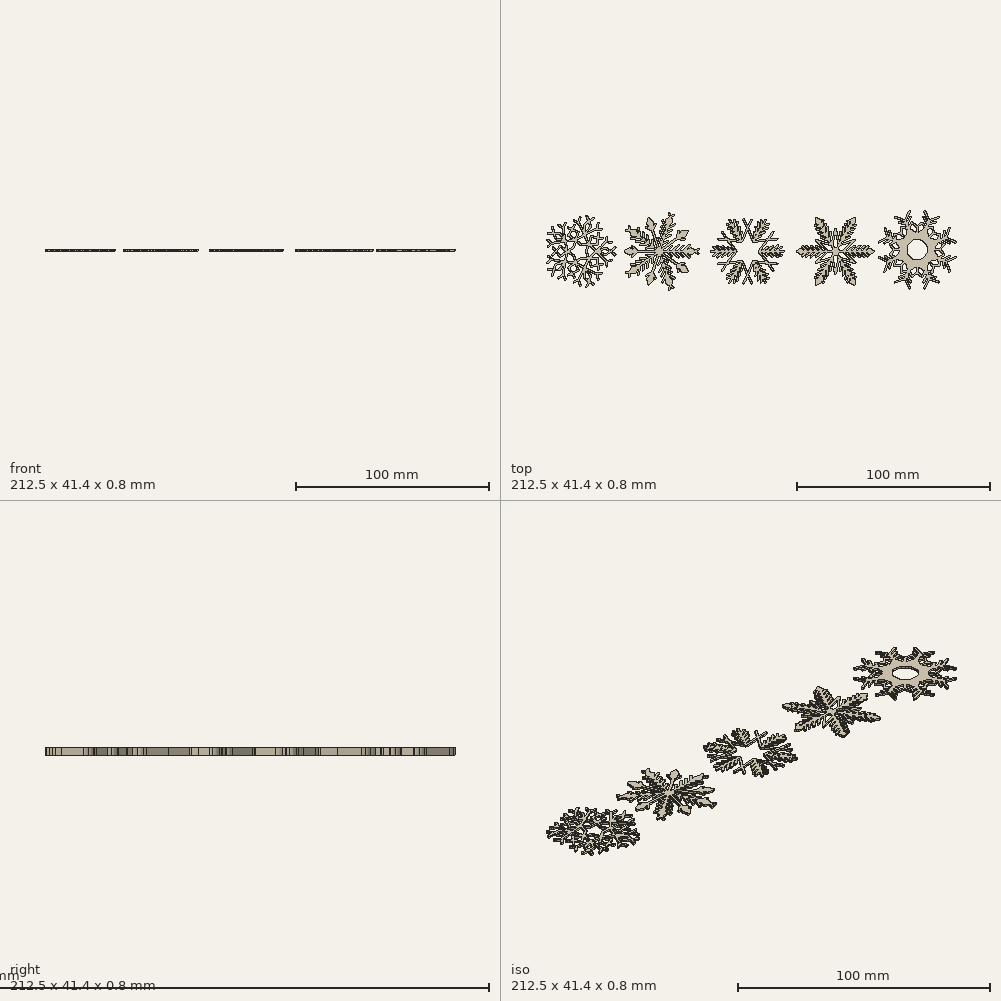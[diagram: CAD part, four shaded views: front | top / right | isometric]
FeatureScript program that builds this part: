
annotation { "Feature Type Name" : "Feature", "Feature Type Description" : "" }
export const myFeature = defineFeature(function(context is Context, id is Id, definition is map)
    precondition{}
    {
        {
            var Q0;
            Q0=qCreatedBy(makeId("Top.planeOp"),FACE);
            var sketch = newSketch(context, id + "F0", { "sketchPlane" : qUnion([Q0])});
            skFitSpline(sketch, "E0", {"points": [v(111.87, -6.39) * mm, v(111.5, -7.63) * mm, v(111.28, -8.86) * mm, v(111.02, -10.1) * mm]});
            skFitSpline(sketch, "E1", {"points": [v(111.02, -10.1) * mm, v(111.8, -10.32) * mm, v(112.58, -10.54) * mm, v(113.38, -10.77) * mm]});
            skFitSpline(sketch, "E2", {"points": [v(113.38, -10.77) * mm, v(113.4, -10.65) * mm, v(113.42, -10.54) * mm, v(113.43, -10.43) * mm]});
            skFitSpline(sketch, "E3", {"points": [v(113.43, -10.43) * mm, v(113.52, -9.82) * mm, v(113.59, -9.2) * mm, v(113.69, -8.59) * mm]});
            skFitSpline(sketch, "E4", {"points": [v(113.69, -8.59) * mm, v(113.72, -8.4) * mm, v(113.68, -8.28) * mm, v(113.58, -8.15) * mm]});
            skFitSpline(sketch, "E5", {"points": [v(113.58, -8.15) * mm, v(113.52, -8.08) * mm, v(113.46, -8.01) * mm, v(113.4, -7.95) * mm]});
            skFitSpline(sketch, "E6", {"points": [v(113.4, -7.95) * mm, v(113.06, -7.6) * mm, v(112.71, -7.24) * mm, v(112.37, -6.89) * mm]});
            skFitSpline(sketch, "E7", {"points": [v(112.37, -6.89) * mm, v(112.21, -6.73) * mm, v(112.05, -6.57) * mm, v(111.87, -6.39) * mm]});
            skFitSpline(sketch, "E8", {"points": [v(95.38, 5.54) * mm, v(96.61, 5.8) * mm, v(97.85, 6.01) * mm, v(99.08, 6.39) * mm]});
            skFitSpline(sketch, "E9", {"points": [v(99.08, 6.39) * mm, v(99.03, 6.44) * mm, v(99, 6.48) * mm, v(98.97, 6.51) * mm]});
            skFitSpline(sketch, "E10", {"points": [v(98.97, 6.51) * mm, v(98.46, 7.01) * mm, v(97.95, 7.52) * mm, v(97.43, 8.02) * mm]});
            skFitSpline(sketch, "E11", {"points": [v(97.43, 8.02) * mm, v(97.36, 8.08) * mm, v(97.28, 8.14) * mm, v(97.2, 8.18) * mm]});
            skFitSpline(sketch, "E12", {"points": [v(97.2, 8.18) * mm, v(97.13, 8.21) * mm, v(97.04, 8.22) * mm, v(96.97, 8.22) * mm]});
            skFitSpline(sketch, "E13", {"points": [v(96.97, 8.22) * mm, v(96.44, 8.15) * mm, v(95.92, 8.08) * mm, v(95.39, 8) * mm]});
            skFitSpline(sketch, "E14", {"points": [v(95.39, 8) * mm, v(95.16, 7.97) * mm, v(94.94, 7.93) * mm, v(94.7, 7.9) * mm]});
            skFitSpline(sketch, "E15", {"points": [v(94.7, 7.9) * mm, v(94.94, 7.1) * mm, v(95.16, 6.33) * mm, v(95.38, 5.54) * mm]});
            skFitSpline(sketch, "E16", {"points": [v(112.6, -5.66) * mm, v(112.68, -5.74) * mm, v(112.73, -5.8) * mm, v(112.79, -5.86) * mm]});
            skFitSpline(sketch, "E17", {"points": [v(112.79, -5.86) * mm, v(113.27, -6.32) * mm, v(113.75, -6.8) * mm, v(114.23, -7.26) * mm]});
            skFitSpline(sketch, "E18", {"points": [v(114.23, -7.26) * mm, v(114.27, -7.3) * mm, v(114.3, -7.34) * mm, v(114.35, -7.37) * mm]});
            skFitSpline(sketch, "E19", {"points": [v(114.35, -7.37) * mm, v(114.48, -7.47) * mm, v(114.63, -7.51) * mm, v(114.8, -7.49) * mm]});
            skFitSpline(sketch, "E20", {"points": [v(114.8, -7.49) * mm, v(115.46, -7.39) * mm, v(116.12, -7.3) * mm, v(116.78, -7.2) * mm]});
            skFitSpline(sketch, "E21", {"points": [v(116.78, -7.2) * mm, v(116.85, -7.2) * mm, v(116.92, -7.18) * mm, v(116.98, -7.16) * mm]});
            skFitSpline(sketch, "E22", {"points": [v(116.98, -7.16) * mm, v(116.75, -6.36) * mm, v(116.52, -5.58) * mm, v(116.3, -4.8) * mm]});
            skFitSpline(sketch, "E23", {"points": [v(116.3, -4.8) * mm, v(115.07, -5.08) * mm, v(113.84, -5.28) * mm, v(112.6, -5.66) * mm]});
            skFitSpline(sketch, "E24", {"points": [v(98.3, 11.5) * mm, v(98.3, 11.42) * mm, v(98.28, 11.35) * mm, v(98.27, 11.28) * mm]});
            skFitSpline(sketch, "E25", {"points": [v(98.27, 11.28) * mm, v(98.18, 10.65) * mm, v(98.1, 10.01) * mm, v(98, 9.39) * mm]});
            skFitSpline(sketch, "E26", {"points": [v(98, 9.39) * mm, v(97.96, 9.14) * mm, v(98.02, 8.95) * mm, v(98.19, 8.78) * mm]});
            skFitSpline(sketch, "E27", {"points": [v(98.19, 8.78) * mm, v(98.7, 8.26) * mm, v(99.2, 7.74) * mm, v(99.71, 7.22) * mm]});
            skFitSpline(sketch, "E28", {"points": [v(99.71, 7.22) * mm, v(99.74, 7.2) * mm, v(99.78, 7.18) * mm, v(99.82, 7.15) * mm]});
            skFitSpline(sketch, "E29", {"points": [v(99.82, 7.15) * mm, v(100.2, 8.37) * mm, v(100.4, 9.6) * mm, v(100.67, 10.82) * mm]});
            skFitSpline(sketch, "E30", {"points": [v(100.67, 10.82) * mm, v(99.88, 11.05) * mm, v(99.11, 11.27) * mm, v(98.3, 11.5) * mm]});
            skFitSpline(sketch, "E31", {"points": [v(99.83, -6.44) * mm, v(99.73, -6.42) * mm, v(99.7, -6.51) * mm, v(99.64, -6.56) * mm]});
            skFitSpline(sketch, "E32", {"points": [v(99.64, -6.56) * mm, v(99.17, -7.05) * mm, v(98.7, -7.53) * mm, v(98.22, -8.02) * mm]});
            skFitSpline(sketch, "E33", {"points": [v(98.22, -8.02) * mm, v(98.18, -8.06) * mm, v(98.13, -8.11) * mm, v(98.1, -8.16) * mm]});
            skFitSpline(sketch, "E34", {"points": [v(98.1, -8.16) * mm, v(98, -8.29) * mm, v(97.97, -8.42) * mm, v(98, -8.59) * mm]});
            skFitSpline(sketch, "E35", {"points": [v(98, -8.59) * mm, v(98.1, -9.26) * mm, v(98.18, -9.93) * mm, v(98.27, -10.6) * mm]});
            skFitSpline(sketch, "E36", {"points": [v(98.27, -10.6) * mm, v(98.28, -10.65) * mm, v(98.3, -10.71) * mm, v(98.32, -10.77) * mm]});
            skFitSpline(sketch, "E37", {"points": [v(98.32, -10.77) * mm, v(99.11, -10.54) * mm, v(99.89, -10.32) * mm, v(100.67, -10.1) * mm]});
            skFitSpline(sketch, "E38", {"points": [v(100.67, -10.1) * mm, v(100.4, -8.87) * mm, v(100.2, -7.64) * mm, v(99.83, -6.44) * mm]});
            skFitSpline(sketch, "E39", {"points": [v(99.08, -5.66) * mm, v(97.84, -5.28) * mm, v(96.6, -5.08) * mm, v(95.38, -4.81) * mm]});
            skFitSpline(sketch, "E40", {"points": [v(95.38, -4.81) * mm, v(95.15, -5.6) * mm, v(94.93, -6.38) * mm, v(94.7, -7.17) * mm]});
            skFitSpline(sketch, "E41", {"points": [v(94.7, -7.17) * mm, v(94.76, -7.18) * mm, v(94.8, -7.2) * mm, v(94.84, -7.2) * mm]});
            skFitSpline(sketch, "E42", {"points": [v(94.84, -7.2) * mm, v(95.53, -7.3) * mm, v(96.23, -7.39) * mm, v(96.92, -7.49) * mm]});
            skFitSpline(sketch, "E43", {"points": [v(96.92, -7.49) * mm, v(97.05, -7.5) * mm, v(97.17, -7.5) * mm, v(97.28, -7.4) * mm]});
            skFitSpline(sketch, "E44", {"points": [v(97.28, -7.4) * mm, v(97.37, -7.34) * mm, v(97.45, -7.27) * mm, v(97.53, -7.19) * mm]});
            skFitSpline(sketch, "E45", {"points": [v(97.53, -7.19) * mm, v(97.89, -6.85) * mm, v(98.24, -6.5) * mm, v(98.6, -6.16) * mm]});
            skFitSpline(sketch, "E46", {"points": [v(98.6, -6.16) * mm, v(98.75, -6) * mm, v(98.9, -5.84) * mm, v(99.08, -5.66) * mm]});
            skFitSpline(sketch, "E47", {"points": [v(116.9, 4.1) * mm, v(116.77, 3.91) * mm, v(116.65, 3.73) * mm, v(116.54, 3.54) * mm]});
            skFitSpline(sketch, "E48", {"points": [v(116.54, 3.54) * mm, v(116.02, 2.73) * mm, v(115.51, 1.92) * mm, v(115, 1.11) * mm]});
            skFitSpline(sketch, "E49", {"points": [v(115, 1.11) * mm, v(114.96, 1.04) * mm, v(114.93, 0.96) * mm, v(114.87, 0.85) * mm]});
            skFitSpline(sketch, "E50", {"points": [v(114.87, 0.85) * mm, v(115.26, 0.87) * mm, v(115.59, 0.89) * mm, v(115.92, 0.9) * mm]});
            skFitSpline(sketch, "E51", {"points": [v(115.92, 0.9) * mm, v(116.35, 0.9) * mm, v(116.77, 0.9) * mm, v(117.2, 0.9) * mm]});
            skFitSpline(sketch, "E52", {"points": [v(117.2, 0.9) * mm, v(117.36, 0.9) * mm, v(117.54, 0.91) * mm, v(117.66, 1.07) * mm]});
            skFitSpline(sketch, "E53", {"points": [v(117.66, 1.07) * mm, v(118.08, 1.63) * mm, v(118.5, 2.18) * mm, v(118.92, 2.73) * mm]});
            skFitSpline(sketch, "E54", {"points": [v(118.92, 2.73) * mm, v(118.96, 2.8) * mm, v(119, 2.86) * mm, v(119.04, 2.91) * mm]});
            skFitSpline(sketch, "E55", {"points": [v(119.04, 2.91) * mm, v(118.31, 3.32) * mm, v(117.61, 3.7) * mm, v(116.9, 4.1) * mm]});
            skFitSpline(sketch, "E56", {"points": [v(112.6, 6.4) * mm, v(113.83, 6.01) * mm, v(115.07, 5.8) * mm, v(116.3, 5.54) * mm]});
            skFitSpline(sketch, "E57", {"points": [v(116.3, 5.54) * mm, v(116.53, 6.33) * mm, v(116.75, 7.1) * mm, v(116.98, 7.9) * mm]});
            skFitSpline(sketch, "E58", {"points": [v(116.98, 7.9) * mm, v(116.87, 7.92) * mm, v(116.76, 7.94) * mm, v(116.65, 7.95) * mm]});
            skFitSpline(sketch, "E59", {"points": [v(116.65, 7.95) * mm, v(116.04, 8.04) * mm, v(115.42, 8.1) * mm, v(114.8, 8.2) * mm]});
            skFitSpline(sketch, "E60", {"points": [v(114.8, 8.2) * mm, v(114.6, 8.25) * mm, v(114.45, 8.18) * mm, v(114.3, 8.06) * mm]});
            skFitSpline(sketch, "E61", {"points": [v(114.3, 8.06) * mm, v(114.25, 8.01) * mm, v(114.2, 7.95) * mm, v(114.13, 7.9) * mm]});
            skFitSpline(sketch, "E62", {"points": [v(114.13, 7.9) * mm, v(113.79, 7.57) * mm, v(113.45, 7.23) * mm, v(113.1, 6.9) * mm]});
            skFitSpline(sketch, "E63", {"points": [v(113.1, 6.9) * mm, v(112.94, 6.74) * mm, v(112.78, 6.57) * mm, v(112.6, 6.4) * mm]});
            skFitSpline(sketch, "E64", {"points": [v(111.88, 7.14) * mm, v(111.92, 7.18) * mm, v(111.97, 7.21) * mm, v(112, 7.25) * mm]});
            skFitSpline(sketch, "E65", {"points": [v(112, 7.25) * mm, v(112.5, 7.75) * mm, v(112.99, 8.25) * mm, v(113.48, 8.76) * mm]});
            skFitSpline(sketch, "E66", {"points": [v(113.48, 8.76) * mm, v(113.55, 8.84) * mm, v(113.61, 8.93) * mm, v(113.67, 9.03) * mm]});
            skFitSpline(sketch, "E67", {"points": [v(113.67, 9.03) * mm, v(113.7, 9.07) * mm, v(113.71, 9.14) * mm, v(113.7, 9.19) * mm]});
            skFitSpline(sketch, "E68", {"points": [v(113.7, 9.19) * mm, v(113.7, 9.34) * mm, v(113.67, 9.49) * mm, v(113.65, 9.64) * mm]});
            skFitSpline(sketch, "E69", {"points": [v(113.65, 9.64) * mm, v(113.6, 10.05) * mm, v(113.54, 10.46) * mm, v(113.48, 10.87) * mm]});
            skFitSpline(sketch, "E70", {"points": [v(113.48, 10.87) * mm, v(113.45, 11.08) * mm, v(113.41, 11.29) * mm, v(113.38, 11.5) * mm]});
            skFitSpline(sketch, "E71", {"points": [v(113.38, 11.5) * mm, v(112.58, 11.27) * mm, v(111.8, 11.05) * mm, v(111.02, 10.82) * mm]});
            skFitSpline(sketch, "E72", {"points": [v(111.02, 10.82) * mm, v(111.1, 10.13) * mm, v(111.7, 7.54) * mm, v(111.88, 7.14) * mm]});
            skFitSpline(sketch, "E73", {"points": [v(106.33, 9.42) * mm, v(106.73, 9.56) * mm, v(109.14, 11.06) * mm, v(109.57, 11.43) * mm]});
            skFitSpline(sketch, "E74", {"points": [v(109.57, 11.43) * mm, v(109.18, 12.14) * mm, v(108.8, 12.84) * mm, v(108.4, 13.55) * mm]});
            skFitSpline(sketch, "E75", {"points": [v(108.4, 13.55) * mm, v(108.37, 13.54) * mm, v(108.35, 13.54) * mm, v(108.33, 13.52) * mm]});
            skFitSpline(sketch, "E76", {"points": [v(108.33, 13.52) * mm, v(107.72, 13.07) * mm, v(107.12, 12.61) * mm, v(106.52, 12.15) * mm]});
            skFitSpline(sketch, "E77", {"points": [v(106.52, 12.15) * mm, v(106.48, 12.12) * mm, v(106.44, 12.07) * mm, v(106.43, 12.02) * mm]});
            skFitSpline(sketch, "E78", {"points": [v(106.43, 12.02) * mm, v(106.4, 11.86) * mm, v(106.38, 11.7) * mm, v(106.38, 11.55) * mm]});
            skFitSpline(sketch, "E79", {"points": [v(106.38, 11.55) * mm, v(106.37, 11.15) * mm, v(106.38, 10.75) * mm, v(106.37, 10.35) * mm]});
            skFitSpline(sketch, "E80", {"points": [v(106.37, 10.35) * mm, v(106.37, 10.05) * mm, v(106.34, 9.75) * mm, v(106.33, 9.42) * mm]});
            skFitSpline(sketch, "E81", {"points": [v(106.34, -8.67) * mm, v(106.34, -8.8) * mm, v(106.34, -8.87) * mm, v(106.34, -8.95) * mm]});
            skFitSpline(sketch, "E82", {"points": [v(106.34, -8.95) * mm, v(106.35, -9.6) * mm, v(106.36, -10.27) * mm, v(106.37, -10.93) * mm]});
            skFitSpline(sketch, "E83", {"points": [v(106.37, -10.93) * mm, v(106.37, -10.96) * mm, v(106.37, -10.98) * mm, v(106.38, -11) * mm]});
            skFitSpline(sketch, "E84", {"points": [v(106.38, -11) * mm, v(106.39, -11.22) * mm, v(106.45, -11.4) * mm, v(106.64, -11.53) * mm]});
            skFitSpline(sketch, "E85", {"points": [v(106.64, -11.53) * mm, v(107.07, -11.83) * mm, v(107.47, -12.15) * mm, v(107.88, -12.47) * mm]});
            skFitSpline(sketch, "E86", {"points": [v(107.88, -12.47) * mm, v(108.05, -12.6) * mm, v(108.21, -12.71) * mm, v(108.39, -12.84) * mm]});
            skFitSpline(sketch, "E87", {"points": [v(108.39, -12.84) * mm, v(108.8, -12.1) * mm, v(109.19, -11.4) * mm, v(109.58, -10.69) * mm]});
            skFitSpline(sketch, "E88", {"points": [v(109.58, -10.69) * mm, v(108.52, -10.01) * mm, v(107.5, -9.28) * mm, v(106.34, -8.67) * mm]});
            skFitSpline(sketch, "E89", {"points": [v(94.79, 4.1) * mm, v(94.06, 3.7) * mm, v(93.36, 3.3) * mm, v(92.65, 2.91) * mm]});
            skFitSpline(sketch, "E90", {"points": [v(92.65, 2.91) * mm, v(92.68, 2.86) * mm, v(92.7, 2.83) * mm, v(92.72, 2.8) * mm]});
            skFitSpline(sketch, "E91", {"points": [v(92.72, 2.8) * mm, v(93.16, 2.22) * mm, v(93.6, 1.64) * mm, v(94.04, 1.06) * mm]});
            skFitSpline(sketch, "E92", {"points": [v(94.04, 1.06) * mm, v(94.08, 1) * mm, v(94.15, 0.96) * mm, v(94.21, 0.95) * mm]});
            skFitSpline(sketch, "E93", {"points": [v(94.21, 0.95) * mm, v(94.35, 0.92) * mm, v(94.5, 0.9) * mm, v(94.63, 0.9) * mm]});
            skFitSpline(sketch, "E94", {"points": [v(94.63, 0.9) * mm, v(95.13, 0.88) * mm, v(95.62, 0.87) * mm, v(96.12, 0.86) * mm]});
            skFitSpline(sketch, "E95", {"points": [v(96.12, 0.86) * mm, v(96.34, 0.86) * mm, v(96.56, 0.86) * mm, v(96.8, 0.86) * mm]});
            skFitSpline(sketch, "E96", {"points": [v(96.8, 0.86) * mm, v(96.2, 2.02) * mm, v(95.47, 3.03) * mm, v(94.79, 4.1) * mm]});
            skFitSpline(sketch, "E97", {"points": [v(119.04, -2.18) * mm, v(118.98, -2.09) * mm, v(118.92, -2) * mm, v(118.86, -1.92) * mm]});
            skFitSpline(sketch, "E98", {"points": [v(118.86, -1.92) * mm, v(118.49, -1.43) * mm, v(118.1, -0.95) * mm, v(117.75, -0.45) * mm]});
            skFitSpline(sketch, "E99", {"points": [v(117.75, -0.45) * mm, v(117.6, -0.24) * mm, v(117.42, -0.19) * mm, v(117.2, -0.16) * mm]});
            skFitSpline(sketch, "E100", {"points": [v(117.2, -0.16) * mm, v(117.15, -0.15) * mm, v(117.1, -0.16) * mm, v(117.03, -0.16) * mm]});
            skFitSpline(sketch, "E101", {"points": [v(117.03, -0.16) * mm, v(116.55, -0.15) * mm, v(116.06, -0.15) * mm, v(115.57, -0.14) * mm]});
            skFitSpline(sketch, "E102", {"points": [v(115.57, -0.14) * mm, v(115.35, -0.14) * mm, v(115.13, -0.14) * mm, v(114.88, -0.14) * mm]});
            skFitSpline(sketch, "E103", {"points": [v(114.88, -0.14) * mm, v(115.49, -1.3) * mm, v(116.22, -2.32) * mm, v(116.9, -3.37) * mm]});
            skFitSpline(sketch, "E104", {"points": [v(116.9, -3.37) * mm, v(117.62, -2.97) * mm, v(118.32, -2.58) * mm, v(119.04, -2.18) * mm]});
            skFitSpline(sketch, "E105", {"points": [v(105.34, 9.42) * mm, v(105.34, 9.52) * mm, v(105.34, 9.6) * mm, v(105.34, 9.68) * mm]});
            skFitSpline(sketch, "E106", {"points": [v(105.34, 9.68) * mm, v(105.33, 10.29) * mm, v(105.32, 10.9) * mm, v(105.32, 11.5) * mm]});
            skFitSpline(sketch, "E107", {"points": [v(105.32, 11.5) * mm, v(105.32, 11.56) * mm, v(105.32, 11.61) * mm, v(105.32, 11.67) * mm]});
            skFitSpline(sketch, "E108", {"points": [v(105.32, 11.67) * mm, v(105.3, 11.91) * mm, v(105.25, 12.12) * mm, v(105.02, 12.28) * mm]});
            skFitSpline(sketch, "E109", {"points": [v(105.02, 12.28) * mm, v(104.58, 12.58) * mm, v(104.16, 12.92) * mm, v(103.74, 13.24) * mm]});
            skFitSpline(sketch, "E110", {"points": [v(103.74, 13.24) * mm, v(103.6, 13.35) * mm, v(103.44, 13.46) * mm, v(103.3, 13.57) * mm]});
            skFitSpline(sketch, "E111", {"points": [v(103.3, 13.57) * mm, v(102.9, 12.84) * mm, v(102.5, 12.14) * mm, v(102.11, 11.43) * mm]});
            skFitSpline(sketch, "E112", {"points": [v(102.11, 11.43) * mm, v(102.57, 11.05) * mm, v(104.9, 9.6) * mm, v(105.34, 9.42) * mm]});
            skFitSpline(sketch, "E113", {"points": [v(105.34, -8.7) * mm, v(104.9, -8.86) * mm, v(102.73, -10.22) * mm, v(102.1, -10.7) * mm]});
            skFitSpline(sketch, "E114", {"points": [v(102.1, -10.7) * mm, v(102.5, -11.4) * mm, v(102.9, -12.11) * mm, v(103.3, -12.84) * mm]});
            skFitSpline(sketch, "E115", {"points": [v(103.3, -12.84) * mm, v(103.38, -12.78) * mm, v(103.47, -12.72) * mm, v(103.55, -12.66) * mm]});
            skFitSpline(sketch, "E116", {"points": [v(103.55, -12.66) * mm, v(104.04, -12.28) * mm, v(104.53, -11.9) * mm, v(105.04, -11.53) * mm]});
            skFitSpline(sketch, "E117", {"points": [v(105.04, -11.53) * mm, v(105.2, -11.42) * mm, v(105.28, -11.3) * mm, v(105.3, -11.1) * mm]});
            skFitSpline(sketch, "E118", {"points": [v(105.3, -11.1) * mm, v(105.3, -11.03) * mm, v(105.32, -10.96) * mm, v(105.32, -10.9) * mm]});
            skFitSpline(sketch, "E119", {"points": [v(105.32, -10.9) * mm, v(105.33, -10.37) * mm, v(105.33, -9.85) * mm, v(105.34, -9.34) * mm]});
            skFitSpline(sketch, "E120", {"points": [v(105.34, -9.34) * mm, v(105.34, -9.13) * mm, v(105.34, -8.92) * mm, v(105.34, -8.7) * mm]});
            skFitSpline(sketch, "E121", {"points": [v(94.78, -3.37) * mm, v(95.2, -2.86) * mm, v(96.68, -0.48) * mm, v(96.77, -0.14) * mm]});
            skFitSpline(sketch, "E122", {"points": [v(96.77, -0.14) * mm, v(96.69, -0.14) * mm, v(96.61, -0.14) * mm, v(96.53, -0.14) * mm]});
            skFitSpline(sketch, "E123", {"points": [v(96.53, -0.14) * mm, v(96.03, -0.15) * mm, v(95.53, -0.15) * mm, v(95.02, -0.16) * mm]});
            skFitSpline(sketch, "E124", {"points": [v(95.02, -0.16) * mm, v(94.86, -0.16) * mm, v(94.69, -0.15) * mm, v(94.52, -0.16) * mm]});
            skFitSpline(sketch, "E125", {"points": [v(94.52, -0.16) * mm, v(94.29, -0.18) * mm, v(94.09, -0.23) * mm, v(93.93, -0.46) * mm]});
            skFitSpline(sketch, "E126", {"points": [v(93.93, -0.46) * mm, v(93.64, -0.89) * mm, v(93.3, -1.3) * mm, v(92.98, -1.72) * mm]});
            skFitSpline(sketch, "E127", {"points": [v(92.98, -1.72) * mm, v(92.87, -1.87) * mm, v(92.76, -2.02) * mm, v(92.64, -2.18) * mm]});
            skFitSpline(sketch, "E128", {"points": [v(92.64, -2.18) * mm, v(93.36, -2.58) * mm, v(94.07, -2.98) * mm, v(94.78, -3.37) * mm]});
            skFitSpline(sketch, "E129", {"points": [v(100.7, 0.34) * mm, v(100.72, -0.1) * mm, v(100.75, -0.58) * mm, v(100.76, -1.06) * mm]});
            skFitSpline(sketch, "E130", {"points": [v(100.76, -1.06) * mm, v(100.76, -1.49) * mm, v(100.91, -1.86) * mm, v(101.18, -2.18) * mm]});
            skFitSpline(sketch, "E131", {"points": [v(101.18, -2.18) * mm, v(101.46, -2.5) * mm, v(101.75, -2.8) * mm, v(102.05, -3.1) * mm]});
            skFitSpline(sketch, "E132", {"points": [v(102.05, -3.1) * mm, v(102.45, -3.5) * mm, v(102.86, -3.9) * mm, v(103.28, -4.28) * mm]});
            skFitSpline(sketch, "E133", {"points": [v(103.28, -4.28) * mm, v(103.56, -4.53) * mm, v(103.9, -4.7) * mm, v(104.27, -4.71) * mm]});
            skFitSpline(sketch, "E134", {"points": [v(104.27, -4.71) * mm, v(104.77, -4.74) * mm, v(105.28, -4.76) * mm, v(105.78, -4.76) * mm]});
            skFitSpline(sketch, "E135", {"points": [v(105.78, -4.76) * mm, v(106.27, -4.76) * mm, v(106.77, -4.72) * mm, v(107.26, -4.72) * mm]});
            skFitSpline(sketch, "E136", {"points": [v(107.26, -4.72) * mm, v(107.7, -4.72) * mm, v(108.08, -4.56) * mm, v(108.4, -4.28) * mm]});
            skFitSpline(sketch, "E137", {"points": [v(108.4, -4.28) * mm, v(108.75, -3.97) * mm, v(109.09, -3.64) * mm, v(109.42, -3.31) * mm]});
            skFitSpline(sketch, "E138", {"points": [v(109.42, -3.31) * mm, v(109.78, -2.95) * mm, v(110.14, -2.58) * mm, v(110.48, -2.2) * mm]});
            skFitSpline(sketch, "E139", {"points": [v(110.48, -2.2) * mm, v(110.74, -1.92) * mm, v(110.9, -1.57) * mm, v(110.93, -1.19) * mm]});
            skFitSpline(sketch, "E140", {"points": [v(110.93, -1.19) * mm, v(110.96, -0.77) * mm, v(110.98, -0.34) * mm, v(110.98, 0.08) * mm]});
            skFitSpline(sketch, "E141", {"points": [v(110.98, 0.08) * mm, v(110.97, 0.64) * mm, v(110.95, 1.2) * mm, v(110.93, 1.78) * mm]});
            skFitSpline(sketch, "E142", {"points": [v(110.93, 1.78) * mm, v(110.92, 2.2) * mm, v(110.78, 2.6) * mm, v(110.5, 2.91) * mm]});
            skFitSpline(sketch, "E143", {"points": [v(110.5, 2.91) * mm, v(110.19, 3.26) * mm, v(109.87, 3.6) * mm, v(109.54, 3.92) * mm]});
            skFitSpline(sketch, "E144", {"points": [v(109.54, 3.92) * mm, v(109.17, 4.29) * mm, v(108.8, 4.65) * mm, v(108.41, 5) * mm]});
            skFitSpline(sketch, "E145", {"points": [v(108.41, 5) * mm, v(108.13, 5.26) * mm, v(107.78, 5.41) * mm, v(107.4, 5.45) * mm]});
            skFitSpline(sketch, "E146", {"points": [v(107.4, 5.45) * mm, v(107, 5.49) * mm, v(106.57, 5.5) * mm, v(106.16, 5.5) * mm]});
            skFitSpline(sketch, "E147", {"points": [v(106.16, 5.5) * mm, v(105.6, 5.5) * mm, v(105.03, 5.46) * mm, v(104.46, 5.46) * mm]});
            skFitSpline(sketch, "E148", {"points": [v(104.46, 5.46) * mm, v(104.02, 5.45) * mm, v(103.63, 5.3) * mm, v(103.3, 5.02) * mm]});
            skFitSpline(sketch, "E149", {"points": [v(103.3, 5.02) * mm, v(102.97, 4.73) * mm, v(102.65, 4.43) * mm, v(102.34, 4.12) * mm]});
            skFitSpline(sketch, "E150", {"points": [v(102.34, 4.12) * mm, v(101.96, 3.73) * mm, v(101.58, 3.34) * mm, v(101.21, 2.94) * mm]});
            skFitSpline(sketch, "E151", {"points": [v(101.21, 2.94) * mm, v(100.95, 2.66) * mm, v(100.79, 2.32) * mm, v(100.77, 1.93) * mm]});
            skFitSpline(sketch, "E152", {"points": [v(100.77, 1.93) * mm, v(100.73, 1.41) * mm, v(100.72, 0.9) * mm, v(100.7, 0.34) * mm]});
            skFitSpline(sketch, "E153", {"points": [v(99.2, -13.61) * mm, v(98.76, -13.75) * mm, v(98.37, -13.87) * mm, v(97.98, -13.99) * mm]});
            skFitSpline(sketch, "E154", {"points": [v(97.98, -13.99) * mm, v(97.52, -14.12) * mm, v(97.06, -14.25) * mm, v(96.6, -14.37) * mm]});
            skFitSpline(sketch, "E155", {"points": [v(96.6, -14.37) * mm, v(96.3, -14.45) * mm, v(96.06, -14.32) * mm, v(95.97, -14.07) * mm]});
            skFitSpline(sketch, "E156", {"points": [v(95.97, -14.07) * mm, v(95.87, -13.8) * mm, v(96.02, -13.52) * mm, v(96.34, -13.43) * mm]});
            skFitSpline(sketch, "E157", {"points": [v(96.34, -13.43) * mm, v(96.65, -13.34) * mm, v(96.97, -13.27) * mm, v(97.28, -13.17) * mm]});
            skFitSpline(sketch, "E158", {"points": [v(97.28, -13.17) * mm, v(97.8, -13.02) * mm, v(98.32, -12.86) * mm, v(98.84, -12.71) * mm]});
            skFitSpline(sketch, "E159", {"points": [v(98.84, -12.71) * mm, v(99.08, -12.64) * mm, v(99.33, -12.6) * mm, v(99.57, -12.54) * mm]});
            skFitSpline(sketch, "E160", {"points": [v(99.57, -12.54) * mm, v(99.63, -12.52) * mm, v(99.7, -12.48) * mm, v(99.73, -12.43) * mm]});
            skFitSpline(sketch, "E161", {"points": [v(99.73, -12.43) * mm, v(99.9, -12.1) * mm, v(100.04, -11.77) * mm, v(100.2, -11.4) * mm]});
            skFitSpline(sketch, "E162", {"points": [v(100.2, -11.4) * mm, v(100.12, -11.42) * mm, v(100.07, -11.42) * mm, v(100.03, -11.43) * mm]});
            skFitSpline(sketch, "E163", {"points": [v(100.03, -11.43) * mm, v(99.67, -11.5) * mm, v(99.32, -11.62) * mm, v(98.95, -11.64) * mm]});
            skFitSpline(sketch, "E164", {"points": [v(98.95, -11.64) * mm, v(98.7, -11.66) * mm, v(98.47, -11.76) * mm, v(98.24, -11.84) * mm]});
            skFitSpline(sketch, "E165", {"points": [v(98.24, -11.84) * mm, v(97.8, -11.98) * mm, v(97.42, -11.65) * mm, v(97.37, -11.23) * mm]});
            skFitSpline(sketch, "E166", {"points": [v(97.37, -11.23) * mm, v(97.3, -10.57) * mm, v(97.18, -9.92) * mm, v(97.1, -9.27) * mm]});
            skFitSpline(sketch, "E167", {"points": [v(97.1, -9.27) * mm, v(97.06, -9.01) * mm, v(97.04, -8.76) * mm, v(97.01, -8.49) * mm]});
            skFitSpline(sketch, "E168", {"points": [v(97.01, -8.49) * mm, v(96.86, -8.46) * mm, v(96.72, -8.43) * mm, v(96.58, -8.41) * mm]});
            skFitSpline(sketch, "E169", {"points": [v(96.58, -8.41) * mm, v(96.03, -8.34) * mm, v(95.48, -8.27) * mm, v(94.92, -8.2) * mm]});
            skFitSpline(sketch, "E170", {"points": [v(94.92, -8.2) * mm, v(94.71, -8.17) * mm, v(94.5, -8.12) * mm, v(94.28, -8.11) * mm]});
            skFitSpline(sketch, "E171", {"points": [v(94.28, -8.11) * mm, v(93.83, -8.1) * mm, v(93.49, -7.67) * mm, v(93.65, -7.23) * mm]});
            skFitSpline(sketch, "E172", {"points": [v(93.65, -7.23) * mm, v(93.7, -7.05) * mm, v(93.75, -6.86) * mm, v(93.8, -6.68) * mm]});
            skFitSpline(sketch, "E173", {"points": [v(93.8, -6.68) * mm, v(93.8, -6.67) * mm, v(93.81, -6.65) * mm, v(93.81, -6.63) * mm]});
            skFitSpline(sketch, "E174", {"points": [v(93.81, -6.63) * mm, v(93.9, -6.2) * mm, v(93.97, -5.76) * mm, v(94.06, -5.28) * mm]});
            skFitSpline(sketch, "E175", {"points": [v(94.06, -5.28) * mm, v(93.8, -5.4) * mm, v(93.58, -5.51) * mm, v(93.33, -5.6) * mm]});
            skFitSpline(sketch, "E176", {"points": [v(93.33, -5.6) * mm, v(93.06, -5.7) * mm, v(92.92, -5.85) * mm, v(92.88, -6.16) * mm]});
            skFitSpline(sketch, "E177", {"points": [v(92.88, -6.16) * mm, v(92.84, -6.49) * mm, v(92.72, -6.8) * mm, v(92.63, -7.13) * mm]});
            skFitSpline(sketch, "E178", {"points": [v(92.63, -7.13) * mm, v(92.44, -7.79) * mm, v(92.24, -8.45) * mm, v(92.06, -9.1) * mm]});
            skFitSpline(sketch, "E179", {"points": [v(92.06, -9.1) * mm, v(91.96, -9.45) * mm, v(91.7, -9.61) * mm, v(91.42, -9.51) * mm]});
            skFitSpline(sketch, "E180", {"points": [v(91.42, -9.51) * mm, v(91.21, -9.44) * mm, v(91.08, -9.26) * mm, v(91.09, -9.03) * mm]});
            skFitSpline(sketch, "E181", {"points": [v(91.09, -9.03) * mm, v(91.1, -8.94) * mm, v(91.1, -8.84) * mm, v(91.14, -8.75) * mm]});
            skFitSpline(sketch, "E182", {"points": [v(91.14, -8.75) * mm, v(91.33, -8.08) * mm, v(91.53, -7.4) * mm, v(91.73, -6.73) * mm]});
            skFitSpline(sketch, "E183", {"points": [v(91.73, -6.73) * mm, v(91.77, -6.6) * mm, v(91.8, -6.46) * mm, v(91.86, -6.27) * mm]});
            skFitSpline(sketch, "E184", {"points": [v(91.86, -6.27) * mm, v(91.6, -6.36) * mm, v(91.4, -6.43) * mm, v(91.2, -6.51) * mm]});
            skFitSpline(sketch, "E185", {"points": [v(91.2, -6.51) * mm, v(91.13, -6.54) * mm, v(91.08, -6.62) * mm, v(91.05, -6.69) * mm]});
            skFitSpline(sketch, "E186", {"points": [v(91.05, -6.69) * mm, v(90.6, -7.95) * mm, v(90.15, -9.21) * mm, v(89.7, -10.48) * mm]});
            skFitSpline(sketch, "E187", {"points": [v(89.7, -10.48) * mm, v(89.66, -10.6) * mm, v(89.64, -10.74) * mm, v(89.63, -10.88) * mm]});
            skFitSpline(sketch, "E188", {"points": [v(89.63, -10.88) * mm, v(89.6, -11.17) * mm, v(89.4, -11.38) * mm, v(89.12, -11.37) * mm]});
            skFitSpline(sketch, "E189", {"points": [v(89.12, -11.37) * mm, v(88.83, -11.36) * mm, v(88.6, -11.14) * mm, v(88.63, -10.84) * mm]});
            skFitSpline(sketch, "E190", {"points": [v(88.63, -10.84) * mm, v(88.65, -10.6) * mm, v(88.71, -10.36) * mm, v(88.8, -10.14) * mm]});
            skFitSpline(sketch, "E191", {"points": [v(88.8, -10.14) * mm, v(89.2, -9) * mm, v(89.6, -7.87) * mm, v(90, -6.73) * mm]});
            skFitSpline(sketch, "E192", {"points": [v(90, -6.73) * mm, v(90.08, -6.53) * mm, v(90.15, -6.33) * mm, v(90.22, -6.11) * mm]});
            skFitSpline(sketch, "E193", {"points": [v(90.22, -6.11) * mm, v(90.06, -6.03) * mm, v(89.91, -5.95) * mm, v(89.76, -5.87) * mm]});
            skFitSpline(sketch, "E194", {"points": [v(89.76, -5.87) * mm, v(89.15, -5.6) * mm, v(88.53, -5.32) * mm, v(87.93, -5.03) * mm]});
            skFitSpline(sketch, "E195", {"points": [v(87.93, -5.03) * mm, v(87.31, -4.74) * mm, v(86.7, -4.44) * mm, v(86.1, -4.13) * mm]});
            skFitSpline(sketch, "E196", {"points": [v(86.1, -4.13) * mm, v(85.97, -4.07) * mm, v(85.85, -3.99) * mm, v(85.74, -3.9) * mm]});
            skFitSpline(sketch, "E197", {"points": [v(85.74, -3.9) * mm, v(85.52, -3.69) * mm, v(85.51, -3.38) * mm, v(85.72, -3.17) * mm]});
            skFitSpline(sketch, "E198", {"points": [v(85.72, -3.17) * mm, v(85.91, -2.96) * mm, v(86.2, -2.97) * mm, v(86.43, -3.16) * mm]});
            skFitSpline(sketch, "E199", {"points": [v(86.43, -3.16) * mm, v(86.54, -3.25) * mm, v(86.66, -3.33) * mm, v(86.79, -3.4) * mm]});
            skFitSpline(sketch, "E200", {"points": [v(86.79, -3.4) * mm, v(87.88, -3.91) * mm, v(88.98, -4.43) * mm, v(90.08, -4.95) * mm]});
            skFitSpline(sketch, "E201", {"points": [v(90.08, -4.95) * mm, v(90.12, -4.97) * mm, v(90.17, -4.98) * mm, v(90.2, -5.01) * mm]});
            skFitSpline(sketch, "E202", {"points": [v(90.2, -5.01) * mm, v(90.45, -5.2) * mm, v(90.68, -5.15) * mm, v(90.92, -5) * mm]});
            skFitSpline(sketch, "E203", {"points": [v(90.92, -5) * mm, v(91.01, -4.95) * mm, v(91.11, -4.9) * mm, v(91.25, -4.83) * mm]});
            skFitSpline(sketch, "E204", {"points": [v(91.25, -4.83) * mm, v(91.14, -4.76) * mm, v(91.06, -4.71) * mm, v(90.97, -4.66) * mm]});
            skFitSpline(sketch, "E205", {"points": [v(90.97, -4.66) * mm, v(90.34, -4.32) * mm, v(89.71, -3.98) * mm, v(89.08, -3.63) * mm]});
            skFitSpline(sketch, "E206", {"points": [v(89.08, -3.63) * mm, v(88.98, -3.58) * mm, v(88.88, -3.52) * mm, v(88.8, -3.45) * mm]});
            skFitSpline(sketch, "E207", {"points": [v(88.8, -3.45) * mm, v(88.63, -3.32) * mm, v(88.51, -3.07) * mm, v(88.68, -2.81) * mm]});
            skFitSpline(sketch, "E208", {"points": [v(88.68, -2.81) * mm, v(88.82, -2.6) * mm, v(89.09, -2.52) * mm, v(89.33, -2.65) * mm]});
            skFitSpline(sketch, "E209", {"points": [v(89.33, -2.65) * mm, v(89.51, -2.74) * mm, v(89.68, -2.85) * mm, v(89.86, -2.95) * mm]});
            skFitSpline(sketch, "E210", {"points": [v(89.86, -2.95) * mm, v(90.33, -3.2) * mm, v(90.81, -3.46) * mm, v(91.28, -3.73) * mm]});
            skFitSpline(sketch, "E211", {"points": [v(91.28, -3.73) * mm, v(91.61, -3.91) * mm, v(91.93, -4.11) * mm, v(92.25, -4.31) * mm]});
            skFitSpline(sketch, "E212", {"points": [v(92.25, -4.31) * mm, v(92.35, -4.37) * mm, v(92.43, -4.4) * mm, v(92.54, -4.35) * mm]});
            skFitSpline(sketch, "E213", {"points": [v(92.54, -4.35) * mm, v(92.86, -4.23) * mm, v(93.18, -4.11) * mm, v(93.55, -3.97) * mm]});
            skFitSpline(sketch, "E214", {"points": [v(93.55, -3.97) * mm, v(93.38, -3.87) * mm, v(93.25, -3.79) * mm, v(93.12, -3.7) * mm]});
            skFitSpline(sketch, "E215", {"points": [v(93.12, -3.7) * mm, v(92.92, -3.57) * mm, v(92.73, -3.43) * mm, v(92.53, -3.3) * mm]});
            skFitSpline(sketch, "E216", {"points": [v(92.53, -3.3) * mm, v(92.46, -3.25) * mm, v(92.4, -3.2) * mm, v(92.33, -3.16) * mm]});
            skFitSpline(sketch, "E217", {"points": [v(92.33, -3.16) * mm, v(92.15, -3.06) * mm, v(91.97, -2.94) * mm, v(91.79, -2.86) * mm]});
            skFitSpline(sketch, "E218", {"points": [v(91.79, -2.86) * mm, v(91.47, -2.7) * mm, v(91.4, -2.16) * mm, v(91.61, -1.9) * mm]});
            skFitSpline(sketch, "E219", {"points": [v(91.61, -1.9) * mm, v(91.89, -1.57) * mm, v(92.14, -1.22) * mm, v(92.4, -0.87) * mm]});
            skFitSpline(sketch, "E220", {"points": [v(92.4, -0.87) * mm, v(92.71, -0.47) * mm, v(93.02, -0.05) * mm, v(93.33, 0.36) * mm]});
            skFitSpline(sketch, "E221", {"points": [v(93.33, 0.36) * mm, v(93.3, 0.4) * mm, v(93.27, 0.46) * mm, v(93.23, 0.5) * mm]});
            skFitSpline(sketch, "E222", {"points": [v(93.23, 0.5) * mm, v(92.72, 1.18) * mm, v(92.2, 1.86) * mm, v(91.68, 2.54) * mm]});
            skFitSpline(sketch, "E223", {"points": [v(91.68, 2.54) * mm, v(91.55, 2.7) * mm, v(91.45, 2.87) * mm, v(91.5, 3.1) * mm]});
            skFitSpline(sketch, "E224", {"points": [v(91.5, 3.1) * mm, v(91.52, 3.33) * mm, v(91.61, 3.48) * mm, v(91.8, 3.59) * mm]});
            skFitSpline(sketch, "E225", {"points": [v(91.8, 3.59) * mm, v(91.98, 3.7) * mm, v(92.16, 3.8) * mm, v(92.34, 3.9) * mm]});
            skFitSpline(sketch, "E226", {"points": [v(92.34, 3.9) * mm, v(92.38, 3.91) * mm, v(92.41, 3.93) * mm, v(92.44, 3.95) * mm]});
            skFitSpline(sketch, "E227", {"points": [v(92.44, 3.95) * mm, v(92.8, 4.2) * mm, v(93.14, 4.44) * mm, v(93.5, 4.69) * mm]});
            skFitSpline(sketch, "E228", {"points": [v(93.5, 4.69) * mm, v(93.46, 4.71) * mm, v(93.41, 4.74) * mm, v(93.37, 4.76) * mm]});
            skFitSpline(sketch, "E229", {"points": [v(93.37, 4.76) * mm, v(93.08, 4.87) * mm, v(92.8, 4.97) * mm, v(92.52, 5.08) * mm]});
            skFitSpline(sketch, "E230", {"points": [v(92.52, 5.08) * mm, v(92.44, 5.11) * mm, v(92.37, 5.12) * mm, v(92.3, 5.07) * mm]});
            skFitSpline(sketch, "E231", {"points": [v(92.3, 5.07) * mm, v(91.45, 4.47) * mm, v(90.49, 4.08) * mm, v(89.6, 3.54) * mm]});
            skFitSpline(sketch, "E232", {"points": [v(89.6, 3.54) * mm, v(89.51, 3.48) * mm, v(89.42, 3.42) * mm, v(89.32, 3.37) * mm]});
            skFitSpline(sketch, "E233", {"points": [v(89.32, 3.37) * mm, v(89.02, 3.23) * mm, v(88.71, 3.37) * mm, v(88.62, 3.69) * mm]});
            skFitSpline(sketch, "E234", {"points": [v(88.62, 3.69) * mm, v(88.56, 3.88) * mm, v(88.64, 4.03) * mm, v(88.77, 4.16) * mm]});
            skFitSpline(sketch, "E235", {"points": [v(88.77, 4.16) * mm, v(88.86, 4.24) * mm, v(88.97, 4.3) * mm, v(89.07, 4.36) * mm]});
            skFitSpline(sketch, "E236", {"points": [v(89.07, 4.36) * mm, v(89.7, 4.7) * mm, v(90.34, 5.04) * mm, v(90.97, 5.39) * mm]});
            skFitSpline(sketch, "E237", {"points": [v(90.97, 5.39) * mm, v(91.05, 5.43) * mm, v(91.13, 5.48) * mm, v(91.23, 5.54) * mm]});
            skFitSpline(sketch, "E238", {"points": [v(91.23, 5.54) * mm, v(91.02, 5.7) * mm, v(90.8, 5.8) * mm, v(90.59, 5.87) * mm]});
            skFitSpline(sketch, "E239", {"points": [v(90.59, 5.87) * mm, v(90.53, 5.89) * mm, v(90.46, 5.86) * mm, v(90.4, 5.84) * mm]});
            skFitSpline(sketch, "E240", {"points": [v(90.4, 5.84) * mm, v(89.2, 5.27) * mm, v(88, 4.7) * mm, v(86.8, 4.12) * mm]});
            skFitSpline(sketch, "E241", {"points": [v(86.8, 4.12) * mm, v(86.66, 4.06) * mm, v(86.53, 3.97) * mm, v(86.41, 3.87) * mm]});
            skFitSpline(sketch, "E242", {"points": [v(86.41, 3.87) * mm, v(86.2, 3.7) * mm, v(85.92, 3.7) * mm, v(85.72, 3.9) * mm]});
            skFitSpline(sketch, "E243", {"points": [v(85.72, 3.9) * mm, v(85.53, 4.1) * mm, v(85.51, 4.38) * mm, v(85.7, 4.58) * mm]});
            skFitSpline(sketch, "E244", {"points": [v(85.7, 4.58) * mm, v(85.8, 4.68) * mm, v(85.93, 4.77) * mm, v(86.05, 4.83) * mm]});
            skFitSpline(sketch, "E245", {"points": [v(86.05, 4.83) * mm, v(86.8, 5.2) * mm, v(87.56, 5.57) * mm, v(88.31, 5.94) * mm]});
            skFitSpline(sketch, "E246", {"points": [v(88.31, 5.94) * mm, v(88.94, 6.24) * mm, v(89.57, 6.52) * mm, v(90.22, 6.82) * mm]});
            skFitSpline(sketch, "E247", {"points": [v(90.22, 6.82) * mm, v(90.16, 7) * mm, v(90.11, 7.17) * mm, v(90.05, 7.34) * mm]});
            skFitSpline(sketch, "E248", {"points": [v(90.05, 7.34) * mm, v(89.64, 8.5) * mm, v(89.22, 9.66) * mm, v(88.8, 10.82) * mm]});
            skFitSpline(sketch, "E249", {"points": [v(88.8, 10.82) * mm, v(88.75, 10.98) * mm, v(88.7, 11.15) * mm, v(88.66, 11.32) * mm]});
            skFitSpline(sketch, "E250", {"points": [v(88.66, 11.32) * mm, v(88.63, 11.41) * mm, v(88.62, 11.5) * mm, v(88.63, 11.6) * mm]});
            skFitSpline(sketch, "E251", {"points": [v(88.63, 11.6) * mm, v(88.63, 11.88) * mm, v(88.82, 12.08) * mm, v(89.09, 12.09) * mm]});
            skFitSpline(sketch, "E252", {"points": [v(89.09, 12.09) * mm, v(89.37, 12.1) * mm, v(89.6, 11.94) * mm, v(89.62, 11.66) * mm]});
            skFitSpline(sketch, "E253", {"points": [v(89.62, 11.66) * mm, v(89.63, 11.43) * mm, v(89.7, 11.22) * mm, v(89.77, 11) * mm]});
            skFitSpline(sketch, "E254", {"points": [v(89.77, 11) * mm, v(90.16, 9.94) * mm, v(90.54, 8.87) * mm, v(90.92, 7.8) * mm]});
            skFitSpline(sketch, "E255", {"points": [v(90.92, 7.8) * mm, v(90.94, 7.74) * mm, v(90.98, 7.67) * mm, v(90.99, 7.6) * mm]});
            skFitSpline(sketch, "E256", {"points": [v(90.99, 7.6) * mm, v(91.03, 7.33) * mm, v(91.2, 7.2) * mm, v(91.46, 7.13) * mm]});
            skFitSpline(sketch, "E257", {"points": [v(91.46, 7.13) * mm, v(91.58, 7.1) * mm, v(91.7, 7.06) * mm, v(91.86, 7.01) * mm]});
            skFitSpline(sketch, "E258", {"points": [v(91.86, 7.01) * mm, v(91.82, 7.16) * mm, v(91.79, 7.28) * mm, v(91.75, 7.39) * mm]});
            skFitSpline(sketch, "E259", {"points": [v(91.75, 7.39) * mm, v(91.55, 8.08) * mm, v(91.34, 8.77) * mm, v(91.14, 9.45) * mm]});
            skFitSpline(sketch, "E260", {"points": [v(91.14, 9.45) * mm, v(91.12, 9.54) * mm, v(91.1, 9.63) * mm, v(91.09, 9.71) * mm]});
            skFitSpline(sketch, "E261", {"points": [v(91.09, 9.71) * mm, v(91.06, 9.97) * mm, v(91.22, 10.2) * mm, v(91.46, 10.25) * mm]});
            skFitSpline(sketch, "E262", {"points": [v(91.46, 10.25) * mm, v(91.71, 10.31) * mm, v(91.96, 10.17) * mm, v(92.04, 9.9) * mm]});
            skFitSpline(sketch, "E263", {"points": [v(92.04, 9.9) * mm, v(92.12, 9.65) * mm, v(92.18, 9.38) * mm, v(92.25, 9.12) * mm]});
            skFitSpline(sketch, "E264", {"points": [v(92.25, 9.12) * mm, v(92.42, 8.53) * mm, v(92.6, 7.94) * mm, v(92.77, 7.35) * mm]});
            skFitSpline(sketch, "E265", {"points": [v(92.77, 7.35) * mm, v(92.84, 7.12) * mm, v(92.88, 6.88) * mm, v(92.94, 6.65) * mm]});
            skFitSpline(sketch, "E266", {"points": [v(92.94, 6.65) * mm, v(92.95, 6.59) * mm, v(92.98, 6.5) * mm, v(93.03, 6.48) * mm]});
            skFitSpline(sketch, "E267", {"points": [v(93.03, 6.48) * mm, v(93.36, 6.32) * mm, v(93.7, 6.17) * mm, v(94.08, 6) * mm]});
            skFitSpline(sketch, "E268", {"points": [v(94.08, 6) * mm, v(94.04, 6.2) * mm, v(94, 6.34) * mm, v(93.97, 6.49) * mm]});
            skFitSpline(sketch, "E269", {"points": [v(93.97, 6.49) * mm, v(93.93, 6.72) * mm, v(93.9, 6.94) * mm, v(93.85, 7.17) * mm]});
            skFitSpline(sketch, "E270", {"points": [v(93.85, 7.17) * mm, v(93.83, 7.27) * mm, v(93.8, 7.37) * mm, v(93.78, 7.47) * mm]});
            skFitSpline(sketch, "E271", {"points": [v(93.78, 7.47) * mm, v(93.72, 7.67) * mm, v(93.66, 7.87) * mm, v(93.62, 8.07) * mm]});
            skFitSpline(sketch, "E272", {"points": [v(93.62, 8.07) * mm, v(93.56, 8.45) * mm, v(93.8, 8.77) * mm, v(94.19, 8.82) * mm]});
            skFitSpline(sketch, "E273", {"points": [v(94.19, 8.82) * mm, v(94.83, 8.91) * mm, v(95.46, 9) * mm, v(96.1, 9.1) * mm]});
            skFitSpline(sketch, "E274", {"points": [v(96.1, 9.1) * mm, v(96.4, 9.14) * mm, v(96.69, 9.16) * mm, v(97, 9.2) * mm]});
            skFitSpline(sketch, "E275", {"points": [v(97, 9.2) * mm, v(97.02, 9.35) * mm, v(97.05, 9.5) * mm, v(97.07, 9.63) * mm]});
            skFitSpline(sketch, "E276", {"points": [v(97.07, 9.63) * mm, v(97.14, 10.19) * mm, v(97.21, 10.74) * mm, v(97.29, 11.3) * mm]});
            skFitSpline(sketch, "E277", {"points": [v(97.29, 11.3) * mm, v(97.31, 11.51) * mm, v(97.35, 11.73) * mm, v(97.37, 11.96) * mm]});
            skFitSpline(sketch, "E278", {"points": [v(97.37, 11.96) * mm, v(97.4, 12.19) * mm, v(97.5, 12.36) * mm, v(97.68, 12.5) * mm]});
            skFitSpline(sketch, "E279", {"points": [v(97.68, 12.5) * mm, v(97.8, 12.58) * mm, v(97.94, 12.63) * mm, v(98.1, 12.6) * mm]});
            skFitSpline(sketch, "E280", {"points": [v(98.1, 12.6) * mm, v(98.3, 12.55) * mm, v(98.52, 12.48) * mm, v(98.74, 12.43) * mm]});
            skFitSpline(sketch, "E281", {"points": [v(98.74, 12.43) * mm, v(98.9, 12.4) * mm, v(99.05, 12.38) * mm, v(99.2, 12.34) * mm]});
            skFitSpline(sketch, "E282", {"points": [v(99.2, 12.34) * mm, v(99.52, 12.28) * mm, v(99.84, 12.2) * mm, v(100.19, 12.13) * mm]});
            skFitSpline(sketch, "E283", {"points": [v(100.19, 12.13) * mm, v(100.07, 12.51) * mm, v(99.9, 12.84) * mm, v(99.73, 13.17) * mm]});
            skFitSpline(sketch, "E284", {"points": [v(99.73, 13.17) * mm, v(99.7, 13.22) * mm, v(99.62, 13.26) * mm, v(99.55, 13.27) * mm]});
            skFitSpline(sketch, "E285", {"points": [v(99.55, 13.27) * mm, v(99.04, 13.41) * mm, v(98.52, 13.55) * mm, v(98, 13.69) * mm]});
            skFitSpline(sketch, "E286", {"points": [v(98, 13.69) * mm, v(97.46, 13.84) * mm, v(96.92, 14) * mm, v(96.37, 14.15) * mm]});
            skFitSpline(sketch, "E287", {"points": [v(96.37, 14.15) * mm, v(96.03, 14.24) * mm, v(95.86, 14.52) * mm, v(95.98, 14.81) * mm]});
            skFitSpline(sketch, "E288", {"points": [v(95.98, 14.81) * mm, v(96.05, 14.99) * mm, v(96.18, 15.1) * mm, v(96.38, 15.1) * mm]});
            skFitSpline(sketch, "E289", {"points": [v(96.38, 15.1) * mm, v(96.52, 15.1) * mm, v(96.66, 15.09) * mm, v(96.8, 15.05) * mm]});
            skFitSpline(sketch, "E290", {"points": [v(96.8, 15.05) * mm, v(97.49, 14.85) * mm, v(98.18, 14.64) * mm, v(98.87, 14.44) * mm]});
            skFitSpline(sketch, "E291", {"points": [v(98.87, 14.44) * mm, v(98.96, 14.4) * mm, v(99.06, 14.4) * mm, v(99.2, 14.36) * mm]});
            skFitSpline(sketch, "E292", {"points": [v(99.2, 14.36) * mm, v(99.12, 14.6) * mm, v(99.05, 14.82) * mm, v(98.96, 15.02) * mm]});
            skFitSpline(sketch, "E293", {"points": [v(98.96, 15.02) * mm, v(98.94, 15.07) * mm, v(98.86, 15.13) * mm, v(98.8, 15.15) * mm]});
            skFitSpline(sketch, "E294", {"points": [v(98.8, 15.15) * mm, v(97.72, 15.54) * mm, v(96.64, 15.93) * mm, v(95.56, 16.32) * mm]});
            skFitSpline(sketch, "E295", {"points": [v(95.56, 16.32) * mm, v(95.36, 16.39) * mm, v(95.17, 16.46) * mm, v(94.97, 16.51) * mm]});
            skFitSpline(sketch, "E296", {"points": [v(94.97, 16.51) * mm, v(94.85, 16.55) * mm, v(94.72, 16.57) * mm, v(94.6, 16.58) * mm]});
            skFitSpline(sketch, "E297", {"points": [v(94.6, 16.58) * mm, v(94.3, 16.6) * mm, v(94.11, 16.8) * mm, v(94.1, 17.08) * mm]});
            skFitSpline(sketch, "E298", {"points": [v(94.1, 17.08) * mm, v(94.1, 17.36) * mm, v(94.32, 17.59) * mm, v(94.6, 17.59) * mm]});
            skFitSpline(sketch, "E299", {"points": [v(94.6, 17.59) * mm, v(94.73, 17.59) * mm, v(94.86, 17.56) * mm, v(94.98, 17.52) * mm]});
            skFitSpline(sketch, "E300", {"points": [v(94.98, 17.52) * mm, v(95.77, 17.26) * mm, v(96.55, 17) * mm, v(97.34, 16.72) * mm]});
            skFitSpline(sketch, "E301", {"points": [v(97.34, 16.72) * mm, v(98.01, 16.48) * mm, v(98.68, 16.23) * mm, v(99.37, 15.97) * mm]});
            skFitSpline(sketch, "E302", {"points": [v(99.37, 15.97) * mm, v(99.46, 16.16) * mm, v(99.54, 16.32) * mm, v(99.62, 16.5) * mm]});
            skFitSpline(sketch, "E303", {"points": [v(99.62, 16.5) * mm, v(100.04, 17.38) * mm, v(100.44, 18.27) * mm, v(100.86, 19.15) * mm]});
            skFitSpline(sketch, "E304", {"points": [v(100.86, 19.15) * mm, v(101.03, 19.5) * mm, v(101.21, 19.85) * mm, v(101.4, 20.2) * mm]});
            skFitSpline(sketch, "E305", {"points": [v(101.4, 20.2) * mm, v(101.46, 20.3) * mm, v(101.53, 20.41) * mm, v(101.62, 20.5) * mm]});
            skFitSpline(sketch, "E306", {"points": [v(101.62, 20.5) * mm, v(101.82, 20.69) * mm, v(102.12, 20.68) * mm, v(102.31, 20.49) * mm]});
            skFitSpline(sketch, "E307", {"points": [v(102.31, 20.49) * mm, v(102.5, 20.3) * mm, v(102.51, 20) * mm, v(102.33, 19.8) * mm]});
            skFitSpline(sketch, "E308", {"points": [v(102.33, 19.8) * mm, v(102.24, 19.68) * mm, v(102.15, 19.55) * mm, v(102.09, 19.42) * mm]});
            skFitSpline(sketch, "E309", {"points": [v(102.09, 19.42) * mm, v(101.56, 18.32) * mm, v(101.05, 17.22) * mm, v(100.53, 16.13) * mm]});
            skFitSpline(sketch, "E310", {"points": [v(100.53, 16.13) * mm, v(100.49, 16.04) * mm, v(100.45, 15.95) * mm, v(100.4, 15.87) * mm]});
            skFitSpline(sketch, "E311", {"points": [v(100.4, 15.87) * mm, v(100.32, 15.74) * mm, v(100.31, 15.62) * mm, v(100.38, 15.48) * mm]});
            skFitSpline(sketch, "E312", {"points": [v(100.38, 15.48) * mm, v(100.47, 15.32) * mm, v(100.54, 15.15) * mm, v(100.64, 14.95) * mm]});
            skFitSpline(sketch, "E313", {"points": [v(100.64, 14.95) * mm, v(100.7, 15.05) * mm, v(100.75, 15.12) * mm, v(100.79, 15.19) * mm]});
            skFitSpline(sketch, "E314", {"points": [v(100.79, 15.19) * mm, v(101.14, 15.83) * mm, v(101.48, 16.47) * mm, v(101.83, 17.1) * mm]});
            skFitSpline(sketch, "E315", {"points": [v(101.83, 17.1) * mm, v(101.9, 17.2) * mm, v(101.95, 17.32) * mm, v(102.02, 17.4) * mm]});
            skFitSpline(sketch, "E316", {"points": [v(102.02, 17.4) * mm, v(102.2, 17.63) * mm, v(102.47, 17.67) * mm, v(102.69, 17.51) * mm]});
            skFitSpline(sketch, "E317", {"points": [v(102.69, 17.51) * mm, v(102.89, 17.37) * mm, v(102.95, 17.1) * mm, v(102.83, 16.87) * mm]});
            skFitSpline(sketch, "E318", {"points": [v(102.83, 16.87) * mm, v(102.71, 16.66) * mm, v(102.59, 16.46) * mm, v(102.47, 16.25) * mm]});
            skFitSpline(sketch, "E319", {"points": [v(102.47, 16.25) * mm, v(102.19, 15.73) * mm, v(101.91, 15.2) * mm, v(101.62, 14.69) * mm]});
            skFitSpline(sketch, "E320", {"points": [v(101.62, 14.69) * mm, v(101.48, 14.44) * mm, v(101.33, 14.2) * mm, v(101.17, 13.96) * mm]});
            skFitSpline(sketch, "E321", {"points": [v(101.17, 13.96) * mm, v(101.1, 13.86) * mm, v(101.09, 13.78) * mm, v(101.13, 13.67) * mm]});
            skFitSpline(sketch, "E322", {"points": [v(101.13, 13.67) * mm, v(101.25, 13.35) * mm, v(101.37, 13.03) * mm, v(101.5, 12.66) * mm]});
            skFitSpline(sketch, "E323", {"points": [v(101.5, 12.66) * mm, v(101.61, 12.83) * mm, v(101.7, 12.96) * mm, v(101.78, 13.09) * mm]});
            skFitSpline(sketch, "E324", {"points": [v(101.78, 13.09) * mm, v(101.91, 13.28) * mm, v(102.05, 13.48) * mm, v(102.18, 13.68) * mm]});
            skFitSpline(sketch, "E325", {"points": [v(102.18, 13.68) * mm, v(102.25, 13.77) * mm, v(102.3, 13.87) * mm, v(102.35, 13.96) * mm]});
            skFitSpline(sketch, "E326", {"points": [v(102.35, 13.96) * mm, v(102.47, 14.15) * mm, v(102.58, 14.33) * mm, v(102.7, 14.51) * mm]});
            skFitSpline(sketch, "E327", {"points": [v(102.7, 14.51) * mm, v(102.85, 14.75) * mm, v(103.34, 14.8) * mm, v(103.58, 14.6) * mm]});
            skFitSpline(sketch, "E328", {"points": [v(103.58, 14.6) * mm, v(103.9, 14.32) * mm, v(104.25, 14.07) * mm, v(104.59, 13.82) * mm]});
            skFitSpline(sketch, "E329", {"points": [v(104.59, 13.82) * mm, v(105, 13.5) * mm, v(105.42, 13.2) * mm, v(105.84, 12.88) * mm]});
            skFitSpline(sketch, "E330", {"points": [v(105.84, 12.88) * mm, v(105.9, 12.92) * mm, v(105.97, 12.96) * mm, v(106.02, 13) * mm]});
            skFitSpline(sketch, "E331", {"points": [v(106.02, 13) * mm, v(106.7, 13.52) * mm, v(107.38, 14.04) * mm, v(108.06, 14.56) * mm]});
            skFitSpline(sketch, "E332", {"points": [v(108.06, 14.56) * mm, v(108.2, 14.67) * mm, v(108.35, 14.74) * mm, v(108.54, 14.72) * mm]});
            skFitSpline(sketch, "E333", {"points": [v(108.54, 14.72) * mm, v(108.78, 14.7) * mm, v(108.96, 14.6) * mm, v(109.07, 14.4) * mm]});
            skFitSpline(sketch, "E334", {"points": [v(109.07, 14.4) * mm, v(109.17, 14.22) * mm, v(109.27, 14.04) * mm, v(109.38, 13.86) * mm]});
            skFitSpline(sketch, "E335", {"points": [v(109.38, 13.86) * mm, v(109.39, 13.84) * mm, v(109.4, 13.82) * mm, v(109.4, 13.8) * mm]});
            skFitSpline(sketch, "E336", {"points": [v(109.4, 13.8) * mm, v(109.66, 13.44) * mm, v(109.91, 13.08) * mm, v(110.18, 12.7) * mm]});
            skFitSpline(sketch, "E337", {"points": [v(110.18, 12.7) * mm, v(110.23, 12.81) * mm, v(110.28, 12.92) * mm, v(110.32, 13.02) * mm]});
            skFitSpline(sketch, "E338", {"points": [v(110.32, 13.02) * mm, v(110.4, 13.25) * mm, v(110.48, 13.48) * mm, v(110.57, 13.7) * mm]});
            skFitSpline(sketch, "E339", {"points": [v(110.57, 13.7) * mm, v(110.6, 13.78) * mm, v(110.6, 13.85) * mm, v(110.54, 13.92) * mm]});
            skFitSpline(sketch, "E340", {"points": [v(110.54, 13.92) * mm, v(109.95, 14.75) * mm, v(109.57, 15.7) * mm, v(109.04, 16.56) * mm]});
            skFitSpline(sketch, "E341", {"points": [v(109.04, 16.56) * mm, v(108.98, 16.66) * mm, v(108.92, 16.76) * mm, v(108.87, 16.86) * mm]});
            skFitSpline(sketch, "E342", {"points": [v(108.87, 16.86) * mm, v(108.73, 17.11) * mm, v(108.8, 17.39) * mm, v(109.02, 17.53) * mm]});
            skFitSpline(sketch, "E343", {"points": [v(109.02, 17.53) * mm, v(109.24, 17.67) * mm, v(109.5, 17.61) * mm, v(109.68, 17.39) * mm]});
            skFitSpline(sketch, "E344", {"points": [v(109.68, 17.39) * mm, v(109.73, 17.32) * mm, v(109.77, 17.26) * mm, v(109.8, 17.19) * mm]});
            skFitSpline(sketch, "E345", {"points": [v(109.8, 17.19) * mm, v(110.15, 16.56) * mm, v(110.49, 15.94) * mm, v(110.83, 15.31) * mm]});
            skFitSpline(sketch, "E346", {"points": [v(110.83, 15.31) * mm, v(110.89, 15.2) * mm, v(110.95, 15.1) * mm, v(111.02, 14.97) * mm]});
            skFitSpline(sketch, "E347", {"points": [v(111.02, 14.97) * mm, v(111.19, 15.19) * mm, v(111.28, 15.41) * mm, v(111.36, 15.64) * mm]});
            skFitSpline(sketch, "E348", {"points": [v(111.36, 15.64) * mm, v(111.37, 15.68) * mm, v(111.34, 15.75) * mm, v(111.32, 15.8) * mm]});
            skFitSpline(sketch, "E349", {"points": [v(111.32, 15.8) * mm, v(110.86, 16.78) * mm, v(110.4, 17.75) * mm, v(109.95, 18.73) * mm]});
            skFitSpline(sketch, "E350", {"points": [v(109.95, 18.73) * mm, v(109.83, 18.98) * mm, v(109.7, 19.23) * mm, v(109.57, 19.48) * mm]});
            skFitSpline(sketch, "E351", {"points": [v(109.57, 19.48) * mm, v(109.5, 19.59) * mm, v(109.43, 19.7) * mm, v(109.35, 19.8) * mm]});
            skFitSpline(sketch, "E352", {"points": [v(109.35, 19.8) * mm, v(109.17, 20) * mm, v(109.17, 20.29) * mm, v(109.37, 20.48) * mm]});
            skFitSpline(sketch, "E353", {"points": [v(109.37, 20.48) * mm, v(109.57, 20.68) * mm, v(109.88, 20.7) * mm, v(110.08, 20.49) * mm]});
            skFitSpline(sketch, "E354", {"points": [v(110.08, 20.49) * mm, v(110.18, 20.38) * mm, v(110.27, 20.25) * mm, v(110.33, 20.11) * mm]});
            skFitSpline(sketch, "E355", {"points": [v(110.33, 20.11) * mm, v(110.72, 19.33) * mm, v(111.1, 18.55) * mm, v(111.47, 17.76) * mm]});
            skFitSpline(sketch, "E356", {"points": [v(111.47, 17.76) * mm, v(111.75, 17.17) * mm, v(112.03, 16.58) * mm, v(112.31, 15.97) * mm]});
            skFitSpline(sketch, "E357", {"points": [v(112.31, 15.97) * mm, v(113.2, 16.3) * mm, v(114.09, 16.64) * mm, v(114.97, 16.95) * mm]});
            skFitSpline(sketch, "E358", {"points": [v(114.97, 16.95) * mm, v(115.54, 17.16) * mm, v(116.12, 17.34) * mm, v(116.7, 17.52) * mm]});
            skFitSpline(sketch, "E359", {"points": [v(116.7, 17.52) * mm, v(116.82, 17.56) * mm, v(116.95, 17.59) * mm, v(117.08, 17.59) * mm]});
            skFitSpline(sketch, "E360", {"points": [v(117.08, 17.59) * mm, v(117.37, 17.59) * mm, v(117.57, 17.37) * mm, v(117.57, 17.08) * mm]});
            skFitSpline(sketch, "E361", {"points": [v(117.57, 17.08) * mm, v(117.57, 16.8) * mm, v(117.38, 16.61) * mm, v(117.1, 16.58) * mm]});
            skFitSpline(sketch, "E362", {"points": [v(117.1, 16.58) * mm, v(116.95, 16.57) * mm, v(116.8, 16.55) * mm, v(116.68, 16.5) * mm]});
            skFitSpline(sketch, "E363", {"points": [v(116.68, 16.5) * mm, v(115.53, 16.1) * mm, v(114.4, 15.68) * mm, v(113.25, 15.27) * mm]});
            skFitSpline(sketch, "E364", {"points": [v(113.25, 15.27) * mm, v(113.16, 15.24) * mm, v(113.08, 15.2) * mm, v(113, 15.19) * mm]});
            skFitSpline(sketch, "E365", {"points": [v(113, 15.19) * mm, v(112.8, 15.15) * mm, v(112.7, 15.04) * mm, v(112.65, 14.85) * mm]});
            skFitSpline(sketch, "E366", {"points": [v(112.65, 14.85) * mm, v(112.6, 14.7) * mm, v(112.55, 14.56) * mm, v(112.5, 14.41) * mm]});
            skFitSpline(sketch, "E367", {"points": [v(112.5, 14.41) * mm, v(112.6, 14.35) * mm, v(112.69, 14.4) * mm, v(112.76, 14.43) * mm]});
            skFitSpline(sketch, "E368", {"points": [v(112.76, 14.43) * mm, v(113.45, 14.63) * mm, v(114.14, 14.83) * mm, v(114.83, 15.03) * mm]});
            skFitSpline(sketch, "E369", {"points": [v(114.83, 15.03) * mm, v(114.96, 15.07) * mm, v(115.1, 15.1) * mm, v(115.23, 15.1) * mm]});
            skFitSpline(sketch, "E370", {"points": [v(115.23, 15.1) * mm, v(115.5, 15.12) * mm, v(115.7, 14.95) * mm, v(115.74, 14.7) * mm]});
            skFitSpline(sketch, "E371", {"points": [v(115.74, 14.7) * mm, v(115.77, 14.46) * mm, v(115.63, 14.24) * mm, v(115.37, 14.16) * mm]});
            skFitSpline(sketch, "E372", {"points": [v(115.37, 14.16) * mm, v(115.22, 14.12) * mm, v(115.06, 14.08) * mm, v(114.9, 14.04) * mm]});
            skFitSpline(sketch, "E373", {"points": [v(114.9, 14.04) * mm, v(114.18, 13.83) * mm, v(113.45, 13.61) * mm, v(112.72, 13.4) * mm]});
            skFitSpline(sketch, "E374", {"points": [v(112.72, 13.4) * mm, v(112.53, 13.35) * mm, v(112.33, 13.32) * mm, v(112.14, 13.27) * mm]});
            skFitSpline(sketch, "E375", {"points": [v(112.14, 13.27) * mm, v(112.07, 13.26) * mm, v(111.99, 13.23) * mm, v(111.96, 13.18) * mm]});
            skFitSpline(sketch, "E376", {"points": [v(111.96, 13.18) * mm, v(111.8, 12.85) * mm, v(111.65, 12.5) * mm, v(111.47, 12.12) * mm]});
            skFitSpline(sketch, "E377", {"points": [v(111.47, 12.12) * mm, v(111.65, 12.16) * mm, v(111.78, 12.2) * mm, v(111.91, 12.22) * mm]});
            skFitSpline(sketch, "E378", {"points": [v(111.91, 12.22) * mm, v(112.18, 12.27) * mm, v(112.45, 12.31) * mm, v(112.71, 12.37) * mm]});
            skFitSpline(sketch, "E379", {"points": [v(112.71, 12.37) * mm, v(112.8, 12.38) * mm, v(112.88, 12.41) * mm, v(112.97, 12.43) * mm]});
            skFitSpline(sketch, "E380", {"points": [v(112.97, 12.43) * mm, v(113.18, 12.5) * mm, v(113.4, 12.56) * mm, v(113.61, 12.6) * mm]});
            skFitSpline(sketch, "E381", {"points": [v(113.61, 12.6) * mm, v(113.93, 12.65) * mm, v(114.26, 12.37) * mm, v(114.3, 12.03) * mm]});
            skFitSpline(sketch, "E382", {"points": [v(114.3, 12.03) * mm, v(114.36, 11.56) * mm, v(114.42, 11.08) * mm, v(114.49, 10.6) * mm]});
            skFitSpline(sketch, "E383", {"points": [v(114.49, 10.6) * mm, v(114.55, 10.15) * mm, v(114.62, 9.7) * mm, v(114.7, 9.2) * mm]});
            skFitSpline(sketch, "E384", {"points": [v(114.7, 9.2) * mm, v(114.9, 9.18) * mm, v(115.12, 9.15) * mm, v(115.34, 9.12) * mm]});
            skFitSpline(sketch, "E385", {"points": [v(115.34, 9.12) * mm, v(115.87, 9.04) * mm, v(116.4, 8.97) * mm, v(116.93, 8.9) * mm]});
            skFitSpline(sketch, "E386", {"points": [v(116.93, 8.9) * mm, v(117.1, 8.87) * mm, v(117.3, 8.83) * mm, v(117.47, 8.83) * mm]});
            skFitSpline(sketch, "E387", {"points": [v(117.47, 8.83) * mm, v(117.82, 8.83) * mm, v(118.19, 8.38) * mm, v(118.06, 8.03) * mm]});
            skFitSpline(sketch, "E388", {"points": [v(118.06, 8.03) * mm, v(117.98, 7.83) * mm, v(117.94, 7.62) * mm, v(117.89, 7.4) * mm]});
            skFitSpline(sketch, "E389", {"points": [v(117.89, 7.4) * mm, v(117.86, 7.28) * mm, v(117.85, 7.14) * mm, v(117.82, 7) * mm]});
            skFitSpline(sketch, "E390", {"points": [v(117.82, 7) * mm, v(117.76, 6.69) * mm, v(117.69, 6.37) * mm, v(117.61, 6.03) * mm]});
            skFitSpline(sketch, "E391", {"points": [v(117.61, 6.03) * mm, v(117.69, 6.05) * mm, v(117.74, 6.06) * mm, v(117.8, 6.09) * mm]});
            skFitSpline(sketch, "E392", {"points": [v(117.8, 6.09) * mm, v(118.06, 6.2) * mm, v(118.32, 6.32) * mm, v(118.58, 6.44) * mm]});
            skFitSpline(sketch, "E393", {"points": [v(118.58, 6.44) * mm, v(118.68, 6.48) * mm, v(118.73, 6.54) * mm, v(118.76, 6.65) * mm]});
            skFitSpline(sketch, "E394", {"points": [v(118.76, 6.65) * mm, v(118.9, 7.19) * mm, v(119.04, 7.73) * mm, v(119.19, 8.26) * mm]});
            skFitSpline(sketch, "E395", {"points": [v(119.19, 8.26) * mm, v(119.33, 8.8) * mm, v(119.48, 9.33) * mm, v(119.63, 9.86) * mm]});
            skFitSpline(sketch, "E396", {"points": [v(119.63, 9.86) * mm, v(119.7, 10.13) * mm, v(119.92, 10.3) * mm, v(120.17, 10.26) * mm]});
            skFitSpline(sketch, "E397", {"points": [v(120.17, 10.26) * mm, v(120.4, 10.24) * mm, v(120.58, 10.06) * mm, v(120.59, 9.84) * mm]});
            skFitSpline(sketch, "E398", {"points": [v(120.59, 9.84) * mm, v(120.59, 9.68) * mm, v(120.56, 9.52) * mm, v(120.51, 9.37) * mm]});
            skFitSpline(sketch, "E399", {"points": [v(120.51, 9.37) * mm, v(120.32, 8.68) * mm, v(120.1, 7.99) * mm, v(119.9, 7.3) * mm]});
            skFitSpline(sketch, "E400", {"points": [v(119.9, 7.3) * mm, v(119.88, 7.22) * mm, v(119.87, 7.15) * mm, v(119.84, 7.03) * mm]});
            skFitSpline(sketch, "E401", {"points": [v(119.84, 7.03) * mm, v(120.11, 7.07) * mm, v(120.34, 7.16) * mm, v(120.55, 7.28) * mm]});
            skFitSpline(sketch, "E402", {"points": [v(120.55, 7.28) * mm, v(120.6, 7.3) * mm, v(120.61, 7.37) * mm, v(120.63, 7.42) * mm]});
            skFitSpline(sketch, "E403", {"points": [v(120.63, 7.42) * mm, v(120.9, 8.16) * mm, v(121.18, 8.9) * mm, v(121.45, 9.64) * mm]});
            skFitSpline(sketch, "E404", {"points": [v(121.45, 9.64) * mm, v(121.64, 10.2) * mm, v(121.83, 10.75) * mm, v(122.01, 11.3) * mm]});
            skFitSpline(sketch, "E405", {"points": [v(122.01, 11.3) * mm, v(122.05, 11.4) * mm, v(122.05, 11.52) * mm, v(122.06, 11.63) * mm]});
            skFitSpline(sketch, "E406", {"points": [v(122.06, 11.63) * mm, v(122.09, 11.9) * mm, v(122.27, 12.09) * mm, v(122.55, 12.1) * mm]});
            skFitSpline(sketch, "E407", {"points": [v(122.55, 12.1) * mm, v(122.83, 12.1) * mm, v(123.05, 11.9) * mm, v(123.06, 11.63) * mm]});
            skFitSpline(sketch, "E408", {"points": [v(123.06, 11.63) * mm, v(123.07, 11.5) * mm, v(123.04, 11.35) * mm, v(123, 11.21) * mm]});
            skFitSpline(sketch, "E409", {"points": [v(123, 11.21) * mm, v(122.73, 10.4) * mm, v(122.45, 9.6) * mm, v(122.17, 8.79) * mm]});
            skFitSpline(sketch, "E410", {"points": [v(122.17, 8.79) * mm, v(121.96, 8.2) * mm, v(121.75, 7.63) * mm, v(121.54, 7.05) * mm]});
            skFitSpline(sketch, "E411", {"points": [v(121.54, 7.05) * mm, v(121.52, 6.99) * mm, v(121.49, 6.92) * mm, v(121.46, 6.84) * mm]});
            skFitSpline(sketch, "E412", {"points": [v(121.46, 6.84) * mm, v(121.63, 6.75) * mm, v(121.8, 6.66) * mm, v(121.97, 6.58) * mm]});
            skFitSpline(sketch, "E413", {"points": [v(121.97, 6.58) * mm, v(122.85, 6.18) * mm, v(123.72, 5.77) * mm, v(124.6, 5.36) * mm]});
            skFitSpline(sketch, "E414", {"points": [v(124.6, 5.36) * mm, v(124.95, 5.2) * mm, v(125.3, 5.01) * mm, v(125.64, 4.83) * mm]});
            skFitSpline(sketch, "E415", {"points": [v(125.64, 4.83) * mm, v(125.76, 4.77) * mm, v(125.87, 4.7) * mm, v(125.96, 4.6) * mm]});
            skFitSpline(sketch, "E416", {"points": [v(125.96, 4.6) * mm, v(126.16, 4.4) * mm, v(126.16, 4.1) * mm, v(125.97, 3.9) * mm]});
            skFitSpline(sketch, "E417", {"points": [v(125.97, 3.9) * mm, v(125.77, 3.7) * mm, v(125.49, 3.7) * mm, v(125.26, 3.88) * mm]});
            skFitSpline(sketch, "E418", {"points": [v(125.26, 3.88) * mm, v(125.15, 3.97) * mm, v(125.03, 4.06) * mm, v(124.9, 4.12) * mm]});
            skFitSpline(sketch, "E419", {"points": [v(124.9, 4.12) * mm, v(123.82, 4.63) * mm, v(122.74, 5.14) * mm, v(121.66, 5.66) * mm]});
            skFitSpline(sketch, "E420", {"points": [v(121.66, 5.66) * mm, v(121.6, 5.68) * mm, v(121.53, 5.7) * mm, v(121.48, 5.74) * mm]});
            skFitSpline(sketch, "E421", {"points": [v(121.48, 5.74) * mm, v(121.24, 5.93) * mm, v(121, 5.87) * mm, v(120.75, 5.73) * mm]});
            skFitSpline(sketch, "E422", {"points": [v(120.75, 5.73) * mm, v(120.67, 5.68) * mm, v(120.57, 5.63) * mm, v(120.47, 5.58) * mm]});
            skFitSpline(sketch, "E423", {"points": [v(120.47, 5.58) * mm, v(120.52, 5.47) * mm, v(120.62, 5.45) * mm, v(120.7, 5.4) * mm]});
            skFitSpline(sketch, "E424", {"points": [v(120.7, 5.4) * mm, v(121.33, 5.06) * mm, v(121.96, 4.71) * mm, v(122.59, 4.37) * mm]});
            skFitSpline(sketch, "E425", {"points": [v(122.59, 4.37) * mm, v(122.69, 4.31) * mm, v(122.79, 4.26) * mm, v(122.87, 4.2) * mm]});
            skFitSpline(sketch, "E426", {"points": [v(122.87, 4.2) * mm, v(123.1, 4.02) * mm, v(123.15, 3.75) * mm, v(123, 3.53) * mm]});
            skFitSpline(sketch, "E427", {"points": [v(123, 3.53) * mm, v(122.86, 3.32) * mm, v(122.6, 3.25) * mm, v(122.35, 3.38) * mm]});
            skFitSpline(sketch, "E428", {"points": [v(122.35, 3.38) * mm, v(122.21, 3.45) * mm, v(122.08, 3.53) * mm, v(121.95, 3.6) * mm]});
            skFitSpline(sketch, "E429", {"points": [v(121.95, 3.6) * mm, v(121.4, 3.9) * mm, v(120.84, 4.2) * mm, v(120.29, 4.51) * mm]});
            skFitSpline(sketch, "E430", {"points": [v(120.29, 4.51) * mm, v(120, 4.67) * mm, v(119.72, 4.85) * mm, v(119.45, 5.03) * mm]});
            skFitSpline(sketch, "E431", {"points": [v(119.45, 5.03) * mm, v(119.34, 5.1) * mm, v(119.25, 5.12) * mm, v(119.12, 5.07) * mm]});
            skFitSpline(sketch, "E432", {"points": [v(119.12, 5.07) * mm, v(118.81, 4.95) * mm, v(118.5, 4.83) * mm, v(118.15, 4.7) * mm]});
            skFitSpline(sketch, "E433", {"points": [v(118.15, 4.7) * mm, v(118.27, 4.62) * mm, v(118.35, 4.56) * mm, v(118.44, 4.5) * mm]});
            skFitSpline(sketch, "E434", {"points": [v(118.44, 4.5) * mm, v(118.7, 4.32) * mm, v(118.96, 4.14) * mm, v(119.23, 3.97) * mm]});
            skFitSpline(sketch, "E435", {"points": [v(119.23, 3.97) * mm, v(119.44, 3.83) * mm, v(119.65, 3.7) * mm, v(119.87, 3.6) * mm]});
            skFitSpline(sketch, "E436", {"points": [v(119.87, 3.6) * mm, v(120.23, 3.44) * mm, v(120.3, 2.9) * mm, v(120.04, 2.57) * mm]});
            skFitSpline(sketch, "E437", {"points": [v(120.04, 2.57) * mm, v(119.5, 1.91) * mm, v(119, 1.23) * mm, v(118.49, 0.55) * mm]});
            skFitSpline(sketch, "E438", {"points": [v(118.49, 0.55) * mm, v(118.45, 0.5) * mm, v(118.4, 0.44) * mm, v(118.36, 0.37) * mm]});
            skFitSpline(sketch, "E439", {"points": [v(118.36, 0.37) * mm, v(118.4, 0.32) * mm, v(118.42, 0.27) * mm, v(118.45, 0.23) * mm]});
            skFitSpline(sketch, "E440", {"points": [v(118.45, 0.23) * mm, v(118.97, -0.45) * mm, v(119.48, -1.14) * mm, v(120, -1.81) * mm]});
            skFitSpline(sketch, "E441", {"points": [v(120, -1.81) * mm, v(120.15, -2) * mm, v(120.24, -2.19) * mm, v(120.2, -2.43) * mm]});
            skFitSpline(sketch, "E442", {"points": [v(120.2, -2.43) * mm, v(120.17, -2.58) * mm, v(120.1, -2.7) * mm, v(119.98, -2.8) * mm]});
            skFitSpline(sketch, "E443", {"points": [v(119.98, -2.8) * mm, v(119.8, -2.91) * mm, v(119.62, -3.02) * mm, v(119.43, -3.13) * mm]});
            skFitSpline(sketch, "E444", {"points": [v(119.43, -3.13) * mm, v(119.38, -3.16) * mm, v(119.32, -3.18) * mm, v(119.26, -3.21) * mm]});
            skFitSpline(sketch, "E445", {"points": [v(119.26, -3.21) * mm, v(118.91, -3.45) * mm, v(118.56, -3.69) * mm, v(118.21, -3.92) * mm]});
            skFitSpline(sketch, "E446", {"points": [v(118.21, -3.92) * mm, v(118.2, -3.93) * mm, v(118.2, -3.95) * mm, v(118.17, -3.99) * mm]});
            skFitSpline(sketch, "E447", {"points": [v(118.17, -3.99) * mm, v(118.51, -4.11) * mm, v(118.85, -4.24) * mm, v(119.18, -4.36) * mm]});
            skFitSpline(sketch, "E448", {"points": [v(119.18, -4.36) * mm, v(119.26, -4.4) * mm, v(119.33, -4.38) * mm, v(119.4, -4.33) * mm]});
            skFitSpline(sketch, "E449", {"points": [v(119.4, -4.33) * mm, v(120.23, -3.75) * mm, v(121.17, -3.37) * mm, v(122.03, -2.84) * mm]});
            skFitSpline(sketch, "E450", {"points": [v(122.03, -2.84) * mm, v(122.13, -2.77) * mm, v(122.23, -2.71) * mm, v(122.34, -2.66) * mm]});
            skFitSpline(sketch, "E451", {"points": [v(122.34, -2.66) * mm, v(122.58, -2.53) * mm, v(122.86, -2.59) * mm, v(123, -2.8) * mm]});
            skFitSpline(sketch, "E452", {"points": [v(123, -2.8) * mm, v(123.15, -3.02) * mm, v(123.1, -3.28) * mm, v(122.88, -3.46) * mm]});
            skFitSpline(sketch, "E453", {"points": [v(122.88, -3.46) * mm, v(122.82, -3.5) * mm, v(122.76, -3.55) * mm, v(122.7, -3.58) * mm]});
            skFitSpline(sketch, "E454", {"points": [v(122.7, -3.58) * mm, v(122.1, -3.92) * mm, v(121.48, -4.25) * mm, v(120.87, -4.58) * mm]});
            skFitSpline(sketch, "E455", {"points": [v(120.87, -4.58) * mm, v(120.73, -4.66) * mm, v(120.6, -4.74) * mm, v(120.42, -4.83) * mm]});
            skFitSpline(sketch, "E456", {"points": [v(120.42, -4.83) * mm, v(120.64, -4.94) * mm, v(120.83, -5.03) * mm, v(121.02, -5.12) * mm]});
            skFitSpline(sketch, "E457", {"points": [v(121.02, -5.12) * mm, v(121.11, -5.16) * mm, v(121.2, -5.15) * mm, v(121.3, -5.1) * mm]});
            skFitSpline(sketch, "E458", {"points": [v(121.3, -5.1) * mm, v(122.49, -4.54) * mm, v(123.69, -3.97) * mm, v(124.88, -3.4) * mm]});
            skFitSpline(sketch, "E459", {"points": [v(124.88, -3.4) * mm, v(125.03, -3.33) * mm, v(125.16, -3.23) * mm, v(125.28, -3.14) * mm]});
            skFitSpline(sketch, "E460", {"points": [v(125.28, -3.14) * mm, v(125.49, -2.97) * mm, v(125.77, -2.97) * mm, v(125.96, -3.16) * mm]});
            skFitSpline(sketch, "E461", {"points": [v(125.96, -3.16) * mm, v(126.14, -3.34) * mm, v(126.18, -3.64) * mm, v(126, -3.83) * mm]});
            skFitSpline(sketch, "E462", {"points": [v(126, -3.83) * mm, v(125.89, -3.95) * mm, v(125.74, -4.05) * mm, v(125.6, -4.12) * mm]});
            skFitSpline(sketch, "E463", {"points": [v(125.6, -4.12) * mm, v(124.82, -4.5) * mm, v(124.03, -4.89) * mm, v(123.25, -5.26) * mm]});
            skFitSpline(sketch, "E464", {"points": [v(123.25, -5.26) * mm, v(122.74, -5.5) * mm, v(122.22, -5.75) * mm, v(121.7, -5.99) * mm]});
            skFitSpline(sketch, "E465", {"points": [v(121.7, -5.99) * mm, v(121.63, -6.03) * mm, v(121.55, -6.06) * mm, v(121.45, -6.1) * mm]});
            skFitSpline(sketch, "E466", {"points": [v(121.45, -6.1) * mm, v(121.72, -6.83) * mm, v(121.99, -7.55) * mm, v(122.24, -8.27) * mm]});
            skFitSpline(sketch, "E467", {"points": [v(122.24, -8.27) * mm, v(122.5, -9) * mm, v(122.75, -9.75) * mm, v(123, -10.49) * mm]});
            skFitSpline(sketch, "E468", {"points": [v(123, -10.49) * mm, v(123.04, -10.6) * mm, v(123.06, -10.72) * mm, v(123.07, -10.84) * mm]});
            skFitSpline(sketch, "E469", {"points": [v(123.07, -10.84) * mm, v(123.08, -11.14) * mm, v(122.86, -11.37) * mm, v(122.57, -11.37) * mm]});
            skFitSpline(sketch, "E470", {"points": [v(122.57, -11.37) * mm, v(122.29, -11.37) * mm, v(122.09, -11.17) * mm, v(122.06, -10.87) * mm]});
            skFitSpline(sketch, "E471", {"points": [v(122.06, -10.87) * mm, v(122.05, -10.74) * mm, v(122.02, -10.6) * mm, v(121.98, -10.48) * mm]});
            skFitSpline(sketch, "E472", {"points": [v(121.98, -10.48) * mm, v(121.58, -9.33) * mm, v(121.17, -8.2) * mm, v(120.76, -7.05) * mm]});
            skFitSpline(sketch, "E473", {"points": [v(120.76, -7.05) * mm, v(120.74, -7) * mm, v(120.7, -6.95) * mm, v(120.7, -6.9) * mm]});
            skFitSpline(sketch, "E474", {"points": [v(120.7, -6.9) * mm, v(120.66, -6.6) * mm, v(120.47, -6.46) * mm, v(120.2, -6.4) * mm]});
            skFitSpline(sketch, "E475", {"points": [v(120.2, -6.4) * mm, v(120.1, -6.36) * mm, v(119.99, -6.33) * mm, v(119.84, -6.28) * mm]});
            skFitSpline(sketch, "E476", {"points": [v(119.84, -6.28) * mm, v(119.87, -6.4) * mm, v(119.88, -6.47) * mm, v(119.9, -6.55) * mm]});
            skFitSpline(sketch, "E477", {"points": [v(119.9, -6.55) * mm, v(120.1, -7.25) * mm, v(120.32, -7.95) * mm, v(120.52, -8.64) * mm]});
            skFitSpline(sketch, "E478", {"points": [v(120.52, -8.64) * mm, v(120.55, -8.77) * mm, v(120.58, -8.9) * mm, v(120.59, -9.04) * mm]});
            skFitSpline(sketch, "E479", {"points": [v(120.59, -9.04) * mm, v(120.6, -9.3) * mm, v(120.44, -9.49) * mm, v(120.19, -9.53) * mm]});
            skFitSpline(sketch, "E480", {"points": [v(120.19, -9.53) * mm, v(119.96, -9.58) * mm, v(119.73, -9.44) * mm, v(119.65, -9.2) * mm]});
            skFitSpline(sketch, "E481", {"points": [v(119.65, -9.2) * mm, v(119.6, -9.02) * mm, v(119.56, -8.84) * mm, v(119.5, -8.66) * mm]});
            skFitSpline(sketch, "E482", {"points": [v(119.5, -8.66) * mm, v(119.3, -7.95) * mm, v(119.1, -7.24) * mm, v(118.89, -6.52) * mm]});
            skFitSpline(sketch, "E483", {"points": [v(118.89, -6.52) * mm, v(118.83, -6.33) * mm, v(118.8, -6.13) * mm, v(118.76, -5.94) * mm]});
            skFitSpline(sketch, "E484", {"points": [v(118.76, -5.94) * mm, v(118.74, -5.85) * mm, v(118.72, -5.77) * mm, v(118.62, -5.73) * mm]});
            skFitSpline(sketch, "E485", {"points": [v(118.62, -5.73) * mm, v(118.3, -5.58) * mm, v(117.97, -5.43) * mm, v(117.6, -5.26) * mm]});
            skFitSpline(sketch, "E486", {"points": [v(117.6, -5.26) * mm, v(117.65, -5.46) * mm, v(117.68, -5.62) * mm, v(117.71, -5.77) * mm]});
            skFitSpline(sketch, "E487", {"points": [v(117.71, -5.77) * mm, v(117.76, -6) * mm, v(117.8, -6.24) * mm, v(117.84, -6.47) * mm]});
            skFitSpline(sketch, "E488", {"points": [v(117.84, -6.47) * mm, v(117.86, -6.57) * mm, v(117.89, -6.66) * mm, v(117.91, -6.75) * mm]});
            skFitSpline(sketch, "E489", {"points": [v(117.91, -6.75) * mm, v(117.97, -6.97) * mm, v(118.04, -7.18) * mm, v(118.07, -7.4) * mm]});
            skFitSpline(sketch, "E490", {"points": [v(118.07, -7.4) * mm, v(118.12, -7.7) * mm, v(117.9, -8.01) * mm, v(117.59, -8.07) * mm]});
            skFitSpline(sketch, "E491", {"points": [v(117.59, -8.07) * mm, v(117.26, -8.14) * mm, v(116.92, -8.17) * mm, v(116.6, -8.22) * mm]});
            skFitSpline(sketch, "E492", {"points": [v(116.6, -8.22) * mm, v(115.99, -8.3) * mm, v(115.38, -8.38) * mm, v(114.77, -8.46) * mm]});
            skFitSpline(sketch, "E493", {"points": [v(114.77, -8.46) * mm, v(114.75, -8.47) * mm, v(114.73, -8.48) * mm, v(114.68, -8.5) * mm]});
            skFitSpline(sketch, "E494", {"points": [v(114.68, -8.5) * mm, v(114.66, -8.7) * mm, v(114.63, -8.93) * mm, v(114.6, -9.15) * mm]});
            skFitSpline(sketch, "E495", {"points": [v(114.6, -9.15) * mm, v(114.52, -9.68) * mm, v(114.45, -10.2) * mm, v(114.37, -10.73) * mm]});
            skFitSpline(sketch, "E496", {"points": [v(114.37, -10.73) * mm, v(114.35, -10.92) * mm, v(114.33, -11.1) * mm, v(114.3, -11.28) * mm]});
            skFitSpline(sketch, "E497", {"points": [v(114.3, -11.28) * mm, v(114.25, -11.68) * mm, v(113.91, -11.93) * mm, v(113.52, -11.85) * mm]});
            skFitSpline(sketch, "E498", {"points": [v(113.52, -11.85) * mm, v(113.31, -11.8) * mm, v(113.12, -11.74) * mm, v(112.92, -11.69) * mm]});
            skFitSpline(sketch, "E499", {"points": [v(112.92, -11.69) * mm, v(112.86, -11.67) * mm, v(112.81, -11.64) * mm, v(112.76, -11.64) * mm]});
            skFitSpline(sketch, "E500", {"points": [v(112.76, -11.64) * mm, v(112.36, -11.64) * mm, v(112, -11.5) * mm, v(111.6, -11.43) * mm]});
            skFitSpline(sketch, "E501", {"points": [v(111.6, -11.43) * mm, v(111.59, -11.42) * mm, v(111.56, -11.43) * mm, v(111.5, -11.43) * mm]});
            skFitSpline(sketch, "E502", {"points": [v(111.5, -11.43) * mm, v(111.55, -11.54) * mm, v(111.58, -11.64) * mm, v(111.62, -11.74) * mm]});
            skFitSpline(sketch, "E503", {"points": [v(111.62, -11.74) * mm, v(111.72, -11.96) * mm, v(111.83, -12.18) * mm, v(111.93, -12.4) * mm]});
            skFitSpline(sketch, "E504", {"points": [v(111.93, -12.4) * mm, v(111.96, -12.48) * mm, v(112.02, -12.53) * mm, v(112.12, -12.55) * mm]});
            skFitSpline(sketch, "E505", {"points": [v(112.12, -12.55) * mm, v(113.12, -12.73) * mm, v(114.06, -13.12) * mm, v(115.05, -13.35) * mm]});
            skFitSpline(sketch, "E506", {"points": [v(115.05, -13.35) * mm, v(115.16, -13.38) * mm, v(115.27, -13.4) * mm, v(115.37, -13.44) * mm]});
            skFitSpline(sketch, "E507", {"points": [v(115.37, -13.44) * mm, v(115.64, -13.52) * mm, v(115.79, -13.75) * mm, v(115.73, -14) * mm]});
            skFitSpline(sketch, "E508", {"points": [v(115.73, -14) * mm, v(115.69, -14.25) * mm, v(115.45, -14.42) * mm, v(115.18, -14.4) * mm]});
            skFitSpline(sketch, "E509", {"points": [v(115.18, -14.4) * mm, v(115.1, -14.38) * mm, v(115.02, -14.36) * mm, v(114.95, -14.34) * mm]});
            skFitSpline(sketch, "E510", {"points": [v(114.95, -14.34) * mm, v(114.27, -14.14) * mm, v(113.6, -13.94) * mm, v(112.93, -13.74) * mm]});
            skFitSpline(sketch, "E511", {"points": [v(112.93, -13.74) * mm, v(112.8, -13.7) * mm, v(112.67, -13.67) * mm, v(112.51, -13.63) * mm]});
            skFitSpline(sketch, "E512", {"points": [v(112.51, -13.63) * mm, v(112.54, -13.89) * mm, v(112.64, -14.1) * mm, v(112.74, -14.32) * mm]});
            skFitSpline(sketch, "E513", {"points": [v(112.74, -14.32) * mm, v(112.76, -14.37) * mm, v(112.83, -14.4) * mm, v(112.89, -14.42) * mm]});
            skFitSpline(sketch, "E514", {"points": [v(112.89, -14.42) * mm, v(113.95, -14.8) * mm, v(115, -15.19) * mm, v(116.07, -15.57) * mm]});
            skFitSpline(sketch, "E515", {"points": [v(116.07, -15.57) * mm, v(116.28, -15.65) * mm, v(116.49, -15.72) * mm, v(116.7, -15.78) * mm]});
            skFitSpline(sketch, "E516", {"points": [v(116.7, -15.78) * mm, v(116.82, -15.82) * mm, v(116.95, -15.84) * mm, v(117.08, -15.85) * mm]});
            skFitSpline(sketch, "E517", {"points": [v(117.08, -15.85) * mm, v(117.39, -15.88) * mm, v(117.58, -16.08) * mm, v(117.57, -16.38) * mm]});
            skFitSpline(sketch, "E518", {"points": [v(117.57, -16.38) * mm, v(117.56, -16.67) * mm, v(117.35, -16.88) * mm, v(117.05, -16.85) * mm]});
            skFitSpline(sketch, "E519", {"points": [v(117.05, -16.85) * mm, v(116.81, -16.83) * mm, v(116.58, -16.77) * mm, v(116.35, -16.7) * mm]});
            skFitSpline(sketch, "E520", {"points": [v(116.35, -16.7) * mm, v(115.22, -16.3) * mm, v(114.1, -15.89) * mm, v(112.97, -15.48) * mm]});
            skFitSpline(sketch, "E521", {"points": [v(112.97, -15.48) * mm, v(112.76, -15.4) * mm, v(112.55, -15.34) * mm, v(112.32, -15.26) * mm]});
            skFitSpline(sketch, "E522", {"points": [v(112.32, -15.26) * mm, v(112.24, -15.42) * mm, v(112.15, -15.58) * mm, v(112.07, -15.74) * mm]});
            skFitSpline(sketch, "E523", {"points": [v(112.07, -15.74) * mm, v(111.55, -16.85) * mm, v(111.03, -17.96) * mm, v(110.5, -19.08) * mm]});
            skFitSpline(sketch, "E524", {"points": [v(110.5, -19.08) * mm, v(110.4, -19.28) * mm, v(110.28, -19.49) * mm, v(110.15, -19.68) * mm]});
            skFitSpline(sketch, "E525", {"points": [v(110.15, -19.68) * mm, v(109.97, -19.93) * mm, v(109.7, -19.98) * mm, v(109.45, -19.82) * mm]});
            skFitSpline(sketch, "E526", {"points": [v(109.45, -19.82) * mm, v(109.2, -19.65) * mm, v(109.15, -19.32) * mm, v(109.34, -19.07) * mm]});
            skFitSpline(sketch, "E527", {"points": [v(109.34, -19.07) * mm, v(109.44, -18.95) * mm, v(109.54, -18.82) * mm, v(109.6, -18.68) * mm]});
            skFitSpline(sketch, "E528", {"points": [v(109.6, -18.68) * mm, v(110.13, -17.58) * mm, v(110.65, -16.47) * mm, v(111.17, -15.37) * mm]});
            skFitSpline(sketch, "E529", {"points": [v(111.17, -15.37) * mm, v(111.18, -15.35) * mm, v(111.18, -15.33) * mm, v(111.2, -15.32) * mm]});
            skFitSpline(sketch, "E530", {"points": [v(111.2, -15.32) * mm, v(111.43, -15.03) * mm, v(111.34, -14.75) * mm, v(111.17, -14.47) * mm]});
            skFitSpline(sketch, "E531", {"points": [v(111.17, -14.47) * mm, v(111.13, -14.41) * mm, v(111.1, -14.35) * mm, v(111.07, -14.3) * mm]});
            skFitSpline(sketch, "E532", {"points": [v(111.07, -14.3) * mm, v(111.07, -14.29) * mm, v(111.05, -14.28) * mm, v(111.01, -14.26) * mm]});
            skFitSpline(sketch, "E533", {"points": [v(111.01, -14.26) * mm, v(110.95, -14.37) * mm, v(110.89, -14.48) * mm, v(110.83, -14.59) * mm]});
            skFitSpline(sketch, "E534", {"points": [v(110.83, -14.59) * mm, v(110.49, -15.21) * mm, v(110.15, -15.83) * mm, v(109.8, -16.46) * mm]});
            skFitSpline(sketch, "E535", {"points": [v(109.8, -16.46) * mm, v(109.72, -16.62) * mm, v(109.63, -16.76) * mm, v(109.46, -16.84) * mm]});
            skFitSpline(sketch, "E536", {"points": [v(109.46, -16.84) * mm, v(109.28, -16.92) * mm, v(109.13, -16.88) * mm, v(108.98, -16.77) * mm]});
            skFitSpline(sketch, "E537", {"points": [v(108.98, -16.77) * mm, v(108.84, -16.66) * mm, v(108.77, -16.51) * mm, v(108.8, -16.33) * mm]});
            skFitSpline(sketch, "E538", {"points": [v(108.8, -16.33) * mm, v(108.8, -16.26) * mm, v(108.83, -16.2) * mm, v(108.87, -16.13) * mm]});
            skFitSpline(sketch, "E539", {"points": [v(108.87, -16.13) * mm, v(109.28, -15.38) * mm, v(109.69, -14.63) * mm, v(110.1, -13.88) * mm]});
            skFitSpline(sketch, "E540", {"points": [v(110.1, -13.88) * mm, v(110.23, -13.66) * mm, v(110.37, -13.44) * mm, v(110.52, -13.23) * mm]});
            skFitSpline(sketch, "E541", {"points": [v(110.52, -13.23) * mm, v(110.59, -13.13) * mm, v(110.6, -13.04) * mm, v(110.55, -12.93) * mm]});
            skFitSpline(sketch, "E542", {"points": [v(110.55, -12.93) * mm, v(110.43, -12.61) * mm, v(110.34, -12.28) * mm, v(110.16, -11.96) * mm]});
            skFitSpline(sketch, "E543", {"points": [v(110.16, -11.96) * mm, v(110.07, -12.1) * mm, v(109.99, -12.23) * mm, v(109.9, -12.36) * mm]});
            skFitSpline(sketch, "E544", {"points": [v(109.9, -12.36) * mm, v(109.85, -12.45) * mm, v(109.81, -12.55) * mm, v(109.75, -12.63) * mm]});
            skFitSpline(sketch, "E545", {"points": [v(109.75, -12.63) * mm, v(109.47, -12.94) * mm, v(109.28, -13.31) * mm, v(109.08, -13.67) * mm]});
            skFitSpline(sketch, "E546", {"points": [v(109.08, -13.67) * mm, v(108.9, -14) * mm, v(108.37, -14.08) * mm, v(108.08, -13.86) * mm]});
            skFitSpline(sketch, "E547", {"points": [v(108.08, -13.86) * mm, v(107.43, -13.33) * mm, v(106.75, -12.83) * mm, v(106.09, -12.32) * mm]});
            skFitSpline(sketch, "E548", {"points": [v(106.09, -12.32) * mm, v(106.01, -12.26) * mm, v(105.93, -12.21) * mm, v(105.85, -12.15) * mm]});
            skFitSpline(sketch, "E549", {"points": [v(105.85, -12.15) * mm, v(105.78, -12.2) * mm, v(105.7, -12.24) * mm, v(105.65, -12.29) * mm]});
            skFitSpline(sketch, "E550", {"points": [v(105.65, -12.29) * mm, v(104.97, -12.8) * mm, v(104.29, -13.3) * mm, v(103.63, -13.83) * mm]});
            skFitSpline(sketch, "E551", {"points": [v(103.63, -13.83) * mm, v(103.32, -14.09) * mm, v(102.76, -14.02) * mm, v(102.6, -13.66) * mm]});
            skFitSpline(sketch, "E552", {"points": [v(102.6, -13.66) * mm, v(102.52, -13.48) * mm, v(102.41, -13.31) * mm, v(102.31, -13.14) * mm]});
            skFitSpline(sketch, "E553", {"points": [v(102.31, -13.14) * mm, v(102.3, -13.13) * mm, v(102.3, -13.12) * mm, v(102.3, -13.12) * mm]});
            skFitSpline(sketch, "E554", {"points": [v(102.3, -13.12) * mm, v(102.04, -12.74) * mm, v(101.78, -12.36) * mm, v(101.5, -11.95) * mm]});
            skFitSpline(sketch, "E555", {"points": [v(101.5, -11.95) * mm, v(101.37, -12.3) * mm, v(101.24, -12.64) * mm, v(101.12, -12.97) * mm]});
            skFitSpline(sketch, "E556", {"points": [v(101.12, -12.97) * mm, v(101.09, -13.06) * mm, v(101.1, -13.13) * mm, v(101.15, -13.2) * mm]});
            skFitSpline(sketch, "E557", {"points": [v(101.15, -13.2) * mm, v(101.73, -14.03) * mm, v(102.12, -14.98) * mm, v(102.65, -15.84) * mm]});
            skFitSpline(sketch, "E558", {"points": [v(102.65, -15.84) * mm, v(102.72, -15.95) * mm, v(102.78, -16.05) * mm, v(102.83, -16.16) * mm]});
            skFitSpline(sketch, "E559", {"points": [v(102.83, -16.16) * mm, v(102.98, -16.46) * mm, v(102.84, -16.76) * mm, v(102.52, -16.86) * mm]});
            skFitSpline(sketch, "E560", {"points": [v(102.52, -16.86) * mm, v(102.33, -16.92) * mm, v(102.18, -16.84) * mm, v(102.05, -16.7) * mm]});
            skFitSpline(sketch, "E561", {"points": [v(102.05, -16.7) * mm, v(101.98, -16.63) * mm, v(101.92, -16.54) * mm, v(101.88, -16.45) * mm]});
            skFitSpline(sketch, "E562", {"points": [v(101.88, -16.45) * mm, v(101.53, -15.82) * mm, v(101.19, -15.19) * mm, v(100.84, -14.56) * mm]});
            skFitSpline(sketch, "E563", {"points": [v(100.84, -14.56) * mm, v(100.79, -14.45) * mm, v(100.73, -14.35) * mm, v(100.65, -14.22) * mm]});
            skFitSpline(sketch, "E564", {"points": [v(100.65, -14.22) * mm, v(100.53, -14.45) * mm, v(100.43, -14.64) * mm, v(100.35, -14.84) * mm]});
            skFitSpline(sketch, "E565", {"points": [v(100.35, -14.84) * mm, v(100.33, -14.9) * mm, v(100.34, -15) * mm, v(100.37, -15.07) * mm]});
            skFitSpline(sketch, "E566", {"points": [v(100.37, -15.07) * mm, v(100.84, -16.08) * mm, v(101.31, -17.1) * mm, v(101.79, -18.1) * mm]});
            skFitSpline(sketch, "E567", {"points": [v(101.79, -18.1) * mm, v(101.89, -18.31) * mm, v(102, -18.52) * mm, v(102.1, -18.72) * mm]});
            skFitSpline(sketch, "E568", {"points": [v(102.1, -18.72) * mm, v(102.17, -18.84) * mm, v(102.24, -18.96) * mm, v(102.33, -19.06) * mm]});
            skFitSpline(sketch, "E569", {"points": [v(102.33, -19.06) * mm, v(102.5, -19.27) * mm, v(102.5, -19.56) * mm, v(102.32, -19.75) * mm]});
            skFitSpline(sketch, "E570", {"points": [v(102.32, -19.75) * mm, v(102.11, -19.96) * mm, v(101.82, -19.97) * mm, v(101.61, -19.76) * mm]});
            skFitSpline(sketch, "E571", {"points": [v(101.61, -19.76) * mm, v(101.5, -19.65) * mm, v(101.42, -19.52) * mm, v(101.35, -19.39) * mm]});
            skFitSpline(sketch, "E572", {"points": [v(101.35, -19.39) * mm, v(100.97, -18.6) * mm, v(100.6, -17.82) * mm, v(100.22, -17.04) * mm]});
            skFitSpline(sketch, "E573", {"points": [v(100.22, -17.04) * mm, v(99.93, -16.45) * mm, v(99.66, -15.86) * mm, v(99.38, -15.26) * mm]});
            skFitSpline(sketch, "E574", {"points": [v(99.38, -15.26) * mm, v(99.2, -15.32) * mm, v(99.02, -15.37) * mm, v(98.85, -15.43) * mm]});
            skFitSpline(sketch, "E575", {"points": [v(98.85, -15.43) * mm, v(97.69, -15.85) * mm, v(96.53, -16.26) * mm, v(95.37, -16.68) * mm]});
            skFitSpline(sketch, "E576", {"points": [v(95.37, -16.68) * mm, v(95.22, -16.73) * mm, v(95.05, -16.78) * mm, v(94.9, -16.82) * mm]});
            skFitSpline(sketch, "E577", {"points": [v(94.9, -16.82) * mm, v(94.8, -16.84) * mm, v(94.7, -16.85) * mm, v(94.6, -16.85) * mm]});
            skFitSpline(sketch, "E578", {"points": [v(94.6, -16.85) * mm, v(94.34, -16.85) * mm, v(94.13, -16.66) * mm, v(94.11, -16.4) * mm]});
            skFitSpline(sketch, "E579", {"points": [v(94.11, -16.4) * mm, v(94.09, -16.14) * mm, v(94.26, -15.88) * mm, v(94.52, -15.87) * mm]});
            skFitSpline(sketch, "E580", {"points": [v(94.52, -15.87) * mm, v(94.86, -15.85) * mm, v(95.16, -15.72) * mm, v(95.46, -15.62) * mm]});
            skFitSpline(sketch, "E581", {"points": [v(95.46, -15.62) * mm, v(96.45, -15.27) * mm, v(97.43, -14.9) * mm, v(98.42, -14.55) * mm]});
            skFitSpline(sketch, "E582", {"points": [v(98.42, -14.55) * mm, v(98.45, -14.54) * mm, v(98.5, -14.52) * mm, v(98.53, -14.51) * mm]});
            skFitSpline(sketch, "E583", {"points": [v(98.53, -14.51) * mm, v(98.9, -14.47) * mm, v(99.05, -14.22) * mm, v(99.12, -13.9) * mm]});
            skFitSpline(sketch, "E584", {"points": [v(99.12, -13.9) * mm, v(99.14, -13.82) * mm, v(99.16, -13.74) * mm, v(99.2, -13.61) * mm]});
            skFitSpline(sketch, "E585", {"points": [v(18, -11.43) * mm, v(18, -11.43) * mm, v(18.03, -11.43) * mm, v(18.04, -11.43) * mm]});
            skFitSpline(sketch, "E586", {"points": [v(18.04, -11.43) * mm, v(18.12, -11.24) * mm, v(18.2, -11.04) * mm, v(18.27, -10.85) * mm]});
            skFitSpline(sketch, "E587", {"points": [v(18.27, -10.85) * mm, v(18.56, -10.14) * mm, v(18.84, -9.43) * mm, v(19.13, -8.72) * mm]});
            skFitSpline(sketch, "E588", {"points": [v(19.13, -8.72) * mm, v(19.38, -8.1) * mm, v(19.63, -7.48) * mm, v(19.9, -6.86) * mm]});
            skFitSpline(sketch, "E589", {"points": [v(19.9, -6.86) * mm, v(20.08, -6.43) * mm, v(20.24, -5.99) * mm, v(20.53, -5.6) * mm]});
            skFitSpline(sketch, "E590", {"points": [v(20.53, -5.6) * mm, v(20.69, -5.38) * mm, v(20.89, -5.25) * mm, v(21.16, -5.24) * mm]});
            skFitSpline(sketch, "E591", {"points": [v(21.16, -5.24) * mm, v(21.4, -5.24) * mm, v(21.62, -5.24) * mm, v(21.85, -5.27) * mm]});
            skFitSpline(sketch, "E592", {"points": [v(21.85, -5.27) * mm, v(22.57, -5.35) * mm, v(23.3, -5.43) * mm, v(24.01, -5.52) * mm]});
            skFitSpline(sketch, "E593", {"points": [v(24.01, -5.52) * mm, v(24.34, -5.56) * mm, v(24.66, -5.61) * mm, v(24.98, -5.66) * mm]});
            skFitSpline(sketch, "E594", {"points": [v(24.98, -5.66) * mm, v(25.5, -5.73) * mm, v(26.02, -5.8) * mm, v(26.54, -5.87) * mm]});
            skFitSpline(sketch, "E595", {"points": [v(26.54, -5.87) * mm, v(26.84, -5.92) * mm, v(27.14, -5.96) * mm, v(27.43, -6) * mm]});
            skFitSpline(sketch, "E596", {"points": [v(27.43, -6) * mm, v(27.44, -6) * mm, v(27.45, -5.98) * mm, v(27.46, -5.96) * mm]});
            skFitSpline(sketch, "E597", {"points": [v(27.46, -5.96) * mm, v(27.41, -5.9) * mm, v(27.36, -5.83) * mm, v(27.31, -5.76) * mm]});
            skFitSpline(sketch, "E598", {"points": [v(27.31, -5.76) * mm, v(26.98, -5.35) * mm, v(26.64, -4.94) * mm, v(26.32, -4.53) * mm]});
            skFitSpline(sketch, "E599", {"points": [v(26.32, -4.53) * mm, v(25.68, -3.7) * mm, v(25.04, -2.87) * mm, v(24.41, -2.04) * mm]});
            skFitSpline(sketch, "E600", {"points": [v(24.41, -2.04) * mm, v(24.14, -1.67) * mm, v(23.83, -1.31) * mm, v(23.65, -0.88) * mm]});
            skFitSpline(sketch, "E601", {"points": [v(23.65, -0.88) * mm, v(23.56, -0.65) * mm, v(23.56, -0.42) * mm, v(23.65, -0.18) * mm]});
            skFitSpline(sketch, "E602", {"points": [v(23.65, -0.18) * mm, v(23.78, 0.13) * mm, v(24, 0.4) * mm, v(24.19, 0.66) * mm]});
            skFitSpline(sketch, "E603", {"points": [v(24.19, 0.66) * mm, v(24.5, 1.09) * mm, v(24.84, 1.5) * mm, v(25.16, 1.91) * mm]});
            skFitSpline(sketch, "E604", {"points": [v(25.16, 1.91) * mm, v(25.52, 2.39) * mm, v(25.87, 2.87) * mm, v(26.24, 3.35) * mm]});
            skFitSpline(sketch, "E605", {"points": [v(26.24, 3.35) * mm, v(26.6, 3.82) * mm, v(26.98, 4.28) * mm, v(27.36, 4.75) * mm]});
            skFitSpline(sketch, "E606", {"points": [v(27.36, 4.75) * mm, v(27.4, 4.8) * mm, v(27.43, 4.86) * mm, v(27.48, 4.94) * mm]});
            skFitSpline(sketch, "E607", {"points": [v(27.48, 4.94) * mm, v(27.28, 4.91) * mm, v(27.12, 4.9) * mm, v(26.96, 4.87) * mm]});
            skFitSpline(sketch, "E608", {"points": [v(26.96, 4.87) * mm, v(26.16, 4.75) * mm, v(25.35, 4.64) * mm, v(24.55, 4.52) * mm]});
            skFitSpline(sketch, "E609", {"points": [v(24.55, 4.52) * mm, v(23.96, 4.44) * mm, v(23.37, 4.36) * mm, v(22.77, 4.29) * mm]});
            skFitSpline(sketch, "E610", {"points": [v(22.77, 4.29) * mm, v(22.23, 4.22) * mm, v(21.69, 4.12) * mm, v(21.14, 4.17) * mm]});
            skFitSpline(sketch, "E611", {"points": [v(21.14, 4.17) * mm, v(20.88, 4.2) * mm, v(20.7, 4.32) * mm, v(20.53, 4.52) * mm]});
            skFitSpline(sketch, "E612", {"points": [v(20.53, 4.52) * mm, v(20.32, 4.8) * mm, v(20.19, 5.13) * mm, v(20.05, 5.45) * mm]});
            skFitSpline(sketch, "E613", {"points": [v(20.05, 5.45) * mm, v(19.84, 5.92) * mm, v(19.66, 6.41) * mm, v(19.46, 6.89) * mm]});
            skFitSpline(sketch, "E614", {"points": [v(19.46, 6.89) * mm, v(19.25, 7.4) * mm, v(19.01, 7.91) * mm, v(18.8, 8.43) * mm]});
            skFitSpline(sketch, "E615", {"points": [v(18.8, 8.43) * mm, v(18.57, 9) * mm, v(18.35, 9.59) * mm, v(18.12, 10.17) * mm]});
            skFitSpline(sketch, "E616", {"points": [v(18.12, 10.17) * mm, v(18.1, 10.23) * mm, v(18.06, 10.3) * mm, v(18.01, 10.4) * mm]});
            skFitSpline(sketch, "E617", {"points": [v(18.01, 10.4) * mm, v(17.97, 10.3) * mm, v(17.95, 10.25) * mm, v(17.93, 10.2) * mm]});
            skFitSpline(sketch, "E618", {"points": [v(17.93, 10.2) * mm, v(17.75, 9.73) * mm, v(17.58, 9.27) * mm, v(17.4, 8.8) * mm]});
            skFitSpline(sketch, "E619", {"points": [v(17.4, 8.8) * mm, v(17.03, 7.93) * mm, v(16.67, 7.06) * mm, v(16.3, 6.18) * mm]});
            skFitSpline(sketch, "E620", {"points": [v(16.3, 6.18) * mm, v(16.06, 5.62) * mm, v(15.86, 5.03) * mm, v(15.5, 4.53) * mm]});
            skFitSpline(sketch, "E621", {"points": [v(15.5, 4.53) * mm, v(15.35, 4.31) * mm, v(15.14, 4.2) * mm, v(14.88, 4.17) * mm]});
            skFitSpline(sketch, "E622", {"points": [v(14.88, 4.17) * mm, v(14.65, 4.14) * mm, v(14.42, 4.16) * mm, v(14.2, 4.19) * mm]});
            skFitSpline(sketch, "E623", {"points": [v(14.2, 4.19) * mm, v(13.71, 4.24) * mm, v(13.23, 4.29) * mm, v(12.75, 4.35) * mm]});
            skFitSpline(sketch, "E624", {"points": [v(12.75, 4.35) * mm, v(12.22, 4.41) * mm, v(11.7, 4.5) * mm, v(11.16, 4.57) * mm]});
            skFitSpline(sketch, "E625", {"points": [v(11.16, 4.57) * mm, v(10.6, 4.65) * mm, v(10.06, 4.72) * mm, v(9.5, 4.8) * mm]});
            skFitSpline(sketch, "E626", {"points": [v(9.5, 4.8) * mm, v(9.2, 4.84) * mm, v(8.9, 4.9) * mm, v(8.54, 4.94) * mm]});
            skFitSpline(sketch, "E627", {"points": [v(8.54, 4.94) * mm, v(8.62, 4.83) * mm, v(8.67, 4.76) * mm, v(8.72, 4.7) * mm]});
            skFitSpline(sketch, "E628", {"points": [v(8.72, 4.7) * mm, v(9, 4.34) * mm, v(9.3, 4) * mm, v(9.57, 3.65) * mm]});
            skFitSpline(sketch, "E629", {"points": [v(9.57, 3.65) * mm, v(10.26, 2.76) * mm, v(10.95, 1.87) * mm, v(11.62, 0.97) * mm]});
            skFitSpline(sketch, "E630", {"points": [v(11.62, 0.97) * mm, v(11.9, 0.6) * mm, v(12.2, 0.24) * mm, v(12.38, -0.19) * mm]});
            skFitSpline(sketch, "E631", {"points": [v(12.38, -0.19) * mm, v(12.48, -0.42) * mm, v(12.48, -0.64) * mm, v(12.38, -0.88) * mm]});
            skFitSpline(sketch, "E632", {"points": [v(12.38, -0.88) * mm, v(12.26, -1.2) * mm, v(12.05, -1.46) * mm, v(11.85, -1.73) * mm]});
            skFitSpline(sketch, "E633", {"points": [v(11.85, -1.73) * mm, v(11.54, -2.15) * mm, v(11.2, -2.56) * mm, v(10.88, -2.98) * mm]});
            skFitSpline(sketch, "E634", {"points": [v(10.88, -2.98) * mm, v(10.52, -3.45) * mm, v(10.17, -3.94) * mm, v(9.8, -4.41) * mm]});
            skFitSpline(sketch, "E635", {"points": [v(9.8, -4.41) * mm, v(9.44, -4.89) * mm, v(9.05, -5.35) * mm, v(8.68, -5.82) * mm]});
            skFitSpline(sketch, "E636", {"points": [v(8.68, -5.82) * mm, v(8.64, -5.87) * mm, v(8.62, -5.92) * mm, v(8.56, -6.01) * mm]});
            skFitSpline(sketch, "E637", {"points": [v(8.56, -6.01) * mm, v(8.8, -5.98) * mm, v(9, -5.95) * mm, v(9.2, -5.92) * mm]});
            skFitSpline(sketch, "E638", {"points": [v(9.2, -5.92) * mm, v(9.77, -5.84) * mm, v(10.33, -5.74) * mm, v(10.89, -5.67) * mm]});
            skFitSpline(sketch, "E639", {"points": [v(10.89, -5.67) * mm, v(11.39, -5.6) * mm, v(11.89, -5.55) * mm, v(12.38, -5.5) * mm]});
            skFitSpline(sketch, "E640", {"points": [v(12.38, -5.5) * mm, v(13.08, -5.4) * mm, v(13.77, -5.3) * mm, v(14.47, -5.23) * mm]});
            skFitSpline(sketch, "E641", {"points": [v(14.47, -5.23) * mm, v(14.74, -5.2) * mm, v(15, -5.21) * mm, v(15.26, -5.36) * mm]});
            skFitSpline(sketch, "E642", {"points": [v(15.26, -5.36) * mm, v(15.47, -5.49) * mm, v(15.59, -5.69) * mm, v(15.7, -5.89) * mm]});
            skFitSpline(sketch, "E643", {"points": [v(15.7, -5.89) * mm, v(15.88, -6.22) * mm, v(16.02, -6.58) * mm, v(16.16, -6.93) * mm]});
            skFitSpline(sketch, "E644", {"points": [v(16.16, -6.93) * mm, v(16.38, -7.46) * mm, v(16.59, -7.98) * mm, v(16.8, -8.5) * mm]});
            skFitSpline(sketch, "E645", {"points": [v(16.8, -8.5) * mm, v(17.1, -9.22) * mm, v(17.39, -9.92) * mm, v(17.68, -10.63) * mm]});
            skFitSpline(sketch, "E646", {"points": [v(17.68, -10.63) * mm, v(17.79, -10.9) * mm, v(17.89, -11.17) * mm, v(18, -11.43) * mm]});
            skFitSpline(sketch, "E647", {"points": [v(11.76, -12.58) * mm, v(11.56, -12.93) * mm, v(11.36, -13.24) * mm, v(11.23, -13.59) * mm]});
            skFitSpline(sketch, "E648", {"points": [v(11.23, -13.59) * mm, v(11.19, -13.7) * mm, v(11.21, -13.86) * mm, v(11.23, -13.99) * mm]});
            skFitSpline(sketch, "E649", {"points": [v(11.23, -13.99) * mm, v(11.37, -14.9) * mm, v(11.52, -15.82) * mm, v(11.67, -16.73) * mm]});
            skFitSpline(sketch, "E650", {"points": [v(11.67, -16.73) * mm, v(11.7, -16.99) * mm, v(11.62, -17.2) * mm, v(11.41, -17.3) * mm]});
            skFitSpline(sketch, "E651", {"points": [v(11.41, -17.3) * mm, v(11.13, -17.43) * mm, v(10.82, -17.29) * mm, v(10.74, -16.97) * mm]});
            skFitSpline(sketch, "E652", {"points": [v(10.74, -16.97) * mm, v(10.67, -16.72) * mm, v(10.64, -16.45) * mm, v(10.6, -16.2) * mm]});
            skFitSpline(sketch, "E653", {"points": [v(10.6, -16.2) * mm, v(10.52, -15.76) * mm, v(10.45, -15.33) * mm, v(10.34, -14.88) * mm]});
            skFitSpline(sketch, "E654", {"points": [v(10.34, -14.88) * mm, v(10.26, -15) * mm, v(10.18, -15.13) * mm, v(10.1, -15.26) * mm]});
            skFitSpline(sketch, "E655", {"points": [v(10.1, -15.26) * mm, v(9.91, -15.59) * mm, v(9.72, -15.91) * mm, v(9.52, -16.24) * mm]});
            skFitSpline(sketch, "E656", {"points": [v(9.52, -16.24) * mm, v(9.38, -16.49) * mm, v(9.24, -16.73) * mm, v(9.11, -16.97) * mm]});
            skFitSpline(sketch, "E657", {"points": [v(9.11, -16.97) * mm, v(8.96, -17.25) * mm, v(8.69, -17.35) * mm, v(8.43, -17.22) * mm]});
            skFitSpline(sketch, "E658", {"points": [v(8.43, -17.22) * mm, v(8.16, -17.09) * mm, v(8.06, -16.8) * mm, v(8.2, -16.53) * mm]});
            skFitSpline(sketch, "E659", {"points": [v(8.2, -16.53) * mm, v(8.23, -16.47) * mm, v(8.27, -16.43) * mm, v(8.3, -16.37) * mm]});
            skFitSpline(sketch, "E660", {"points": [v(8.3, -16.37) * mm, v(8.68, -15.7) * mm, v(9.05, -15.03) * mm, v(9.44, -14.33) * mm]});
            skFitSpline(sketch, "E661", {"points": [v(9.44, -14.33) * mm, v(9.35, -14.36) * mm, v(9.28, -14.37) * mm, v(9.22, -14.4) * mm]});
            skFitSpline(sketch, "E662", {"points": [v(9.22, -14.4) * mm, v(8.68, -14.6) * mm, v(8.15, -14.8) * mm, v(7.6, -15) * mm]});
            skFitSpline(sketch, "E663", {"points": [v(7.6, -15) * mm, v(7.51, -15.04) * mm, v(7.4, -15.06) * mm, v(7.3, -15.06) * mm]});
            skFitSpline(sketch, "E664", {"points": [v(7.3, -15.06) * mm, v(7.05, -15.08) * mm, v(6.87, -14.94) * mm, v(6.8, -14.7) * mm]});
            skFitSpline(sketch, "E665", {"points": [v(6.8, -14.7) * mm, v(6.76, -14.5) * mm, v(6.86, -14.29) * mm, v(7.06, -14.18) * mm]});
            skFitSpline(sketch, "E666", {"points": [v(7.06, -14.18) * mm, v(7.1, -14.15) * mm, v(7.16, -14.13) * mm, v(7.21, -14.1) * mm]});
            skFitSpline(sketch, "E667", {"points": [v(7.21, -14.1) * mm, v(8.1, -13.77) * mm, v(8.99, -13.42) * mm, v(9.87, -13.08) * mm]});
            skFitSpline(sketch, "E668", {"points": [v(9.87, -13.08) * mm, v(10, -13.03) * mm, v(10.12, -12.96) * mm, v(10.19, -12.84) * mm]});
            skFitSpline(sketch, "E669", {"points": [v(10.19, -12.84) * mm, v(10.36, -12.57) * mm, v(10.53, -12.3) * mm, v(10.67, -11.98) * mm]});
            skFitSpline(sketch, "E670", {"points": [v(10.67, -11.98) * mm, v(10.6, -12) * mm, v(10.53, -12.03) * mm, v(10.46, -12.06) * mm]});
            skFitSpline(sketch, "E671", {"points": [v(10.46, -12.06) * mm, v(9.87, -12.32) * mm, v(9.29, -12.59) * mm, v(8.7, -12.83) * mm]});
            skFitSpline(sketch, "E672", {"points": [v(8.7, -12.83) * mm, v(8.43, -12.94) * mm, v(8.14, -13.02) * mm, v(7.85, -13.08) * mm]});
            skFitSpline(sketch, "E673", {"points": [v(7.85, -13.08) * mm, v(7.5, -13.16) * mm, v(7.23, -12.88) * mm, v(7.28, -12.54) * mm]});
            skFitSpline(sketch, "E674", {"points": [v(7.28, -12.54) * mm, v(7.3, -12.33) * mm, v(7.44, -12.2) * mm, v(7.63, -12.15) * mm]});
            skFitSpline(sketch, "E675", {"points": [v(7.63, -12.15) * mm, v(8.5, -11.94) * mm, v(9.28, -11.48) * mm, v(10.11, -11.15) * mm]});
            skFitSpline(sketch, "E676", {"points": [v(10.11, -11.15) * mm, v(10.59, -10.96) * mm, v(11.06, -10.77) * mm, v(11.53, -10.57) * mm]});
            skFitSpline(sketch, "E677", {"points": [v(11.53, -10.57) * mm, v(11.6, -10.55) * mm, v(11.66, -10.5) * mm, v(11.7, -10.45) * mm]});
            skFitSpline(sketch, "E678", {"points": [v(11.7, -10.45) * mm, v(11.8, -10.3) * mm, v(11.9, -10.14) * mm, v(12.02, -9.94) * mm]});
            skFitSpline(sketch, "E679", {"points": [v(12.02, -9.94) * mm, v(11.72, -10.05) * mm, v(11.47, -10.13) * mm, v(11.22, -10.23) * mm]});
            skFitSpline(sketch, "E680", {"points": [v(11.22, -10.23) * mm, v(10.68, -10.44) * mm, v(10.15, -10.66) * mm, v(9.62, -10.87) * mm]});
            skFitSpline(sketch, "E681", {"points": [v(9.62, -10.87) * mm, v(9.51, -10.91) * mm, v(9.4, -10.93) * mm, v(9.3, -10.94) * mm]});
            skFitSpline(sketch, "E682", {"points": [v(9.3, -10.94) * mm, v(9.07, -10.94) * mm, v(8.92, -10.83) * mm, v(8.84, -10.61) * mm]});
            skFitSpline(sketch, "E683", {"points": [v(8.84, -10.61) * mm, v(8.78, -10.44) * mm, v(8.84, -10.23) * mm, v(9, -10.1) * mm]});
            skFitSpline(sketch, "E684", {"points": [v(9, -10.1) * mm, v(9.07, -10.05) * mm, v(9.15, -10.01) * mm, v(9.23, -9.98) * mm]});
            skFitSpline(sketch, "E685", {"points": [v(9.23, -9.98) * mm, v(9.95, -9.7) * mm, v(10.67, -9.42) * mm, v(11.4, -9.12) * mm]});
            skFitSpline(sketch, "E686", {"points": [v(11.4, -9.12) * mm, v(11.84, -8.94) * mm, v(12.28, -8.72) * mm, v(12.73, -8.53) * mm]});
            skFitSpline(sketch, "E687", {"points": [v(12.73, -8.53) * mm, v(12.9, -8.45) * mm, v(12.94, -8.27) * mm, v(13.06, -8.09) * mm]});
            skFitSpline(sketch, "E688", {"points": [v(13.06, -8.09) * mm, v(12.94, -8.13) * mm, v(12.87, -8.15) * mm, v(12.8, -8.18) * mm]});
            skFitSpline(sketch, "E689", {"points": [v(12.8, -8.18) * mm, v(12.36, -8.35) * mm, v(11.92, -8.53) * mm, v(11.48, -8.7) * mm]});
            skFitSpline(sketch, "E690", {"points": [v(11.48, -8.7) * mm, v(11.39, -8.74) * mm, v(11.28, -8.76) * mm, v(11.18, -8.76) * mm]});
            skFitSpline(sketch, "E691", {"points": [v(11.18, -8.76) * mm, v(10.98, -8.75) * mm, v(10.8, -8.59) * mm, v(10.75, -8.4) * mm]});
            skFitSpline(sketch, "E692", {"points": [v(10.75, -8.4) * mm, v(10.7, -8.2) * mm, v(10.79, -7.99) * mm, v(10.97, -7.88) * mm]});
            skFitSpline(sketch, "E693", {"points": [v(10.97, -7.88) * mm, v(11.04, -7.83) * mm, v(11.12, -7.8) * mm, v(11.2, -7.77) * mm]});
            skFitSpline(sketch, "E694", {"points": [v(11.2, -7.77) * mm, v(11.84, -7.52) * mm, v(12.47, -7.28) * mm, v(13.1, -7.04) * mm]});
            skFitSpline(sketch, "E695", {"points": [v(13.1, -7.04) * mm, v(13.19, -7) * mm, v(13.27, -6.96) * mm, v(13.35, -6.93) * mm]});
            skFitSpline(sketch, "E696", {"points": [v(13.35, -6.93) * mm, v(13.5, -6.87) * mm, v(13.66, -6.82) * mm, v(13.86, -6.74) * mm]});
            skFitSpline(sketch, "E697", {"points": [v(13.86, -6.74) * mm, v(13.93, -6.62) * mm, v(14.01, -6.44) * mm, v(14.12, -6.23) * mm]});
            skFitSpline(sketch, "E698", {"points": [v(14.12, -6.23) * mm, v(13.79, -6.27) * mm, v(13.5, -6.3) * mm, v(13.2, -6.35) * mm]});
            skFitSpline(sketch, "E699", {"points": [v(13.2, -6.35) * mm, v(12.47, -6.44) * mm, v(11.74, -6.53) * mm, v(11, -6.63) * mm]});
            skFitSpline(sketch, "E700", {"points": [v(11, -6.63) * mm, v(10.46, -6.7) * mm, v(9.92, -6.8) * mm, v(9.37, -6.88) * mm]});
            skFitSpline(sketch, "E701", {"points": [v(9.37, -6.88) * mm, v(8.86, -6.95) * mm, v(8.36, -7.1) * mm, v(7.84, -7.1) * mm]});
            skFitSpline(sketch, "E702", {"points": [v(7.84, -7.1) * mm, v(7.71, -7.1) * mm, v(7.65, -7.18) * mm, v(7.6, -7.26) * mm]});
            skFitSpline(sketch, "E703", {"points": [v(7.6, -7.26) * mm, v(7.4, -7.53) * mm, v(7.22, -7.82) * mm, v(7.03, -8.1) * mm]});
            skFitSpline(sketch, "E704", {"points": [v(7.03, -8.1) * mm, v(6.87, -8.33) * mm, v(6.7, -8.56) * mm, v(6.54, -8.8) * mm]});
            skFitSpline(sketch, "E705", {"points": [v(6.54, -8.8) * mm, v(6.38, -9.03) * mm, v(6.23, -9.27) * mm, v(6.08, -9.5) * mm]});
            skFitSpline(sketch, "E706", {"points": [v(6.08, -9.5) * mm, v(5.83, -9.9) * mm, v(5.58, -10.28) * mm, v(5.32, -10.67) * mm]});
            skFitSpline(sketch, "E707", {"points": [v(5.32, -10.67) * mm, v(5.24, -10.8) * mm, v(5.12, -10.9) * mm, v(4.96, -10.93) * mm]});
            skFitSpline(sketch, "E708", {"points": [v(4.96, -10.93) * mm, v(4.76, -10.98) * mm, v(4.57, -10.9) * mm, v(4.45, -10.75) * mm]});
            skFitSpline(sketch, "E709", {"points": [v(4.45, -10.75) * mm, v(4.33, -10.58) * mm, v(4.33, -10.37) * mm, v(4.45, -10.18) * mm]});
            skFitSpline(sketch, "E710", {"points": [v(4.45, -10.18) * mm, v(4.58, -10) * mm, v(4.72, -9.8) * mm, v(4.85, -9.62) * mm]});
            skFitSpline(sketch, "E711", {"points": [v(4.85, -9.62) * mm, v(5, -9.4) * mm, v(5.15, -9.18) * mm, v(5.27, -8.95) * mm]});
            skFitSpline(sketch, "E712", {"points": [v(5.27, -8.95) * mm, v(5.47, -8.55) * mm, v(5.77, -8.23) * mm, v(6.01, -7.86) * mm]});
            skFitSpline(sketch, "E713", {"points": [v(6.01, -7.86) * mm, v(6.14, -7.67) * mm, v(6.27, -7.47) * mm, v(6.42, -7.25) * mm]});
            skFitSpline(sketch, "E714", {"points": [v(6.42, -7.25) * mm, v(6.18, -7.25) * mm, v(5.98, -7.24) * mm, v(5.79, -7.25) * mm]});
            skFitSpline(sketch, "E715", {"points": [v(5.79, -7.25) * mm, v(5.5, -7.27) * mm, v(5.22, -7.32) * mm, v(4.93, -7.35) * mm]});
            skFitSpline(sketch, "E716", {"points": [v(4.93, -7.35) * mm, v(4.75, -7.36) * mm, v(4.57, -7.35) * mm, v(4.38, -7.36) * mm]});
            skFitSpline(sketch, "E717", {"points": [v(4.38, -7.36) * mm, v(4.08, -7.37) * mm, v(3.77, -7.39) * mm, v(3.46, -7.4) * mm]});
            skFitSpline(sketch, "E718", {"points": [v(3.46, -7.4) * mm, v(3.26, -7.42) * mm, v(3.06, -7.46) * mm, v(2.86, -7.47) * mm]});
            skFitSpline(sketch, "E719", {"points": [v(2.86, -7.47) * mm, v(2.64, -7.48) * mm, v(2.42, -7.32) * mm, v(2.36, -7.1) * mm]});
            skFitSpline(sketch, "E720", {"points": [v(2.36, -7.1) * mm, v(2.3, -6.88) * mm, v(2.4, -6.66) * mm, v(2.6, -6.55) * mm]});
            skFitSpline(sketch, "E721", {"points": [v(2.6, -6.55) * mm, v(2.68, -6.51) * mm, v(2.77, -6.48) * mm, v(2.86, -6.47) * mm]});
            skFitSpline(sketch, "E722", {"points": [v(2.86, -6.47) * mm, v(3.31, -6.44) * mm, v(3.76, -6.38) * mm, v(4.22, -6.4) * mm]});
            skFitSpline(sketch, "E723", {"points": [v(4.22, -6.4) * mm, v(4.67, -6.4) * mm, v(5.12, -6.34) * mm, v(5.57, -6.3) * mm]});
            skFitSpline(sketch, "E724", {"points": [v(5.57, -6.3) * mm, v(5.98, -6.26) * mm, v(6.4, -6.25) * mm, v(6.81, -6.22) * mm]});
            skFitSpline(sketch, "E725", {"points": [v(6.81, -6.22) * mm, v(6.9, -6.22) * mm, v(6.99, -6.2) * mm, v(7.07, -6.18) * mm]});
            skFitSpline(sketch, "E726", {"points": [v(7.07, -6.18) * mm, v(7.13, -6.17) * mm, v(7.2, -6.13) * mm, v(7.22, -6.09) * mm]});
            skFitSpline(sketch, "E727", {"points": [v(7.22, -6.09) * mm, v(7.6, -5.49) * mm, v(8.11, -5) * mm, v(8.54, -4.44) * mm]});
            skFitSpline(sketch, "E728", {"points": [v(8.54, -4.44) * mm, v(8.91, -3.96) * mm, v(9.28, -3.48) * mm, v(9.65, -3) * mm]});
            skFitSpline(sketch, "E729", {"points": [v(9.65, -3) * mm, v(9.88, -2.7) * mm, v(10.12, -2.4) * mm, v(10.36, -2.1) * mm]});
            skFitSpline(sketch, "E730", {"points": [v(10.36, -2.1) * mm, v(10.61, -1.76) * mm, v(10.86, -1.42) * mm, v(11.13, -1.06) * mm]});
            skFitSpline(sketch, "E731", {"points": [v(11.13, -1.06) * mm, v(10.91, -1.04) * mm, v(10.72, -1.03) * mm, v(10.58, -1.02) * mm]});
            skFitSpline(sketch, "E732", {"points": [v(10.58, -1.02) * mm, v(10.4, -1.17) * mm, v(10.24, -1.3) * mm, v(10.08, -1.43) * mm]});
            skFitSpline(sketch, "E733", {"points": [v(10.08, -1.43) * mm, v(9.92, -1.56) * mm, v(9.77, -1.7) * mm, v(9.6, -1.83) * mm]});
            skFitSpline(sketch, "E734", {"points": [v(9.6, -1.83) * mm, v(9.15, -2.19) * mm, v(8.7, -2.54) * mm, v(8.25, -2.9) * mm]});
            skFitSpline(sketch, "E735", {"points": [v(8.25, -2.9) * mm, v(8.17, -2.96) * mm, v(8.06, -3) * mm, v(7.97, -3.02) * mm]});
            skFitSpline(sketch, "E736", {"points": [v(7.97, -3.02) * mm, v(7.77, -3.05) * mm, v(7.6, -2.97) * mm, v(7.5, -2.8) * mm]});
            skFitSpline(sketch, "E737", {"points": [v(7.5, -2.8) * mm, v(7.4, -2.63) * mm, v(7.4, -2.4) * mm, v(7.53, -2.25) * mm]});
            skFitSpline(sketch, "E738", {"points": [v(7.53, -2.25) * mm, v(7.6, -2.18) * mm, v(7.67, -2.12) * mm, v(7.74, -2.06) * mm]});
            skFitSpline(sketch, "E739", {"points": [v(7.74, -2.06) * mm, v(8.1, -1.77) * mm, v(8.46, -1.5) * mm, v(8.82, -1.21) * mm]});
            skFitSpline(sketch, "E740", {"points": [v(8.82, -1.21) * mm, v(8.87, -1.17) * mm, v(8.91, -1.13) * mm, v(9, -1.06) * mm]});
            skFitSpline(sketch, "E741", {"points": [v(9, -1.06) * mm, v(8.75, -1.04) * mm, v(8.57, -1.02) * mm, v(8.39, -1.16) * mm]});
            skFitSpline(sketch, "E742", {"points": [v(8.39, -1.16) * mm, v(7.4, -1.9) * mm, v(6.4, -2.63) * mm, v(5.46, -3.41) * mm]});
            skFitSpline(sketch, "E743", {"points": [v(5.46, -3.41) * mm, v(5.4, -3.46) * mm, v(5.33, -3.51) * mm, v(5.26, -3.55) * mm]});
            skFitSpline(sketch, "E744", {"points": [v(5.26, -3.55) * mm, v(5.06, -3.65) * mm, v(4.84, -3.6) * mm, v(4.7, -3.43) * mm]});
            skFitSpline(sketch, "E745", {"points": [v(4.7, -3.43) * mm, v(4.54, -3.27) * mm, v(4.52, -3.05) * mm, v(4.65, -2.86) * mm]});
            skFitSpline(sketch, "E746", {"points": [v(4.65, -2.86) * mm, v(4.7, -2.78) * mm, v(4.77, -2.72) * mm, v(4.85, -2.66) * mm]});
            skFitSpline(sketch, "E747", {"points": [v(4.85, -2.66) * mm, v(5.26, -2.33) * mm, v(5.67, -2) * mm, v(6.09, -1.67) * mm]});
            skFitSpline(sketch, "E748", {"points": [v(6.09, -1.67) * mm, v(6.35, -1.47) * mm, v(6.6, -1.26) * mm, v(6.9, -1.01) * mm]});
            skFitSpline(sketch, "E749", {"points": [v(6.9, -1.01) * mm, v(6.63, -1.03) * mm, v(6.41, -1.04) * mm, v(6.2, -1.05) * mm]});
            skFitSpline(sketch, "E750", {"points": [v(6.2, -1.05) * mm, v(6.17, -1.05) * mm, v(6.14, -1.08) * mm, v(6.11, -1.1) * mm]});
            skFitSpline(sketch, "E751", {"points": [v(6.11, -1.1) * mm, v(5.36, -1.67) * mm, v(4.6, -2.25) * mm, v(3.85, -2.83) * mm]});
            skFitSpline(sketch, "E752", {"points": [v(3.85, -2.83) * mm, v(3.48, -3.1) * mm, v(3.1, -3.34) * mm, v(2.8, -3.7) * mm]});
            skFitSpline(sketch, "E753", {"points": [v(2.8, -3.7) * mm, v(2.68, -3.83) * mm, v(2.52, -3.9) * mm, v(2.34, -3.86) * mm]});
            skFitSpline(sketch, "E754", {"points": [v(2.34, -3.86) * mm, v(1.98, -3.8) * mm, v(1.8, -3.37) * mm, v(2.06, -3.08) * mm]});
            skFitSpline(sketch, "E755", {"points": [v(2.06, -3.08) * mm, v(2.25, -2.85) * mm, v(2.47, -2.64) * mm, v(2.71, -2.46) * mm]});
            skFitSpline(sketch, "E756", {"points": [v(2.71, -2.46) * mm, v(3.21, -2.07) * mm, v(3.73, -1.7) * mm, v(4.24, -1.33) * mm]});
            skFitSpline(sketch, "E757", {"points": [v(4.24, -1.33) * mm, v(4.3, -1.28) * mm, v(4.36, -1.23) * mm, v(4.46, -1.16) * mm]});
            skFitSpline(sketch, "E758", {"points": [v(4.46, -1.16) * mm, v(4.37, -1.15) * mm, v(4.32, -1.14) * mm, v(4.27, -1.14) * mm]});
            skFitSpline(sketch, "E759", {"points": [v(4.27, -1.14) * mm, v(3.96, -1.15) * mm, v(3.65, -1.16) * mm, v(3.34, -1.18) * mm]});
            skFitSpline(sketch, "E760", {"points": [v(3.34, -1.18) * mm, v(3.27, -1.2) * mm, v(3.2, -1.23) * mm, v(3.13, -1.28) * mm]});
            skFitSpline(sketch, "E761", {"points": [v(3.13, -1.28) * mm, v(2.38, -1.88) * mm, v(1.62, -2.5) * mm, v(0.87, -3.1) * mm]});
            skFitSpline(sketch, "E762", {"points": [v(0.87, -3.1) * mm, v(0.77, -3.17) * mm, v(0.65, -3.24) * mm, v(0.53, -3.26) * mm]});
            skFitSpline(sketch, "E763", {"points": [v(0.53, -3.26) * mm, v(0.3, -3.3) * mm, v(0.14, -3.2) * mm, v(0.04, -3) * mm]});
            skFitSpline(sketch, "E764", {"points": [v(0.04, -3) * mm, v(-0.06, -2.82) * mm, v(-0.03, -2.63) * mm, v(0.13, -2.46) * mm]});
            skFitSpline(sketch, "E765", {"points": [v(0.13, -2.46) * mm, v(0.25, -2.34) * mm, v(0.38, -2.23) * mm, v(0.5, -2.12) * mm]});
            skFitSpline(sketch, "E766", {"points": [v(0.5, -2.12) * mm, v(0.88, -1.81) * mm, v(1.26, -1.5) * mm, v(1.64, -1.2) * mm]});
            skFitSpline(sketch, "E767", {"points": [v(1.64, -1.2) * mm, v(1.68, -1.16) * mm, v(1.72, -1.12) * mm, v(1.8, -1.05) * mm]});
            skFitSpline(sketch, "E768", {"points": [v(1.8, -1.05) * mm, v(1.58, -1.05) * mm, v(1.4, -1.05) * mm, v(1.23, -1.05) * mm]});
            skFitSpline(sketch, "E769", {"points": [v(1.23, -1.05) * mm, v(0.86, -1.04) * mm, v(0.48, -1.02) * mm, v(0.11, -1.02) * mm]});
            skFitSpline(sketch, "E770", {"points": [v(0.11, -1.02) * mm, v(-0.13, -1.01) * mm, v(-0.38, -1.02) * mm, v(-0.62, -1.04) * mm]});
            skFitSpline(sketch, "E771", {"points": [v(-0.62, -1.04) * mm, v(-1.01, -1.07) * mm, v(-1.24, -0.85) * mm, v(-1.22, -0.47) * mm]});
            skFitSpline(sketch, "E772", {"points": [v(-1.22, -0.47) * mm, v(-1.2, -0.23) * mm, v(-1.03, -0.05) * mm, v(-0.8, -0.04) * mm]});
            skFitSpline(sketch, "E773", {"points": [v(-0.8, -0.04) * mm, v(-0.69, -0.03) * mm, v(-0.58, -0.04) * mm, v(-0.48, -0.04) * mm]});
            skFitSpline(sketch, "E774", {"points": [v(-0.48, -0.04) * mm, v(-0.02, -0.03) * mm, v(0.44, -0.01) * mm, v(0.9, 0) * mm]});
            skFitSpline(sketch, "E775", {"points": [v(0.9, 0) * mm, v(1.14, 0) * mm, v(1.37, -0.02) * mm, v(1.6, -0.03) * mm]});
            skFitSpline(sketch, "E776", {"points": [v(1.6, -0.03) * mm, v(1.65, -0.04) * mm, v(1.7, -0.04) * mm, v(1.8, -0.04) * mm]});
            skFitSpline(sketch, "E777", {"points": [v(1.8, -0.04) * mm, v(1.74, 0.04) * mm, v(1.7, 0.08) * mm, v(1.66, 0.1) * mm]});
            skFitSpline(sketch, "E778", {"points": [v(1.66, 0.1) * mm, v(1.21, 0.48) * mm, v(0.76, 0.85) * mm, v(0.31, 1.22) * mm]});
            skFitSpline(sketch, "E779", {"points": [v(0.31, 1.22) * mm, v(0.24, 1.28) * mm, v(0.18, 1.33) * mm, v(0.12, 1.4) * mm]});
            skFitSpline(sketch, "E780", {"points": [v(0.12, 1.4) * mm, v(-0.06, 1.6) * mm, v(-0.06, 1.86) * mm, v(0.12, 2.05) * mm]});
            skFitSpline(sketch, "E781", {"points": [v(0.12, 2.05) * mm, v(0.28, 2.23) * mm, v(0.54, 2.26) * mm, v(0.75, 2.12) * mm]});
            skFitSpline(sketch, "E782", {"points": [v(0.75, 2.12) * mm, v(0.87, 2.04) * mm, v(0.97, 1.93) * mm, v(1.08, 1.84) * mm]});
            skFitSpline(sketch, "E783", {"points": [v(1.08, 1.84) * mm, v(1.77, 1.3) * mm, v(2.46, 0.75) * mm, v(3.14, 0.2) * mm]});
            skFitSpline(sketch, "E784", {"points": [v(3.14, 0.2) * mm, v(3.3, 0.07) * mm, v(3.48, 0.07) * mm, v(3.66, 0.06) * mm]});
            skFitSpline(sketch, "E785", {"points": [v(3.66, 0.06) * mm, v(3.92, 0.05) * mm, v(4.17, 0.06) * mm, v(4.48, 0.06) * mm]});
            skFitSpline(sketch, "E786", {"points": [v(4.48, 0.06) * mm, v(4.4, 0.13) * mm, v(4.34, 0.19) * mm, v(4.28, 0.23) * mm]});
            skFitSpline(sketch, "E787", {"points": [v(4.28, 0.23) * mm, v(3.75, 0.62) * mm, v(3.22, 1) * mm, v(2.7, 1.4) * mm]});
            skFitSpline(sketch, "E788", {"points": [v(2.7, 1.4) * mm, v(2.47, 1.57) * mm, v(2.27, 1.78) * mm, v(2.07, 1.99) * mm]});
            skFitSpline(sketch, "E789", {"points": [v(2.07, 1.99) * mm, v(1.89, 2.2) * mm, v(1.9, 2.48) * mm, v(2.08, 2.66) * mm]});
            skFitSpline(sketch, "E790", {"points": [v(2.08, 2.66) * mm, v(2.27, 2.84) * mm, v(2.57, 2.86) * mm, v(2.76, 2.66) * mm]});
            skFitSpline(sketch, "E791", {"points": [v(2.76, 2.66) * mm, v(3.33, 2.05) * mm, v(4.06, 1.64) * mm, v(4.71, 1.12) * mm]});
            skFitSpline(sketch, "E792", {"points": [v(4.71, 1.12) * mm, v(5.18, 0.76) * mm, v(5.64, 0.4) * mm, v(6.11, 0.03) * mm]});
            skFitSpline(sketch, "E793", {"points": [v(6.11, 0.03) * mm, v(6.14, 0) * mm, v(6.18, -0.03) * mm, v(6.2, -0.03) * mm]});
            skFitSpline(sketch, "E794", {"points": [v(6.2, -0.03) * mm, v(6.42, -0.03) * mm, v(6.63, -0.03) * mm, v(6.88, -0.03) * mm]});
            skFitSpline(sketch, "E795", {"points": [v(6.88, -0.03) * mm, v(6.56, 0.22) * mm, v(6.27, 0.46) * mm, v(5.98, 0.69) * mm]});
            skFitSpline(sketch, "E796", {"points": [v(5.98, 0.69) * mm, v(5.6, 1) * mm, v(5.21, 1.3) * mm, v(4.83, 1.6) * mm]});
            skFitSpline(sketch, "E797", {"points": [v(4.83, 1.6) * mm, v(4.77, 1.65) * mm, v(4.71, 1.7) * mm, v(4.67, 1.77) * mm]});
            skFitSpline(sketch, "E798", {"points": [v(4.67, 1.77) * mm, v(4.52, 1.96) * mm, v(4.54, 2.18) * mm, v(4.69, 2.36) * mm]});
            skFitSpline(sketch, "E799", {"points": [v(4.69, 2.36) * mm, v(4.84, 2.53) * mm, v(5.07, 2.58) * mm, v(5.28, 2.47) * mm]});
            skFitSpline(sketch, "E800", {"points": [v(5.28, 2.47) * mm, v(5.34, 2.44) * mm, v(5.4, 2.4) * mm, v(5.45, 2.35) * mm]});
            skFitSpline(sketch, "E801", {"points": [v(5.45, 2.35) * mm, v(6.06, 1.87) * mm, v(6.66, 1.38) * mm, v(7.27, 0.9) * mm]});
            skFitSpline(sketch, "E802", {"points": [v(7.27, 0.9) * mm, v(7.66, 0.6) * mm, v(8.08, 0.32) * mm, v(8.48, 0.03) * mm]});
            skFitSpline(sketch, "E803", {"points": [v(8.48, 0.03) * mm, v(8.63, -0.08) * mm, v(8.8, -0.02) * mm, v(9, -0.03) * mm]});
            skFitSpline(sketch, "E804", {"points": [v(9, -0.03) * mm, v(8.92, 0.04) * mm, v(8.88, 0.09) * mm, v(8.84, 0.12) * mm]});
            skFitSpline(sketch, "E805", {"points": [v(8.84, 0.12) * mm, v(8.46, 0.42) * mm, v(8.08, 0.71) * mm, v(7.71, 1.02) * mm]});
            skFitSpline(sketch, "E806", {"points": [v(7.71, 1.02) * mm, v(7.6, 1.1) * mm, v(7.52, 1.21) * mm, v(7.46, 1.33) * mm]});
            skFitSpline(sketch, "E807", {"points": [v(7.46, 1.33) * mm, v(7.39, 1.5) * mm, v(7.43, 1.68) * mm, v(7.57, 1.81) * mm]});
            skFitSpline(sketch, "E808", {"points": [v(7.57, 1.81) * mm, v(7.7, 1.95) * mm, v(7.87, 2) * mm, v(8.05, 1.93) * mm]});
            skFitSpline(sketch, "E809", {"points": [v(8.05, 1.93) * mm, v(8.14, 1.9) * mm, v(8.23, 1.85) * mm, v(8.3, 1.79) * mm]});
            skFitSpline(sketch, "E810", {"points": [v(8.3, 1.79) * mm, v(8.84, 1.35) * mm, v(9.38, 0.91) * mm, v(9.92, 0.47) * mm]});
            skFitSpline(sketch, "E811", {"points": [v(9.92, 0.47) * mm, v(9.99, 0.42) * mm, v(10.07, 0.37) * mm, v(10.13, 0.32) * mm]});
            skFitSpline(sketch, "E812", {"points": [v(10.13, 0.32) * mm, v(10.27, 0.21) * mm, v(10.4, 0.1) * mm, v(10.56, -0.04) * mm]});
            skLineSegment(sketch, "E813", {"start": v(10.56, -0.04) * mm, "end": v(11.12, -0.04) * mm});
            skFitSpline(sketch, "E814", {"points": [v(11.12, -0.04) * mm, v(11.08, 0.03) * mm, v(11.07, 0.08) * mm, v(11.04, 0.12) * mm]});
            skFitSpline(sketch, "E815", {"points": [v(11.04, 0.12) * mm, v(10.74, 0.5) * mm, v(10.44, 0.88) * mm, v(10.14, 1.27) * mm]});
            skFitSpline(sketch, "E816", {"points": [v(10.14, 1.27) * mm, v(9.71, 1.84) * mm, v(9.3, 2.42) * mm, v(8.86, 2.97) * mm]});
            skFitSpline(sketch, "E817", {"points": [v(8.86, 2.97) * mm, v(8.5, 3.43) * mm, v(8.1, 3.87) * mm, v(7.74, 4.32) * mm]});
            skFitSpline(sketch, "E818", {"points": [v(7.74, 4.32) * mm, v(7.58, 4.51) * mm, v(7.42, 4.72) * mm, v(7.29, 4.93) * mm]});
            skFitSpline(sketch, "E819", {"points": [v(7.29, 4.93) * mm, v(7.2, 5.07) * mm, v(7.1, 5.13) * mm, v(6.94, 5.14) * mm]});
            skFitSpline(sketch, "E820", {"points": [v(6.94, 5.14) * mm, v(6.7, 5.16) * mm, v(6.46, 5.17) * mm, v(6.22, 5.2) * mm]});
            skFitSpline(sketch, "E821", {"points": [v(6.22, 5.2) * mm, v(5.75, 5.24) * mm, v(5.29, 5.29) * mm, v(4.82, 5.32) * mm]});
            skFitSpline(sketch, "E822", {"points": [v(4.82, 5.32) * mm, v(4.61, 5.33) * mm, v(4.4, 5.32) * mm, v(4.2, 5.32) * mm]});
            skFitSpline(sketch, "E823", {"points": [v(4.2, 5.32) * mm, v(3.76, 5.34) * mm, v(3.33, 5.36) * mm, v(2.9, 5.4) * mm]});
            skFitSpline(sketch, "E824", {"points": [v(2.9, 5.4) * mm, v(2.82, 5.4) * mm, v(2.73, 5.43) * mm, v(2.65, 5.46) * mm]});
            skFitSpline(sketch, "E825", {"points": [v(2.65, 5.46) * mm, v(2.43, 5.56) * mm, v(2.31, 5.78) * mm, v(2.36, 6) * mm]});
            skFitSpline(sketch, "E826", {"points": [v(2.36, 6) * mm, v(2.4, 6.24) * mm, v(2.62, 6.4) * mm, v(2.86, 6.4) * mm]});
            skFitSpline(sketch, "E827", {"points": [v(2.86, 6.4) * mm, v(3.12, 6.38) * mm, v(3.37, 6.34) * mm, v(3.63, 6.33) * mm]});
            skFitSpline(sketch, "E828", {"points": [v(3.63, 6.33) * mm, v(3.91, 6.3) * mm, v(4.2, 6.31) * mm, v(4.48, 6.3) * mm]});
            skFitSpline(sketch, "E829", {"points": [v(4.48, 6.3) * mm, v(4.8, 6.27) * mm, v(5.1, 6.24) * mm, v(5.41, 6.22) * mm]});
            skFitSpline(sketch, "E830", {"points": [v(5.41, 6.22) * mm, v(5.73, 6.2) * mm, v(6.06, 6.17) * mm, v(6.38, 6.14) * mm]});
            skFitSpline(sketch, "E831", {"points": [v(6.38, 6.14) * mm, v(6.39, 6.16) * mm, v(6.4, 6.18) * mm, v(6.4, 6.2) * mm]});
            skFitSpline(sketch, "E832", {"points": [v(6.4, 6.2) * mm, v(6.28, 6.39) * mm, v(6.16, 6.58) * mm, v(6.03, 6.77) * mm]});
            skFitSpline(sketch, "E833", {"points": [v(6.03, 6.77) * mm, v(5.99, 6.83) * mm, v(5.94, 6.9) * mm, v(5.89, 6.96) * mm]});
            skFitSpline(sketch, "E834", {"points": [v(5.89, 6.96) * mm, v(5.59, 7.34) * mm, v(5.35, 7.75) * mm, v(5.11, 8.17) * mm]});
            skFitSpline(sketch, "E835", {"points": [v(5.11, 8.17) * mm, v(4.93, 8.48) * mm, v(4.7, 8.77) * mm, v(4.48, 9.07) * mm]});
            skFitSpline(sketch, "E836", {"points": [v(4.48, 9.07) * mm, v(4.26, 9.37) * mm, v(4.37, 9.76) * mm, v(4.72, 9.86) * mm]});
            skFitSpline(sketch, "E837", {"points": [v(4.72, 9.86) * mm, v(4.87, 9.9) * mm, v(5.02, 9.87) * mm, v(5.15, 9.77) * mm]});
            skFitSpline(sketch, "E838", {"points": [v(5.15, 9.77) * mm, v(5.21, 9.72) * mm, v(5.28, 9.66) * mm, v(5.33, 9.58) * mm]});
            skFitSpline(sketch, "E839", {"points": [v(5.33, 9.58) * mm, v(5.6, 9.16) * mm, v(5.87, 8.74) * mm, v(6.15, 8.32) * mm]});
            skFitSpline(sketch, "E840", {"points": [v(6.15, 8.32) * mm, v(6.3, 8.07) * mm, v(6.48, 7.83) * mm, v(6.64, 7.59) * mm]});
            skFitSpline(sketch, "E841", {"points": [v(6.64, 7.59) * mm, v(6.91, 7.19) * mm, v(7.2, 6.8) * mm, v(7.44, 6.39) * mm]});
            skFitSpline(sketch, "E842", {"points": [v(7.44, 6.39) * mm, v(7.6, 6.12) * mm, v(7.8, 6) * mm, v(8.12, 6) * mm]});
            skFitSpline(sketch, "E843", {"points": [v(8.12, 6) * mm, v(8.38, 6) * mm, v(8.63, 5.92) * mm, v(8.9, 5.88) * mm]});
            skFitSpline(sketch, "E844", {"points": [v(8.9, 5.88) * mm, v(9.43, 5.8) * mm, v(9.96, 5.7) * mm, v(10.5, 5.63) * mm]});
            skFitSpline(sketch, "E845", {"points": [v(10.5, 5.63) * mm, v(11.01, 5.55) * mm, v(11.53, 5.5) * mm, v(12.04, 5.44) * mm]});
            skFitSpline(sketch, "E846", {"points": [v(12.04, 5.44) * mm, v(12.64, 5.36) * mm, v(13.24, 5.27) * mm, v(13.84, 5.2) * mm]});
            skFitSpline(sketch, "E847", {"points": [v(13.84, 5.2) * mm, v(13.92, 5.18) * mm, v(14, 5.18) * mm, v(14.12, 5.18) * mm]});
            skFitSpline(sketch, "E848", {"points": [v(14.12, 5.18) * mm, v(14.02, 5.37) * mm, v(13.93, 5.54) * mm, v(13.87, 5.67) * mm]});
            skFitSpline(sketch, "E849", {"points": [v(13.87, 5.67) * mm, v(13.66, 5.74) * mm, v(13.5, 5.8) * mm, v(13.34, 5.86) * mm]});
            skFitSpline(sketch, "E850", {"points": [v(13.34, 5.86) * mm, v(13.11, 5.95) * mm, v(12.89, 6.03) * mm, v(12.67, 6.11) * mm]});
            skFitSpline(sketch, "E851", {"points": [v(12.67, 6.11) * mm, v(12.15, 6.32) * mm, v(11.63, 6.53) * mm, v(11.1, 6.73) * mm]});
            skFitSpline(sketch, "E852", {"points": [v(11.1, 6.73) * mm, v(11.04, 6.76) * mm, v(10.96, 6.8) * mm, v(10.9, 6.86) * mm]});
            skFitSpline(sketch, "E853", {"points": [v(10.9, 6.86) * mm, v(10.75, 6.99) * mm, v(10.7, 7.2) * mm, v(10.77, 7.38) * mm]});
            skFitSpline(sketch, "E854", {"points": [v(10.77, 7.38) * mm, v(10.85, 7.57) * mm, v(11, 7.7) * mm, v(11.22, 7.69) * mm]});
            skFitSpline(sketch, "E855", {"points": [v(11.22, 7.69) * mm, v(11.32, 7.68) * mm, v(11.42, 7.66) * mm, v(11.52, 7.62) * mm]});
            skFitSpline(sketch, "E856", {"points": [v(11.52, 7.62) * mm, v(11.93, 7.46) * mm, v(12.35, 7.29) * mm, v(12.76, 7.12) * mm]});
            skFitSpline(sketch, "E857", {"points": [v(12.76, 7.12) * mm, v(12.84, 7.1) * mm, v(12.93, 7.06) * mm, v(13.05, 7.02) * mm]});
            skFitSpline(sketch, "E858", {"points": [v(13.05, 7.02) * mm, v(12.94, 7.25) * mm, v(12.85, 7.41) * mm, v(12.63, 7.5) * mm]});
            skFitSpline(sketch, "E859", {"points": [v(12.63, 7.5) * mm, v(11.52, 8) * mm, v(10.4, 8.47) * mm, v(9.26, 8.9) * mm]});
            skFitSpline(sketch, "E860", {"points": [v(9.26, 8.9) * mm, v(9.17, 8.93) * mm, v(9.08, 8.97) * mm, v(9, 9.02) * mm]});
            skFitSpline(sketch, "E861", {"points": [v(9, 9.02) * mm, v(8.83, 9.15) * mm, v(8.77, 9.37) * mm, v(8.85, 9.56) * mm]});
            skFitSpline(sketch, "E862", {"points": [v(8.85, 9.56) * mm, v(8.93, 9.77) * mm, v(9.1, 9.9) * mm, v(9.33, 9.88) * mm]});
            skFitSpline(sketch, "E863", {"points": [v(9.33, 9.88) * mm, v(9.43, 9.87) * mm, v(9.53, 9.83) * mm, v(9.63, 9.8) * mm]});
            skFitSpline(sketch, "E864", {"points": [v(9.63, 9.8) * mm, v(10.37, 9.5) * mm, v(11.11, 9.22) * mm, v(11.86, 8.92) * mm]});
            skFitSpline(sketch, "E865", {"points": [v(11.86, 8.92) * mm, v(11.9, 8.91) * mm, v(11.93, 8.9) * mm, v(12, 8.92) * mm]});
            skFitSpline(sketch, "E866", {"points": [v(12, 8.92) * mm, v(11.89, 9.08) * mm, v(11.79, 9.25) * mm, v(11.68, 9.42) * mm]});
            skFitSpline(sketch, "E867", {"points": [v(11.68, 9.42) * mm, v(11.66, 9.45) * mm, v(11.6, 9.48) * mm, v(11.57, 9.5) * mm]});
            skFitSpline(sketch, "E868", {"points": [v(11.57, 9.5) * mm, v(10.52, 9.94) * mm, v(9.48, 10.38) * mm, v(8.43, 10.82) * mm]});
            skFitSpline(sketch, "E869", {"points": [v(8.43, 10.82) * mm, v(8.2, 10.9) * mm, v(7.96, 10.97) * mm, v(7.73, 11.05) * mm]});
            skFitSpline(sketch, "E870", {"points": [v(7.73, 11.05) * mm, v(7.68, 11.06) * mm, v(7.62, 11.08) * mm, v(7.57, 11.1) * mm]});
            skFitSpline(sketch, "E871", {"points": [v(7.57, 11.1) * mm, v(7.36, 11.2) * mm, v(7.26, 11.37) * mm, v(7.28, 11.6) * mm]});
            skFitSpline(sketch, "E872", {"points": [v(7.28, 11.6) * mm, v(7.3, 11.86) * mm, v(7.56, 12.08) * mm, v(7.81, 12.02) * mm]});
            skFitSpline(sketch, "E873", {"points": [v(7.81, 12.02) * mm, v(8.1, 11.95) * mm, v(8.4, 11.88) * mm, v(8.68, 11.77) * mm]});
            skFitSpline(sketch, "E874", {"points": [v(8.68, 11.77) * mm, v(9.28, 11.52) * mm, v(9.87, 11.25) * mm, v(10.46, 11) * mm]});
            skFitSpline(sketch, "E875", {"points": [v(10.46, 11) * mm, v(10.54, 10.96) * mm, v(10.6, 10.93) * mm, v(10.73, 10.88) * mm]});
            skFitSpline(sketch, "E876", {"points": [v(10.73, 10.88) * mm, v(10.52, 11.25) * mm, v(10.34, 11.58) * mm, v(10.1, 11.88) * mm]});
            skFitSpline(sketch, "E877", {"points": [v(10.1, 11.88) * mm, v(10.07, 11.92) * mm, v(10, 11.96) * mm, v(9.95, 11.98) * mm]});
            skFitSpline(sketch, "E878", {"points": [v(9.95, 11.98) * mm, v(9.05, 12.33) * mm, v(8.15, 12.68) * mm, v(7.25, 13.03) * mm]});
            skFitSpline(sketch, "E879", {"points": [v(7.25, 13.03) * mm, v(7.16, 13.06) * mm, v(7.08, 13.1) * mm, v(7, 13.14) * mm]});
            skFitSpline(sketch, "E880", {"points": [v(7, 13.14) * mm, v(6.83, 13.26) * mm, v(6.76, 13.48) * mm, v(6.82, 13.67) * mm]});
            skFitSpline(sketch, "E881", {"points": [v(6.82, 13.67) * mm, v(6.9, 13.88) * mm, v(7.07, 14.01) * mm, v(7.3, 14) * mm]});
            skFitSpline(sketch, "E882", {"points": [v(7.3, 14) * mm, v(7.4, 14) * mm, v(7.5, 13.97) * mm, v(7.6, 13.94) * mm]});
            skFitSpline(sketch, "E883", {"points": [v(7.6, 13.94) * mm, v(8.14, 13.74) * mm, v(8.69, 13.53) * mm, v(9.23, 13.33) * mm]});
            skFitSpline(sketch, "E884", {"points": [v(9.23, 13.33) * mm, v(9.3, 13.3) * mm, v(9.35, 13.29) * mm, v(9.45, 13.25) * mm]});
            skFitSpline(sketch, "E885", {"points": [v(9.45, 13.25) * mm, v(9.36, 13.42) * mm, v(9.29, 13.55) * mm, v(9.22, 13.68) * mm]});
            skFitSpline(sketch, "E886", {"points": [v(9.22, 13.68) * mm, v(9.03, 14.02) * mm, v(8.85, 14.35) * mm, v(8.66, 14.68) * mm]});
            skFitSpline(sketch, "E887", {"points": [v(8.66, 14.68) * mm, v(8.52, 14.93) * mm, v(8.38, 15.17) * mm, v(8.23, 15.4) * mm]});
            skFitSpline(sketch, "E888", {"points": [v(8.23, 15.4) * mm, v(8.03, 15.73) * mm, v(8.18, 16.1) * mm, v(8.55, 16.2) * mm]});
            skFitSpline(sketch, "E889", {"points": [v(8.55, 16.2) * mm, v(8.78, 16.25) * mm, v(8.98, 16.14) * mm, v(9.11, 15.9) * mm]});
            skFitSpline(sketch, "E890", {"points": [v(9.11, 15.9) * mm, v(9.5, 15.24) * mm, v(9.89, 14.58) * mm, v(10.28, 13.92) * mm]});
            skFitSpline(sketch, "E891", {"points": [v(10.28, 13.92) * mm, v(10.3, 13.89) * mm, v(10.32, 13.86) * mm, v(10.37, 13.8) * mm]});
            skFitSpline(sketch, "E892", {"points": [v(10.37, 13.8) * mm, v(10.43, 14.16) * mm, v(10.49, 14.48) * mm, v(10.54, 14.8) * mm]});
            skFitSpline(sketch, "E893", {"points": [v(10.54, 14.8) * mm, v(10.6, 15.12) * mm, v(10.64, 15.42) * mm, v(10.7, 15.73) * mm]});
            skFitSpline(sketch, "E894", {"points": [v(10.7, 15.73) * mm, v(10.7, 15.82) * mm, v(10.73, 15.9) * mm, v(10.76, 15.98) * mm]});
            skFitSpline(sketch, "E895", {"points": [v(10.76, 15.98) * mm, v(10.86, 16.21) * mm, v(11.11, 16.32) * mm, v(11.34, 16.25) * mm]});
            skFitSpline(sketch, "E896", {"points": [v(11.34, 16.25) * mm, v(11.57, 16.18) * mm, v(11.72, 15.96) * mm, v(11.68, 15.72) * mm]});
            skFitSpline(sketch, "E897", {"points": [v(11.68, 15.72) * mm, v(11.6, 15.22) * mm, v(11.5, 14.72) * mm, v(11.43, 14.23) * mm]});
            skFitSpline(sketch, "E898", {"points": [v(11.43, 14.23) * mm, v(11.36, 13.74) * mm, v(11.3, 13.25) * mm, v(11.22, 12.76) * mm]});
            skFitSpline(sketch, "E899", {"points": [v(11.22, 12.76) * mm, v(11.2, 12.62) * mm, v(11.22, 12.49) * mm, v(11.28, 12.37) * mm]});
            skFitSpline(sketch, "E900", {"points": [v(11.28, 12.37) * mm, v(11.43, 12.09) * mm, v(11.59, 11.81) * mm, v(11.78, 11.53) * mm]});
            skFitSpline(sketch, "E901", {"points": [v(11.78, 11.53) * mm, v(11.8, 11.67) * mm, v(11.82, 11.8) * mm, v(11.83, 11.94) * mm]});
            skFitSpline(sketch, "E902", {"points": [v(11.83, 11.94) * mm, v(11.91, 12.63) * mm, v(11.99, 13.32) * mm, v(12.08, 14) * mm]});
            skFitSpline(sketch, "E903", {"points": [v(12.08, 14) * mm, v(12.1, 14.2) * mm, v(12.17, 14.38) * mm, v(12.24, 14.56) * mm]});
            skFitSpline(sketch, "E904", {"points": [v(12.24, 14.56) * mm, v(12.33, 14.8) * mm, v(12.58, 14.93) * mm, v(12.81, 14.86) * mm]});
            skFitSpline(sketch, "E905", {"points": [v(12.81, 14.86) * mm, v(13.07, 14.78) * mm, v(13.23, 14.53) * mm, v(13.15, 14.26) * mm]});
            skFitSpline(sketch, "E906", {"points": [v(13.15, 14.26) * mm, v(12.95, 13.64) * mm, v(12.94, 13) * mm, v(12.86, 12.35) * mm]});
            skFitSpline(sketch, "E907", {"points": [v(12.86, 12.35) * mm, v(12.76, 11.6) * mm, v(12.66, 10.85) * mm, v(12.56, 10.1) * mm]});
            skFitSpline(sketch, "E908", {"points": [v(12.56, 10.1) * mm, v(12.56, 10.05) * mm, v(12.54, 9.98) * mm, v(12.57, 9.94) * mm]});
            skFitSpline(sketch, "E909", {"points": [v(12.57, 9.94) * mm, v(12.66, 9.75) * mm, v(12.76, 9.58) * mm, v(12.9, 9.4) * mm]});
            skFitSpline(sketch, "E910", {"points": [v(12.9, 9.4) * mm, v(12.98, 9.97) * mm, v(13.06, 10.54) * mm, v(13.14, 11.1) * mm]});
            skFitSpline(sketch, "E911", {"points": [v(13.14, 11.1) * mm, v(13.18, 11.42) * mm, v(13.23, 11.74) * mm, v(13.3, 12.05) * mm]});
            skFitSpline(sketch, "E912", {"points": [v(13.3, 12.05) * mm, v(13.35, 12.36) * mm, v(13.64, 12.53) * mm, v(13.92, 12.44) * mm]});
            skFitSpline(sketch, "E913", {"points": [v(13.92, 12.44) * mm, v(14.11, 12.37) * mm, v(14.24, 12.22) * mm, v(14.24, 12.01) * mm]});
            skFitSpline(sketch, "E914", {"points": [v(14.24, 12.01) * mm, v(14.24, 11.88) * mm, v(14.22, 11.74) * mm, v(14.2, 11.6) * mm]});
            skFitSpline(sketch, "E915", {"points": [v(14.2, 11.6) * mm, v(14.12, 11.03) * mm, v(14.03, 10.46) * mm, v(13.96, 9.88) * mm]});
            skFitSpline(sketch, "E916", {"points": [v(13.96, 9.88) * mm, v(13.88, 9.26) * mm, v(13.81, 8.64) * mm, v(13.74, 8.03) * mm]});
            skFitSpline(sketch, "E917", {"points": [v(13.74, 8.03) * mm, v(13.72, 7.84) * mm, v(13.86, 7.73) * mm, v(13.97, 7.59) * mm]});
            skFitSpline(sketch, "E918", {"points": [v(13.97, 7.59) * mm, v(14, 7.73) * mm, v(14.02, 7.86) * mm, v(14.04, 8) * mm]});
            skFitSpline(sketch, "E919", {"points": [v(14.04, 8) * mm, v(14.1, 8.39) * mm, v(14.15, 8.77) * mm, v(14.2, 9.16) * mm]});
            skFitSpline(sketch, "E920", {"points": [v(14.2, 9.16) * mm, v(14.2, 9.22) * mm, v(14.22, 9.27) * mm, v(14.24, 9.32) * mm]});
            skFitSpline(sketch, "E921", {"points": [v(14.24, 9.32) * mm, v(14.31, 9.6) * mm, v(14.55, 9.75) * mm, v(14.82, 9.7) * mm]});
            skFitSpline(sketch, "E922", {"points": [v(14.82, 9.7) * mm, v(15.06, 9.64) * mm, v(15.22, 9.4) * mm, v(15.18, 9.12) * mm]});
            skFitSpline(sketch, "E923", {"points": [v(15.18, 9.12) * mm, v(15.14, 8.8) * mm, v(15.08, 8.46) * mm, v(15.03, 8.13) * mm]});
            skFitSpline(sketch, "E924", {"points": [v(15.03, 8.13) * mm, v(14.95, 7.65) * mm, v(14.88, 7.17) * mm, v(14.8, 6.69) * mm]});
            skFitSpline(sketch, "E925", {"points": [v(14.8, 6.69) * mm, v(14.78, 6.53) * mm, v(14.76, 6.38) * mm, v(14.72, 6.15) * mm]});
            skFitSpline(sketch, "E926", {"points": [v(14.72, 6.15) * mm, v(14.8, 6.05) * mm, v(14.9, 5.89) * mm, v(15.03, 5.69) * mm]});
            skFitSpline(sketch, "E927", {"points": [v(15.03, 5.69) * mm, v(15.16, 5.99) * mm, v(15.27, 6.25) * mm, v(15.38, 6.5) * mm]});
            skFitSpline(sketch, "E928", {"points": [v(15.38, 6.5) * mm, v(15.72, 7.34) * mm, v(16.08, 8.17) * mm, v(16.41, 9) * mm]});
            skFitSpline(sketch, "E929", {"points": [v(16.41, 9) * mm, v(16.65, 9.6) * mm, v(16.86, 10.22) * mm, v(17.09, 10.82) * mm]});
            skFitSpline(sketch, "E930", {"points": [v(17.09, 10.82) * mm, v(17.18, 11.06) * mm, v(17.29, 11.3) * mm, v(17.4, 11.52) * mm]});
            skFitSpline(sketch, "E931", {"points": [v(17.4, 11.52) * mm, v(17.46, 11.63) * mm, v(17.47, 11.73) * mm, v(17.41, 11.84) * mm]});
            skFitSpline(sketch, "E932", {"points": [v(17.41, 11.84) * mm, v(17.3, 12.08) * mm, v(17.18, 12.33) * mm, v(17.06, 12.57) * mm]});
            skFitSpline(sketch, "E933", {"points": [v(17.06, 12.57) * mm, v(16.87, 12.98) * mm, v(16.69, 13.39) * mm, v(16.5, 13.79) * mm]});
            skFitSpline(sketch, "E934", {"points": [v(16.5, 13.79) * mm, v(16.43, 13.93) * mm, v(16.34, 14.07) * mm, v(16.27, 14.2) * mm]});
            skFitSpline(sketch, "E935", {"points": [v(16.27, 14.2) * mm, v(16.04, 14.65) * mm, v(15.81, 15.09) * mm, v(15.6, 15.53) * mm]});
            skFitSpline(sketch, "E936", {"points": [v(15.6, 15.53) * mm, v(15.55, 15.61) * mm, v(15.53, 15.71) * mm, v(15.53, 15.8) * mm]});
            skFitSpline(sketch, "E937", {"points": [v(15.53, 15.8) * mm, v(15.52, 16.06) * mm, v(15.66, 16.25) * mm, v(15.89, 16.3) * mm]});
            skFitSpline(sketch, "E938", {"points": [v(15.89, 16.3) * mm, v(16.1, 16.36) * mm, v(16.34, 16.26) * mm, v(16.45, 16.04) * mm]});
            skFitSpline(sketch, "E939", {"points": [v(16.45, 16.04) * mm, v(16.55, 15.83) * mm, v(16.64, 15.62) * mm, v(16.74, 15.41) * mm]});
            skFitSpline(sketch, "E940", {"points": [v(16.74, 15.41) * mm, v(16.86, 15.17) * mm, v(16.96, 14.93) * mm, v(17.1, 14.71) * mm]});
            skFitSpline(sketch, "E941", {"points": [v(17.1, 14.71) * mm, v(17.35, 14.35) * mm, v(17.47, 13.93) * mm, v(17.66, 13.55) * mm]});
            skFitSpline(sketch, "E942", {"points": [v(17.66, 13.55) * mm, v(17.77, 13.33) * mm, v(17.88, 13.1) * mm, v(18.01, 12.84) * mm]});
            skFitSpline(sketch, "E943", {"points": [v(18.01, 12.84) * mm, v(18.13, 13.07) * mm, v(18.25, 13.26) * mm, v(18.33, 13.46) * mm]});
            skFitSpline(sketch, "E944", {"points": [v(18.33, 13.46) * mm, v(18.56, 13.98) * mm, v(18.79, 14.5) * mm, v(19.1, 14.98) * mm]});
            skFitSpline(sketch, "E945", {"points": [v(19.1, 14.98) * mm, v(19.27, 15.28) * mm, v(19.4, 15.61) * mm, v(19.55, 15.93) * mm]});
            skFitSpline(sketch, "E946", {"points": [v(19.55, 15.93) * mm, v(19.56, 15.97) * mm, v(19.57, 16) * mm, v(19.59, 16.04) * mm]});
            skFitSpline(sketch, "E947", {"points": [v(19.59, 16.04) * mm, v(19.7, 16.28) * mm, v(19.96, 16.38) * mm, v(20.2, 16.3) * mm]});
            skFitSpline(sketch, "E948", {"points": [v(20.2, 16.3) * mm, v(20.43, 16.2) * mm, v(20.56, 15.96) * mm, v(20.5, 15.71) * mm]});
            skFitSpline(sketch, "E949", {"points": [v(20.5, 15.71) * mm, v(20.49, 15.64) * mm, v(20.46, 15.56) * mm, v(20.43, 15.49) * mm]});
            skFitSpline(sketch, "E950", {"points": [v(20.43, 15.49) * mm, v(20.16, 15) * mm, v(19.97, 14.48) * mm, v(19.66, 14.02) * mm]});
            skFitSpline(sketch, "E951", {"points": [v(19.66, 14.02) * mm, v(19.54, 13.83) * mm, v(19.47, 13.6) * mm, v(19.37, 13.4) * mm]});
            skFitSpline(sketch, "E952", {"points": [v(19.37, 13.4) * mm, v(19.17, 12.98) * mm, v(18.96, 12.56) * mm, v(18.76, 12.14) * mm]});
            skFitSpline(sketch, "E953", {"points": [v(18.76, 12.14) * mm, v(18.74, 12.1) * mm, v(18.72, 12.06) * mm, v(18.7, 12.02) * mm]});
            skFitSpline(sketch, "E954", {"points": [v(18.7, 12.02) * mm, v(18.57, 11.8) * mm, v(18.59, 11.62) * mm, v(18.7, 11.4) * mm]});
            skFitSpline(sketch, "E955", {"points": [v(18.7, 11.4) * mm, v(18.94, 10.82) * mm, v(19.14, 10.23) * mm, v(19.36, 9.65) * mm]});
            skFitSpline(sketch, "E956", {"points": [v(19.36, 9.65) * mm, v(19.5, 9.29) * mm, v(19.66, 8.93) * mm, v(19.8, 8.57) * mm]});
            skFitSpline(sketch, "E957", {"points": [v(19.8, 8.57) * mm, v(20.03, 8) * mm, v(20.26, 7.44) * mm, v(20.5, 6.88) * mm]});
            skFitSpline(sketch, "E958", {"points": [v(20.5, 6.88) * mm, v(20.65, 6.52) * mm, v(20.8, 6.15) * mm, v(20.96, 5.78) * mm]});
            skFitSpline(sketch, "E959", {"points": [v(20.96, 5.78) * mm, v(20.97, 5.76) * mm, v(21, 5.74) * mm, v(21.02, 5.7) * mm]});
            skFitSpline(sketch, "E960", {"points": [v(21.02, 5.7) * mm, v(21.13, 5.88) * mm, v(21.24, 6.04) * mm, v(21.32, 6.16) * mm]});
            skFitSpline(sketch, "E961", {"points": [v(21.32, 6.16) * mm, v(21.28, 6.4) * mm, v(21.24, 6.6) * mm, v(21.2, 6.8) * mm]});
            skFitSpline(sketch, "E962", {"points": [v(21.2, 6.8) * mm, v(21.1, 7.52) * mm, v(20.99, 8.24) * mm, v(20.88, 8.96) * mm]});
            skFitSpline(sketch, "E963", {"points": [v(20.88, 8.96) * mm, v(20.86, 9.04) * mm, v(20.85, 9.13) * mm, v(20.85, 9.22) * mm]});
            skFitSpline(sketch, "E964", {"points": [v(20.85, 9.22) * mm, v(20.86, 9.48) * mm, v(21.03, 9.67) * mm, v(21.27, 9.7) * mm]});
            skFitSpline(sketch, "E965", {"points": [v(21.27, 9.7) * mm, v(21.5, 9.73) * mm, v(21.73, 9.59) * mm, v(21.8, 9.34) * mm]});
            skFitSpline(sketch, "E966", {"points": [v(21.8, 9.34) * mm, v(21.83, 9.2) * mm, v(21.85, 9.06) * mm, v(21.87, 8.92) * mm]});
            skFitSpline(sketch, "E967", {"points": [v(21.87, 8.92) * mm, v(21.93, 8.5) * mm, v(21.99, 8.08) * mm, v(22.05, 7.67) * mm]});
            skFitSpline(sketch, "E968", {"points": [v(22.05, 7.67) * mm, v(22.05, 7.64) * mm, v(22.06, 7.61) * mm, v(22.08, 7.57) * mm]});
            skFitSpline(sketch, "E969", {"points": [v(22.08, 7.57) * mm, v(22.25, 7.77) * mm, v(22.33, 7.97) * mm, v(22.28, 8.23) * mm]});
            skFitSpline(sketch, "E970", {"points": [v(22.28, 8.23) * mm, v(22.22, 8.6) * mm, v(22.2, 8.98) * mm, v(22.16, 9.35) * mm]});
            skFitSpline(sketch, "E971", {"points": [v(22.16, 9.35) * mm, v(22.11, 9.75) * mm, v(22.06, 10.14) * mm, v(22, 10.53) * mm]});
            skFitSpline(sketch, "E972", {"points": [v(22, 10.53) * mm, v(21.93, 10.98) * mm, v(21.86, 11.42) * mm, v(21.8, 11.86) * mm]});
            skFitSpline(sketch, "E973", {"points": [v(21.8, 11.86) * mm, v(21.75, 12.16) * mm, v(21.9, 12.4) * mm, v(22.18, 12.46) * mm]});
            skFitSpline(sketch, "E974", {"points": [v(22.18, 12.46) * mm, v(22.43, 12.51) * mm, v(22.68, 12.35) * mm, v(22.74, 12.06) * mm]});
            skFitSpline(sketch, "E975", {"points": [v(22.74, 12.06) * mm, v(22.8, 11.73) * mm, v(22.86, 11.4) * mm, v(22.9, 11.07) * mm]});
            skFitSpline(sketch, "E976", {"points": [v(22.9, 11.07) * mm, v(22.98, 10.52) * mm, v(23.05, 9.96) * mm, v(23.13, 9.4) * mm]});
            skFitSpline(sketch, "E977", {"points": [v(23.13, 9.4) * mm, v(23.22, 9.48) * mm, v(23.48, 9.9) * mm, v(23.49, 9.98) * mm]});
            skFitSpline(sketch, "E978", {"points": [v(23.49, 9.98) * mm, v(23.5, 10.01) * mm, v(23.48, 10.04) * mm, v(23.48, 10.08) * mm]});
            skFitSpline(sketch, "E979", {"points": [v(23.48, 10.08) * mm, v(23.37, 10.87) * mm, v(23.27, 11.67) * mm, v(23.17, 12.47) * mm]});
            skFitSpline(sketch, "E980", {"points": [v(23.17, 12.47) * mm, v(23.1, 12.94) * mm, v(23.05, 13.42) * mm, v(22.98, 13.9) * mm]});
            skFitSpline(sketch, "E981", {"points": [v(22.98, 13.9) * mm, v(22.97, 14) * mm, v(22.92, 14.1) * mm, v(22.9, 14.2) * mm]});
            skFitSpline(sketch, "E982", {"points": [v(22.9, 14.2) * mm, v(22.89, 14.3) * mm, v(22.87, 14.43) * mm, v(22.9, 14.54) * mm]});
            skFitSpline(sketch, "E983", {"points": [v(22.9, 14.54) * mm, v(22.94, 14.73) * mm, v(23.13, 14.87) * mm, v(23.32, 14.88) * mm]});
            skFitSpline(sketch, "E984", {"points": [v(23.32, 14.88) * mm, v(23.51, 14.9) * mm, v(23.71, 14.78) * mm, v(23.79, 14.58) * mm]});
            skFitSpline(sketch, "E985", {"points": [v(23.79, 14.58) * mm, v(23.87, 14.34) * mm, v(23.94, 14.1) * mm, v(23.98, 13.86) * mm]});
            skFitSpline(sketch, "E986", {"points": [v(23.98, 13.86) * mm, v(24.06, 13.3) * mm, v(24.11, 12.72) * mm, v(24.18, 12.15) * mm]});
            skFitSpline(sketch, "E987", {"points": [v(24.18, 12.15) * mm, v(24.2, 11.95) * mm, v(24.22, 11.75) * mm, v(24.29, 11.53) * mm]});
            skFitSpline(sketch, "E988", {"points": [v(24.29, 11.53) * mm, v(24.33, 11.61) * mm, v(24.38, 11.69) * mm, v(24.42, 11.77) * mm]});
            skFitSpline(sketch, "E989", {"points": [v(24.42, 11.77) * mm, v(24.55, 12) * mm, v(24.68, 12.25) * mm, v(24.8, 12.49) * mm]});
            skFitSpline(sketch, "E990", {"points": [v(24.8, 12.49) * mm, v(24.82, 12.54) * mm, v(24.84, 12.61) * mm, v(24.83, 12.67) * mm]});
            skFitSpline(sketch, "E991", {"points": [v(24.83, 12.67) * mm, v(24.74, 13.33) * mm, v(24.64, 13.98) * mm, v(24.54, 14.64) * mm]});
            skFitSpline(sketch, "E992", {"points": [v(24.54, 14.64) * mm, v(24.48, 14.97) * mm, v(24.41, 15.31) * mm, v(24.37, 15.65) * mm]});
            skFitSpline(sketch, "E993", {"points": [v(24.37, 15.65) * mm, v(24.35, 15.76) * mm, v(24.36, 15.88) * mm, v(24.4, 15.98) * mm]});
            skFitSpline(sketch, "E994", {"points": [v(24.4, 15.98) * mm, v(24.46, 16.16) * mm, v(24.65, 16.28) * mm, v(24.85, 16.27) * mm]});
            skFitSpline(sketch, "E995", {"points": [v(24.85, 16.27) * mm, v(25.05, 16.27) * mm, v(25.24, 16.13) * mm, v(25.3, 15.9) * mm]});
            skFitSpline(sketch, "E996", {"points": [v(25.3, 15.9) * mm, v(25.35, 15.7) * mm, v(25.38, 15.49) * mm, v(25.42, 15.27) * mm]});
            skFitSpline(sketch, "E997", {"points": [v(25.42, 15.27) * mm, v(25.5, 14.79) * mm, v(25.58, 14.3) * mm, v(25.67, 13.76) * mm]});
            skFitSpline(sketch, "E998", {"points": [v(25.67, 13.76) * mm, v(25.78, 13.95) * mm, v(25.87, 14.1) * mm, v(25.96, 14.25) * mm]});
            skFitSpline(sketch, "E999", {"points": [v(25.96, 14.25) * mm, v(26.14, 14.55) * mm, v(26.32, 14.85) * mm, v(26.5, 15.15) * mm]});
            skFitSpline(sketch, "E1000", {"points": [v(26.5, 15.15) * mm, v(26.64, 15.4) * mm, v(26.78, 15.65) * mm, v(26.92, 15.9) * mm]});
            skFitSpline(sketch, "E1001", {"points": [v(26.92, 15.9) * mm, v(27.09, 16.2) * mm, v(27.4, 16.3) * mm, v(27.67, 16.12) * mm]});
            skFitSpline(sketch, "E1002", {"points": [v(27.67, 16.12) * mm, v(27.9, 15.97) * mm, v(27.97, 15.7) * mm, v(27.83, 15.44) * mm]});
            skFitSpline(sketch, "E1003", {"points": [v(27.83, 15.44) * mm, v(27.48, 14.84) * mm, v(27.13, 14.24) * mm, v(26.8, 13.64) * mm]});
            skFitSpline(sketch, "E1004", {"points": [v(26.8, 13.64) * mm, v(26.72, 13.52) * mm, v(26.67, 13.4) * mm, v(26.58, 13.24) * mm]});
            skFitSpline(sketch, "E1005", {"points": [v(26.58, 13.24) * mm, v(27.02, 13.4) * mm, v(27.42, 13.56) * mm, v(27.81, 13.7) * mm]});
            skFitSpline(sketch, "E1006", {"points": [v(27.81, 13.7) * mm, v(28.04, 13.79) * mm, v(28.26, 13.88) * mm, v(28.48, 13.96) * mm]});
            skFitSpline(sketch, "E1007", {"points": [v(28.48, 13.96) * mm, v(28.56, 13.98) * mm, v(28.64, 14) * mm, v(28.72, 14) * mm]});
            skFitSpline(sketch, "E1008", {"points": [v(28.72, 14) * mm, v(28.95, 14.02) * mm, v(29.16, 13.89) * mm, v(29.2, 13.69) * mm]});
            skFitSpline(sketch, "E1009", {"points": [v(29.2, 13.69) * mm, v(29.25, 13.44) * mm, v(29.22, 13.26) * mm, v(28.98, 13.1) * mm]});
            skFitSpline(sketch, "E1010", {"points": [v(28.98, 13.1) * mm, v(28.93, 13.08) * mm, v(28.88, 13.06) * mm, v(28.83, 13.04) * mm]});
            skFitSpline(sketch, "E1011", {"points": [v(28.83, 13.04) * mm, v(27.93, 12.7) * mm, v(27.04, 12.35) * mm, v(26.15, 12) * mm]});
            skFitSpline(sketch, "E1012", {"points": [v(26.15, 12) * mm, v(26.02, 11.96) * mm, v(25.92, 11.9) * mm, v(25.85, 11.78) * mm]});
            skFitSpline(sketch, "E1013", {"points": [v(25.85, 11.78) * mm, v(25.67, 11.5) * mm, v(25.5, 11.21) * mm, v(25.3, 10.88) * mm]});
            skFitSpline(sketch, "E1014", {"points": [v(25.3, 10.88) * mm, v(25.41, 10.93) * mm, v(25.48, 10.95) * mm, v(25.54, 10.98) * mm]});
            skFitSpline(sketch, "E1015", {"points": [v(25.54, 10.98) * mm, v(26.12, 11.23) * mm, v(26.7, 11.5) * mm, v(27.3, 11.74) * mm]});
            skFitSpline(sketch, "E1016", {"points": [v(27.3, 11.74) * mm, v(27.58, 11.86) * mm, v(27.89, 11.94) * mm, v(28.19, 12.01) * mm]});
            skFitSpline(sketch, "E1017", {"points": [v(28.19, 12.01) * mm, v(28.43, 12.07) * mm, v(28.66, 11.93) * mm, v(28.74, 11.7) * mm]});
            skFitSpline(sketch, "E1018", {"points": [v(28.74, 11.7) * mm, v(28.82, 11.47) * mm, v(28.72, 11.23) * mm, v(28.5, 11.12) * mm]});
            skFitSpline(sketch, "E1019", {"points": [v(28.5, 11.12) * mm, v(28.44, 11.09) * mm, v(28.38, 11.07) * mm, v(28.32, 11.05) * mm]});
            skFitSpline(sketch, "E1020", {"points": [v(28.32, 11.05) * mm, v(28.05, 10.96) * mm, v(27.78, 10.9) * mm, v(27.53, 10.78) * mm]});
            skFitSpline(sketch, "E1021", {"points": [v(27.53, 10.78) * mm, v(26.97, 10.55) * mm, v(26.42, 10.3) * mm, v(25.86, 10.05) * mm]});
            skFitSpline(sketch, "E1022", {"points": [v(25.86, 10.05) * mm, v(25.41, 9.86) * mm, v(24.95, 9.69) * mm, v(24.5, 9.5) * mm]});
            skFitSpline(sketch, "E1023", {"points": [v(24.5, 9.5) * mm, v(24.44, 9.47) * mm, v(24.36, 9.43) * mm, v(24.32, 9.37) * mm]});
            skFitSpline(sketch, "E1024", {"points": [v(24.32, 9.37) * mm, v(24.22, 9.22) * mm, v(24.14, 9.07) * mm, v(24.03, 8.88) * mm]});
            skFitSpline(sketch, "E1025", {"points": [v(24.03, 8.88) * mm, v(24.1, 8.9) * mm, v(24.16, 8.92) * mm, v(24.2, 8.93) * mm]});
            skFitSpline(sketch, "E1026", {"points": [v(24.2, 8.93) * mm, v(24.92, 9.21) * mm, v(25.63, 9.5) * mm, v(26.34, 9.78) * mm]});
            skFitSpline(sketch, "E1027", {"points": [v(26.34, 9.78) * mm, v(26.43, 9.81) * mm, v(26.52, 9.85) * mm, v(26.62, 9.87) * mm]});
            skFitSpline(sketch, "E1028", {"points": [v(26.62, 9.87) * mm, v(26.85, 9.92) * mm, v(27.1, 9.8) * mm, v(27.17, 9.6) * mm]});
            skFitSpline(sketch, "E1029", {"points": [v(27.17, 9.6) * mm, v(27.25, 9.36) * mm, v(27.21, 9.12) * mm, v(26.96, 8.98) * mm]});
            skFitSpline(sketch, "E1030", {"points": [v(26.96, 8.98) * mm, v(26.9, 8.94) * mm, v(26.83, 8.92) * mm, v(26.76, 8.9) * mm]});
            skFitSpline(sketch, "E1031", {"points": [v(26.76, 8.9) * mm, v(26.05, 8.61) * mm, v(25.33, 8.34) * mm, v(24.62, 8.05) * mm]});
            skFitSpline(sketch, "E1032", {"points": [v(24.62, 8.05) * mm, v(24.18, 7.87) * mm, v(23.75, 7.65) * mm, v(23.3, 7.46) * mm]});
            skFitSpline(sketch, "E1033", {"points": [v(23.3, 7.46) * mm, v(23.13, 7.38) * mm, v(23.1, 7.2) * mm, v(22.98, 7.02) * mm]});
            skFitSpline(sketch, "E1034", {"points": [v(22.98, 7.02) * mm, v(23.09, 7.06) * mm, v(23.15, 7.08) * mm, v(23.21, 7.1) * mm]});
            skFitSpline(sketch, "E1035", {"points": [v(23.21, 7.1) * mm, v(23.65, 7.28) * mm, v(24.09, 7.45) * mm, v(24.53, 7.62) * mm]});
            skFitSpline(sketch, "E1036", {"points": [v(24.53, 7.62) * mm, v(24.62, 7.66) * mm, v(24.71, 7.68) * mm, v(24.8, 7.69) * mm]});
            skFitSpline(sketch, "E1037", {"points": [v(24.8, 7.69) * mm, v(25.01, 7.7) * mm, v(25.19, 7.57) * mm, v(25.26, 7.4) * mm]});
            skFitSpline(sketch, "E1038", {"points": [v(25.26, 7.4) * mm, v(25.33, 7.2) * mm, v(25.28, 6.96) * mm, v(25.1, 6.83) * mm]});
            skFitSpline(sketch, "E1039", {"points": [v(25.1, 6.83) * mm, v(25.04, 6.79) * mm, v(24.97, 6.75) * mm, v(24.9, 6.72) * mm]});
            skFitSpline(sketch, "E1040", {"points": [v(24.9, 6.72) * mm, v(24.24, 6.47) * mm, v(23.6, 6.22) * mm, v(22.95, 5.97) * mm]});
            skFitSpline(sketch, "E1041", {"points": [v(22.95, 5.97) * mm, v(22.85, 5.94) * mm, v(22.76, 5.89) * mm, v(22.66, 5.85) * mm]});
            skFitSpline(sketch, "E1042", {"points": [v(22.66, 5.85) * mm, v(22.52, 5.8) * mm, v(22.37, 5.74) * mm, v(22.17, 5.67) * mm]});
            skFitSpline(sketch, "E1043", {"points": [v(22.17, 5.67) * mm, v(22.1, 5.55) * mm, v(22.02, 5.38) * mm, v(21.91, 5.17) * mm]});
            skFitSpline(sketch, "E1044", {"points": [v(21.91, 5.17) * mm, v(22.18, 5.2) * mm, v(22.4, 5.22) * mm, v(22.64, 5.25) * mm]});
            skFitSpline(sketch, "E1045", {"points": [v(22.64, 5.25) * mm, v(23.22, 5.33) * mm, v(23.8, 5.4) * mm, v(24.4, 5.48) * mm]});
            skFitSpline(sketch, "E1046", {"points": [v(24.4, 5.48) * mm, v(25.2, 5.6) * mm, v(26, 5.71) * mm, v(26.8, 5.83) * mm]});
            skFitSpline(sketch, "E1047", {"points": [v(26.8, 5.83) * mm, v(27.26, 5.9) * mm, v(27.72, 5.97) * mm, v(28.18, 6.03) * mm]});
            skFitSpline(sketch, "E1048", {"points": [v(28.18, 6.03) * mm, v(28.3, 6.05) * mm, v(28.38, 6.1) * mm, v(28.45, 6.2) * mm]});
            skFitSpline(sketch, "E1049", {"points": [v(28.45, 6.2) * mm, v(28.6, 6.43) * mm, v(28.77, 6.67) * mm, v(28.93, 6.9) * mm]});
            skFitSpline(sketch, "E1050", {"points": [v(28.93, 6.9) * mm, v(29.17, 7.25) * mm, v(29.41, 7.58) * mm, v(29.65, 7.93) * mm]});
            skFitSpline(sketch, "E1051", {"points": [v(29.65, 7.93) * mm, v(29.76, 8.1) * mm, v(29.86, 8.29) * mm, v(29.97, 8.46) * mm]});
            skFitSpline(sketch, "E1052", {"points": [v(29.97, 8.46) * mm, v(30.21, 8.84) * mm, v(30.47, 9.22) * mm, v(30.72, 9.6) * mm]});
            skFitSpline(sketch, "E1053", {"points": [v(30.72, 9.6) * mm, v(30.76, 9.66) * mm, v(30.81, 9.71) * mm, v(30.87, 9.76) * mm]});
            skFitSpline(sketch, "E1054", {"points": [v(30.87, 9.76) * mm, v(31.06, 9.92) * mm, v(31.32, 9.92) * mm, v(31.5, 9.76) * mm]});
            skFitSpline(sketch, "E1055", {"points": [v(31.5, 9.76) * mm, v(31.69, 9.6) * mm, v(31.73, 9.32) * mm, v(31.58, 9.1) * mm]});
            skFitSpline(sketch, "E1056", {"points": [v(31.58, 9.1) * mm, v(31.45, 8.92) * mm, v(31.31, 8.73) * mm, v(31.18, 8.54) * mm]});
            skFitSpline(sketch, "E1057", {"points": [v(31.18, 8.54) * mm, v(31.04, 8.33) * mm, v(30.89, 8.12) * mm, v(30.77, 7.9) * mm]});
            skFitSpline(sketch, "E1058", {"points": [v(30.77, 7.9) * mm, v(30.57, 7.49) * mm, v(30.27, 7.16) * mm, v(30.02, 6.79) * mm]});
            skFitSpline(sketch, "E1059", {"points": [v(30.02, 6.79) * mm, v(29.89, 6.6) * mm, v(29.76, 6.4) * mm, v(29.6, 6.15) * mm]});
            skFitSpline(sketch, "E1060", {"points": [v(29.6, 6.15) * mm, v(29.74, 6.15) * mm, v(29.83, 6.15) * mm, v(29.91, 6.16) * mm]});
            skFitSpline(sketch, "E1061", {"points": [v(29.91, 6.16) * mm, v(30.27, 6.19) * mm, v(30.62, 6.23) * mm, v(30.98, 6.27) * mm]});
            skFitSpline(sketch, "E1062", {"points": [v(30.98, 6.27) * mm, v(31.07, 6.28) * mm, v(31.16, 6.3) * mm, v(31.24, 6.3) * mm]});
            skFitSpline(sketch, "E1063", {"points": [v(31.24, 6.3) * mm, v(31.75, 6.27) * mm, v(32.25, 6.28) * mm, v(32.75, 6.35) * mm]});
            skFitSpline(sketch, "E1064", {"points": [v(32.75, 6.35) * mm, v(32.87, 6.36) * mm, v(32.98, 6.37) * mm, v(33.1, 6.39) * mm]});
            skFitSpline(sketch, "E1065", {"points": [v(33.1, 6.39) * mm, v(33.46, 6.43) * mm, v(33.72, 6.18) * mm, v(33.68, 5.83) * mm]});
            skFitSpline(sketch, "E1066", {"points": [v(33.68, 5.83) * mm, v(33.66, 5.67) * mm, v(33.56, 5.55) * mm, v(33.42, 5.48) * mm]});
            skFitSpline(sketch, "E1067", {"points": [v(33.42, 5.48) * mm, v(33.32, 5.43) * mm, v(33.2, 5.4) * mm, v(33.1, 5.4) * mm]});
            skFitSpline(sketch, "E1068", {"points": [v(33.1, 5.4) * mm, v(32.53, 5.38) * mm, v(31.96, 5.3) * mm, v(31.38, 5.33) * mm]});
            skFitSpline(sketch, "E1069", {"points": [v(31.38, 5.33) * mm, v(31.12, 5.34) * mm, v(30.86, 5.26) * mm, v(30.6, 5.24) * mm]});
            skFitSpline(sketch, "E1070", {"points": [v(30.6, 5.24) * mm, v(30.11, 5.2) * mm, v(29.63, 5.18) * mm, v(29.14, 5.15) * mm]});
            skFitSpline(sketch, "E1071", {"points": [v(29.14, 5.15) * mm, v(28.96, 5.14) * mm, v(28.83, 5.08) * mm, v(28.73, 4.91) * mm]});
            skFitSpline(sketch, "E1072", {"points": [v(28.73, 4.91) * mm, v(28.41, 4.38) * mm, v(27.95, 3.96) * mm, v(27.58, 3.47) * mm]});
            skFitSpline(sketch, "E1073", {"points": [v(27.58, 3.47) * mm, v(27.17, 2.95) * mm, v(26.77, 2.42) * mm, v(26.36, 1.9) * mm]});
            skFitSpline(sketch, "E1074", {"points": [v(26.36, 1.9) * mm, v(26.14, 1.6) * mm, v(25.9, 1.32) * mm, v(25.69, 1.03) * mm]});
            skFitSpline(sketch, "E1075", {"points": [v(25.69, 1.03) * mm, v(25.43, 0.7) * mm, v(25.18, 0.36) * mm, v(24.9, -0.02) * mm]});
            skFitSpline(sketch, "E1076", {"points": [v(24.9, -0.02) * mm, v(25.12, -0.03) * mm, v(25.32, -0.04) * mm, v(25.46, -0.05) * mm]});
            skFitSpline(sketch, "E1077", {"points": [v(25.46, -0.05) * mm, v(25.64, 0.1) * mm, v(25.78, 0.22) * mm, v(25.93, 0.34) * mm]});
            skFitSpline(sketch, "E1078", {"points": [v(25.93, 0.34) * mm, v(26.11, 0.5) * mm, v(26.3, 0.65) * mm, v(26.48, 0.8) * mm]});
            skFitSpline(sketch, "E1079", {"points": [v(26.48, 0.8) * mm, v(26.9, 1.14) * mm, v(27.33, 1.47) * mm, v(27.76, 1.8) * mm]});
            skFitSpline(sketch, "E1080", {"points": [v(27.76, 1.8) * mm, v(27.88, 1.9) * mm, v(28.02, 1.98) * mm, v(28.18, 1.96) * mm]});
            skFitSpline(sketch, "E1081", {"points": [v(28.18, 1.96) * mm, v(28.35, 1.93) * mm, v(28.5, 1.84) * mm, v(28.56, 1.67) * mm]});
            skFitSpline(sketch, "E1082", {"points": [v(28.56, 1.67) * mm, v(28.62, 1.5) * mm, v(28.62, 1.32) * mm, v(28.5, 1.17) * mm]});
            skFitSpline(sketch, "E1083", {"points": [v(28.5, 1.17) * mm, v(28.43, 1.1) * mm, v(28.37, 1.05) * mm, v(28.3, 1) * mm]});
            skFitSpline(sketch, "E1084", {"points": [v(28.3, 1) * mm, v(27.95, 0.72) * mm, v(27.6, 0.45) * mm, v(27.26, 0.18) * mm]});
            skFitSpline(sketch, "E1085", {"points": [v(27.26, 0.18) * mm, v(27.2, 0.12) * mm, v(27.13, 0.07) * mm, v(27.03, -0.01) * mm]});
            skFitSpline(sketch, "E1086", {"points": [v(27.03, -0.01) * mm, v(27.3, -0.06) * mm, v(27.48, -0.03) * mm, v(27.67, 0.1) * mm]});
            skFitSpline(sketch, "E1087", {"points": [v(27.67, 0.1) * mm, v(28.66, 0.84) * mm, v(29.64, 1.57) * mm, v(30.58, 2.35) * mm]});
            skFitSpline(sketch, "E1088", {"points": [v(30.58, 2.35) * mm, v(30.72, 2.46) * mm, v(30.86, 2.56) * mm, v(31.06, 2.52) * mm]});
            skFitSpline(sketch, "E1089", {"points": [v(31.06, 2.52) * mm, v(31.24, 2.49) * mm, v(31.38, 2.38) * mm, v(31.44, 2.2) * mm]});
            skFitSpline(sketch, "E1090", {"points": [v(31.44, 2.2) * mm, v(31.5, 2) * mm, v(31.45, 1.81) * mm, v(31.29, 1.67) * mm]});
            skFitSpline(sketch, "E1091", {"points": [v(31.29, 1.67) * mm, v(31.04, 1.46) * mm, v(30.79, 1.25) * mm, v(30.53, 1.05) * mm]});
            skFitSpline(sketch, "E1092", {"points": [v(30.53, 1.05) * mm, v(30.08, 0.7) * mm, v(29.63, 0.35) * mm, v(29.15, -0.02) * mm]});
            skFitSpline(sketch, "E1093", {"points": [v(29.15, -0.02) * mm, v(29.24, -0.03) * mm, v(29.29, -0.05) * mm, v(29.34, -0.05) * mm]});
            skFitSpline(sketch, "E1094", {"points": [v(29.34, -0.05) * mm, v(29.43, -0.05) * mm, v(29.53, -0.03) * mm, v(29.62, -0.04) * mm]});
            skFitSpline(sketch, "E1095", {"points": [v(29.62, -0.04) * mm, v(29.79, -0.06) * mm, v(29.9, 0.02) * mm, v(30.03, 0.12) * mm]});
            skFitSpline(sketch, "E1096", {"points": [v(30.03, 0.12) * mm, v(30.47, 0.47) * mm, v(30.92, 0.82) * mm, v(31.37, 1.16) * mm]});
            skFitSpline(sketch, "E1097", {"points": [v(31.37, 1.16) * mm, v(31.8, 1.47) * mm, v(32.23, 1.78) * mm, v(32.65, 2.1) * mm]});
            skFitSpline(sketch, "E1098", {"points": [v(32.65, 2.1) * mm, v(32.84, 2.24) * mm, v(33, 2.41) * mm, v(33.18, 2.57) * mm]});
            skFitSpline(sketch, "E1099", {"points": [v(33.18, 2.57) * mm, v(33.22, 2.6) * mm, v(33.26, 2.65) * mm, v(33.3, 2.69) * mm]});
            skFitSpline(sketch, "E1100", {"points": [v(33.3, 2.69) * mm, v(33.51, 2.84) * mm, v(33.79, 2.83) * mm, v(33.96, 2.65) * mm]});
            skFitSpline(sketch, "E1101", {"points": [v(33.96, 2.65) * mm, v(34.13, 2.48) * mm, v(34.15, 2.2) * mm, v(33.98, 2.02) * mm]});
            skFitSpline(sketch, "E1102", {"points": [v(33.98, 2.02) * mm, v(33.78, 1.8) * mm, v(33.56, 1.58) * mm, v(33.33, 1.4) * mm]});
            skFitSpline(sketch, "E1103", {"points": [v(33.33, 1.4) * mm, v(32.82, 1) * mm, v(32.3, 0.63) * mm, v(31.78, 0.25) * mm]});
            skFitSpline(sketch, "E1104", {"points": [v(31.78, 0.25) * mm, v(31.72, 0.2) * mm, v(31.66, 0.15) * mm, v(31.56, 0.08) * mm]});
            skFitSpline(sketch, "E1105", {"points": [v(31.56, 0.08) * mm, v(31.65, 0.07) * mm, v(31.7, 0.06) * mm, v(31.74, 0.06) * mm]});
            skFitSpline(sketch, "E1106", {"points": [v(31.74, 0.06) * mm, v(32.05, 0.07) * mm, v(32.37, 0.08) * mm, v(32.67, 0.1) * mm]});
            skFitSpline(sketch, "E1107", {"points": [v(32.67, 0.1) * mm, v(32.75, 0.11) * mm, v(32.83, 0.15) * mm, v(32.89, 0.2) * mm]});
            skFitSpline(sketch, "E1108", {"points": [v(32.89, 0.2) * mm, v(33.64, 0.8) * mm, v(34.4, 1.4) * mm, v(35.15, 2.01) * mm]});
            skFitSpline(sketch, "E1109", {"points": [v(35.15, 2.01) * mm, v(35.2, 2.05) * mm, v(35.23, 2.08) * mm, v(35.28, 2.12) * mm]});
            skFitSpline(sketch, "E1110", {"points": [v(35.28, 2.12) * mm, v(35.5, 2.26) * mm, v(35.77, 2.23) * mm, v(35.93, 2.04) * mm]});
            skFitSpline(sketch, "E1111", {"points": [v(35.93, 2.04) * mm, v(36.1, 1.85) * mm, v(36.1, 1.6) * mm, v(35.92, 1.4) * mm]});
            skFitSpline(sketch, "E1112", {"points": [v(35.92, 1.4) * mm, v(35.8, 1.28) * mm, v(35.68, 1.18) * mm, v(35.55, 1.07) * mm]});
            skFitSpline(sketch, "E1113", {"points": [v(35.55, 1.07) * mm, v(35.16, 0.75) * mm, v(34.78, 0.44) * mm, v(34.4, 0.13) * mm]});
            skFitSpline(sketch, "E1114", {"points": [v(34.4, 0.13) * mm, v(34.35, 0.1) * mm, v(34.3, 0.05) * mm, v(34.28, -0.03) * mm]});
            skFitSpline(sketch, "E1115", {"points": [v(34.28, -0.03) * mm, v(34.44, -0.03) * mm, v(34.61, -0.05) * mm, v(34.77, -0.03) * mm]});
            skFitSpline(sketch, "E1116", {"points": [v(34.77, -0.03) * mm, v(35.13, 0.01) * mm, v(35.49, 0) * mm, v(35.85, -0.04) * mm]});
            skFitSpline(sketch, "E1117", {"points": [v(35.85, -0.04) * mm, v(36.12, -0.06) * mm, v(36.4, -0.03) * mm, v(36.68, -0.04) * mm]});
            skFitSpline(sketch, "E1118", {"points": [v(36.68, -0.04) * mm, v(36.79, -0.04) * mm, v(36.9, -0.05) * mm, v(36.99, -0.08) * mm]});
            skFitSpline(sketch, "E1119", {"points": [v(36.99, -0.08) * mm, v(37.2, -0.17) * mm, v(37.3, -0.4) * mm, v(37.26, -0.64) * mm]});
            skFitSpline(sketch, "E1120", {"points": [v(37.26, -0.64) * mm, v(37.22, -0.86) * mm, v(37.03, -1.03) * mm, v(36.8, -1.04) * mm]});
            skFitSpline(sketch, "E1121", {"points": [v(36.8, -1.04) * mm, v(36.63, -1.05) * mm, v(36.46, -1.03) * mm, v(36.28, -1.02) * mm]});
            skFitSpline(sketch, "E1122", {"points": [v(36.28, -1.02) * mm, v(36.17, -1.02) * mm, v(36.06, -1) * mm, v(35.95, -1.02) * mm]});
            skFitSpline(sketch, "E1123", {"points": [v(35.95, -1.02) * mm, v(35.55, -1.08) * mm, v(35.15, -1.06) * mm, v(34.75, -1.04) * mm]});
            skFitSpline(sketch, "E1124", {"points": [v(34.75, -1.04) * mm, v(34.6, -1.04) * mm, v(34.45, -1.04) * mm, v(34.25, -1.04) * mm]});
            skFitSpline(sketch, "E1125", {"points": [v(34.25, -1.04) * mm, v(34.32, -1.11) * mm, v(34.34, -1.16) * mm, v(34.38, -1.19) * mm]});
            skFitSpline(sketch, "E1126", {"points": [v(34.38, -1.19) * mm, v(34.83, -1.56) * mm, v(35.28, -1.93) * mm, v(35.74, -2.3) * mm]});
            skFitSpline(sketch, "E1127", {"points": [v(35.74, -2.3) * mm, v(35.8, -2.35) * mm, v(35.86, -2.4) * mm, v(35.91, -2.46) * mm]});
            skFitSpline(sketch, "E1128", {"points": [v(35.91, -2.46) * mm, v(36.1, -2.67) * mm, v(36.1, -2.92) * mm, v(35.93, -3.11) * mm]});
            skFitSpline(sketch, "E1129", {"points": [v(35.93, -3.11) * mm, v(35.76, -3.3) * mm, v(35.49, -3.33) * mm, v(35.27, -3.18) * mm]});
            skFitSpline(sketch, "E1130", {"points": [v(35.27, -3.18) * mm, v(35.18, -3.11) * mm, v(35.1, -3.03) * mm, v(35.02, -2.96) * mm]});
            skFitSpline(sketch, "E1131", {"points": [v(35.02, -2.96) * mm, v(34.3, -2.4) * mm, v(33.6, -1.82) * mm, v(32.88, -1.26) * mm]});
            skFitSpline(sketch, "E1132", {"points": [v(32.88, -1.26) * mm, v(32.83, -1.22) * mm, v(32.77, -1.2) * mm, v(32.71, -1.18) * mm]});
            skFitSpline(sketch, "E1133", {"points": [v(32.71, -1.18) * mm, v(32.34, -1.1) * mm, v(31.97, -1.16) * mm, v(31.6, -1.17) * mm]});
            skFitSpline(sketch, "E1134", {"points": [v(31.6, -1.17) * mm, v(31.68, -1.24) * mm, v(31.78, -1.31) * mm, v(31.87, -1.38) * mm]});
            skFitSpline(sketch, "E1135", {"points": [v(31.87, -1.38) * mm, v(32.36, -1.74) * mm, v(32.86, -2.1) * mm, v(33.34, -2.47) * mm]});
            skFitSpline(sketch, "E1136", {"points": [v(33.34, -2.47) * mm, v(33.57, -2.65) * mm, v(33.79, -2.85) * mm, v(33.98, -3.08) * mm]});
            skFitSpline(sketch, "E1137", {"points": [v(33.98, -3.08) * mm, v(34.23, -3.38) * mm, v(34.06, -3.8) * mm, v(33.68, -3.86) * mm]});
            skFitSpline(sketch, "E1138", {"points": [v(33.68, -3.86) * mm, v(33.5, -3.89) * mm, v(33.34, -3.82) * mm, v(33.23, -3.68) * mm]});
            skFitSpline(sketch, "E1139", {"points": [v(33.23, -3.68) * mm, v(32.98, -3.4) * mm, v(32.67, -3.18) * mm, v(32.37, -2.96) * mm]});
            skFitSpline(sketch, "E1140", {"points": [v(32.37, -2.96) * mm, v(31.65, -2.42) * mm, v(30.93, -1.9) * mm, v(30.22, -1.35) * mm]});
            skFitSpline(sketch, "E1141", {"points": [v(30.22, -1.35) * mm, v(29.98, -1.16) * mm, v(29.77, -0.99) * mm, v(29.44, -1.03) * mm]});
            skFitSpline(sketch, "E1142", {"points": [v(29.44, -1.03) * mm, v(29.36, -1.05) * mm, v(29.27, -1.02) * mm, v(29.16, -1.04) * mm]});
            skFitSpline(sketch, "E1143", {"points": [v(29.16, -1.04) * mm, v(29.38, -1.22) * mm, v(29.6, -1.4) * mm, v(29.82, -1.58) * mm]});
            skFitSpline(sketch, "E1144", {"points": [v(29.82, -1.58) * mm, v(30.29, -1.95) * mm, v(30.76, -2.32) * mm, v(31.23, -2.7) * mm]});
            skFitSpline(sketch, "E1145", {"points": [v(31.23, -2.7) * mm, v(31.37, -2.8) * mm, v(31.46, -2.93) * mm, v(31.46, -3.12) * mm]});
            skFitSpline(sketch, "E1146", {"points": [v(31.46, -3.12) * mm, v(31.45, -3.46) * mm, v(31.12, -3.7) * mm, v(30.8, -3.56) * mm]});
            skFitSpline(sketch, "E1147", {"points": [v(30.8, -3.56) * mm, v(30.72, -3.52) * mm, v(30.65, -3.47) * mm, v(30.58, -3.42) * mm]});
            skFitSpline(sketch, "E1148", {"points": [v(30.58, -3.42) * mm, v(29.98, -2.94) * mm, v(29.37, -2.44) * mm, v(28.76, -1.97) * mm]});
            skFitSpline(sketch, "E1149", {"points": [v(28.76, -1.97) * mm, v(28.37, -1.67) * mm, v(27.97, -1.38) * mm, v(27.55, -1.1) * mm]});
            skFitSpline(sketch, "E1150", {"points": [v(27.55, -1.1) * mm, v(27.43, -1.03) * mm, v(27.25, -1.05) * mm, v(27.1, -1.02) * mm]});
            skFitSpline(sketch, "E1151", {"points": [v(27.1, -1.02) * mm, v(27.1, -1.04) * mm, v(27.08, -1.06) * mm, v(27.08, -1.07) * mm]});
            skFitSpline(sketch, "E1152", {"points": [v(27.08, -1.07) * mm, v(27.12, -1.11) * mm, v(27.15, -1.16) * mm, v(27.2, -1.2) * mm]});
            skFitSpline(sketch, "E1153", {"points": [v(27.2, -1.2) * mm, v(27.58, -1.5) * mm, v(27.96, -1.8) * mm, v(28.35, -2.1) * mm]});
            skFitSpline(sketch, "E1154", {"points": [v(28.35, -2.1) * mm, v(28.49, -2.21) * mm, v(28.6, -2.34) * mm, v(28.6, -2.54) * mm]});
            skFitSpline(sketch, "E1155", {"points": [v(28.6, -2.54) * mm, v(28.6, -2.9) * mm, v(28.24, -3.14) * mm, v(27.9, -2.97) * mm]});
            skFitSpline(sketch, "E1156", {"points": [v(27.9, -2.97) * mm, v(27.84, -2.94) * mm, v(27.79, -2.9) * mm, v(27.73, -2.85) * mm]});
            skFitSpline(sketch, "E1157", {"points": [v(27.73, -2.85) * mm, v(27.19, -2.42) * mm, v(26.65, -1.98) * mm, v(26.11, -1.54) * mm]});
            skFitSpline(sketch, "E1158", {"points": [v(26.11, -1.54) * mm, v(26.04, -1.48) * mm, v(25.96, -1.44) * mm, v(25.9, -1.39) * mm]});
            skFitSpline(sketch, "E1159", {"points": [v(25.9, -1.39) * mm, v(25.76, -1.28) * mm, v(25.63, -1.16) * mm, v(25.47, -1.02) * mm]});
            skFitSpline(sketch, "E1160", {"points": [v(25.47, -1.02) * mm, v(25.33, -1.03) * mm, v(25.13, -1.04) * mm, v(24.9, -1.06) * mm]});
            skFitSpline(sketch, "E1161", {"points": [v(24.9, -1.06) * mm, v(25.09, -1.3) * mm, v(25.25, -1.53) * mm, v(25.42, -1.75) * mm]});
            skFitSpline(sketch, "E1162", {"points": [v(25.42, -1.75) * mm, v(25.96, -2.45) * mm, v(26.49, -3.16) * mm, v(27.04, -3.86) * mm]});
            skFitSpline(sketch, "E1163", {"points": [v(27.04, -3.86) * mm, v(27.45, -4.38) * mm, v(27.9, -4.89) * mm, v(28.32, -5.4) * mm]});
            skFitSpline(sketch, "E1164", {"points": [v(28.32, -5.4) * mm, v(28.47, -5.6) * mm, v(28.62, -5.8) * mm, v(28.75, -6.01) * mm]});
            skFitSpline(sketch, "E1165", {"points": [v(28.75, -6.01) * mm, v(28.83, -6.13) * mm, v(28.92, -6.2) * mm, v(29.06, -6.2) * mm]});
            skFitSpline(sketch, "E1166", {"points": [v(29.06, -6.2) * mm, v(29.34, -6.23) * mm, v(29.61, -6.25) * mm, v(29.9, -6.27) * mm]});
            skFitSpline(sketch, "E1167", {"points": [v(29.9, -6.27) * mm, v(30.34, -6.31) * mm, v(30.8, -6.35) * mm, v(31.25, -6.39) * mm]});
            skFitSpline(sketch, "E1168", {"points": [v(31.25, -6.39) * mm, v(31.37, -6.4) * mm, v(31.5, -6.38) * mm, v(31.63, -6.39) * mm]});
            skFitSpline(sketch, "E1169", {"points": [v(31.63, -6.39) * mm, v(31.99, -6.4) * mm, v(32.34, -6.42) * mm, v(32.7, -6.44) * mm]});
            skFitSpline(sketch, "E1170", {"points": [v(32.7, -6.44) * mm, v(32.81, -6.45) * mm, v(32.92, -6.45) * mm, v(33.04, -6.47) * mm]});
            skFitSpline(sketch, "E1171", {"points": [v(33.04, -6.47) * mm, v(33.15, -6.48) * mm, v(33.26, -6.49) * mm, v(33.36, -6.52) * mm]});
            skFitSpline(sketch, "E1172", {"points": [v(33.36, -6.52) * mm, v(33.62, -6.62) * mm, v(33.74, -6.87) * mm, v(33.66, -7.13) * mm]});
            skFitSpline(sketch, "E1173", {"points": [v(33.66, -7.13) * mm, v(33.6, -7.35) * mm, v(33.34, -7.5) * mm, v(33.1, -7.46) * mm]});
            skFitSpline(sketch, "E1174", {"points": [v(33.1, -7.46) * mm, v(32.69, -7.41) * mm, v(32.27, -7.38) * mm, v(31.86, -7.35) * mm]});
            skFitSpline(sketch, "E1175", {"points": [v(31.86, -7.35) * mm, v(31.74, -7.34) * mm, v(31.62, -7.38) * mm, v(31.5, -7.37) * mm]});
            skFitSpline(sketch, "E1176", {"points": [v(31.5, -7.37) * mm, v(31.27, -7.36) * mm, v(31.04, -7.33) * mm, v(30.81, -7.31) * mm]});
            skFitSpline(sketch, "E1177", {"points": [v(30.81, -7.31) * mm, v(30.46, -7.29) * mm, v(30.11, -7.26) * mm, v(29.76, -7.23) * mm]});
            skFitSpline(sketch, "E1178", {"points": [v(29.76, -7.23) * mm, v(29.73, -7.23) * mm, v(29.7, -7.24) * mm, v(29.62, -7.25) * mm]});
            skFitSpline(sketch, "E1179", {"points": [v(29.62, -7.25) * mm, v(29.76, -7.47) * mm, v(29.88, -7.66) * mm, v(30.01, -7.85) * mm]});
            skFitSpline(sketch, "E1180", {"points": [v(30.01, -7.85) * mm, v(30.06, -7.91) * mm, v(30.1, -7.98) * mm, v(30.15, -8.04) * mm]});
            skFitSpline(sketch, "E1181", {"points": [v(30.15, -8.04) * mm, v(30.45, -8.42) * mm, v(30.7, -8.83) * mm, v(30.93, -9.25) * mm]});
            skFitSpline(sketch, "E1182", {"points": [v(30.93, -9.25) * mm, v(31.1, -9.55) * mm, v(31.33, -9.83) * mm, v(31.54, -10.11) * mm]});
            skFitSpline(sketch, "E1183", {"points": [v(31.54, -10.11) * mm, v(31.61, -10.22) * mm, v(31.66, -10.32) * mm, v(31.67, -10.46) * mm]});
            skFitSpline(sketch, "E1184", {"points": [v(31.67, -10.46) * mm, v(31.67, -10.65) * mm, v(31.6, -10.79) * mm, v(31.44, -10.88) * mm]});
            skFitSpline(sketch, "E1185", {"points": [v(31.44, -10.88) * mm, v(31.27, -10.98) * mm, v(31.09, -10.98) * mm, v(30.94, -10.87) * mm]});
            skFitSpline(sketch, "E1186", {"points": [v(30.94, -10.87) * mm, v(30.82, -10.79) * mm, v(30.72, -10.68) * mm, v(30.64, -10.56) * mm]});
            skFitSpline(sketch, "E1187", {"points": [v(30.64, -10.56) * mm, v(30.33, -10.1) * mm, v(30, -9.64) * mm, v(29.75, -9.14) * mm]});
            skFitSpline(sketch, "E1188", {"points": [v(29.75, -9.14) * mm, v(29.66, -8.96) * mm, v(29.5, -8.81) * mm, v(29.38, -8.64) * mm]});
            skFitSpline(sketch, "E1189", {"points": [v(29.38, -8.64) * mm, v(29.12, -8.25) * mm, v(28.86, -7.86) * mm, v(28.6, -7.47) * mm]});
            skFitSpline(sketch, "E1190", {"points": [v(28.6, -7.47) * mm, v(28.53, -7.38) * mm, v(28.47, -7.3) * mm, v(28.4, -7.22) * mm]});
            skFitSpline(sketch, "E1191", {"points": [v(28.4, -7.22) * mm, v(28.35, -7.14) * mm, v(28.29, -7.1) * mm, v(28.19, -7.1) * mm]});
            skFitSpline(sketch, "E1192", {"points": [v(28.19, -7.1) * mm, v(27.5, -7.08) * mm, v(26.82, -6.88) * mm, v(26.13, -6.79) * mm]});
            skFitSpline(sketch, "E1193", {"points": [v(26.13, -6.79) * mm, v(25.72, -6.73) * mm, v(25.31, -6.68) * mm, v(24.9, -6.62) * mm]});
            skFitSpline(sketch, "E1194", {"points": [v(24.9, -6.62) * mm, v(24.33, -6.54) * mm, v(23.77, -6.46) * mm, v(23.2, -6.39) * mm]});
            skFitSpline(sketch, "E1195", {"points": [v(23.2, -6.39) * mm, v(22.78, -6.33) * mm, v(22.37, -6.29) * mm, v(21.91, -6.23) * mm]});
            skFitSpline(sketch, "E1196", {"points": [v(21.91, -6.23) * mm, v(22.02, -6.44) * mm, v(22.1, -6.62) * mm, v(22.17, -6.74) * mm]});
            skFitSpline(sketch, "E1197", {"points": [v(22.17, -6.74) * mm, v(22.38, -6.82) * mm, v(22.53, -6.87) * mm, v(22.69, -6.93) * mm]});
            skFitSpline(sketch, "E1198", {"points": [v(22.69, -6.93) * mm, v(22.9, -7) * mm, v(23.12, -7.09) * mm, v(23.34, -7.17) * mm]});
            skFitSpline(sketch, "E1199", {"points": [v(23.34, -7.17) * mm, v(23.87, -7.38) * mm, v(24.4, -7.6) * mm, v(24.94, -7.81) * mm]});
            skFitSpline(sketch, "E1200", {"points": [v(24.94, -7.81) * mm, v(25.15, -7.9) * mm, v(25.28, -8.04) * mm, v(25.28, -8.28) * mm]});
            skFitSpline(sketch, "E1201", {"points": [v(25.28, -8.28) * mm, v(25.28, -8.6) * mm, v(25, -8.83) * mm, v(24.68, -8.74) * mm]});
            skFitSpline(sketch, "E1202", {"points": [v(24.68, -8.74) * mm, v(24.5, -8.7) * mm, v(24.34, -8.62) * mm, v(24.17, -8.55) * mm]});
            skFitSpline(sketch, "E1203", {"points": [v(24.17, -8.55) * mm, v(23.79, -8.4) * mm, v(23.41, -8.25) * mm, v(22.98, -8.08) * mm]});
            skFitSpline(sketch, "E1204", {"points": [v(22.98, -8.08) * mm, v(23.1, -8.3) * mm, v(23.16, -8.47) * mm, v(23.38, -8.56) * mm]});
            skFitSpline(sketch, "E1205", {"points": [v(23.38, -8.56) * mm, v(24.5, -9.05) * mm, v(25.62, -9.53) * mm, v(26.76, -9.96) * mm]});
            skFitSpline(sketch, "E1206", {"points": [v(26.76, -9.96) * mm, v(26.84, -10) * mm, v(26.91, -10.02) * mm, v(26.98, -10.06) * mm]});
            skFitSpline(sketch, "E1207", {"points": [v(26.98, -10.06) * mm, v(27.22, -10.21) * mm, v(27.23, -10.4) * mm, v(27.19, -10.62) * mm]});
            skFitSpline(sketch, "E1208", {"points": [v(27.19, -10.62) * mm, v(27.15, -10.81) * mm, v(26.95, -10.95) * mm, v(26.73, -10.94) * mm]});
            skFitSpline(sketch, "E1209", {"points": [v(26.73, -10.94) * mm, v(26.62, -10.93) * mm, v(26.5, -10.9) * mm, v(26.4, -10.87) * mm]});
            skFitSpline(sketch, "E1210", {"points": [v(26.4, -10.87) * mm, v(25.89, -10.66) * mm, v(25.37, -10.45) * mm, v(24.85, -10.25) * mm]});
            skFitSpline(sketch, "E1211", {"points": [v(24.85, -10.25) * mm, v(24.6, -10.15) * mm, v(24.35, -10.06) * mm, v(24.05, -9.94) * mm]});
            skFitSpline(sketch, "E1212", {"points": [v(24.05, -9.94) * mm, v(24.14, -10.18) * mm, v(24.26, -10.35) * mm, v(24.38, -10.51) * mm]});
            skFitSpline(sketch, "E1213", {"points": [v(24.38, -10.51) * mm, v(24.4, -10.54) * mm, v(24.44, -10.55) * mm, v(24.48, -10.56) * mm]});
            skFitSpline(sketch, "E1214", {"points": [v(24.48, -10.56) * mm, v(25.43, -10.97) * mm, v(26.38, -11.37) * mm, v(27.33, -11.77) * mm]});
            skFitSpline(sketch, "E1215", {"points": [v(27.33, -11.77) * mm, v(27.66, -11.91) * mm, v(28, -12.07) * mm, v(28.36, -12.14) * mm]});
            skFitSpline(sketch, "E1216", {"points": [v(28.36, -12.14) * mm, v(28.61, -12.19) * mm, v(28.76, -12.38) * mm, v(28.77, -12.6) * mm]});
            skFitSpline(sketch, "E1217", {"points": [v(28.77, -12.6) * mm, v(28.77, -12.82) * mm, v(28.63, -13.02) * mm, v(28.42, -13.07) * mm]});
            skFitSpline(sketch, "E1218", {"points": [v(28.42, -13.07) * mm, v(28.33, -13.1) * mm, v(28.23, -13.1) * mm, v(28.14, -13.08) * mm]});
            skFitSpline(sketch, "E1219", {"points": [v(28.14, -13.08) * mm, v(27.86, -13) * mm, v(27.58, -12.93) * mm, v(27.32, -12.82) * mm]});
            skFitSpline(sketch, "E1220", {"points": [v(27.32, -12.82) * mm, v(26.73, -12.58) * mm, v(26.15, -12.31) * mm, v(25.56, -12.05) * mm]});
            skFitSpline(sketch, "E1221", {"points": [v(25.56, -12.05) * mm, v(25.49, -12.02) * mm, v(25.42, -12) * mm, v(25.31, -12) * mm]});
            skFitSpline(sketch, "E1222", {"points": [v(25.31, -12) * mm, v(25.51, -12.3) * mm, v(25.71, -12.62) * mm, v(25.92, -12.93) * mm]});
            skFitSpline(sketch, "E1223", {"points": [v(25.92, -12.93) * mm, v(25.95, -12.98) * mm, v(26.02, -13.02) * mm, v(26.09, -13.05) * mm]});
            skFitSpline(sketch, "E1224", {"points": [v(26.09, -13.05) * mm, v(27, -13.4) * mm, v(27.92, -13.76) * mm, v(28.83, -14.11) * mm]});
            skFitSpline(sketch, "E1225", {"points": [v(28.83, -14.11) * mm, v(29.12, -14.22) * mm, v(29.23, -14.37) * mm, v(29.22, -14.65) * mm]});
            skFitSpline(sketch, "E1226", {"points": [v(29.22, -14.65) * mm, v(29.2, -14.88) * mm, v(29.04, -15.06) * mm, v(28.8, -15.06) * mm]});
            skFitSpline(sketch, "E1227", {"points": [v(28.8, -15.06) * mm, v(28.68, -15.06) * mm, v(28.55, -15.05) * mm, v(28.43, -15) * mm]});
            skFitSpline(sketch, "E1228", {"points": [v(28.43, -15) * mm, v(27.9, -14.81) * mm, v(27.38, -14.61) * mm, v(26.86, -14.42) * mm]});
            skFitSpline(sketch, "E1229", {"points": [v(26.86, -14.42) * mm, v(26.79, -14.39) * mm, v(26.71, -14.37) * mm, v(26.59, -14.32) * mm]});
            skFitSpline(sketch, "E1230", {"points": [v(26.59, -14.32) * mm, v(26.68, -14.5) * mm, v(26.76, -14.64) * mm, v(26.83, -14.77) * mm]});
            skFitSpline(sketch, "E1231", {"points": [v(26.83, -14.77) * mm, v(27, -15.1) * mm, v(27.19, -15.42) * mm, v(27.37, -15.73) * mm]});
            skFitSpline(sketch, "E1232", {"points": [v(27.37, -15.73) * mm, v(27.51, -15.98) * mm, v(27.66, -16.23) * mm, v(27.8, -16.48) * mm]});
            skFitSpline(sketch, "E1233", {"points": [v(27.8, -16.48) * mm, v(27.92, -16.66) * mm, v(27.94, -16.85) * mm, v(27.82, -17.04) * mm]});
            skFitSpline(sketch, "E1234", {"points": [v(27.82, -17.04) * mm, v(27.7, -17.21) * mm, v(27.53, -17.3) * mm, v(27.32, -17.27) * mm]});
            skFitSpline(sketch, "E1235", {"points": [v(27.32, -17.27) * mm, v(27.15, -17.25) * mm, v(27.03, -17.15) * mm, v(26.94, -17) * mm]});
            skFitSpline(sketch, "E1236", {"points": [v(26.94, -17) * mm, v(26.73, -16.64) * mm, v(26.5, -16.28) * mm, v(26.3, -15.92) * mm]});
            skFitSpline(sketch, "E1237", {"points": [v(26.3, -15.92) * mm, v(26.1, -15.6) * mm, v(25.93, -15.28) * mm, v(25.75, -14.96) * mm]});
            skFitSpline(sketch, "E1238", {"points": [v(25.75, -14.96) * mm, v(25.73, -14.94) * mm, v(25.71, -14.91) * mm, v(25.67, -14.85) * mm]});
            skFitSpline(sketch, "E1239", {"points": [v(25.67, -14.85) * mm, v(25.6, -15.27) * mm, v(25.53, -15.65) * mm, v(25.47, -16.03) * mm]});
            skFitSpline(sketch, "E1240", {"points": [v(25.47, -16.03) * mm, v(25.42, -16.33) * mm, v(25.37, -16.64) * mm, v(25.3, -16.95) * mm]});
            skFitSpline(sketch, "E1241", {"points": [v(25.3, -16.95) * mm, v(25.26, -17.18) * mm, v(25.07, -17.33) * mm, v(24.86, -17.35) * mm]});
            skFitSpline(sketch, "E1242", {"points": [v(24.86, -17.35) * mm, v(24.68, -17.36) * mm, v(24.46, -17.24) * mm, v(24.4, -17.06) * mm]});
            skFitSpline(sketch, "E1243", {"points": [v(24.4, -17.06) * mm, v(24.36, -16.95) * mm, v(24.36, -16.82) * mm, v(24.37, -16.7) * mm]});
            skFitSpline(sketch, "E1244", {"points": [v(24.37, -16.7) * mm, v(24.4, -16.48) * mm, v(24.45, -16.27) * mm, v(24.48, -16.05) * mm]});
            skFitSpline(sketch, "E1245", {"points": [v(24.48, -16.05) * mm, v(24.6, -15.28) * mm, v(24.72, -14.52) * mm, v(24.83, -13.75) * mm]});
            skFitSpline(sketch, "E1246", {"points": [v(24.83, -13.75) * mm, v(24.84, -13.68) * mm, v(24.82, -13.6) * mm, v(24.78, -13.52) * mm]});
            skFitSpline(sketch, "E1247", {"points": [v(24.78, -13.52) * mm, v(24.63, -13.21) * mm, v(24.46, -12.9) * mm, v(24.25, -12.6) * mm]});
            skFitSpline(sketch, "E1248", {"points": [v(24.25, -12.6) * mm, v(24.22, -12.8) * mm, v(24.2, -13) * mm, v(24.18, -13.2) * mm]});
            skFitSpline(sketch, "E1249", {"points": [v(24.18, -13.2) * mm, v(24.1, -13.87) * mm, v(24.02, -14.53) * mm, v(23.93, -15.2) * mm]});
            skFitSpline(sketch, "E1250", {"points": [v(23.93, -15.2) * mm, v(23.9, -15.34) * mm, v(23.85, -15.5) * mm, v(23.8, -15.63) * mm]});
            skFitSpline(sketch, "E1251", {"points": [v(23.8, -15.63) * mm, v(23.7, -15.87) * mm, v(23.46, -16) * mm, v(23.24, -15.94) * mm]});
            skFitSpline(sketch, "E1252", {"points": [v(23.24, -15.94) * mm, v(22.98, -15.86) * mm, v(22.83, -15.65) * mm, v(22.88, -15.37) * mm]});
            skFitSpline(sketch, "E1253", {"points": [v(22.88, -15.37) * mm, v(22.9, -15.25) * mm, v(22.95, -15.13) * mm, v(22.97, -15) * mm]});
            skFitSpline(sketch, "E1254", {"points": [v(22.97, -15) * mm, v(23.03, -14.7) * mm, v(23.07, -14.37) * mm, v(23.1, -14.06) * mm]});
            skFitSpline(sketch, "E1255", {"points": [v(23.1, -14.06) * mm, v(23.2, -13.3) * mm, v(23.3, -12.54) * mm, v(23.39, -11.78) * mm]});
            skFitSpline(sketch, "E1256", {"points": [v(23.39, -11.78) * mm, v(23.41, -11.56) * mm, v(23.45, -11.34) * mm, v(23.48, -11.12) * mm]});
            skFitSpline(sketch, "E1257", {"points": [v(23.48, -11.12) * mm, v(23.49, -11.08) * mm, v(23.49, -11.04) * mm, v(23.47, -11) * mm]});
            skFitSpline(sketch, "E1258", {"points": [v(23.47, -11) * mm, v(23.38, -10.82) * mm, v(23.28, -10.64) * mm, v(23.14, -10.47) * mm]});
            skFitSpline(sketch, "E1259", {"points": [v(23.14, -10.47) * mm, v(23.08, -10.84) * mm, v(23.03, -11.21) * mm, v(22.98, -11.58) * mm]});
            skFitSpline(sketch, "E1260", {"points": [v(22.98, -11.58) * mm, v(22.9, -12.07) * mm, v(22.84, -12.55) * mm, v(22.76, -13.03) * mm]});
            skFitSpline(sketch, "E1261", {"points": [v(22.76, -13.03) * mm, v(22.76, -13.07) * mm, v(22.75, -13.1) * mm, v(22.74, -13.14) * mm]});
            skFitSpline(sketch, "E1262", {"points": [v(22.74, -13.14) * mm, v(22.66, -13.43) * mm, v(22.42, -13.58) * mm, v(22.16, -13.52) * mm]});
            skFitSpline(sketch, "E1263", {"points": [v(22.16, -13.52) * mm, v(21.91, -13.47) * mm, v(21.75, -13.22) * mm, v(21.79, -12.96) * mm]});
            skFitSpline(sketch, "E1264", {"points": [v(21.79, -12.96) * mm, v(21.85, -12.53) * mm, v(21.92, -12.1) * mm, v(21.98, -11.68) * mm]});
            skFitSpline(sketch, "E1265", {"points": [v(21.98, -11.68) * mm, v(22.07, -10.97) * mm, v(22.16, -10.26) * mm, v(22.24, -9.55) * mm]});
            skFitSpline(sketch, "E1266", {"points": [v(22.24, -9.55) * mm, v(22.25, -9.47) * mm, v(22.26, -9.39) * mm, v(22.28, -9.3) * mm]});
            skFitSpline(sketch, "E1267", {"points": [v(22.28, -9.3) * mm, v(22.33, -9) * mm, v(22.3, -8.93) * mm, v(22.07, -8.63) * mm]});
            skFitSpline(sketch, "E1268", {"points": [v(22.07, -8.63) * mm, v(22.03, -8.89) * mm, v(22, -9.12) * mm, v(21.96, -9.35) * mm]});
            skFitSpline(sketch, "E1269", {"points": [v(21.96, -9.35) * mm, v(21.91, -9.68) * mm, v(21.87, -10.01) * mm, v(21.8, -10.34) * mm]});
            skFitSpline(sketch, "E1270", {"points": [v(21.8, -10.34) * mm, v(21.75, -10.67) * mm, v(21.46, -10.85) * mm, v(21.17, -10.75) * mm]});
            skFitSpline(sketch, "E1271", {"points": [v(21.17, -10.75) * mm, v(20.98, -10.68) * mm, v(20.85, -10.52) * mm, v(20.86, -10.31) * mm]});
            skFitSpline(sketch, "E1272", {"points": [v(20.86, -10.31) * mm, v(20.86, -10.12) * mm, v(20.9, -9.92) * mm, v(20.92, -9.72) * mm]});
            skFitSpline(sketch, "E1273", {"points": [v(20.92, -9.72) * mm, v(21.02, -9.07) * mm, v(21.13, -8.43) * mm, v(21.23, -7.78) * mm]});
            skFitSpline(sketch, "E1274", {"points": [v(21.23, -7.78) * mm, v(21.25, -7.62) * mm, v(21.28, -7.46) * mm, v(21.3, -7.22) * mm]});
            skFitSpline(sketch, "E1275", {"points": [v(21.3, -7.22) * mm, v(21.25, -7.12) * mm, v(21.14, -6.96) * mm, v(21, -6.76) * mm]});
            skFitSpline(sketch, "E1276", {"points": [v(21, -6.76) * mm, v(20.93, -6.93) * mm, v(20.87, -7.07) * mm, v(20.81, -7.2) * mm]});
            skFitSpline(sketch, "E1277", {"points": [v(20.81, -7.2) * mm, v(20.38, -8.24) * mm, v(19.94, -9.28) * mm, v(19.51, -10.32) * mm]});
            skFitSpline(sketch, "E1278", {"points": [v(19.51, -10.32) * mm, v(19.31, -10.83) * mm, v(19.15, -11.34) * mm, v(18.96, -11.85) * mm]});
            skFitSpline(sketch, "E1279", {"points": [v(18.96, -11.85) * mm, v(18.86, -12.1) * mm, v(18.76, -12.34) * mm, v(18.64, -12.58) * mm]});
            skFitSpline(sketch, "E1280", {"points": [v(18.64, -12.58) * mm, v(18.58, -12.7) * mm, v(18.57, -12.81) * mm, v(18.63, -12.94) * mm]});
            skFitSpline(sketch, "E1281", {"points": [v(18.63, -12.94) * mm, v(18.75, -13.19) * mm, v(18.88, -13.44) * mm, v(19, -13.69) * mm]});
            skFitSpline(sketch, "E1282", {"points": [v(19, -13.69) * mm, v(19.18, -14.07) * mm, v(19.35, -14.46) * mm, v(19.53, -14.84) * mm]});
            skFitSpline(sketch, "E1283", {"points": [v(19.53, -14.84) * mm, v(19.62, -15.02) * mm, v(19.73, -15.19) * mm, v(19.82, -15.36) * mm]});
            skFitSpline(sketch, "E1284", {"points": [v(19.82, -15.36) * mm, v(20.03, -15.78) * mm, v(20.24, -16.19) * mm, v(20.45, -16.6) * mm]});
            skFitSpline(sketch, "E1285", {"points": [v(20.45, -16.6) * mm, v(20.47, -16.66) * mm, v(20.5, -16.72) * mm, v(20.5, -16.79) * mm]});
            skFitSpline(sketch, "E1286", {"points": [v(20.5, -16.79) * mm, v(20.56, -17.04) * mm, v(20.43, -17.28) * mm, v(20.2, -17.36) * mm]});
            skFitSpline(sketch, "E1287", {"points": [v(20.2, -17.36) * mm, v(19.96, -17.45) * mm, v(19.7, -17.34) * mm, v(19.59, -17.1) * mm]});
            skFitSpline(sketch, "E1288", {"points": [v(19.59, -17.1) * mm, v(19.47, -16.87) * mm, v(19.37, -16.63) * mm, v(19.26, -16.4) * mm]});
            skFitSpline(sketch, "E1289", {"points": [v(19.26, -16.4) * mm, v(19.2, -16.25) * mm, v(19.13, -16.1) * mm, v(19.04, -15.96) * mm]});
            skFitSpline(sketch, "E1290", {"points": [v(19.04, -15.96) * mm, v(18.75, -15.54) * mm, v(18.57, -15.06) * mm, v(18.36, -14.6) * mm]});
            skFitSpline(sketch, "E1291", {"points": [v(18.36, -14.6) * mm, v(18.26, -14.38) * mm, v(18.15, -14.17) * mm, v(18.02, -13.91) * mm]});
            skFitSpline(sketch, "E1292", {"points": [v(18.02, -13.91) * mm, v(17.9, -14.16) * mm, v(17.79, -14.36) * mm, v(17.69, -14.56) * mm]});
            skFitSpline(sketch, "E1293", {"points": [v(17.69, -14.56) * mm, v(17.65, -14.63) * mm, v(17.62, -14.7) * mm, v(17.6, -14.78) * mm]});
            skFitSpline(sketch, "E1294", {"points": [v(17.6, -14.78) * mm, v(17.41, -15.23) * mm, v(17.18, -15.64) * mm, v(16.94, -16.06) * mm]});
            skFitSpline(sketch, "E1295", {"points": [v(16.94, -16.06) * mm, v(16.76, -16.36) * mm, v(16.63, -16.7) * mm, v(16.48, -17.03) * mm]});
            skFitSpline(sketch, "E1296", {"points": [v(16.48, -17.03) * mm, v(16.36, -17.31) * mm, v(16.13, -17.45) * mm, v(15.88, -17.37) * mm]});
            skFitSpline(sketch, "E1297", {"points": [v(15.88, -17.37) * mm, v(15.66, -17.3) * mm, v(15.53, -17.15) * mm, v(15.53, -16.92) * mm]});
            skFitSpline(sketch, "E1298", {"points": [v(15.53, -16.92) * mm, v(15.53, -16.8) * mm, v(15.55, -16.67) * mm, v(15.6, -16.57) * mm]});
            skFitSpline(sketch, "E1299", {"points": [v(15.6, -16.57) * mm, v(15.85, -16.09) * mm, v(16.1, -15.6) * mm, v(16.36, -15.13) * mm]});
            skFitSpline(sketch, "E1300", {"points": [v(16.36, -15.13) * mm, v(16.47, -14.9) * mm, v(16.57, -14.66) * mm, v(16.68, -14.43) * mm]});
            skFitSpline(sketch, "E1301", {"points": [v(16.68, -14.43) * mm, v(16.88, -14.02) * mm, v(17.08, -13.61) * mm, v(17.28, -13.2) * mm]});
            skFitSpline(sketch, "E1302", {"points": [v(17.28, -13.2) * mm, v(17.3, -13.16) * mm, v(17.33, -13.1) * mm, v(17.35, -13.06) * mm]});
            skFitSpline(sketch, "E1303", {"points": [v(17.35, -13.06) * mm, v(17.45, -12.87) * mm, v(17.45, -12.7) * mm, v(17.36, -12.5) * mm]});
            skFitSpline(sketch, "E1304", {"points": [v(17.36, -12.5) * mm, v(17.12, -11.94) * mm, v(16.92, -11.37) * mm, v(16.7, -10.8) * mm]});
            skFitSpline(sketch, "E1305", {"points": [v(16.7, -10.8) * mm, v(16.46, -10.2) * mm, v(16.2, -9.6) * mm, v(15.96, -9) * mm]});
            skFitSpline(sketch, "E1306", {"points": [v(15.96, -9) * mm, v(15.82, -8.66) * mm, v(15.68, -8.31) * mm, v(15.54, -7.96) * mm]});
            skFitSpline(sketch, "E1307", {"points": [v(15.54, -7.96) * mm, v(15.38, -7.57) * mm, v(15.21, -7.19) * mm, v(15.03, -6.76) * mm]});
            skFitSpline(sketch, "E1308", {"points": [v(15.03, -6.76) * mm, v(14.92, -6.93) * mm, v(14.82, -7.07) * mm, v(14.73, -7.22) * mm]});
            skFitSpline(sketch, "E1309", {"points": [v(14.73, -7.22) * mm, v(14.71, -7.25) * mm, v(14.73, -7.32) * mm, v(14.74, -7.37) * mm]});
            skFitSpline(sketch, "E1310", {"points": [v(14.74, -7.37) * mm, v(14.76, -7.5) * mm, v(14.79, -7.62) * mm, v(14.8, -7.74) * mm]});
            skFitSpline(sketch, "E1311", {"points": [v(14.8, -7.74) * mm, v(14.83, -7.88) * mm, v(14.84, -8.02) * mm, v(14.87, -8.17) * mm]});
            skFitSpline(sketch, "E1312", {"points": [v(14.87, -8.17) * mm, v(14.97, -8.85) * mm, v(15.09, -9.54) * mm, v(15.19, -10.22) * mm]});
            skFitSpline(sketch, "E1313", {"points": [v(15.19, -10.22) * mm, v(15.22, -10.49) * mm, v(15.05, -10.71) * mm, v(14.79, -10.77) * mm]});
            skFitSpline(sketch, "E1314", {"points": [v(14.79, -10.77) * mm, v(14.54, -10.82) * mm, v(14.3, -10.66) * mm, v(14.24, -10.39) * mm]});
            skFitSpline(sketch, "E1315", {"points": [v(14.24, -10.39) * mm, v(14.18, -10.1) * mm, v(14.14, -9.8) * mm, v(14.1, -9.51) * mm]});
            skFitSpline(sketch, "E1316", {"points": [v(14.1, -9.51) * mm, v(14.05, -9.23) * mm, v(14.02, -8.95) * mm, v(13.98, -8.66) * mm]});
            skFitSpline(sketch, "E1317", {"points": [v(13.98, -8.66) * mm, v(13.79, -8.82) * mm, v(13.73, -8.96) * mm, v(13.75, -9.17) * mm]});
            skFitSpline(sketch, "E1318", {"points": [v(13.75, -9.17) * mm, v(13.86, -10.4) * mm, v(14.02, -11.62) * mm, v(14.23, -12.84) * mm]});
            skFitSpline(sketch, "E1319", {"points": [v(14.23, -12.84) * mm, v(14.24, -12.91) * mm, v(14.25, -12.98) * mm, v(14.25, -13.06) * mm]});
            skFitSpline(sketch, "E1320", {"points": [v(14.25, -13.06) * mm, v(14.24, -13.3) * mm, v(14.08, -13.5) * mm, v(13.85, -13.52) * mm]});
            skFitSpline(sketch, "E1321", {"points": [v(13.85, -13.52) * mm, v(13.6, -13.56) * mm, v(13.38, -13.43) * mm, v(13.31, -13.19) * mm]});
            skFitSpline(sketch, "E1322", {"points": [v(13.31, -13.19) * mm, v(13.26, -13) * mm, v(13.23, -12.8) * mm, v(13.2, -12.6) * mm]});
            skFitSpline(sketch, "E1323", {"points": [v(13.2, -12.6) * mm, v(13.1, -11.9) * mm, v(13, -11.2) * mm, v(12.9, -10.46) * mm]});
            skFitSpline(sketch, "E1324", {"points": [v(12.9, -10.46) * mm, v(12.76, -10.59) * mm, v(12.72, -10.74) * mm, v(12.63, -10.86) * mm]});
            skFitSpline(sketch, "E1325", {"points": [v(12.63, -10.86) * mm, v(12.53, -11) * mm, v(12.56, -11.14) * mm, v(12.59, -11.3) * mm]});
            skFitSpline(sketch, "E1326", {"points": [v(12.59, -11.3) * mm, v(12.67, -11.81) * mm, v(12.73, -12.34) * mm, v(12.8, -12.86) * mm]});
            skFitSpline(sketch, "E1327", {"points": [v(12.8, -12.86) * mm, v(12.87, -13.54) * mm, v(12.95, -14.22) * mm, v(13.04, -14.9) * mm]});
            skFitSpline(sketch, "E1328", {"points": [v(13.04, -14.9) * mm, v(13.05, -15.03) * mm, v(13.1, -15.16) * mm, v(13.14, -15.3) * mm]});
            skFitSpline(sketch, "E1329", {"points": [v(13.14, -15.3) * mm, v(13.22, -15.6) * mm, v(13.1, -15.84) * mm, v(12.8, -15.93) * mm]});
            skFitSpline(sketch, "E1330", {"points": [v(12.8, -15.93) * mm, v(12.56, -16) * mm, v(12.33, -15.86) * mm, v(12.22, -15.58) * mm]});
            skFitSpline(sketch, "E1331", {"points": [v(12.22, -15.58) * mm, v(12.07, -15.22) * mm, v(12.03, -14.83) * mm, v(12, -14.45) * mm]});
            skFitSpline(sketch, "E1332", {"points": [v(12, -14.45) * mm, v(11.93, -13.86) * mm, v(11.86, -13.27) * mm, v(11.8, -12.67) * mm]});
            skFitSpline(sketch, "E1333", {"points": [v(11.8, -12.67) * mm, v(11.8, -12.65) * mm, v(11.78, -12.63) * mm, v(11.76, -12.58) * mm]});
            skFitSpline(sketch, "E1334", {"points": [v(55.44, 4.12) * mm, v(55.74, 3.84) * mm, v(56.02, 3.58) * mm, v(56.3, 3.32) * mm]});
            skFitSpline(sketch, "E1335", {"points": [v(56.3, 3.32) * mm, v(56.92, 2.73) * mm, v(57.54, 2.15) * mm, v(58.16, 1.56) * mm]});
            skFitSpline(sketch, "E1336", {"points": [v(58.16, 1.56) * mm, v(58.39, 1.35) * mm, v(58.61, 1.13) * mm, v(58.84, 0.92) * mm]});
            skFitSpline(sketch, "E1337", {"points": [v(58.84, 0.92) * mm, v(59.09, 0.67) * mm, v(59.34, 0.42) * mm, v(59.6, 0.19) * mm]});
            skFitSpline(sketch, "E1338", {"points": [v(59.6, 0.19) * mm, v(59.65, 0.14) * mm, v(59.73, 0.1) * mm, v(59.8, 0.1) * mm]});
            skFitSpline(sketch, "E1339", {"points": [v(59.8, 0.1) * mm, v(60.17, 0.06) * mm, v(60.54, 0.03) * mm, v(60.91, 0) * mm]});
            skFitSpline(sketch, "E1340", {"points": [v(60.91, 0) * mm, v(61.02, 0) * mm, v(61.12, -0.03) * mm, v(61.22, -0.02) * mm]});
            skFitSpline(sketch, "E1341", {"points": [v(61.22, -0.02) * mm, v(61.33, -0.02) * mm, v(61.82, 0.4) * mm, v(61.84, 0.51) * mm]});
            skFitSpline(sketch, "E1342", {"points": [v(61.84, 0.51) * mm, v(61.88, 0.68) * mm, v(61.9, 0.84) * mm, v(61.93, 1) * mm]});
            skFitSpline(sketch, "E1343", {"points": [v(61.93, 1) * mm, v(61.95, 1.11) * mm, v(61.92, 1.2) * mm, v(61.85, 1.3) * mm]});
            skFitSpline(sketch, "E1344", {"points": [v(61.85, 1.3) * mm, v(61.66, 1.56) * mm, v(61.44, 1.81) * mm, v(61.3, 2.1) * mm]});
            skFitSpline(sketch, "E1345", {"points": [v(61.3, 2.1) * mm, v(61.14, 2.38) * mm, v(60.94, 2.52) * mm, v(60.65, 2.6) * mm]});
            skFitSpline(sketch, "E1346", {"points": [v(60.65, 2.6) * mm, v(59.78, 2.83) * mm, v(58.92, 3.07) * mm, v(58.07, 3.32) * mm]});
            skFitSpline(sketch, "E1347", {"points": [v(58.07, 3.32) * mm, v(57.23, 3.57) * mm, v(56.4, 3.85) * mm, v(55.55, 4.1) * mm]});
            skFitSpline(sketch, "E1348", {"points": [v(55.55, 4.1) * mm, v(55.53, 4.12) * mm, v(55.5, 4.12) * mm, v(55.44, 4.12) * mm]});
            skFitSpline(sketch, "E1349", {"points": [v(63.54, 8.74) * mm, v(63.53, 8.75) * mm, v(63.52, 8.75) * mm, v(63.5, 8.75) * mm]});
            skFitSpline(sketch, "E1350", {"points": [v(63.5, 8.75) * mm, v(63.42, 8.4) * mm, v(63.33, 8.04) * mm, v(63.25, 7.68) * mm]});
            skFitSpline(sketch, "E1351", {"points": [v(63.25, 7.68) * mm, v(63, 6.6) * mm, v(62.74, 5.53) * mm, v(62.48, 4.45) * mm]});
            skFitSpline(sketch, "E1352", {"points": [v(62.48, 4.45) * mm, v(62.38, 4.04) * mm, v(62.28, 3.63) * mm, v(62.18, 3.22) * mm]});
            skFitSpline(sketch, "E1353", {"points": [v(62.18, 3.22) * mm, v(62.17, 3.14) * mm, v(62.18, 3.04) * mm, v(62.22, 2.97) * mm]});
            skFitSpline(sketch, "E1354", {"points": [v(62.22, 2.97) * mm, v(62.36, 2.64) * mm, v(62.53, 2.32) * mm, v(62.67, 2) * mm]});
            skFitSpline(sketch, "E1355", {"points": [v(62.67, 2) * mm, v(62.78, 1.75) * mm, v(62.9, 1.57) * mm, v(63.2, 1.54) * mm]});
            skFitSpline(sketch, "E1356", {"points": [v(63.2, 1.54) * mm, v(63.25, 1.53) * mm, v(63.3, 1.5) * mm, v(63.35, 1.47) * mm]});
            skFitSpline(sketch, "E1357", {"points": [v(63.35, 1.47) * mm, v(63.53, 1.4) * mm, v(64.12, 1.57) * mm, v(64.23, 1.73) * mm]});
            skFitSpline(sketch, "E1358", {"points": [v(64.23, 1.73) * mm, v(64.25, 1.76) * mm, v(64.26, 1.8) * mm, v(64.28, 1.84) * mm]});
            skFitSpline(sketch, "E1359", {"points": [v(64.28, 1.84) * mm, v(64.46, 2.22) * mm, v(64.64, 2.6) * mm, v(64.82, 2.98) * mm]});
            skFitSpline(sketch, "E1360", {"points": [v(64.82, 2.98) * mm, v(64.85, 3.05) * mm, v(64.87, 3.14) * mm, v(64.85, 3.2) * mm]});
            skFitSpline(sketch, "E1361", {"points": [v(64.85, 3.2) * mm, v(64.8, 3.5) * mm, v(64.72, 3.8) * mm, v(64.65, 4.1) * mm]});
            skFitSpline(sketch, "E1362", {"points": [v(64.65, 4.1) * mm, v(64.48, 4.74) * mm, v(64.3, 5.4) * mm, v(64.15, 6.04) * mm]});
            skFitSpline(sketch, "E1363", {"points": [v(64.15, 6.04) * mm, v(63.97, 6.76) * mm, v(63.81, 7.49) * mm, v(63.65, 8.2) * mm]});
            skFitSpline(sketch, "E1364", {"points": [v(63.65, 8.2) * mm, v(63.6, 8.39) * mm, v(63.57, 8.56) * mm, v(63.54, 8.74) * mm]});
            skFitSpline(sketch, "E1365", {"points": [v(71.58, -5.18) * mm, v(71.28, -4.9) * mm, v(71, -4.64) * mm, v(70.72, -4.38) * mm]});
            skFitSpline(sketch, "E1366", {"points": [v(70.72, -4.38) * mm, v(70.1, -3.79) * mm, v(69.47, -3.2) * mm, v(68.84, -2.6) * mm]});
            skFitSpline(sketch, "E1367", {"points": [v(68.84, -2.6) * mm, v(68.62, -2.4) * mm, v(68.4, -2.18) * mm, v(68.18, -1.97) * mm]});
            skFitSpline(sketch, "E1368", {"points": [v(68.18, -1.97) * mm, v(67.94, -1.73) * mm, v(67.7, -1.5) * mm, v(67.44, -1.26) * mm]});
            skFitSpline(sketch, "E1369", {"points": [v(67.44, -1.26) * mm, v(67.37, -1.2) * mm, v(67.27, -1.17) * mm, v(67.18, -1.16) * mm]});
            skFitSpline(sketch, "E1370", {"points": [v(67.18, -1.16) * mm, v(66.83, -1.12) * mm, v(66.47, -1.09) * mm, v(66.11, -1.07) * mm]});
            skFitSpline(sketch, "E1371", {"points": [v(66.11, -1.07) * mm, v(65.98, -1.06) * mm, v(65.82, -1.04) * mm, v(65.72, -1.1) * mm]});
            skFitSpline(sketch, "E1372", {"points": [v(65.72, -1.1) * mm, v(65.54, -1.2) * mm, v(65.4, -1.35) * mm, v(65.24, -1.48) * mm]});
            skFitSpline(sketch, "E1373", {"points": [v(65.24, -1.48) * mm, v(65.22, -1.5) * mm, v(65.2, -1.54) * mm, v(65.2, -1.57) * mm]});
            skFitSpline(sketch, "E1374", {"points": [v(65.2, -1.57) * mm, v(65.16, -1.77) * mm, v(65.12, -1.97) * mm, v(65.1, -2.18) * mm]});
            skFitSpline(sketch, "E1375", {"points": [v(65.1, -2.18) * mm, v(65.1, -2.24) * mm, v(65.15, -2.31) * mm, v(65.19, -2.37) * mm]});
            skFitSpline(sketch, "E1376", {"points": [v(65.19, -2.37) * mm, v(65.37, -2.63) * mm, v(65.59, -2.87) * mm, v(65.73, -3.16) * mm]});
            skFitSpline(sketch, "E1377", {"points": [v(65.73, -3.16) * mm, v(65.89, -3.46) * mm, v(66.1, -3.62) * mm, v(66.42, -3.68) * mm]});
            skFitSpline(sketch, "E1378", {"points": [v(66.42, -3.68) * mm, v(66.43, -3.68) * mm, v(66.44, -3.68) * mm, v(66.44, -3.68) * mm]});
            skFitSpline(sketch, "E1379", {"points": [v(66.44, -3.68) * mm, v(67.23, -3.9) * mm, v(68.01, -4.1) * mm, v(68.8, -4.34) * mm]});
            skFitSpline(sketch, "E1380", {"points": [v(68.8, -4.34) * mm, v(69.68, -4.6) * mm, v(70.56, -4.9) * mm, v(71.44, -5.17) * mm]});
            skFitSpline(sketch, "E1381", {"points": [v(71.44, -5.17) * mm, v(71.48, -5.18) * mm, v(71.51, -5.18) * mm, v(71.58, -5.18) * mm]});
            skFitSpline(sketch, "E1382", {"points": [v(55.44, -5.18) * mm, v(55.52, -5.17) * mm, v(55.55, -5.18) * mm, v(55.58, -5.17) * mm]});
            skFitSpline(sketch, "E1383", {"points": [v(55.58, -5.17) * mm, v(56.15, -5) * mm, v(56.72, -4.8) * mm, v(57.3, -4.63) * mm]});
            skFitSpline(sketch, "E1384", {"points": [v(57.3, -4.63) * mm, v(58.11, -4.39) * mm, v(58.93, -4.15) * mm, v(59.75, -3.91) * mm]});
            skFitSpline(sketch, "E1385", {"points": [v(59.75, -3.91) * mm, v(60.14, -3.8) * mm, v(60.53, -3.7) * mm, v(60.92, -3.57) * mm]});
            skFitSpline(sketch, "E1386", {"points": [v(60.92, -3.57) * mm, v(61, -3.55) * mm, v(61.08, -3.49) * mm, v(61.12, -3.42) * mm]});
            skFitSpline(sketch, "E1387", {"points": [v(61.12, -3.42) * mm, v(61.37, -3.07) * mm, v(61.6, -2.7) * mm, v(61.86, -2.36) * mm]});
            skFitSpline(sketch, "E1388", {"points": [v(61.86, -2.36) * mm, v(61.94, -2.25) * mm, v(61.95, -2.14) * mm, v(61.93, -2.02) * mm]});
            skFitSpline(sketch, "E1389", {"points": [v(61.93, -2.02) * mm, v(61.87, -1.7) * mm, v(61.82, -1.39) * mm, v(61.49, -1.23) * mm]});
            skFitSpline(sketch, "E1390", {"points": [v(61.49, -1.23) * mm, v(61.48, -1.22) * mm, v(61.48, -1.21) * mm, v(61.47, -1.2) * mm]});
            skFitSpline(sketch, "E1391", {"points": [v(61.47, -1.2) * mm, v(61.37, -1.1) * mm, v(61.25, -1.04) * mm, v(61.1, -1.06) * mm]});
            skFitSpline(sketch, "E1392", {"points": [v(61.1, -1.06) * mm, v(60.66, -1.1) * mm, v(60.22, -1.12) * mm, v(59.78, -1.16) * mm]});
            skFitSpline(sketch, "E1393", {"points": [v(59.78, -1.16) * mm, v(59.72, -1.17) * mm, v(59.65, -1.2) * mm, v(59.6, -1.25) * mm]});
            skFitSpline(sketch, "E1394", {"points": [v(59.6, -1.25) * mm, v(59.32, -1.51) * mm, v(59.06, -1.78) * mm, v(58.79, -2.03) * mm]});
            skFitSpline(sketch, "E1395", {"points": [v(58.79, -2.03) * mm, v(58.45, -2.36) * mm, v(58.12, -2.68) * mm, v(57.78, -3) * mm]});
            skFitSpline(sketch, "E1396", {"points": [v(57.78, -3) * mm, v(57.1, -3.64) * mm, v(56.4, -4.29) * mm, v(55.72, -4.94) * mm]});
            skFitSpline(sketch, "E1397", {"points": [v(55.72, -4.94) * mm, v(55.64, -5.01) * mm, v(55.56, -5.08) * mm, v(55.44, -5.18) * mm]});
            skFitSpline(sketch, "E1398", {"points": [v(71.6, 4.13) * mm, v(71.2, 4) * mm, v(70.82, 3.9) * mm, v(70.45, 3.78) * mm]});
            skFitSpline(sketch, "E1399", {"points": [v(70.45, 3.78) * mm, v(69.62, 3.54) * mm, v(68.8, 3.29) * mm, v(67.97, 3.04) * mm]});
            skFitSpline(sketch, "E1400", {"points": [v(67.97, 3.04) * mm, v(67.7, 2.96) * mm, v(67.4, 2.88) * mm, v(67.12, 2.8) * mm]});
            skFitSpline(sketch, "E1401", {"points": [v(67.12, 2.8) * mm, v(66.79, 2.7) * mm, v(66.45, 2.6) * mm, v(66.11, 2.5) * mm]});
            skFitSpline(sketch, "E1402", {"points": [v(66.11, 2.5) * mm, v(66.04, 2.48) * mm, v(65.96, 2.42) * mm, v(65.91, 2.36) * mm]});
            skFitSpline(sketch, "E1403", {"points": [v(65.91, 2.36) * mm, v(65.68, 2.04) * mm, v(65.48, 1.7) * mm, v(65.24, 1.4) * mm]});
            skFitSpline(sketch, "E1404", {"points": [v(65.24, 1.4) * mm, v(65.1, 1.21) * mm, v(65.11, 1.03) * mm, v(65.13, 0.82) * mm]});
            skFitSpline(sketch, "E1405", {"points": [v(65.13, 0.82) * mm, v(65.16, 0.53) * mm, v(65.27, 0.34) * mm, v(65.5, 0.2) * mm]});
            skFitSpline(sketch, "E1406", {"points": [v(65.5, 0.2) * mm, v(65.58, 0.15) * mm, v(65.63, 0.08) * mm, v(65.7, 0.03) * mm]});
            skFitSpline(sketch, "E1407", {"points": [v(65.7, 0.03) * mm, v(65.74, 0) * mm, v(65.8, -0.02) * mm, v(65.83, -0.02) * mm]});
            skFitSpline(sketch, "E1408", {"points": [v(65.83, -0.02) * mm, v(66, 0) * mm, v(66.18, 0.02) * mm, v(66.36, 0.03) * mm]});
            skFitSpline(sketch, "E1409", {"points": [v(66.36, 0.03) * mm, v(66.57, 0.05) * mm, v(66.78, 0.1) * mm, v(67, 0.07) * mm]});
            skFitSpline(sketch, "E1410", {"points": [v(67, 0.07) * mm, v(67.18, 0.06) * mm, v(67.38, 0.07) * mm, v(67.51, 0.25) * mm]});
            skFitSpline(sketch, "E1411", {"points": [v(67.51, 0.25) * mm, v(67.56, 0.31) * mm, v(67.63, 0.36) * mm, v(67.69, 0.41) * mm]});
            skFitSpline(sketch, "E1412", {"points": [v(67.69, 0.41) * mm, v(67.95, 0.67) * mm, v(68.2, 0.93) * mm, v(68.47, 1.19) * mm]});
            skFitSpline(sketch, "E1413", {"points": [v(68.47, 1.19) * mm, v(68.74, 1.44) * mm, v(69, 1.7) * mm, v(69.27, 1.95) * mm]});
            skFitSpline(sketch, "E1414", {"points": [v(69.27, 1.95) * mm, v(69.75, 2.4) * mm, v(70.23, 2.85) * mm, v(70.72, 3.3) * mm]});
            skFitSpline(sketch, "E1415", {"points": [v(70.72, 3.3) * mm, v(71, 3.57) * mm, v(71.29, 3.84) * mm, v(71.6, 4.13) * mm]});
            skFitSpline(sketch, "E1416", {"points": [v(63.5, -9.84) * mm, v(63.53, -9.8) * mm, v(63.56, -9.76) * mm, v(63.56, -9.72) * mm]});
            skFitSpline(sketch, "E1417", {"points": [v(63.56, -9.72) * mm, v(63.68, -9.18) * mm, v(63.8, -8.63) * mm, v(63.92, -8.1) * mm]});
            skFitSpline(sketch, "E1418", {"points": [v(63.92, -8.1) * mm, v(64.13, -7.2) * mm, v(64.36, -6.3) * mm, v(64.58, -5.4) * mm]});
            skFitSpline(sketch, "E1419", {"points": [v(64.58, -5.4) * mm, v(64.67, -5.03) * mm, v(64.75, -4.67) * mm, v(64.85, -4.3) * mm]});
            skFitSpline(sketch, "E1420", {"points": [v(64.85, -4.3) * mm, v(64.88, -4.2) * mm, v(64.86, -4.12) * mm, v(64.82, -4.03) * mm]});
            skFitSpline(sketch, "E1421", {"points": [v(64.82, -4.03) * mm, v(64.66, -3.7) * mm, v(64.5, -3.38) * mm, v(64.35, -3.04) * mm]});
            skFitSpline(sketch, "E1422", {"points": [v(64.35, -3.04) * mm, v(64.25, -2.81) * mm, v(64.13, -2.64) * mm, v(63.86, -2.61) * mm]});
            skFitSpline(sketch, "E1423", {"points": [v(63.86, -2.61) * mm, v(63.8, -2.6) * mm, v(63.74, -2.57) * mm, v(63.68, -2.54) * mm]});
            skFitSpline(sketch, "E1424", {"points": [v(63.68, -2.54) * mm, v(63.5, -2.47) * mm, v(62.91, -2.64) * mm, v(62.8, -2.8) * mm]});
            skFitSpline(sketch, "E1425", {"points": [v(62.8, -2.8) * mm, v(62.79, -2.83) * mm, v(62.77, -2.87) * mm, v(62.76, -2.9) * mm]});
            skFitSpline(sketch, "E1426", {"points": [v(62.76, -2.9) * mm, v(62.57, -3.28) * mm, v(62.39, -3.66) * mm, v(62.21, -4.05) * mm]});
            skFitSpline(sketch, "E1427", {"points": [v(62.21, -4.05) * mm, v(62.18, -4.12) * mm, v(62.17, -4.22) * mm, v(62.18, -4.3) * mm]});
            skFitSpline(sketch, "E1428", {"points": [v(62.18, -4.3) * mm, v(62.3, -4.81) * mm, v(62.44, -5.33) * mm, v(62.56, -5.85) * mm]});
            skFitSpline(sketch, "E1429", {"points": [v(62.56, -5.85) * mm, v(62.73, -6.54) * mm, v(62.9, -7.23) * mm, v(63.06, -7.92) * mm]});
            skFitSpline(sketch, "E1430", {"points": [v(63.06, -7.92) * mm, v(63.21, -8.55) * mm, v(63.36, -9.19) * mm, v(63.5, -9.84) * mm]});
            skFitSpline(sketch, "E1431", {"points": [v(71.9, -13.83) * mm, v(71.95, -14.04) * mm, v(72.04, -14.17) * mm, v(72.22, -14.25) * mm]});
            skFitSpline(sketch, "E1432", {"points": [v(72.22, -14.25) * mm, v(72.66, -14.47) * mm, v(73.1, -14.7) * mm, v(73.54, -14.92) * mm]});
            skFitSpline(sketch, "E1433", {"points": [v(73.54, -14.92) * mm, v(73.64, -14.96) * mm, v(73.73, -15) * mm, v(73.81, -15.07) * mm]});
            skFitSpline(sketch, "E1434", {"points": [v(73.81, -15.07) * mm, v(73.95, -15.18) * mm, v(74.04, -15.32) * mm, v(74.02, -15.5) * mm]});
            skFitSpline(sketch, "E1435", {"points": [v(74.02, -15.5) * mm, v(74, -15.83) * mm, v(73.98, -16.16) * mm, v(73.95, -16.48) * mm]});
            skFitSpline(sketch, "E1436", {"points": [v(73.95, -16.48) * mm, v(73.91, -16.84) * mm, v(73.87, -17.2) * mm, v(73.84, -17.55) * mm]});
            skFitSpline(sketch, "E1437", {"points": [v(73.84, -17.55) * mm, v(73.8, -17.95) * mm, v(73.47, -18.16) * mm, v(73.1, -18) * mm]});
            skFitSpline(sketch, "E1438", {"points": [v(73.1, -18) * mm, v(72.5, -17.72) * mm, v(71.91, -17.44) * mm, v(71.32, -17.17) * mm]});
            skFitSpline(sketch, "E1439", {"points": [v(71.32, -17.17) * mm, v(71.06, -17.06) * mm, v(70.93, -16.87) * mm, v(70.96, -16.59) * mm]});
            skFitSpline(sketch, "E1440", {"points": [v(70.96, -16.59) * mm, v(70.98, -16.19) * mm, v(71.02, -15.8) * mm, v(71.04, -15.4) * mm]});
            skFitSpline(sketch, "E1441", {"points": [v(71.04, -15.4) * mm, v(71.05, -15.2) * mm, v(71.05, -15) * mm, v(71.05, -14.8) * mm]});
            skFitSpline(sketch, "E1442", {"points": [v(71.05, -14.8) * mm, v(71.05, -14.65) * mm, v(70.94, -14.56) * mm, v(70.84, -14.43) * mm]});
            skFitSpline(sketch, "E1443", {"points": [v(70.84, -14.43) * mm, v(70.77, -14.78) * mm, v(70.7, -15.1) * mm, v(70.64, -15.42) * mm]});
            skFitSpline(sketch, "E1444", {"points": [v(70.64, -15.42) * mm, v(70.59, -15.74) * mm, v(70.49, -16.05) * mm, v(70.47, -16.38) * mm]});
            skFitSpline(sketch, "E1445", {"points": [v(70.47, -16.38) * mm, v(70.45, -16.74) * mm, v(69.97, -16.98) * mm, v(69.67, -16.8) * mm]});
            skFitSpline(sketch, "E1446", {"points": [v(69.67, -16.8) * mm, v(69.53, -16.73) * mm, v(69.43, -16.6) * mm, v(69.43, -16.44) * mm]});
            skFitSpline(sketch, "E1447", {"points": [v(69.43, -16.44) * mm, v(69.43, -16.3) * mm, v(69.43, -16.15) * mm, v(69.48, -16.02) * mm]});
            skFitSpline(sketch, "E1448", {"points": [v(69.48, -16.02) * mm, v(69.64, -15.58) * mm, v(69.71, -15.1) * mm, v(69.8, -14.65) * mm]});
            skFitSpline(sketch, "E1449", {"points": [v(69.8, -14.65) * mm, v(69.84, -14.48) * mm, v(69.88, -14.3) * mm, v(69.9, -14.13) * mm]});
            skFitSpline(sketch, "E1450", {"points": [v(69.9, -14.13) * mm, v(69.92, -13.88) * mm, v(70.04, -13.7) * mm, v(70.31, -13.6) * mm]});
            skFitSpline(sketch, "E1451", {"points": [v(70.31, -13.6) * mm, v(70.1, -13.24) * mm, v(69.88, -12.9) * mm, v(69.67, -12.56) * mm]});
            skFitSpline(sketch, "E1452", {"points": [v(69.67, -12.56) * mm, v(69.66, -12.56) * mm, v(69.64, -12.56) * mm, v(69.62, -12.56) * mm]});
            skFitSpline(sketch, "E1453", {"points": [v(69.62, -12.56) * mm, v(69.6, -12.64) * mm, v(69.6, -12.73) * mm, v(69.58, -12.82) * mm]});
            skFitSpline(sketch, "E1454", {"points": [v(69.58, -12.82) * mm, v(69.56, -12.91) * mm, v(69.55, -13) * mm, v(69.54, -13.1) * mm]});
            skFitSpline(sketch, "E1455", {"points": [v(69.54, -13.1) * mm, v(69.49, -13.38) * mm, v(69.43, -13.66) * mm, v(69.4, -13.95) * mm]});
            skFitSpline(sketch, "E1456", {"points": [v(69.4, -13.95) * mm, v(69.36, -14.16) * mm, v(69.35, -14.38) * mm, v(69.32, -14.59) * mm]});
            skFitSpline(sketch, "E1457", {"points": [v(69.32, -14.59) * mm, v(69.3, -14.73) * mm, v(69.27, -14.88) * mm, v(69.21, -15) * mm]});
            skFitSpline(sketch, "E1458", {"points": [v(69.21, -15) * mm, v(69.12, -15.2) * mm, v(68.89, -15.3) * mm, v(68.69, -15.24) * mm]});
            skFitSpline(sketch, "E1459", {"points": [v(68.69, -15.24) * mm, v(68.47, -15.19) * mm, v(68.3, -15) * mm, v(68.32, -14.77) * mm]});
            skFitSpline(sketch, "E1460", {"points": [v(68.32, -14.77) * mm, v(68.36, -14.35) * mm, v(68.42, -13.94) * mm, v(68.49, -13.52) * mm]});
            skFitSpline(sketch, "E1461", {"points": [v(68.49, -13.52) * mm, v(68.6, -12.88) * mm, v(68.7, -12.24) * mm, v(68.72, -11.6) * mm]});
            skFitSpline(sketch, "E1462", {"points": [v(68.72, -11.6) * mm, v(68.72, -11.57) * mm, v(68.71, -11.55) * mm, v(68.72, -11.53) * mm]});
            skFitSpline(sketch, "E1463", {"points": [v(68.72, -11.53) * mm, v(68.84, -11.18) * mm, v(68.7, -10.9) * mm, v(68.5, -10.64) * mm]});
            skFitSpline(sketch, "E1464", {"points": [v(68.5, -10.64) * mm, v(68.41, -10.54) * mm, v(68.34, -10.41) * mm, v(68.24, -10.25) * mm]});
            skFitSpline(sketch, "E1465", {"points": [v(68.24, -10.25) * mm, v(68.2, -10.56) * mm, v(68.17, -10.82) * mm, v(68.14, -11.08) * mm]});
            skFitSpline(sketch, "E1466", {"points": [v(68.14, -11.08) * mm, v(68.08, -11.54) * mm, v(68.02, -12) * mm, v(67.96, -12.46) * mm]});
            skFitSpline(sketch, "E1467", {"points": [v(67.96, -12.46) * mm, v(67.96, -12.5) * mm, v(67.94, -12.55) * mm, v(67.95, -12.6) * mm]});
            skFitSpline(sketch, "E1468", {"points": [v(67.95, -12.6) * mm, v(68.02, -12.83) * mm, v(67.9, -13.02) * mm, v(67.78, -13.2) * mm]});
            skFitSpline(sketch, "E1469", {"points": [v(67.78, -13.2) * mm, v(67.66, -13.37) * mm, v(67.44, -13.43) * mm, v(67.25, -13.36) * mm]});
            skFitSpline(sketch, "E1470", {"points": [v(67.25, -13.36) * mm, v(67.06, -13.3) * mm, v(66.93, -13.13) * mm, v(66.93, -12.93) * mm]});
            skFitSpline(sketch, "E1471", {"points": [v(66.93, -12.93) * mm, v(66.93, -12.8) * mm, v(66.94, -12.67) * mm, v(66.95, -12.55) * mm]});
            skFitSpline(sketch, "E1472", {"points": [v(66.95, -12.55) * mm, v(67.04, -11.88) * mm, v(67.14, -11.22) * mm, v(67.23, -10.56) * mm]});
            skFitSpline(sketch, "E1473", {"points": [v(67.23, -10.56) * mm, v(67.3, -10.05) * mm, v(67.34, -9.54) * mm, v(67.4, -9.04) * mm]});
            skFitSpline(sketch, "E1474", {"points": [v(67.4, -9.04) * mm, v(67.42, -8.91) * mm, v(67.42, -8.8) * mm, v(67.35, -8.7) * mm]});
            skFitSpline(sketch, "E1475", {"points": [v(67.35, -8.7) * mm, v(67.21, -8.44) * mm, v(67.08, -8.2) * mm, v(66.95, -7.94) * mm]});
            skFitSpline(sketch, "E1476", {"points": [v(66.95, -7.94) * mm, v(66.93, -7.94) * mm, v(66.91, -7.95) * mm, v(66.9, -7.95) * mm]});
            skFitSpline(sketch, "E1477", {"points": [v(66.9, -7.95) * mm, v(66.85, -8.26) * mm, v(66.8, -8.57) * mm, v(66.75, -8.88) * mm]});
            skFitSpline(sketch, "E1478", {"points": [v(66.75, -8.88) * mm, v(66.7, -9.3) * mm, v(66.65, -9.73) * mm, v(66.6, -10.16) * mm]});
            skFitSpline(sketch, "E1479", {"points": [v(66.6, -10.16) * mm, v(66.6, -10.25) * mm, v(66.6, -10.35) * mm, v(66.62, -10.44) * mm]});
            skFitSpline(sketch, "E1480", {"points": [v(66.62, -10.44) * mm, v(66.66, -10.74) * mm, v(66.5, -11) * mm, v(66.23, -11.03) * mm]});
            skFitSpline(sketch, "E1481", {"points": [v(66.23, -11.03) * mm, v(65.9, -11.08) * mm, v(65.62, -10.9) * mm, v(65.6, -10.57) * mm]});
            skFitSpline(sketch, "E1482", {"points": [v(65.6, -10.57) * mm, v(65.6, -10.4) * mm, v(65.63, -10.22) * mm, v(65.65, -10.05) * mm]});
            skFitSpline(sketch, "E1483", {"points": [v(65.65, -10.05) * mm, v(65.7, -9.55) * mm, v(65.75, -9.05) * mm, v(65.82, -8.55) * mm]});
            skFitSpline(sketch, "E1484", {"points": [v(65.82, -8.55) * mm, v(65.9, -7.9) * mm, v(66.01, -7.26) * mm, v(66.1, -6.61) * mm]});
            skFitSpline(sketch, "E1485", {"points": [v(66.1, -6.61) * mm, v(66.14, -6.44) * mm, v(66.13, -6.28) * mm, v(66.04, -6.13) * mm]});
            skFitSpline(sketch, "E1486", {"points": [v(66.04, -6.13) * mm, v(65.93, -5.92) * mm, v(65.83, -5.7) * mm, v(65.72, -5.49) * mm]});
            skFitSpline(sketch, "E1487", {"points": [v(65.72, -5.49) * mm, v(65.7, -5.45) * mm, v(65.66, -5.42) * mm, v(65.6, -5.36) * mm]});
            skFitSpline(sketch, "E1488", {"points": [v(65.6, -5.36) * mm, v(65.56, -5.5) * mm, v(65.52, -5.63) * mm, v(65.5, -5.75) * mm]});
            skFitSpline(sketch, "E1489", {"points": [v(65.5, -5.75) * mm, v(65.28, -6.6) * mm, v(65.07, -7.47) * mm, v(64.87, -8.33) * mm]});
            skFitSpline(sketch, "E1490", {"points": [v(64.87, -8.33) * mm, v(64.68, -9.15) * mm, v(64.51, -9.97) * mm, v(64.33, -10.79) * mm]});
            skFitSpline(sketch, "E1491", {"points": [v(64.33, -10.79) * mm, v(64.22, -11.28) * mm, v(64.11, -11.78) * mm, v(64, -12.28) * mm]});
            skFitSpline(sketch, "E1492", {"points": [v(64, -12.28) * mm, v(63.96, -12.51) * mm, v(63.78, -12.66) * mm, v(63.55, -12.67) * mm]});
            skFitSpline(sketch, "E1493", {"points": [v(63.55, -12.67) * mm, v(63.29, -12.68) * mm, v(63.1, -12.57) * mm, v(63.04, -12.33) * mm]});
            skFitSpline(sketch, "E1494", {"points": [v(63.04, -12.33) * mm, v(63, -12.14) * mm, v(62.98, -11.95) * mm, v(62.94, -11.76) * mm]});
            skFitSpline(sketch, "E1495", {"points": [v(62.94, -11.76) * mm, v(62.74, -10.87) * mm, v(62.54, -9.97) * mm, v(62.33, -9.08) * mm]});
            skFitSpline(sketch, "E1496", {"points": [v(62.33, -9.08) * mm, v(62.09, -8.06) * mm, v(61.84, -7.05) * mm, v(61.6, -6.03) * mm]});
            skFitSpline(sketch, "E1497", {"points": [v(61.6, -6.03) * mm, v(61.55, -5.82) * mm, v(61.5, -5.6) * mm, v(61.44, -5.39) * mm]});
            skLineSegment(sketch, "E1498", {"start": v(61.44, -5.39) * mm, "end": v(61.38, -5.38) * mm});
            skFitSpline(sketch, "E1499", {"points": [v(61.38, -5.38) * mm, v(61.28, -5.55) * mm, v(61.18, -5.71) * mm, v(61.1, -5.88) * mm]});
            skFitSpline(sketch, "E1500", {"points": [v(61.1, -5.88) * mm, v(61.03, -6) * mm, v(60.98, -6.13) * mm, v(60.94, -6.26) * mm]});
            skFitSpline(sketch, "E1501", {"points": [v(60.94, -6.26) * mm, v(60.91, -6.34) * mm, v(60.9, -6.43) * mm, v(60.91, -6.51) * mm]});
            skFitSpline(sketch, "E1502", {"points": [v(60.91, -6.51) * mm, v(61.04, -7.56) * mm, v(61.26, -8.59) * mm, v(61.33, -9.64) * mm]});
            skFitSpline(sketch, "E1503", {"points": [v(61.33, -9.64) * mm, v(61.35, -9.88) * mm, v(61.4, -10.12) * mm, v(61.42, -10.35) * mm]});
            skFitSpline(sketch, "E1504", {"points": [v(61.42, -10.35) * mm, v(61.43, -10.47) * mm, v(61.43, -10.6) * mm, v(61.4, -10.7) * mm]});
            skFitSpline(sketch, "E1505", {"points": [v(61.4, -10.7) * mm, v(61.33, -10.96) * mm, v(61.06, -11.09) * mm, v(60.78, -11.03) * mm]});
            skFitSpline(sketch, "E1506", {"points": [v(60.78, -11.03) * mm, v(60.54, -10.98) * mm, v(60.38, -10.75) * mm, v(60.4, -10.5) * mm]});
            skFitSpline(sketch, "E1507", {"points": [v(60.4, -10.5) * mm, v(60.42, -10.37) * mm, v(60.42, -10.24) * mm, v(60.41, -10.12) * mm]});
            skFitSpline(sketch, "E1508", {"points": [v(60.41, -10.12) * mm, v(60.33, -9.47) * mm, v(60.25, -8.82) * mm, v(60.17, -8.17) * mm]});
            skFitSpline(sketch, "E1509", {"points": [v(60.17, -8.17) * mm, v(60.16, -8.1) * mm, v(60.14, -8.02) * mm, v(60.1, -7.89) * mm]});
            skFitSpline(sketch, "E1510", {"points": [v(60.1, -7.89) * mm, v(59.93, -8.22) * mm, v(59.78, -8.5) * mm, v(59.64, -8.78) * mm]});
            skFitSpline(sketch, "E1511", {"points": [v(59.64, -8.78) * mm, v(59.62, -8.83) * mm, v(59.61, -8.89) * mm, v(59.62, -8.94) * mm]});
            skFitSpline(sketch, "E1512", {"points": [v(59.62, -8.94) * mm, v(59.75, -10.05) * mm, v(59.89, -11.16) * mm, v(60.02, -12.26) * mm]});
            skFitSpline(sketch, "E1513", {"points": [v(60.02, -12.26) * mm, v(60.04, -12.39) * mm, v(60.07, -12.51) * mm, v(60.09, -12.64) * mm]});
            skFitSpline(sketch, "E1514", {"points": [v(60.09, -12.64) * mm, v(60.1, -12.74) * mm, v(60.12, -12.85) * mm, v(60.1, -12.95) * mm]});
            skFitSpline(sketch, "E1515", {"points": [v(60.1, -12.95) * mm, v(60.1, -13.15) * mm, v(59.94, -13.33) * mm, v(59.74, -13.37) * mm]});
            skFitSpline(sketch, "E1516", {"points": [v(59.74, -13.37) * mm, v(59.55, -13.42) * mm, v(59.35, -13.35) * mm, v(59.24, -13.18) * mm]});
            skFitSpline(sketch, "E1517", {"points": [v(59.24, -13.18) * mm, v(59.13, -13.01) * mm, v(59.05, -12.84) * mm, v(59.06, -12.62) * mm]});
            skFitSpline(sketch, "E1518", {"points": [v(59.06, -12.62) * mm, v(59.07, -12.4) * mm, v(59.03, -12.18) * mm, v(59, -11.96) * mm]});
            skFitSpline(sketch, "E1519", {"points": [v(59, -11.96) * mm, v(58.95, -11.43) * mm, v(58.88, -10.91) * mm, v(58.82, -10.39) * mm]});
            skFitSpline(sketch, "E1520", {"points": [v(58.82, -10.39) * mm, v(58.81, -10.36) * mm, v(58.8, -10.33) * mm, v(58.78, -10.26) * mm]});
            skFitSpline(sketch, "E1521", {"points": [v(58.78, -10.26) * mm, v(58.6, -10.55) * mm, v(58.43, -10.8) * mm, v(58.28, -11.05) * mm]});
            skFitSpline(sketch, "E1522", {"points": [v(58.28, -11.05) * mm, v(58.26, -11.08) * mm, v(58.26, -11.12) * mm, v(58.26, -11.15) * mm]});
            skFitSpline(sketch, "E1523", {"points": [v(58.26, -11.15) * mm, v(58.34, -12.05) * mm, v(58.41, -12.96) * mm, v(58.6, -13.85) * mm]});
            skFitSpline(sketch, "E1524", {"points": [v(58.6, -13.85) * mm, v(58.66, -14.14) * mm, v(58.7, -14.43) * mm, v(58.72, -14.72) * mm]});
            skFitSpline(sketch, "E1525", {"points": [v(58.72, -14.72) * mm, v(58.74, -14.97) * mm, v(58.58, -15.18) * mm, v(58.35, -15.24) * mm]});
            skFitSpline(sketch, "E1526", {"points": [v(58.35, -15.24) * mm, v(58.13, -15.3) * mm, v(57.9, -15.18) * mm, v(57.8, -14.96) * mm]});
            skFitSpline(sketch, "E1527", {"points": [v(57.8, -14.96) * mm, v(57.75, -14.87) * mm, v(57.73, -14.76) * mm, v(57.72, -14.66) * mm]});
            skFitSpline(sketch, "E1528", {"points": [v(57.72, -14.66) * mm, v(57.68, -14.41) * mm, v(57.66, -14.16) * mm, v(57.63, -13.9) * mm]});
            skFitSpline(sketch, "E1529", {"points": [v(57.63, -13.9) * mm, v(57.57, -13.5) * mm, v(57.5, -13.09) * mm, v(57.43, -12.68) * mm]});
            skFitSpline(sketch, "E1530", {"points": [v(57.43, -12.68) * mm, v(57.43, -12.64) * mm, v(57.42, -12.6) * mm, v(57.4, -12.5) * mm]});
            skFitSpline(sketch, "E1531", {"points": [v(57.4, -12.5) * mm, v(57.27, -12.72) * mm, v(57.16, -12.89) * mm, v(57.05, -13.06) * mm]});
            skFitSpline(sketch, "E1532", {"points": [v(57.05, -13.06) * mm, v(56.94, -13.23) * mm, v(56.84, -13.4) * mm, v(56.72, -13.6) * mm]});
            skFitSpline(sketch, "E1533", {"points": [v(56.72, -13.6) * mm, v(57.04, -13.7) * mm, v(57.1, -13.95) * mm, v(57.16, -14.23) * mm]});
            skFitSpline(sketch, "E1534", {"points": [v(57.16, -14.23) * mm, v(57.23, -14.7) * mm, v(57.33, -15.14) * mm, v(57.42, -15.6) * mm]});
            skFitSpline(sketch, "E1535", {"points": [v(57.42, -15.6) * mm, v(57.45, -15.71) * mm, v(57.5, -15.82) * mm, v(57.53, -15.94) * mm]});
            skFitSpline(sketch, "E1536", {"points": [v(57.53, -15.94) * mm, v(57.56, -16.1) * mm, v(57.62, -16.25) * mm, v(57.61, -16.4) * mm]});
            skFitSpline(sketch, "E1537", {"points": [v(57.61, -16.4) * mm, v(57.6, -16.75) * mm, v(57.26, -16.96) * mm, v(56.94, -16.83) * mm]});
            skFitSpline(sketch, "E1538", {"points": [v(56.94, -16.83) * mm, v(56.76, -16.76) * mm, v(56.55, -16.55) * mm, v(56.56, -16.3) * mm]});
            skFitSpline(sketch, "E1539", {"points": [v(56.56, -16.3) * mm, v(56.56, -16.14) * mm, v(56.5, -15.97) * mm, v(56.47, -15.8) * mm]});
            skFitSpline(sketch, "E1540", {"points": [v(56.47, -15.8) * mm, v(56.4, -15.4) * mm, v(56.3, -14.98) * mm, v(56.23, -14.56) * mm]});
            skFitSpline(sketch, "E1541", {"points": [v(56.23, -14.56) * mm, v(56.22, -14.53) * mm, v(56.2, -14.5) * mm, v(56.18, -14.45) * mm]});
            skFitSpline(sketch, "E1542", {"points": [v(56.18, -14.45) * mm, v(56.04, -14.59) * mm, v(55.98, -14.74) * mm, v(55.98, -14.93) * mm]});
            skFitSpline(sketch, "E1543", {"points": [v(55.98, -14.93) * mm, v(55.99, -15.42) * mm, v(56.01, -15.92) * mm, v(56.08, -16.4) * mm]});
            skFitSpline(sketch, "E1544", {"points": [v(56.08, -16.4) * mm, v(56.09, -16.47) * mm, v(56.08, -16.54) * mm, v(56.08, -16.6) * mm]});
            skFitSpline(sketch, "E1545", {"points": [v(56.08, -16.6) * mm, v(56.1, -16.86) * mm, v(55.98, -17.05) * mm, v(55.74, -17.16) * mm]});
            skFitSpline(sketch, "E1546", {"points": [v(55.74, -17.16) * mm, v(55.4, -17.31) * mm, v(55.04, -17.47) * mm, v(54.7, -17.63) * mm]});
            skFitSpline(sketch, "E1547", {"points": [v(54.7, -17.63) * mm, v(54.45, -17.74) * mm, v(54.21, -17.87) * mm, v(53.96, -17.97) * mm]});
            skFitSpline(sketch, "E1548", {"points": [v(53.96, -17.97) * mm, v(53.86, -18.02) * mm, v(53.73, -18.04) * mm, v(53.62, -18.03) * mm]});
            skFitSpline(sketch, "E1549", {"points": [v(53.62, -18.03) * mm, v(53.4, -18.03) * mm, v(53.23, -17.85) * mm, v(53.2, -17.63) * mm]});
            skFitSpline(sketch, "E1550", {"points": [v(53.2, -17.63) * mm, v(53.2, -17.54) * mm, v(53.18, -17.44) * mm, v(53.17, -17.35) * mm]});
            skFitSpline(sketch, "E1551", {"points": [v(53.17, -17.35) * mm, v(53.12, -16.79) * mm, v(53.06, -16.22) * mm, v(53.02, -15.66) * mm]});
            skFitSpline(sketch, "E1552", {"points": [v(53.02, -15.66) * mm, v(52.98, -15.27) * mm, v(53.1, -15.1) * mm, v(53.45, -14.93) * mm]});
            skFitSpline(sketch, "E1553", {"points": [v(53.45, -14.93) * mm, v(53.9, -14.7) * mm, v(54.35, -14.47) * mm, v(54.8, -14.25) * mm]});
            skFitSpline(sketch, "E1554", {"points": [v(54.8, -14.25) * mm, v(54.98, -14.17) * mm, v(55.08, -14.05) * mm, v(55.13, -13.84) * mm]});
            skFitSpline(sketch, "E1555", {"points": [v(55.13, -13.84) * mm, v(55.08, -13.85) * mm, v(55.03, -13.86) * mm, v(55, -13.87) * mm]});
            skFitSpline(sketch, "E1556", {"points": [v(55, -13.87) * mm, v(54.5, -14.03) * mm, v(54, -14.2) * mm, v(53.51, -14.36) * mm]});
            skFitSpline(sketch, "E1557", {"points": [v(53.51, -14.36) * mm, v(53.45, -14.37) * mm, v(53.4, -14.42) * mm, v(53.34, -14.45) * mm]});
            skFitSpline(sketch, "E1558", {"points": [v(53.34, -14.45) * mm, v(53.09, -14.59) * mm, v(52.72, -14.49) * mm, v(52.57, -14.24) * mm]});
            skFitSpline(sketch, "E1559", {"points": [v(52.57, -14.24) * mm, v(52.44, -14.02) * mm, v(52.49, -13.75) * mm, v(52.7, -13.6) * mm]});
            skFitSpline(sketch, "E1560", {"points": [v(52.7, -13.6) * mm, v(52.8, -13.53) * mm, v(52.91, -13.47) * mm, v(53.02, -13.45) * mm]});
            skFitSpline(sketch, "E1561", {"points": [v(53.02, -13.45) * mm, v(53.66, -13.35) * mm, v(54.25, -13.1) * mm, v(54.85, -12.89) * mm]});
            skFitSpline(sketch, "E1562", {"points": [v(54.85, -12.89) * mm, v(54.87, -12.88) * mm, v(54.9, -12.87) * mm, v(54.92, -12.86) * mm]});
            skFitSpline(sketch, "E1563", {"points": [v(54.92, -12.86) * mm, v(55.2, -12.76) * mm, v(55.33, -12.77) * mm, v(55.6, -12.94) * mm]});
            skFitSpline(sketch, "E1564", {"points": [v(55.6, -12.94) * mm, v(55.7, -12.76) * mm, v(55.8, -12.58) * mm, v(55.9, -12.4) * mm]});
            skFitSpline(sketch, "E1565", {"points": [v(55.9, -12.4) * mm, v(56, -12.22) * mm, v(56.09, -12.05) * mm, v(56.2, -11.83) * mm]});
            skFitSpline(sketch, "E1566", {"points": [v(56.2, -11.83) * mm, v(56.1, -11.86) * mm, v(56.04, -11.88) * mm, v(55.98, -11.9) * mm]});
            skFitSpline(sketch, "E1567", {"points": [v(55.98, -11.9) * mm, v(55.58, -12.05) * mm, v(55.19, -12.2) * mm, v(54.8, -12.35) * mm]});
            skFitSpline(sketch, "E1568", {"points": [v(54.8, -12.35) * mm, v(54.6, -12.43) * mm, v(54.4, -12.53) * mm, v(54.2, -12.6) * mm]});
            skFitSpline(sketch, "E1569", {"points": [v(54.2, -12.6) * mm, v(54.1, -12.65) * mm, v(53.97, -12.69) * mm, v(53.86, -12.7) * mm]});
            skFitSpline(sketch, "E1570", {"points": [v(53.86, -12.7) * mm, v(53.6, -12.71) * mm, v(53.4, -12.56) * mm, v(53.36, -12.34) * mm]});
            skFitSpline(sketch, "E1571", {"points": [v(53.36, -12.34) * mm, v(53.3, -12.1) * mm, v(53.41, -11.88) * mm, v(53.65, -11.77) * mm]});
            skFitSpline(sketch, "E1572", {"points": [v(53.65, -11.77) * mm, v(54, -11.63) * mm, v(54.35, -11.5) * mm, v(54.7, -11.35) * mm]});
            skFitSpline(sketch, "E1573", {"points": [v(54.7, -11.35) * mm, v(55.3, -11.1) * mm, v(55.89, -10.85) * mm, v(56.48, -10.6) * mm]});
            skFitSpline(sketch, "E1574", {"points": [v(56.48, -10.6) * mm, v(56.58, -10.56) * mm, v(56.68, -10.48) * mm, v(56.78, -10.46) * mm]});
            skFitSpline(sketch, "E1575", {"points": [v(56.78, -10.46) * mm, v(56.97, -10.42) * mm, v(57.06, -10.3) * mm, v(57.13, -10.14) * mm]});
            skFitSpline(sketch, "E1576", {"points": [v(57.13, -10.14) * mm, v(57.23, -9.93) * mm, v(57.34, -9.74) * mm, v(57.45, -9.5) * mm]});
            skFitSpline(sketch, "E1577", {"points": [v(57.45, -9.5) * mm, v(57.38, -9.53) * mm, v(57.33, -9.54) * mm, v(57.29, -9.56) * mm]});
            skFitSpline(sketch, "E1578", {"points": [v(57.29, -9.56) * mm, v(56.66, -9.82) * mm, v(56.04, -10.09) * mm, v(55.41, -10.35) * mm]});
            skFitSpline(sketch, "E1579", {"points": [v(55.41, -10.35) * mm, v(55.37, -10.37) * mm, v(55.32, -10.39) * mm, v(55.29, -10.42) * mm]});
            skFitSpline(sketch, "E1580", {"points": [v(55.29, -10.42) * mm, v(55.1, -10.6) * mm, v(54.86, -10.58) * mm, v(54.63, -10.55) * mm]});
            skFitSpline(sketch, "E1581", {"points": [v(54.63, -10.55) * mm, v(54.28, -10.5) * mm, v(54.14, -10.04) * mm, v(54.39, -9.77) * mm]});
            skFitSpline(sketch, "E1582", {"points": [v(54.39, -9.77) * mm, v(54.47, -9.68) * mm, v(54.6, -9.6) * mm, v(54.72, -9.56) * mm]});
            skFitSpline(sketch, "E1583", {"points": [v(54.72, -9.56) * mm, v(55.61, -9.18) * mm, v(56.5, -8.81) * mm, v(57.4, -8.44) * mm]});
            skFitSpline(sketch, "E1584", {"points": [v(57.4, -8.44) * mm, v(57.64, -8.34) * mm, v(57.89, -8.24) * mm, v(58.13, -8.13) * mm]});
            skFitSpline(sketch, "E1585", {"points": [v(58.13, -8.13) * mm, v(58.2, -8.1) * mm, v(58.29, -8.05) * mm, v(58.33, -7.98) * mm]});
            skFitSpline(sketch, "E1586", {"points": [v(58.33, -7.98) * mm, v(58.5, -7.73) * mm, v(58.66, -7.47) * mm, v(58.84, -7.18) * mm]});
            skFitSpline(sketch, "E1587", {"points": [v(58.84, -7.18) * mm, v(58.75, -7.2) * mm, v(58.7, -7.2) * mm, v(58.65, -7.22) * mm]});
            skFitSpline(sketch, "E1588", {"points": [v(58.65, -7.22) * mm, v(57.99, -7.5) * mm, v(57.33, -7.78) * mm, v(56.67, -8.06) * mm]});
            skFitSpline(sketch, "E1589", {"points": [v(56.67, -8.06) * mm, v(56.6, -8.09) * mm, v(56.53, -8.14) * mm, v(56.47, -8.19) * mm]});
            skFitSpline(sketch, "E1590", {"points": [v(56.47, -8.19) * mm, v(56.24, -8.37) * mm, v(55.94, -8.34) * mm, v(55.76, -8.12) * mm]});
            skFitSpline(sketch, "E1591", {"points": [v(55.76, -8.12) * mm, v(55.58, -7.9) * mm, v(55.6, -7.56) * mm, v(55.83, -7.39) * mm]});
            skFitSpline(sketch, "E1592", {"points": [v(55.83, -7.39) * mm, v(55.91, -7.32) * mm, v(56, -7.28) * mm, v(56.1, -7.24) * mm]});
            skFitSpline(sketch, "E1593", {"points": [v(56.1, -7.24) * mm, v(57.28, -6.75) * mm, v(58.45, -6.27) * mm, v(59.62, -5.79) * mm]});
            skFitSpline(sketch, "E1594", {"points": [v(59.62, -5.79) * mm, v(59.73, -5.74) * mm, v(59.81, -5.68) * mm, v(59.88, -5.6) * mm]});
            skFitSpline(sketch, "E1595", {"points": [v(59.88, -5.6) * mm, v(60.06, -5.35) * mm, v(60.25, -5.11) * mm, v(60.37, -4.81) * mm]});
            skFitSpline(sketch, "E1596", {"points": [v(60.37, -4.81) * mm, v(60.27, -4.76) * mm, v(60.2, -4.8) * mm, v(60.11, -4.82) * mm]});
            skFitSpline(sketch, "E1597", {"points": [v(60.11, -4.82) * mm, v(59.01, -5.15) * mm, v(57.9, -5.47) * mm, v(56.8, -5.8) * mm]});
            skFitSpline(sketch, "E1598", {"points": [v(56.8, -5.8) * mm, v(55.95, -6.07) * mm, v(55.09, -6.34) * mm, v(54.23, -6.6) * mm]});
            skFitSpline(sketch, "E1599", {"points": [v(54.23, -6.6) * mm, v(54.03, -6.67) * mm, v(53.83, -6.74) * mm, v(53.64, -6.81) * mm]});
            skFitSpline(sketch, "E1600", {"points": [v(53.64, -6.81) * mm, v(53.37, -6.9) * mm, v(53.13, -6.83) * mm, v(53, -6.6) * mm]});
            skFitSpline(sketch, "E1601", {"points": [v(53, -6.6) * mm, v(52.87, -6.38) * mm, v(52.93, -6.13) * mm, v(53.14, -5.94) * mm]});
            skFitSpline(sketch, "E1602", {"points": [v(53.14, -5.94) * mm, v(53.39, -5.74) * mm, v(53.62, -5.52) * mm, v(53.86, -5.3) * mm]});
            skFitSpline(sketch, "E1603", {"points": [v(53.86, -5.3) * mm, v(54.26, -4.94) * mm, v(54.67, -4.58) * mm, v(55.07, -4.21) * mm]});
            skFitSpline(sketch, "E1604", {"points": [v(55.07, -4.21) * mm, v(55.53, -3.79) * mm, v(56, -3.36) * mm, v(56.46, -2.92) * mm]});
            skFitSpline(sketch, "E1605", {"points": [v(56.46, -2.92) * mm, v(56.96, -2.44) * mm, v(57.46, -1.96) * mm, v(57.96, -1.48) * mm]});
            skFitSpline(sketch, "E1606", {"points": [v(57.96, -1.48) * mm, v(58.06, -1.37) * mm, v(58.16, -1.26) * mm, v(58.29, -1.14) * mm]});
            skFitSpline(sketch, "E1607", {"points": [v(58.29, -1.14) * mm, v(58.03, -1.07) * mm, v(57.8, -1.1) * mm, v(57.57, -1.11) * mm]});
            skFitSpline(sketch, "E1608", {"points": [v(57.57, -1.11) * mm, v(57.27, -1.12) * mm, v(57.04, -1.26) * mm, v(56.8, -1.44) * mm]});
            skFitSpline(sketch, "E1609", {"points": [v(56.8, -1.44) * mm, v(55.88, -2.17) * mm, v(54.94, -2.89) * mm, v(54, -3.6) * mm]});
            skFitSpline(sketch, "E1610", {"points": [v(54, -3.6) * mm, v(53.86, -3.72) * mm, v(53.71, -3.8) * mm, v(53.52, -3.8) * mm]});
            skFitSpline(sketch, "E1611", {"points": [v(53.52, -3.8) * mm, v(53.28, -3.77) * mm, v(53.08, -3.6) * mm, v(53.04, -3.33) * mm]});
            skFitSpline(sketch, "E1612", {"points": [v(53.04, -3.33) * mm, v(53, -3.12) * mm, v(53.13, -2.92) * mm, v(53.34, -2.82) * mm]});
            skFitSpline(sketch, "E1613", {"points": [v(53.34, -2.82) * mm, v(53.46, -2.76) * mm, v(53.57, -2.7) * mm, v(53.67, -2.63) * mm]});
            skFitSpline(sketch, "E1614", {"points": [v(53.67, -2.63) * mm, v(54.2, -2.24) * mm, v(54.72, -1.84) * mm, v(55.24, -1.44) * mm]});
            skFitSpline(sketch, "E1615", {"points": [v(55.24, -1.44) * mm, v(55.3, -1.4) * mm, v(55.36, -1.34) * mm, v(55.44, -1.26) * mm]});
            skFitSpline(sketch, "E1616", {"points": [v(55.44, -1.26) * mm, v(55.1, -1.28) * mm, v(54.78, -1.28) * mm, v(54.48, -1.3) * mm]});
            skFitSpline(sketch, "E1617", {"points": [v(54.48, -1.3) * mm, v(54.4, -1.3) * mm, v(54.31, -1.35) * mm, v(54.25, -1.4) * mm]});
            skFitSpline(sketch, "E1618", {"points": [v(54.25, -1.4) * mm, v(53.42, -2.01) * mm, v(52.6, -2.63) * mm, v(51.77, -3.25) * mm]});
            skFitSpline(sketch, "E1619", {"points": [v(51.77, -3.25) * mm, v(51.62, -3.36) * mm, v(51.49, -3.5) * mm, v(51.34, -3.6) * mm]});
            skFitSpline(sketch, "E1620", {"points": [v(51.34, -3.6) * mm, v(51.24, -3.68) * mm, v(51.14, -3.76) * mm, v(51.02, -3.8) * mm]});
            skFitSpline(sketch, "E1621", {"points": [v(51.02, -3.8) * mm, v(50.84, -3.88) * mm, v(50.63, -3.83) * mm, v(50.5, -3.67) * mm]});
            skFitSpline(sketch, "E1622", {"points": [v(50.5, -3.67) * mm, v(50.37, -3.52) * mm, v(50.33, -3.34) * mm, v(50.42, -3.16) * mm]});
            skFitSpline(sketch, "E1623", {"points": [v(50.42, -3.16) * mm, v(50.52, -2.97) * mm, v(50.62, -2.8) * mm, v(50.84, -2.72) * mm]});
            skFitSpline(sketch, "E1624", {"points": [v(50.84, -2.72) * mm, v(50.95, -2.68) * mm, v(51.03, -2.58) * mm, v(51.13, -2.51) * mm]});
            skFitSpline(sketch, "E1625", {"points": [v(51.13, -2.51) * mm, v(51.61, -2.15) * mm, v(52.1, -1.78) * mm, v(52.58, -1.42) * mm]});
            skFitSpline(sketch, "E1626", {"points": [v(52.58, -1.42) * mm, v(52.62, -1.39) * mm, v(52.66, -1.36) * mm, v(52.72, -1.3) * mm]});
            skFitSpline(sketch, "E1627", {"points": [v(52.72, -1.3) * mm, v(52.64, -1.3) * mm, v(52.59, -1.29) * mm, v(52.54, -1.28) * mm]});
            skFitSpline(sketch, "E1628", {"points": [v(52.54, -1.28) * mm, v(52.32, -1.27) * mm, v(52.1, -1.26) * mm, v(51.87, -1.25) * mm]});
            skFitSpline(sketch, "E1629", {"points": [v(51.87, -1.25) * mm, v(51.81, -1.25) * mm, v(51.74, -1.26) * mm, v(51.7, -1.3) * mm]});
            skFitSpline(sketch, "E1630", {"points": [v(51.7, -1.3) * mm, v(51.13, -1.7) * mm, v(50.57, -2.11) * mm, v(50.01, -2.53) * mm]});
            skFitSpline(sketch, "E1631", {"points": [v(50.01, -2.53) * mm, v(49.64, -2.81) * mm, v(49.27, -3.12) * mm, v(48.9, -3.42) * mm]});
            skFitSpline(sketch, "E1632", {"points": [v(48.9, -3.42) * mm, v(48.8, -3.5) * mm, v(48.68, -3.56) * mm, v(48.54, -3.55) * mm]});
            skFitSpline(sketch, "E1633", {"points": [v(48.54, -3.55) * mm, v(48.17, -3.54) * mm, v(47.95, -3.17) * mm, v(48.13, -2.85) * mm]});
            skFitSpline(sketch, "E1634", {"points": [v(48.13, -2.85) * mm, v(48.17, -2.77) * mm, v(48.23, -2.7) * mm, v(48.3, -2.63) * mm]});
            skFitSpline(sketch, "E1635", {"points": [v(48.3, -2.63) * mm, v(48.78, -2.26) * mm, v(49.25, -1.9) * mm, v(49.72, -1.52) * mm]});
            skFitSpline(sketch, "E1636", {"points": [v(49.72, -1.52) * mm, v(49.83, -1.43) * mm, v(49.94, -1.35) * mm, v(50.1, -1.23) * mm]});
            skFitSpline(sketch, "E1637", {"points": [v(50.1, -1.23) * mm, v(49.65, -1.17) * mm, v(49.24, -1.2) * mm, v(48.81, -1.18) * mm]});
            skFitSpline(sketch, "E1638", {"points": [v(48.81, -1.18) * mm, v(48.88, -1.47) * mm, v(48.74, -1.65) * mm, v(48.54, -1.82) * mm]});
            skFitSpline(sketch, "E1639", {"points": [v(48.54, -1.82) * mm, v(48.17, -2.13) * mm, v(47.8, -2.46) * mm, v(47.44, -2.78) * mm]});
            skFitSpline(sketch, "E1640", {"points": [v(47.44, -2.78) * mm, v(47.35, -2.86) * mm, v(47.27, -2.95) * mm, v(47.2, -3.04) * mm]});
            skFitSpline(sketch, "E1641", {"points": [v(47.2, -3.04) * mm, v(47.1, -3.12) * mm, v(47.03, -3.22) * mm, v(46.94, -3.29) * mm]});
            skFitSpline(sketch, "E1642", {"points": [v(46.94, -3.29) * mm, v(46.68, -3.48) * mm, v(46.38, -3.44) * mm, v(46.21, -3.22) * mm]});
            skFitSpline(sketch, "E1643", {"points": [v(46.21, -3.22) * mm, v(46.04, -3) * mm, v(46.08, -2.6) * mm, v(46.31, -2.44) * mm]});
            skFitSpline(sketch, "E1644", {"points": [v(46.31, -2.44) * mm, v(46.6, -2.25) * mm, v(46.83, -2) * mm, v(47.1, -1.77) * mm]});
            skFitSpline(sketch, "E1645", {"points": [v(47.1, -1.77) * mm, v(47.28, -1.62) * mm, v(47.47, -1.45) * mm, v(47.66, -1.29) * mm]});
            skFitSpline(sketch, "E1646", {"points": [v(47.66, -1.29) * mm, v(47.7, -1.24) * mm, v(47.75, -1.2) * mm, v(47.82, -1.13) * mm]});
            skFitSpline(sketch, "E1647", {"points": [v(47.82, -1.13) * mm, v(47.62, -1.08) * mm, v(47.46, -1.1) * mm, v(47.3, -1.2) * mm]});
            skFitSpline(sketch, "E1648", {"points": [v(47.3, -1.2) * mm, v(46.89, -1.48) * mm, v(46.47, -1.75) * mm, v(46.06, -2.02) * mm]});
            skFitSpline(sketch, "E1649", {"points": [v(46.06, -2.02) * mm, v(46.01, -2.05) * mm, v(45.97, -2.08) * mm, v(45.92, -2.11) * mm]});
            skFitSpline(sketch, "E1650", {"points": [v(45.92, -2.11) * mm, v(45.68, -2.27) * mm, v(45.45, -2.27) * mm, v(45.21, -2.1) * mm]});
            skFitSpline(sketch, "E1651", {"points": [v(45.21, -2.1) * mm, v(44.9, -1.87) * mm, v(44.6, -1.65) * mm, v(44.28, -1.43) * mm]});
            skFitSpline(sketch, "E1652", {"points": [v(44.28, -1.43) * mm, v(44.07, -1.28) * mm, v(43.86, -1.14) * mm, v(43.65, -1) * mm]});
            skFitSpline(sketch, "E1653", {"points": [v(43.65, -1) * mm, v(43.27, -0.73) * mm, v(43.27, -0.34) * mm, v(43.65, -0.07) * mm]});
            skFitSpline(sketch, "E1654", {"points": [v(43.65, -0.07) * mm, v(44.17, 0.3) * mm, v(44.7, 0.66) * mm, v(45.21, 1.03) * mm]});
            skFitSpline(sketch, "E1655", {"points": [v(45.21, 1.03) * mm, v(45.45, 1.2) * mm, v(45.69, 1.2) * mm, v(45.92, 1.04) * mm]});
            skFitSpline(sketch, "E1656", {"points": [v(45.92, 1.04) * mm, v(46.22, 0.85) * mm, v(46.5, 0.64) * mm, v(46.8, 0.45) * mm]});
            skFitSpline(sketch, "E1657", {"points": [v(46.8, 0.45) * mm, v(46.94, 0.35) * mm, v(47.1, 0.27) * mm, v(47.24, 0.17) * mm]});
            skFitSpline(sketch, "E1658", {"points": [v(47.24, 0.17) * mm, v(47.4, 0.06) * mm, v(47.59, 0.01) * mm, v(47.8, 0.07) * mm]});
            skFitSpline(sketch, "E1659", {"points": [v(47.8, 0.07) * mm, v(47.76, 0.11) * mm, v(47.73, 0.15) * mm, v(47.7, 0.18) * mm]});
            skFitSpline(sketch, "E1660", {"points": [v(47.7, 0.18) * mm, v(47.32, 0.53) * mm, v(46.93, 0.87) * mm, v(46.55, 1.2) * mm]});
            skFitSpline(sketch, "E1661", {"points": [v(46.55, 1.2) * mm, v(46.5, 1.25) * mm, v(46.43, 1.28) * mm, v(46.37, 1.32) * mm]});
            skFitSpline(sketch, "E1662", {"points": [v(46.37, 1.32) * mm, v(46.12, 1.48) * mm, v(46.03, 1.85) * mm, v(46.18, 2.1) * mm]});
            skFitSpline(sketch, "E1663", {"points": [v(46.18, 2.1) * mm, v(46.3, 2.3) * mm, v(46.55, 2.4) * mm, v(46.76, 2.31) * mm]});
            skFitSpline(sketch, "E1664", {"points": [v(46.76, 2.31) * mm, v(46.88, 2.26) * mm, v(47, 2.18) * mm, v(47.09, 2.08) * mm]});
            skFitSpline(sketch, "E1665", {"points": [v(47.09, 2.08) * mm, v(47.51, 1.58) * mm, v(48.02, 1.2) * mm, v(48.51, 0.77) * mm]});
            skFitSpline(sketch, "E1666", {"points": [v(48.51, 0.77) * mm, v(48.6, 0.7) * mm, v(48.7, 0.62) * mm, v(48.74, 0.53) * mm]});
            skFitSpline(sketch, "E1667", {"points": [v(48.74, 0.53) * mm, v(48.8, 0.4) * mm, v(48.82, 0.26) * mm, v(48.86, 0.1) * mm]});
            skFitSpline(sketch, "E1668", {"points": [v(48.86, 0.1) * mm, v(49.23, 0.11) * mm, v(49.63, 0.13) * mm, v(50.08, 0.14) * mm]});
            skFitSpline(sketch, "E1669", {"points": [v(50.08, 0.14) * mm, v(50.02, 0.2) * mm, v(50, 0.23) * mm, v(49.97, 0.26) * mm]});
            skFitSpline(sketch, "E1670", {"points": [v(49.97, 0.26) * mm, v(49.59, 0.57) * mm, v(49.2, 0.89) * mm, v(48.82, 1.2) * mm]});
            skFitSpline(sketch, "E1671", {"points": [v(48.82, 1.2) * mm, v(48.68, 1.3) * mm, v(48.53, 1.4) * mm, v(48.39, 1.5) * mm]});
            skFitSpline(sketch, "E1672", {"points": [v(48.39, 1.5) * mm, v(48.25, 1.6) * mm, v(48.13, 1.72) * mm, v(48.08, 1.89) * mm]});
            skFitSpline(sketch, "E1673", {"points": [v(48.08, 1.89) * mm, v(48.03, 2.1) * mm, v(48.11, 2.3) * mm, v(48.28, 2.41) * mm]});
            skFitSpline(sketch, "E1674", {"points": [v(48.28, 2.41) * mm, v(48.46, 2.53) * mm, v(48.66, 2.53) * mm, v(48.84, 2.4) * mm]});
            skFitSpline(sketch, "E1675", {"points": [v(48.84, 2.4) * mm, v(49.13, 2.18) * mm, v(49.4, 1.96) * mm, v(49.68, 1.75) * mm]});
            skFitSpline(sketch, "E1676", {"points": [v(49.68, 1.75) * mm, v(50.2, 1.34) * mm, v(50.73, 0.94) * mm, v(51.26, 0.54) * mm]});
            skFitSpline(sketch, "E1677", {"points": [v(51.26, 0.54) * mm, v(51.35, 0.47) * mm, v(51.47, 0.42) * mm, v(51.55, 0.34) * mm]});
            skFitSpline(sketch, "E1678", {"points": [v(51.55, 0.34) * mm, v(51.68, 0.2) * mm, v(51.84, 0.18) * mm, v(52, 0.19) * mm]});
            skFitSpline(sketch, "E1679", {"points": [v(52, 0.19) * mm, v(52.23, 0.2) * mm, v(52.45, 0.19) * mm, v(52.73, 0.19) * mm]});
            skFitSpline(sketch, "E1680", {"points": [v(52.73, 0.19) * mm, v(52.67, 0.26) * mm, v(52.65, 0.3) * mm, v(52.62, 0.33) * mm]});
            skFitSpline(sketch, "E1681", {"points": [v(52.62, 0.33) * mm, v(52.06, 0.75) * mm, v(51.5, 1.16) * mm, v(50.95, 1.58) * mm]});
            skFitSpline(sketch, "E1682", {"points": [v(50.95, 1.58) * mm, v(50.9, 1.62) * mm, v(50.86, 1.64) * mm, v(50.8, 1.67) * mm]});
            skFitSpline(sketch, "E1683", {"points": [v(50.8, 1.67) * mm, v(50.58, 1.76) * mm, v(50.47, 1.96) * mm, v(50.4, 2.17) * mm]});
            skFitSpline(sketch, "E1684", {"points": [v(50.4, 2.17) * mm, v(50.33, 2.34) * mm, v(50.4, 2.5) * mm, v(50.52, 2.63) * mm]});
            skFitSpline(sketch, "E1685", {"points": [v(50.52, 2.63) * mm, v(50.65, 2.75) * mm, v(50.8, 2.82) * mm, v(50.98, 2.75) * mm]});
            skFitSpline(sketch, "E1686", {"points": [v(50.98, 2.75) * mm, v(51.1, 2.7) * mm, v(51.2, 2.65) * mm, v(51.3, 2.57) * mm]});
            skFitSpline(sketch, "E1687", {"points": [v(51.3, 2.57) * mm, v(52.03, 2.01) * mm, v(52.77, 1.45) * mm, v(53.5, 0.88) * mm]});
            skFitSpline(sketch, "E1688", {"points": [v(53.5, 0.88) * mm, v(53.74, 0.7) * mm, v(53.97, 0.52) * mm, v(54.22, 0.35) * mm]});
            skFitSpline(sketch, "E1689", {"points": [v(54.22, 0.35) * mm, v(54.3, 0.3) * mm, v(54.41, 0.24) * mm, v(54.51, 0.23) * mm]});
            skFitSpline(sketch, "E1690", {"points": [v(54.51, 0.23) * mm, v(54.8, 0.2) * mm, v(55.1, 0.2) * mm, v(55.39, 0.18) * mm]});
            skFitSpline(sketch, "E1691", {"points": [v(55.39, 0.18) * mm, v(55.4, 0.2) * mm, v(55.4, 0.22) * mm, v(55.4, 0.24) * mm]});
            skFitSpline(sketch, "E1692", {"points": [v(55.4, 0.24) * mm, v(55.2, 0.42) * mm, v(54.98, 0.6) * mm, v(54.75, 0.77) * mm]});
            skFitSpline(sketch, "E1693", {"points": [v(54.75, 0.77) * mm, v(54.36, 1.07) * mm, v(53.96, 1.36) * mm, v(53.55, 1.65) * mm]});
            skFitSpline(sketch, "E1694", {"points": [v(53.55, 1.65) * mm, v(53.5, 1.7) * mm, v(53.43, 1.71) * mm, v(53.36, 1.74) * mm]});
            skFitSpline(sketch, "E1695", {"points": [v(53.36, 1.74) * mm, v(53.08, 1.86) * mm, v(52.96, 2.13) * mm, v(53.08, 2.4) * mm]});
            skFitSpline(sketch, "E1696", {"points": [v(53.08, 2.4) * mm, v(53.2, 2.67) * mm, v(53.5, 2.8) * mm, v(53.76, 2.69) * mm]});
            skFitSpline(sketch, "E1697", {"points": [v(53.76, 2.69) * mm, v(53.85, 2.64) * mm, v(53.94, 2.58) * mm, v(54.02, 2.52) * mm]});
            skFitSpline(sketch, "E1698", {"points": [v(54.02, 2.52) * mm, v(55.03, 1.75) * mm, v(56.03, 0.97) * mm, v(57.04, 0.2) * mm]});
            skFitSpline(sketch, "E1699", {"points": [v(57.04, 0.2) * mm, v(57.12, 0.14) * mm, v(57.2, 0.1) * mm, v(57.3, 0.09) * mm]});
            skFitSpline(sketch, "E1700", {"points": [v(57.3, 0.09) * mm, v(57.46, 0.08) * mm, v(57.63, 0.03) * mm, v(57.8, 0.02) * mm]});
            skFitSpline(sketch, "E1701", {"points": [v(57.8, 0.02) * mm, v(57.95, 0.01) * mm, v(58.1, 0.04) * mm, v(58.25, 0.04) * mm]});
            skFitSpline(sketch, "E1702", {"points": [v(58.25, 0.04) * mm, v(58.26, 0.06) * mm, v(58.26, 0.08) * mm, v(58.27, 0.1) * mm]});
            skFitSpline(sketch, "E1703", {"points": [v(58.27, 0.1) * mm, v(58.08, 0.28) * mm, v(57.89, 0.47) * mm, v(57.7, 0.66) * mm]});
            skFitSpline(sketch, "E1704", {"points": [v(57.7, 0.66) * mm, v(57.15, 1.19) * mm, v(56.6, 1.71) * mm, v(56.04, 2.23) * mm]});
            skFitSpline(sketch, "E1705", {"points": [v(56.04, 2.23) * mm, v(55.51, 2.73) * mm, v(54.97, 3.21) * mm, v(54.44, 3.7) * mm]});
            skFitSpline(sketch, "E1706", {"points": [v(54.44, 3.7) * mm, v(54.06, 4.05) * mm, v(53.68, 4.4) * mm, v(53.3, 4.74) * mm]});
            skFitSpline(sketch, "E1707", {"points": [v(53.3, 4.74) * mm, v(53.24, 4.8) * mm, v(53.17, 4.85) * mm, v(53.1, 4.91) * mm]});
            skFitSpline(sketch, "E1708", {"points": [v(53.1, 4.91) * mm, v(52.91, 5.08) * mm, v(52.87, 5.32) * mm, v(53, 5.54) * mm]});
            skFitSpline(sketch, "E1709", {"points": [v(53, 5.54) * mm, v(53.12, 5.75) * mm, v(53.36, 5.84) * mm, v(53.6, 5.76) * mm]});
            skFitSpline(sketch, "E1710", {"points": [v(53.6, 5.76) * mm, v(54.47, 5.47) * mm, v(55.34, 5.18) * mm, v(56.21, 4.9) * mm]});
            skFitSpline(sketch, "E1711", {"points": [v(56.21, 4.9) * mm, v(57.12, 4.62) * mm, v(58.03, 4.36) * mm, v(58.94, 4.1) * mm]});
            skFitSpline(sketch, "E1712", {"points": [v(58.94, 4.1) * mm, v(59.33, 3.98) * mm, v(59.72, 3.86) * mm, v(60.12, 3.75) * mm]});
            skFitSpline(sketch, "E1713", {"points": [v(60.12, 3.75) * mm, v(60.2, 3.73) * mm, v(60.28, 3.72) * mm, v(60.39, 3.7) * mm]});
            skFitSpline(sketch, "E1714", {"points": [v(60.39, 3.7) * mm, v(60.25, 4.07) * mm, v(60.02, 4.34) * mm, v(59.8, 4.62) * mm]});
            skFitSpline(sketch, "E1715", {"points": [v(59.8, 4.62) * mm, v(59.76, 4.67) * mm, v(59.69, 4.69) * mm, v(59.63, 4.71) * mm]});
            skFitSpline(sketch, "E1716", {"points": [v(59.63, 4.71) * mm, v(58.47, 5.19) * mm, v(57.31, 5.67) * mm, v(56.15, 6.15) * mm]});
            skFitSpline(sketch, "E1717", {"points": [v(56.15, 6.15) * mm, v(56.06, 6.19) * mm, v(55.96, 6.23) * mm, v(55.88, 6.28) * mm]});
            skFitSpline(sketch, "E1718", {"points": [v(55.88, 6.28) * mm, v(55.62, 6.45) * mm, v(55.57, 6.78) * mm, v(55.74, 7.02) * mm]});
            skFitSpline(sketch, "E1719", {"points": [v(55.74, 7.02) * mm, v(55.92, 7.27) * mm, v(56.22, 7.3) * mm, v(56.48, 7.11) * mm]});
            skFitSpline(sketch, "E1720", {"points": [v(56.48, 7.11) * mm, v(56.53, 7.07) * mm, v(56.6, 7.02) * mm, v(56.66, 7) * mm]});
            skFitSpline(sketch, "E1721", {"points": [v(56.66, 7) * mm, v(57.32, 6.71) * mm, v(57.98, 6.43) * mm, v(58.64, 6.16) * mm]});
            skFitSpline(sketch, "E1722", {"points": [v(58.64, 6.16) * mm, v(58.7, 6.13) * mm, v(58.74, 6.12) * mm, v(58.82, 6.14) * mm]});
            skFitSpline(sketch, "E1723", {"points": [v(58.82, 6.14) * mm, v(58.65, 6.4) * mm, v(58.48, 6.68) * mm, v(58.3, 6.95) * mm]});
            skFitSpline(sketch, "E1724", {"points": [v(58.3, 6.95) * mm, v(58.27, 7) * mm, v(58.2, 7.03) * mm, v(58.15, 7.06) * mm]});
            skFitSpline(sketch, "E1725", {"points": [v(58.15, 7.06) * mm, v(57.22, 7.45) * mm, v(56.3, 7.85) * mm, v(55.37, 8.24) * mm]});
            skFitSpline(sketch, "E1726", {"points": [v(55.37, 8.24) * mm, v(55.17, 8.33) * mm, v(54.95, 8.4) * mm, v(54.75, 8.48) * mm]});
            skFitSpline(sketch, "E1727", {"points": [v(54.75, 8.48) * mm, v(54.63, 8.53) * mm, v(54.5, 8.59) * mm, v(54.42, 8.67) * mm]});
            skFitSpline(sketch, "E1728", {"points": [v(54.42, 8.67) * mm, v(54.27, 8.8) * mm, v(54.22, 8.98) * mm, v(54.3, 9.17) * mm]});
            skFitSpline(sketch, "E1729", {"points": [v(54.3, 9.17) * mm, v(54.36, 9.36) * mm, v(54.5, 9.48) * mm, v(54.7, 9.5) * mm]});
            skFitSpline(sketch, "E1730", {"points": [v(54.7, 9.5) * mm, v(54.91, 9.51) * mm, v(55.12, 9.5) * mm, v(55.29, 9.35) * mm]});
            skFitSpline(sketch, "E1731", {"points": [v(55.29, 9.35) * mm, v(55.32, 9.32) * mm, v(55.37, 9.3) * mm, v(55.41, 9.28) * mm]});
            skFitSpline(sketch, "E1732", {"points": [v(55.41, 9.28) * mm, v(56.03, 9.02) * mm, v(56.65, 8.76) * mm, v(57.27, 8.5) * mm]});
            skFitSpline(sketch, "E1733", {"points": [v(57.27, 8.5) * mm, v(57.32, 8.48) * mm, v(57.37, 8.47) * mm, v(57.45, 8.44) * mm]});
            skFitSpline(sketch, "E1734", {"points": [v(57.45, 8.44) * mm, v(57.3, 8.73) * mm, v(57.18, 8.98) * mm, v(57.04, 9.23) * mm]});
            skFitSpline(sketch, "E1735", {"points": [v(57.04, 9.23) * mm, v(57.02, 9.27) * mm, v(56.98, 9.3) * mm, v(56.94, 9.32) * mm]});
            skFitSpline(sketch, "E1736", {"points": [v(56.94, 9.32) * mm, v(56.38, 9.57) * mm, v(55.82, 9.83) * mm, v(55.25, 10.07) * mm]});
            skFitSpline(sketch, "E1737", {"points": [v(55.25, 10.07) * mm, v(54.74, 10.29) * mm, v(54.21, 10.48) * mm, v(53.7, 10.69) * mm]});
            skFitSpline(sketch, "E1738", {"points": [v(53.7, 10.69) * mm, v(53.44, 10.79) * mm, v(53.33, 10.96) * mm, v(53.35, 11.2) * mm]});
            skFitSpline(sketch, "E1739", {"points": [v(53.35, 11.2) * mm, v(53.37, 11.44) * mm, v(53.55, 11.61) * mm, v(53.79, 11.62) * mm]});
            skFitSpline(sketch, "E1740", {"points": [v(53.79, 11.62) * mm, v(53.93, 11.63) * mm, v(54.07, 11.6) * mm, v(54.2, 11.54) * mm]});
            skFitSpline(sketch, "E1741", {"points": [v(54.2, 11.54) * mm, v(54.41, 11.44) * mm, v(54.63, 11.35) * mm, v(54.84, 11.27) * mm]});
            skFitSpline(sketch, "E1742", {"points": [v(54.84, 11.27) * mm, v(55.27, 11.1) * mm, v(55.7, 10.94) * mm, v(56.17, 10.77) * mm]});
            skFitSpline(sketch, "E1743", {"points": [v(56.17, 10.77) * mm, v(56.03, 11.17) * mm, v(55.78, 11.5) * mm, v(55.6, 11.88) * mm]});
            skFitSpline(sketch, "E1744", {"points": [v(55.6, 11.88) * mm, v(55.37, 11.67) * mm, v(55.13, 11.7) * mm, v(54.88, 11.8) * mm]});
            skFitSpline(sketch, "E1745", {"points": [v(54.88, 11.8) * mm, v(54.45, 11.96) * mm, v(54.02, 12.1) * mm, v(53.59, 12.25) * mm]});
            skFitSpline(sketch, "E1746", {"points": [v(53.59, 12.25) * mm, v(53.45, 12.3) * mm, v(53.3, 12.31) * mm, v(53.17, 12.35) * mm]});
            skFitSpline(sketch, "E1747", {"points": [v(53.17, 12.35) * mm, v(53.06, 12.37) * mm, v(52.95, 12.4) * mm, v(52.85, 12.44) * mm]});
            skFitSpline(sketch, "E1748", {"points": [v(52.85, 12.44) * mm, v(52.55, 12.57) * mm, v(52.43, 12.84) * mm, v(52.53, 13.1) * mm]});
            skFitSpline(sketch, "E1749", {"points": [v(52.53, 13.1) * mm, v(52.64, 13.37) * mm, v(53.02, 13.54) * mm, v(53.27, 13.4) * mm]});
            skFitSpline(sketch, "E1750", {"points": [v(53.27, 13.4) * mm, v(53.5, 13.28) * mm, v(53.75, 13.23) * mm, v(54, 13.15) * mm]});
            skFitSpline(sketch, "E1751", {"points": [v(54, 13.15) * mm, v(54.36, 13.02) * mm, v(54.73, 12.9) * mm, v(55.13, 12.76) * mm]});
            skFitSpline(sketch, "E1752", {"points": [v(55.13, 12.76) * mm, v(55.09, 12.94) * mm, v(55.03, 13.07) * mm, v(54.87, 13.15) * mm]});
            skFitSpline(sketch, "E1753", {"points": [v(54.87, 13.15) * mm, v(54.42, 13.37) * mm, v(53.96, 13.6) * mm, v(53.5, 13.84) * mm]});
            skFitSpline(sketch, "E1754", {"points": [v(53.5, 13.84) * mm, v(53.43, 13.87) * mm, v(53.36, 13.9) * mm, v(53.3, 13.95) * mm]});
            skFitSpline(sketch, "E1755", {"points": [v(53.3, 13.95) * mm, v(53.1, 14.06) * mm, v(53, 14.23) * mm, v(53.01, 14.46) * mm]});
            skFitSpline(sketch, "E1756", {"points": [v(53.01, 14.46) * mm, v(53.04, 14.85) * mm, v(53.04, 15.23) * mm, v(53.11, 15.6) * mm]});
            skFitSpline(sketch, "E1757", {"points": [v(53.11, 15.6) * mm, v(53.17, 15.9) * mm, v(53.17, 16.22) * mm, v(53.2, 16.53) * mm]});
            skFitSpline(sketch, "E1758", {"points": [v(53.2, 16.53) * mm, v(53.24, 16.86) * mm, v(53.53, 17.05) * mm, v(53.84, 16.96) * mm]});
            skFitSpline(sketch, "E1759", {"points": [v(53.84, 16.96) * mm, v(53.93, 16.93) * mm, v(54.02, 16.88) * mm, v(54.1, 16.84) * mm]});
            skFitSpline(sketch, "E1760", {"points": [v(54.1, 16.84) * mm, v(54.62, 16.6) * mm, v(55.13, 16.36) * mm, v(55.65, 16.13) * mm]});
            skFitSpline(sketch, "E1761", {"points": [v(55.65, 16.13) * mm, v(56.1, 15.94) * mm, v(56.1, 15.66) * mm, v(56.08, 15.32) * mm]});
            skFitSpline(sketch, "E1762", {"points": [v(56.08, 15.32) * mm, v(56.04, 14.84) * mm, v(56.01, 14.35) * mm, v(55.99, 13.87) * mm]});
            skFitSpline(sketch, "E1763", {"points": [v(55.99, 13.87) * mm, v(55.98, 13.62) * mm, v(55.99, 13.62) * mm, v(56.18, 13.39) * mm]});
            skFitSpline(sketch, "E1764", {"points": [v(56.18, 13.39) * mm, v(56.2, 13.44) * mm, v(56.22, 13.47) * mm, v(56.23, 13.52) * mm]});
            skFitSpline(sketch, "E1765", {"points": [v(56.23, 13.52) * mm, v(56.34, 14.02) * mm, v(56.44, 14.53) * mm, v(56.54, 15.04) * mm]});
            skFitSpline(sketch, "E1766", {"points": [v(56.54, 15.04) * mm, v(56.56, 15.1) * mm, v(56.56, 15.18) * mm, v(56.56, 15.25) * mm]});
            skFitSpline(sketch, "E1767", {"points": [v(56.56, 15.25) * mm, v(56.57, 15.56) * mm, v(56.86, 15.82) * mm, v(57.17, 15.8) * mm]});
            skFitSpline(sketch, "E1768", {"points": [v(57.17, 15.8) * mm, v(57.47, 15.77) * mm, v(57.66, 15.5) * mm, v(57.61, 15.17) * mm]});
            skFitSpline(sketch, "E1769", {"points": [v(57.61, 15.17) * mm, v(57.6, 15.1) * mm, v(57.6, 15.04) * mm, v(57.57, 14.98) * mm]});
            skFitSpline(sketch, "E1770", {"points": [v(57.57, 14.98) * mm, v(57.33, 14.38) * mm, v(57.26, 13.73) * mm, v(57.14, 13.1) * mm]});
            skFitSpline(sketch, "E1771", {"points": [v(57.14, 13.1) * mm, v(57.1, 12.84) * mm, v(57.01, 12.62) * mm, v(56.72, 12.52) * mm]});
            skFitSpline(sketch, "E1772", {"points": [v(56.72, 12.52) * mm, v(56.94, 12.16) * mm, v(57.16, 11.82) * mm, v(57.37, 11.47) * mm]});
            skFitSpline(sketch, "E1773", {"points": [v(57.37, 11.47) * mm, v(57.39, 11.48) * mm, v(57.4, 11.48) * mm, v(57.42, 11.49) * mm]});
            skFitSpline(sketch, "E1774", {"points": [v(57.42, 11.49) * mm, v(57.45, 11.71) * mm, v(57.47, 11.94) * mm, v(57.5, 12.17) * mm]});
            skFitSpline(sketch, "E1775", {"points": [v(57.5, 12.17) * mm, v(57.57, 12.52) * mm, v(57.63, 12.87) * mm, v(57.69, 13.23) * mm]});
            skFitSpline(sketch, "E1776", {"points": [v(57.69, 13.23) * mm, v(57.7, 13.34) * mm, v(57.7, 13.45) * mm, v(57.72, 13.56) * mm]});
            skFitSpline(sketch, "E1777", {"points": [v(57.72, 13.56) * mm, v(57.73, 13.66) * mm, v(57.74, 13.77) * mm, v(57.78, 13.86) * mm]});
            skFitSpline(sketch, "E1778", {"points": [v(57.78, 13.86) * mm, v(57.88, 14.12) * mm, v(58.12, 14.23) * mm, v(58.39, 14.16) * mm]});
            skFitSpline(sketch, "E1779", {"points": [v(58.39, 14.16) * mm, v(58.6, 14.1) * mm, v(58.75, 13.87) * mm, v(58.72, 13.63) * mm]});
            skFitSpline(sketch, "E1780", {"points": [v(58.72, 13.63) * mm, v(58.66, 13.2) * mm, v(58.59, 12.78) * mm, v(58.52, 12.36) * mm]});
            skFitSpline(sketch, "E1781", {"points": [v(58.52, 12.36) * mm, v(58.46, 11.9) * mm, v(58.4, 11.44) * mm, v(58.34, 10.98) * mm]});
            skFitSpline(sketch, "E1782", {"points": [v(58.34, 10.98) * mm, v(58.3, 10.7) * mm, v(58.29, 10.4) * mm, v(58.26, 10.1) * mm]});
            skFitSpline(sketch, "E1783", {"points": [v(58.26, 10.1) * mm, v(58.26, 10.06) * mm, v(58.26, 10.02) * mm, v(58.27, 9.99) * mm]});
            skFitSpline(sketch, "E1784", {"points": [v(58.27, 9.99) * mm, v(58.43, 9.73) * mm, v(58.6, 9.48) * mm, v(58.79, 9.18) * mm]});
            skFitSpline(sketch, "E1785", {"points": [v(58.79, 9.18) * mm, v(58.82, 9.4) * mm, v(58.84, 9.58) * mm, v(58.86, 9.75) * mm]});
            skFitSpline(sketch, "E1786", {"points": [v(58.86, 9.75) * mm, v(58.93, 10.27) * mm, v(59, 10.8) * mm, v(59.06, 11.32) * mm]});
            skFitSpline(sketch, "E1787", {"points": [v(59.06, 11.32) * mm, v(59.07, 11.39) * mm, v(59.08, 11.46) * mm, v(59.07, 11.53) * mm]});
            skFitSpline(sketch, "E1788", {"points": [v(59.07, 11.53) * mm, v(59.03, 11.74) * mm, v(59.11, 11.9) * mm, v(59.21, 12.07) * mm]});
            skFitSpline(sketch, "E1789", {"points": [v(59.21, 12.07) * mm, v(59.33, 12.27) * mm, v(59.54, 12.36) * mm, v(59.74, 12.3) * mm]});
            skFitSpline(sketch, "E1790", {"points": [v(59.74, 12.3) * mm, v(59.97, 12.24) * mm, v(60.12, 12.07) * mm, v(60.1, 11.83) * mm]});
            skFitSpline(sketch, "E1791", {"points": [v(60.1, 11.83) * mm, v(60.1, 11.6) * mm, v(60.04, 11.36) * mm, v(60.01, 11.12) * mm]});
            skFitSpline(sketch, "E1792", {"points": [v(60.01, 11.12) * mm, v(59.94, 10.53) * mm, v(59.86, 9.94) * mm, v(59.79, 9.34) * mm]});
            skFitSpline(sketch, "E1793", {"points": [v(59.79, 9.34) * mm, v(59.73, 8.86) * mm, v(59.68, 8.38) * mm, v(59.63, 7.9) * mm]});
            skFitSpline(sketch, "E1794", {"points": [v(59.63, 7.9) * mm, v(59.62, 7.83) * mm, v(59.62, 7.76) * mm, v(59.64, 7.71) * mm]});
            skFitSpline(sketch, "E1795", {"points": [v(59.64, 7.71) * mm, v(59.78, 7.43) * mm, v(59.93, 7.15) * mm, v(60.13, 6.87) * mm]});
            skFitSpline(sketch, "E1796", {"points": [v(60.13, 6.87) * mm, v(60.15, 7.03) * mm, v(60.19, 7.18) * mm, v(60.2, 7.33) * mm]});
            skFitSpline(sketch, "E1797", {"points": [v(60.2, 7.33) * mm, v(60.29, 7.96) * mm, v(60.36, 8.58) * mm, v(60.43, 9.2) * mm]});
            skFitSpline(sketch, "E1798", {"points": [v(60.43, 9.2) * mm, v(60.44, 9.27) * mm, v(60.42, 9.33) * mm, v(60.41, 9.4) * mm]});
            skFitSpline(sketch, "E1799", {"points": [v(60.41, 9.4) * mm, v(60.37, 9.7) * mm, v(60.55, 9.94) * mm, v(60.84, 9.97) * mm]});
            skFitSpline(sketch, "E1800", {"points": [v(60.84, 9.97) * mm, v(61.16, 10.01) * mm, v(61.42, 9.8) * mm, v(61.42, 9.48) * mm]});
            skFitSpline(sketch, "E1801", {"points": [v(61.42, 9.48) * mm, v(61.42, 9.22) * mm, v(61.39, 8.96) * mm, v(61.35, 8.7) * mm]});
            skFitSpline(sketch, "E1802", {"points": [v(61.35, 8.7) * mm, v(61.2, 7.6) * mm, v(61.05, 6.5) * mm, v(60.9, 5.4) * mm]});
            skFitSpline(sketch, "E1803", {"points": [v(60.9, 5.4) * mm, v(60.9, 5.36) * mm, v(60.88, 5.32) * mm, v(60.9, 5.28) * mm]});
            skFitSpline(sketch, "E1804", {"points": [v(60.9, 5.28) * mm, v(61.03, 4.95) * mm, v(61.15, 4.6) * mm, v(61.42, 4.3) * mm]});
            skFitSpline(sketch, "E1805", {"points": [v(61.42, 4.3) * mm, v(61.45, 4.4) * mm, v(61.48, 4.48) * mm, v(61.5, 4.56) * mm]});
            skFitSpline(sketch, "E1806", {"points": [v(61.5, 4.56) * mm, v(61.66, 5.15) * mm, v(61.81, 5.75) * mm, v(61.95, 6.35) * mm]});
            skFitSpline(sketch, "E1807", {"points": [v(61.95, 6.35) * mm, v(62.2, 7.48) * mm, v(62.46, 8.62) * mm, v(62.7, 9.76) * mm]});
            skFitSpline(sketch, "E1808", {"points": [v(62.7, 9.76) * mm, v(62.81, 10.23) * mm, v(62.92, 10.7) * mm, v(63.02, 11.18) * mm]});
            skFitSpline(sketch, "E1809", {"points": [v(63.02, 11.18) * mm, v(63.08, 11.46) * mm, v(63.27, 11.62) * mm, v(63.54, 11.6) * mm]});
            skFitSpline(sketch, "E1810", {"points": [v(63.54, 11.6) * mm, v(63.8, 11.6) * mm, v(63.97, 11.42) * mm, v(64.01, 11.15) * mm]});
            skFitSpline(sketch, "E1811", {"points": [v(64.01, 11.15) * mm, v(64.06, 10.9) * mm, v(64.1, 10.66) * mm, v(64.16, 10.42) * mm]});
            skFitSpline(sketch, "E1812", {"points": [v(64.16, 10.42) * mm, v(64.4, 9.3) * mm, v(64.66, 8.16) * mm, v(64.92, 7.04) * mm]});
            skFitSpline(sketch, "E1813", {"points": [v(64.92, 7.04) * mm, v(65.07, 6.36) * mm, v(65.25, 5.69) * mm, v(65.41, 5.02) * mm]});
            skFitSpline(sketch, "E1814", {"points": [v(65.41, 5.02) * mm, v(65.47, 4.78) * mm, v(65.53, 4.55) * mm, v(65.6, 4.28) * mm]});
            skFitSpline(sketch, "E1815", {"points": [v(65.6, 4.28) * mm, v(65.66, 4.35) * mm, v(65.7, 4.4) * mm, v(65.73, 4.44) * mm]});
            skFitSpline(sketch, "E1816", {"points": [v(65.73, 4.44) * mm, v(65.86, 4.7) * mm, v(65.99, 4.96) * mm, v(66.1, 5.22) * mm]});
            skFitSpline(sketch, "E1817", {"points": [v(66.1, 5.22) * mm, v(66.13, 5.28) * mm, v(66.13, 5.36) * mm, v(66.12, 5.43) * mm]});
            skFitSpline(sketch, "E1818", {"points": [v(66.12, 5.43) * mm, v(66.02, 6.12) * mm, v(65.9, 6.82) * mm, v(65.82, 7.51) * mm]});
            skFitSpline(sketch, "E1819", {"points": [v(65.82, 7.51) * mm, v(65.75, 8.02) * mm, v(65.7, 8.52) * mm, v(65.64, 9.03) * mm]});
            skFitSpline(sketch, "E1820", {"points": [v(65.64, 9.03) * mm, v(65.62, 9.19) * mm, v(65.6, 9.35) * mm, v(65.6, 9.5) * mm]});
            skFitSpline(sketch, "E1821", {"points": [v(65.6, 9.5) * mm, v(65.62, 9.77) * mm, v(65.83, 9.96) * mm, v(66.09, 9.98) * mm]});
            skFitSpline(sketch, "E1822", {"points": [v(66.09, 9.98) * mm, v(66.36, 9.99) * mm, v(66.56, 9.84) * mm, v(66.62, 9.59) * mm]});
            skFitSpline(sketch, "E1823", {"points": [v(66.62, 9.59) * mm, v(66.63, 9.56) * mm, v(66.64, 9.52) * mm, v(66.63, 9.5) * mm]});
            skFitSpline(sketch, "E1824", {"points": [v(66.63, 9.5) * mm, v(66.54, 9.04) * mm, v(66.68, 8.6) * mm, v(66.71, 8.16) * mm]});
            skFitSpline(sketch, "E1825", {"points": [v(66.71, 8.16) * mm, v(66.74, 7.73) * mm, v(66.83, 7.31) * mm, v(66.9, 6.85) * mm]});
            skFitSpline(sketch, "E1826", {"points": [v(66.9, 6.85) * mm, v(66.94, 6.9) * mm, v(66.97, 6.93) * mm, v(67, 6.96) * mm]});
            skFitSpline(sketch, "E1827", {"points": [v(67, 6.96) * mm, v(67.12, 7.19) * mm, v(67.24, 7.4) * mm, v(67.35, 7.64) * mm]});
            skFitSpline(sketch, "E1828", {"points": [v(67.35, 7.64) * mm, v(67.4, 7.73) * mm, v(67.41, 7.84) * mm, v(67.4, 7.94) * mm]});
            skFitSpline(sketch, "E1829", {"points": [v(67.4, 7.94) * mm, v(67.33, 8.6) * mm, v(67.26, 9.28) * mm, v(67.17, 9.96) * mm]});
            skFitSpline(sketch, "E1830", {"points": [v(67.17, 9.96) * mm, v(67.1, 10.47) * mm, v(67.02, 10.98) * mm, v(66.95, 11.5) * mm]});
            skFitSpline(sketch, "E1831", {"points": [v(66.95, 11.5) * mm, v(66.93, 11.62) * mm, v(66.92, 11.75) * mm, v(66.93, 11.88) * mm]});
            skFitSpline(sketch, "E1832", {"points": [v(66.93, 11.88) * mm, v(66.94, 12.08) * mm, v(67.07, 12.23) * mm, v(67.26, 12.3) * mm]});
            skFitSpline(sketch, "E1833", {"points": [v(67.26, 12.3) * mm, v(67.46, 12.36) * mm, v(67.64, 12.3) * mm, v(67.76, 12.15) * mm]});
            skFitSpline(sketch, "E1834", {"points": [v(67.76, 12.15) * mm, v(67.9, 11.98) * mm, v(68, 11.78) * mm, v(67.96, 11.54) * mm]});
            skFitSpline(sketch, "E1835", {"points": [v(67.96, 11.54) * mm, v(67.94, 11.42) * mm, v(67.98, 11.28) * mm, v(68, 11.16) * mm]});
            skFitSpline(sketch, "E1836", {"points": [v(68, 11.16) * mm, v(68.08, 10.52) * mm, v(68.16, 9.88) * mm, v(68.24, 9.18) * mm]});
            skFitSpline(sketch, "E1837", {"points": [v(68.24, 9.18) * mm, v(68.43, 9.48) * mm, v(68.6, 9.73) * mm, v(68.75, 9.98) * mm]});
            skFitSpline(sketch, "E1838", {"points": [v(68.75, 9.98) * mm, v(68.78, 10.04) * mm, v(68.76, 10.12) * mm, v(68.75, 10.2) * mm]});
            skFitSpline(sketch, "E1839", {"points": [v(68.75, 10.2) * mm, v(68.7, 10.64) * mm, v(68.68, 11.08) * mm, v(68.62, 11.53) * mm]});
            skFitSpline(sketch, "E1840", {"points": [v(68.62, 11.53) * mm, v(68.56, 11.98) * mm, v(68.47, 12.44) * mm, v(68.4, 12.9) * mm]});
            skFitSpline(sketch, "E1841", {"points": [v(68.4, 12.9) * mm, v(68.37, 13.14) * mm, v(68.34, 13.39) * mm, v(68.32, 13.63) * mm]});
            skFitSpline(sketch, "E1842", {"points": [v(68.32, 13.63) * mm, v(68.3, 13.9) * mm, v(68.45, 14.12) * mm, v(68.67, 14.16) * mm]});
            skFitSpline(sketch, "E1843", {"points": [v(68.67, 14.16) * mm, v(68.96, 14.22) * mm, v(69.17, 14.1) * mm, v(69.27, 13.82) * mm]});
            skFitSpline(sketch, "E1844", {"points": [v(69.27, 13.82) * mm, v(69.3, 13.75) * mm, v(69.32, 13.68) * mm, v(69.32, 13.6) * mm]});
            skFitSpline(sketch, "E1845", {"points": [v(69.32, 13.6) * mm, v(69.3, 13.17) * mm, v(69.44, 12.76) * mm, v(69.5, 12.33) * mm]});
            skFitSpline(sketch, "E1846", {"points": [v(69.5, 12.33) * mm, v(69.54, 12.06) * mm, v(69.57, 11.78) * mm, v(69.62, 11.47) * mm]});
            skFitSpline(sketch, "E1847", {"points": [v(69.62, 11.47) * mm, v(69.91, 11.8) * mm, v(70.06, 12.17) * mm, v(70.3, 12.5) * mm]});
            skFitSpline(sketch, "E1848", {"points": [v(70.3, 12.5) * mm, v(70.22, 12.56) * mm, v(70.12, 12.6) * mm, v(70.07, 12.67) * mm]});
            skFitSpline(sketch, "E1849", {"points": [v(70.07, 12.67) * mm, v(70, 12.77) * mm, v(69.93, 12.89) * mm, v(69.9, 13) * mm]});
            skFitSpline(sketch, "E1850", {"points": [v(69.9, 13) * mm, v(69.8, 13.48) * mm, v(69.72, 13.96) * mm, v(69.63, 14.44) * mm]});
            skFitSpline(sketch, "E1851", {"points": [v(69.63, 14.44) * mm, v(69.6, 14.59) * mm, v(69.53, 14.73) * mm, v(69.5, 14.88) * mm]});
            skFitSpline(sketch, "E1852", {"points": [v(69.5, 14.88) * mm, v(69.47, 15.03) * mm, v(69.43, 15.19) * mm, v(69.43, 15.34) * mm]});
            skFitSpline(sketch, "E1853", {"points": [v(69.43, 15.34) * mm, v(69.43, 15.61) * mm, v(69.65, 15.8) * mm, v(69.91, 15.8) * mm]});
            skFitSpline(sketch, "E1854", {"points": [v(69.91, 15.8) * mm, v(70.17, 15.79) * mm, v(70.43, 15.56) * mm, v(70.47, 15.32) * mm]});
            skFitSpline(sketch, "E1855", {"points": [v(70.47, 15.32) * mm, v(70.52, 15.01) * mm, v(70.58, 14.7) * mm, v(70.63, 14.4) * mm]});
            skFitSpline(sketch, "E1856", {"points": [v(70.63, 14.4) * mm, v(70.7, 14.07) * mm, v(70.76, 13.73) * mm, v(70.84, 13.37) * mm]});
            skFitSpline(sketch, "E1857", {"points": [v(70.84, 13.37) * mm, v(70.97, 13.5) * mm, v(71.07, 13.64) * mm, v(71.05, 13.83) * mm]});
            skFitSpline(sketch, "E1858", {"points": [v(71.05, 13.83) * mm, v(71.02, 14.32) * mm, v(71, 14.8) * mm, v(70.96, 15.29) * mm]});
            skFitSpline(sketch, "E1859", {"points": [v(70.96, 15.29) * mm, v(70.96, 15.33) * mm, v(70.96, 15.37) * mm, v(70.96, 15.4) * mm]});
            skFitSpline(sketch, "E1860", {"points": [v(70.96, 15.4) * mm, v(70.9, 15.77) * mm, v(71.05, 16) * mm, v(71.4, 16.14) * mm]});
            skFitSpline(sketch, "E1861", {"points": [v(71.4, 16.14) * mm, v(71.7, 16.26) * mm, v(72, 16.4) * mm, v(72.3, 16.55) * mm]});
            skFitSpline(sketch, "E1862", {"points": [v(72.3, 16.55) * mm, v(72.57, 16.67) * mm, v(72.83, 16.8) * mm, v(73.09, 16.92) * mm]});
            skFitSpline(sketch, "E1863", {"points": [v(73.09, 16.92) * mm, v(73.33, 17.03) * mm, v(73.57, 16.99) * mm, v(73.72, 16.8) * mm]});
            skFitSpline(sketch, "E1864", {"points": [v(73.72, 16.8) * mm, v(73.77, 16.74) * mm, v(73.82, 16.65) * mm, v(73.83, 16.57) * mm]});
            skFitSpline(sketch, "E1865", {"points": [v(73.83, 16.57) * mm, v(73.86, 16.36) * mm, v(73.87, 16.14) * mm, v(73.88, 15.93) * mm]});
            skFitSpline(sketch, "E1866", {"points": [v(73.88, 15.93) * mm, v(73.89, 15.87) * mm, v(73.89, 15.81) * mm, v(73.9, 15.76) * mm]});
            skFitSpline(sketch, "E1867", {"points": [v(73.9, 15.76) * mm, v(73.93, 15.36) * mm, v(73.98, 14.95) * mm, v(74.02, 14.55) * mm]});
            skFitSpline(sketch, "E1868", {"points": [v(74.02, 14.55) * mm, v(74.05, 14.28) * mm, v(73.96, 14.07) * mm, v(73.73, 13.94) * mm]});
            skFitSpline(sketch, "E1869", {"points": [v(73.73, 13.94) * mm, v(73.57, 13.86) * mm, v(73.41, 13.79) * mm, v(73.26, 13.7) * mm]});
            skFitSpline(sketch, "E1870", {"points": [v(73.26, 13.7) * mm, v(72.89, 13.52) * mm, v(72.52, 13.33) * mm, v(72.15, 13.14) * mm]});
            skFitSpline(sketch, "E1871", {"points": [v(72.15, 13.14) * mm, v(72, 13.06) * mm, v(72, 13.05) * mm, v(71.9, 12.77) * mm]});
            skFitSpline(sketch, "E1872", {"points": [v(71.9, 12.77) * mm, v(71.97, 12.79) * mm, v(72.03, 12.8) * mm, v(72.09, 12.82) * mm]});
            skFitSpline(sketch, "E1873", {"points": [v(72.09, 12.82) * mm, v(72.57, 12.98) * mm, v(73.04, 13.13) * mm, v(73.52, 13.29) * mm]});
            skFitSpline(sketch, "E1874", {"points": [v(73.52, 13.29) * mm, v(73.59, 13.31) * mm, v(73.64, 13.36) * mm, v(73.7, 13.39) * mm]});
            skFitSpline(sketch, "E1875", {"points": [v(73.7, 13.39) * mm, v(73.92, 13.5) * mm, v(74.11, 13.45) * mm, v(74.3, 13.33) * mm]});
            skFitSpline(sketch, "E1876", {"points": [v(74.3, 13.33) * mm, v(74.47, 13.23) * mm, v(74.54, 13.07) * mm, v(74.52, 12.86) * mm]});
            skFitSpline(sketch, "E1877", {"points": [v(74.52, 12.86) * mm, v(74.5, 12.7) * mm, v(74.43, 12.57) * mm, v(74.29, 12.5) * mm]});
            skFitSpline(sketch, "E1878", {"points": [v(74.29, 12.5) * mm, v(74.18, 12.44) * mm, v(74.05, 12.4) * mm, v(73.93, 12.36) * mm]});
            skFitSpline(sketch, "E1879", {"points": [v(73.93, 12.36) * mm, v(73.53, 12.24) * mm, v(73.12, 12.13) * mm, v(72.71, 12) * mm]});
            skFitSpline(sketch, "E1880", {"points": [v(72.71, 12) * mm, v(72.53, 11.95) * mm, v(72.35, 11.89) * mm, v(72.17, 11.81) * mm]});
            skFitSpline(sketch, "E1881", {"points": [v(72.17, 11.81) * mm, v(71.92, 11.7) * mm, v(71.67, 11.66) * mm, v(71.43, 11.88) * mm]});
            skFitSpline(sketch, "E1882", {"points": [v(71.43, 11.88) * mm, v(71.23, 11.5) * mm, v(71.04, 11.15) * mm, v(70.85, 10.8) * mm]});
            skFitSpline(sketch, "E1883", {"points": [v(70.85, 10.8) * mm, v(70.88, 10.78) * mm, v(70.89, 10.77) * mm, v(70.9, 10.77) * mm]});
            skFitSpline(sketch, "E1884", {"points": [v(70.9, 10.77) * mm, v(71.55, 11.03) * mm, v(72.2, 11.29) * mm, v(72.85, 11.55) * mm]});
            skFitSpline(sketch, "E1885", {"points": [v(72.85, 11.55) * mm, v(73, 11.62) * mm, v(73.16, 11.64) * mm, v(73.32, 11.62) * mm]});
            skFitSpline(sketch, "E1886", {"points": [v(73.32, 11.62) * mm, v(73.5, 11.6) * mm, v(73.65, 11.42) * mm, v(73.68, 11.22) * mm]});
            skFitSpline(sketch, "E1887", {"points": [v(73.68, 11.22) * mm, v(73.72, 11.02) * mm, v(73.6, 10.8) * mm, v(73.4, 10.71) * mm]});
            skFitSpline(sketch, "E1888", {"points": [v(73.4, 10.71) * mm, v(73.18, 10.6) * mm, v(72.95, 10.5) * mm, v(72.72, 10.42) * mm]});
            skFitSpline(sketch, "E1889", {"points": [v(72.72, 10.42) * mm, v(71.89, 10.14) * mm, v(71.08, 9.8) * mm, v(70.29, 9.41) * mm]});
            skFitSpline(sketch, "E1890", {"points": [v(70.29, 9.41) * mm, v(70.07, 9.31) * mm, v(69.95, 9.18) * mm, v(69.85, 8.98) * mm]});
            skFitSpline(sketch, "E1891", {"points": [v(69.85, 8.98) * mm, v(69.77, 8.8) * mm, v(69.68, 8.64) * mm, v(69.57, 8.43) * mm]});
            skFitSpline(sketch, "E1892", {"points": [v(69.57, 8.43) * mm, v(69.66, 8.47) * mm, v(69.73, 8.48) * mm, v(69.79, 8.5) * mm]});
            skFitSpline(sketch, "E1893", {"points": [v(69.79, 8.5) * mm, v(70.4, 8.76) * mm, v(71, 9.02) * mm, v(71.6, 9.27) * mm]});
            skFitSpline(sketch, "E1894", {"points": [v(71.6, 9.27) * mm, v(71.65, 9.3) * mm, v(71.7, 9.31) * mm, v(71.75, 9.35) * mm]});
            skFitSpline(sketch, "E1895", {"points": [v(71.75, 9.35) * mm, v(71.91, 9.5) * mm, v(72.1, 9.5) * mm, v(72.31, 9.5) * mm]});
            skFitSpline(sketch, "E1896", {"points": [v(72.31, 9.5) * mm, v(72.52, 9.48) * mm, v(72.67, 9.37) * mm, v(72.74, 9.17) * mm]});
            skFitSpline(sketch, "E1897", {"points": [v(72.74, 9.17) * mm, v(72.8, 8.98) * mm, v(72.76, 8.78) * mm, v(72.6, 8.65) * mm]});
            skFitSpline(sketch, "E1898", {"points": [v(72.6, 8.65) * mm, v(72.52, 8.59) * mm, v(72.42, 8.54) * mm, v(72.33, 8.5) * mm]});
            skFitSpline(sketch, "E1899", {"points": [v(72.33, 8.5) * mm, v(71.34, 8.08) * mm, v(70.35, 7.67) * mm, v(69.37, 7.26) * mm]});
            skFitSpline(sketch, "E1900", {"points": [v(69.37, 7.26) * mm, v(69.3, 7.23) * mm, v(69.23, 7.2) * mm, v(69.17, 7.17) * mm]});
            skFitSpline(sketch, "E1901", {"points": [v(69.17, 7.17) * mm, v(68.73, 6.99) * mm, v(68.73, 7) * mm, v(68.48, 6.6) * mm]});
            skFitSpline(sketch, "E1902", {"points": [v(68.48, 6.6) * mm, v(68.4, 6.44) * mm, v(68.3, 6.3) * mm, v(68.2, 6.1) * mm]});
            skFitSpline(sketch, "E1903", {"points": [v(68.2, 6.1) * mm, v(68.28, 6.13) * mm, v(68.33, 6.13) * mm, v(68.37, 6.15) * mm]});
            skFitSpline(sketch, "E1904", {"points": [v(68.37, 6.15) * mm, v(69.04, 6.43) * mm, v(69.7, 6.71) * mm, v(70.38, 7) * mm]});
            skFitSpline(sketch, "E1905", {"points": [v(70.38, 7) * mm, v(70.44, 7.02) * mm, v(70.5, 7.07) * mm, v(70.56, 7.11) * mm]});
            skFitSpline(sketch, "E1906", {"points": [v(70.56, 7.11) * mm, v(70.8, 7.3) * mm, v(71.1, 7.28) * mm, v(71.27, 7.04) * mm]});
            skFitSpline(sketch, "E1907", {"points": [v(71.27, 7.04) * mm, v(71.46, 6.8) * mm, v(71.42, 6.47) * mm, v(71.17, 6.3) * mm]});
            skFitSpline(sketch, "E1908", {"points": [v(71.17, 6.3) * mm, v(71.09, 6.24) * mm, v(71, 6.2) * mm, v(70.9, 6.16) * mm]});
            skFitSpline(sketch, "E1909", {"points": [v(70.9, 6.16) * mm, v(69.75, 5.68) * mm, v(68.6, 5.2) * mm, v(67.46, 4.74) * mm]});
            skFitSpline(sketch, "E1910", {"points": [v(67.46, 4.74) * mm, v(67.32, 4.68) * mm, v(67.2, 4.6) * mm, v(67.11, 4.47) * mm]});
            skFitSpline(sketch, "E1911", {"points": [v(67.11, 4.47) * mm, v(66.93, 4.24) * mm, v(66.77, 4) * mm, v(66.63, 3.69) * mm]});
            skFitSpline(sketch, "E1912", {"points": [v(66.63, 3.69) * mm, v(66.81, 3.73) * mm, v(66.96, 3.76) * mm, v(67.1, 3.8) * mm]});
            skFitSpline(sketch, "E1913", {"points": [v(67.1, 3.8) * mm, v(68, 4.06) * mm, v(68.88, 4.32) * mm, v(69.77, 4.58) * mm]});
            skFitSpline(sketch, "E1914", {"points": [v(69.77, 4.58) * mm, v(70.35, 4.76) * mm, v(70.94, 4.95) * mm, v(71.52, 5.14) * mm]});
            skFitSpline(sketch, "E1915", {"points": [v(71.52, 5.14) * mm, v(72.17, 5.35) * mm, v(72.82, 5.55) * mm, v(73.46, 5.77) * mm]});
            skFitSpline(sketch, "E1916", {"points": [v(73.46, 5.77) * mm, v(73.66, 5.84) * mm, v(73.93, 5.72) * mm, v(74.03, 5.54) * mm]});
            skFitSpline(sketch, "E1917", {"points": [v(74.03, 5.54) * mm, v(74.14, 5.34) * mm, v(74.1, 5.08) * mm, v(73.94, 4.92) * mm]});
            skFitSpline(sketch, "E1918", {"points": [v(73.94, 4.92) * mm, v(73.8, 4.8) * mm, v(73.66, 4.69) * mm, v(73.52, 4.57) * mm]});
            skFitSpline(sketch, "E1919", {"points": [v(73.52, 4.57) * mm, v(73.08, 4.16) * mm, v(72.64, 3.75) * mm, v(72.2, 3.34) * mm]});
            skFitSpline(sketch, "E1920", {"points": [v(72.2, 3.34) * mm, v(71.71, 2.9) * mm, v(71.22, 2.45) * mm, v(70.73, 2) * mm]});
            skFitSpline(sketch, "E1921", {"points": [v(70.73, 2) * mm, v(70.25, 1.54) * mm, v(69.77, 1.07) * mm, v(69.28, 0.6) * mm]});
            skFitSpline(sketch, "E1922", {"points": [v(69.28, 0.6) * mm, v(69.17, 0.5) * mm, v(69.06, 0.4) * mm, v(68.95, 0.3) * mm]});
            skFitSpline(sketch, "E1923", {"points": [v(68.95, 0.3) * mm, v(68.89, 0.22) * mm, v(68.83, 0.15) * mm, v(68.76, 0.08) * mm]});
            skFitSpline(sketch, "E1924", {"points": [v(68.76, 0.08) * mm, v(69.05, -0.05) * mm, v(69.31, 0.05) * mm, v(69.58, 0.06) * mm]});
            skFitSpline(sketch, "E1925", {"points": [v(69.58, 0.06) * mm, v(69.78, 0.08) * mm, v(69.95, 0.16) * mm, v(70.11, 0.29) * mm]});
            skFitSpline(sketch, "E1926", {"points": [v(70.11, 0.29) * mm, v(71.07, 1.04) * mm, v(72.04, 1.77) * mm, v(73, 2.51) * mm]});
            skFitSpline(sketch, "E1927", {"points": [v(73, 2.51) * mm, v(73.08, 2.57) * mm, v(73.17, 2.64) * mm, v(73.26, 2.68) * mm]});
            skFitSpline(sketch, "E1928", {"points": [v(73.26, 2.68) * mm, v(73.53, 2.8) * mm, v(73.83, 2.68) * mm, v(73.95, 2.4) * mm]});
            skFitSpline(sketch, "E1929", {"points": [v(73.95, 2.4) * mm, v(74.07, 2.13) * mm, v(73.95, 1.85) * mm, v(73.66, 1.74) * mm]});
            skFitSpline(sketch, "E1930", {"points": [v(73.66, 1.74) * mm, v(73.6, 1.71) * mm, v(73.54, 1.7) * mm, v(73.49, 1.66) * mm]});
            skFitSpline(sketch, "E1931", {"points": [v(73.49, 1.66) * mm, v(72.89, 1.2) * mm, v(72.3, 0.75) * mm, v(71.7, 0.3) * mm]});
            skFitSpline(sketch, "E1932", {"points": [v(71.7, 0.3) * mm, v(71.67, 0.28) * mm, v(71.64, 0.26) * mm, v(71.63, 0.2) * mm]});
            skFitSpline(sketch, "E1933", {"points": [v(71.63, 0.2) * mm, v(71.69, 0.2) * mm, v(71.75, 0.19) * mm, v(71.8, 0.2) * mm]});
            skFitSpline(sketch, "E1934", {"points": [v(71.8, 0.2) * mm, v(72.05, 0.2) * mm, v(72.3, 0.2) * mm, v(72.55, 0.23) * mm]});
            skFitSpline(sketch, "E1935", {"points": [v(72.55, 0.23) * mm, v(72.63, 0.24) * mm, v(72.73, 0.29) * mm, v(72.8, 0.34) * mm]});
            skFitSpline(sketch, "E1936", {"points": [v(72.8, 0.34) * mm, v(73.6, 0.93) * mm, v(74.38, 1.52) * mm, v(75.16, 2.1) * mm]});
            skFitSpline(sketch, "E1937", {"points": [v(75.16, 2.1) * mm, v(75.34, 2.24) * mm, v(75.5, 2.4) * mm, v(75.68, 2.53) * mm]});
            skFitSpline(sketch, "E1938", {"points": [v(75.68, 2.53) * mm, v(75.78, 2.6) * mm, v(75.88, 2.68) * mm, v(75.98, 2.73) * mm]});
            skFitSpline(sketch, "E1939", {"points": [v(75.98, 2.73) * mm, v(76.18, 2.81) * mm, v(76.4, 2.76) * mm, v(76.53, 2.6) * mm]});
            skFitSpline(sketch, "E1940", {"points": [v(76.53, 2.6) * mm, v(76.66, 2.46) * mm, v(76.7, 2.25) * mm, v(76.6, 2.07) * mm]});
            skFitSpline(sketch, "E1941", {"points": [v(76.6, 2.07) * mm, v(76.5, 1.9) * mm, v(76.4, 1.72) * mm, v(76.2, 1.65) * mm]});
            skFitSpline(sketch, "E1942", {"points": [v(76.2, 1.65) * mm, v(76.15, 1.64) * mm, v(76.11, 1.6) * mm, v(76.08, 1.58) * mm]});
            skFitSpline(sketch, "E1943", {"points": [v(76.08, 1.58) * mm, v(75.52, 1.16) * mm, v(74.97, 0.74) * mm, v(74.41, 0.32) * mm]});
            skFitSpline(sketch, "E1944", {"points": [v(74.41, 0.32) * mm, v(74.38, 0.3) * mm, v(74.35, 0.27) * mm, v(74.28, 0.21) * mm]});
            skFitSpline(sketch, "E1945", {"points": [v(74.28, 0.21) * mm, v(74.64, 0.2) * mm, v(74.95, 0.2) * mm, v(75.25, 0.2) * mm]});
            skFitSpline(sketch, "E1946", {"points": [v(75.25, 0.2) * mm, v(75.29, 0.2) * mm, v(75.33, 0.22) * mm, v(75.36, 0.24) * mm]});
            skFitSpline(sketch, "E1947", {"points": [v(75.36, 0.24) * mm, v(75.91, 0.65) * mm, v(76.47, 1.05) * mm, v(77.02, 1.46) * mm]});
            skFitSpline(sketch, "E1948", {"points": [v(77.02, 1.46) * mm, v(77.39, 1.74) * mm, v(77.74, 2.04) * mm, v(78.1, 2.33) * mm]});
            skFitSpline(sketch, "E1949", {"points": [v(78.1, 2.33) * mm, v(78.15, 2.37) * mm, v(78.2, 2.4) * mm, v(78.26, 2.44) * mm]});
            skFitSpline(sketch, "E1950", {"points": [v(78.26, 2.44) * mm, v(78.45, 2.54) * mm, v(78.68, 2.5) * mm, v(78.83, 2.34) * mm]});
            skFitSpline(sketch, "E1951", {"points": [v(78.83, 2.34) * mm, v(78.98, 2.18) * mm, v(79.02, 1.96) * mm, v(78.9, 1.77) * mm]});
            skFitSpline(sketch, "E1952", {"points": [v(78.9, 1.77) * mm, v(78.83, 1.67) * mm, v(78.73, 1.58) * mm, v(78.63, 1.5) * mm]});
            skFitSpline(sketch, "E1953", {"points": [v(78.63, 1.5) * mm, v(78.44, 1.34) * mm, v(78.23, 1.2) * mm, v(78.04, 1.05) * mm]});
            skFitSpline(sketch, "E1954", {"points": [v(78.04, 1.05) * mm, v(77.69, 0.76) * mm, v(77.34, 0.47) * mm, v(76.96, 0.17) * mm]});
            skFitSpline(sketch, "E1955", {"points": [v(76.96, 0.17) * mm, v(77.39, 0.1) * mm, v(77.8, 0.1) * mm, v(78.21, 0.11) * mm]});
            skFitSpline(sketch, "E1956", {"points": [v(78.21, 0.11) * mm, v(78.16, 0.4) * mm, v(78.3, 0.6) * mm, v(78.5, 0.76) * mm]});
            skFitSpline(sketch, "E1957", {"points": [v(78.5, 0.76) * mm, v(78.87, 1.07) * mm, v(79.23, 1.39) * mm, v(79.59, 1.7) * mm]});
            skFitSpline(sketch, "E1958", {"points": [v(79.59, 1.7) * mm, v(79.68, 1.79) * mm, v(79.75, 1.88) * mm, v(79.84, 1.97) * mm]});
            skFitSpline(sketch, "E1959", {"points": [v(79.84, 1.97) * mm, v(79.95, 2.08) * mm, v(80.06, 2.2) * mm, v(80.2, 2.28) * mm]});
            skFitSpline(sketch, "E1960", {"points": [v(80.2, 2.28) * mm, v(80.53, 2.47) * mm, v(80.89, 2.25) * mm, v(80.9, 1.87) * mm]});
            skFitSpline(sketch, "E1961", {"points": [v(80.9, 1.87) * mm, v(80.92, 1.6) * mm, v(80.83, 1.4) * mm, v(80.58, 1.28) * mm]});
            skFitSpline(sketch, "E1962", {"points": [v(80.58, 1.28) * mm, v(80.45, 1.21) * mm, v(80.36, 1.08) * mm, v(80.24, 0.98) * mm]});
            skFitSpline(sketch, "E1963", {"points": [v(80.24, 0.98) * mm, v(79.9, 0.68) * mm, v(79.57, 0.39) * mm, v(79.22, 0.08) * mm]});
            skFitSpline(sketch, "E1964", {"points": [v(79.22, 0.08) * mm, v(79.4, 0.03) * mm, v(79.55, 0.02) * mm, v(79.7, 0.12) * mm]});
            skFitSpline(sketch, "E1965", {"points": [v(79.7, 0.12) * mm, v(80.12, 0.4) * mm, v(80.54, 0.67) * mm, v(80.96, 0.94) * mm]});
            skFitSpline(sketch, "E1966", {"points": [v(80.96, 0.94) * mm, v(81.04, 1) * mm, v(81.12, 1.05) * mm, v(81.2, 1.1) * mm]});
            skFitSpline(sketch, "E1967", {"points": [v(81.2, 1.1) * mm, v(81.4, 1.2) * mm, v(81.58, 1.2) * mm, v(81.75, 1.07) * mm]});
            skFitSpline(sketch, "E1968", {"points": [v(81.75, 1.07) * mm, v(82.07, 0.85) * mm, v(82.38, 0.63) * mm, v(82.69, 0.4) * mm]});
            skFitSpline(sketch, "E1969", {"points": [v(82.69, 0.4) * mm, v(82.92, 0.24) * mm, v(83.14, 0.08) * mm, v(83.38, -0.07) * mm]});
            skFitSpline(sketch, "E1970", {"points": [v(83.38, -0.07) * mm, v(83.77, -0.31) * mm, v(83.73, -0.78) * mm, v(83.37, -1) * mm]});
            skFitSpline(sketch, "E1971", {"points": [v(83.37, -1) * mm, v(82.85, -1.35) * mm, v(82.35, -1.71) * mm, v(81.85, -2.08) * mm]});
            skFitSpline(sketch, "E1972", {"points": [v(81.85, -2.08) * mm, v(81.57, -2.28) * mm, v(81.32, -2.26) * mm, v(81.05, -2.08) * mm]});
            skFitSpline(sketch, "E1973", {"points": [v(81.05, -2.08) * mm, v(80.79, -1.9) * mm, v(80.52, -1.7) * mm, v(80.24, -1.53) * mm]});
            skFitSpline(sketch, "E1974", {"points": [v(80.24, -1.53) * mm, v(80.05, -1.4) * mm, v(79.85, -1.28) * mm, v(79.65, -1.16) * mm]});
            skFitSpline(sketch, "E1975", {"points": [v(79.65, -1.16) * mm, v(79.52, -1.08) * mm, v(79.38, -1.1) * mm, v(79.2, -1.12) * mm]});
            skFitSpline(sketch, "E1976", {"points": [v(79.2, -1.12) * mm, v(79.27, -1.18) * mm, v(79.3, -1.22) * mm, v(79.34, -1.25) * mm]});
            skFitSpline(sketch, "E1977", {"points": [v(79.34, -1.25) * mm, v(79.72, -1.6) * mm, v(80.1, -1.94) * mm, v(80.48, -2.28) * mm]});
            skFitSpline(sketch, "E1978", {"points": [v(80.48, -2.28) * mm, v(80.53, -2.32) * mm, v(80.6, -2.35) * mm, v(80.66, -2.4) * mm]});
            skFitSpline(sketch, "E1979", {"points": [v(80.66, -2.4) * mm, v(80.9, -2.55) * mm, v(81, -2.93) * mm, v(80.85, -3.18) * mm]});
            skFitSpline(sketch, "E1980", {"points": [v(80.85, -3.18) * mm, v(80.72, -3.4) * mm, v(80.45, -3.48) * mm, v(80.22, -3.36) * mm]});
            skFitSpline(sketch, "E1981", {"points": [v(80.22, -3.36) * mm, v(80.12, -3.31) * mm, v(80.02, -3.25) * mm, v(79.95, -3.16) * mm]});
            skFitSpline(sketch, "E1982", {"points": [v(79.95, -3.16) * mm, v(79.52, -2.65) * mm, v(79, -2.24) * mm, v(78.49, -1.82) * mm]});
            skFitSpline(sketch, "E1983", {"points": [v(78.49, -1.82) * mm, v(78.3, -1.66) * mm, v(78.16, -1.47) * mm, v(78.21, -1.2) * mm]});
            skLineSegment(sketch, "E1984", {"start": v(78.21, -1.2) * mm, "end": v(76.94, -1.2) * mm});
            skFitSpline(sketch, "E1985", {"points": [v(76.94, -1.2) * mm, v(77.01, -1.27) * mm, v(77.04, -1.31) * mm, v(77.08, -1.35) * mm]});
            skFitSpline(sketch, "E1986", {"points": [v(77.08, -1.35) * mm, v(77.45, -1.65) * mm, v(77.82, -1.95) * mm, v(78.2, -2.25) * mm]});
            skFitSpline(sketch, "E1987", {"points": [v(78.2, -2.25) * mm, v(78.33, -2.36) * mm, v(78.48, -2.46) * mm, v(78.62, -2.56) * mm]});
            skFitSpline(sketch, "E1988", {"points": [v(78.62, -2.56) * mm, v(78.7, -2.62) * mm, v(78.78, -2.68) * mm, v(78.84, -2.75) * mm]});
            skFitSpline(sketch, "E1989", {"points": [v(78.84, -2.75) * mm, v(79.01, -2.96) * mm, v(79, -3.22) * mm, v(78.84, -3.4) * mm]});
            skFitSpline(sketch, "E1990", {"points": [v(78.84, -3.4) * mm, v(78.67, -3.59) * mm, v(78.4, -3.62) * mm, v(78.18, -3.46) * mm]});
            skFitSpline(sketch, "E1991", {"points": [v(78.18, -3.46) * mm, v(77.91, -3.26) * mm, v(77.64, -3.06) * mm, v(77.39, -2.84) * mm]});
            skFitSpline(sketch, "E1992", {"points": [v(77.39, -2.84) * mm, v(76.82, -2.36) * mm, v(76.24, -1.9) * mm, v(75.61, -1.5) * mm]});
            skFitSpline(sketch, "E1993", {"points": [v(75.61, -1.5) * mm, v(75.56, -1.46) * mm, v(75.5, -1.44) * mm, v(75.45, -1.4) * mm]});
            skFitSpline(sketch, "E1994", {"points": [v(75.45, -1.4) * mm, v(75.34, -1.26) * mm, v(75.2, -1.23) * mm, v(75.04, -1.25) * mm]});
            skFitSpline(sketch, "E1995", {"points": [v(75.04, -1.25) * mm, v(74.82, -1.27) * mm, v(74.59, -1.28) * mm, v(74.32, -1.3) * mm]});
            skFitSpline(sketch, "E1996", {"points": [v(74.32, -1.3) * mm, v(74.39, -1.36) * mm, v(74.43, -1.4) * mm, v(74.48, -1.44) * mm]});
            skFitSpline(sketch, "E1997", {"points": [v(74.48, -1.44) * mm, v(75.01, -1.85) * mm, v(75.54, -2.25) * mm, v(76.07, -2.65) * mm]});
            skFitSpline(sketch, "E1998", {"points": [v(76.07, -2.65) * mm, v(76.1, -2.67) * mm, v(76.15, -2.7) * mm, v(76.2, -2.72) * mm]});
            skFitSpline(sketch, "E1999", {"points": [v(76.2, -2.72) * mm, v(76.42, -2.8) * mm, v(76.53, -2.99) * mm, v(76.62, -3.18) * mm]});
            skFitSpline(sketch, "E2000", {"points": [v(76.62, -3.18) * mm, v(76.7, -3.37) * mm, v(76.65, -3.54) * mm, v(76.52, -3.69) * mm]});
            skFitSpline(sketch, "E2001", {"points": [v(76.52, -3.69) * mm, v(76.38, -3.83) * mm, v(76.2, -3.88) * mm, v(76.01, -3.8) * mm]});
            skFitSpline(sketch, "E2002", {"points": [v(76.01, -3.8) * mm, v(75.92, -3.77) * mm, v(75.82, -3.71) * mm, v(75.74, -3.65) * mm]});
            skFitSpline(sketch, "E2003", {"points": [v(75.74, -3.65) * mm, v(74.98, -3.07) * mm, v(74.22, -2.49) * mm, v(73.46, -1.9) * mm]});
            skFitSpline(sketch, "E2004", {"points": [v(73.46, -1.9) * mm, v(73.24, -1.74) * mm, v(73.02, -1.58) * mm, v(72.8, -1.41) * mm]});
            skFitSpline(sketch, "E2005", {"points": [v(72.8, -1.41) * mm, v(72.7, -1.33) * mm, v(72.6, -1.29) * mm, v(72.48, -1.29) * mm]});
            skFitSpline(sketch, "E2006", {"points": [v(72.48, -1.29) * mm, v(72.2, -1.29) * mm, v(71.91, -1.29) * mm, v(71.62, -1.29) * mm]});
            skFitSpline(sketch, "E2007", {"points": [v(71.62, -1.29) * mm, v(71.65, -1.31) * mm, v(71.67, -1.35) * mm, v(71.7, -1.38) * mm]});
            skFitSpline(sketch, "E2008", {"points": [v(71.7, -1.38) * mm, v(72.3, -1.83) * mm, v(72.89, -2.28) * mm, v(73.48, -2.72) * mm]});
            skFitSpline(sketch, "E2009", {"points": [v(73.48, -2.72) * mm, v(73.53, -2.76) * mm, v(73.6, -2.78) * mm, v(73.65, -2.8) * mm]});
            skFitSpline(sketch, "E2010", {"points": [v(73.65, -2.8) * mm, v(73.95, -2.93) * mm, v(74.07, -3.2) * mm, v(73.94, -3.48) * mm]});
            skFitSpline(sketch, "E2011", {"points": [v(73.94, -3.48) * mm, v(73.81, -3.77) * mm, v(73.5, -3.88) * mm, v(73.22, -3.73) * mm]});
            skFitSpline(sketch, "E2012", {"points": [v(73.22, -3.73) * mm, v(73.15, -3.7) * mm, v(73.08, -3.65) * mm, v(73.02, -3.6) * mm]});
            skFitSpline(sketch, "E2013", {"points": [v(73.02, -3.6) * mm, v(72, -2.82) * mm, v(71, -2.04) * mm, v(69.98, -1.26) * mm]});
            skFitSpline(sketch, "E2014", {"points": [v(69.98, -1.26) * mm, v(69.9, -1.19) * mm, v(69.81, -1.15) * mm, v(69.7, -1.15) * mm]});
            skFitSpline(sketch, "E2015", {"points": [v(69.7, -1.15) * mm, v(69.42, -1.14) * mm, v(69.13, -1.12) * mm, v(68.84, -1.1) * mm]});
            skFitSpline(sketch, "E2016", {"points": [v(68.84, -1.1) * mm, v(68.82, -1.1) * mm, v(68.8, -1.12) * mm, v(68.75, -1.14) * mm]});
            skFitSpline(sketch, "E2017", {"points": [v(68.75, -1.14) * mm, v(68.83, -1.23) * mm, v(68.9, -1.3) * mm, v(68.96, -1.37) * mm]});
            skFitSpline(sketch, "E2018", {"points": [v(68.96, -1.37) * mm, v(69.8, -2.16) * mm, v(70.62, -2.95) * mm, v(71.46, -3.73) * mm]});
            skFitSpline(sketch, "E2019", {"points": [v(71.46, -3.73) * mm, v(72.11, -4.34) * mm, v(72.78, -4.95) * mm, v(73.44, -5.57) * mm]});
            skFitSpline(sketch, "E2020", {"points": [v(73.44, -5.57) * mm, v(73.59, -5.7) * mm, v(73.73, -5.82) * mm, v(73.88, -5.94) * mm]});
            skFitSpline(sketch, "E2021", {"points": [v(73.88, -5.94) * mm, v(74.1, -6.12) * mm, v(74.16, -6.38) * mm, v(74.04, -6.6) * mm]});
            skFitSpline(sketch, "E2022", {"points": [v(74.04, -6.6) * mm, v(73.9, -6.83) * mm, v(73.67, -6.9) * mm, v(73.4, -6.81) * mm]});
            skFitSpline(sketch, "E2023", {"points": [v(73.4, -6.81) * mm, v(72.74, -6.6) * mm, v(72.09, -6.39) * mm, v(71.43, -6.18) * mm]});
            skFitSpline(sketch, "E2024", {"points": [v(71.43, -6.18) * mm, v(70.5, -5.89) * mm, v(69.55, -5.6) * mm, v(68.6, -5.3) * mm]});
            skFitSpline(sketch, "E2025", {"points": [v(68.6, -5.3) * mm, v(68.04, -5.13) * mm, v(67.47, -4.97) * mm, v(66.9, -4.81) * mm]});
            skFitSpline(sketch, "E2026", {"points": [v(66.9, -4.81) * mm, v(66.82, -4.8) * mm, v(66.74, -4.79) * mm, v(66.65, -4.78) * mm]});
            skFitSpline(sketch, "E2027", {"points": [v(66.65, -4.78) * mm, v(66.78, -5.14) * mm, v(67.02, -5.42) * mm, v(67.24, -5.7) * mm]});
            skFitSpline(sketch, "E2028", {"points": [v(67.24, -5.7) * mm, v(67.26, -5.74) * mm, v(67.33, -5.75) * mm, v(67.38, -5.77) * mm]});
            skFitSpline(sketch, "E2029", {"points": [v(67.38, -5.77) * mm, v(68.56, -6.26) * mm, v(69.74, -6.75) * mm, v(70.92, -7.24) * mm]});
            skFitSpline(sketch, "E2030", {"points": [v(70.92, -7.24) * mm, v(71, -7.27) * mm, v(71.07, -7.3) * mm, v(71.14, -7.34) * mm]});
            skFitSpline(sketch, "E2031", {"points": [v(71.14, -7.34) * mm, v(71.4, -7.52) * mm, v(71.47, -7.84) * mm, v(71.28, -8.1) * mm]});
            skFitSpline(sketch, "E2032", {"points": [v(71.28, -8.1) * mm, v(71.1, -8.34) * mm, v(70.8, -8.37) * mm, v(70.55, -8.18) * mm]});
            skFitSpline(sketch, "E2033", {"points": [v(70.55, -8.18) * mm, v(70.5, -8.13) * mm, v(70.44, -8.09) * mm, v(70.37, -8.06) * mm]});
            skFitSpline(sketch, "E2034", {"points": [v(70.37, -8.06) * mm, v(69.73, -7.79) * mm, v(69.1, -7.52) * mm, v(68.45, -7.25) * mm]});
            skFitSpline(sketch, "E2035", {"points": [v(68.45, -7.25) * mm, v(68.39, -7.22) * mm, v(68.32, -7.2) * mm, v(68.22, -7.22) * mm]});
            skFitSpline(sketch, "E2036", {"points": [v(68.22, -7.22) * mm, v(68.39, -7.5) * mm, v(68.56, -7.77) * mm, v(68.74, -8.03) * mm]});
            skFitSpline(sketch, "E2037", {"points": [v(68.74, -8.03) * mm, v(68.77, -8.08) * mm, v(68.84, -8.1) * mm, v(68.9, -8.13) * mm]});
            skFitSpline(sketch, "E2038", {"points": [v(68.9, -8.13) * mm, v(69.82, -8.53) * mm, v(70.75, -8.92) * mm, v(71.67, -9.32) * mm]});
            skFitSpline(sketch, "E2039", {"points": [v(71.67, -9.32) * mm, v(71.9, -9.41) * mm, v(72.12, -9.48) * mm, v(72.34, -9.57) * mm]});
            skFitSpline(sketch, "E2040", {"points": [v(72.34, -9.57) * mm, v(72.54, -9.65) * mm, v(72.7, -9.76) * mm, v(72.75, -9.98) * mm]});
            skFitSpline(sketch, "E2041", {"points": [v(72.75, -9.98) * mm, v(72.82, -10.24) * mm, v(72.64, -10.53) * mm, v(72.36, -10.55) * mm]});
            skFitSpline(sketch, "E2042", {"points": [v(72.36, -10.55) * mm, v(72.14, -10.57) * mm, v(71.91, -10.59) * mm, v(71.73, -10.4) * mm]});
            skFitSpline(sketch, "E2043", {"points": [v(71.73, -10.4) * mm, v(71.7, -10.38) * mm, v(71.66, -10.37) * mm, v(71.63, -10.35) * mm]});
            skFitSpline(sketch, "E2044", {"points": [v(71.63, -10.35) * mm, v(70.99, -10.08) * mm, v(70.35, -9.81) * mm, v(69.7, -9.54) * mm]});
            skFitSpline(sketch, "E2045", {"points": [v(69.7, -9.54) * mm, v(69.68, -9.53) * mm, v(69.65, -9.52) * mm, v(69.58, -9.5) * mm]});
            skFitSpline(sketch, "E2046", {"points": [v(69.58, -9.5) * mm, v(69.61, -9.57) * mm, v(69.63, -9.61) * mm, v(69.65, -9.66) * mm]});
            skFitSpline(sketch, "E2047", {"points": [v(69.65, -9.66) * mm, v(69.72, -9.78) * mm, v(69.8, -9.9) * mm, v(69.85, -10.04) * mm]});
            skFitSpline(sketch, "E2048", {"points": [v(69.85, -10.04) * mm, v(69.94, -10.25) * mm, v(70.08, -10.38) * mm, v(70.3, -10.49) * mm]});
            skFitSpline(sketch, "E2049", {"points": [v(70.3, -10.49) * mm, v(71.09, -10.87) * mm, v(71.89, -11.2) * mm, v(72.71, -11.49) * mm]});
            skFitSpline(sketch, "E2050", {"points": [v(72.71, -11.49) * mm, v(72.94, -11.57) * mm, v(73.17, -11.68) * mm, v(73.4, -11.78) * mm]});
            skFitSpline(sketch, "E2051", {"points": [v(73.4, -11.78) * mm, v(73.62, -11.88) * mm, v(73.73, -12.1) * mm, v(73.67, -12.33) * mm]});
            skFitSpline(sketch, "E2052", {"points": [v(73.67, -12.33) * mm, v(73.61, -12.57) * mm, v(73.43, -12.72) * mm, v(73.16, -12.7) * mm]});
            skFitSpline(sketch, "E2053", {"points": [v(73.16, -12.7) * mm, v(73.05, -12.69) * mm, v(72.94, -12.65) * mm, v(72.84, -12.61) * mm]});
            skFitSpline(sketch, "E2054", {"points": [v(72.84, -12.61) * mm, v(72.6, -12.52) * mm, v(72.37, -12.4) * mm, v(72.13, -12.32) * mm]});
            skFitSpline(sketch, "E2055", {"points": [v(72.13, -12.32) * mm, v(71.8, -12.18) * mm, v(71.45, -12.05) * mm, v(71.1, -11.92) * mm]});
            skFitSpline(sketch, "E2056", {"points": [v(71.1, -11.92) * mm, v(71.03, -11.9) * mm, v(70.96, -11.87) * mm, v(70.83, -11.82) * mm]});
            skFitSpline(sketch, "E2057", {"points": [v(70.83, -11.82) * mm, v(70.95, -12.05) * mm, v(71.03, -12.22) * mm, v(71.13, -12.4) * mm]});
            skFitSpline(sketch, "E2058", {"points": [v(71.13, -12.4) * mm, v(71.22, -12.57) * mm, v(71.32, -12.74) * mm, v(71.42, -12.93) * mm]});
            skFitSpline(sketch, "E2059", {"points": [v(71.42, -12.93) * mm, v(71.46, -12.91) * mm, v(71.5, -12.9) * mm, v(71.54, -12.87) * mm]});
            skFitSpline(sketch, "E2060", {"points": [v(71.54, -12.87) * mm, v(71.7, -12.76) * mm, v(71.89, -12.78) * mm, v(72.07, -12.85) * mm]});
            skFitSpline(sketch, "E2061", {"points": [v(72.07, -12.85) * mm, v(72.53, -13) * mm, v(72.99, -13.17) * mm, v(73.45, -13.32) * mm]});
            skFitSpline(sketch, "E2062", {"points": [v(73.45, -13.32) * mm, v(73.6, -13.37) * mm, v(73.76, -13.4) * mm, v(73.91, -13.43) * mm]});
            skFitSpline(sketch, "E2063", {"points": [v(73.91, -13.43) * mm, v(74.04, -13.47) * mm, v(74.18, -13.5) * mm, v(74.3, -13.57) * mm]});
            skFitSpline(sketch, "E2064", {"points": [v(74.3, -13.57) * mm, v(74.61, -13.75) * mm, v(74.6, -14.23) * mm, v(74.3, -14.4) * mm]});
            skFitSpline(sketch, "E2065", {"points": [v(74.3, -14.4) * mm, v(74.09, -14.53) * mm, v(73.88, -14.57) * mm, v(73.66, -14.43) * mm]});
            skFitSpline(sketch, "E2066", {"points": [v(73.66, -14.43) * mm, v(73.57, -14.38) * mm, v(73.46, -14.35) * mm, v(73.35, -14.32) * mm]});
            skFitSpline(sketch, "E2067", {"points": [v(73.35, -14.32) * mm, v(72.93, -14.17) * mm, v(72.5, -14.03) * mm, v(72.08, -13.89) * mm]});
            skFitSpline(sketch, "E2068", {"points": [v(72.08, -13.89) * mm, v(72.03, -13.87) * mm, v(71.98, -13.85) * mm, v(71.9, -13.83) * mm]});
            skFitSpline(sketch, "E2069", {"points": [v(-119.93, -7.18) * mm, v(-119.83, -7.19) * mm, v(-119.77, -7.2) * mm, v(-119.7, -7.2) * mm]});
            skFitSpline(sketch, "E2070", {"points": [v(-119.7, -7.2) * mm, v(-119.36, -7.21) * mm, v(-119, -7.21) * mm, v(-118.66, -7.23) * mm]});
            skFitSpline(sketch, "E2071", {"points": [v(-118.66, -7.23) * mm, v(-118.46, -7.25) * mm, v(-118.32, -7.2) * mm, v(-118.22, -7.02) * mm]});
            skFitSpline(sketch, "E2072", {"points": [v(-118.22, -7.02) * mm, v(-118.19, -6.97) * mm, v(-118.14, -6.93) * mm, v(-118.1, -6.88) * mm]});
            skFitSpline(sketch, "E2073", {"points": [v(-118.1, -6.88) * mm, v(-117.7, -6.46) * mm, v(-117.32, -6.03) * mm, v(-116.92, -5.62) * mm]});
            skFitSpline(sketch, "E2074", {"points": [v(-116.92, -5.62) * mm, v(-116.44, -5.11) * mm, v(-115.95, -4.62) * mm, v(-115.47, -4.12) * mm]});
            skFitSpline(sketch, "E2075", {"points": [v(-115.47, -4.12) * mm, v(-115.3, -3.94) * mm, v(-115.12, -3.76) * mm, v(-114.95, -3.58) * mm]});
            skFitSpline(sketch, "E2076", {"points": [v(-114.95, -3.58) * mm, v(-115.18, -3.65) * mm, v(-115.39, -3.74) * mm, v(-115.59, -3.85) * mm]});
            skFitSpline(sketch, "E2077", {"points": [v(-115.59, -3.85) * mm, v(-116.8, -4.54) * mm, v(-118.1, -5.06) * mm, v(-119.38, -5.64) * mm]});
            skFitSpline(sketch, "E2078", {"points": [v(-119.38, -5.64) * mm, v(-119.46, -5.68) * mm, v(-119.51, -5.72) * mm, v(-119.54, -5.82) * mm]});
            skFitSpline(sketch, "E2079", {"points": [v(-119.54, -5.82) * mm, v(-119.64, -6.18) * mm, v(-119.76, -6.54) * mm, v(-119.86, -6.9) * mm]});
            skFitSpline(sketch, "E2080", {"points": [v(-119.86, -6.9) * mm, v(-119.89, -6.98) * mm, v(-119.9, -7.06) * mm, v(-119.93, -7.18) * mm]});
            skFitSpline(sketch, "E2081", {"points": [v(-99.49, -0.53) * mm, v(-99.58, -0.45) * mm, v(-99.66, -0.39) * mm, v(-99.74, -0.33) * mm]});
            skFitSpline(sketch, "E2082", {"points": [v(-99.74, -0.33) * mm, v(-99.95, -0.17) * mm, v(-100.18, -0.02) * mm, v(-100.37, 0.15) * mm]});
            skFitSpline(sketch, "E2083", {"points": [v(-100.37, 0.15) * mm, v(-100.59, 0.35) * mm, v(-100.8, 0.46) * mm, v(-101.1, 0.31) * mm]});
            skFitSpline(sketch, "E2084", {"points": [v(-101.1, 0.31) * mm, v(-101.1, 0.3) * mm, v(-101.12, 0.3) * mm, v(-101.14, 0.3) * mm]});
            skFitSpline(sketch, "E2085", {"points": [v(-101.14, 0.3) * mm, v(-101.74, 0.19) * mm, v(-102.33, 0.07) * mm, v(-102.92, -0.04) * mm]});
            skFitSpline(sketch, "E2086", {"points": [v(-102.92, -0.04) * mm, v(-103.57, -0.16) * mm, v(-104.21, -0.27) * mm, v(-104.86, -0.38) * mm]});
            skFitSpline(sketch, "E2087", {"points": [v(-104.86, -0.38) * mm, v(-105.14, -0.43) * mm, v(-105.42, -0.48) * mm, v(-105.7, -0.52) * mm]});
            skFitSpline(sketch, "E2088", {"points": [v(-105.7, -0.52) * mm, v(-105.05, -0.65) * mm, v(-104.4, -0.74) * mm, v(-103.76, -0.85) * mm]});
            skFitSpline(sketch, "E2089", {"points": [v(-103.76, -0.85) * mm, v(-103.31, -0.93) * mm, v(-102.87, -1.03) * mm, v(-102.42, -1.12) * mm]});
            skFitSpline(sketch, "E2090", {"points": [v(-102.42, -1.12) * mm, v(-101.9, -1.23) * mm, v(-101.36, -1.34) * mm, v(-100.83, -1.46) * mm]});
            skFitSpline(sketch, "E2091", {"points": [v(-100.83, -1.46) * mm, v(-100.74, -1.48) * mm, v(-100.68, -1.46) * mm, v(-100.61, -1.4) * mm]});
            skFitSpline(sketch, "E2092", {"points": [v(-100.61, -1.4) * mm, v(-100.3, -1.17) * mm, v(-100, -0.94) * mm, v(-99.68, -0.7) * mm]});
            skFitSpline(sketch, "E2093", {"points": [v(-99.68, -0.7) * mm, v(-99.62, -0.65) * mm, v(-99.56, -0.6) * mm, v(-99.49, -0.53) * mm]});
            skFitSpline(sketch, "E2094", {"points": [v(-109.24, 4.38) * mm, v(-109.22, 4.37) * mm, v(-109.2, 4.37) * mm, v(-109.18, 4.36) * mm]});
            skFitSpline(sketch, "E2095", {"points": [v(-109.18, 4.36) * mm, v(-108.8, 5.1) * mm, v(-108.42, 5.85) * mm, v(-108.02, 6.58) * mm]});
            skFitSpline(sketch, "E2096", {"points": [v(-108.02, 6.58) * mm, v(-107.62, 7.32) * mm, v(-107.2, 8.04) * mm, v(-106.78, 8.77) * mm]});
            skFitSpline(sketch, "E2097", {"points": [v(-106.78, 8.77) * mm, v(-106.97, 9.24) * mm, v(-107.1, 9.73) * mm, v(-107.3, 10.22) * mm]});
            skFitSpline(sketch, "E2098", {"points": [v(-107.3, 10.22) * mm, v(-107.74, 9.91) * mm, v(-108.16, 9.63) * mm, v(-108.57, 9.34) * mm]});
            skFitSpline(sketch, "E2099", {"points": [v(-108.57, 9.34) * mm, v(-108.76, 7.68) * mm, v(-108.9, 6.02) * mm, v(-109.24, 4.38) * mm]});
            skFitSpline(sketch, "E2100", {"points": [v(-119.92, 6.1) * mm, v(-119.91, 6.03) * mm, v(-119.91, 6) * mm, v(-119.9, 5.97) * mm]});
            skFitSpline(sketch, "E2101", {"points": [v(-119.9, 5.97) * mm, v(-119.78, 5.55) * mm, v(-119.66, 5.13) * mm, v(-119.52, 4.71) * mm]});
            skFitSpline(sketch, "E2102", {"points": [v(-119.52, 4.71) * mm, v(-119.5, 4.66) * mm, v(-119.44, 4.6) * mm, v(-119.38, 4.57) * mm]});
            skFitSpline(sketch, "E2103", {"points": [v(-119.38, 4.57) * mm, v(-118.95, 4.38) * mm, v(-118.5, 4.2) * mm, v(-118.07, 4) * mm]});
            skFitSpline(sketch, "E2104", {"points": [v(-118.07, 4) * mm, v(-117.16, 3.57) * mm, v(-116.25, 3.17) * mm, v(-115.38, 2.68) * mm]});
            skFitSpline(sketch, "E2105", {"points": [v(-115.38, 2.68) * mm, v(-115.26, 2.6) * mm, v(-115.13, 2.55) * mm, v(-115, 2.5) * mm]});
            skFitSpline(sketch, "E2106", {"points": [v(-115, 2.5) * mm, v(-115, 2.56) * mm, v(-115.03, 2.6) * mm, v(-115.06, 2.63) * mm]});
            skFitSpline(sketch, "E2107", {"points": [v(-115.06, 2.63) * mm, v(-115.27, 2.84) * mm, v(-115.5, 3.05) * mm, v(-115.7, 3.27) * mm]});
            skFitSpline(sketch, "E2108", {"points": [v(-115.7, 3.27) * mm, v(-116.28, 3.86) * mm, v(-116.84, 4.46) * mm, v(-117.4, 5.06) * mm]});
            skFitSpline(sketch, "E2109", {"points": [v(-117.4, 5.06) * mm, v(-117.71, 5.38) * mm, v(-118, 5.72) * mm, v(-118.3, 6.06) * mm]});
            skFitSpline(sketch, "E2110", {"points": [v(-118.3, 6.06) * mm, v(-118.36, 6.12) * mm, v(-118.41, 6.16) * mm, v(-118.5, 6.16) * mm]});
            skFitSpline(sketch, "E2111", {"points": [v(-118.5, 6.16) * mm, v(-118.92, 6.15) * mm, v(-119.33, 6.14) * mm, v(-119.75, 6.14) * mm]});
            skFitSpline(sketch, "E2112", {"points": [v(-119.75, 6.14) * mm, v(-119.8, 6.13) * mm, v(-119.85, 6.11) * mm, v(-119.92, 6.1) * mm]});
            skFitSpline(sketch, "E2113", {"points": [v(-109.18, -5.42) * mm, v(-109.2, -5.42) * mm, v(-109.2, -5.43) * mm, v(-109.22, -5.43) * mm]});
            skFitSpline(sketch, "E2114", {"points": [v(-109.22, -5.43) * mm, v(-109.2, -5.61) * mm, v(-109.17, -5.8) * mm, v(-109.14, -5.97) * mm]});
            skFitSpline(sketch, "E2115", {"points": [v(-109.14, -5.97) * mm, v(-109.06, -6.5) * mm, v(-108.95, -7) * mm, v(-108.89, -7.53) * mm]});
            skFitSpline(sketch, "E2116", {"points": [v(-108.89, -7.53) * mm, v(-108.78, -8.44) * mm, v(-108.7, -9.35) * mm, v(-108.6, -10.26) * mm]});
            skFitSpline(sketch, "E2117", {"points": [v(-108.6, -10.26) * mm, v(-108.59, -10.37) * mm, v(-108.55, -10.43) * mm, v(-108.46, -10.5) * mm]});
            skFitSpline(sketch, "E2118", {"points": [v(-108.46, -10.5) * mm, v(-108.15, -10.7) * mm, v(-107.84, -10.92) * mm, v(-107.53, -11.14) * mm]});
            skFitSpline(sketch, "E2119", {"points": [v(-107.53, -11.14) * mm, v(-107.46, -11.18) * mm, v(-107.39, -11.23) * mm, v(-107.3, -11.28) * mm]});
            skFitSpline(sketch, "E2120", {"points": [v(-107.3, -11.28) * mm, v(-107.27, -11.21) * mm, v(-107.24, -11.17) * mm, v(-107.22, -11.11) * mm]});
            skFitSpline(sketch, "E2121", {"points": [v(-107.22, -11.11) * mm, v(-107.08, -10.72) * mm, v(-106.95, -10.31) * mm, v(-106.8, -9.92) * mm]});
            skFitSpline(sketch, "E2122", {"points": [v(-106.8, -9.92) * mm, v(-106.77, -9.82) * mm, v(-106.81, -9.77) * mm, v(-106.85, -9.7) * mm]});
            skFitSpline(sketch, "E2123", {"points": [v(-106.85, -9.7) * mm, v(-107.1, -9.29) * mm, v(-107.34, -8.88) * mm, v(-107.57, -8.46) * mm]});
            skFitSpline(sketch, "E2124", {"points": [v(-107.57, -8.46) * mm, v(-108.05, -7.6) * mm, v(-108.56, -6.74) * mm, v(-108.96, -5.83) * mm]});
            skFitSpline(sketch, "E2125", {"points": [v(-108.96, -5.83) * mm, v(-109.03, -5.7) * mm, v(-109.1, -5.56) * mm, v(-109.18, -5.42) * mm]});
            skFitSpline(sketch, "E2126", {"points": [v(-114.5, 1.1) * mm, v(-114.88, 0.94) * mm, v(-115.24, 0.82) * mm, v(-115.57, 0.66) * mm]});
            skFitSpline(sketch, "E2127", {"points": [v(-115.57, 0.66) * mm, v(-116.25, 0.32) * mm, v(-116.92, -0.04) * mm, v(-117.59, -0.39) * mm]});
            skFitSpline(sketch, "E2128", {"points": [v(-117.59, -0.39) * mm, v(-117.66, -0.42) * mm, v(-117.71, -0.48) * mm, v(-117.8, -0.54) * mm]});
            skFitSpline(sketch, "E2129", {"points": [v(-117.8, -0.54) * mm, v(-117.66, -0.63) * mm, v(-117.56, -0.7) * mm, v(-117.45, -0.76) * mm]});
            skFitSpline(sketch, "E2130", {"points": [v(-117.45, -0.76) * mm, v(-117.04, -0.98) * mm, v(-116.63, -1.2) * mm, v(-116.22, -1.4) * mm]});
            skFitSpline(sketch, "E2131", {"points": [v(-116.22, -1.4) * mm, v(-115.99, -1.53) * mm, v(-115.75, -1.65) * mm, v(-115.51, -1.75) * mm]});
            skFitSpline(sketch, "E2132", {"points": [v(-115.51, -1.75) * mm, v(-115.18, -1.9) * mm, v(-114.85, -2.03) * mm, v(-114.5, -2.17) * mm]});
            skFitSpline(sketch, "E2133", {"points": [v(-114.5, -2.17) * mm, v(-114, -1.93) * mm, v(-112.02, -0.72) * mm, v(-111.83, -0.53) * mm]});
            skFitSpline(sketch, "E2134", {"points": [v(-111.83, -0.53) * mm, v(-112.05, -0.33) * mm, v(-114, 0.86) * mm, v(-114.5, 1.1) * mm]});
            skFitSpline(sketch, "E2135", {"points": [v(-111.07, -1.53) * mm, v(-111.09, -1.52) * mm, v(-111.11, -1.51) * mm, v(-111.13, -1.5) * mm]});
            skFitSpline(sketch, "E2136", {"points": [v(-111.13, -1.5) * mm, v(-111.94, -2.17) * mm, v(-112.75, -2.85) * mm, v(-113.5, -3.55) * mm]});
            skFitSpline(sketch, "E2137", {"points": [v(-113.5, -3.55) * mm, v(-113.47, -3.88) * mm, v(-113.46, -4.18) * mm, v(-113.43, -4.48) * mm]});
            skFitSpline(sketch, "E2138", {"points": [v(-113.43, -4.48) * mm, v(-113.4, -4.75) * mm, v(-113.38, -5.02) * mm, v(-113.34, -5.29) * mm]});
            skFitSpline(sketch, "E2139", {"points": [v(-113.34, -5.29) * mm, v(-113.28, -5.65) * mm, v(-113.22, -6.01) * mm, v(-113.15, -6.37) * mm]});
            skFitSpline(sketch, "E2140", {"points": [v(-113.15, -6.37) * mm, v(-113.1, -6.64) * mm, v(-113.03, -6.91) * mm, v(-112.97, -7.22) * mm]});
            skFitSpline(sketch, "E2141", {"points": [v(-112.97, -7.22) * mm, v(-112.84, -7.11) * mm, v(-112.74, -7.04) * mm, v(-112.65, -6.96) * mm]});
            skFitSpline(sketch, "E2142", {"points": [v(-112.65, -6.96) * mm, v(-112.35, -6.67) * mm, v(-112.05, -6.37) * mm, v(-111.74, -6.08) * mm]});
            skFitSpline(sketch, "E2143", {"points": [v(-111.74, -6.08) * mm, v(-111.6, -5.93) * mm, v(-111.44, -5.8) * mm, v(-111.3, -5.64) * mm]});
            skFitSpline(sketch, "E2144", {"points": [v(-111.3, -5.64) * mm, v(-111, -5.3) * mm, v(-110.7, -4.94) * mm, v(-110.36, -4.54) * mm]});
            skFitSpline(sketch, "E2145", {"points": [v(-110.36, -4.54) * mm, v(-110.59, -3.57) * mm, v(-110.83, -2.55) * mm, v(-111.07, -1.53) * mm]});
            skFitSpline(sketch, "E2146", {"points": [v(-106.84, -1.37) * mm, v(-107.32, -1.33) * mm, v(-107.85, -1.28) * mm, v(-108.38, -1.23) * mm]});
            skFitSpline(sketch, "E2147", {"points": [v(-108.38, -1.23) * mm, v(-108.9, -1.18) * mm, v(-109.43, -1.14) * mm, v(-110, -1.11) * mm]});
            skFitSpline(sketch, "E2148", {"points": [v(-110, -1.11) * mm, v(-109.58, -2.13) * mm, v(-109.17, -3.1) * mm, v(-108.78, -4.03) * mm]});
            skFitSpline(sketch, "E2149", {"points": [v(-108.78, -4.03) * mm, v(-107.56, -4.35) * mm, v(-106.37, -4.56) * mm, v(-105.12, -4.67) * mm]});
            skFitSpline(sketch, "E2150", {"points": [v(-105.12, -4.67) * mm, v(-105.16, -4.55) * mm, v(-105.17, -4.47) * mm, v(-105.2, -4.4) * mm]});
            skFitSpline(sketch, "E2151", {"points": [v(-105.2, -4.4) * mm, v(-105.49, -3.81) * mm, v(-105.76, -3.22) * mm, v(-106.07, -2.64) * mm]});
            skFitSpline(sketch, "E2152", {"points": [v(-106.07, -2.64) * mm, v(-106.3, -2.22) * mm, v(-106.56, -1.82) * mm, v(-106.84, -1.37) * mm]});
            skFitSpline(sketch, "E2153", {"points": [v(-106.8, 0.32) * mm, v(-106.7, 0.52) * mm, v(-106.61, 0.7) * mm, v(-106.5, 0.88) * mm]});
            skFitSpline(sketch, "E2154", {"points": [v(-106.5, 0.88) * mm, v(-106.24, 1.27) * mm, v(-106, 1.68) * mm, v(-105.8, 2.1) * mm]});
            skFitSpline(sketch, "E2155", {"points": [v(-105.8, 2.1) * mm, v(-105.63, 2.5) * mm, v(-105.43, 2.87) * mm, v(-105.24, 3.25) * mm]});
            skFitSpline(sketch, "E2156", {"points": [v(-105.24, 3.25) * mm, v(-105.2, 3.35) * mm, v(-105.17, 3.46) * mm, v(-105.12, 3.6) * mm]});
            skFitSpline(sketch, "E2157", {"points": [v(-105.12, 3.6) * mm, v(-105.25, 3.6) * mm, v(-105.34, 3.6) * mm, v(-105.42, 3.58) * mm]});
            skFitSpline(sketch, "E2158", {"points": [v(-105.42, 3.58) * mm, v(-105.72, 3.54) * mm, v(-106.02, 3.5) * mm, v(-106.32, 3.45) * mm]});
            skFitSpline(sketch, "E2159", {"points": [v(-106.32, 3.45) * mm, v(-106.73, 3.39) * mm, v(-107.14, 3.34) * mm, v(-107.55, 3.26) * mm]});
            skFitSpline(sketch, "E2160", {"points": [v(-107.55, 3.26) * mm, v(-107.95, 3.18) * mm, v(-108.34, 3.07) * mm, v(-108.75, 2.97) * mm]});
            skFitSpline(sketch, "E2161", {"points": [v(-108.75, 2.97) * mm, v(-109.02, 2.48) * mm, v(-109.91, 0.32) * mm, v(-109.94, 0.06) * mm]});
            skFitSpline(sketch, "E2162", {"points": [v(-109.94, 0.06) * mm, v(-109.63, 0.03) * mm, v(-108.1, 0.15) * mm, v(-106.8, 0.32) * mm]});
            skFitSpline(sketch, "E2163", {"points": [v(-112.96, 6.14) * mm, v(-113, 5.98) * mm, v(-113.04, 5.86) * mm, v(-113.06, 5.74) * mm]});
            skFitSpline(sketch, "E2164", {"points": [v(-113.06, 5.74) * mm, v(-113.12, 5.41) * mm, v(-113.18, 5.08) * mm, v(-113.24, 4.75) * mm]});
            skFitSpline(sketch, "E2165", {"points": [v(-113.24, 4.75) * mm, v(-113.3, 4.42) * mm, v(-113.36, 4.1) * mm, v(-113.4, 3.76) * mm]});
            skFitSpline(sketch, "E2166", {"points": [v(-113.4, 3.76) * mm, v(-113.44, 3.34) * mm, v(-113.46, 2.92) * mm, v(-113.5, 2.48) * mm]});
            skFitSpline(sketch, "E2167", {"points": [v(-113.5, 2.48) * mm, v(-112.75, 1.78) * mm, v(-111.94, 1.1) * mm, v(-111.1, 0.4) * mm]});
            skFitSpline(sketch, "E2168", {"points": [v(-111.1, 0.4) * mm, v(-110.82, 1.47) * mm, v(-110.56, 2.5) * mm, v(-110.37, 3.51) * mm]});
            skFitSpline(sketch, "E2169", {"points": [v(-110.37, 3.51) * mm, v(-110.8, 3.98) * mm, v(-111.18, 4.45) * mm, v(-111.6, 4.87) * mm]});
            skFitSpline(sketch, "E2170", {"points": [v(-111.6, 4.87) * mm, v(-112.04, 5.3) * mm, v(-112.44, 5.75) * mm, v(-112.96, 6.14) * mm]});
            skFitSpline(sketch, "E2171", {"points": [v(-105.4, -13.55) * mm, v(-105.12, -14) * mm, v(-104.81, -14.4) * mm, v(-104.45, -14.76) * mm]});
            skFitSpline(sketch, "E2172", {"points": [v(-104.45, -14.76) * mm, v(-104.31, -14.9) * mm, v(-104.2, -15.06) * mm, v(-104.1, -15.22) * mm]});
            skFitSpline(sketch, "E2173", {"points": [v(-104.1, -15.22) * mm, v(-103.99, -15.36) * mm, v(-103.97, -15.52) * mm, v(-104.02, -15.7) * mm]});
            skFitSpline(sketch, "E2174", {"points": [v(-104.02, -15.7) * mm, v(-104.2, -16.4) * mm, v(-104.38, -17.1) * mm, v(-104.57, -17.8) * mm]});
            skFitSpline(sketch, "E2175", {"points": [v(-104.57, -17.8) * mm, v(-104.73, -18.4) * mm, v(-105.16, -18.55) * mm, v(-105.65, -18.17) * mm]});
            skFitSpline(sketch, "E2176", {"points": [v(-105.65, -18.17) * mm, v(-105.93, -17.96) * mm, v(-106.2, -17.72) * mm, v(-106.46, -17.5) * mm]});
            skFitSpline(sketch, "E2177", {"points": [v(-106.46, -17.5) * mm, v(-106.74, -17.27) * mm, v(-107.02, -17.04) * mm, v(-107.3, -16.82) * mm]});
            skFitSpline(sketch, "E2178", {"points": [v(-107.3, -16.82) * mm, v(-107.5, -16.68) * mm, v(-107.6, -16.5) * mm, v(-107.58, -16.27) * mm]});
            skFitSpline(sketch, "E2179", {"points": [v(-107.58, -16.27) * mm, v(-107.56, -16.02) * mm, v(-107.54, -15.76) * mm, v(-107.51, -15.5) * mm]});
            skFitSpline(sketch, "E2180", {"points": [v(-107.51, -15.5) * mm, v(-107.5, -15.42) * mm, v(-107.5, -15.34) * mm, v(-107.49, -15.25) * mm]});
            skFitSpline(sketch, "E2181", {"points": [v(-107.49, -15.25) * mm, v(-107.47, -14.91) * mm, v(-107.46, -14.58) * mm, v(-107.44, -14.19) * mm]});
            skFitSpline(sketch, "E2182", {"points": [v(-107.44, -14.19) * mm, v(-107.5, -14.26) * mm, v(-107.52, -14.28) * mm, v(-107.53, -14.3) * mm]});
            skFitSpline(sketch, "E2183", {"points": [v(-107.53, -14.3) * mm, v(-107.8, -14.9) * mm, v(-108.06, -15.5) * mm, v(-108.34, -16.1) * mm]});
            skFitSpline(sketch, "E2184", {"points": [v(-108.34, -16.1) * mm, v(-108.47, -16.38) * mm, v(-108.63, -16.65) * mm, v(-108.8, -16.91) * mm]});
            skFitSpline(sketch, "E2185", {"points": [v(-108.8, -16.91) * mm, v(-108.93, -17.14) * mm, v(-109.2, -17.2) * mm, v(-109.43, -17.08) * mm]});
            skFitSpline(sketch, "E2186", {"points": [v(-109.43, -17.08) * mm, v(-109.66, -16.96) * mm, v(-109.75, -16.7) * mm, v(-109.64, -16.45) * mm]});
            skFitSpline(sketch, "E2187", {"points": [v(-109.64, -16.45) * mm, v(-109.63, -16.42) * mm, v(-109.62, -16.4) * mm, v(-109.6, -16.38) * mm]});
            skFitSpline(sketch, "E2188", {"points": [v(-109.6, -16.38) * mm, v(-109.03, -15.41) * mm, v(-108.63, -14.36) * mm, v(-108.19, -13.32) * mm]});
            skFitSpline(sketch, "E2189", {"points": [v(-108.19, -13.32) * mm, v(-108.05, -13) * mm, v(-107.9, -12.68) * mm, v(-107.75, -12.36) * mm]});
            skFitSpline(sketch, "E2190", {"points": [v(-107.75, -12.36) * mm, v(-107.72, -12.31) * mm, v(-107.7, -12.26) * mm, v(-107.69, -12.2) * mm]});
            skFitSpline(sketch, "E2191", {"points": [v(-107.69, -12.2) * mm, v(-108.05, -11.95) * mm, v(-108.41, -11.7) * mm, v(-108.78, -11.45) * mm]});
            skFitSpline(sketch, "E2192", {"points": [v(-108.78, -11.45) * mm, v(-108.83, -11.54) * mm, v(-108.86, -11.61) * mm, v(-108.9, -11.68) * mm]});
            skFitSpline(sketch, "E2193", {"points": [v(-108.9, -11.68) * mm, v(-109.37, -12.57) * mm, v(-109.83, -13.47) * mm, v(-110.32, -14.35) * mm]});
            skFitSpline(sketch, "E2194", {"points": [v(-110.32, -14.35) * mm, v(-110.57, -14.8) * mm, v(-110.88, -15.22) * mm, v(-111.17, -15.65) * mm]});
            skFitSpline(sketch, "E2195", {"points": [v(-111.17, -15.65) * mm, v(-111.21, -15.7) * mm, v(-111.26, -15.76) * mm, v(-111.32, -15.8) * mm]});
            skFitSpline(sketch, "E2196", {"points": [v(-111.32, -15.8) * mm, v(-111.53, -15.97) * mm, v(-111.82, -15.95) * mm, v(-112, -15.77) * mm]});
            skFitSpline(sketch, "E2197", {"points": [v(-112, -15.77) * mm, v(-112.17, -15.58) * mm, v(-112.18, -15.3) * mm, v(-112.02, -15.09) * mm]});
            skFitSpline(sketch, "E2198", {"points": [v(-112.02, -15.09) * mm, v(-111.65, -14.64) * mm, v(-111.32, -14.15) * mm, v(-111.04, -13.65) * mm]});
            skFitSpline(sketch, "E2199", {"points": [v(-111.04, -13.65) * mm, v(-110.66, -12.98) * mm, v(-110.3, -12.3) * mm, v(-109.95, -11.62) * mm]});
            skFitSpline(sketch, "E2200", {"points": [v(-109.95, -11.62) * mm, v(-109.82, -11.38) * mm, v(-109.71, -11.13) * mm, v(-109.6, -10.88) * mm]});
            skFitSpline(sketch, "E2201", {"points": [v(-109.6, -10.88) * mm, v(-109.57, -10.79) * mm, v(-109.55, -10.68) * mm, v(-109.55, -10.58) * mm]});
            skFitSpline(sketch, "E2202", {"points": [v(-109.55, -10.58) * mm, v(-109.55, -10.38) * mm, v(-109.57, -10.18) * mm, v(-109.6, -9.98) * mm]});
            skFitSpline(sketch, "E2203", {"points": [v(-109.6, -9.98) * mm, v(-109.66, -9.44) * mm, v(-109.72, -8.89) * mm, v(-109.79, -8.34) * mm]});
            skFitSpline(sketch, "E2204", {"points": [v(-109.79, -8.34) * mm, v(-109.8, -8.32) * mm, v(-109.8, -8.3) * mm, v(-109.82, -8.25) * mm]});
            skFitSpline(sketch, "E2205", {"points": [v(-109.82, -8.25) * mm, v(-109.92, -8.38) * mm, v(-110.01, -8.49) * mm, v(-110.1, -8.6) * mm]});
            skFitSpline(sketch, "E2206", {"points": [v(-110.1, -8.6) * mm, v(-110.47, -9.06) * mm, v(-110.84, -9.53) * mm, v(-111.2, -9.99) * mm]});
            skFitSpline(sketch, "E2207", {"points": [v(-111.2, -9.99) * mm, v(-111.25, -10.05) * mm, v(-111.3, -10.11) * mm, v(-111.37, -10.17) * mm]});
            skFitSpline(sketch, "E2208", {"points": [v(-111.37, -10.17) * mm, v(-111.57, -10.36) * mm, v(-111.86, -10.37) * mm, v(-112.06, -10.19) * mm]});
            skFitSpline(sketch, "E2209", {"points": [v(-112.06, -10.19) * mm, v(-112.24, -10.01) * mm, v(-112.28, -9.67) * mm, v(-112.1, -9.49) * mm]});
            skFitSpline(sketch, "E2210", {"points": [v(-112.1, -9.49) * mm, v(-111.5, -8.91) * mm, v(-111.07, -8.2) * mm, v(-110.53, -7.58) * mm]});
            skFitSpline(sketch, "E2211", {"points": [v(-110.53, -7.58) * mm, v(-110.35, -7.38) * mm, v(-110.17, -7.18) * mm, v(-109.96, -6.95) * mm]});
            skFitSpline(sketch, "E2212", {"points": [v(-109.96, -6.95) * mm, v(-110.02, -6.61) * mm, v(-110.08, -6.23) * mm, v(-110.16, -5.83) * mm]});
            skFitSpline(sketch, "E2213", {"points": [v(-110.16, -5.83) * mm, v(-110.2, -5.87) * mm, v(-110.23, -5.9) * mm, v(-110.25, -5.92) * mm]});
            skFitSpline(sketch, "E2214", {"points": [v(-110.25, -5.92) * mm, v(-110.52, -6.2) * mm, v(-110.78, -6.48) * mm, v(-111.05, -6.75) * mm]});
            skFitSpline(sketch, "E2215", {"points": [v(-111.05, -6.75) * mm, v(-111.34, -7.05) * mm, v(-111.65, -7.35) * mm, v(-111.95, -7.64) * mm]});
            skFitSpline(sketch, "E2216", {"points": [v(-111.95, -7.64) * mm, v(-112.15, -7.82) * mm, v(-112.35, -7.98) * mm, v(-112.56, -8.14) * mm]});
            skFitSpline(sketch, "E2217", {"points": [v(-112.56, -8.14) * mm, v(-112.76, -8.3) * mm, v(-112.97, -8.3) * mm, v(-113.19, -8.17) * mm]});
            skFitSpline(sketch, "E2218", {"points": [v(-113.19, -8.17) * mm, v(-113.24, -8.14) * mm, v(-113.3, -8.11) * mm, v(-113.36, -8.11) * mm]});
            skFitSpline(sketch, "E2219", {"points": [v(-113.36, -8.11) * mm, v(-113.6, -8.1) * mm, v(-113.74, -7.98) * mm, v(-113.81, -7.78) * mm]});
            skFitSpline(sketch, "E2220", {"points": [v(-113.81, -7.78) * mm, v(-113.9, -7.54) * mm, v(-113.97, -7.29) * mm, v(-114.01, -7.04) * mm]});
            skFitSpline(sketch, "E2221", {"points": [v(-114.01, -7.04) * mm, v(-114.1, -6.63) * mm, v(-114.16, -6.2) * mm, v(-114.22, -5.8) * mm]});
            skFitSpline(sketch, "E2222", {"points": [v(-114.22, -5.8) * mm, v(-114.3, -5.36) * mm, v(-114.36, -4.93) * mm, v(-114.43, -4.48) * mm]});
            skFitSpline(sketch, "E2223", {"points": [v(-114.43, -4.48) * mm, v(-114.59, -4.57) * mm, v(-114.7, -4.74) * mm, v(-114.84, -4.86) * mm]});
            skFitSpline(sketch, "E2224", {"points": [v(-114.84, -4.86) * mm, v(-114.98, -5) * mm, v(-115.12, -5.13) * mm, v(-115.23, -5.23) * mm]});
            skFitSpline(sketch, "E2225", {"points": [v(-115.23, -5.23) * mm, v(-115.2, -5.62) * mm, v(-115.15, -5.98) * mm, v(-115.13, -6.33) * mm]});
            skFitSpline(sketch, "E2226", {"points": [v(-115.13, -6.33) * mm, v(-115.1, -6.95) * mm, v(-115.09, -7.58) * mm, v(-115.06, -8.2) * mm]});
            skFitSpline(sketch, "E2227", {"points": [v(-115.06, -8.2) * mm, v(-115.06, -8.28) * mm, v(-115.03, -8.35) * mm, v(-115.01, -8.43) * mm]});
            skFitSpline(sketch, "E2228", {"points": [v(-115.01, -8.43) * mm, v(-114.94, -8.74) * mm, v(-115.13, -9.04) * mm, v(-115.44, -9.1) * mm]});
            skFitSpline(sketch, "E2229", {"points": [v(-115.44, -9.1) * mm, v(-115.7, -9.14) * mm, v(-115.97, -8.93) * mm, v(-115.99, -8.62) * mm]});
            skFitSpline(sketch, "E2230", {"points": [v(-115.99, -8.62) * mm, v(-116.03, -7.92) * mm, v(-116.05, -7.22) * mm, v(-116.09, -6.52) * mm]});
            skFitSpline(sketch, "E2231", {"points": [v(-116.09, -6.52) * mm, v(-116.1, -6.45) * mm, v(-116.1, -6.37) * mm, v(-116.1, -6.3) * mm]});
            skFitSpline(sketch, "E2232", {"points": [v(-116.1, -6.3) * mm, v(-116.1, -6.28) * mm, v(-116.12, -6.26) * mm, v(-116.1, -6.3) * mm]});
            skFitSpline(sketch, "E2233", {"points": [v(-116.1, -6.3) * mm, v(-116.3, -6.47) * mm, v(-116.53, -6.63) * mm, v(-116.73, -6.83) * mm]});
            skFitSpline(sketch, "E2234", {"points": [v(-116.73, -6.83) * mm, v(-117.05, -7.16) * mm, v(-117.34, -7.52) * mm, v(-117.65, -7.87) * mm]});
            skFitSpline(sketch, "E2235", {"points": [v(-117.65, -7.87) * mm, v(-117.75, -7.98) * mm, v(-117.82, -8.1) * mm, v(-117.84, -8.25) * mm]});
            skFitSpline(sketch, "E2236", {"points": [v(-117.84, -8.25) * mm, v(-117.94, -8.85) * mm, v(-118.04, -9.44) * mm, v(-118.13, -10.04) * mm]});
            skFitSpline(sketch, "E2237", {"points": [v(-118.13, -10.04) * mm, v(-118.2, -10.55) * mm, v(-118.28, -11.05) * mm, v(-118.33, -11.56) * mm]});
            skFitSpline(sketch, "E2238", {"points": [v(-118.33, -11.56) * mm, v(-118.37, -11.95) * mm, v(-118.37, -12.35) * mm, v(-118.39, -12.75) * mm]});
            skFitSpline(sketch, "E2239", {"points": [v(-118.39, -12.75) * mm, v(-118.4, -12.82) * mm, v(-118.38, -12.9) * mm, v(-118.36, -12.96) * mm]});
            skFitSpline(sketch, "E2240", {"points": [v(-118.36, -12.96) * mm, v(-118.3, -13.27) * mm, v(-118.52, -13.55) * mm, v(-118.82, -13.58) * mm]});
            skFitSpline(sketch, "E2241", {"points": [v(-118.82, -13.58) * mm, v(-119.1, -13.6) * mm, v(-119.35, -13.38) * mm, v(-119.35, -13.08) * mm]});
            skFitSpline(sketch, "E2242", {"points": [v(-119.35, -13.08) * mm, v(-119.34, -12.3) * mm, v(-119.33, -11.54) * mm, v(-119.21, -10.77) * mm]});
            skFitSpline(sketch, "E2243", {"points": [v(-119.21, -10.77) * mm, v(-119.1, -10.07) * mm, v(-119.01, -9.36) * mm, v(-118.91, -8.66) * mm]});
            skFitSpline(sketch, "E2244", {"points": [v(-118.91, -8.66) * mm, v(-118.9, -8.52) * mm, v(-118.86, -8.38) * mm, v(-118.83, -8.2) * mm]});
            skFitSpline(sketch, "E2245", {"points": [v(-118.83, -8.2) * mm, v(-119.26, -8.1) * mm, v(-119.7, -8.2) * mm, v(-120.16, -8.14) * mm]});
            skFitSpline(sketch, "E2246", {"points": [v(-120.16, -8.14) * mm, v(-120.19, -8.25) * mm, v(-120.2, -8.34) * mm, v(-120.22, -8.43) * mm]});
            skFitSpline(sketch, "E2247", {"points": [v(-120.22, -8.43) * mm, v(-120.37, -9.08) * mm, v(-120.51, -9.73) * mm, v(-120.66, -10.37) * mm]});
            skFitSpline(sketch, "E2248", {"points": [v(-120.66, -10.37) * mm, v(-120.77, -10.88) * mm, v(-120.88, -11.39) * mm, v(-120.97, -11.9) * mm]});
            skFitSpline(sketch, "E2249", {"points": [v(-120.97, -11.9) * mm, v(-121.02, -12.15) * mm, v(-121.03, -12.4) * mm, v(-121.06, -12.66) * mm]});
            skFitSpline(sketch, "E2250", {"points": [v(-121.06, -12.66) * mm, v(-121.1, -12.96) * mm, v(-121.33, -13.16) * mm, v(-121.6, -13.13) * mm]});
            skFitSpline(sketch, "E2251", {"points": [v(-121.6, -13.13) * mm, v(-121.88, -13.1) * mm, v(-122.06, -12.86) * mm, v(-122.03, -12.55) * mm]});
            skFitSpline(sketch, "E2252", {"points": [v(-122.03, -12.55) * mm, v(-121.98, -11.85) * mm, v(-121.82, -11.18) * mm, v(-121.67, -10.5) * mm]});
            skFitSpline(sketch, "E2253", {"points": [v(-121.67, -10.5) * mm, v(-121.61, -10.23) * mm, v(-121.56, -9.96) * mm, v(-121.54, -9.67) * mm]});
            skFitSpline(sketch, "E2254", {"points": [v(-121.54, -9.67) * mm, v(-121.6, -9.74) * mm, v(-121.65, -9.81) * mm, v(-121.7, -9.9) * mm]});
            skFitSpline(sketch, "E2255", {"points": [v(-121.7, -9.9) * mm, v(-121.92, -10.24) * mm, v(-122.13, -10.6) * mm, v(-122.35, -10.95) * mm]});
            skFitSpline(sketch, "E2256", {"points": [v(-122.35, -10.95) * mm, v(-122.46, -11.12) * mm, v(-122.58, -11.3) * mm, v(-122.7, -11.46) * mm]});
            skFitSpline(sketch, "E2257", {"points": [v(-122.7, -11.46) * mm, v(-122.8, -11.6) * mm, v(-122.95, -11.66) * mm, v(-123.12, -11.66) * mm]});
            skFitSpline(sketch, "E2258", {"points": [v(-123.12, -11.66) * mm, v(-123.53, -11.68) * mm, v(-123.93, -11.69) * mm, v(-124.34, -11.71) * mm]});
            skFitSpline(sketch, "E2259", {"points": [v(-124.34, -11.71) * mm, v(-124.61, -11.73) * mm, v(-124.88, -11.76) * mm, v(-125.15, -11.77) * mm]});
            skFitSpline(sketch, "E2260", {"points": [v(-125.15, -11.77) * mm, v(-125.32, -11.78) * mm, v(-125.5, -11.77) * mm, v(-125.67, -11.74) * mm]});
            skFitSpline(sketch, "E2261", {"points": [v(-125.67, -11.74) * mm, v(-125.92, -11.69) * mm, v(-126.08, -11.45) * mm, v(-126.05, -11.2) * mm]});
            skFitSpline(sketch, "E2262", {"points": [v(-126.05, -11.2) * mm, v(-126.03, -11.05) * mm, v(-125.99, -10.9) * mm, v(-125.93, -10.76) * mm]});
            skFitSpline(sketch, "E2263", {"points": [v(-125.93, -10.76) * mm, v(-125.7, -10.13) * mm, v(-125.44, -9.51) * mm, v(-125.2, -8.88) * mm]});
            skFitSpline(sketch, "E2264", {"points": [v(-125.2, -8.88) * mm, v(-125.12, -8.66) * mm, v(-125, -8.5) * mm, v(-124.77, -8.45) * mm]});
            skFitSpline(sketch, "E2265", {"points": [v(-124.77, -8.45) * mm, v(-124.54, -8.39) * mm, v(-124.32, -8.35) * mm, v(-124.1, -8.29) * mm]});
            skFitSpline(sketch, "E2266", {"points": [v(-124.1, -8.29) * mm, v(-123.66, -8.18) * mm, v(-123.23, -8.07) * mm, v(-122.8, -7.96) * mm]});
            skFitSpline(sketch, "E2267", {"points": [v(-122.8, -7.96) * mm, v(-122.8, -7.94) * mm, v(-122.8, -7.93) * mm, v(-122.8, -7.91) * mm]});
            skFitSpline(sketch, "E2268", {"points": [v(-122.8, -7.91) * mm, v(-122.87, -7.9) * mm, v(-122.94, -7.88) * mm, v(-123, -7.87) * mm]});
            skFitSpline(sketch, "E2269", {"points": [v(-123, -7.87) * mm, v(-123.56, -7.81) * mm, v(-124.11, -7.76) * mm, v(-124.67, -7.69) * mm]});
            skFitSpline(sketch, "E2270", {"points": [v(-124.67, -7.69) * mm, v(-125, -7.64) * mm, v(-125.34, -7.58) * mm, v(-125.68, -7.52) * mm]});
            skFitSpline(sketch, "E2271", {"points": [v(-125.68, -7.52) * mm, v(-125.88, -7.48) * mm, v(-126.04, -7.37) * mm, v(-126.1, -7.16) * mm]});
            skFitSpline(sketch, "E2272", {"points": [v(-126.1, -7.16) * mm, v(-126.14, -6.99) * mm, v(-126.1, -6.83) * mm, v(-125.98, -6.7) * mm]});
            skFitSpline(sketch, "E2273", {"points": [v(-125.98, -6.7) * mm, v(-125.9, -6.61) * mm, v(-125.8, -6.55) * mm, v(-125.69, -6.56) * mm]});
            skFitSpline(sketch, "E2274", {"points": [v(-125.69, -6.56) * mm, v(-125.57, -6.57) * mm, v(-125.44, -6.56) * mm, v(-125.33, -6.59) * mm]});
            skFitSpline(sketch, "E2275", {"points": [v(-125.33, -6.59) * mm, v(-124.8, -6.73) * mm, v(-124.25, -6.77) * mm, v(-123.7, -6.82) * mm]});
            skFitSpline(sketch, "E2276", {"points": [v(-123.7, -6.82) * mm, v(-123.39, -6.84) * mm, v(-123.08, -6.89) * mm, v(-122.77, -6.92) * mm]});
            skFitSpline(sketch, "E2277", {"points": [v(-122.77, -6.92) * mm, v(-122.5, -6.94) * mm, v(-122.25, -6.96) * mm, v(-121.99, -6.99) * mm]});
            skFitSpline(sketch, "E2278", {"points": [v(-121.99, -6.99) * mm, v(-121.68, -7.02) * mm, v(-121.37, -7.06) * mm, v(-121.06, -7.1) * mm]});
            skFitSpline(sketch, "E2279", {"points": [v(-121.06, -7.1) * mm, v(-121.02, -7.1) * mm, v(-120.98, -7.1) * mm, v(-120.93, -7.1) * mm]});
            skFitSpline(sketch, "E2280", {"points": [v(-120.93, -7.1) * mm, v(-120.8, -6.67) * mm, v(-120.68, -6.25) * mm, v(-120.55, -5.82) * mm]});
            skFitSpline(sketch, "E2281", {"points": [v(-120.55, -5.82) * mm, v(-120.9, -5.76) * mm, v(-121.25, -5.72) * mm, v(-121.6, -5.66) * mm]});
            skFitSpline(sketch, "E2282", {"points": [v(-121.6, -5.66) * mm, v(-122.5, -5.5) * mm, v(-123.4, -5.38) * mm, v(-124.27, -5.13) * mm]});
            skFitSpline(sketch, "E2283", {"points": [v(-124.27, -5.13) * mm, v(-124.6, -5.04) * mm, v(-124.93, -4.94) * mm, v(-125.26, -4.84) * mm]});
            skFitSpline(sketch, "E2284", {"points": [v(-125.26, -4.84) * mm, v(-125.35, -4.82) * mm, v(-125.44, -4.78) * mm, v(-125.52, -4.72) * mm]});
            skFitSpline(sketch, "E2285", {"points": [v(-125.52, -4.72) * mm, v(-125.72, -4.56) * mm, v(-125.77, -4.3) * mm, v(-125.64, -4.07) * mm]});
            skFitSpline(sketch, "E2286", {"points": [v(-125.64, -4.07) * mm, v(-125.5, -3.86) * mm, v(-125.24, -3.78) * mm, v(-125, -3.87) * mm]});
            skFitSpline(sketch, "E2287", {"points": [v(-125, -3.87) * mm, v(-124.39, -4.1) * mm, v(-123.75, -4.28) * mm, v(-123.1, -4.4) * mm]});
            skFitSpline(sketch, "E2288", {"points": [v(-123.1, -4.4) * mm, v(-122.41, -4.53) * mm, v(-121.72, -4.65) * mm, v(-121.03, -4.76) * mm]});
            skFitSpline(sketch, "E2289", {"points": [v(-121.03, -4.76) * mm, v(-120.75, -4.81) * mm, v(-120.47, -4.84) * mm, v(-120.2, -4.87) * mm]});
            skFitSpline(sketch, "E2290", {"points": [v(-120.2, -4.87) * mm, v(-120.14, -4.88) * mm, v(-120.07, -4.86) * mm, v(-120.01, -4.84) * mm]});
            skFitSpline(sketch, "E2291", {"points": [v(-120.01, -4.84) * mm, v(-119.9, -4.8) * mm, v(-119.77, -4.75) * mm, v(-119.66, -4.7) * mm]});
            skFitSpline(sketch, "E2292", {"points": [v(-119.66, -4.7) * mm, v(-119.05, -4.43) * mm, v(-118.45, -4.15) * mm, v(-117.8, -3.85) * mm]});
            skFitSpline(sketch, "E2293", {"points": [v(-117.8, -3.85) * mm, v(-118.01, -3.77) * mm, v(-118.18, -3.71) * mm, v(-118.35, -3.65) * mm]});
            skFitSpline(sketch, "E2294", {"points": [v(-118.35, -3.65) * mm, v(-118.92, -3.43) * mm, v(-119.5, -3.21) * mm, v(-120.07, -2.99) * mm]});
            skFitSpline(sketch, "E2295", {"points": [v(-120.07, -2.99) * mm, v(-120.24, -2.92) * mm, v(-120.37, -2.8) * mm, v(-120.4, -2.6) * mm]});
            skFitSpline(sketch, "E2296", {"points": [v(-120.4, -2.6) * mm, v(-120.43, -2.4) * mm, v(-120.37, -2.24) * mm, v(-120.2, -2.12) * mm]});
            skFitSpline(sketch, "E2297", {"points": [v(-120.2, -2.12) * mm, v(-120.03, -2) * mm, v(-119.85, -1.98) * mm, v(-119.66, -2.08) * mm]});
            skFitSpline(sketch, "E2298", {"points": [v(-119.66, -2.08) * mm, v(-119.14, -2.37) * mm, v(-118.57, -2.53) * mm, v(-118.01, -2.73) * mm]});
            skFitSpline(sketch, "E2299", {"points": [v(-118.01, -2.73) * mm, v(-117.56, -2.9) * mm, v(-117.1, -3.08) * mm, v(-116.65, -3.32) * mm]});
            skFitSpline(sketch, "E2300", {"points": [v(-116.65, -3.32) * mm, v(-116.33, -3.15) * mm, v(-116, -2.97) * mm, v(-115.66, -2.79) * mm]});
            skFitSpline(sketch, "E2301", {"points": [v(-115.66, -2.79) * mm, v(-115.65, -2.77) * mm, v(-115.64, -2.76) * mm, v(-115.63, -2.74) * mm]});
            skFitSpline(sketch, "E2302", {"points": [v(-115.63, -2.74) * mm, v(-115.65, -2.74) * mm, v(-115.68, -2.74) * mm, v(-115.7, -2.73) * mm]});
            skFitSpline(sketch, "E2303", {"points": [v(-115.7, -2.73) * mm, v(-116.5, -2.42) * mm, v(-117.24, -1.96) * mm, v(-118, -1.57) * mm]});
            skFitSpline(sketch, "E2304", {"points": [v(-118, -1.57) * mm, v(-118.21, -1.47) * mm, v(-118.4, -1.32) * mm, v(-118.59, -1.19) * mm]});
            skFitSpline(sketch, "E2305", {"points": [v(-118.59, -1.19) * mm, v(-118.78, -1.05) * mm, v(-118.86, -0.86) * mm, v(-118.8, -0.62) * mm]});
            skFitSpline(sketch, "E2306", {"points": [v(-118.8, -0.62) * mm, v(-118.78, -0.56) * mm, v(-118.78, -0.5) * mm, v(-118.8, -0.44) * mm]});
            skFitSpline(sketch, "E2307", {"points": [v(-118.8, -0.44) * mm, v(-118.86, -0.2) * mm, v(-118.78, -0.02) * mm, v(-118.6, 0.1) * mm]});
            skFitSpline(sketch, "E2308", {"points": [v(-118.6, 0.1) * mm, v(-118.4, 0.25) * mm, v(-118.21, 0.4) * mm, v(-118, 0.5) * mm]});
            skFitSpline(sketch, "E2309", {"points": [v(-118, 0.5) * mm, v(-117.24, 0.89) * mm, v(-116.52, 1.36) * mm, v(-115.71, 1.65) * mm]});
            skFitSpline(sketch, "E2310", {"points": [v(-115.71, 1.65) * mm, v(-115.69, 1.66) * mm, v(-115.67, 1.68) * mm, v(-115.64, 1.7) * mm]});
            skFitSpline(sketch, "E2311", {"points": [v(-115.64, 1.7) * mm, v(-115.99, 1.9) * mm, v(-116.32, 2.07) * mm, v(-116.65, 2.25) * mm]});
            skFitSpline(sketch, "E2312", {"points": [v(-116.65, 2.25) * mm, v(-117.06, 2.02) * mm, v(-117.5, 1.85) * mm, v(-117.93, 1.7) * mm]});
            skFitSpline(sketch, "E2313", {"points": [v(-117.93, 1.7) * mm, v(-118.4, 1.52) * mm, v(-118.87, 1.34) * mm, v(-119.34, 1.17) * mm]});
            skFitSpline(sketch, "E2314", {"points": [v(-119.34, 1.17) * mm, v(-119.44, 1.13) * mm, v(-119.53, 1.08) * mm, v(-119.62, 1.03) * mm]});
            skFitSpline(sketch, "E2315", {"points": [v(-119.62, 1.03) * mm, v(-119.9, 0.88) * mm, v(-120.21, 0.97) * mm, v(-120.35, 1.22) * mm]});
            skFitSpline(sketch, "E2316", {"points": [v(-120.35, 1.22) * mm, v(-120.5, 1.48) * mm, v(-120.39, 1.79) * mm, v(-120.09, 1.91) * mm]});
            skFitSpline(sketch, "E2317", {"points": [v(-120.09, 1.91) * mm, v(-119.5, 2.15) * mm, v(-118.9, 2.37) * mm, v(-118.3, 2.6) * mm]});
            skFitSpline(sketch, "E2318", {"points": [v(-118.3, 2.6) * mm, v(-118.15, 2.65) * mm, v(-118, 2.7) * mm, v(-117.82, 2.78) * mm]});
            skFitSpline(sketch, "E2319", {"points": [v(-117.82, 2.78) * mm, v(-118.06, 2.9) * mm, v(-118.25, 3) * mm, v(-118.46, 3.1) * mm]});
            skFitSpline(sketch, "E2320", {"points": [v(-118.46, 3.1) * mm, v(-118.94, 3.31) * mm, v(-119.42, 3.52) * mm, v(-119.9, 3.73) * mm]});
            skFitSpline(sketch, "E2321", {"points": [v(-119.9, 3.73) * mm, v(-120.04, 3.8) * mm, v(-120.17, 3.8) * mm, v(-120.32, 3.79) * mm]});
            skFitSpline(sketch, "E2322", {"points": [v(-120.32, 3.79) * mm, v(-121.02, 3.68) * mm, v(-121.73, 3.59) * mm, v(-122.43, 3.46) * mm]});
            skFitSpline(sketch, "E2323", {"points": [v(-122.43, 3.46) * mm, v(-123.06, 3.34) * mm, v(-123.7, 3.25) * mm, v(-124.31, 3.02) * mm]});
            skFitSpline(sketch, "E2324", {"points": [v(-124.31, 3.02) * mm, v(-124.55, 2.94) * mm, v(-124.8, 2.87) * mm, v(-125.04, 2.79) * mm]});
            skFitSpline(sketch, "E2325", {"points": [v(-125.04, 2.79) * mm, v(-125.25, 2.71) * mm, v(-125.5, 2.8) * mm, v(-125.62, 2.99) * mm]});
            skFitSpline(sketch, "E2326", {"points": [v(-125.62, 2.99) * mm, v(-125.75, 3.18) * mm, v(-125.75, 3.42) * mm, v(-125.58, 3.58) * mm]});
            skFitSpline(sketch, "E2327", {"points": [v(-125.58, 3.58) * mm, v(-125.5, 3.67) * mm, v(-125.38, 3.74) * mm, v(-125.26, 3.78) * mm]});
            skFitSpline(sketch, "E2328", {"points": [v(-125.26, 3.78) * mm, v(-124.28, 4.07) * mm, v(-123.3, 4.32) * mm, v(-122.28, 4.47) * mm]});
            skFitSpline(sketch, "E2329", {"points": [v(-122.28, 4.47) * mm, v(-121.86, 4.53) * mm, v(-121.44, 4.6) * mm, v(-121.03, 4.68) * mm]});
            skFitSpline(sketch, "E2330", {"points": [v(-121.03, 4.68) * mm, v(-120.88, 4.7) * mm, v(-120.73, 4.71) * mm, v(-120.55, 4.74) * mm]});
            skFitSpline(sketch, "E2331", {"points": [v(-120.55, 4.74) * mm, v(-120.68, 5.17) * mm, v(-120.8, 5.6) * mm, v(-120.93, 6.03) * mm]});
            skFitSpline(sketch, "E2332", {"points": [v(-120.93, 6.03) * mm, v(-121.17, 6) * mm, v(-121.4, 5.97) * mm, v(-121.64, 5.95) * mm]});
            skFitSpline(sketch, "E2333", {"points": [v(-121.64, 5.95) * mm, v(-122.03, 5.91) * mm, v(-122.4, 5.89) * mm, v(-122.79, 5.85) * mm]});
            skFitSpline(sketch, "E2334", {"points": [v(-122.79, 5.85) * mm, v(-123.3, 5.8) * mm, v(-123.82, 5.72) * mm, v(-124.33, 5.69) * mm]});
            skFitSpline(sketch, "E2335", {"points": [v(-124.33, 5.69) * mm, v(-124.73, 5.66) * mm, v(-125.1, 5.56) * mm, v(-125.49, 5.48) * mm]});
            skFitSpline(sketch, "E2336", {"points": [v(-125.49, 5.48) * mm, v(-125.79, 5.42) * mm, v(-126.06, 5.6) * mm, v(-126.1, 5.87) * mm]});
            skFitSpline(sketch, "E2337", {"points": [v(-126.1, 5.87) * mm, v(-126.16, 6.15) * mm, v(-125.99, 6.37) * mm, v(-125.67, 6.44) * mm]});
            skFitSpline(sketch, "E2338", {"points": [v(-125.67, 6.44) * mm, v(-125.04, 6.6) * mm, v(-124.4, 6.66) * mm, v(-123.75, 6.72) * mm]});
            skFitSpline(sketch, "E2339", {"points": [v(-123.75, 6.72) * mm, v(-123.44, 6.75) * mm, v(-123.12, 6.8) * mm, v(-122.77, 6.83) * mm]});
            skFitSpline(sketch, "E2340", {"points": [v(-122.77, 6.83) * mm, v(-122.84, 6.87) * mm, v(-122.88, 6.9) * mm, v(-122.92, 6.9) * mm]});
            skFitSpline(sketch, "E2341", {"points": [v(-122.92, 6.9) * mm, v(-123.38, 7.06) * mm, v(-123.85, 7.19) * mm, v(-124.34, 7.26) * mm]});
            skFitSpline(sketch, "E2342", {"points": [v(-124.34, 7.26) * mm, v(-124.52, 7.28) * mm, v(-124.7, 7.35) * mm, v(-124.86, 7.42) * mm]});
            skFitSpline(sketch, "E2343", {"points": [v(-124.86, 7.42) * mm, v(-125.03, 7.48) * mm, v(-125.13, 7.61) * mm, v(-125.2, 7.78) * mm]});
            skFitSpline(sketch, "E2344", {"points": [v(-125.2, 7.78) * mm, v(-125.45, 8.43) * mm, v(-125.7, 9.08) * mm, v(-125.96, 9.74) * mm]});
            skFitSpline(sketch, "E2345", {"points": [v(-125.96, 9.74) * mm, v(-126, 9.84) * mm, v(-126.02, 9.95) * mm, v(-126.04, 10.06) * mm]});
            skFitSpline(sketch, "E2346", {"points": [v(-126.04, 10.06) * mm, v(-126.1, 10.38) * mm, v(-125.92, 10.65) * mm, v(-125.6, 10.69) * mm]});
            skFitSpline(sketch, "E2347", {"points": [v(-125.6, 10.69) * mm, v(-125.38, 10.72) * mm, v(-125.16, 10.7) * mm, v(-124.95, 10.7) * mm]});
            skFitSpline(sketch, "E2348", {"points": [v(-124.95, 10.7) * mm, v(-124.4, 10.67) * mm, v(-123.84, 10.62) * mm, v(-123.28, 10.6) * mm]});
            skFitSpline(sketch, "E2349", {"points": [v(-123.28, 10.6) * mm, v(-122.98, 10.6) * mm, v(-122.75, 10.51) * mm, v(-122.6, 10.25) * mm]});
            skFitSpline(sketch, "E2350", {"points": [v(-122.6, 10.25) * mm, v(-122.5, 10.08) * mm, v(-122.39, 9.91) * mm, v(-122.28, 9.74) * mm]});
            skFitSpline(sketch, "E2351", {"points": [v(-122.28, 9.74) * mm, v(-122.04, 9.36) * mm, v(-121.8, 8.97) * mm, v(-121.56, 8.59) * mm]});
            skFitSpline(sketch, "E2352", {"points": [v(-121.56, 8.59) * mm, v(-121.54, 8.6) * mm, v(-121.53, 8.6) * mm, v(-121.51, 8.61) * mm]});
            skFitSpline(sketch, "E2353", {"points": [v(-121.51, 8.61) * mm, v(-121.56, 8.87) * mm, v(-121.6, 9.13) * mm, v(-121.66, 9.39) * mm]});
            skFitSpline(sketch, "E2354", {"points": [v(-121.66, 9.39) * mm, v(-121.74, 9.78) * mm, v(-121.84, 10.16) * mm, v(-121.91, 10.56) * mm]});
            skFitSpline(sketch, "E2355", {"points": [v(-121.91, 10.56) * mm, v(-121.97, 10.89) * mm, v(-122, 11.22) * mm, v(-122.03, 11.55) * mm]});
            skFitSpline(sketch, "E2356", {"points": [v(-122.03, 11.55) * mm, v(-122.05, 11.81) * mm, v(-121.86, 12.03) * mm, v(-121.61, 12.05) * mm]});
            skFitSpline(sketch, "E2357", {"points": [v(-121.61, 12.05) * mm, v(-121.35, 12.08) * mm, v(-121.12, 11.92) * mm, v(-121.07, 11.65) * mm]});
            skFitSpline(sketch, "E2358", {"points": [v(-121.07, 11.65) * mm, v(-121.06, 11.6) * mm, v(-121.05, 11.53) * mm, v(-121.05, 11.46) * mm]});
            skFitSpline(sketch, "E2359", {"points": [v(-121.05, 11.46) * mm, v(-121.01, 10.81) * mm, v(-120.84, 10.2) * mm, v(-120.7, 9.56) * mm]});
            skFitSpline(sketch, "E2360", {"points": [v(-120.7, 9.56) * mm, v(-120.57, 8.92) * mm, v(-120.41, 8.28) * mm, v(-120.27, 7.64) * mm]});
            skFitSpline(sketch, "E2361", {"points": [v(-120.27, 7.64) * mm, v(-120.23, 7.46) * mm, v(-120.2, 7.27) * mm, v(-120.17, 7.1) * mm]});
            skLineSegment(sketch, "E2362", {"start": v(-120.17, 7.1) * mm, "end": v(-118.83, 7.1) * mm});
            skFitSpline(sketch, "E2363", {"points": [v(-118.83, 7.1) * mm, v(-118.9, 7.54) * mm, v(-118.98, 7.93) * mm, v(-119.03, 8.34) * mm]});
            skFitSpline(sketch, "E2364", {"points": [v(-119.03, 8.34) * mm, v(-119.12, 9.11) * mm, v(-119.28, 9.88) * mm, v(-119.3, 10.66) * mm]});
            skFitSpline(sketch, "E2365", {"points": [v(-119.3, 10.66) * mm, v(-119.32, 11.1) * mm, v(-119.34, 11.52) * mm, v(-119.35, 11.95) * mm]});
            skFitSpline(sketch, "E2366", {"points": [v(-119.35, 11.95) * mm, v(-119.35, 12.03) * mm, v(-119.34, 12.12) * mm, v(-119.32, 12.19) * mm]});
            skFitSpline(sketch, "E2367", {"points": [v(-119.32, 12.19) * mm, v(-119.23, 12.42) * mm, v(-118.98, 12.55) * mm, v(-118.76, 12.5) * mm]});
            skFitSpline(sketch, "E2368", {"points": [v(-118.76, 12.5) * mm, v(-118.49, 12.43) * mm, v(-118.33, 12.19) * mm, v(-118.35, 11.93) * mm]});
            skFitSpline(sketch, "E2369", {"points": [v(-118.35, 11.93) * mm, v(-118.37, 11.74) * mm, v(-118.36, 11.55) * mm, v(-118.36, 11.36) * mm]});
            skFitSpline(sketch, "E2370", {"points": [v(-118.36, 11.36) * mm, v(-118.36, 11.07) * mm, v(-118.36, 10.79) * mm, v(-118.33, 10.5) * mm]});
            skFitSpline(sketch, "E2371", {"points": [v(-118.33, 10.5) * mm, v(-118.27, 9.96) * mm, v(-118.2, 9.41) * mm, v(-118.12, 8.87) * mm]});
            skFitSpline(sketch, "E2372", {"points": [v(-118.12, 8.87) * mm, v(-118.05, 8.38) * mm, v(-117.94, 7.9) * mm, v(-117.89, 7.4) * mm]});
            skFitSpline(sketch, "E2373", {"points": [v(-117.89, 7.4) * mm, v(-117.85, 7.03) * mm, v(-117.65, 6.77) * mm, v(-117.42, 6.51) * mm]});
            skFitSpline(sketch, "E2374", {"points": [v(-117.42, 6.51) * mm, v(-117.01, 6.07) * mm, v(-116.6, 5.63) * mm, v(-116.2, 5.2) * mm]});
            skFitSpline(sketch, "E2375", {"points": [v(-116.2, 5.2) * mm, v(-116.18, 5.19) * mm, v(-116.17, 5.18) * mm, v(-116.13, 5.16) * mm]});
            skFitSpline(sketch, "E2376", {"points": [v(-116.13, 5.16) * mm, v(-116.11, 5.22) * mm, v(-116.1, 5.28) * mm, v(-116.09, 5.33) * mm]});
            skFitSpline(sketch, "E2377", {"points": [v(-116.09, 5.33) * mm, v(-116.08, 5.65) * mm, v(-116.08, 5.97) * mm, v(-116.07, 6.3) * mm]});
            skFitSpline(sketch, "E2378", {"points": [v(-116.07, 6.3) * mm, v(-116.05, 6.71) * mm, v(-116.02, 7.14) * mm, v(-115.99, 7.56) * mm]});
            skFitSpline(sketch, "E2379", {"points": [v(-115.99, 7.56) * mm, v(-115.96, 7.87) * mm, v(-115.7, 8.07) * mm, v(-115.4, 8.02) * mm]});
            skFitSpline(sketch, "E2380", {"points": [v(-115.4, 8.02) * mm, v(-115.13, 7.96) * mm, v(-114.95, 7.66) * mm, v(-115, 7.38) * mm]});
            skFitSpline(sketch, "E2381", {"points": [v(-115, 7.38) * mm, v(-115.04, 7.24) * mm, v(-115.06, 7.1) * mm, v(-115.07, 6.95) * mm]});
            skFitSpline(sketch, "E2382", {"points": [v(-115.07, 6.95) * mm, v(-115.1, 6.41) * mm, v(-115.1, 5.87) * mm, v(-115.13, 5.33) * mm]});
            skFitSpline(sketch, "E2383", {"points": [v(-115.13, 5.33) * mm, v(-115.15, 4.96) * mm, v(-115.2, 4.58) * mm, v(-115.23, 4.16) * mm]});
            skFitSpline(sketch, "E2384", {"points": [v(-115.23, 4.16) * mm, v(-114.99, 3.93) * mm, v(-114.71, 3.66) * mm, v(-114.41, 3.37) * mm]});
            skFitSpline(sketch, "E2385", {"points": [v(-114.41, 3.37) * mm, v(-114.38, 3.7) * mm, v(-114.36, 4) * mm, v(-114.3, 4.28) * mm]});
            skFitSpline(sketch, "E2386", {"points": [v(-114.3, 4.28) * mm, v(-114.22, 4.86) * mm, v(-114.12, 5.44) * mm, v(-114, 6.02) * mm]});
            skFitSpline(sketch, "E2387", {"points": [v(-114, 6.02) * mm, v(-113.96, 6.25) * mm, v(-113.9, 6.47) * mm, v(-113.82, 6.7) * mm]});
            skFitSpline(sketch, "E2388", {"points": [v(-113.82, 6.7) * mm, v(-113.75, 6.9) * mm, v(-113.6, 7.03) * mm, v(-113.36, 7.05) * mm]});
            skFitSpline(sketch, "E2389", {"points": [v(-113.36, 7.05) * mm, v(-113.3, 7.06) * mm, v(-113.22, 7.08) * mm, v(-113.16, 7.12) * mm]});
            skFitSpline(sketch, "E2390", {"points": [v(-113.16, 7.12) * mm, v(-112.97, 7.23) * mm, v(-112.78, 7.23) * mm, v(-112.6, 7.1) * mm]});
            skFitSpline(sketch, "E2391", {"points": [v(-112.6, 7.1) * mm, v(-112.4, 6.95) * mm, v(-112.18, 6.8) * mm, v(-112, 6.62) * mm]});
            skFitSpline(sketch, "E2392", {"points": [v(-112, 6.62) * mm, v(-111.4, 6.02) * mm, v(-110.74, 5.46) * mm, v(-110.2, 4.8) * mm]});
            skFitSpline(sketch, "E2393", {"points": [v(-110.2, 4.8) * mm, v(-110.2, 4.8) * mm, v(-110.19, 4.8) * mm, v(-110.16, 4.78) * mm]});
            skFitSpline(sketch, "E2394", {"points": [v(-110.16, 4.78) * mm, v(-110.09, 5.15) * mm, v(-110.02, 5.52) * mm, v(-109.95, 5.9) * mm]});
            skFitSpline(sketch, "E2395", {"points": [v(-109.95, 5.9) * mm, v(-110.55, 6.44) * mm, v(-110.98, 7.11) * mm, v(-111.49, 7.73) * mm]});
            skFitSpline(sketch, "E2396", {"points": [v(-111.49, 7.73) * mm, v(-111.66, 7.95) * mm, v(-111.85, 8.15) * mm, v(-112.04, 8.35) * mm]});
            skFitSpline(sketch, "E2397", {"points": [v(-112.04, 8.35) * mm, v(-112.25, 8.57) * mm, v(-112.26, 8.91) * mm, v(-112.06, 9.11) * mm]});
            skFitSpline(sketch, "E2398", {"points": [v(-112.06, 9.11) * mm, v(-111.86, 9.32) * mm, v(-111.56, 9.3) * mm, v(-111.34, 9.07) * mm]});
            skFitSpline(sketch, "E2399", {"points": [v(-111.34, 9.07) * mm, v(-111.14, 8.85) * mm, v(-110.94, 8.61) * mm, v(-110.75, 8.38) * mm]});
            skFitSpline(sketch, "E2400", {"points": [v(-110.75, 8.38) * mm, v(-110.5, 8.07) * mm, v(-110.28, 7.76) * mm, v(-110.04, 7.45) * mm]});
            skFitSpline(sketch, "E2401", {"points": [v(-110.04, 7.45) * mm, v(-109.97, 7.36) * mm, v(-109.9, 7.29) * mm, v(-109.81, 7.18) * mm]});
            skFitSpline(sketch, "E2402", {"points": [v(-109.81, 7.18) * mm, v(-109.77, 7.43) * mm, v(-109.73, 7.64) * mm, v(-109.7, 7.86) * mm]});
            skFitSpline(sketch, "E2403", {"points": [v(-109.7, 7.86) * mm, v(-109.65, 8.37) * mm, v(-109.6, 8.87) * mm, v(-109.55, 9.38) * mm]});
            skFitSpline(sketch, "E2404", {"points": [v(-109.55, 9.38) * mm, v(-109.53, 9.56) * mm, v(-109.56, 9.73) * mm, v(-109.64, 9.9) * mm]});
            skFitSpline(sketch, "E2405", {"points": [v(-109.64, 9.9) * mm, v(-110.13, 10.83) * mm, v(-110.6, 11.77) * mm, v(-111.1, 12.7) * mm]});
            skFitSpline(sketch, "E2406", {"points": [v(-111.1, 12.7) * mm, v(-111.32, 13.09) * mm, v(-111.59, 13.45) * mm, v(-111.83, 13.82) * mm]});
            skFitSpline(sketch, "E2407", {"points": [v(-111.83, 13.82) * mm, v(-111.87, 13.88) * mm, v(-111.93, 13.93) * mm, v(-111.98, 13.98) * mm]});
            skFitSpline(sketch, "E2408", {"points": [v(-111.98, 13.98) * mm, v(-112.2, 14.21) * mm, v(-112.19, 14.53) * mm, v(-111.96, 14.73) * mm]});
            skFitSpline(sketch, "E2409", {"points": [v(-111.96, 14.73) * mm, v(-111.76, 14.9) * mm, v(-111.43, 14.88) * mm, v(-111.24, 14.66) * mm]});
            skFitSpline(sketch, "E2410", {"points": [v(-111.24, 14.66) * mm, v(-111.13, 14.53) * mm, v(-111.04, 14.38) * mm, v(-110.95, 14.25) * mm]});
            skFitSpline(sketch, "E2411", {"points": [v(-110.95, 14.25) * mm, v(-110.12, 13.05) * mm, v(-109.46, 11.76) * mm, v(-108.83, 10.46) * mm]});
            skFitSpline(sketch, "E2412", {"points": [v(-108.83, 10.46) * mm, v(-108.82, 10.44) * mm, v(-108.8, 10.43) * mm, v(-108.77, 10.39) * mm]});
            skFitSpline(sketch, "E2413", {"points": [v(-108.77, 10.39) * mm, v(-108.41, 10.64) * mm, v(-108.05, 10.89) * mm, v(-107.69, 11.14) * mm]});
            skFitSpline(sketch, "E2414", {"points": [v(-107.69, 11.14) * mm, v(-107.7, 11.17) * mm, v(-107.7, 11.2) * mm, v(-107.72, 11.23) * mm]});
            skFitSpline(sketch, "E2415", {"points": [v(-107.72, 11.23) * mm, v(-108.22, 12.36) * mm, v(-108.72, 13.5) * mm, v(-109.22, 14.63) * mm]});
            skFitSpline(sketch, "E2416", {"points": [v(-109.22, 14.63) * mm, v(-109.32, 14.85) * mm, v(-109.47, 15.06) * mm, v(-109.59, 15.27) * mm]});
            skFitSpline(sketch, "E2417", {"points": [v(-109.59, 15.27) * mm, v(-109.66, 15.4) * mm, v(-109.71, 15.52) * mm, v(-109.68, 15.66) * mm]});
            skFitSpline(sketch, "E2418", {"points": [v(-109.68, 15.66) * mm, v(-109.64, 15.87) * mm, v(-109.52, 16) * mm, v(-109.31, 16.06) * mm]});
            skFitSpline(sketch, "E2419", {"points": [v(-109.31, 16.06) * mm, v(-109.12, 16.11) * mm, v(-108.9, 16.03) * mm, v(-108.8, 15.85) * mm]});
            skFitSpline(sketch, "E2420", {"points": [v(-108.8, 15.85) * mm, v(-108.62, 15.55) * mm, v(-108.45, 15.25) * mm, v(-108.3, 14.94) * mm]});
            skFitSpline(sketch, "E2421", {"points": [v(-108.3, 14.94) * mm, v(-108.04, 14.38) * mm, v(-107.79, 13.8) * mm, v(-107.53, 13.24) * mm]});
            skFitSpline(sketch, "E2422", {"points": [v(-107.53, 13.24) * mm, v(-107.52, 13.21) * mm, v(-107.5, 13.2) * mm, v(-107.46, 13.14) * mm]});
            skFitSpline(sketch, "E2423", {"points": [v(-107.46, 13.14) * mm, v(-107.44, 13.68) * mm, v(-107.48, 14.17) * mm, v(-107.55, 14.67) * mm]});
            skFitSpline(sketch, "E2424", {"points": [v(-107.55, 14.67) * mm, v(-107.58, 14.9) * mm, v(-107.58, 15.12) * mm, v(-107.57, 15.34) * mm]});
            skFitSpline(sketch, "E2425", {"points": [v(-107.57, 15.34) * mm, v(-107.57, 15.5) * mm, v(-107.47, 15.62) * mm, v(-107.35, 15.72) * mm]});
            skFitSpline(sketch, "E2426", {"points": [v(-107.35, 15.72) * mm, v(-106.8, 16.18) * mm, v(-106.24, 16.63) * mm, v(-105.68, 17.09) * mm]});
            skFitSpline(sketch, "E2427", {"points": [v(-105.68, 17.09) * mm, v(-105.58, 17.16) * mm, v(-105.46, 17.23) * mm, v(-105.35, 17.27) * mm]});
            skFitSpline(sketch, "E2428", {"points": [v(-105.35, 17.27) * mm, v(-105.11, 17.37) * mm, v(-104.87, 17.3) * mm, v(-104.74, 17.09) * mm]});
            skFitSpline(sketch, "E2429", {"points": [v(-104.74, 17.09) * mm, v(-104.66, 16.97) * mm, v(-104.6, 16.83) * mm, v(-104.56, 16.7) * mm]});
            skFitSpline(sketch, "E2430", {"points": [v(-104.56, 16.7) * mm, v(-104.38, 16.03) * mm, v(-104.21, 15.35) * mm, v(-104.03, 14.68) * mm]});
            skFitSpline(sketch, "E2431", {"points": [v(-104.03, 14.68) * mm, v(-103.97, 14.46) * mm, v(-104, 14.26) * mm, v(-104.14, 14.07) * mm]});
            skFitSpline(sketch, "E2432", {"points": [v(-104.14, 14.07) * mm, v(-104.28, 13.9) * mm, v(-104.42, 13.73) * mm, v(-104.58, 13.56) * mm]});
            skFitSpline(sketch, "E2433", {"points": [v(-104.58, 13.56) * mm, v(-104.87, 13.25) * mm, v(-105.14, 12.91) * mm, v(-105.42, 12.52) * mm]});
            skFitSpline(sketch, "E2434", {"points": [v(-105.42, 12.52) * mm, v(-105.33, 12.54) * mm, v(-105.3, 12.55) * mm, v(-105.26, 12.57) * mm]});
            skFitSpline(sketch, "E2435", {"points": [v(-105.26, 12.57) * mm, v(-104.71, 12.88) * mm, v(-104.17, 13.2) * mm, v(-103.62, 13.5) * mm]});
            skFitSpline(sketch, "E2436", {"points": [v(-103.62, 13.5) * mm, v(-103.34, 13.65) * mm, v(-103.06, 13.78) * mm, v(-102.77, 13.9) * mm]});
            skFitSpline(sketch, "E2437", {"points": [v(-102.77, 13.9) * mm, v(-102.53, 14) * mm, v(-102.27, 13.88) * mm, v(-102.16, 13.65) * mm]});
            skFitSpline(sketch, "E2438", {"points": [v(-102.16, 13.65) * mm, v(-102.06, 13.43) * mm, v(-102.12, 13.18) * mm, v(-102.33, 13.04) * mm]});
            skFitSpline(sketch, "E2439", {"points": [v(-102.33, 13.04) * mm, v(-102.41, 12.98) * mm, v(-102.5, 12.94) * mm, v(-102.59, 12.9) * mm]});
            skFitSpline(sketch, "E2440", {"points": [v(-102.59, 12.9) * mm, v(-103.08, 12.71) * mm, v(-103.53, 12.43) * mm, v(-103.98, 12.17) * mm]});
            skFitSpline(sketch, "E2441", {"points": [v(-103.98, 12.17) * mm, v(-104.76, 11.71) * mm, v(-105.53, 11.27) * mm, v(-106.3, 10.82) * mm]});
            skFitSpline(sketch, "E2442", {"points": [v(-106.3, 10.82) * mm, v(-106.35, 10.8) * mm, v(-106.38, 10.77) * mm, v(-106.44, 10.74) * mm]});
            skFitSpline(sketch, "E2443", {"points": [v(-106.44, 10.74) * mm, v(-106.3, 10.32) * mm, v(-106.15, 9.9) * mm, v(-106, 9.48) * mm]});
            skFitSpline(sketch, "E2444", {"points": [v(-106, 9.48) * mm, v(-105.93, 9.51) * mm, v(-105.88, 9.54) * mm, v(-105.82, 9.56) * mm]});
            skFitSpline(sketch, "E2445", {"points": [v(-105.82, 9.56) * mm, v(-105.18, 9.89) * mm, v(-104.54, 10.21) * mm, v(-103.9, 10.53) * mm]});
            skFitSpline(sketch, "E2446", {"points": [v(-103.9, 10.53) * mm, v(-103.51, 10.71) * mm, v(-103.13, 10.88) * mm, v(-102.74, 11.05) * mm]});
            skFitSpline(sketch, "E2447", {"points": [v(-102.74, 11.05) * mm, v(-102.37, 11.2) * mm, v(-102, 11.32) * mm, v(-101.64, 11.45) * mm]});
            skFitSpline(sketch, "E2448", {"points": [v(-101.64, 11.45) * mm, v(-101.54, 11.49) * mm, v(-101.43, 11.5) * mm, v(-101.33, 11.5) * mm]});
            skFitSpline(sketch, "E2449", {"points": [v(-101.33, 11.5) * mm, v(-101.08, 11.5) * mm, v(-100.89, 11.31) * mm, v(-100.86, 11.08) * mm]});
            skFitSpline(sketch, "E2450", {"points": [v(-100.86, 11.08) * mm, v(-100.84, 10.8) * mm, v(-101, 10.58) * mm, v(-101.25, 10.52) * mm]});
            skFitSpline(sketch, "E2451", {"points": [v(-101.25, 10.52) * mm, v(-101.8, 10.39) * mm, v(-102.31, 10.19) * mm, v(-102.82, 9.96) * mm]});
            skFitSpline(sketch, "E2452", {"points": [v(-102.82, 9.96) * mm, v(-103.55, 9.62) * mm, v(-104.26, 9.27) * mm, v(-104.98, 8.91) * mm]});
            skFitSpline(sketch, "E2453", {"points": [v(-104.98, 8.91) * mm, v(-105.22, 8.8) * mm, v(-105.46, 8.65) * mm, v(-105.69, 8.51) * mm]});
            skFitSpline(sketch, "E2454", {"points": [v(-105.69, 8.51) * mm, v(-105.77, 8.46) * mm, v(-105.86, 8.38) * mm, v(-105.9, 8.3) * mm]});
            skFitSpline(sketch, "E2455", {"points": [v(-105.9, 8.3) * mm, v(-106.22, 7.76) * mm, v(-106.53, 7.22) * mm, v(-106.84, 6.68) * mm]});
            skFitSpline(sketch, "E2456", {"points": [v(-106.84, 6.68) * mm, v(-106.9, 6.56) * mm, v(-106.97, 6.44) * mm, v(-107.06, 6.28) * mm]});
            skFitSpline(sketch, "E2457", {"points": [v(-107.06, 6.28) * mm, v(-106.87, 6.32) * mm, v(-106.73, 6.36) * mm, v(-106.58, 6.4) * mm]});
            skFitSpline(sketch, "E2458", {"points": [v(-106.58, 6.4) * mm, v(-105.98, 6.57) * mm, v(-105.38, 6.74) * mm, v(-104.78, 6.89) * mm]});
            skFitSpline(sketch, "E2459", {"points": [v(-104.78, 6.89) * mm, v(-104.65, 6.92) * mm, v(-104.5, 6.92) * mm, v(-104.38, 6.88) * mm]});
            skFitSpline(sketch, "E2460", {"points": [v(-104.38, 6.88) * mm, v(-104.19, 6.83) * mm, v(-104.07, 6.61) * mm, v(-104.08, 6.41) * mm]});
            skFitSpline(sketch, "E2461", {"points": [v(-104.08, 6.41) * mm, v(-104.1, 6.2) * mm, v(-104.25, 6) * mm, v(-104.47, 5.94) * mm]});
            skFitSpline(sketch, "E2462", {"points": [v(-104.47, 5.94) * mm, v(-104.58, 5.91) * mm, v(-104.7, 5.91) * mm, v(-104.82, 5.88) * mm]});
            skFitSpline(sketch, "E2463", {"points": [v(-104.82, 5.88) * mm, v(-105.31, 5.75) * mm, v(-105.8, 5.6) * mm, v(-106.3, 5.47) * mm]});
            skFitSpline(sketch, "E2464", {"points": [v(-106.3, 5.47) * mm, v(-106.74, 5.35) * mm, v(-107.2, 5.25) * mm, v(-107.7, 5.13) * mm]});
            skFitSpline(sketch, "E2465", {"points": [v(-107.7, 5.13) * mm, v(-107.84, 4.84) * mm, v(-108, 4.5) * mm, v(-108.17, 4.16) * mm]});
            skFitSpline(sketch, "E2466", {"points": [v(-108.17, 4.16) * mm, v(-108.14, 4.15) * mm, v(-108.13, 4.13) * mm, v(-108.12, 4.13) * mm]});
            skFitSpline(sketch, "E2467", {"points": [v(-108.12, 4.13) * mm, v(-107.53, 4.3) * mm, v(-106.93, 4.33) * mm, v(-106.33, 4.43) * mm]});
            skFitSpline(sketch, "E2468", {"points": [v(-106.33, 4.43) * mm, v(-105.86, 4.51) * mm, v(-105.38, 4.57) * mm, v(-104.9, 4.57) * mm]});
            skFitSpline(sketch, "E2469", {"points": [v(-104.9, 4.57) * mm, v(-104.64, 4.58) * mm, v(-104.45, 4.48) * mm, v(-104.36, 4.23) * mm]});
            skFitSpline(sketch, "E2470", {"points": [v(-104.36, 4.23) * mm, v(-104.35, 4.19) * mm, v(-104.32, 4.14) * mm, v(-104.28, 4.12) * mm]});
            skFitSpline(sketch, "E2471", {"points": [v(-104.28, 4.12) * mm, v(-104.04, 3.94) * mm, v(-104.03, 3.7) * mm, v(-104.12, 3.45) * mm]});
            skFitSpline(sketch, "E2472", {"points": [v(-104.12, 3.45) * mm, v(-104.26, 3.08) * mm, v(-104.42, 2.71) * mm, v(-104.6, 2.35) * mm]});
            skFitSpline(sketch, "E2473", {"points": [v(-104.6, 2.35) * mm, v(-104.82, 1.87) * mm, v(-105.07, 1.4) * mm, v(-105.32, 0.92) * mm]});
            skFitSpline(sketch, "E2474", {"points": [v(-105.32, 0.92) * mm, v(-105.39, 0.79) * mm, v(-105.47, 0.66) * mm, v(-105.57, 0.5) * mm]});
            skFitSpline(sketch, "E2475", {"points": [v(-105.57, 0.5) * mm, v(-105.28, 0.54) * mm, v(-105.03, 0.58) * mm, v(-104.77, 0.6) * mm]});
            skFitSpline(sketch, "E2476", {"points": [v(-104.77, 0.6) * mm, v(-104.52, 0.61) * mm, v(-104.39, 0.72) * mm, v(-104.26, 0.95) * mm]});
            skFitSpline(sketch, "E2477", {"points": [v(-104.26, 0.95) * mm, v(-103.92, 1.54) * mm, v(-103.51, 2.1) * mm, v(-103.14, 2.68) * mm]});
            skFitSpline(sketch, "E2478", {"points": [v(-103.14, 2.68) * mm, v(-103, 2.92) * mm, v(-102.85, 3.16) * mm, v(-102.72, 3.4) * mm]});
            skFitSpline(sketch, "E2479", {"points": [v(-102.72, 3.4) * mm, v(-102.61, 3.61) * mm, v(-102.41, 3.73) * mm, v(-102.17, 3.7) * mm]});
            skFitSpline(sketch, "E2480", {"points": [v(-102.17, 3.7) * mm, v(-101.97, 3.68) * mm, v(-101.8, 3.54) * mm, v(-101.76, 3.33) * mm]});
            skFitSpline(sketch, "E2481", {"points": [v(-101.76, 3.33) * mm, v(-101.72, 3.18) * mm, v(-101.77, 3.04) * mm, v(-101.85, 2.92) * mm]});
            skFitSpline(sketch, "E2482", {"points": [v(-101.85, 2.92) * mm, v(-102.18, 2.4) * mm, v(-102.5, 1.9) * mm, v(-102.84, 1.4) * mm]});
            skFitSpline(sketch, "E2483", {"points": [v(-102.84, 1.4) * mm, v(-102.94, 1.25) * mm, v(-103.04, 1.1) * mm, v(-103.16, 0.92) * mm]});
            skFitSpline(sketch, "E2484", {"points": [v(-103.16, 0.92) * mm, v(-102.9, 0.96) * mm, v(-102.67, 0.98) * mm, v(-102.45, 1.03) * mm]});
            skFitSpline(sketch, "E2485", {"points": [v(-102.45, 1.03) * mm, v(-101.95, 1.13) * mm, v(-101.47, 1.25) * mm, v(-100.97, 1.35) * mm]});
            skFitSpline(sketch, "E2486", {"points": [v(-100.97, 1.35) * mm, v(-100.81, 1.39) * mm, v(-100.68, 1.45) * mm, v(-100.55, 1.56) * mm]});
            skFitSpline(sketch, "E2487", {"points": [v(-100.55, 1.56) * mm, v(-99.7, 2.35) * mm, v(-98.9, 3.2) * mm, v(-98.12, 4.07) * mm]});
            skFitSpline(sketch, "E2488", {"points": [v(-98.12, 4.07) * mm, v(-97.89, 4.33) * mm, v(-97.69, 4.6) * mm, v(-97.47, 4.88) * mm]});
            skFitSpline(sketch, "E2489", {"points": [v(-97.47, 4.88) * mm, v(-97.43, 4.94) * mm, v(-97.4, 5.01) * mm, v(-97.35, 5.08) * mm]});
            skFitSpline(sketch, "E2490", {"points": [v(-97.35, 5.08) * mm, v(-97.2, 5.35) * mm, v(-96.91, 5.44) * mm, v(-96.66, 5.31) * mm]});
            skFitSpline(sketch, "E2491", {"points": [v(-96.66, 5.31) * mm, v(-96.41, 5.18) * mm, v(-96.32, 4.87) * mm, v(-96.47, 4.6) * mm]});
            skFitSpline(sketch, "E2492", {"points": [v(-96.47, 4.6) * mm, v(-96.49, 4.56) * mm, v(-96.52, 4.52) * mm, v(-96.55, 4.49) * mm]});
            skFitSpline(sketch, "E2493", {"points": [v(-96.55, 4.49) * mm, v(-97.03, 3.88) * mm, v(-97.49, 3.25) * mm, v(-98.04, 2.7) * mm]});
            skFitSpline(sketch, "E2494", {"points": [v(-98.04, 2.7) * mm, v(-98.62, 2.12) * mm, v(-99.19, 1.52) * mm, v(-99.77, 0.92) * mm]});
            skFitSpline(sketch, "E2495", {"points": [v(-99.77, 0.92) * mm, v(-99.43, 0.66) * mm, v(-99.09, 0.4) * mm, v(-98.73, 0.12) * mm]});
            skFitSpline(sketch, "E2496", {"points": [v(-98.73, 0.12) * mm, v(-98.7, 0.15) * mm, v(-98.67, 0.17) * mm, v(-98.64, 0.2) * mm]});
            skFitSpline(sketch, "E2497", {"points": [v(-98.64, 0.2) * mm, v(-98.17, 0.6) * mm, v(-97.7, 1.02) * mm, v(-97.24, 1.43) * mm]});
            skFitSpline(sketch, "E2498", {"points": [v(-97.24, 1.43) * mm, v(-96.77, 1.86) * mm, v(-96.3, 2.28) * mm, v(-95.84, 2.7) * mm]});
            skFitSpline(sketch, "E2499", {"points": [v(-95.84, 2.7) * mm, v(-95.67, 2.86) * mm, v(-95.53, 3.06) * mm, v(-95.37, 3.22) * mm]});
            skFitSpline(sketch, "E2500", {"points": [v(-95.37, 3.22) * mm, v(-95.3, 3.3) * mm, v(-95.2, 3.36) * mm, v(-95.1, 3.4) * mm]});
            skFitSpline(sketch, "E2501", {"points": [v(-95.1, 3.4) * mm, v(-94.9, 3.47) * mm, v(-94.68, 3.38) * mm, v(-94.57, 3.21) * mm]});
            skFitSpline(sketch, "E2502", {"points": [v(-94.57, 3.21) * mm, v(-94.45, 3.03) * mm, v(-94.45, 2.8) * mm, v(-94.6, 2.63) * mm]});
            skFitSpline(sketch, "E2503", {"points": [v(-94.6, 2.63) * mm, v(-94.78, 2.4) * mm, v(-94.98, 2.18) * mm, v(-95.19, 1.98) * mm]});
            skFitSpline(sketch, "E2504", {"points": [v(-95.19, 1.98) * mm, v(-95.66, 1.53) * mm, v(-96.15, 1.1) * mm, v(-96.63, 0.67) * mm]});
            skFitSpline(sketch, "E2505", {"points": [v(-96.63, 0.67) * mm, v(-96.66, 0.64) * mm, v(-96.7, 0.61) * mm, v(-96.72, 0.55) * mm]});
            skFitSpline(sketch, "E2506", {"points": [v(-96.72, 0.55) * mm, v(-96.68, 0.56) * mm, v(-96.63, 0.57) * mm, v(-96.58, 0.58) * mm]});
            skFitSpline(sketch, "E2507", {"points": [v(-96.58, 0.58) * mm, v(-96.15, 0.76) * mm, v(-95.73, 0.93) * mm, v(-95.3, 1.1) * mm]});
            skFitSpline(sketch, "E2508", {"points": [v(-95.3, 1.1) * mm, v(-95.13, 1.17) * mm, v(-94.96, 1.24) * mm, v(-94.78, 1.29) * mm]});
            skFitSpline(sketch, "E2509", {"points": [v(-94.78, 1.29) * mm, v(-94.59, 1.34) * mm, v(-94.4, 1.31) * mm, v(-94.23, 1.2) * mm]});
            skFitSpline(sketch, "E2510", {"points": [v(-94.23, 1.2) * mm, v(-93.66, 0.82) * mm, v(-93.09, 0.46) * mm, v(-92.52, 0.1) * mm]});
            skFitSpline(sketch, "E2511", {"points": [v(-92.52, 0.1) * mm, v(-92.41, 0.02) * mm, v(-92.3, -0.06) * mm, v(-92.22, -0.15) * mm]});
            skFitSpline(sketch, "E2512", {"points": [v(-92.22, -0.15) * mm, v(-91.99, -0.4) * mm, v(-91.99, -0.67) * mm, v(-92.22, -0.92) * mm]});
            skFitSpline(sketch, "E2513", {"points": [v(-92.22, -0.92) * mm, v(-92.3, -1) * mm, v(-92.4, -1.09) * mm, v(-92.51, -1.16) * mm]});
            skFitSpline(sketch, "E2514", {"points": [v(-92.51, -1.16) * mm, v(-93.08, -1.53) * mm, v(-93.66, -1.89) * mm, v(-94.22, -2.26) * mm]});
            skFitSpline(sketch, "E2515", {"points": [v(-94.22, -2.26) * mm, v(-94.41, -2.38) * mm, v(-94.6, -2.43) * mm, v(-94.81, -2.35) * mm]});
            skFitSpline(sketch, "E2516", {"points": [v(-94.81, -2.35) * mm, v(-95.03, -2.27) * mm, v(-95.25, -2.19) * mm, v(-95.46, -2.09) * mm]});
            skFitSpline(sketch, "E2517", {"points": [v(-95.46, -2.09) * mm, v(-95.87, -1.9) * mm, v(-96.3, -1.75) * mm, v(-96.78, -1.59) * mm]});
            skFitSpline(sketch, "E2518", {"points": [v(-96.78, -1.59) * mm, v(-96.72, -1.66) * mm, v(-96.7, -1.68) * mm, v(-96.67, -1.7) * mm]});
            skFitSpline(sketch, "E2519", {"points": [v(-96.67, -1.7) * mm, v(-96.18, -2.15) * mm, v(-95.7, -2.58) * mm, v(-95.21, -3.03) * mm]});
            skFitSpline(sketch, "E2520", {"points": [v(-95.21, -3.03) * mm, v(-95, -3.23) * mm, v(-94.8, -3.47) * mm, v(-94.6, -3.7) * mm]});
            skFitSpline(sketch, "E2521", {"points": [v(-94.6, -3.7) * mm, v(-94.43, -3.9) * mm, v(-94.45, -4.17) * mm, v(-94.63, -4.35) * mm]});
            skFitSpline(sketch, "E2522", {"points": [v(-94.63, -4.35) * mm, v(-94.8, -4.53) * mm, v(-95.07, -4.54) * mm, v(-95.28, -4.38) * mm]});
            skFitSpline(sketch, "E2523", {"points": [v(-95.28, -4.38) * mm, v(-95.36, -4.3) * mm, v(-95.43, -4.22) * mm, v(-95.51, -4.14) * mm]});
            skFitSpline(sketch, "E2524", {"points": [v(-95.51, -4.14) * mm, v(-95.8, -3.85) * mm, v(-96.08, -3.55) * mm, v(-96.38, -3.28) * mm]});
            skFitSpline(sketch, "E2525", {"points": [v(-96.38, -3.28) * mm, v(-97.13, -2.6) * mm, v(-97.9, -1.92) * mm, v(-98.65, -1.25) * mm]});
            skFitSpline(sketch, "E2526", {"points": [v(-98.65, -1.25) * mm, v(-98.67, -1.23) * mm, v(-98.7, -1.21) * mm, v(-98.73, -1.2) * mm]});
            skFitSpline(sketch, "E2527", {"points": [v(-98.73, -1.2) * mm, v(-99.08, -1.46) * mm, v(-99.43, -1.72) * mm, v(-99.78, -2) * mm]});
            skFitSpline(sketch, "E2528", {"points": [v(-99.78, -2) * mm, v(-99.7, -2.07) * mm, v(-99.65, -2.13) * mm, v(-99.59, -2.2) * mm]});
            skFitSpline(sketch, "E2529", {"points": [v(-99.59, -2.2) * mm, v(-98.8, -2.95) * mm, v(-98.04, -3.73) * mm, v(-97.34, -4.55) * mm]});
            skFitSpline(sketch, "E2530", {"points": [v(-97.34, -4.55) * mm, v(-97.06, -4.88) * mm, v(-96.8, -5.21) * mm, v(-96.55, -5.55) * mm]});
            skFitSpline(sketch, "E2531", {"points": [v(-96.55, -5.55) * mm, v(-96.48, -5.65) * mm, v(-96.42, -5.78) * mm, v(-96.4, -5.9) * mm]});
            skFitSpline(sketch, "E2532", {"points": [v(-96.4, -5.9) * mm, v(-96.37, -6.13) * mm, v(-96.5, -6.33) * mm, v(-96.72, -6.4) * mm]});
            skFitSpline(sketch, "E2533", {"points": [v(-96.72, -6.4) * mm, v(-96.95, -6.49) * mm, v(-97.2, -6.4) * mm, v(-97.33, -6.2) * mm]});
            skFitSpline(sketch, "E2534", {"points": [v(-97.33, -6.2) * mm, v(-97.7, -5.63) * mm, v(-98.12, -5.1) * mm, v(-98.6, -4.6) * mm]});
            skFitSpline(sketch, "E2535", {"points": [v(-98.6, -4.6) * mm, v(-99.02, -4.16) * mm, v(-99.44, -3.72) * mm, v(-99.88, -3.28) * mm]});
            skFitSpline(sketch, "E2536", {"points": [v(-99.88, -3.28) * mm, v(-100.1, -3.05) * mm, v(-100.33, -2.83) * mm, v(-100.57, -2.62) * mm]});
            skFitSpline(sketch, "E2537", {"points": [v(-100.57, -2.62) * mm, v(-100.64, -2.56) * mm, v(-100.72, -2.5) * mm, v(-100.81, -2.47) * mm]});
            skFitSpline(sketch, "E2538", {"points": [v(-100.81, -2.47) * mm, v(-101.06, -2.4) * mm, v(-101.32, -2.35) * mm, v(-101.58, -2.3) * mm]});
            skFitSpline(sketch, "E2539", {"points": [v(-101.58, -2.3) * mm, v(-101.9, -2.22) * mm, v(-102.23, -2.15) * mm, v(-102.56, -2.08) * mm]});
            skFitSpline(sketch, "E2540", {"points": [v(-102.56, -2.08) * mm, v(-102.74, -2.05) * mm, v(-102.92, -2.02) * mm, v(-103.16, -1.98) * mm]});
            skFitSpline(sketch, "E2541", {"points": [v(-103.16, -1.98) * mm, v(-103.05, -2.15) * mm, v(-102.97, -2.28) * mm, v(-102.88, -2.4) * mm]});
            skFitSpline(sketch, "E2542", {"points": [v(-102.88, -2.4) * mm, v(-102.54, -2.93) * mm, v(-102.19, -3.46) * mm, v(-101.85, -3.99) * mm]});
            skFitSpline(sketch, "E2543", {"points": [v(-101.85, -3.99) * mm, v(-101.77, -4.11) * mm, v(-101.72, -4.25) * mm, v(-101.76, -4.4) * mm]});
            skFitSpline(sketch, "E2544", {"points": [v(-101.76, -4.4) * mm, v(-101.8, -4.6) * mm, v(-101.97, -4.75) * mm, v(-102.17, -4.78) * mm]});
            skFitSpline(sketch, "E2545", {"points": [v(-102.17, -4.78) * mm, v(-102.38, -4.81) * mm, v(-102.62, -4.7) * mm, v(-102.7, -4.5) * mm]});
            skFitSpline(sketch, "E2546", {"points": [v(-102.7, -4.5) * mm, v(-102.96, -3.95) * mm, v(-103.33, -3.47) * mm, v(-103.67, -2.98) * mm]});
            skFitSpline(sketch, "E2547", {"points": [v(-103.67, -2.98) * mm, v(-103.94, -2.58) * mm, v(-104.2, -2.18) * mm, v(-104.42, -1.73) * mm]});
            skFitSpline(sketch, "E2548", {"points": [v(-104.42, -1.73) * mm, v(-104.78, -1.68) * mm, v(-105.15, -1.63) * mm, v(-105.55, -1.57) * mm]});
            skFitSpline(sketch, "E2549", {"points": [v(-105.55, -1.57) * mm, v(-105.53, -1.62) * mm, v(-105.53, -1.65) * mm, v(-105.51, -1.68) * mm]});
            skFitSpline(sketch, "E2550", {"points": [v(-105.51, -1.68) * mm, v(-105.04, -2.4) * mm, v(-104.73, -3.2) * mm, v(-104.33, -3.95) * mm]});
            skFitSpline(sketch, "E2551", {"points": [v(-104.33, -3.95) * mm, v(-104.24, -4.14) * mm, v(-104.17, -4.35) * mm, v(-104.1, -4.56) * mm]});
            skFitSpline(sketch, "E2552", {"points": [v(-104.1, -4.56) * mm, v(-104.04, -4.8) * mm, v(-104.05, -5.02) * mm, v(-104.27, -5.18) * mm]});
            skFitSpline(sketch, "E2553", {"points": [v(-104.27, -5.18) * mm, v(-104.32, -5.21) * mm, v(-104.35, -5.26) * mm, v(-104.37, -5.31) * mm]});
            skFitSpline(sketch, "E2554", {"points": [v(-104.37, -5.31) * mm, v(-104.46, -5.55) * mm, v(-104.64, -5.67) * mm, v(-104.9, -5.65) * mm]});
            skFitSpline(sketch, "E2555", {"points": [v(-104.9, -5.65) * mm, v(-105.38, -5.6) * mm, v(-105.86, -5.56) * mm, v(-106.34, -5.5) * mm]});
            skFitSpline(sketch, "E2556", {"points": [v(-106.34, -5.5) * mm, v(-106.62, -5.47) * mm, v(-106.9, -5.43) * mm, v(-107.17, -5.38) * mm]});
            skFitSpline(sketch, "E2557", {"points": [v(-107.17, -5.38) * mm, v(-107.5, -5.33) * mm, v(-107.83, -5.26) * mm, v(-108.19, -5.2) * mm]});
            skFitSpline(sketch, "E2558", {"points": [v(-108.19, -5.2) * mm, v(-108.1, -5.37) * mm, v(-108.02, -5.54) * mm, v(-107.93, -5.7) * mm]});
            skFitSpline(sketch, "E2559", {"points": [v(-107.93, -5.7) * mm, v(-107.85, -5.88) * mm, v(-107.77, -6.05) * mm, v(-107.69, -6.23) * mm]});
            skFitSpline(sketch, "E2560", {"points": [v(-107.69, -6.23) * mm, v(-107.04, -6.31) * mm, v(-106.44, -6.5) * mm, v(-105.83, -6.68) * mm]});
            skFitSpline(sketch, "E2561", {"points": [v(-105.83, -6.68) * mm, v(-105.5, -6.78) * mm, v(-105.16, -6.86) * mm, v(-104.83, -6.95) * mm]});
            skFitSpline(sketch, "E2562", {"points": [v(-104.83, -6.95) * mm, v(-104.75, -6.97) * mm, v(-104.66, -6.98) * mm, v(-104.57, -7) * mm]});
            skFitSpline(sketch, "E2563", {"points": [v(-104.57, -7) * mm, v(-104.27, -7.03) * mm, v(-104.05, -7.28) * mm, v(-104.08, -7.56) * mm]});
            skFitSpline(sketch, "E2564", {"points": [v(-104.08, -7.56) * mm, v(-104.12, -7.87) * mm, v(-104.39, -8.05) * mm, v(-104.72, -7.97) * mm]});
            skFitSpline(sketch, "E2565", {"points": [v(-104.72, -7.97) * mm, v(-105.32, -7.82) * mm, v(-105.92, -7.65) * mm, v(-106.52, -7.5) * mm]});
            skFitSpline(sketch, "E2566", {"points": [v(-106.52, -7.5) * mm, v(-106.68, -7.45) * mm, v(-106.84, -7.4) * mm, v(-107.05, -7.35) * mm]});
            skFitSpline(sketch, "E2567", {"points": [v(-107.05, -7.35) * mm, v(-106.93, -7.58) * mm, v(-106.84, -7.77) * mm, v(-106.74, -7.95) * mm]});
            skFitSpline(sketch, "E2568", {"points": [v(-106.74, -7.95) * mm, v(-106.47, -8.42) * mm, v(-106.2, -8.89) * mm, v(-105.91, -9.35) * mm]});
            skFitSpline(sketch, "E2569", {"points": [v(-105.91, -9.35) * mm, v(-105.86, -9.44) * mm, v(-105.77, -9.53) * mm, v(-105.68, -9.59) * mm]});
            skFitSpline(sketch, "E2570", {"points": [v(-105.68, -9.59) * mm, v(-104.64, -10.19) * mm, v(-103.56, -10.7) * mm, v(-102.46, -11.17) * mm]});
            skFitSpline(sketch, "E2571", {"points": [v(-102.46, -11.17) * mm, v(-102.07, -11.34) * mm, v(-101.65, -11.46) * mm, v(-101.24, -11.59) * mm]});
            skFitSpline(sketch, "E2572", {"points": [v(-101.24, -11.59) * mm, v(-100.98, -11.67) * mm, v(-100.82, -11.9) * mm, v(-100.87, -12.18) * mm]});
            skFitSpline(sketch, "E2573", {"points": [v(-100.87, -12.18) * mm, v(-100.9, -12.41) * mm, v(-101.1, -12.58) * mm, v(-101.37, -12.57) * mm]});
            skFitSpline(sketch, "E2574", {"points": [v(-101.37, -12.57) * mm, v(-101.47, -12.57) * mm, v(-101.59, -12.54) * mm, v(-101.7, -12.5) * mm]});
            skFitSpline(sketch, "E2575", {"points": [v(-101.7, -12.5) * mm, v(-103.15, -12) * mm, v(-104.53, -11.32) * mm, v(-105.9, -10.6) * mm]});
            skFitSpline(sketch, "E2576", {"points": [v(-105.9, -10.6) * mm, v(-105.92, -10.58) * mm, v(-105.95, -10.57) * mm, v(-106, -10.55) * mm]});
            skFitSpline(sketch, "E2577", {"points": [v(-106, -10.55) * mm, v(-106.15, -10.97) * mm, v(-106.29, -11.38) * mm, v(-106.44, -11.8) * mm]});
            skFitSpline(sketch, "E2578", {"points": [v(-106.44, -11.8) * mm, v(-106.36, -11.85) * mm, v(-106.29, -11.9) * mm, v(-106.21, -11.94) * mm]});
            skFitSpline(sketch, "E2579", {"points": [v(-106.21, -11.94) * mm, v(-105.82, -12.17) * mm, v(-105.43, -12.4) * mm, v(-105.03, -12.63) * mm]});
            skFitSpline(sketch, "E2580", {"points": [v(-105.03, -12.63) * mm, v(-104.38, -13) * mm, v(-103.72, -13.4) * mm, v(-103.06, -13.77) * mm]});
            skFitSpline(sketch, "E2581", {"points": [v(-103.06, -13.77) * mm, v(-102.87, -13.88) * mm, v(-102.65, -13.95) * mm, v(-102.45, -14.04) * mm]});
            skFitSpline(sketch, "E2582", {"points": [v(-102.45, -14.04) * mm, v(-102.31, -14.1) * mm, v(-102.2, -14.2) * mm, v(-102.15, -14.33) * mm]});
            skFitSpline(sketch, "E2583", {"points": [v(-102.15, -14.33) * mm, v(-102.08, -14.51) * mm, v(-102.1, -14.68) * mm, v(-102.23, -14.82) * mm]});
            skFitSpline(sketch, "E2584", {"points": [v(-102.23, -14.82) * mm, v(-102.36, -14.97) * mm, v(-102.53, -15.05) * mm, v(-102.73, -14.97) * mm]});
            skFitSpline(sketch, "E2585", {"points": [v(-102.73, -14.97) * mm, v(-103.01, -14.86) * mm, v(-103.3, -14.74) * mm, v(-103.58, -14.6) * mm]});
            skFitSpline(sketch, "E2586", {"points": [v(-103.58, -14.6) * mm, v(-104.15, -14.28) * mm, v(-104.72, -13.94) * mm, v(-105.28, -13.62) * mm]});
            skFitSpline(sketch, "E2587", {"points": [v(-105.28, -13.62) * mm, v(-105.32, -13.6) * mm, v(-105.36, -13.57) * mm, v(-105.4, -13.55) * mm]});
            skFitSpline(sketch, "E2588", {"points": [v(-53.87, -0.52) * mm, v(-54.41, -0.15) * mm, v(-54.94, 0.2) * mm, v(-55.46, 0.56) * mm]});
            skFitSpline(sketch, "E2589", {"points": [v(-55.46, 0.56) * mm, v(-55.63, 0.68) * mm, v(-55.77, 0.69) * mm, v(-55.95, 0.57) * mm]});
            skFitSpline(sketch, "E2590", {"points": [v(-55.95, 0.57) * mm, v(-56.12, 0.45) * mm, v(-56.33, 0.4) * mm, v(-56.52, 0.31) * mm]});
            skFitSpline(sketch, "E2591", {"points": [v(-56.52, 0.31) * mm, v(-56.6, 0.28) * mm, v(-56.7, 0.25) * mm, v(-56.79, 0.21) * mm]});
            skFitSpline(sketch, "E2592", {"points": [v(-56.79, 0.21) * mm, v(-57.27, 0) * mm, v(-57.74, -0.23) * mm, v(-58.22, -0.45) * mm]});
            skFitSpline(sketch, "E2593", {"points": [v(-58.22, -0.45) * mm, v(-58.27, -0.47) * mm, v(-58.31, -0.5) * mm, v(-58.38, -0.55) * mm]});
            skFitSpline(sketch, "E2594", {"points": [v(-58.38, -0.55) * mm, v(-57.48, -0.95) * mm, v(-56.6, -1.35) * mm, v(-55.69, -1.75) * mm]});
            skFitSpline(sketch, "E2595", {"points": [v(-55.69, -1.75) * mm, v(-55.08, -1.41) * mm, v(-54.49, -1) * mm, v(-53.87, -0.52) * mm]});
            skFitSpline(sketch, "E2596", {"points": [v(-81.82, -9.63) * mm, v(-81.47, -9.63) * mm, v(-81.17, -9.63) * mm, v(-80.87, -9.63) * mm]});
            skFitSpline(sketch, "E2597", {"points": [v(-80.87, -9.63) * mm, v(-80.8, -9.63) * mm, v(-80.74, -9.63) * mm, v(-80.68, -9.63) * mm]});
            skFitSpline(sketch, "E2598", {"points": [v(-80.68, -9.63) * mm, v(-80.48, -9.61) * mm, v(-80.28, -9.6) * mm, v(-80.08, -9.58) * mm]});
            skFitSpline(sketch, "E2599", {"points": [v(-80.08, -9.58) * mm, v(-79.95, -9.57) * mm, v(-79.81, -9.56) * mm, v(-79.68, -9.54) * mm]});
            skFitSpline(sketch, "E2600", {"points": [v(-79.68, -9.54) * mm, v(-79.64, -9.54) * mm, v(-79.6, -9.5) * mm, v(-79.57, -9.47) * mm]});
            skFitSpline(sketch, "E2601", {"points": [v(-79.57, -9.47) * mm, v(-79.38, -9.15) * mm, v(-79.2, -8.84) * mm, v(-79.02, -8.52) * mm]});
            skFitSpline(sketch, "E2602", {"points": [v(-79.02, -8.52) * mm, v(-78.75, -8.05) * mm, v(-78.5, -7.58) * mm, v(-78.24, -7.12) * mm]});
            skFitSpline(sketch, "E2603", {"points": [v(-78.24, -7.12) * mm, v(-78.21, -7.07) * mm, v(-78.2, -7.02) * mm, v(-78.18, -6.95) * mm]});
            skFitSpline(sketch, "E2604", {"points": [v(-78.18, -6.95) * mm, v(-78.89, -7.1) * mm, v(-79.56, -7.25) * mm, v(-80.24, -7.4) * mm]});
            skFitSpline(sketch, "E2605", {"points": [v(-80.24, -7.4) * mm, v(-80.46, -7.44) * mm, v(-80.7, -7.48) * mm, v(-80.92, -7.52) * mm]});
            skFitSpline(sketch, "E2606", {"points": [v(-80.92, -7.52) * mm, v(-81, -7.53) * mm, v(-81.07, -7.56) * mm, v(-81.1, -7.64) * mm]});
            skFitSpline(sketch, "E2607", {"points": [v(-81.1, -7.64) * mm, v(-81.17, -7.83) * mm, v(-81.25, -8) * mm, v(-81.32, -8.2) * mm]});
            skFitSpline(sketch, "E2608", {"points": [v(-81.32, -8.2) * mm, v(-81.49, -8.66) * mm, v(-81.65, -9.13) * mm, v(-81.82, -9.63) * mm]});
            skFitSpline(sketch, "E2609", {"points": [v(-66.27, -13.87) * mm, v(-65.74, -14.35) * mm, v(-65.16, -14.79) * mm, v(-64.55, -15.2) * mm]});
            skFitSpline(sketch, "E2610", {"points": [v(-64.55, -15.2) * mm, v(-64.3, -14.5) * mm, v(-64.08, -13.81) * mm, v(-63.94, -13.12) * mm]});
            skFitSpline(sketch, "E2611", {"points": [v(-63.94, -13.12) * mm, v(-64.6, -12.38) * mm, v(-65.26, -11.67) * mm, v(-65.9, -10.95) * mm]});
            skFitSpline(sketch, "E2612", {"points": [v(-65.9, -10.95) * mm, v(-65.92, -10.95) * mm, v(-65.94, -10.96) * mm, v(-65.96, -10.96) * mm]});
            skFitSpline(sketch, "E2613", {"points": [v(-65.96, -10.96) * mm, v(-66.06, -11.92) * mm, v(-66.16, -12.87) * mm, v(-66.27, -13.87) * mm]});
            skFitSpline(sketch, "E2614", {"points": [v(-78.17, 5.89) * mm, v(-78.2, 5.95) * mm, v(-78.2, 5.98) * mm, v(-78.21, 6) * mm]});
            skFitSpline(sketch, "E2615", {"points": [v(-78.21, 6) * mm, v(-78.55, 6.6) * mm, v(-78.9, 7.18) * mm, v(-79.24, 7.78) * mm]});
            skFitSpline(sketch, "E2616", {"points": [v(-79.24, 7.78) * mm, v(-79.34, 7.96) * mm, v(-79.45, 8.14) * mm, v(-79.53, 8.32) * mm]});
            skFitSpline(sketch, "E2617", {"points": [v(-79.53, 8.32) * mm, v(-79.58, 8.43) * mm, v(-79.65, 8.49) * mm, v(-79.76, 8.5) * mm]});
            skFitSpline(sketch, "E2618", {"points": [v(-79.76, 8.5) * mm, v(-79.95, 8.5) * mm, v(-80.14, 8.52) * mm, v(-80.33, 8.52) * mm]});
            skFitSpline(sketch, "E2619", {"points": [v(-80.33, 8.52) * mm, v(-80.82, 8.53) * mm, v(-81.3, 8.53) * mm, v(-81.8, 8.53) * mm]});
            skFitSpline(sketch, "E2620", {"points": [v(-81.8, 8.53) * mm, v(-81.7, 8.2) * mm, v(-81.6, 7.87) * mm, v(-81.49, 7.54) * mm]});
            skFitSpline(sketch, "E2621", {"points": [v(-81.49, 7.54) * mm, v(-81.37, 7.22) * mm, v(-81.23, 6.9) * mm, v(-81.1, 6.59) * mm]});
            skFitSpline(sketch, "E2622", {"points": [v(-81.1, 6.59) * mm, v(-81.07, 6.49) * mm, v(-81, 6.45) * mm, v(-80.9, 6.44) * mm]});
            skFitSpline(sketch, "E2623", {"points": [v(-80.9, 6.44) * mm, v(-80.72, 6.42) * mm, v(-80.54, 6.4) * mm, v(-80.37, 6.35) * mm]});
            skFitSpline(sketch, "E2624", {"points": [v(-80.37, 6.35) * mm, v(-80.19, 6.31) * mm, v(-80, 6.25) * mm, v(-79.82, 6.2) * mm]});
            skFitSpline(sketch, "E2625", {"points": [v(-79.82, 6.2) * mm, v(-79.5, 6.14) * mm, v(-79.18, 6.09) * mm, v(-78.86, 6.02) * mm]});
            skFitSpline(sketch, "E2626", {"points": [v(-78.86, 6.02) * mm, v(-78.64, 5.98) * mm, v(-78.42, 5.94) * mm, v(-78.17, 5.89) * mm]});
            skFitSpline(sketch, "E2627", {"points": [v(-63.94, 12.05) * mm, v(-64.1, 12.76) * mm, v(-64.3, 13.45) * mm, v(-64.55, 14.13) * mm]});
            skFitSpline(sketch, "E2628", {"points": [v(-64.55, 14.13) * mm, v(-65.17, 13.7) * mm, v(-65.75, 13.28) * mm, v(-66.27, 12.8) * mm]});
            skFitSpline(sketch, "E2629", {"points": [v(-66.27, 12.8) * mm, v(-66.16, 11.81) * mm, v(-66.06, 10.85) * mm, v(-65.95, 9.83) * mm]});
            skFitSpline(sketch, "E2630", {"points": [v(-65.95, 9.83) * mm, v(-65.26, 10.6) * mm, v(-64.6, 11.32) * mm, v(-63.94, 12.05) * mm]});
            skFitSpline(sketch, "E2631", {"points": [v(-72.78, 10.2) * mm, v(-73.14, 9.78) * mm, v(-74.01, 8.25) * mm, v(-74.08, 7.94) * mm]});
            skFitSpline(sketch, "E2632", {"points": [v(-74.08, 7.94) * mm, v(-73.26, 7.32) * mm, v(-72.4, 6.78) * mm, v(-71.51, 6.23) * mm]});
            skFitSpline(sketch, "E2633", {"points": [v(-71.51, 6.23) * mm, v(-71.12, 7.21) * mm, v(-70.73, 8.16) * mm, v(-70.43, 9.17) * mm]});
            skFitSpline(sketch, "E2634", {"points": [v(-70.43, 9.17) * mm, v(-71.19, 9.59) * mm, v(-71.99, 9.87) * mm, v(-72.78, 10.2) * mm]});
            skFitSpline(sketch, "E2635", {"points": [v(-70.43, -10.2) * mm, v(-70.74, -9.2) * mm, v(-71.13, -8.26) * mm, v(-71.52, -7.29) * mm]});
            skFitSpline(sketch, "E2636", {"points": [v(-71.52, -7.29) * mm, v(-72.4, -7.86) * mm, v(-73.25, -8.43) * mm, v(-74.1, -8.98) * mm]});
            skFitSpline(sketch, "E2637", {"points": [v(-74.1, -8.98) * mm, v(-74, -9.36) * mm, v(-73.05, -10.98) * mm, v(-72.78, -11.24) * mm]});
            skFitSpline(sketch, "E2638", {"points": [v(-72.78, -11.24) * mm, v(-72.32, -11.13) * mm, v(-70.73, -10.43) * mm, v(-70.43, -10.2) * mm]});
            skFitSpline(sketch, "E2639", {"points": [v(-60.21, -7.18) * mm, v(-60.16, -6.55) * mm, v(-60.35, -4.82) * mm, v(-60.48, -4.6) * mm]});
            skFitSpline(sketch, "E2640", {"points": [v(-60.48, -4.6) * mm, v(-61.51, -4.57) * mm, v(-62.53, -4.64) * mm, v(-63.56, -4.72) * mm]});
            skFitSpline(sketch, "E2641", {"points": [v(-63.56, -4.72) * mm, v(-63.3, -5.74) * mm, v(-63.06, -6.74) * mm, v(-62.71, -7.73) * mm]});
            skFitSpline(sketch, "E2642", {"points": [v(-62.71, -7.73) * mm, v(-61.85, -7.62) * mm, v(-61.04, -7.39) * mm, v(-60.21, -7.18) * mm]});
            skFitSpline(sketch, "E2643", {"points": [v(-78.86, 1.42) * mm, v(-79.52, 0.82) * mm, v(-80.05, 0.13) * mm, v(-80.6, -0.54) * mm]});
            skFitSpline(sketch, "E2644", {"points": [v(-80.6, -0.54) * mm, v(-80.03, -1.2) * mm, v(-79.52, -1.9) * mm, v(-78.85, -2.49) * mm]});
            skFitSpline(sketch, "E2645", {"points": [v(-78.85, -2.49) * mm, v(-78.03, -1.83) * mm, v(-77.23, -1.2) * mm, v(-76.4, -0.53) * mm]});
            skFitSpline(sketch, "E2646", {"points": [v(-76.4, -0.53) * mm, v(-77.23, 0.13) * mm, v(-78.03, 0.76) * mm, v(-78.86, 1.42) * mm]});
            skFitSpline(sketch, "E2647", {"points": [v(-60.18, 6.1) * mm, v(-60.36, 6.15) * mm, v(-60.52, 6.2) * mm, v(-60.68, 6.23) * mm]});
            skFitSpline(sketch, "E2648", {"points": [v(-60.68, 6.23) * mm, v(-61.12, 6.34) * mm, v(-61.55, 6.44) * mm, v(-61.98, 6.54) * mm]});
            skFitSpline(sketch, "E2649", {"points": [v(-61.98, 6.54) * mm, v(-62.23, 6.6) * mm, v(-62.48, 6.67) * mm, v(-62.73, 6.62) * mm]});
            skFitSpline(sketch, "E2650", {"points": [v(-62.73, 6.62) * mm, v(-63.06, 5.64) * mm, v(-63.31, 4.66) * mm, v(-63.55, 3.64) * mm]});
            skFitSpline(sketch, "E2651", {"points": [v(-63.55, 3.64) * mm, v(-62.51, 3.58) * mm, v(-61.5, 3.49) * mm, v(-60.44, 3.51) * mm]});
            skFitSpline(sketch, "E2652", {"points": [v(-60.44, 3.51) * mm, v(-60.26, 4.37) * mm, v(-60.24, 5.22) * mm, v(-60.18, 6.1) * mm]});
            skFitSpline(sketch, "E2653", {"points": [v(-61.13, -0.52) * mm, v(-61.23, -0.43) * mm, v(-61.32, -0.33) * mm, v(-61.41, -0.24) * mm]});
            skFitSpline(sketch, "E2654", {"points": [v(-61.41, -0.24) * mm, v(-61.94, 0.27) * mm, v(-62.47, 0.79) * mm, v(-63, 1.29) * mm]});
            skFitSpline(sketch, "E2655", {"points": [v(-63, 1.29) * mm, v(-63.35, 1.6) * mm, v(-63.71, 1.91) * mm, v(-64.07, 2.22) * mm]});
            skFitSpline(sketch, "E2656", {"points": [v(-64.07, 2.22) * mm, v(-64.1, 2.26) * mm, v(-64.17, 2.29) * mm, v(-64.23, 2.33) * mm]});
            skFitSpline(sketch, "E2657", {"points": [v(-64.23, 2.33) * mm, v(-64.25, 2.26) * mm, v(-64.28, 2.2) * mm, v(-64.3, 2.15) * mm]});
            skFitSpline(sketch, "E2658", {"points": [v(-64.3, 2.15) * mm, v(-64.57, 1.33) * mm, v(-64.85, 0.5) * mm, v(-65.13, -0.32) * mm]});
            skFitSpline(sketch, "E2659", {"points": [v(-65.13, -0.32) * mm, v(-65.18, -0.47) * mm, v(-65.18, -0.6) * mm, v(-65.13, -0.76) * mm]});
            skFitSpline(sketch, "E2660", {"points": [v(-65.13, -0.76) * mm, v(-64.87, -1.5) * mm, v(-64.62, -2.25) * mm, v(-64.37, -3) * mm]});
            skFitSpline(sketch, "E2661", {"points": [v(-64.37, -3) * mm, v(-64.33, -3.13) * mm, v(-64.28, -3.27) * mm, v(-64.23, -3.4) * mm]});
            skFitSpline(sketch, "E2662", {"points": [v(-64.23, -3.4) * mm, v(-63.86, -3.17) * mm, v(-61.4, -0.87) * mm, v(-61.13, -0.52) * mm]});
            skFitSpline(sketch, "E2663", {"points": [v(-70.46, 5.2) * mm, v(-70.43, 5.17) * mm, v(-70.43, 5.15) * mm, v(-70.42, 5.14) * mm]});
            skFitSpline(sketch, "E2664", {"points": [v(-70.42, 5.14) * mm, v(-69.67, 4.59) * mm, v(-68.92, 4.03) * mm, v(-68.17, 3.47) * mm]});
            skFitSpline(sketch, "E2665", {"points": [v(-68.17, 3.47) * mm, v(-68.07, 3.4) * mm, v(-67.96, 3.37) * mm, v(-67.83, 3.37) * mm]});
            skFitSpline(sketch, "E2666", {"points": [v(-67.83, 3.37) * mm, v(-67.37, 3.38) * mm, v(-66.91, 3.4) * mm, v(-66.45, 3.4) * mm]});
            skFitSpline(sketch, "E2667", {"points": [v(-66.45, 3.4) * mm, v(-66.03, 3.4) * mm, v(-65.62, 3.4) * mm, v(-65.2, 3.4) * mm]});
            skFitSpline(sketch, "E2668", {"points": [v(-65.2, 3.4) * mm, v(-65.14, 3.4) * mm, v(-65.08, 3.42) * mm, v(-65, 3.42) * mm]});
            skFitSpline(sketch, "E2669", {"points": [v(-65, 3.42) * mm, v(-65.1, 3.68) * mm, v(-65.18, 3.93) * mm, v(-65.29, 4.15) * mm]});
            skFitSpline(sketch, "E2670", {"points": [v(-65.29, 4.15) * mm, v(-65.74, 5.11) * mm, v(-66.2, 6.07) * mm, v(-66.66, 7.03) * mm]});
            skFitSpline(sketch, "E2671", {"points": [v(-66.66, 7.03) * mm, v(-66.7, 7.1) * mm, v(-66.74, 7.18) * mm, v(-66.78, 7.25) * mm]});
            skFitSpline(sketch, "E2672", {"points": [v(-66.78, 7.25) * mm, v(-67.43, 6.99) * mm, v(-70.11, 5.5) * mm, v(-70.46, 5.2) * mm]});
            skFitSpline(sketch, "E2673", {"points": [v(-71.75, -5.83) * mm, v(-71.76, -5.79) * mm, v(-71.77, -5.75) * mm, v(-71.78, -5.71) * mm]});
            skFitSpline(sketch, "E2674", {"points": [v(-71.78, -5.71) * mm, v(-72.05, -4.86) * mm, v(-72.31, -4) * mm, v(-72.58, -3.15) * mm]});
            skFitSpline(sketch, "E2675", {"points": [v(-72.58, -3.15) * mm, v(-72.62, -3) * mm, v(-72.7, -2.9) * mm, v(-72.83, -2.82) * mm]});
            skFitSpline(sketch, "E2676", {"points": [v(-72.83, -2.82) * mm, v(-73.55, -2.31) * mm, v(-74.27, -1.8) * mm, v(-74.98, -1.3) * mm]});
            skFitSpline(sketch, "E2677", {"points": [v(-74.98, -1.3) * mm, v(-75.03, -1.26) * mm, v(-75.08, -1.24) * mm, v(-75.12, -1.21) * mm]});
            skFitSpline(sketch, "E2678", {"points": [v(-75.12, -1.21) * mm, v(-75.34, -1.8) * mm, v(-75.95, -5.08) * mm, v(-75.9, -5.36) * mm]});
            skFitSpline(sketch, "E2679", {"points": [v(-75.9, -5.36) * mm, v(-75.78, -5.38) * mm, v(-75.65, -5.4) * mm, v(-75.53, -5.42) * mm]});
            skFitSpline(sketch, "E2680", {"points": [v(-75.53, -5.42) * mm, v(-74.51, -5.56) * mm, v(-73.5, -5.7) * mm, v(-72.47, -5.83) * mm]});
            skFitSpline(sketch, "E2681", {"points": [v(-72.47, -5.83) * mm, v(-72.24, -5.86) * mm, v(-72, -5.83) * mm, v(-71.75, -5.83) * mm]});
            skFitSpline(sketch, "E2682", {"points": [v(-75.12, 0.14) * mm, v(-75.08, 0.17) * mm, v(-75.05, 0.18) * mm, v(-75.02, 0.2) * mm]});
            skFitSpline(sketch, "E2683", {"points": [v(-75.02, 0.2) * mm, v(-74.28, 0.72) * mm, v(-73.54, 1.25) * mm, v(-72.8, 1.77) * mm]});
            skFitSpline(sketch, "E2684", {"points": [v(-72.8, 1.77) * mm, v(-72.69, 1.85) * mm, v(-72.62, 1.95) * mm, v(-72.58, 2.08) * mm]});
            skFitSpline(sketch, "E2685", {"points": [v(-72.58, 2.08) * mm, v(-72.32, 2.92) * mm, v(-72.05, 3.77) * mm, v(-71.8, 4.61) * mm]});
            skFitSpline(sketch, "E2686", {"points": [v(-71.8, 4.61) * mm, v(-71.77, 4.66) * mm, v(-71.77, 4.72) * mm, v(-71.75, 4.77) * mm]});
            skFitSpline(sketch, "E2687", {"points": [v(-71.75, 4.77) * mm, v(-72.08, 4.82) * mm, v(-75.63, 4.38) * mm, v(-75.92, 4.26) * mm]});
            skFitSpline(sketch, "E2688", {"points": [v(-75.92, 4.26) * mm, v(-75.93, 3.95) * mm, v(-75.3, 0.61) * mm, v(-75.12, 0.14) * mm]});
            skFitSpline(sketch, "E2689", {"points": [v(-70.5, -6.27) * mm, v(-70.27, -6.41) * mm, v(-70.08, -6.55) * mm, v(-69.88, -6.66) * mm]});
            skFitSpline(sketch, "E2690", {"points": [v(-69.88, -6.66) * mm, v(-68.92, -7.19) * mm, v(-67.96, -7.7) * mm, v(-67, -8.22) * mm]});
            skFitSpline(sketch, "E2691", {"points": [v(-67, -8.22) * mm, v(-66.93, -8.26) * mm, v(-66.86, -8.29) * mm, v(-66.76, -8.33) * mm]});
            skFitSpline(sketch, "E2692", {"points": [v(-66.76, -8.33) * mm, v(-66.22, -7.08) * mm, v(-65.54, -5.92) * mm, v(-65.07, -4.67) * mm]});
            skFitSpline(sketch, "E2693", {"points": [v(-65.07, -4.67) * mm, v(-65.04, -4.6) * mm, v(-65.03, -4.55) * mm, v(-65.02, -4.48) * mm]});
            skFitSpline(sketch, "E2694", {"points": [v(-65.02, -4.48) * mm, v(-65.05, -4.48) * mm, v(-65.08, -4.47) * mm, v(-65.1, -4.47) * mm]});
            skFitSpline(sketch, "E2695", {"points": [v(-65.1, -4.47) * mm, v(-66.03, -4.46) * mm, v(-66.97, -4.45) * mm, v(-67.9, -4.45) * mm]});
            skFitSpline(sketch, "E2696", {"points": [v(-67.9, -4.45) * mm, v(-68, -4.45) * mm, v(-68.1, -4.5) * mm, v(-68.18, -4.56) * mm]});
            skFitSpline(sketch, "E2697", {"points": [v(-68.18, -4.56) * mm, v(-68.46, -4.75) * mm, v(-68.74, -4.97) * mm, v(-69.01, -5.17) * mm]});
            skFitSpline(sketch, "E2698", {"points": [v(-69.01, -5.17) * mm, v(-69.5, -5.53) * mm, v(-69.97, -5.88) * mm, v(-70.5, -6.27) * mm]});
            skFitSpline(sketch, "E2699", {"points": [v(-65.23, -3.5) * mm, v(-65.38, -3.08) * mm, v(-65.5, -2.68) * mm, v(-65.63, -2.29) * mm]});
            skFitSpline(sketch, "E2700", {"points": [v(-65.63, -2.29) * mm, v(-65.8, -1.8) * mm, v(-65.96, -1.32) * mm, v(-66.12, -0.84) * mm]});
            skFitSpline(sketch, "E2701", {"points": [v(-66.12, -0.84) * mm, v(-66.19, -0.63) * mm, v(-66.19, -0.43) * mm, v(-66.12, -0.23) * mm]});
            skFitSpline(sketch, "E2702", {"points": [v(-66.12, -0.23) * mm, v(-65.9, 0.4) * mm, v(-65.7, 1.04) * mm, v(-65.48, 1.68) * mm]});
            skFitSpline(sketch, "E2703", {"points": [v(-65.48, 1.68) * mm, v(-65.4, 1.93) * mm, v(-65.32, 2.17) * mm, v(-65.24, 2.44) * mm]});
            skFitSpline(sketch, "E2704", {"points": [v(-65.24, 2.44) * mm, v(-65.35, 2.44) * mm, v(-65.42, 2.45) * mm, v(-65.49, 2.44) * mm]});
            skFitSpline(sketch, "E2705", {"points": [v(-65.49, 2.44) * mm, v(-65.92, 2.43) * mm, v(-66.34, 2.42) * mm, v(-66.77, 2.41) * mm]});
            skFitSpline(sketch, "E2706", {"points": [v(-66.77, 2.41) * mm, v(-67.2, 2.4) * mm, v(-67.62, 2.41) * mm, v(-68.04, 2.41) * mm]});
            skFitSpline(sketch, "E2707", {"points": [v(-68.04, 2.41) * mm, v(-68.24, 2.4) * mm, v(-68.42, 2.46) * mm, v(-68.58, 2.58) * mm]});
            skFitSpline(sketch, "E2708", {"points": [v(-68.58, 2.58) * mm, v(-69.13, 2.98) * mm, v(-69.67, 3.38) * mm, v(-70.22, 3.78) * mm]});
            skFitSpline(sketch, "E2709", {"points": [v(-70.22, 3.78) * mm, v(-70.43, 3.94) * mm, v(-70.64, 4.1) * mm, v(-70.87, 4.26) * mm]});
            skFitSpline(sketch, "E2710", {"points": [v(-70.87, 4.26) * mm, v(-71.03, 3.77) * mm, v(-71.17, 3.32) * mm, v(-71.32, 2.86) * mm]});
            skFitSpline(sketch, "E2711", {"points": [v(-71.32, 2.86) * mm, v(-71.45, 2.44) * mm, v(-71.6, 2.01) * mm, v(-71.72, 1.59) * mm]});
            skFitSpline(sketch, "E2712", {"points": [v(-71.72, 1.59) * mm, v(-71.78, 1.39) * mm, v(-71.9, 1.23) * mm, v(-72.07, 1.11) * mm]});
            skFitSpline(sketch, "E2713", {"points": [v(-72.07, 1.11) * mm, v(-72.61, 0.72) * mm, v(-73.16, 0.33) * mm, v(-73.7, -0.06) * mm]});
            skFitSpline(sketch, "E2714", {"points": [v(-73.7, -0.06) * mm, v(-73.91, -0.21) * mm, v(-74.13, -0.37) * mm, v(-74.36, -0.54) * mm]});
            skFitSpline(sketch, "E2715", {"points": [v(-74.36, -0.54) * mm, v(-73.96, -0.82) * mm, v(-73.59, -1.09) * mm, v(-73.21, -1.36) * mm]});
            skFitSpline(sketch, "E2716", {"points": [v(-73.21, -1.36) * mm, v(-72.82, -1.64) * mm, v(-72.41, -1.92) * mm, v(-72.03, -2.21) * mm]});
            skFitSpline(sketch, "E2717", {"points": [v(-72.03, -2.21) * mm, v(-71.91, -2.3) * mm, v(-71.8, -2.44) * mm, v(-71.76, -2.57) * mm]});
            skFitSpline(sketch, "E2718", {"points": [v(-71.76, -2.57) * mm, v(-71.54, -3.23) * mm, v(-71.33, -3.9) * mm, v(-71.12, -4.55) * mm]});
            skFitSpline(sketch, "E2719", {"points": [v(-71.12, -4.55) * mm, v(-71.04, -4.8) * mm, v(-70.96, -5.06) * mm, v(-70.87, -5.33) * mm]});
            skFitSpline(sketch, "E2720", {"points": [v(-70.87, -5.33) * mm, v(-70.38, -4.97) * mm, v(-69.92, -4.62) * mm, v(-69.46, -4.28) * mm]});
            skFitSpline(sketch, "E2721", {"points": [v(-69.46, -4.28) * mm, v(-69.16, -4.06) * mm, v(-68.86, -3.85) * mm, v(-68.56, -3.63) * mm]});
            skFitSpline(sketch, "E2722", {"points": [v(-68.56, -3.63) * mm, v(-68.43, -3.54) * mm, v(-68.28, -3.49) * mm, v(-68.12, -3.49) * mm]});
            skFitSpline(sketch, "E2723", {"points": [v(-68.12, -3.49) * mm, v(-67.8, -3.5) * mm, v(-67.5, -3.49) * mm, v(-67.19, -3.49) * mm]});
            skFitSpline(sketch, "E2724", {"points": [v(-67.19, -3.49) * mm, v(-66.62, -3.5) * mm, v(-66.05, -3.5) * mm, v(-65.49, -3.5) * mm]});
            skFitSpline(sketch, "E2725", {"points": [v(-65.49, -3.5) * mm, v(-65.42, -3.5) * mm, v(-65.34, -3.5) * mm, v(-65.23, -3.5) * mm]});
            skFitSpline(sketch, "E2726", {"points": [v(-70.02, -16) * mm, v(-70.45, -16.14) * mm, v(-70.8, -16.32) * mm, v(-71.13, -16.54) * mm]});
            skFitSpline(sketch, "E2727", {"points": [v(-71.13, -16.54) * mm, v(-71.33, -16.67) * mm, v(-71.53, -16.82) * mm, v(-71.74, -16.92) * mm]});
            skFitSpline(sketch, "E2728", {"points": [v(-71.74, -16.92) * mm, v(-72, -17.06) * mm, v(-72.27, -16.97) * mm, v(-72.4, -16.73) * mm]});
            skFitSpline(sketch, "E2729", {"points": [v(-72.4, -16.73) * mm, v(-72.52, -16.5) * mm, v(-72.45, -16.2) * mm, v(-72.2, -16.06) * mm]});
            skFitSpline(sketch, "E2730", {"points": [v(-72.2, -16.06) * mm, v(-71.76, -15.82) * mm, v(-71.38, -15.49) * mm, v(-70.9, -15.3) * mm]});
            skFitSpline(sketch, "E2731", {"points": [v(-70.9, -15.3) * mm, v(-70.8, -15.26) * mm, v(-70.69, -15.2) * mm, v(-70.58, -15.15) * mm]});
            skFitSpline(sketch, "E2732", {"points": [v(-70.58, -15.15) * mm, v(-70.42, -15.1) * mm, v(-70.28, -15.05) * mm, v(-70.2, -14.9) * mm]});
            skFitSpline(sketch, "E2733", {"points": [v(-70.2, -14.9) * mm, v(-70.18, -14.86) * mm, v(-70.14, -14.82) * mm, v(-70.1, -14.81) * mm]});
            skFitSpline(sketch, "E2734", {"points": [v(-70.1, -14.81) * mm, v(-69.92, -14.75) * mm, v(-69.86, -14.58) * mm, v(-69.78, -14.43) * mm]});
            skFitSpline(sketch, "E2735", {"points": [v(-69.78, -14.43) * mm, v(-69.59, -14.07) * mm, v(-69.38, -13.72) * mm, v(-69.21, -13.35) * mm]});
            skFitSpline(sketch, "E2736", {"points": [v(-69.21, -13.35) * mm, v(-68.73, -12.3) * mm, v(-68.1, -11.3) * mm, v(-67.67, -10.23) * mm]});
            skFitSpline(sketch, "E2737", {"points": [v(-67.67, -10.23) * mm, v(-67.58, -10) * mm, v(-67.45, -9.77) * mm, v(-67.33, -9.54) * mm]});
            skFitSpline(sketch, "E2738", {"points": [v(-67.33, -9.54) * mm, v(-67.29, -9.44) * mm, v(-67.25, -9.34) * mm, v(-67.2, -9.22) * mm]});
            skFitSpline(sketch, "E2739", {"points": [v(-67.2, -9.22) * mm, v(-68.25, -8.66) * mm, v(-69.29, -8.1) * mm, v(-70.35, -7.52) * mm]});
            skFitSpline(sketch, "E2740", {"points": [v(-70.35, -7.52) * mm, v(-70.33, -7.6) * mm, v(-70.32, -7.66) * mm, v(-70.3, -7.72) * mm]});
            skFitSpline(sketch, "E2741", {"points": [v(-70.3, -7.72) * mm, v(-70, -8.52) * mm, v(-69.7, -9.32) * mm, v(-69.41, -10.12) * mm]});
            skFitSpline(sketch, "E2742", {"points": [v(-69.41, -10.12) * mm, v(-69.37, -10.25) * mm, v(-69.35, -10.39) * mm, v(-69.35, -10.52) * mm]});
            skFitSpline(sketch, "E2743", {"points": [v(-69.35, -10.52) * mm, v(-69.35, -10.7) * mm, v(-69.47, -10.84) * mm, v(-69.62, -10.92) * mm]});
            skFitSpline(sketch, "E2744", {"points": [v(-69.62, -10.92) * mm, v(-69.9, -11.08) * mm, v(-70.2, -11.24) * mm, v(-70.5, -11.37) * mm]});
            skFitSpline(sketch, "E2745", {"points": [v(-70.5, -11.37) * mm, v(-70.94, -11.57) * mm, v(-71.4, -11.75) * mm, v(-71.84, -11.94) * mm]});
            skFitSpline(sketch, "E2746", {"points": [v(-71.84, -11.94) * mm, v(-72, -12) * mm, v(-72.17, -12.09) * mm, v(-72.36, -12.17) * mm]});
            skFitSpline(sketch, "E2747", {"points": [v(-72.36, -12.17) * mm, v(-72.33, -12.22) * mm, v(-72.3, -12.28) * mm, v(-72.27, -12.34) * mm]});
            skFitSpline(sketch, "E2748", {"points": [v(-72.27, -12.34) * mm, v(-72.1, -12.6) * mm, v(-71.93, -12.84) * mm, v(-71.77, -13.1) * mm]});
            skFitSpline(sketch, "E2749", {"points": [v(-71.77, -13.1) * mm, v(-71.63, -13.33) * mm, v(-71.5, -13.57) * mm, v(-71.4, -13.82) * mm]});
            skFitSpline(sketch, "E2750", {"points": [v(-71.4, -13.82) * mm, v(-71.27, -14.12) * mm, v(-71.42, -14.42) * mm, v(-71.7, -14.5) * mm]});
            skFitSpline(sketch, "E2751", {"points": [v(-71.7, -14.5) * mm, v(-71.97, -14.58) * mm, v(-72.32, -14.4) * mm, v(-72.38, -14.12) * mm]});
            skFitSpline(sketch, "E2752", {"points": [v(-72.38, -14.12) * mm, v(-72.43, -13.87) * mm, v(-72.56, -13.67) * mm, v(-72.7, -13.47) * mm]});
            skFitSpline(sketch, "E2753", {"points": [v(-72.7, -13.47) * mm, v(-72.89, -13.2) * mm, v(-73.06, -12.92) * mm, v(-73.24, -12.63) * mm]});
            skFitSpline(sketch, "E2754", {"points": [v(-73.24, -12.63) * mm, v(-73.3, -12.65) * mm, v(-73.36, -12.67) * mm, v(-73.42, -12.7) * mm]});
            skFitSpline(sketch, "E2755", {"points": [v(-73.42, -12.7) * mm, v(-73.74, -12.82) * mm, v(-74.08, -12.94) * mm, v(-74.4, -13.07) * mm]});
            skFitSpline(sketch, "E2756", {"points": [v(-74.4, -13.07) * mm, v(-74.54, -13.13) * mm, v(-74.66, -13.21) * mm, v(-74.78, -13.3) * mm]});
            skFitSpline(sketch, "E2757", {"points": [v(-74.78, -13.3) * mm, v(-74.96, -13.45) * mm, v(-75.22, -13.48) * mm, v(-75.43, -13.37) * mm]});
            skFitSpline(sketch, "E2758", {"points": [v(-75.43, -13.37) * mm, v(-75.62, -13.28) * mm, v(-75.71, -13.09) * mm, v(-75.69, -12.87) * mm]});
            skFitSpline(sketch, "E2759", {"points": [v(-75.69, -12.87) * mm, v(-75.66, -12.7) * mm, v(-75.57, -12.57) * mm, v(-75.42, -12.5) * mm]});
            skFitSpline(sketch, "E2760", {"points": [v(-75.42, -12.5) * mm, v(-75.17, -12.36) * mm, v(-74.92, -12.24) * mm, v(-74.67, -12.13) * mm]});
            skFitSpline(sketch, "E2761", {"points": [v(-74.67, -12.13) * mm, v(-74.34, -12) * mm, v(-74.01, -11.88) * mm, v(-73.68, -11.75) * mm]});
            skFitSpline(sketch, "E2762", {"points": [v(-73.68, -11.75) * mm, v(-74.04, -11.15) * mm, v(-74.4, -10.56) * mm, v(-74.74, -9.97) * mm]});
            skFitSpline(sketch, "E2763", {"points": [v(-74.74, -9.97) * mm, v(-74.9, -9.7) * mm, v(-75.04, -9.4) * mm, v(-75.17, -9.12) * mm]});
            skFitSpline(sketch, "E2764", {"points": [v(-75.17, -9.12) * mm, v(-75.28, -8.88) * mm, v(-75.22, -8.63) * mm, v(-75.03, -8.46) * mm]});
            skFitSpline(sketch, "E2765", {"points": [v(-75.03, -8.46) * mm, v(-74.98, -8.42) * mm, v(-74.94, -8.39) * mm, v(-74.9, -8.36) * mm]});
            skFitSpline(sketch, "E2766", {"points": [v(-74.9, -8.36) * mm, v(-74.19, -7.89) * mm, v(-73.48, -7.42) * mm, v(-72.78, -6.95) * mm]});
            skFitSpline(sketch, "E2767", {"points": [v(-72.78, -6.95) * mm, v(-72.73, -6.91) * mm, v(-72.68, -6.88) * mm, v(-72.57, -6.8) * mm]});
            skFitSpline(sketch, "E2768", {"points": [v(-72.57, -6.8) * mm, v(-73.8, -6.62) * mm, v(-74.96, -6.47) * mm, v(-76.15, -6.32) * mm]});
            skFitSpline(sketch, "E2769", {"points": [v(-76.15, -6.32) * mm, v(-76.2, -6.57) * mm, v(-76.23, -6.8) * mm, v(-76.28, -7.04) * mm]});
            skFitSpline(sketch, "E2770", {"points": [v(-76.28, -7.04) * mm, v(-76.38, -7.57) * mm, v(-76.5, -8.1) * mm, v(-76.58, -8.64) * mm]});
            skFitSpline(sketch, "E2771", {"points": [v(-76.58, -8.64) * mm, v(-76.68, -9.19) * mm, v(-76.74, -9.74) * mm, v(-76.83, -10.3) * mm]});
            skFitSpline(sketch, "E2772", {"points": [v(-76.83, -10.3) * mm, v(-76.9, -10.72) * mm, v(-76.98, -11.14) * mm, v(-77.05, -11.57) * mm]});
            skFitSpline(sketch, "E2773", {"points": [v(-77.05, -11.57) * mm, v(-77.08, -11.8) * mm, v(-77.11, -12.04) * mm, v(-77.14, -12.28) * mm]});
            skFitSpline(sketch, "E2774", {"points": [v(-77.14, -12.28) * mm, v(-77.14, -12.3) * mm, v(-77.16, -12.31) * mm, v(-77.15, -12.32) * mm]});
            skFitSpline(sketch, "E2775", {"points": [v(-77.15, -12.32) * mm, v(-77, -12.55) * mm, v(-77.08, -12.83) * mm, v(-76.92, -13.06) * mm]});
            skFitSpline(sketch, "E2776", {"points": [v(-76.92, -13.06) * mm, v(-76.66, -13.44) * mm, v(-76.46, -13.86) * mm, v(-76.3, -14.3) * mm]});
            skFitSpline(sketch, "E2777", {"points": [v(-76.3, -14.3) * mm, v(-76.26, -14.46) * mm, v(-76.18, -14.61) * mm, v(-76.12, -14.76) * mm]});
            skFitSpline(sketch, "E2778", {"points": [v(-76.12, -14.76) * mm, v(-76.02, -14.98) * mm, v(-76.06, -15.2) * mm, v(-76.22, -15.36) * mm]});
            skFitSpline(sketch, "E2779", {"points": [v(-76.22, -15.36) * mm, v(-76.37, -15.5) * mm, v(-76.6, -15.55) * mm, v(-76.77, -15.44) * mm]});
            skFitSpline(sketch, "E2780", {"points": [v(-76.77, -15.44) * mm, v(-76.85, -15.4) * mm, v(-76.93, -15.33) * mm, v(-76.97, -15.25) * mm]});
            skFitSpline(sketch, "E2781", {"points": [v(-76.97, -15.25) * mm, v(-77.05, -15.1) * mm, v(-77.13, -14.95) * mm, v(-77.17, -14.79) * mm]});
            skFitSpline(sketch, "E2782", {"points": [v(-77.17, -14.79) * mm, v(-77.28, -14.42) * mm, v(-77.46, -14.08) * mm, v(-77.64, -13.74) * mm]});
            skFitSpline(sketch, "E2783", {"points": [v(-77.64, -13.74) * mm, v(-77.68, -13.65) * mm, v(-77.75, -13.57) * mm, v(-77.83, -13.46) * mm]});
            skFitSpline(sketch, "E2784", {"points": [v(-77.83, -13.46) * mm, v(-78.27, -13.76) * mm, v(-78.7, -14.05) * mm, v(-79.13, -14.34) * mm]});
            skFitSpline(sketch, "E2785", {"points": [v(-79.13, -14.34) * mm, v(-79.34, -14.48) * mm, v(-79.56, -14.62) * mm, v(-79.77, -14.75) * mm]});
            skFitSpline(sketch, "E2786", {"points": [v(-79.77, -14.75) * mm, v(-79.9, -14.82) * mm, v(-80.03, -14.83) * mm, v(-80.17, -14.8) * mm]});
            skFitSpline(sketch, "E2787", {"points": [v(-80.17, -14.8) * mm, v(-80.35, -14.74) * mm, v(-80.47, -14.61) * mm, v(-80.5, -14.43) * mm]});
            skFitSpline(sketch, "E2788", {"points": [v(-80.5, -14.43) * mm, v(-80.55, -14.24) * mm, v(-80.49, -14.07) * mm, v(-80.33, -13.96) * mm]});
            skFitSpline(sketch, "E2789", {"points": [v(-80.33, -13.96) * mm, v(-79.89, -13.64) * mm, v(-79.44, -13.34) * mm, v(-79, -13.03) * mm]});
            skFitSpline(sketch, "E2790", {"points": [v(-79, -13.03) * mm, v(-78.77, -12.89) * mm, v(-78.54, -12.76) * mm, v(-78.31, -12.63) * mm]});
            skFitSpline(sketch, "E2791", {"points": [v(-78.31, -12.63) * mm, v(-78.2, -12.57) * mm, v(-78.16, -12.48) * mm, v(-78.14, -12.36) * mm]});
            skFitSpline(sketch, "E2792", {"points": [v(-78.14, -12.36) * mm, v(-78.06, -11.83) * mm, v(-77.98, -11.3) * mm, v(-77.9, -10.78) * mm]});
            skFitSpline(sketch, "E2793", {"points": [v(-77.9, -10.78) * mm, v(-77.83, -10.31) * mm, v(-77.75, -9.85) * mm, v(-77.67, -9.38) * mm]});
            skFitSpline(sketch, "E2794", {"points": [v(-77.67, -9.38) * mm, v(-77.6, -8.86) * mm, v(-77.5, -8.34) * mm, v(-77.42, -7.83) * mm]});
            skFitSpline(sketch, "E2795", {"points": [v(-77.42, -7.83) * mm, v(-77.42, -7.8) * mm, v(-77.42, -7.76) * mm, v(-77.42, -7.7) * mm]});
            skFitSpline(sketch, "E2796", {"points": [v(-77.42, -7.7) * mm, v(-77.47, -7.77) * mm, v(-77.51, -7.81) * mm, v(-77.54, -7.86) * mm]});
            skFitSpline(sketch, "E2797", {"points": [v(-77.54, -7.86) * mm, v(-77.74, -8.23) * mm, v(-77.94, -8.6) * mm, v(-78.14, -8.95) * mm]});
            skFitSpline(sketch, "E2798", {"points": [v(-78.14, -8.95) * mm, v(-78.17, -9) * mm, v(-78.2, -9.05) * mm, v(-78.23, -9.1) * mm]});
            skFitSpline(sketch, "E2799", {"points": [v(-78.23, -9.1) * mm, v(-78.4, -9.35) * mm, v(-78.58, -9.6) * mm, v(-78.69, -9.9) * mm]});
            skFitSpline(sketch, "E2800", {"points": [v(-78.69, -9.9) * mm, v(-78.82, -10.28) * mm, v(-79.09, -10.49) * mm, v(-79.5, -10.5) * mm]});
            skFitSpline(sketch, "E2801", {"points": [v(-79.5, -10.5) * mm, v(-80.03, -10.53) * mm, v(-80.56, -10.57) * mm, v(-81.1, -10.59) * mm]});
            skFitSpline(sketch, "E2802", {"points": [v(-81.1, -10.59) * mm, v(-81.42, -10.6) * mm, v(-81.75, -10.59) * mm, v(-82.1, -10.59) * mm]});
            skFitSpline(sketch, "E2803", {"points": [v(-82.1, -10.59) * mm, v(-82.2, -10.93) * mm, v(-82.3, -11.27) * mm, v(-82.4, -11.6) * mm]});
            skFitSpline(sketch, "E2804", {"points": [v(-82.4, -11.6) * mm, v(-82.5, -11.95) * mm, v(-82.59, -12.3) * mm, v(-82.68, -12.67) * mm]});
            skFitSpline(sketch, "E2805", {"points": [v(-82.68, -12.67) * mm, v(-82.7, -12.75) * mm, v(-82.7, -12.84) * mm, v(-82.7, -12.92) * mm]});
            skFitSpline(sketch, "E2806", {"points": [v(-82.7, -12.92) * mm, v(-82.7, -13.19) * mm, v(-82.9, -13.4) * mm, v(-83.14, -13.43) * mm]});
            skFitSpline(sketch, "E2807", {"points": [v(-83.14, -13.43) * mm, v(-83.42, -13.46) * mm, v(-83.67, -13.26) * mm, v(-83.7, -12.99) * mm]});
            skFitSpline(sketch, "E2808", {"points": [v(-83.7, -12.99) * mm, v(-83.7, -12.85) * mm, v(-83.7, -12.71) * mm, v(-83.66, -12.58) * mm]});
            skFitSpline(sketch, "E2809", {"points": [v(-83.66, -12.58) * mm, v(-83.49, -11.93) * mm, v(-83.3, -11.28) * mm, v(-83.12, -10.62) * mm]});
            skFitSpline(sketch, "E2810", {"points": [v(-83.12, -10.62) * mm, v(-83.12, -10.6) * mm, v(-83.12, -10.6) * mm, v(-83.13, -10.56) * mm]});
            skFitSpline(sketch, "E2811", {"points": [v(-83.13, -10.56) * mm, v(-83.2, -10.55) * mm, v(-83.26, -10.55) * mm, v(-83.33, -10.54) * mm]});
            skFitSpline(sketch, "E2812", {"points": [v(-83.33, -10.54) * mm, v(-83.98, -10.51) * mm, v(-84.63, -10.48) * mm, v(-85.29, -10.45) * mm]});
            skFitSpline(sketch, "E2813", {"points": [v(-85.29, -10.45) * mm, v(-85.44, -10.45) * mm, v(-85.59, -10.4) * mm, v(-85.7, -10.3) * mm]});
            skFitSpline(sketch, "E2814", {"points": [v(-85.7, -10.3) * mm, v(-85.9, -10.14) * mm, v(-85.95, -9.88) * mm, v(-85.84, -9.67) * mm]});
            skFitSpline(sketch, "E2815", {"points": [v(-85.84, -9.67) * mm, v(-85.75, -9.49) * mm, v(-85.5, -9.37) * mm, v(-85.25, -9.44) * mm]});
            skFitSpline(sketch, "E2816", {"points": [v(-85.25, -9.44) * mm, v(-85.04, -9.5) * mm, v(-84.81, -9.52) * mm, v(-84.6, -9.53) * mm]});
            skFitSpline(sketch, "E2817", {"points": [v(-84.6, -9.53) * mm, v(-84.08, -9.56) * mm, v(-83.57, -9.57) * mm, v(-83.06, -9.58) * mm]});
            skFitSpline(sketch, "E2818", {"points": [v(-83.06, -9.58) * mm, v(-82.99, -9.58) * mm, v(-82.92, -9.58) * mm, v(-82.83, -9.58) * mm]});
            skFitSpline(sketch, "E2819", {"points": [v(-82.83, -9.58) * mm, v(-82.72, -9.24) * mm, v(-82.62, -8.9) * mm, v(-82.5, -8.58) * mm]});
            skFitSpline(sketch, "E2820", {"points": [v(-82.5, -8.58) * mm, v(-82.29, -8.03) * mm, v(-82.07, -7.5) * mm, v(-81.85, -6.95) * mm]});
            skFitSpline(sketch, "E2821", {"points": [v(-81.85, -6.95) * mm, v(-81.72, -6.64) * mm, v(-81.43, -6.6) * mm, v(-81.16, -6.56) * mm]});
            skFitSpline(sketch, "E2822", {"points": [v(-81.16, -6.56) * mm, v(-80.87, -6.5) * mm, v(-80.6, -6.45) * mm, v(-80.31, -6.4) * mm]});
            skFitSpline(sketch, "E2823", {"points": [v(-80.31, -6.4) * mm, v(-79.95, -6.32) * mm, v(-79.6, -6.25) * mm, v(-79.24, -6.18) * mm]});
            skFitSpline(sketch, "E2824", {"points": [v(-79.24, -6.18) * mm, v(-79.04, -6.14) * mm, v(-78.85, -6.1) * mm, v(-78.66, -6.06) * mm]});
            skFitSpline(sketch, "E2825", {"points": [v(-78.66, -6.06) * mm, v(-78.66, -6.04) * mm, v(-78.66, -6.02) * mm, v(-78.66, -6) * mm]});
            skFitSpline(sketch, "E2826", {"points": [v(-78.66, -6) * mm, v(-78.86, -5.98) * mm, v(-79.06, -5.96) * mm, v(-79.26, -5.92) * mm]});
            skFitSpline(sketch, "E2827", {"points": [v(-79.26, -5.92) * mm, v(-79.7, -5.85) * mm, v(-80.13, -5.78) * mm, v(-80.56, -5.7) * mm]});
            skFitSpline(sketch, "E2828", {"points": [v(-80.56, -5.7) * mm, v(-81.1, -5.62) * mm, v(-81.63, -5.55) * mm, v(-82.17, -5.47) * mm]});
            skFitSpline(sketch, "E2829", {"points": [v(-82.17, -5.47) * mm, v(-82.51, -5.41) * mm, v(-82.86, -5.36) * mm, v(-83.2, -5.29) * mm]});
            skFitSpline(sketch, "E2830", {"points": [v(-83.2, -5.29) * mm, v(-83.4, -5.25) * mm, v(-83.53, -5.3) * mm, v(-83.68, -5.42) * mm]});
            skFitSpline(sketch, "E2831", {"points": [v(-83.68, -5.42) * mm, v(-84.05, -5.76) * mm, v(-84.44, -6.08) * mm, v(-84.83, -6.4) * mm]});
            skFitSpline(sketch, "E2832", {"points": [v(-84.83, -6.4) * mm, v(-85.03, -6.55) * mm, v(-85.25, -6.7) * mm, v(-85.45, -6.84) * mm]});
            skFitSpline(sketch, "E2833", {"points": [v(-85.45, -6.84) * mm, v(-85.66, -7) * mm, v(-85.92, -6.98) * mm, v(-86.1, -6.8) * mm]});
            skFitSpline(sketch, "E2834", {"points": [v(-86.1, -6.8) * mm, v(-86.27, -6.63) * mm, v(-86.3, -6.35) * mm, v(-86.12, -6.16) * mm]});
            skFitSpline(sketch, "E2835", {"points": [v(-86.12, -6.16) * mm, v(-85.95, -5.97) * mm, v(-85.74, -5.81) * mm, v(-85.54, -5.65) * mm]});
            skFitSpline(sketch, "E2836", {"points": [v(-85.54, -5.65) * mm, v(-85.15, -5.33) * mm, v(-84.74, -5.02) * mm, v(-84.34, -4.7) * mm]});
            skFitSpline(sketch, "E2837", {"points": [v(-84.34, -4.7) * mm, v(-84.31, -4.68) * mm, v(-84.3, -4.66) * mm, v(-84.26, -4.61) * mm]});
            skFitSpline(sketch, "E2838", {"points": [v(-84.26, -4.61) * mm, v(-84.3, -4.55) * mm, v(-84.35, -4.47) * mm, v(-84.4, -4.41) * mm]});
            skFitSpline(sketch, "E2839", {"points": [v(-84.4, -4.41) * mm, v(-84.67, -4.16) * mm, v(-84.93, -3.92) * mm, v(-85.2, -3.68) * mm]});
            skFitSpline(sketch, "E2840", {"points": [v(-85.2, -3.68) * mm, v(-85.35, -3.54) * mm, v(-85.53, -3.42) * mm, v(-85.67, -3.27) * mm]});
            skFitSpline(sketch, "E2841", {"points": [v(-85.67, -3.27) * mm, v(-85.87, -3.06) * mm, v(-85.86, -2.8) * mm, v(-85.67, -2.6) * mm]});
            skFitSpline(sketch, "E2842", {"points": [v(-85.67, -2.6) * mm, v(-85.5, -2.43) * mm, v(-85.2, -2.4) * mm, v(-85, -2.57) * mm]});
            skFitSpline(sketch, "E2843", {"points": [v(-85, -2.57) * mm, v(-84.57, -2.95) * mm, v(-84.1, -3.28) * mm, v(-83.73, -3.7) * mm]});
            skFitSpline(sketch, "E2844", {"points": [v(-83.73, -3.7) * mm, v(-83.67, -3.76) * mm, v(-83.62, -3.83) * mm, v(-83.58, -3.9) * mm]});
            skFitSpline(sketch, "E2845", {"points": [v(-83.58, -3.9) * mm, v(-83.5, -4) * mm, v(-83.4, -4.1) * mm, v(-83.26, -4.13) * mm]});
            skFitSpline(sketch, "E2846", {"points": [v(-83.26, -4.13) * mm, v(-83.22, -4.13) * mm, v(-83.16, -4.16) * mm, v(-83.14, -4.2) * mm]});
            skFitSpline(sketch, "E2847", {"points": [v(-83.14, -4.2) * mm, v(-83.03, -4.34) * mm, v(-82.88, -4.36) * mm, v(-82.72, -4.38) * mm]});
            skFitSpline(sketch, "E2848", {"points": [v(-82.72, -4.38) * mm, v(-82.25, -4.46) * mm, v(-81.78, -4.56) * mm, v(-81.3, -4.63) * mm]});
            skFitSpline(sketch, "E2849", {"points": [v(-81.3, -4.63) * mm, v(-80.33, -4.78) * mm, v(-79.35, -4.93) * mm, v(-78.37, -5.07) * mm]});
            skFitSpline(sketch, "E2850", {"points": [v(-78.37, -5.07) * mm, v(-77.99, -5.13) * mm, v(-77.6, -5.17) * mm, v(-77.21, -5.22) * mm]});
            skFitSpline(sketch, "E2851", {"points": [v(-77.21, -5.22) * mm, v(-77.12, -5.23) * mm, v(-77.03, -5.23) * mm, v(-76.92, -5.23) * mm]});
            skFitSpline(sketch, "E2852", {"points": [v(-76.92, -5.23) * mm, v(-76.7, -4.05) * mm, v(-76.5, -2.9) * mm, v(-76.28, -1.68) * mm]});
            skFitSpline(sketch, "E2853", {"points": [v(-76.28, -1.68) * mm, v(-76.52, -1.88) * mm, v(-76.72, -2.05) * mm, v(-76.92, -2.2) * mm]});
            skFitSpline(sketch, "E2854", {"points": [v(-76.92, -2.2) * mm, v(-77.46, -2.63) * mm, v(-78, -3.05) * mm, v(-78.53, -3.46) * mm]});
            skFitSpline(sketch, "E2855", {"points": [v(-78.53, -3.46) * mm, v(-78.8, -3.66) * mm, v(-79.07, -3.65) * mm, v(-79.3, -3.44) * mm]});
            skFitSpline(sketch, "E2856", {"points": [v(-79.3, -3.44) * mm, v(-79.54, -3.21) * mm, v(-79.78, -2.98) * mm, v(-80, -2.73) * mm]});
            skFitSpline(sketch, "E2857", {"points": [v(-80, -2.73) * mm, v(-80.33, -2.39) * mm, v(-80.62, -2.02) * mm, v(-80.93, -1.67) * mm]});
            skFitSpline(sketch, "E2858", {"points": [v(-80.93, -1.67) * mm, v(-81.06, -1.52) * mm, v(-81.19, -1.38) * mm, v(-81.34, -1.22) * mm]});
            skFitSpline(sketch, "E2859", {"points": [v(-81.34, -1.22) * mm, v(-81.55, -1.5) * mm, v(-81.76, -1.76) * mm, v(-81.98, -2.02) * mm]});
            skFitSpline(sketch, "E2860", {"points": [v(-81.98, -2.02) * mm, v(-82.17, -2.24) * mm, v(-82.37, -2.45) * mm, v(-82.58, -2.65) * mm]});
            skFitSpline(sketch, "E2861", {"points": [v(-82.58, -2.65) * mm, v(-82.84, -2.88) * mm, v(-83.2, -2.82) * mm, v(-83.36, -2.54) * mm]});
            skFitSpline(sketch, "E2862", {"points": [v(-83.36, -2.54) * mm, v(-83.5, -2.3) * mm, v(-83.4, -1.93) * mm, v(-83.16, -1.8) * mm]});
            skFitSpline(sketch, "E2863", {"points": [v(-83.16, -1.8) * mm, v(-82.98, -1.7) * mm, v(-82.86, -1.56) * mm, v(-82.73, -1.4) * mm]});
            skFitSpline(sketch, "E2864", {"points": [v(-82.73, -1.4) * mm, v(-82.5, -1.11) * mm, v(-82.27, -0.83) * mm, v(-82.03, -0.53) * mm]});
            skFitSpline(sketch, "E2865", {"points": [v(-82.03, -0.53) * mm, v(-82.08, -0.47) * mm, v(-82.13, -0.41) * mm, v(-82.18, -0.35) * mm]});
            skFitSpline(sketch, "E2866", {"points": [v(-82.18, -0.35) * mm, v(-82.37, -0.1) * mm, v(-82.57, 0.13) * mm, v(-82.77, 0.38) * mm]});
            skFitSpline(sketch, "E2867", {"points": [v(-82.77, 0.38) * mm, v(-82.87, 0.52) * mm, v(-82.99, 0.64) * mm, v(-83.15, 0.73) * mm]});
            skFitSpline(sketch, "E2868", {"points": [v(-83.15, 0.73) * mm, v(-83.4, 0.85) * mm, v(-83.49, 1.2) * mm, v(-83.38, 1.44) * mm]});
            skFitSpline(sketch, "E2869", {"points": [v(-83.38, 1.44) * mm, v(-83.24, 1.74) * mm, v(-82.87, 1.83) * mm, v(-82.6, 1.59) * mm]});
            skFitSpline(sketch, "E2870", {"points": [v(-82.6, 1.59) * mm, v(-82.38, 1.4) * mm, v(-82.18, 1.18) * mm, v(-82, 0.97) * mm]});
            skFitSpline(sketch, "E2871", {"points": [v(-82, 0.97) * mm, v(-81.8, 0.73) * mm, v(-81.6, 0.49) * mm, v(-81.4, 0.24) * mm]});
            skFitSpline(sketch, "E2872", {"points": [v(-81.4, 0.24) * mm, v(-81.38, 0.21) * mm, v(-81.35, 0.2) * mm, v(-81.32, 0.16) * mm]});
            skFitSpline(sketch, "E2873", {"points": [v(-81.32, 0.16) * mm, v(-80.87, 0.68) * mm, v(-80.43, 1.2) * mm, v(-79.98, 1.7) * mm]});
            skFitSpline(sketch, "E2874", {"points": [v(-79.98, 1.7) * mm, v(-79.76, 1.94) * mm, v(-79.52, 2.17) * mm, v(-79.28, 2.39) * mm]});
            skFitSpline(sketch, "E2875", {"points": [v(-79.28, 2.39) * mm, v(-79.09, 2.56) * mm, v(-78.86, 2.58) * mm, v(-78.64, 2.46) * mm]});
            skFitSpline(sketch, "E2876", {"points": [v(-78.64, 2.46) * mm, v(-78.59, 2.43) * mm, v(-78.54, 2.4) * mm, v(-78.5, 2.36) * mm]});
            skFitSpline(sketch, "E2877", {"points": [v(-78.5, 2.36) * mm, v(-77.82, 1.83) * mm, v(-77.14, 1.3) * mm, v(-76.46, 0.76) * mm]});
            skFitSpline(sketch, "E2878", {"points": [v(-76.46, 0.76) * mm, v(-76.41, 0.72) * mm, v(-76.37, 0.68) * mm, v(-76.28, 0.62) * mm]});
            skFitSpline(sketch, "E2879", {"points": [v(-76.28, 0.62) * mm, v(-76.5, 1.82) * mm, v(-76.7, 2.98) * mm, v(-76.92, 4.15) * mm]});
            skFitSpline(sketch, "E2880", {"points": [v(-76.92, 4.15) * mm, v(-76.97, 4.16) * mm, v(-77.02, 4.17) * mm, v(-77.06, 4.17) * mm]});
            skFitSpline(sketch, "E2881", {"points": [v(-77.06, 4.17) * mm, v(-77.85, 4.06) * mm, v(-78.63, 3.97) * mm, v(-79.4, 3.85) * mm]});
            skFitSpline(sketch, "E2882", {"points": [v(-79.4, 3.85) * mm, v(-79.93, 3.78) * mm, v(-80.45, 3.67) * mm, v(-80.97, 3.59) * mm]});
            skFitSpline(sketch, "E2883", {"points": [v(-80.97, 3.59) * mm, v(-81.54, 3.5) * mm, v(-82.12, 3.4) * mm, v(-82.69, 3.32) * mm]});
            skFitSpline(sketch, "E2884", {"points": [v(-82.69, 3.32) * mm, v(-82.85, 3.3) * mm, v(-83.02, 3.29) * mm, v(-83.13, 3.13) * mm]});
            skFitSpline(sketch, "E2885", {"points": [v(-83.13, 3.13) * mm, v(-83.15, 3.1) * mm, v(-83.2, 3.07) * mm, v(-83.23, 3.07) * mm]});
            skFitSpline(sketch, "E2886", {"points": [v(-83.23, 3.07) * mm, v(-83.43, 3.04) * mm, v(-83.51, 2.88) * mm, v(-83.63, 2.75) * mm]});
            skFitSpline(sketch, "E2887", {"points": [v(-83.63, 2.75) * mm, v(-83.9, 2.48) * mm, v(-84.16, 2.22) * mm, v(-84.44, 1.96) * mm]});
            skFitSpline(sketch, "E2888", {"points": [v(-84.44, 1.96) * mm, v(-84.6, 1.81) * mm, v(-84.78, 1.68) * mm, v(-84.95, 1.54) * mm]});
            skFitSpline(sketch, "E2889", {"points": [v(-84.95, 1.54) * mm, v(-85.24, 1.28) * mm, v(-85.64, 1.37) * mm, v(-85.78, 1.72) * mm]});
            skFitSpline(sketch, "E2890", {"points": [v(-85.78, 1.72) * mm, v(-85.85, 1.9) * mm, v(-85.8, 2.05) * mm, v(-85.69, 2.18) * mm]});
            skFitSpline(sketch, "E2891", {"points": [v(-85.69, 2.18) * mm, v(-85.58, 2.3) * mm, v(-85.45, 2.43) * mm, v(-85.32, 2.52) * mm]});
            skFitSpline(sketch, "E2892", {"points": [v(-85.32, 2.52) * mm, v(-84.95, 2.78) * mm, v(-84.63, 3.1) * mm, v(-84.34, 3.43) * mm]});
            skFitSpline(sketch, "E2893", {"points": [v(-84.34, 3.43) * mm, v(-84.31, 3.46) * mm, v(-84.3, 3.5) * mm, v(-84.26, 3.54) * mm]});
            skFitSpline(sketch, "E2894", {"points": [v(-84.26, 3.54) * mm, v(-84.3, 3.58) * mm, v(-84.32, 3.62) * mm, v(-84.35, 3.65) * mm]});
            skFitSpline(sketch, "E2895", {"points": [v(-84.35, 3.65) * mm, v(-84.76, 3.97) * mm, v(-85.17, 4.28) * mm, v(-85.58, 4.6) * mm]});
            skFitSpline(sketch, "E2896", {"points": [v(-85.58, 4.6) * mm, v(-85.74, 4.74) * mm, v(-85.9, 4.86) * mm, v(-86.05, 5.01) * mm]});
            skFitSpline(sketch, "E2897", {"points": [v(-86.05, 5.01) * mm, v(-86.13, 5.1) * mm, v(-86.2, 5.2) * mm, v(-86.22, 5.32) * mm]});
            skFitSpline(sketch, "E2898", {"points": [v(-86.22, 5.32) * mm, v(-86.27, 5.51) * mm, v(-86.17, 5.72) * mm, v(-86, 5.8) * mm]});
            skFitSpline(sketch, "E2899", {"points": [v(-86, 5.8) * mm, v(-85.82, 5.9) * mm, v(-85.63, 5.9) * mm, v(-85.46, 5.78) * mm]});
            skFitSpline(sketch, "E2900", {"points": [v(-85.46, 5.78) * mm, v(-84.82, 5.34) * mm, v(-84.22, 4.86) * mm, v(-83.66, 4.34) * mm]});
            skFitSpline(sketch, "E2901", {"points": [v(-83.66, 4.34) * mm, v(-83.52, 4.22) * mm, v(-83.4, 4.18) * mm, v(-83.2, 4.22) * mm]});
            skFitSpline(sketch, "E2902", {"points": [v(-83.2, 4.22) * mm, v(-82.65, 4.33) * mm, v(-82.1, 4.42) * mm, v(-81.54, 4.5) * mm]});
            skFitSpline(sketch, "E2903", {"points": [v(-81.54, 4.5) * mm, v(-80.65, 4.64) * mm, v(-79.75, 4.77) * mm, v(-78.86, 4.9) * mm]});
            skFitSpline(sketch, "E2904", {"points": [v(-78.86, 4.9) * mm, v(-78.8, 4.92) * mm, v(-78.73, 4.93) * mm, v(-78.65, 4.99) * mm]});
            skFitSpline(sketch, "E2905", {"points": [v(-78.65, 4.99) * mm, v(-78.97, 5.05) * mm, v(-79.28, 5.12) * mm, v(-79.6, 5.18) * mm]});
            skFitSpline(sketch, "E2906", {"points": [v(-79.6, 5.18) * mm, v(-79.9, 5.25) * mm, v(-80.21, 5.33) * mm, v(-80.52, 5.39) * mm]});
            skFitSpline(sketch, "E2907", {"points": [v(-80.52, 5.39) * mm, v(-80.8, 5.44) * mm, v(-81.07, 5.49) * mm, v(-81.35, 5.53) * mm]});
            skFitSpline(sketch, "E2908", {"points": [v(-81.35, 5.53) * mm, v(-81.6, 5.56) * mm, v(-81.78, 5.7) * mm, v(-81.87, 5.93) * mm]});
            skFitSpline(sketch, "E2909", {"points": [v(-81.87, 5.93) * mm, v(-82.08, 6.47) * mm, v(-82.3, 7.01) * mm, v(-82.5, 7.56) * mm]});
            skFitSpline(sketch, "E2910", {"points": [v(-82.5, 7.56) * mm, v(-82.62, 7.86) * mm, v(-82.72, 8.17) * mm, v(-82.82, 8.49) * mm]});
            skFitSpline(sketch, "E2911", {"points": [v(-82.82, 8.49) * mm, v(-83.2, 8.49) * mm, v(-83.57, 8.5) * mm, v(-83.93, 8.49) * mm]});
            skFitSpline(sketch, "E2912", {"points": [v(-83.93, 8.49) * mm, v(-84.22, 8.48) * mm, v(-84.5, 8.46) * mm, v(-84.8, 8.44) * mm]});
            skFitSpline(sketch, "E2913", {"points": [v(-84.8, 8.44) * mm, v(-84.94, 8.43) * mm, v(-85.1, 8.41) * mm, v(-85.24, 8.38) * mm]});
            skFitSpline(sketch, "E2914", {"points": [v(-85.24, 8.38) * mm, v(-85.56, 8.3) * mm, v(-85.83, 8.44) * mm, v(-85.89, 8.73) * mm]});
            skFitSpline(sketch, "E2915", {"points": [v(-85.89, 8.73) * mm, v(-85.95, 9.03) * mm, v(-85.73, 9.33) * mm, v(-85.42, 9.36) * mm]});
            skFitSpline(sketch, "E2916", {"points": [v(-85.42, 9.36) * mm, v(-85.15, 9.4) * mm, v(-84.9, 9.4) * mm, v(-84.63, 9.42) * mm]});
            skFitSpline(sketch, "E2917", {"points": [v(-84.63, 9.42) * mm, v(-84.15, 9.44) * mm, v(-83.67, 9.45) * mm, v(-83.2, 9.47) * mm]});
            skFitSpline(sketch, "E2918", {"points": [v(-83.2, 9.47) * mm, v(-83.17, 9.47) * mm, v(-83.15, 9.48) * mm, v(-83.13, 9.49) * mm]});
            skFitSpline(sketch, "E2919", {"points": [v(-83.13, 9.49) * mm, v(-83.12, 9.51) * mm, v(-83.12, 9.54) * mm, v(-83.12, 9.56) * mm]});
            skFitSpline(sketch, "E2920", {"points": [v(-83.12, 9.56) * mm, v(-83.3, 10.2) * mm, v(-83.48, 10.85) * mm, v(-83.66, 11.5) * mm]});
            skFitSpline(sketch, "E2921", {"points": [v(-83.66, 11.5) * mm, v(-83.7, 11.63) * mm, v(-83.7, 11.78) * mm, v(-83.7, 11.92) * mm]});
            skFitSpline(sketch, "E2922", {"points": [v(-83.7, 11.92) * mm, v(-83.68, 12.18) * mm, v(-83.44, 12.38) * mm, v(-83.19, 12.37) * mm]});
            skFitSpline(sketch, "E2923", {"points": [v(-83.19, 12.37) * mm, v(-82.95, 12.37) * mm, v(-82.7, 12.17) * mm, v(-82.7, 11.92) * mm]});
            skFitSpline(sketch, "E2924", {"points": [v(-82.7, 11.92) * mm, v(-82.71, 11.69) * mm, v(-82.65, 11.48) * mm, v(-82.6, 11.27) * mm]});
            skFitSpline(sketch, "E2925", {"points": [v(-82.6, 11.27) * mm, v(-82.44, 10.69) * mm, v(-82.27, 10.11) * mm, v(-82.1, 9.52) * mm]});
            skFitSpline(sketch, "E2926", {"points": [v(-82.1, 9.52) * mm, v(-81.78, 9.51) * mm, v(-81.47, 9.5) * mm, v(-81.16, 9.5) * mm]});
            skFitSpline(sketch, "E2927", {"points": [v(-81.16, 9.5) * mm, v(-80.52, 9.53) * mm, v(-79.89, 9.47) * mm, v(-79.25, 9.4) * mm]});
            skFitSpline(sketch, "E2928", {"points": [v(-79.25, 9.4) * mm, v(-79.09, 9.37) * mm, v(-78.95, 9.29) * mm, v(-78.86, 9.14) * mm]});
            skFitSpline(sketch, "E2929", {"points": [v(-78.86, 9.14) * mm, v(-78.78, 9) * mm, v(-78.71, 8.86) * mm, v(-78.64, 8.72) * mm]});
            skFitSpline(sketch, "E2930", {"points": [v(-78.64, 8.72) * mm, v(-78.6, 8.63) * mm, v(-78.55, 8.53) * mm, v(-78.5, 8.44) * mm]});
            skFitSpline(sketch, "E2931", {"points": [v(-78.5, 8.44) * mm, v(-78.19, 7.9) * mm, v(-77.87, 7.37) * mm, v(-77.56, 6.83) * mm]});
            skFitSpline(sketch, "E2932", {"points": [v(-77.56, 6.83) * mm, v(-77.52, 6.77) * mm, v(-77.48, 6.71) * mm, v(-77.4, 6.67) * mm]});
            skFitSpline(sketch, "E2933", {"points": [v(-77.4, 6.67) * mm, v(-77.44, 6.83) * mm, v(-77.47, 6.99) * mm, v(-77.5, 7.15) * mm]});
            skFitSpline(sketch, "E2934", {"points": [v(-77.5, 7.15) * mm, v(-77.58, 7.66) * mm, v(-77.65, 8.17) * mm, v(-77.73, 8.68) * mm]});
            skFitSpline(sketch, "E2935", {"points": [v(-77.73, 8.68) * mm, v(-77.82, 9.24) * mm, v(-77.91, 9.79) * mm, v(-78, 10.34) * mm]});
            skFitSpline(sketch, "E2936", {"points": [v(-78, 10.34) * mm, v(-78.05, 10.64) * mm, v(-78.1, 10.95) * mm, v(-78.14, 11.26) * mm]});
            skFitSpline(sketch, "E2937", {"points": [v(-78.14, 11.26) * mm, v(-78.15, 11.4) * mm, v(-78.22, 11.5) * mm, v(-78.35, 11.58) * mm]});
            skFitSpline(sketch, "E2938", {"points": [v(-78.35, 11.58) * mm, v(-78.8, 11.85) * mm, v(-79.25, 12.13) * mm, v(-79.69, 12.42) * mm]});
            skFitSpline(sketch, "E2939", {"points": [v(-79.69, 12.42) * mm, v(-79.89, 12.55) * mm, v(-80.07, 12.7) * mm, v(-80.27, 12.84) * mm]});
            skFitSpline(sketch, "E2940", {"points": [v(-80.27, 12.84) * mm, v(-80.5, 13) * mm, v(-80.58, 13.26) * mm, v(-80.46, 13.49) * mm]});
            skFitSpline(sketch, "E2941", {"points": [v(-80.46, 13.49) * mm, v(-80.35, 13.72) * mm, v(-80.06, 13.82) * mm, v(-79.8, 13.69) * mm]});
            skFitSpline(sketch, "E2942", {"points": [v(-79.8, 13.69) * mm, v(-79.59, 13.58) * mm, v(-79.4, 13.45) * mm, v(-79.2, 13.31) * mm]});
            skFitSpline(sketch, "E2943", {"points": [v(-79.2, 13.31) * mm, v(-78.76, 13.03) * mm, v(-78.34, 12.75) * mm, v(-77.92, 12.46) * mm]});
            skFitSpline(sketch, "E2944", {"points": [v(-77.92, 12.46) * mm, v(-77.89, 12.45) * mm, v(-77.86, 12.44) * mm, v(-77.81, 12.42) * mm]});
            skFitSpline(sketch, "E2945", {"points": [v(-77.81, 12.42) * mm, v(-77.75, 12.5) * mm, v(-77.68, 12.58) * mm, v(-77.64, 12.67) * mm]});
            skFitSpline(sketch, "E2946", {"points": [v(-77.64, 12.67) * mm, v(-77.45, 13.03) * mm, v(-77.26, 13.38) * mm, v(-77.16, 13.77) * mm]});
            skFitSpline(sketch, "E2947", {"points": [v(-77.16, 13.77) * mm, v(-77.12, 13.91) * mm, v(-77.05, 14.05) * mm, v(-76.97, 14.18) * mm]});
            skFitSpline(sketch, "E2948", {"points": [v(-76.97, 14.18) * mm, v(-76.83, 14.42) * mm, v(-76.57, 14.5) * mm, v(-76.33, 14.37) * mm]});
            skFitSpline(sketch, "E2949", {"points": [v(-76.33, 14.37) * mm, v(-76.1, 14.26) * mm, v(-76, 13.99) * mm, v(-76.1, 13.74) * mm]});
            skFitSpline(sketch, "E2950", {"points": [v(-76.1, 13.74) * mm, v(-76.32, 13.24) * mm, v(-76.48, 12.7) * mm, v(-76.76, 12.23) * mm]});
            skFitSpline(sketch, "E2951", {"points": [v(-76.76, 12.23) * mm, v(-76.8, 12.16) * mm, v(-76.84, 12.1) * mm, v(-76.9, 12.03) * mm]});
            skFitSpline(sketch, "E2952", {"points": [v(-76.9, 12.03) * mm, v(-76.98, 11.9) * mm, v(-77.06, 11.78) * mm, v(-77.04, 11.61) * mm]});
            skFitSpline(sketch, "E2953", {"points": [v(-77.04, 11.61) * mm, v(-77.03, 11.57) * mm, v(-77.04, 11.5) * mm, v(-77.07, 11.47) * mm]});
            skFitSpline(sketch, "E2954", {"points": [v(-77.07, 11.47) * mm, v(-77.18, 11.33) * mm, v(-77.14, 11.17) * mm, v(-77.12, 11.02) * mm]});
            skFitSpline(sketch, "E2955", {"points": [v(-77.12, 11.02) * mm, v(-77, 10.29) * mm, v(-76.88, 9.55) * mm, v(-76.77, 8.82) * mm]});
            skFitSpline(sketch, "E2956", {"points": [v(-76.77, 8.82) * mm, v(-76.66, 8.17) * mm, v(-76.57, 7.51) * mm, v(-76.45, 6.86) * mm]});
            skFitSpline(sketch, "E2957", {"points": [v(-76.45, 6.86) * mm, v(-76.36, 6.33) * mm, v(-76.25, 5.8) * mm, v(-76.14, 5.25) * mm]});
            skFitSpline(sketch, "E2958", {"points": [v(-76.14, 5.25) * mm, v(-74.96, 5.4) * mm, v(-73.79, 5.57) * mm, v(-72.57, 5.73) * mm]});
            skFitSpline(sketch, "E2959", {"points": [v(-72.57, 5.73) * mm, v(-72.66, 5.8) * mm, v(-72.72, 5.83) * mm, v(-72.77, 5.87) * mm]});
            skFitSpline(sketch, "E2960", {"points": [v(-72.77, 5.87) * mm, v(-73.48, 6.35) * mm, v(-74.2, 6.83) * mm, v(-74.9, 7.3) * mm]});
            skFitSpline(sketch, "E2961", {"points": [v(-74.9, 7.3) * mm, v(-75.26, 7.52) * mm, v(-75.29, 7.89) * mm, v(-75.1, 8.19) * mm]});
            skFitSpline(sketch, "E2962", {"points": [v(-75.1, 8.19) * mm, v(-75.03, 8.3) * mm, v(-74.98, 8.43) * mm, v(-74.92, 8.55) * mm]});
            skFitSpline(sketch, "E2963", {"points": [v(-74.92, 8.55) * mm, v(-74.76, 8.84) * mm, v(-74.6, 9.14) * mm, v(-74.43, 9.43) * mm]});
            skFitSpline(sketch, "E2964", {"points": [v(-74.43, 9.43) * mm, v(-74.2, 9.84) * mm, v(-73.95, 10.24) * mm, v(-73.7, 10.66) * mm]});
            skFitSpline(sketch, "E2965", {"points": [v(-73.7, 10.66) * mm, v(-73.73, 10.68) * mm, v(-73.77, 10.71) * mm, v(-73.81, 10.73) * mm]});
            skFitSpline(sketch, "E2966", {"points": [v(-73.81, 10.73) * mm, v(-74.1, 10.85) * mm, v(-74.4, 10.95) * mm, v(-74.68, 11.07) * mm]});
            skFitSpline(sketch, "E2967", {"points": [v(-74.68, 11.07) * mm, v(-74.93, 11.17) * mm, v(-75.18, 11.3) * mm, v(-75.42, 11.42) * mm]});
            skFitSpline(sketch, "E2968", {"points": [v(-75.42, 11.42) * mm, v(-75.56, 11.5) * mm, v(-75.66, 11.63) * mm, v(-75.69, 11.8) * mm]});
            skFitSpline(sketch, "E2969", {"points": [v(-75.69, 11.8) * mm, v(-75.71, 12) * mm, v(-75.63, 12.2) * mm, v(-75.46, 12.29) * mm]});
            skFitSpline(sketch, "E2970", {"points": [v(-75.46, 12.29) * mm, v(-75.26, 12.4) * mm, v(-74.98, 12.43) * mm, v(-74.8, 12.25) * mm]});
            skFitSpline(sketch, "E2971", {"points": [v(-74.8, 12.25) * mm, v(-74.66, 12.1) * mm, v(-74.47, 12.02) * mm, v(-74.27, 11.95) * mm]});
            skFitSpline(sketch, "E2972", {"points": [v(-74.27, 11.95) * mm, v(-73.93, 11.83) * mm, v(-73.6, 11.7) * mm, v(-73.25, 11.56) * mm]});
            skFitSpline(sketch, "E2973", {"points": [v(-73.25, 11.56) * mm, v(-73.22, 11.6) * mm, v(-73.18, 11.66) * mm, v(-73.14, 11.7) * mm]});
            skFitSpline(sketch, "E2974", {"points": [v(-73.14, 11.7) * mm, v(-72.96, 12) * mm, v(-72.76, 12.28) * mm, v(-72.58, 12.57) * mm]});
            skFitSpline(sketch, "E2975", {"points": [v(-72.58, 12.57) * mm, v(-72.5, 12.7) * mm, v(-72.45, 12.84) * mm, v(-72.4, 12.99) * mm]});
            skFitSpline(sketch, "E2976", {"points": [v(-72.4, 12.99) * mm, v(-72.36, 13.15) * mm, v(-72.29, 13.28) * mm, v(-72.14, 13.36) * mm]});
            skFitSpline(sketch, "E2977", {"points": [v(-72.14, 13.36) * mm, v(-71.92, 13.48) * mm, v(-71.7, 13.48) * mm, v(-71.53, 13.34) * mm]});
            skFitSpline(sketch, "E2978", {"points": [v(-71.53, 13.34) * mm, v(-71.36, 13.2) * mm, v(-71.3, 12.98) * mm, v(-71.4, 12.75) * mm]});
            skFitSpline(sketch, "E2979", {"points": [v(-71.4, 12.75) * mm, v(-71.52, 12.49) * mm, v(-71.66, 12.23) * mm, v(-71.81, 11.97) * mm]});
            skFitSpline(sketch, "E2980", {"points": [v(-71.81, 11.97) * mm, v(-72, 11.68) * mm, v(-72.19, 11.4) * mm, v(-72.38, 11.1) * mm]});
            skFitSpline(sketch, "E2981", {"points": [v(-72.38, 11.1) * mm, v(-72, 10.95) * mm, v(-71.65, 10.8) * mm, v(-71.3, 10.65) * mm]});
            skFitSpline(sketch, "E2982", {"points": [v(-71.3, 10.65) * mm, v(-70.85, 10.45) * mm, v(-70.38, 10.3) * mm, v(-69.97, 10) * mm]});
            skFitSpline(sketch, "E2983", {"points": [v(-69.97, 10) * mm, v(-69.92, 9.97) * mm, v(-69.85, 9.96) * mm, v(-69.8, 9.93) * mm]});
            skFitSpline(sketch, "E2984", {"points": [v(-69.8, 9.93) * mm, v(-69.37, 9.76) * mm, v(-69.25, 9.5) * mm, v(-69.4, 9.07) * mm]});
            skFitSpline(sketch, "E2985", {"points": [v(-69.4, 9.07) * mm, v(-69.7, 8.27) * mm, v(-70, 7.47) * mm, v(-70.29, 6.67) * mm]});
            skFitSpline(sketch, "E2986", {"points": [v(-70.29, 6.67) * mm, v(-70.31, 6.61) * mm, v(-70.33, 6.55) * mm, v(-70.37, 6.44) * mm]});
            skFitSpline(sketch, "E2987", {"points": [v(-70.37, 6.44) * mm, v(-69.3, 7.03) * mm, v(-68.26, 7.58) * mm, v(-67.2, 8.15) * mm]});
            skFitSpline(sketch, "E2988", {"points": [v(-67.2, 8.15) * mm, v(-67.24, 8.27) * mm, v(-67.29, 8.38) * mm, v(-67.34, 8.48) * mm]});
            skFitSpline(sketch, "E2989", {"points": [v(-67.34, 8.48) * mm, v(-67.83, 9.5) * mm, v(-68.28, 10.53) * mm, v(-68.83, 11.5) * mm]});
            skFitSpline(sketch, "E2990", {"points": [v(-68.83, 11.5) * mm, v(-69.01, 11.82) * mm, v(-69.15, 12.15) * mm, v(-69.31, 12.47) * mm]});
            skFitSpline(sketch, "E2991", {"points": [v(-69.31, 12.47) * mm, v(-69.5, 12.82) * mm, v(-69.68, 13.17) * mm, v(-69.85, 13.52) * mm]});
            skFitSpline(sketch, "E2992", {"points": [v(-69.85, 13.52) * mm, v(-69.9, 13.6) * mm, v(-69.95, 13.67) * mm, v(-70.05, 13.71) * mm]});
            skFitSpline(sketch, "E2993", {"points": [v(-70.05, 13.71) * mm, v(-70.1, 13.73) * mm, v(-70.17, 13.78) * mm, v(-70.2, 13.83) * mm]});
            skFitSpline(sketch, "E2994", {"points": [v(-70.2, 13.83) * mm, v(-70.28, 13.97) * mm, v(-70.42, 14.01) * mm, v(-70.56, 14.08) * mm]});
            skFitSpline(sketch, "E2995", {"points": [v(-70.56, 14.08) * mm, v(-70.93, 14.26) * mm, v(-71.3, 14.46) * mm, v(-71.66, 14.66) * mm]});
            skFitSpline(sketch, "E2996", {"points": [v(-71.66, 14.66) * mm, v(-71.83, 14.75) * mm, v(-72, 14.87) * mm, v(-72.17, 14.97) * mm]});
            skFitSpline(sketch, "E2997", {"points": [v(-72.17, 14.97) * mm, v(-72.36, 15.09) * mm, v(-72.48, 15.3) * mm, v(-72.46, 15.48) * mm]});
            skFitSpline(sketch, "E2998", {"points": [v(-72.46, 15.48) * mm, v(-72.42, 15.7) * mm, v(-72.27, 15.88) * mm, v(-72.06, 15.9) * mm]});
            skFitSpline(sketch, "E2999", {"points": [v(-72.06, 15.9) * mm, v(-71.96, 15.92) * mm, v(-71.84, 15.9) * mm, v(-71.76, 15.86) * mm]});
            skFitSpline(sketch, "E3000", {"points": [v(-71.76, 15.86) * mm, v(-71.6, 15.8) * mm, v(-71.46, 15.71) * mm, v(-71.33, 15.6) * mm]});
            skFitSpline(sketch, "E3001", {"points": [v(-71.33, 15.6) * mm, v(-71.02, 15.37) * mm, v(-70.67, 15.2) * mm, v(-70.33, 15.03) * mm]});
            skFitSpline(sketch, "E3002", {"points": [v(-70.33, 15.03) * mm, v(-70.25, 14.99) * mm, v(-70.15, 14.97) * mm, v(-70.04, 14.93) * mm]});
            skFitSpline(sketch, "E3003", {"points": [v(-70.04, 14.93) * mm, v(-69.9, 15.3) * mm, v(-69.75, 15.65) * mm, v(-69.62, 16) * mm]});
            skFitSpline(sketch, "E3004", {"points": [v(-69.62, 16) * mm, v(-69.52, 16.28) * mm, v(-69.44, 16.55) * mm, v(-69.34, 16.82) * mm]});
            skFitSpline(sketch, "E3005", {"points": [v(-69.34, 16.82) * mm, v(-69.3, 16.93) * mm, v(-69.26, 17.03) * mm, v(-69.2, 17.13) * mm]});
            skFitSpline(sketch, "E3006", {"points": [v(-69.2, 17.13) * mm, v(-69.06, 17.38) * mm, v(-68.8, 17.48) * mm, v(-68.55, 17.37) * mm]});
            skFitSpline(sketch, "E3007", {"points": [v(-68.55, 17.37) * mm, v(-68.32, 17.26) * mm, v(-68.23, 17.01) * mm, v(-68.31, 16.73) * mm]});
            skFitSpline(sketch, "E3008", {"points": [v(-68.31, 16.73) * mm, v(-68.52, 16.02) * mm, v(-68.78, 15.33) * mm, v(-69.1, 14.65) * mm]});
            skFitSpline(sketch, "E3009", {"points": [v(-69.1, 14.65) * mm, v(-69.18, 14.47) * mm, v(-69.18, 14.32) * mm, v(-69.08, 14.14) * mm]});
            skFitSpline(sketch, "E3010", {"points": [v(-69.08, 14.14) * mm, v(-68.8, 13.64) * mm, v(-68.54, 13.13) * mm, v(-68.28, 12.61) * mm]});
            skFitSpline(sketch, "E3011", {"points": [v(-68.28, 12.61) * mm, v(-67.86, 11.79) * mm, v(-67.45, 10.96) * mm, v(-67.04, 10.13) * mm]});
            skFitSpline(sketch, "E3012", {"points": [v(-67.04, 10.13) * mm, v(-67.03, 10.1) * mm, v(-67, 10.07) * mm, v(-66.97, 10) * mm]});
            skFitSpline(sketch, "E3013", {"points": [v(-66.97, 10) * mm, v(-66.97, 10.12) * mm, v(-66.96, 10.2) * mm, v(-66.97, 10.28) * mm]});
            skFitSpline(sketch, "E3014", {"points": [v(-66.97, 10.28) * mm, v(-67.02, 10.7) * mm, v(-67.08, 11.1) * mm, v(-67.13, 11.51) * mm]});
            skFitSpline(sketch, "E3015", {"points": [v(-67.13, 11.51) * mm, v(-67.15, 11.66) * mm, v(-67.12, 11.8) * mm, v(-67.14, 11.94) * mm]});
            skFitSpline(sketch, "E3016", {"points": [v(-67.14, 11.94) * mm, v(-67.18, 12.22) * mm, v(-67.22, 12.5) * mm, v(-67.27, 12.77) * mm]});
            skFitSpline(sketch, "E3017", {"points": [v(-67.27, 12.77) * mm, v(-67.31, 13.02) * mm, v(-67.25, 13.23) * mm, v(-67.06, 13.4) * mm]});
            skFitSpline(sketch, "E3018", {"points": [v(-67.06, 13.4) * mm, v(-66.63, 13.75) * mm, v(-66.2, 14.12) * mm, v(-65.76, 14.46) * mm]});
            skFitSpline(sketch, "E3019", {"points": [v(-65.76, 14.46) * mm, v(-65.49, 14.69) * mm, v(-65.19, 14.9) * mm, v(-64.89, 15.11) * mm]});
            skFitSpline(sketch, "E3020", {"points": [v(-64.89, 15.11) * mm, v(-65, 15.45) * mm, v(-65.12, 15.78) * mm, v(-65.24, 16.1) * mm]});
            skFitSpline(sketch, "E3021", {"points": [v(-65.24, 16.1) * mm, v(-65.36, 16.43) * mm, v(-65.5, 16.77) * mm, v(-65.62, 17.1) * mm]});
            skFitSpline(sketch, "E3022", {"points": [v(-65.62, 17.1) * mm, v(-65.67, 17.2) * mm, v(-65.72, 17.3) * mm, v(-65.78, 17.4) * mm]});
            skFitSpline(sketch, "E3023", {"points": [v(-65.78, 17.4) * mm, v(-65.9, 17.6) * mm, v(-65.89, 17.85) * mm, v(-65.73, 18.01) * mm]});
            skFitSpline(sketch, "E3024", {"points": [v(-65.73, 18.01) * mm, v(-65.56, 18.18) * mm, v(-65.28, 18.2) * mm, v(-65.08, 18.07) * mm]});
            skFitSpline(sketch, "E3025", {"points": [v(-65.08, 18.07) * mm, v(-64.91, 17.96) * mm, v(-64.84, 17.78) * mm, v(-64.77, 17.6) * mm]});
            skFitSpline(sketch, "E3026", {"points": [v(-64.77, 17.6) * mm, v(-64.53, 16.97) * mm, v(-64.28, 16.34) * mm, v(-64.04, 15.7) * mm]});
            skFitSpline(sketch, "E3027", {"points": [v(-64.04, 15.7) * mm, v(-64.02, 15.7) * mm, v(-64, 15.71) * mm, v(-63.97, 15.73) * mm]});
            skFitSpline(sketch, "E3028", {"points": [v(-63.97, 15.73) * mm, v(-63.5, 16.03) * mm, v(-63.05, 16.34) * mm, v(-62.6, 16.64) * mm]});
            skFitSpline(sketch, "E3029", {"points": [v(-62.6, 16.64) * mm, v(-62.45, 16.74) * mm, v(-62.3, 16.82) * mm, v(-62.16, 16.91) * mm]});
            skFitSpline(sketch, "E3030", {"points": [v(-62.16, 16.91) * mm, v(-62.04, 17) * mm, v(-61.9, 17) * mm, v(-61.75, 17) * mm]});
            skFitSpline(sketch, "E3031", {"points": [v(-61.75, 17) * mm, v(-61.52, 16.97) * mm, v(-61.34, 16.79) * mm, v(-61.3, 16.55) * mm]});
            skFitSpline(sketch, "E3032", {"points": [v(-61.3, 16.55) * mm, v(-61.28, 16.36) * mm, v(-61.41, 16.15) * mm, v(-61.61, 16.06) * mm]});
            skFitSpline(sketch, "E3033", {"points": [v(-61.61, 16.06) * mm, v(-61.76, 15.99) * mm, v(-61.92, 15.92) * mm, v(-62.05, 15.83) * mm]});
            skFitSpline(sketch, "E3034", {"points": [v(-62.05, 15.83) * mm, v(-62.6, 15.47) * mm, v(-63.15, 15.1) * mm, v(-63.7, 14.74) * mm]});
            skFitSpline(sketch, "E3035", {"points": [v(-63.7, 14.74) * mm, v(-63.62, 14.47) * mm, v(-63.55, 14.22) * mm, v(-63.47, 13.99) * mm]});
            skFitSpline(sketch, "E3036", {"points": [v(-63.47, 13.99) * mm, v(-63.27, 13.44) * mm, v(-63.14, 12.89) * mm, v(-63, 12.33) * mm]});
            skFitSpline(sketch, "E3037", {"points": [v(-63, 12.33) * mm, v(-62.98, 12.2) * mm, v(-62.93, 12.07) * mm, v(-62.94, 11.95) * mm]});
            skFitSpline(sketch, "E3038", {"points": [v(-62.94, 11.95) * mm, v(-62.95, 11.82) * mm, v(-62.98, 11.68) * mm, v(-63.05, 11.57) * mm]});
            skFitSpline(sketch, "E3039", {"points": [v(-63.05, 11.57) * mm, v(-63.13, 11.44) * mm, v(-63.25, 11.33) * mm, v(-63.37, 11.21) * mm]});
            skFitSpline(sketch, "E3040", {"points": [v(-63.37, 11.21) * mm, v(-63.44, 11.14) * mm, v(-63.53, 11.07) * mm, v(-63.6, 10.99) * mm]});
            skFitSpline(sketch, "E3041", {"points": [v(-63.6, 10.99) * mm, v(-64.03, 10.52) * mm, v(-64.44, 10.06) * mm, v(-64.85, 9.6) * mm]});
            skFitSpline(sketch, "E3042", {"points": [v(-64.85, 9.6) * mm, v(-64.9, 9.54) * mm, v(-64.94, 9.49) * mm, v(-64.96, 9.4) * mm]});
            skFitSpline(sketch, "E3043", {"points": [v(-64.96, 9.4) * mm, v(-64.92, 9.42) * mm, v(-64.88, 9.44) * mm, v(-64.84, 9.46) * mm]});
            skFitSpline(sketch, "E3044", {"points": [v(-64.84, 9.46) * mm, v(-64.22, 9.77) * mm, v(-63.6, 10.08) * mm, v(-63, 10.39) * mm]});
            skFitSpline(sketch, "E3045", {"points": [v(-63, 10.39) * mm, v(-62.74, 10.52) * mm, v(-62.48, 10.67) * mm, v(-62.22, 10.8) * mm]});
            skFitSpline(sketch, "E3046", {"points": [v(-62.22, 10.8) * mm, v(-61.74, 11.05) * mm, v(-61.26, 11.3) * mm, v(-60.78, 11.52) * mm]});
            skFitSpline(sketch, "E3047", {"points": [v(-60.78, 11.52) * mm, v(-60.64, 11.59) * mm, v(-60.6, 11.7) * mm, v(-60.58, 11.82) * mm]});
            skFitSpline(sketch, "E3048", {"points": [v(-60.58, 11.82) * mm, v(-60.47, 12.3) * mm, v(-60.36, 12.77) * mm, v(-60.23, 13.24) * mm]});
            skFitSpline(sketch, "E3049", {"points": [v(-60.23, 13.24) * mm, v(-60.16, 13.52) * mm, v(-60.06, 13.79) * mm, v(-59.97, 14.06) * mm]});
            skFitSpline(sketch, "E3050", {"points": [v(-59.97, 14.06) * mm, v(-59.88, 14.3) * mm, v(-59.67, 14.44) * mm, v(-59.43, 14.4) * mm]});
            skFitSpline(sketch, "E3051", {"points": [v(-59.43, 14.4) * mm, v(-59.19, 14.36) * mm, v(-59.01, 14.17) * mm, v(-59.03, 13.9) * mm]});
            skFitSpline(sketch, "E3052", {"points": [v(-59.03, 13.9) * mm, v(-59.06, 13.66) * mm, v(-59.12, 13.42) * mm, v(-59.18, 13.18) * mm]});
            skFitSpline(sketch, "E3053", {"points": [v(-59.18, 13.18) * mm, v(-59.31, 12.7) * mm, v(-59.46, 12.2) * mm, v(-59.6, 11.71) * mm]});
            skFitSpline(sketch, "E3054", {"points": [v(-59.6, 11.71) * mm, v(-59.62, 11.67) * mm, v(-59.61, 11.62) * mm, v(-59.62, 11.56) * mm]});
            skFitSpline(sketch, "E3055", {"points": [v(-59.62, 11.56) * mm, v(-59.38, 11.43) * mm, v(-59.11, 11.42) * mm, v(-58.86, 11.39) * mm]});
            skFitSpline(sketch, "E3056", {"points": [v(-58.86, 11.39) * mm, v(-58.59, 11.35) * mm, v(-58.32, 11.35) * mm, v(-58.04, 11.33) * mm]});
            skFitSpline(sketch, "E3057", {"points": [v(-58.04, 11.33) * mm, v(-57.92, 11.33) * mm, v(-57.79, 11.32) * mm, v(-57.67, 11.29) * mm]});
            skFitSpline(sketch, "E3058", {"points": [v(-57.67, 11.29) * mm, v(-57.4, 11.22) * mm, v(-57.27, 11) * mm, v(-57.3, 10.75) * mm]});
            skFitSpline(sketch, "E3059", {"points": [v(-57.3, 10.75) * mm, v(-57.34, 10.52) * mm, v(-57.54, 10.33) * mm, v(-57.79, 10.33) * mm]});
            skFitSpline(sketch, "E3060", {"points": [v(-57.79, 10.33) * mm, v(-57.92, 10.33) * mm, v(-58.06, 10.38) * mm, v(-58.2, 10.37) * mm]});
            skFitSpline(sketch, "E3061", {"points": [v(-58.2, 10.37) * mm, v(-58.63, 10.35) * mm, v(-59.07, 10.43) * mm, v(-59.5, 10.5) * mm]});
            skFitSpline(sketch, "E3062", {"points": [v(-59.5, 10.5) * mm, v(-59.58, 10.52) * mm, v(-59.67, 10.54) * mm, v(-59.75, 10.57) * mm]});
            skFitSpline(sketch, "E3063", {"points": [v(-59.75, 10.57) * mm, v(-59.88, 10.6) * mm, v(-60, 10.64) * mm, v(-60.13, 10.57) * mm]});
            skFitSpline(sketch, "E3064", {"points": [v(-60.13, 10.57) * mm, v(-60.17, 10.55) * mm, v(-60.22, 10.54) * mm, v(-60.27, 10.56) * mm]});
            skFitSpline(sketch, "E3065", {"points": [v(-60.27, 10.56) * mm, v(-60.47, 10.61) * mm, v(-60.64, 10.5) * mm, v(-60.8, 10.42) * mm]});
            skFitSpline(sketch, "E3066", {"points": [v(-60.8, 10.42) * mm, v(-61.14, 10.25) * mm, v(-61.49, 10.1) * mm, v(-61.81, 9.92) * mm]});
            skFitSpline(sketch, "E3067", {"points": [v(-61.81, 9.92) * mm, v(-62.84, 9.34) * mm, v(-63.95, 8.9) * mm, v(-64.95, 8.27) * mm]});
            skFitSpline(sketch, "E3068", {"points": [v(-64.95, 8.27) * mm, v(-65.23, 8.1) * mm, v(-65.53, 7.96) * mm, v(-65.82, 7.8) * mm]});
            skFitSpline(sketch, "E3069", {"points": [v(-65.82, 7.8) * mm, v(-65.85, 7.8) * mm, v(-65.87, 7.77) * mm, v(-65.92, 7.73) * mm]});
            skFitSpline(sketch, "E3070", {"points": [v(-65.92, 7.73) * mm, v(-65.4, 6.67) * mm, v(-64.9, 5.61) * mm, v(-64.37, 4.52) * mm]});
            skFitSpline(sketch, "E3071", {"points": [v(-64.37, 4.52) * mm, v(-64.34, 4.58) * mm, v(-64.32, 4.62) * mm, v(-64.3, 4.66) * mm]});
            skFitSpline(sketch, "E3072", {"points": [v(-64.3, 4.66) * mm, v(-64.07, 5.49) * mm, v(-63.84, 6.32) * mm, v(-63.6, 7.15) * mm]});
            skFitSpline(sketch, "E3073", {"points": [v(-63.6, 7.15) * mm, v(-63.6, 7.2) * mm, v(-63.58, 7.25) * mm, v(-63.56, 7.3) * mm]});
            skFitSpline(sketch, "E3074", {"points": [v(-63.56, 7.3) * mm, v(-63.45, 7.59) * mm, v(-63.24, 7.72) * mm, v(-62.94, 7.68) * mm]});
            skFitSpline(sketch, "E3075", {"points": [v(-62.94, 7.68) * mm, v(-62.16, 7.57) * mm, v(-61.38, 7.43) * mm, v(-60.62, 7.22) * mm]});
            skFitSpline(sketch, "E3076", {"points": [v(-60.62, 7.22) * mm, v(-60.43, 7.17) * mm, v(-60.23, 7.14) * mm, v(-60.01, 7.09) * mm]});
            skFitSpline(sketch, "E3077", {"points": [v(-60.01, 7.09) * mm, v(-60, 7.23) * mm, v(-59.97, 7.38) * mm, v(-59.96, 7.52) * mm]});
            skFitSpline(sketch, "E3078", {"points": [v(-59.96, 7.52) * mm, v(-59.95, 7.7) * mm, v(-59.95, 7.87) * mm, v(-59.94, 8.05) * mm]});
            skFitSpline(sketch, "E3079", {"points": [v(-59.94, 8.05) * mm, v(-59.91, 8.34) * mm, v(-59.88, 8.63) * mm, v(-59.84, 8.93) * mm]});
            skFitSpline(sketch, "E3080", {"points": [v(-59.84, 8.93) * mm, v(-59.83, 9) * mm, v(-59.79, 9.1) * mm, v(-59.74, 9.17) * mm]});
            skFitSpline(sketch, "E3081", {"points": [v(-59.74, 9.17) * mm, v(-59.55, 9.47) * mm, v(-59.14, 9.47) * mm, v(-58.94, 9.18) * mm]});
            skFitSpline(sketch, "E3082", {"points": [v(-58.94, 9.18) * mm, v(-58.8, 8.99) * mm, v(-58.76, 8.8) * mm, v(-58.88, 8.57) * mm]});
            skFitSpline(sketch, "E3083", {"points": [v(-58.88, 8.57) * mm, v(-58.93, 8.47) * mm, v(-58.97, 8.34) * mm, v(-58.97, 8.23) * mm]});
            skFitSpline(sketch, "E3084", {"points": [v(-58.97, 8.23) * mm, v(-59, 7.8) * mm, v(-59, 7.38) * mm, v(-59.02, 6.94) * mm]});
            skFitSpline(sketch, "E3085", {"points": [v(-59.02, 6.94) * mm, v(-58.82, 6.88) * mm, v(-58.6, 6.83) * mm, v(-58.4, 6.77) * mm]});
            skFitSpline(sketch, "E3086", {"points": [v(-58.4, 6.77) * mm, v(-58.22, 6.73) * mm, v(-58.06, 6.67) * mm, v(-57.88, 6.63) * mm]});
            skFitSpline(sketch, "E3087", {"points": [v(-57.88, 6.63) * mm, v(-57.72, 6.6) * mm, v(-57.56, 6.58) * mm, v(-57.4, 6.58) * mm]});
            skFitSpline(sketch, "E3088", {"points": [v(-57.4, 6.58) * mm, v(-57.14, 6.6) * mm, v(-56.9, 6.45) * mm, v(-56.8, 6.22) * mm]});
            skFitSpline(sketch, "E3089", {"points": [v(-56.8, 6.22) * mm, v(-56.68, 5.9) * mm, v(-56.89, 5.58) * mm, v(-57.22, 5.56) * mm]});
            skFitSpline(sketch, "E3090", {"points": [v(-57.22, 5.56) * mm, v(-57.54, 5.55) * mm, v(-57.86, 5.6) * mm, v(-58.16, 5.7) * mm]});
            skFitSpline(sketch, "E3091", {"points": [v(-58.16, 5.7) * mm, v(-58.47, 5.79) * mm, v(-58.78, 5.87) * mm, v(-59.09, 5.95) * mm]});
            skFitSpline(sketch, "E3092", {"points": [v(-59.09, 5.95) * mm, v(-59.12, 5.96) * mm, v(-59.15, 5.95) * mm, v(-59.2, 5.95) * mm]});
            skFitSpline(sketch, "E3093", {"points": [v(-59.2, 5.95) * mm, v(-59.22, 5.71) * mm, v(-59.25, 5.48) * mm, v(-59.27, 5.24) * mm]});
            skFitSpline(sketch, "E3094", {"points": [v(-59.27, 5.24) * mm, v(-59.3, 4.93) * mm, v(-59.32, 4.62) * mm, v(-59.35, 4.32) * mm]});
            skFitSpline(sketch, "E3095", {"points": [v(-59.35, 4.32) * mm, v(-59.4, 3.9) * mm, v(-59.46, 3.5) * mm, v(-59.51, 3.09) * mm]});
            skFitSpline(sketch, "E3096", {"points": [v(-59.51, 3.09) * mm, v(-59.56, 2.7) * mm, v(-59.82, 2.48) * mm, v(-60.22, 2.5) * mm]});
            skFitSpline(sketch, "E3097", {"points": [v(-60.22, 2.5) * mm, v(-60.5, 2.53) * mm, v(-60.78, 2.55) * mm, v(-61.06, 2.55) * mm]});
            skFitSpline(sketch, "E3098", {"points": [v(-61.06, 2.55) * mm, v(-61.66, 2.55) * mm, v(-62.25, 2.58) * mm, v(-62.85, 2.63) * mm]});
            skFitSpline(sketch, "E3099", {"points": [v(-62.85, 2.63) * mm, v(-62.88, 2.64) * mm, v(-62.91, 2.63) * mm, v(-62.99, 2.63) * mm]});
            skFitSpline(sketch, "E3100", {"points": [v(-62.99, 2.63) * mm, v(-62.12, 1.77) * mm, v(-61.26, 0.96) * mm, v(-60.4, 0.14) * mm]});
            skFitSpline(sketch, "E3101", {"points": [v(-60.4, 0.14) * mm, v(-60.3, 0.22) * mm, v(-60.2, 0.3) * mm, v(-60.12, 0.38) * mm]});
            skFitSpline(sketch, "E3102", {"points": [v(-60.12, 0.38) * mm, v(-59.26, 1.2) * mm, v(-58.38, 2) * mm, v(-57.57, 2.88) * mm]});
            skFitSpline(sketch, "E3103", {"points": [v(-57.57, 2.88) * mm, v(-57.38, 3.08) * mm, v(-57.16, 3.26) * mm, v(-56.96, 3.46) * mm]});
            skFitSpline(sketch, "E3104", {"points": [v(-56.96, 3.46) * mm, v(-56.68, 3.75) * mm, v(-56.4, 4.04) * mm, v(-56.1, 4.33) * mm]});
            skFitSpline(sketch, "E3105", {"points": [v(-56.1, 4.33) * mm, v(-56.09, 4.36) * mm, v(-56.05, 4.38) * mm, v(-56.04, 4.4) * mm]});
            skFitSpline(sketch, "E3106", {"points": [v(-56.04, 4.4) * mm, v(-56, 4.6) * mm, v(-55.9, 4.77) * mm, v(-55.82, 4.94) * mm]});
            skFitSpline(sketch, "E3107", {"points": [v(-55.82, 4.94) * mm, v(-55.8, 4.99) * mm, v(-55.8, 5.05) * mm, v(-55.8, 5.1) * mm]});
            skFitSpline(sketch, "E3108", {"points": [v(-55.8, 5.1) * mm, v(-55.78, 5.57) * mm, v(-55.7, 6.03) * mm, v(-55.57, 6.47) * mm]});
            skFitSpline(sketch, "E3109", {"points": [v(-55.57, 6.47) * mm, v(-55.52, 6.65) * mm, v(-55.48, 6.83) * mm, v(-55.44, 7) * mm]});
            skFitSpline(sketch, "E3110", {"points": [v(-55.44, 7) * mm, v(-55.39, 7.26) * mm, v(-55.16, 7.42) * mm, v(-54.9, 7.4) * mm]});
            skFitSpline(sketch, "E3111", {"points": [v(-54.9, 7.4) * mm, v(-54.64, 7.38) * mm, v(-54.46, 7.17) * mm, v(-54.48, 6.9) * mm]});
            skFitSpline(sketch, "E3112", {"points": [v(-54.48, 6.9) * mm, v(-54.49, 6.72) * mm, v(-54.53, 6.53) * mm, v(-54.59, 6.35) * mm]});
            skFitSpline(sketch, "E3113", {"points": [v(-54.59, 6.35) * mm, v(-54.73, 5.92) * mm, v(-54.81, 5.48) * mm, v(-54.82, 5.04) * mm]});
            skFitSpline(sketch, "E3114", {"points": [v(-54.82, 5.04) * mm, v(-54.82, 5.01) * mm, v(-54.82, 4.99) * mm, v(-54.81, 4.95) * mm]});
            skFitSpline(sketch, "E3115", {"points": [v(-54.81, 4.95) * mm, v(-54.64, 4.87) * mm, v(-54.45, 4.9) * mm, v(-54.28, 4.9) * mm]});
            skFitSpline(sketch, "E3116", {"points": [v(-54.28, 4.9) * mm, v(-53.75, 4.87) * mm, v(-53.22, 4.86) * mm, v(-52.7, 4.84) * mm]});
            skFitSpline(sketch, "E3117", {"points": [v(-52.7, 4.84) * mm, v(-52.6, 4.84) * mm, v(-52.49, 4.82) * mm, v(-52.4, 4.8) * mm]});
            skFitSpline(sketch, "E3118", {"points": [v(-52.4, 4.8) * mm, v(-52.17, 4.72) * mm, v(-52.02, 4.48) * mm, v(-52.05, 4.27) * mm]});
            skFitSpline(sketch, "E3119", {"points": [v(-52.05, 4.27) * mm, v(-52.09, 4.03) * mm, v(-52.27, 3.85) * mm, v(-52.52, 3.85) * mm]});
            skFitSpline(sketch, "E3120", {"points": [v(-52.52, 3.85) * mm, v(-53.16, 3.86) * mm, v(-53.8, 3.82) * mm, v(-54.44, 3.93) * mm]});
            skFitSpline(sketch, "E3121", {"points": [v(-54.44, 3.93) * mm, v(-54.62, 3.96) * mm, v(-54.8, 3.96) * mm, v(-54.98, 3.96) * mm]});
            skFitSpline(sketch, "E3122", {"points": [v(-54.98, 3.96) * mm, v(-55.05, 3.96) * mm, v(-55.12, 3.93) * mm, v(-55.17, 3.89) * mm]});
            skFitSpline(sketch, "E3123", {"points": [v(-55.17, 3.89) * mm, v(-55.4, 3.67) * mm, v(-55.6, 3.44) * mm, v(-55.83, 3.22) * mm]});
            skFitSpline(sketch, "E3124", {"points": [v(-55.83, 3.22) * mm, v(-56.12, 2.94) * mm, v(-56.41, 2.65) * mm, v(-56.7, 2.37) * mm]});
            skFitSpline(sketch, "E3125", {"points": [v(-56.7, 2.37) * mm, v(-56.88, 2.19) * mm, v(-57.06, 2) * mm, v(-57.24, 1.82) * mm]});
            skFitSpline(sketch, "E3126", {"points": [v(-57.24, 1.82) * mm, v(-57.62, 1.45) * mm, v(-57.99, 1.08) * mm, v(-58.36, 0.7) * mm]});
            skFitSpline(sketch, "E3127", {"points": [v(-58.36, 0.7) * mm, v(-58.42, 0.64) * mm, v(-58.5, 0.6) * mm, v(-58.56, 0.54) * mm]});
            skFitSpline(sketch, "E3128", {"points": [v(-58.56, 0.54) * mm, v(-58.55, 0.52) * mm, v(-58.54, 0.5) * mm, v(-58.53, 0.5) * mm]});
            skFitSpline(sketch, "E3129", {"points": [v(-58.53, 0.5) * mm, v(-58.48, 0.51) * mm, v(-58.43, 0.52) * mm, v(-58.38, 0.54) * mm]});
            skFitSpline(sketch, "E3130", {"points": [v(-58.38, 0.54) * mm, v(-58, 0.72) * mm, v(-57.62, 0.9) * mm, v(-57.23, 1.08) * mm]});
            skFitSpline(sketch, "E3131", {"points": [v(-57.23, 1.08) * mm, v(-57.21, 1.1) * mm, v(-57.2, 1.1) * mm, v(-57.17, 1.11) * mm]});
            skFitSpline(sketch, "E3132", {"points": [v(-57.17, 1.11) * mm, v(-56.78, 1.23) * mm, v(-56.41, 1.41) * mm, v(-56.06, 1.62) * mm]});
            skFitSpline(sketch, "E3133", {"points": [v(-56.06, 1.62) * mm, v(-55.8, 1.76) * mm, v(-55.56, 1.75) * mm, v(-55.31, 1.6) * mm]});
            skFitSpline(sketch, "E3134", {"points": [v(-55.31, 1.6) * mm, v(-54.86, 1.3) * mm, v(-54.4, 1.02) * mm, v(-53.96, 0.73) * mm]});
            skFitSpline(sketch, "E3135", {"points": [v(-53.96, 0.73) * mm, v(-53.66, 0.53) * mm, v(-53.38, 0.31) * mm, v(-53.07, 0.1) * mm]});
            skFitSpline(sketch, "E3136", {"points": [v(-53.07, 0.1) * mm, v(-52.8, 0.3) * mm, v(-52.53, 0.5) * mm, v(-52.27, 0.7) * mm]});
            skFitSpline(sketch, "E3137", {"points": [v(-52.27, 0.7) * mm, v(-51.97, 0.93) * mm, v(-51.68, 1.17) * mm, v(-51.4, 1.41) * mm]});
            skFitSpline(sketch, "E3138", {"points": [v(-51.4, 1.41) * mm, v(-51.31, 1.48) * mm, v(-51.24, 1.56) * mm, v(-51.18, 1.63) * mm]});
            skFitSpline(sketch, "E3139", {"points": [v(-51.18, 1.63) * mm, v(-51.01, 1.84) * mm, v(-50.77, 1.9) * mm, v(-50.56, 1.78) * mm]});
            skFitSpline(sketch, "E3140", {"points": [v(-50.56, 1.78) * mm, v(-50.34, 1.66) * mm, v(-50.23, 1.4) * mm, v(-50.33, 1.16) * mm]});
            skFitSpline(sketch, "E3141", {"points": [v(-50.33, 1.16) * mm, v(-50.37, 1.04) * mm, v(-50.46, 0.93) * mm, v(-50.56, 0.84) * mm]});
            skFitSpline(sketch, "E3142", {"points": [v(-50.56, 0.84) * mm, v(-50.8, 0.63) * mm, v(-51.04, 0.44) * mm, v(-51.28, 0.25) * mm]});
            skFitSpline(sketch, "E3143", {"points": [v(-51.28, 0.25) * mm, v(-51.6, -0.01) * mm, v(-51.93, -0.27) * mm, v(-52.25, -0.53) * mm]});
            skFitSpline(sketch, "E3144", {"points": [v(-52.25, -0.53) * mm, v(-51.94, -0.78) * mm, v(-51.63, -1.03) * mm, v(-51.33, -1.28) * mm]});
            skFitSpline(sketch, "E3145", {"points": [v(-51.33, -1.28) * mm, v(-51.08, -1.49) * mm, v(-50.82, -1.68) * mm, v(-50.58, -1.89) * mm]});
            skFitSpline(sketch, "E3146", {"points": [v(-50.58, -1.89) * mm, v(-50.49, -1.97) * mm, v(-50.4, -2.07) * mm, v(-50.35, -2.18) * mm]});
            skFitSpline(sketch, "E3147", {"points": [v(-50.35, -2.18) * mm, v(-50.23, -2.42) * mm, v(-50.32, -2.7) * mm, v(-50.53, -2.83) * mm]});
            skFitSpline(sketch, "E3148", {"points": [v(-50.53, -2.83) * mm, v(-50.76, -2.97) * mm, v(-51, -2.92) * mm, v(-51.19, -2.7) * mm]});
            skFitSpline(sketch, "E3149", {"points": [v(-51.19, -2.7) * mm, v(-51.27, -2.6) * mm, v(-51.36, -2.5) * mm, v(-51.46, -2.43) * mm]});
            skFitSpline(sketch, "E3150", {"points": [v(-51.46, -2.43) * mm, v(-51.98, -2) * mm, v(-52.5, -1.59) * mm, v(-53.05, -1.15) * mm]});
            skFitSpline(sketch, "E3151", {"points": [v(-53.05, -1.15) * mm, v(-53.35, -1.37) * mm, v(-53.63, -1.57) * mm, v(-53.92, -1.77) * mm]});
            skFitSpline(sketch, "E3152", {"points": [v(-53.92, -1.77) * mm, v(-54.34, -2.05) * mm, v(-54.78, -2.32) * mm, v(-55.2, -2.6) * mm]});
            skFitSpline(sketch, "E3153", {"points": [v(-55.2, -2.6) * mm, v(-55.6, -2.88) * mm, v(-55.95, -2.8) * mm, v(-56.31, -2.56) * mm]});
            skFitSpline(sketch, "E3154", {"points": [v(-56.31, -2.56) * mm, v(-56.4, -2.5) * mm, v(-56.5, -2.44) * mm, v(-56.6, -2.4) * mm]});
            skFitSpline(sketch, "E3155", {"points": [v(-56.6, -2.4) * mm, v(-57.18, -2.14) * mm, v(-57.76, -1.89) * mm, v(-58.34, -1.63) * mm]});
            skFitSpline(sketch, "E3156", {"points": [v(-58.34, -1.63) * mm, v(-58.4, -1.6) * mm, v(-58.47, -1.58) * mm, v(-58.55, -1.58) * mm]});
            skFitSpline(sketch, "E3157", {"points": [v(-58.55, -1.58) * mm, v(-58.5, -1.63) * mm, v(-58.44, -1.69) * mm, v(-58.39, -1.74) * mm]});
            skFitSpline(sketch, "E3158", {"points": [v(-58.39, -1.74) * mm, v(-58.07, -2.06) * mm, v(-57.74, -2.38) * mm, v(-57.42, -2.7) * mm]});
            skFitSpline(sketch, "E3159", {"points": [v(-57.42, -2.7) * mm, v(-56.99, -3.13) * mm, v(-56.56, -3.56) * mm, v(-56.13, -3.99) * mm]});
            skFitSpline(sketch, "E3160", {"points": [v(-56.13, -3.99) * mm, v(-55.83, -4.29) * mm, v(-55.53, -4.59) * mm, v(-55.24, -4.9) * mm]});
            skFitSpline(sketch, "E3161", {"points": [v(-55.24, -4.9) * mm, v(-55.14, -5) * mm, v(-55.03, -5.05) * mm, v(-54.88, -5.03) * mm]});
            skFitSpline(sketch, "E3162", {"points": [v(-54.88, -5.03) * mm, v(-54.16, -4.94) * mm, v(-53.43, -4.9) * mm, v(-52.7, -4.93) * mm]});
            skFitSpline(sketch, "E3163", {"points": [v(-52.7, -4.93) * mm, v(-52.66, -4.93) * mm, v(-52.61, -4.93) * mm, v(-52.56, -4.93) * mm]});
            skFitSpline(sketch, "E3164", {"points": [v(-52.56, -4.93) * mm, v(-52.27, -4.93) * mm, v(-52.08, -5.1) * mm, v(-52.05, -5.35) * mm]});
            skFitSpline(sketch, "E3165", {"points": [v(-52.05, -5.35) * mm, v(-52.02, -5.6) * mm, v(-52.2, -5.83) * mm, v(-52.47, -5.88) * mm]});
            skFitSpline(sketch, "E3166", {"points": [v(-52.47, -5.88) * mm, v(-52.64, -5.91) * mm, v(-52.82, -5.93) * mm, v(-53, -5.93) * mm]});
            skFitSpline(sketch, "E3167", {"points": [v(-53, -5.93) * mm, v(-53.4, -5.95) * mm, v(-53.8, -5.94) * mm, v(-54.22, -5.95) * mm]});
            skFitSpline(sketch, "E3168", {"points": [v(-54.22, -5.95) * mm, v(-54.41, -5.96) * mm, v(-54.6, -5.99) * mm, v(-54.82, -6) * mm]});
            skFitSpline(sketch, "E3169", {"points": [v(-54.82, -6) * mm, v(-54.83, -6.44) * mm, v(-54.76, -6.85) * mm, v(-54.64, -7.25) * mm]});
            skFitSpline(sketch, "E3170", {"points": [v(-54.64, -7.25) * mm, v(-54.56, -7.49) * mm, v(-54.47, -7.73) * mm, v(-54.47, -7.99) * mm]});
            skFitSpline(sketch, "E3171", {"points": [v(-54.47, -7.99) * mm, v(-54.47, -8.36) * mm, v(-54.83, -8.59) * mm, v(-55.16, -8.43) * mm]});
            skFitSpline(sketch, "E3172", {"points": [v(-55.16, -8.43) * mm, v(-55.31, -8.35) * mm, v(-55.4, -8.23) * mm, v(-55.44, -8.06) * mm]});
            skFitSpline(sketch, "E3173", {"points": [v(-55.44, -8.06) * mm, v(-55.48, -7.9) * mm, v(-55.5, -7.73) * mm, v(-55.56, -7.58) * mm]});
            skFitSpline(sketch, "E3174", {"points": [v(-55.56, -7.58) * mm, v(-55.7, -7.12) * mm, v(-55.77, -6.65) * mm, v(-55.8, -6.17) * mm]});
            skFitSpline(sketch, "E3175", {"points": [v(-55.8, -6.17) * mm, v(-55.81, -6.05) * mm, v(-55.8, -5.93) * mm, v(-55.91, -5.84) * mm]});
            skFitSpline(sketch, "E3176", {"points": [v(-55.91, -5.84) * mm, v(-55.95, -5.8) * mm, v(-55.98, -5.74) * mm, v(-55.98, -5.7) * mm]});
            skFitSpline(sketch, "E3177", {"points": [v(-55.98, -5.7) * mm, v(-55.98, -5.5) * mm, v(-56.1, -5.4) * mm, v(-56.22, -5.3) * mm]});
            skFitSpline(sketch, "E3178", {"points": [v(-56.22, -5.3) * mm, v(-56.97, -4.53) * mm, v(-57.71, -3.76) * mm, v(-58.47, -3.01) * mm]});
            skFitSpline(sketch, "E3179", {"points": [v(-58.47, -3.01) * mm, v(-59.06, -2.43) * mm, v(-59.67, -1.88) * mm, v(-60.27, -1.31) * mm]});
            skFitSpline(sketch, "E3180", {"points": [v(-60.27, -1.31) * mm, v(-60.3, -1.28) * mm, v(-60.34, -1.25) * mm, v(-60.4, -1.2) * mm]});
            skFitSpline(sketch, "E3181", {"points": [v(-60.4, -1.2) * mm, v(-61.25, -2.02) * mm, v(-62.1, -2.84) * mm, v(-62.98, -3.67) * mm]});
            skFitSpline(sketch, "E3182", {"points": [v(-62.98, -3.67) * mm, v(-62.74, -3.67) * mm, v(-62.53, -3.68) * mm, v(-62.32, -3.67) * mm]});
            skFitSpline(sketch, "E3183", {"points": [v(-62.32, -3.67) * mm, v(-62.15, -3.67) * mm, v(-61.99, -3.64) * mm, v(-61.82, -3.63) * mm]});
            skFitSpline(sketch, "E3184", {"points": [v(-61.82, -3.63) * mm, v(-61.28, -3.62) * mm, v(-60.73, -3.6) * mm, v(-60.2, -3.59) * mm]});
            skFitSpline(sketch, "E3185", {"points": [v(-60.2, -3.59) * mm, v(-59.78, -3.57) * mm, v(-59.55, -3.77) * mm, v(-59.5, -4.18) * mm]});
            skFitSpline(sketch, "E3186", {"points": [v(-59.5, -4.18) * mm, v(-59.5, -4.32) * mm, v(-59.47, -4.45) * mm, v(-59.45, -4.58) * mm]});
            skFitSpline(sketch, "E3187", {"points": [v(-59.45, -4.58) * mm, v(-59.42, -4.75) * mm, v(-59.38, -4.91) * mm, v(-59.37, -5.08) * mm]});
            skFitSpline(sketch, "E3188", {"points": [v(-59.37, -5.08) * mm, v(-59.32, -5.6) * mm, v(-59.27, -6.13) * mm, v(-59.23, -6.65) * mm]});
            skFitSpline(sketch, "E3189", {"points": [v(-59.23, -6.65) * mm, v(-59.22, -6.77) * mm, v(-59.23, -6.89) * mm, v(-59.23, -7.05) * mm]});
            skFitSpline(sketch, "E3190", {"points": [v(-59.23, -7.05) * mm, v(-58.92, -6.97) * mm, v(-58.64, -6.9) * mm, v(-58.37, -6.83) * mm]});
            skFitSpline(sketch, "E3191", {"points": [v(-58.37, -6.83) * mm, v(-58.08, -6.76) * mm, v(-57.78, -6.7) * mm, v(-57.49, -6.64) * mm]});
            skFitSpline(sketch, "E3192", {"points": [v(-57.49, -6.64) * mm, v(-57.4, -6.62) * mm, v(-57.3, -6.62) * mm, v(-57.2, -6.63) * mm]});
            skFitSpline(sketch, "E3193", {"points": [v(-57.2, -6.63) * mm, v(-57.02, -6.65) * mm, v(-56.88, -6.74) * mm, v(-56.81, -6.91) * mm]});
            skFitSpline(sketch, "E3194", {"points": [v(-56.81, -6.91) * mm, v(-56.74, -7.08) * mm, v(-56.75, -7.26) * mm, v(-56.87, -7.4) * mm]});
            skFitSpline(sketch, "E3195", {"points": [v(-56.87, -7.4) * mm, v(-57.02, -7.58) * mm, v(-57.19, -7.7) * mm, v(-57.44, -7.64) * mm]});
            skFitSpline(sketch, "E3196", {"points": [v(-57.44, -7.64) * mm, v(-57.51, -7.62) * mm, v(-57.6, -7.62) * mm, v(-57.67, -7.64) * mm]});
            skFitSpline(sketch, "E3197", {"points": [v(-57.67, -7.64) * mm, v(-58.12, -7.76) * mm, v(-58.56, -7.89) * mm, v(-59.03, -8.02) * mm]});
            skFitSpline(sketch, "E3198", {"points": [v(-59.03, -8.02) * mm, v(-59.02, -8.2) * mm, v(-59, -8.39) * mm, v(-59, -8.58) * mm]});
            skFitSpline(sketch, "E3199", {"points": [v(-59, -8.58) * mm, v(-58.99, -8.78) * mm, v(-59, -9) * mm, v(-58.98, -9.2) * mm]});
            skFitSpline(sketch, "E3200", {"points": [v(-58.98, -9.2) * mm, v(-58.96, -9.35) * mm, v(-58.93, -9.51) * mm, v(-58.87, -9.66) * mm]});
            skFitSpline(sketch, "E3201", {"points": [v(-58.87, -9.66) * mm, v(-58.77, -9.9) * mm, v(-58.83, -10.18) * mm, v(-59.03, -10.35) * mm]});
            skFitSpline(sketch, "E3202", {"points": [v(-59.03, -10.35) * mm, v(-59.24, -10.52) * mm, v(-59.55, -10.5) * mm, v(-59.7, -10.27) * mm]});
            skFitSpline(sketch, "E3203", {"points": [v(-59.7, -10.27) * mm, v(-59.78, -10.17) * mm, v(-59.82, -10.05) * mm, v(-59.85, -9.93) * mm]});
            skFitSpline(sketch, "E3204", {"points": [v(-59.85, -9.93) * mm, v(-59.96, -9.52) * mm, v(-59.93, -9.1) * mm, v(-59.96, -8.69) * mm]});
            skFitSpline(sketch, "E3205", {"points": [v(-59.96, -8.69) * mm, v(-59.97, -8.51) * mm, v(-59.99, -8.34) * mm, v(-60, -8.15) * mm]});
            skFitSpline(sketch, "E3206", {"points": [v(-60, -8.15) * mm, v(-60.4, -8.24) * mm, v(-60.78, -8.34) * mm, v(-61.15, -8.42) * mm]});
            skFitSpline(sketch, "E3207", {"points": [v(-61.15, -8.42) * mm, v(-61.51, -8.5) * mm, v(-61.87, -8.58) * mm, v(-62.23, -8.65) * mm]});
            skFitSpline(sketch, "E3208", {"points": [v(-62.23, -8.65) * mm, v(-62.47, -8.7) * mm, v(-62.72, -8.73) * mm, v(-62.96, -8.76) * mm]});
            skFitSpline(sketch, "E3209", {"points": [v(-62.96, -8.76) * mm, v(-63.18, -8.8) * mm, v(-63.4, -8.67) * mm, v(-63.52, -8.46) * mm]});
            skFitSpline(sketch, "E3210", {"points": [v(-63.52, -8.46) * mm, v(-63.55, -8.4) * mm, v(-63.57, -8.33) * mm, v(-63.6, -8.26) * mm]});
            skFitSpline(sketch, "E3211", {"points": [v(-63.6, -8.26) * mm, v(-63.82, -7.46) * mm, v(-64.05, -6.65) * mm, v(-64.27, -5.84) * mm]});
            skFitSpline(sketch, "E3212", {"points": [v(-64.27, -5.84) * mm, v(-64.3, -5.77) * mm, v(-64.32, -5.7) * mm, v(-64.36, -5.57) * mm]});
            skFitSpline(sketch, "E3213", {"points": [v(-64.36, -5.57) * mm, v(-64.9, -6.67) * mm, v(-65.4, -7.73) * mm, v(-65.92, -8.8) * mm]});
            skFitSpline(sketch, "E3214", {"points": [v(-65.92, -8.8) * mm, v(-65.83, -8.86) * mm, v(-65.76, -8.92) * mm, v(-65.67, -8.96) * mm]});
            skFitSpline(sketch, "E3215", {"points": [v(-65.67, -8.96) * mm, v(-65.24, -9.2) * mm, v(-64.8, -9.44) * mm, v(-64.37, -9.67) * mm]});
            skFitSpline(sketch, "E3216", {"points": [v(-64.37, -9.67) * mm, v(-63.88, -9.93) * mm, v(-63.39, -10.17) * mm, v(-62.9, -10.42) * mm]});
            skFitSpline(sketch, "E3217", {"points": [v(-62.9, -10.42) * mm, v(-62.5, -10.63) * mm, v(-62.09, -10.84) * mm, v(-61.68, -11.05) * mm]});
            skFitSpline(sketch, "E3218", {"points": [v(-61.68, -11.05) * mm, v(-61.33, -11.23) * mm, v(-60.97, -11.4) * mm, v(-60.61, -11.59) * mm]});
            skFitSpline(sketch, "E3219", {"points": [v(-60.61, -11.59) * mm, v(-60.53, -11.63) * mm, v(-60.46, -11.65) * mm, v(-60.36, -11.63) * mm]});
            skFitSpline(sketch, "E3220", {"points": [v(-60.36, -11.63) * mm, v(-60.3, -11.61) * mm, v(-60.2, -11.61) * mm, v(-60.13, -11.64) * mm]});
            skFitSpline(sketch, "E3221", {"points": [v(-60.13, -11.64) * mm, v(-60, -11.7) * mm, v(-59.9, -11.67) * mm, v(-59.78, -11.64) * mm]});
            skFitSpline(sketch, "E3222", {"points": [v(-59.78, -11.64) * mm, v(-59.33, -11.53) * mm, v(-58.88, -11.45) * mm, v(-58.41, -11.45) * mm]});
            skFitSpline(sketch, "E3223", {"points": [v(-58.41, -11.45) * mm, v(-58.26, -11.45) * mm, v(-58.11, -11.42) * mm, v(-57.96, -11.42) * mm]});
            skFitSpline(sketch, "E3224", {"points": [v(-57.96, -11.42) * mm, v(-57.84, -11.41) * mm, v(-57.72, -11.4) * mm, v(-57.6, -11.44) * mm]});
            skFitSpline(sketch, "E3225", {"points": [v(-57.6, -11.44) * mm, v(-57.41, -11.5) * mm, v(-57.3, -11.7) * mm, v(-57.3, -11.9) * mm]});
            skFitSpline(sketch, "E3226", {"points": [v(-57.3, -11.9) * mm, v(-57.3, -12.12) * mm, v(-57.43, -12.3) * mm, v(-57.64, -12.35) * mm]});
            skFitSpline(sketch, "E3227", {"points": [v(-57.64, -12.35) * mm, v(-57.78, -12.39) * mm, v(-57.92, -12.42) * mm, v(-58.06, -12.4) * mm]});
            skFitSpline(sketch, "E3228", {"points": [v(-58.06, -12.4) * mm, v(-58.48, -12.4) * mm, v(-58.9, -12.45) * mm, v(-59.3, -12.52) * mm]});
            skFitSpline(sketch, "E3229", {"points": [v(-59.3, -12.52) * mm, v(-59.4, -12.54) * mm, v(-59.5, -12.58) * mm, v(-59.61, -12.61) * mm]});
            skFitSpline(sketch, "E3230", {"points": [v(-59.61, -12.61) * mm, v(-59.6, -12.68) * mm, v(-59.61, -12.74) * mm, v(-59.6, -12.8) * mm]});
            skFitSpline(sketch, "E3231", {"points": [v(-59.6, -12.8) * mm, v(-59.46, -13.3) * mm, v(-59.3, -13.78) * mm, v(-59.17, -14.27) * mm]});
            skFitSpline(sketch, "E3232", {"points": [v(-59.17, -14.27) * mm, v(-59.11, -14.5) * mm, v(-59.05, -14.74) * mm, v(-59.03, -14.97) * mm]});
            skFitSpline(sketch, "E3233", {"points": [v(-59.03, -14.97) * mm, v(-59.01, -15.24) * mm, v(-59.2, -15.44) * mm, v(-59.45, -15.47) * mm]});
            skFitSpline(sketch, "E3234", {"points": [v(-59.45, -15.47) * mm, v(-59.66, -15.5) * mm, v(-59.89, -15.37) * mm, v(-59.96, -15.13) * mm]});
            skFitSpline(sketch, "E3235", {"points": [v(-59.96, -15.13) * mm, v(-60.1, -14.7) * mm, v(-60.24, -14.28) * mm, v(-60.36, -13.85) * mm]});
            skFitSpline(sketch, "E3236", {"points": [v(-60.36, -13.85) * mm, v(-60.45, -13.53) * mm, v(-60.52, -13.2) * mm, v(-60.58, -12.87) * mm]});
            skFitSpline(sketch, "E3237", {"points": [v(-60.58, -12.87) * mm, v(-60.61, -12.73) * mm, v(-60.68, -12.64) * mm, v(-60.82, -12.57) * mm]});
            skFitSpline(sketch, "E3238", {"points": [v(-60.82, -12.57) * mm, v(-61.36, -12.31) * mm, v(-61.9, -12.05) * mm, v(-62.43, -11.77) * mm]});
            skFitSpline(sketch, "E3239", {"points": [v(-62.43, -11.77) * mm, v(-63.24, -11.36) * mm, v(-64.05, -10.94) * mm, v(-64.85, -10.52) * mm]});
            skFitSpline(sketch, "E3240", {"points": [v(-64.85, -10.52) * mm, v(-64.9, -10.5) * mm, v(-64.94, -10.48) * mm, v(-65, -10.49) * mm]});
            skFitSpline(sketch, "E3241", {"points": [v(-65, -10.49) * mm, v(-64.94, -10.55) * mm, v(-64.89, -10.63) * mm, v(-64.83, -10.7) * mm]});
            skFitSpline(sketch, "E3242", {"points": [v(-64.83, -10.7) * mm, v(-64.56, -10.98) * mm, v(-64.29, -11.26) * mm, v(-64.02, -11.55) * mm]});
            skFitSpline(sketch, "E3243", {"points": [v(-64.02, -11.55) * mm, v(-64.01, -11.55) * mm, v(-64, -11.56) * mm, v(-64, -11.57) * mm]});
            skFitSpline(sketch, "E3244", {"points": [v(-64, -11.57) * mm, v(-63.76, -11.9) * mm, v(-63.47, -12.2) * mm, v(-63.17, -12.48) * mm]});
            skFitSpline(sketch, "E3245", {"points": [v(-63.17, -12.48) * mm, v(-62.96, -12.67) * mm, v(-62.89, -12.9) * mm, v(-62.97, -13.18) * mm]});
            skFitSpline(sketch, "E3246", {"points": [v(-62.97, -13.18) * mm, v(-63.11, -13.72) * mm, v(-63.24, -14.26) * mm, v(-63.39, -14.8) * mm]});
            skFitSpline(sketch, "E3247", {"points": [v(-63.39, -14.8) * mm, v(-63.48, -15.13) * mm, v(-63.59, -15.45) * mm, v(-63.7, -15.8) * mm]});
            skFitSpline(sketch, "E3248", {"points": [v(-63.7, -15.8) * mm, v(-63.41, -16) * mm, v(-63.14, -16.18) * mm, v(-62.86, -16.37) * mm]});
            skFitSpline(sketch, "E3249", {"points": [v(-62.86, -16.37) * mm, v(-62.57, -16.57) * mm, v(-62.27, -16.76) * mm, v(-61.98, -16.94) * mm]});
            skFitSpline(sketch, "E3250", {"points": [v(-61.98, -16.94) * mm, v(-61.88, -17) * mm, v(-61.77, -17.07) * mm, v(-61.66, -17.11) * mm]});
            skFitSpline(sketch, "E3251", {"points": [v(-61.66, -17.11) * mm, v(-61.38, -17.22) * mm, v(-61.25, -17.45) * mm, v(-61.33, -17.7) * mm]});
            skFitSpline(sketch, "E3252", {"points": [v(-61.33, -17.7) * mm, v(-61.42, -17.98) * mm, v(-61.7, -18.14) * mm, v(-61.98, -18.05) * mm]});
            skFitSpline(sketch, "E3253", {"points": [v(-61.98, -18.05) * mm, v(-62.1, -18.02) * mm, v(-62.21, -17.95) * mm, v(-62.32, -17.88) * mm]});
            skFitSpline(sketch, "E3254", {"points": [v(-62.32, -17.88) * mm, v(-62.88, -17.52) * mm, v(-63.44, -17.14) * mm, v(-64, -16.78) * mm]});
            skFitSpline(sketch, "E3255", {"points": [v(-64, -16.78) * mm, v(-64.01, -16.77) * mm, v(-64.03, -16.77) * mm, v(-64.04, -16.77) * mm]});
            skFitSpline(sketch, "E3256", {"points": [v(-64.04, -16.77) * mm, v(-64.18, -17.14) * mm, v(-64.33, -17.5) * mm, v(-64.47, -17.88) * mm]});
            skFitSpline(sketch, "E3257", {"points": [v(-64.47, -17.88) * mm, v(-64.58, -18.17) * mm, v(-64.69, -18.46) * mm, v(-64.8, -18.75) * mm]});
            skFitSpline(sketch, "E3258", {"points": [v(-64.8, -18.75) * mm, v(-64.83, -18.83) * mm, v(-64.87, -18.91) * mm, v(-64.92, -18.98) * mm]});
            skFitSpline(sketch, "E3259", {"points": [v(-64.92, -18.98) * mm, v(-65.04, -19.15) * mm, v(-65.2, -19.25) * mm, v(-65.41, -19.22) * mm]});
            skFitSpline(sketch, "E3260", {"points": [v(-65.41, -19.22) * mm, v(-65.86, -19.18) * mm, v(-65.93, -18.76) * mm, v(-65.8, -18.5) * mm]});
            skFitSpline(sketch, "E3261", {"points": [v(-65.8, -18.5) * mm, v(-65.67, -18.23) * mm, v(-65.55, -17.95) * mm, v(-65.43, -17.67) * mm]});
            skFitSpline(sketch, "E3262", {"points": [v(-65.43, -17.67) * mm, v(-65.34, -17.47) * mm, v(-65.27, -17.27) * mm, v(-65.2, -17.07) * mm]});
            skFitSpline(sketch, "E3263", {"points": [v(-65.2, -17.07) * mm, v(-65.1, -16.78) * mm, v(-65, -16.5) * mm, v(-64.9, -16.18) * mm]});
            skFitSpline(sketch, "E3264", {"points": [v(-64.9, -16.18) * mm, v(-65.16, -15.98) * mm, v(-65.43, -15.8) * mm, v(-65.7, -15.58) * mm]});
            skFitSpline(sketch, "E3265", {"points": [v(-65.7, -15.58) * mm, v(-66.15, -15.22) * mm, v(-66.6, -14.85) * mm, v(-67.04, -14.47) * mm]});
            skFitSpline(sketch, "E3266", {"points": [v(-67.04, -14.47) * mm, v(-67.25, -14.3) * mm, v(-67.31, -14.08) * mm, v(-67.26, -13.8) * mm]});
            skFitSpline(sketch, "E3267", {"points": [v(-67.26, -13.8) * mm, v(-67.12, -13.05) * mm, v(-67.1, -12.27) * mm, v(-67, -11.5) * mm]});
            skFitSpline(sketch, "E3268", {"points": [v(-67, -11.5) * mm, v(-66.97, -11.38) * mm, v(-66.96, -11.26) * mm, v(-66.98, -11.12) * mm]});
            skFitSpline(sketch, "E3269", {"points": [v(-66.98, -11.12) * mm, v(-67, -11.16) * mm, v(-67.04, -11.2) * mm, v(-67.06, -11.24) * mm]});
            skFitSpline(sketch, "E3270", {"points": [v(-67.06, -11.24) * mm, v(-67.38, -11.86) * mm, v(-67.7, -12.48) * mm, v(-68, -13.1) * mm]});
            skFitSpline(sketch, "E3271", {"points": [v(-68, -13.1) * mm, v(-68.15, -13.37) * mm, v(-68.27, -13.64) * mm, v(-68.4, -13.91) * mm]});
            skFitSpline(sketch, "E3272", {"points": [v(-68.4, -13.91) * mm, v(-68.64, -14.38) * mm, v(-68.88, -14.84) * mm, v(-69.12, -15.3) * mm]});
            skFitSpline(sketch, "E3273", {"points": [v(-69.12, -15.3) * mm, v(-69.19, -15.41) * mm, v(-69.18, -15.51) * mm, v(-69.13, -15.63) * mm]});
            skFitSpline(sketch, "E3274", {"points": [v(-69.13, -15.63) * mm, v(-68.94, -16.09) * mm, v(-68.75, -16.55) * mm, v(-68.57, -17) * mm]});
            skFitSpline(sketch, "E3275", {"points": [v(-68.57, -17) * mm, v(-68.47, -17.28) * mm, v(-68.39, -17.55) * mm, v(-68.3, -17.83) * mm]});
            skFitSpline(sketch, "E3276", {"points": [v(-68.3, -17.83) * mm, v(-68.23, -18.1) * mm, v(-68.33, -18.33) * mm, v(-68.55, -18.44) * mm]});
            skFitSpline(sketch, "E3277", {"points": [v(-68.55, -18.44) * mm, v(-68.79, -18.54) * mm, v(-69.06, -18.46) * mm, v(-69.19, -18.21) * mm]});
            skFitSpline(sketch, "E3278", {"points": [v(-69.19, -18.21) * mm, v(-69.3, -18.01) * mm, v(-69.37, -17.8) * mm, v(-69.45, -17.57) * mm]});
            skFitSpline(sketch, "E3279", {"points": [v(-69.45, -17.57) * mm, v(-69.64, -17.06) * mm, v(-69.82, -16.54) * mm, v(-70.02, -16) * mm]});
            skFitSpline(sketch, "E3280", {"points": [v(-24.75, -8.09) * mm, v(-24.71, -8.21) * mm, v(-24.69, -8.3) * mm, v(-24.66, -8.4) * mm]});
            skFitSpline(sketch, "E3281", {"points": [v(-24.66, -8.4) * mm, v(-24.58, -8.65) * mm, v(-24.5, -8.9) * mm, v(-24.43, -9.17) * mm]});
            skFitSpline(sketch, "E3282", {"points": [v(-24.43, -9.17) * mm, v(-24.4, -9.29) * mm, v(-24.34, -9.36) * mm, v(-24.23, -9.41) * mm]});
            skFitSpline(sketch, "E3283", {"points": [v(-24.23, -9.41) * mm, v(-23.73, -9.67) * mm, v(-23.25, -9.95) * mm, v(-22.75, -10.2) * mm]});
            skFitSpline(sketch, "E3284", {"points": [v(-22.75, -10.2) * mm, v(-22.28, -10.45) * mm, v(-21.8, -10.67) * mm, v(-21.33, -10.9) * mm]});
            skFitSpline(sketch, "E3285", {"points": [v(-21.33, -10.9) * mm, v(-21.1, -11) * mm, v(-20.91, -11.13) * mm, v(-20.81, -11.37) * mm]});
            skFitSpline(sketch, "E3286", {"points": [v(-20.81, -11.37) * mm, v(-20.74, -11.55) * mm, v(-20.77, -11.72) * mm, v(-20.88, -11.87) * mm]});
            skFitSpline(sketch, "E3287", {"points": [v(-20.88, -11.87) * mm, v(-21, -12.02) * mm, v(-21.17, -12.08) * mm, v(-21.35, -12.03) * mm]});
            skFitSpline(sketch, "E3288", {"points": [v(-21.35, -12.03) * mm, v(-21.45, -12.01) * mm, v(-21.53, -11.94) * mm, v(-21.62, -11.88) * mm]});
            skFitSpline(sketch, "E3289", {"points": [v(-21.62, -11.88) * mm, v(-21.68, -11.85) * mm, v(-21.73, -11.8) * mm, v(-21.8, -11.76) * mm]});
            skFitSpline(sketch, "E3290", {"points": [v(-21.8, -11.76) * mm, v(-22.34, -11.49) * mm, v(-22.9, -11.22) * mm, v(-23.44, -10.94) * mm]});
            skFitSpline(sketch, "E3291", {"points": [v(-23.44, -10.94) * mm, v(-23.6, -10.86) * mm, v(-23.75, -10.77) * mm, v(-23.95, -10.66) * mm]});
            skFitSpline(sketch, "E3292", {"points": [v(-23.95, -10.66) * mm, v(-23.86, -10.97) * mm, v(-23.78, -11.22) * mm, v(-23.7, -11.48) * mm]});
            skFitSpline(sketch, "E3293", {"points": [v(-23.7, -11.48) * mm, v(-23.69, -11.53) * mm, v(-23.65, -11.58) * mm, v(-23.64, -11.63) * mm]});
            skFitSpline(sketch, "E3294", {"points": [v(-23.64, -11.63) * mm, v(-23.57, -11.96) * mm, v(-23.35, -12.13) * mm, v(-23.06, -12.27) * mm]});
            skFitSpline(sketch, "E3295", {"points": [v(-23.06, -12.27) * mm, v(-22.04, -12.76) * mm, v(-21.03, -13.28) * mm, v(-20.01, -13.79) * mm]});
            skFitSpline(sketch, "E3296", {"points": [v(-20.01, -13.79) * mm, v(-19.88, -13.85) * mm, v(-19.76, -13.93) * mm, v(-19.64, -14) * mm]});
            skFitSpline(sketch, "E3297", {"points": [v(-19.64, -14) * mm, v(-19.4, -14.16) * mm, v(-19.31, -14.43) * mm, v(-19.44, -14.66) * mm]});
            skFitSpline(sketch, "E3298", {"points": [v(-19.44, -14.66) * mm, v(-19.57, -14.9) * mm, v(-19.85, -14.98) * mm, v(-20.1, -14.85) * mm]});
            skFitSpline(sketch, "E3299", {"points": [v(-20.1, -14.85) * mm, v(-20.37, -14.73) * mm, v(-20.62, -14.59) * mm, v(-20.87, -14.45) * mm]});
            skFitSpline(sketch, "E3300", {"points": [v(-20.87, -14.45) * mm, v(-21.34, -14.21) * mm, v(-21.81, -13.97) * mm, v(-22.28, -13.73) * mm]});
            skFitSpline(sketch, "E3301", {"points": [v(-22.28, -13.73) * mm, v(-22.35, -13.7) * mm, v(-22.42, -13.67) * mm, v(-22.52, -13.67) * mm]});
            skFitSpline(sketch, "E3302", {"points": [v(-22.52, -13.67) * mm, v(-22.41, -13.78) * mm, v(-22.31, -13.9) * mm, v(-22.2, -14.01) * mm]});
            skFitSpline(sketch, "E3303", {"points": [v(-22.2, -14.01) * mm, v(-21.9, -14.36) * mm, v(-21.6, -14.7) * mm, v(-21.29, -15.05) * mm]});
            skFitSpline(sketch, "E3304", {"points": [v(-21.29, -15.05) * mm, v(-21.2, -15.14) * mm, v(-21.12, -15.22) * mm, v(-21.03, -15.3) * mm]});
            skFitSpline(sketch, "E3305", {"points": [v(-21.03, -15.3) * mm, v(-20.84, -15.5) * mm, v(-20.78, -15.72) * mm, v(-20.86, -15.99) * mm]});
            skFitSpline(sketch, "E3306", {"points": [v(-20.86, -15.99) * mm, v(-21.03, -16.6) * mm, v(-21.19, -17.2) * mm, v(-21.37, -17.8) * mm]});
            skFitSpline(sketch, "E3307", {"points": [v(-21.37, -17.8) * mm, v(-21.42, -17.99) * mm, v(-21.37, -18.1) * mm, v(-21.22, -18.2) * mm]});
            skFitSpline(sketch, "E3308", {"points": [v(-21.22, -18.2) * mm, v(-20.87, -18.45) * mm, v(-20.51, -18.7) * mm, v(-20.16, -18.97) * mm]});
            skFitSpline(sketch, "E3309", {"points": [v(-20.16, -18.97) * mm, v(-20.13, -19) * mm, v(-20.1, -19.01) * mm, v(-20.07, -19.04) * mm]});
            skFitSpline(sketch, "E3310", {"points": [v(-20.07, -19.04) * mm, v(-19.9, -19.2) * mm, v(-19.85, -19.44) * mm, v(-19.95, -19.63) * mm]});
            skFitSpline(sketch, "E3311", {"points": [v(-19.95, -19.63) * mm, v(-20.06, -19.83) * mm, v(-20.3, -19.94) * mm, v(-20.52, -19.88) * mm]});
            skFitSpline(sketch, "E3312", {"points": [v(-20.52, -19.88) * mm, v(-20.62, -19.85) * mm, v(-20.71, -19.8) * mm, v(-20.8, -19.75) * mm]});
            skFitSpline(sketch, "E3313", {"points": [v(-20.8, -19.75) * mm, v(-21.1, -19.57) * mm, v(-21.4, -19.38) * mm, v(-21.72, -19.19) * mm]});
            skFitSpline(sketch, "E3314", {"points": [v(-21.72, -19.19) * mm, v(-21.74, -19.24) * mm, v(-21.76, -19.28) * mm, v(-21.78, -19.33) * mm]});
            skFitSpline(sketch, "E3315", {"points": [v(-21.78, -19.33) * mm, v(-21.92, -19.64) * mm, v(-22.05, -19.96) * mm, v(-22.18, -20.28) * mm]});
            skFitSpline(sketch, "E3316", {"points": [v(-22.18, -20.28) * mm, v(-22.26, -20.46) * mm, v(-22.38, -20.6) * mm, v(-22.58, -20.63) * mm]});
            skFitSpline(sketch, "E3317", {"points": [v(-22.58, -20.63) * mm, v(-22.94, -20.7) * mm, v(-23.23, -20.4) * mm, v(-23.15, -20.03) * mm]});
            skFitSpline(sketch, "E3318", {"points": [v(-23.15, -20.03) * mm, v(-23.1, -19.8) * mm, v(-23.02, -19.6) * mm, v(-22.94, -19.37) * mm]});
            skFitSpline(sketch, "E3319", {"points": [v(-22.94, -19.37) * mm, v(-22.86, -19.12) * mm, v(-22.78, -18.87) * mm, v(-22.7, -18.62) * mm]});
            skFitSpline(sketch, "E3320", {"points": [v(-22.7, -18.62) * mm, v(-22.66, -18.5) * mm, v(-22.68, -18.4) * mm, v(-22.8, -18.3) * mm]});
            skFitSpline(sketch, "E3321", {"points": [v(-22.8, -18.3) * mm, v(-23.28, -17.93) * mm, v(-23.75, -17.53) * mm, v(-24.24, -17.16) * mm]});
            skFitSpline(sketch, "E3322", {"points": [v(-24.24, -17.16) * mm, v(-24.53, -16.94) * mm, v(-24.6, -16.68) * mm, v(-24.55, -16.34) * mm]});
            skFitSpline(sketch, "E3323", {"points": [v(-24.55, -16.34) * mm, v(-24.5, -16.1) * mm, v(-24.5, -15.85) * mm, v(-24.47, -15.6) * mm]});
            skFitSpline(sketch, "E3324", {"points": [v(-24.47, -15.6) * mm, v(-24.43, -15.19) * mm, v(-24.38, -14.77) * mm, v(-24.33, -14.35) * mm]});
            skFitSpline(sketch, "E3325", {"points": [v(-24.33, -14.35) * mm, v(-24.32, -14.32) * mm, v(-24.33, -14.29) * mm, v(-24.34, -14.2) * mm]});
            skFitSpline(sketch, "E3326", {"points": [v(-24.34, -14.2) * mm, v(-24.4, -14.3) * mm, v(-24.43, -14.36) * mm, v(-24.46, -14.42) * mm]});
            skFitSpline(sketch, "E3327", {"points": [v(-24.46, -14.42) * mm, v(-24.77, -15.02) * mm, v(-25.09, -15.62) * mm, v(-25.4, -16.23) * mm]});
            skFitSpline(sketch, "E3328", {"points": [v(-25.4, -16.23) * mm, v(-25.46, -16.36) * mm, v(-25.51, -16.51) * mm, v(-25.59, -16.64) * mm]});
            skFitSpline(sketch, "E3329", {"points": [v(-25.59, -16.64) * mm, v(-25.72, -16.88) * mm, v(-25.96, -16.97) * mm, v(-26.2, -16.88) * mm]});
            skFitSpline(sketch, "E3330", {"points": [v(-26.2, -16.88) * mm, v(-26.43, -16.8) * mm, v(-26.57, -16.54) * mm, v(-26.48, -16.3) * mm]});
            skFitSpline(sketch, "E3331", {"points": [v(-26.48, -16.3) * mm, v(-26.41, -16.1) * mm, v(-26.33, -15.91) * mm, v(-26.23, -15.73) * mm]});
            skFitSpline(sketch, "E3332", {"points": [v(-26.23, -15.73) * mm, v(-25.69, -14.67) * mm, v(-25.14, -13.61) * mm, v(-24.6, -12.56) * mm]});
            skFitSpline(sketch, "E3333", {"points": [v(-24.6, -12.56) * mm, v(-24.53, -12.43) * mm, v(-24.51, -12.3) * mm, v(-24.55, -12.17) * mm]});
            skFitSpline(sketch, "E3334", {"points": [v(-24.55, -12.17) * mm, v(-24.67, -11.79) * mm, v(-24.78, -11.4) * mm, v(-24.91, -10.97) * mm]});
            skFitSpline(sketch, "E3335", {"points": [v(-24.91, -10.97) * mm, v(-24.97, -11.08) * mm, v(-25, -11.15) * mm, v(-25.04, -11.22) * mm]});
            skFitSpline(sketch, "E3336", {"points": [v(-25.04, -11.22) * mm, v(-25.3, -11.75) * mm, v(-25.57, -12.28) * mm, v(-25.83, -12.8) * mm]});
            skFitSpline(sketch, "E3337", {"points": [v(-25.83, -12.8) * mm, v(-25.88, -12.9) * mm, v(-25.93, -12.99) * mm, v(-26, -13.07) * mm]});
            skFitSpline(sketch, "E3338", {"points": [v(-26, -13.07) * mm, v(-26.05, -13.17) * mm, v(-26.1, -13.26) * mm, v(-26.1, -13.38) * mm]});
            skFitSpline(sketch, "E3339", {"points": [v(-26.1, -13.38) * mm, v(-26.14, -13.63) * mm, v(-26.35, -13.78) * mm, v(-26.6, -13.77) * mm]});
            skFitSpline(sketch, "E3340", {"points": [v(-26.6, -13.77) * mm, v(-26.85, -13.76) * mm, v(-27.04, -13.58) * mm, v(-27.06, -13.34) * mm]});
            skFitSpline(sketch, "E3341", {"points": [v(-27.06, -13.34) * mm, v(-27.08, -13.1) * mm, v(-27.03, -12.9) * mm, v(-26.91, -12.7) * mm]});
            skFitSpline(sketch, "E3342", {"points": [v(-26.91, -12.7) * mm, v(-26.67, -12.28) * mm, v(-26.44, -11.86) * mm, v(-26.22, -11.43) * mm]});
            skFitSpline(sketch, "E3343", {"points": [v(-26.22, -11.43) * mm, v(-25.95, -10.88) * mm, v(-25.69, -10.33) * mm, v(-25.43, -9.77) * mm]});
            skFitSpline(sketch, "E3344", {"points": [v(-25.43, -9.77) * mm, v(-25.4, -9.71) * mm, v(-25.38, -9.63) * mm, v(-25.4, -9.57) * mm]});
            skFitSpline(sketch, "E3345", {"points": [v(-25.4, -9.57) * mm, v(-25.52, -9.22) * mm, v(-25.64, -8.88) * mm, v(-25.76, -8.53) * mm]});
            skFitSpline(sketch, "E3346", {"points": [v(-25.76, -8.53) * mm, v(-25.77, -8.51) * mm, v(-25.8, -8.5) * mm, v(-25.82, -8.46) * mm]});
            skFitSpline(sketch, "E3347", {"points": [v(-25.82, -8.46) * mm, v(-25.84, -8.5) * mm, v(-25.87, -8.53) * mm, v(-25.88, -8.56) * mm]});
            skFitSpline(sketch, "E3348", {"points": [v(-25.88, -8.56) * mm, v(-26.28, -9.38) * mm, v(-26.67, -10.2) * mm, v(-27.06, -11.03) * mm]});
            skFitSpline(sketch, "E3349", {"points": [v(-27.06, -11.03) * mm, v(-27.18, -11.3) * mm, v(-27.43, -11.42) * mm, v(-27.68, -11.33) * mm]});
            skFitSpline(sketch, "E3350", {"points": [v(-27.68, -11.33) * mm, v(-27.93, -11.24) * mm, v(-28.06, -10.98) * mm, v(-27.97, -10.7) * mm]});
            skFitSpline(sketch, "E3351", {"points": [v(-27.97, -10.7) * mm, v(-27.86, -10.42) * mm, v(-27.73, -10.15) * mm, v(-27.6, -9.88) * mm]});
            skFitSpline(sketch, "E3352", {"points": [v(-27.6, -9.88) * mm, v(-27.18, -9) * mm, v(-26.76, -8.13) * mm, v(-26.34, -7.26) * mm]});
            skFitSpline(sketch, "E3353", {"points": [v(-26.34, -7.26) * mm, v(-26.27, -7.14) * mm, v(-26.26, -7.02) * mm, v(-26.3, -6.88) * mm]});
            skFitSpline(sketch, "E3354", {"points": [v(-26.3, -6.88) * mm, v(-26.43, -6.47) * mm, v(-26.55, -6.05) * mm, v(-26.72, -5.63) * mm]});
            skFitSpline(sketch, "E3355", {"points": [v(-26.72, -5.63) * mm, v(-26.81, -5.81) * mm, v(-26.9, -6) * mm, v(-27, -6.2) * mm]});
            skFitSpline(sketch, "E3356", {"points": [v(-27, -6.2) * mm, v(-27.24, -6.67) * mm, v(-27.47, -7.15) * mm, v(-27.7, -7.63) * mm]});
            skFitSpline(sketch, "E3357", {"points": [v(-27.7, -7.63) * mm, v(-27.86, -7.94) * mm, v(-28.1, -7.97) * mm, v(-28.35, -7.9) * mm]});
            skFitSpline(sketch, "E3358", {"points": [v(-28.35, -7.9) * mm, v(-28.6, -7.82) * mm, v(-28.72, -7.51) * mm, v(-28.6, -7.24) * mm]});
            skFitSpline(sketch, "E3359", {"points": [v(-28.6, -7.24) * mm, v(-28.45, -6.92) * mm, v(-28.29, -6.6) * mm, v(-28.13, -6.29) * mm]});
            skFitSpline(sketch, "E3360", {"points": [v(-28.13, -6.29) * mm, v(-27.83, -5.67) * mm, v(-27.52, -5.04) * mm, v(-27.24, -4.4) * mm]});
            skFitSpline(sketch, "E3361", {"points": [v(-27.24, -4.4) * mm, v(-27.17, -4.26) * mm, v(-27.18, -4.04) * mm, v(-27.23, -3.87) * mm]});
            skFitSpline(sketch, "E3362", {"points": [v(-27.23, -3.87) * mm, v(-27.38, -3.36) * mm, v(-27.56, -2.86) * mm, v(-27.74, -2.35) * mm]});
            skFitSpline(sketch, "E3363", {"points": [v(-27.74, -2.35) * mm, v(-27.74, -2.34) * mm, v(-27.76, -2.33) * mm, v(-27.78, -2.3) * mm]});
            skFitSpline(sketch, "E3364", {"points": [v(-27.78, -2.3) * mm, v(-27.8, -2.35) * mm, v(-27.84, -2.38) * mm, v(-27.85, -2.42) * mm]});
            skFitSpline(sketch, "E3365", {"points": [v(-27.85, -2.42) * mm, v(-28.13, -3.32) * mm, v(-28.4, -4.22) * mm, v(-28.68, -5.12) * mm]});
            skFitSpline(sketch, "E3366", {"points": [v(-28.68, -5.12) * mm, v(-28.98, -6.09) * mm, v(-29.27, -7.06) * mm, v(-29.58, -8.02) * mm]});
            skFitSpline(sketch, "E3367", {"points": [v(-29.58, -8.02) * mm, v(-29.91, -9.05) * mm, v(-30.2, -10.09) * mm, v(-30.6, -11.09) * mm]});
            skFitSpline(sketch, "E3368", {"points": [v(-30.6, -11.09) * mm, v(-30.74, -11.4) * mm, v(-30.72, -11.65) * mm, v(-30.52, -11.95) * mm]});
            skFitSpline(sketch, "E3369", {"points": [v(-30.52, -11.95) * mm, v(-30.27, -12.33) * mm, v(-30.08, -12.76) * mm, v(-29.88, -13.17) * mm]});
            skFitSpline(sketch, "E3370", {"points": [v(-29.88, -13.17) * mm, v(-29.68, -13.58) * mm, v(-29.5, -14) * mm, v(-29.32, -14.42) * mm]});
            skFitSpline(sketch, "E3371", {"points": [v(-29.32, -14.42) * mm, v(-29.27, -14.54) * mm, v(-29.26, -14.66) * mm, v(-29.3, -14.8) * mm]});
            skFitSpline(sketch, "E3372", {"points": [v(-29.3, -14.8) * mm, v(-29.42, -15.14) * mm, v(-29.83, -15.26) * mm, v(-30.1, -15) * mm]});
            skFitSpline(sketch, "E3373", {"points": [v(-30.1, -15) * mm, v(-30.18, -14.92) * mm, v(-30.24, -14.8) * mm, v(-30.3, -14.69) * mm]});
            skFitSpline(sketch, "E3374", {"points": [v(-30.3, -14.69) * mm, v(-30.36, -14.55) * mm, v(-30.4, -14.4) * mm, v(-30.45, -14.26) * mm]});
            skFitSpline(sketch, "E3375", {"points": [v(-30.45, -14.26) * mm, v(-30.56, -14) * mm, v(-30.68, -13.75) * mm, v(-30.8, -13.5) * mm]});
            skFitSpline(sketch, "E3376", {"points": [v(-30.8, -13.5) * mm, v(-30.82, -13.43) * mm, v(-30.86, -13.37) * mm, v(-30.92, -13.32) * mm]});
            skFitSpline(sketch, "E3377", {"points": [v(-30.92, -13.32) * mm, v(-30.9, -13.54) * mm, v(-30.89, -13.77) * mm, v(-30.87, -14) * mm]});
            skFitSpline(sketch, "E3378", {"points": [v(-30.87, -14) * mm, v(-30.87, -14.08) * mm, v(-30.86, -14.16) * mm, v(-30.85, -14.24) * mm]});
            skFitSpline(sketch, "E3379", {"points": [v(-30.85, -14.24) * mm, v(-30.83, -14.5) * mm, v(-30.81, -14.76) * mm, v(-30.8, -15.02) * mm]});
            skFitSpline(sketch, "E3380", {"points": [v(-30.8, -15.02) * mm, v(-30.77, -15.21) * mm, v(-30.75, -15.4) * mm, v(-30.74, -15.6) * mm]});
            skFitSpline(sketch, "E3381", {"points": [v(-30.74, -15.6) * mm, v(-30.73, -15.76) * mm, v(-30.8, -15.9) * mm, v(-30.91, -16) * mm]});
            skFitSpline(sketch, "E3382", {"points": [v(-30.91, -16) * mm, v(-31.26, -16.34) * mm, v(-31.62, -16.67) * mm, v(-31.97, -17) * mm]});
            skFitSpline(sketch, "E3383", {"points": [v(-31.97, -17) * mm, v(-32.2, -17.23) * mm, v(-32.4, -17.46) * mm, v(-32.62, -17.68) * mm]});
            skFitSpline(sketch, "E3384", {"points": [v(-32.62, -17.68) * mm, v(-32.84, -17.9) * mm, v(-33.09, -17.97) * mm, v(-33.38, -17.83) * mm]});
            skFitSpline(sketch, "E3385", {"points": [v(-33.38, -17.83) * mm, v(-33.41, -17.8) * mm, v(-33.46, -17.8) * mm, v(-33.5, -17.8) * mm]});
            skFitSpline(sketch, "E3386", {"points": [v(-33.5, -17.8) * mm, v(-33.71, -17.75) * mm, v(-33.85, -17.62) * mm, v(-33.9, -17.4) * mm]});
            skFitSpline(sketch, "E3387", {"points": [v(-33.9, -17.4) * mm, v(-33.95, -17.26) * mm, v(-33.98, -17.11) * mm, v(-34, -16.96) * mm]});
            skFitSpline(sketch, "E3388", {"points": [v(-34, -16.96) * mm, v(-34.05, -16.65) * mm, v(-34.09, -16.33) * mm, v(-34.14, -16.02) * mm]});
            skFitSpline(sketch, "E3389", {"points": [v(-34.14, -16.02) * mm, v(-34.2, -15.63) * mm, v(-34.28, -15.25) * mm, v(-34.35, -14.87) * mm]});
            skFitSpline(sketch, "E3390", {"points": [v(-34.35, -14.87) * mm, v(-34.37, -14.71) * mm, v(-34.34, -14.56) * mm, v(-34.24, -14.44) * mm]});
            skFitSpline(sketch, "E3391", {"points": [v(-34.24, -14.44) * mm, v(-34.15, -14.34) * mm, v(-34.07, -14.24) * mm, v(-34, -14.14) * mm]});
            skFitSpline(sketch, "E3392", {"points": [v(-34, -14.14) * mm, v(-33.6, -13.7) * mm, v(-33.22, -13.25) * mm, v(-32.83, -12.8) * mm]});
            skFitSpline(sketch, "E3393", {"points": [v(-32.83, -12.8) * mm, v(-32.81, -12.78) * mm, v(-32.8, -12.76) * mm, v(-32.76, -12.7) * mm]});
            skFitSpline(sketch, "E3394", {"points": [v(-32.76, -12.7) * mm, v(-32.83, -12.72) * mm, v(-32.87, -12.73) * mm, v(-32.9, -12.75) * mm]});
            skFitSpline(sketch, "E3395", {"points": [v(-32.9, -12.75) * mm, v(-33.23, -12.93) * mm, v(-33.55, -13.12) * mm, v(-33.88, -13.3) * mm]});
            skFitSpline(sketch, "E3396", {"points": [v(-33.88, -13.3) * mm, v(-33.93, -13.33) * mm, v(-33.98, -13.39) * mm, v(-34.03, -13.42) * mm]});
            skFitSpline(sketch, "E3397", {"points": [v(-34.03, -13.42) * mm, v(-34.13, -13.48) * mm, v(-34.23, -13.55) * mm, v(-34.34, -13.59) * mm]});
            skFitSpline(sketch, "E3398", {"points": [v(-34.34, -13.59) * mm, v(-34.56, -13.65) * mm, v(-34.79, -13.56) * mm, v(-34.9, -13.37) * mm]});
            skFitSpline(sketch, "E3399", {"points": [v(-34.9, -13.37) * mm, v(-35, -13.18) * mm, v(-34.98, -12.93) * mm, v(-34.82, -12.77) * mm]});
            skFitSpline(sketch, "E3400", {"points": [v(-34.82, -12.77) * mm, v(-34.72, -12.68) * mm, v(-34.6, -12.6) * mm, v(-34.5, -12.53) * mm]});
            skFitSpline(sketch, "E3401", {"points": [v(-34.5, -12.53) * mm, v(-33.77, -12.15) * mm, v(-33.1, -11.7) * mm, v(-32.33, -11.39) * mm]});
            skFitSpline(sketch, "E3402", {"points": [v(-32.33, -11.39) * mm, v(-32.26, -11.36) * mm, v(-32.2, -11.32) * mm, v(-32.13, -11.3) * mm]});
            skFitSpline(sketch, "E3403", {"points": [v(-32.13, -11.3) * mm, v(-31.91, -11.26) * mm, v(-31.82, -11.12) * mm, v(-31.76, -10.92) * mm]});
            skFitSpline(sketch, "E3404", {"points": [v(-31.76, -10.92) * mm, v(-31.64, -10.48) * mm, v(-31.52, -10.04) * mm, v(-31.38, -9.6) * mm]});
            skFitSpline(sketch, "E3405", {"points": [v(-31.38, -9.6) * mm, v(-31.25, -9.18) * mm, v(-31.09, -8.75) * mm, v(-30.94, -8.32) * mm]});
            skFitSpline(sketch, "E3406", {"points": [v(-30.94, -8.32) * mm, v(-30.62, -7.34) * mm, v(-30.3, -6.36) * mm, v(-29.98, -5.38) * mm]});
            skFitSpline(sketch, "E3407", {"points": [v(-29.98, -5.38) * mm, v(-29.7, -4.53) * mm, v(-29.4, -3.69) * mm, v(-29.11, -2.84) * mm]});
            skFitSpline(sketch, "E3408", {"points": [v(-29.11, -2.84) * mm, v(-29.04, -2.63) * mm, v(-28.96, -2.42) * mm, v(-28.89, -2.21) * mm]});
            skFitSpline(sketch, "E3409", {"points": [v(-28.89, -2.21) * mm, v(-28.86, -2.14) * mm, v(-28.84, -2.07) * mm, v(-28.8, -1.95) * mm]});
            skFitSpline(sketch, "E3410", {"points": [v(-28.8, -1.95) * mm, v(-28.87, -1.98) * mm, v(-28.91, -1.99) * mm, v(-28.94, -2) * mm]});
            skFitSpline(sketch, "E3411", {"points": [v(-28.94, -2) * mm, v(-29.34, -2.3) * mm, v(-29.75, -2.57) * mm, v(-30.15, -2.87) * mm]});
            skFitSpline(sketch, "E3412", {"points": [v(-30.15, -2.87) * mm, v(-30.35, -3.02) * mm, v(-30.5, -3.22) * mm, v(-30.55, -3.49) * mm]});
            skFitSpline(sketch, "E3413", {"points": [v(-30.55, -3.49) * mm, v(-30.65, -4.07) * mm, v(-30.77, -4.65) * mm, v(-30.87, -5.23) * mm]});
            skFitSpline(sketch, "E3414", {"points": [v(-30.87, -5.23) * mm, v(-30.94, -5.58) * mm, v(-30.98, -5.94) * mm, v(-31.04, -6.3) * mm]});
            skFitSpline(sketch, "E3415", {"points": [v(-31.04, -6.3) * mm, v(-31.05, -6.36) * mm, v(-31.06, -6.44) * mm, v(-31.08, -6.5) * mm]});
            skFitSpline(sketch, "E3416", {"points": [v(-31.08, -6.5) * mm, v(-31.17, -6.75) * mm, v(-31.41, -6.89) * mm, v(-31.65, -6.83) * mm]});
            skFitSpline(sketch, "E3417", {"points": [v(-31.65, -6.83) * mm, v(-31.9, -6.76) * mm, v(-32.07, -6.52) * mm, v(-32.02, -6.27) * mm]});
            skFitSpline(sketch, "E3418", {"points": [v(-32.02, -6.27) * mm, v(-31.98, -6) * mm, v(-31.91, -5.72) * mm, v(-31.87, -5.44) * mm]});
            skFitSpline(sketch, "E3419", {"points": [v(-31.87, -5.44) * mm, v(-31.8, -5.04) * mm, v(-31.73, -4.63) * mm, v(-31.67, -4.22) * mm]});
            skFitSpline(sketch, "E3420", {"points": [v(-31.67, -4.22) * mm, v(-31.66, -4.16) * mm, v(-31.66, -4.1) * mm, v(-31.65, -4.03) * mm]});
            skFitSpline(sketch, "E3421", {"points": [v(-31.65, -4.03) * mm, v(-31.7, -4.05) * mm, v(-31.75, -4.06) * mm, v(-31.78, -4.08) * mm]});
            skFitSpline(sketch, "E3422", {"points": [v(-31.78, -4.08) * mm, v(-32.1, -4.33) * mm, v(-32.41, -4.58) * mm, v(-32.73, -4.81) * mm]});
            skFitSpline(sketch, "E3423", {"points": [v(-32.73, -4.81) * mm, v(-32.84, -4.9) * mm, v(-32.89, -4.99) * mm, v(-32.9, -5.11) * mm]});
            skFitSpline(sketch, "E3424", {"points": [v(-32.9, -5.11) * mm, v(-33, -5.65) * mm, v(-33.1, -6.18) * mm, v(-33.2, -6.71) * mm]});
            skFitSpline(sketch, "E3425", {"points": [v(-33.2, -6.71) * mm, v(-33.3, -7.35) * mm, v(-33.42, -7.99) * mm, v(-33.54, -8.62) * mm]});
            skFitSpline(sketch, "E3426", {"points": [v(-33.54, -8.62) * mm, v(-33.56, -8.73) * mm, v(-33.6, -8.84) * mm, v(-33.64, -8.94) * mm]});
            skFitSpline(sketch, "E3427", {"points": [v(-33.64, -8.94) * mm, v(-33.79, -9.23) * mm, v(-34.04, -9.26) * mm, v(-34.27, -9.19) * mm]});
            skFitSpline(sketch, "E3428", {"points": [v(-34.27, -9.19) * mm, v(-34.5, -9.11) * mm, v(-34.6, -8.85) * mm, v(-34.54, -8.6) * mm]});
            skFitSpline(sketch, "E3429", {"points": [v(-34.54, -8.6) * mm, v(-34.46, -8.2) * mm, v(-34.39, -7.8) * mm, v(-34.31, -7.4) * mm]});
            skFitSpline(sketch, "E3430", {"points": [v(-34.31, -7.4) * mm, v(-34.22, -6.89) * mm, v(-34.13, -6.38) * mm, v(-34.04, -5.87) * mm]});
            skFitSpline(sketch, "E3431", {"points": [v(-34.04, -5.87) * mm, v(-34.03, -5.85) * mm, v(-34.04, -5.82) * mm, v(-34.04, -5.76) * mm]});
            skFitSpline(sketch, "E3432", {"points": [v(-34.04, -5.76) * mm, v(-34.16, -5.84) * mm, v(-34.26, -5.9) * mm, v(-34.35, -5.97) * mm]});
            skFitSpline(sketch, "E3433", {"points": [v(-34.35, -5.97) * mm, v(-34.55, -6.1) * mm, v(-34.74, -6.25) * mm, v(-34.94, -6.38) * mm]});
            skFitSpline(sketch, "E3434", {"points": [v(-34.94, -6.38) * mm, v(-35.06, -6.45) * mm, v(-35.11, -6.54) * mm, v(-35.14, -6.68) * mm]});
            skFitSpline(sketch, "E3435", {"points": [v(-35.14, -6.68) * mm, v(-35.25, -7.38) * mm, v(-35.4, -8.08) * mm, v(-35.52, -8.78) * mm]});
            skFitSpline(sketch, "E3436", {"points": [v(-35.52, -8.78) * mm, v(-35.58, -9.16) * mm, v(-35.6, -9.54) * mm, v(-35.65, -9.92) * mm]});
            skFitSpline(sketch, "E3437", {"points": [v(-35.65, -9.92) * mm, v(-35.67, -10.14) * mm, v(-35.74, -10.34) * mm, v(-35.91, -10.5) * mm]});
            skFitSpline(sketch, "E3438", {"points": [v(-35.91, -10.5) * mm, v(-36.2, -10.75) * mm, v(-36.6, -10.64) * mm, v(-36.73, -10.29) * mm]});
            skFitSpline(sketch, "E3439", {"points": [v(-36.73, -10.29) * mm, v(-36.77, -10.15) * mm, v(-36.74, -10.04) * mm, v(-36.69, -9.92) * mm]});
            skFitSpline(sketch, "E3440", {"points": [v(-36.69, -9.92) * mm, v(-36.65, -9.83) * mm, v(-36.62, -9.74) * mm, v(-36.6, -9.65) * mm]});
            skFitSpline(sketch, "E3441", {"points": [v(-36.6, -9.65) * mm, v(-36.5, -8.97) * mm, v(-36.4, -8.3) * mm, v(-36.3, -7.61) * mm]});
            skFitSpline(sketch, "E3442", {"points": [v(-36.3, -7.61) * mm, v(-36.28, -7.53) * mm, v(-36.27, -7.45) * mm, v(-36.25, -7.33) * mm]});
            skFitSpline(sketch, "E3443", {"points": [v(-36.25, -7.33) * mm, v(-36.67, -7.58) * mm, v(-37.02, -7.85) * mm, v(-37.35, -8.15) * mm]});
            skFitSpline(sketch, "E3444", {"points": [v(-37.35, -8.15) * mm, v(-37.4, -8.2) * mm, v(-37.41, -8.28) * mm, v(-37.42, -8.34) * mm]});
            skFitSpline(sketch, "E3445", {"points": [v(-37.42, -8.34) * mm, v(-37.48, -8.72) * mm, v(-37.54, -9.1) * mm, v(-37.6, -9.48) * mm]});
            skFitSpline(sketch, "E3446", {"points": [v(-37.6, -9.48) * mm, v(-37.7, -10.16) * mm, v(-37.81, -10.83) * mm, v(-37.92, -11.51) * mm]});
            skFitSpline(sketch, "E3447", {"points": [v(-37.92, -11.51) * mm, v(-37.97, -11.82) * mm, v(-38.03, -12.12) * mm, v(-38.08, -12.43) * mm]});
            skFitSpline(sketch, "E3448", {"points": [v(-38.08, -12.43) * mm, v(-38.11, -12.68) * mm, v(-38.36, -12.9) * mm, v(-38.66, -12.83) * mm]});
            skFitSpline(sketch, "E3449", {"points": [v(-38.66, -12.83) * mm, v(-38.92, -12.77) * mm, v(-39.08, -12.51) * mm, v(-39.03, -12.22) * mm]});
            skFitSpline(sketch, "E3450", {"points": [v(-39.03, -12.22) * mm, v(-38.9, -11.41) * mm, v(-38.76, -10.6) * mm, v(-38.63, -9.8) * mm]});
            skFitSpline(sketch, "E3451", {"points": [v(-38.63, -9.8) * mm, v(-38.62, -9.74) * mm, v(-38.62, -9.69) * mm, v(-38.62, -9.57) * mm]});
            skFitSpline(sketch, "E3452", {"points": [v(-38.62, -9.57) * mm, v(-38.72, -9.73) * mm, v(-38.78, -9.84) * mm, v(-38.84, -9.94) * mm]});
            skFitSpline(sketch, "E3453", {"points": [v(-38.84, -9.94) * mm, v(-39.1, -10.36) * mm, v(-39.34, -10.78) * mm, v(-39.58, -11.2) * mm]});
            skFitSpline(sketch, "E3454", {"points": [v(-39.58, -11.2) * mm, v(-39.64, -11.3) * mm, v(-39.69, -11.4) * mm, v(-39.74, -11.5) * mm]});
            skFitSpline(sketch, "E3455", {"points": [v(-39.74, -11.5) * mm, v(-39.86, -11.74) * mm, v(-40.04, -11.88) * mm, v(-40.32, -11.89) * mm]});
            skFitSpline(sketch, "E3456", {"points": [v(-40.32, -11.89) * mm, v(-40.46, -11.89) * mm, v(-40.6, -11.9) * mm, v(-40.73, -11.9) * mm]});
            skFitSpline(sketch, "E3457", {"points": [v(-40.73, -11.9) * mm, v(-41.26, -11.93) * mm, v(-41.78, -11.96) * mm, v(-42.3, -11.98) * mm]});
            skFitSpline(sketch, "E3458", {"points": [v(-42.3, -11.98) * mm, v(-42.44, -11.99) * mm, v(-42.5, -12.06) * mm, v(-42.53, -12.16) * mm]});
            skFitSpline(sketch, "E3459", {"points": [v(-42.53, -12.16) * mm, v(-42.6, -12.4) * mm, v(-42.68, -12.64) * mm, v(-42.76, -12.87) * mm]});
            skFitSpline(sketch, "E3460", {"points": [v(-42.76, -12.87) * mm, v(-42.83, -13.09) * mm, v(-42.9, -13.3) * mm, v(-42.98, -13.53) * mm]});
            skFitSpline(sketch, "E3461", {"points": [v(-42.98, -13.53) * mm, v(-43.08, -13.81) * mm, v(-43.32, -13.95) * mm, v(-43.57, -13.87) * mm]});
            skFitSpline(sketch, "E3462", {"points": [v(-43.57, -13.87) * mm, v(-43.84, -13.8) * mm, v(-43.99, -13.54) * mm, v(-43.93, -13.25) * mm]});
            skFitSpline(sketch, "E3463", {"points": [v(-43.93, -13.25) * mm, v(-43.9, -13.1) * mm, v(-43.86, -12.94) * mm, v(-43.82, -12.79) * mm]});
            skFitSpline(sketch, "E3464", {"points": [v(-43.82, -12.79) * mm, v(-43.76, -12.55) * mm, v(-43.7, -12.31) * mm, v(-43.65, -12.06) * mm]});
            skFitSpline(sketch, "E3465", {"points": [v(-43.65, -12.06) * mm, v(-44, -12.03) * mm, v(-44.32, -12) * mm, v(-44.64, -11.98) * mm]});
            skFitSpline(sketch, "E3466", {"points": [v(-44.64, -11.98) * mm, v(-44.75, -11.97) * mm, v(-44.85, -11.96) * mm, v(-44.95, -11.94) * mm]});
            skFitSpline(sketch, "E3467", {"points": [v(-44.95, -11.94) * mm, v(-45.21, -11.89) * mm, v(-45.36, -11.67) * mm, v(-45.34, -11.4) * mm]});
            skFitSpline(sketch, "E3468", {"points": [v(-45.34, -11.4) * mm, v(-45.32, -11.15) * mm, v(-45.13, -10.98) * mm, v(-44.87, -10.98) * mm]});
            skFitSpline(sketch, "E3469", {"points": [v(-44.87, -10.98) * mm, v(-44.42, -10.97) * mm, v(-43.98, -10.97) * mm, v(-43.53, -10.98) * mm]});
            skFitSpline(sketch, "E3470", {"points": [v(-43.53, -10.98) * mm, v(-43.32, -10.98) * mm, v(-43.19, -10.91) * mm, v(-43.1, -10.69) * mm]});
            skFitSpline(sketch, "E3471", {"points": [v(-43.1, -10.69) * mm, v(-42.92, -10.13) * mm, v(-42.7, -9.58) * mm, v(-42.5, -9.02) * mm]});
            skFitSpline(sketch, "E3472", {"points": [v(-42.5, -9.02) * mm, v(-42.38, -8.73) * mm, v(-42.2, -8.54) * mm, v(-41.87, -8.52) * mm]});
            skFitSpline(sketch, "E3473", {"points": [v(-41.87, -8.52) * mm, v(-41.68, -8.5) * mm, v(-41.5, -8.43) * mm, v(-41.31, -8.39) * mm]});
            skFitSpline(sketch, "E3474", {"points": [v(-41.31, -8.39) * mm, v(-40.86, -8.3) * mm, v(-40.4, -8.2) * mm, v(-39.95, -8.1) * mm]});
            skFitSpline(sketch, "E3475", {"points": [v(-39.95, -8.1) * mm, v(-39.88, -8.1) * mm, v(-39.82, -8.07) * mm, v(-39.75, -8.02) * mm]});
            skFitSpline(sketch, "E3476", {"points": [v(-39.75, -8.02) * mm, v(-40.08, -7.97) * mm, v(-40.4, -7.92) * mm, v(-40.73, -7.87) * mm]});
            skFitSpline(sketch, "E3477", {"points": [v(-40.73, -7.87) * mm, v(-41.13, -7.8) * mm, v(-41.54, -7.73) * mm, v(-41.95, -7.66) * mm]});
            skFitSpline(sketch, "E3478", {"points": [v(-41.95, -7.66) * mm, v(-42.09, -7.64) * mm, v(-42.22, -7.63) * mm, v(-42.36, -7.62) * mm]});
            skFitSpline(sketch, "E3479", {"points": [v(-42.36, -7.62) * mm, v(-42.5, -7.6) * mm, v(-42.63, -7.54) * mm, v(-42.73, -7.43) * mm]});
            skFitSpline(sketch, "E3480", {"points": [v(-42.73, -7.43) * mm, v(-42.85, -7.28) * mm, v(-42.88, -7.1) * mm, v(-42.8, -6.93) * mm]});
            skFitSpline(sketch, "E3481", {"points": [v(-42.8, -6.93) * mm, v(-42.72, -6.76) * mm, v(-42.6, -6.64) * mm, v(-42.4, -6.66) * mm]});
            skFitSpline(sketch, "E3482", {"points": [v(-42.4, -6.66) * mm, v(-42.05, -6.69) * mm, v(-41.71, -6.73) * mm, v(-41.37, -6.78) * mm]});
            skFitSpline(sketch, "E3483", {"points": [v(-41.37, -6.78) * mm, v(-40.7, -6.87) * mm, v(-40.03, -6.98) * mm, v(-39.36, -7.1) * mm]});
            skFitSpline(sketch, "E3484", {"points": [v(-39.36, -7.1) * mm, v(-39.04, -7.14) * mm, v(-38.72, -7.2) * mm, v(-38.4, -7.26) * mm]});
            skFitSpline(sketch, "E3485", {"points": [v(-38.4, -7.26) * mm, v(-38.15, -7.32) * mm, v(-37.95, -7.29) * mm, v(-37.75, -7.14) * mm]});
            skFitSpline(sketch, "E3486", {"points": [v(-37.75, -7.14) * mm, v(-37.46, -6.92) * mm, v(-37.16, -6.72) * mm, v(-36.89, -6.47) * mm]});
            skFitSpline(sketch, "E3487", {"points": [v(-36.89, -6.47) * mm, v(-37.1, -6.44) * mm, v(-37.34, -6.42) * mm, v(-37.56, -6.38) * mm]});
            skFitSpline(sketch, "E3488", {"points": [v(-37.56, -6.38) * mm, v(-38.1, -6.29) * mm, v(-38.66, -6.2) * mm, v(-39.2, -6.1) * mm]});
            skFitSpline(sketch, "E3489", {"points": [v(-39.2, -6.1) * mm, v(-39.3, -6.09) * mm, v(-39.4, -6.1) * mm, v(-39.5, -6.1) * mm]});
            skFitSpline(sketch, "E3490", {"points": [v(-39.5, -6.1) * mm, v(-39.77, -6.1) * mm, v(-39.96, -5.98) * mm, v(-40.03, -5.72) * mm]});
            skFitSpline(sketch, "E3491", {"points": [v(-40.03, -5.72) * mm, v(-40.08, -5.52) * mm, v(-39.95, -5.27) * mm, v(-39.73, -5.17) * mm]});
            skFitSpline(sketch, "E3492", {"points": [v(-39.73, -5.17) * mm, v(-39.54, -5.07) * mm, v(-39.33, -5.06) * mm, v(-39.13, -5.12) * mm]});
            skFitSpline(sketch, "E3493", {"points": [v(-39.13, -5.12) * mm, v(-38.45, -5.3) * mm, v(-37.76, -5.38) * mm, v(-37.08, -5.47) * mm]});
            skFitSpline(sketch, "E3494", {"points": [v(-37.08, -5.47) * mm, v(-36.66, -5.52) * mm, v(-36.25, -5.58) * mm, v(-35.84, -5.63) * mm]});
            skFitSpline(sketch, "E3495", {"points": [v(-35.84, -5.63) * mm, v(-35.77, -5.64) * mm, v(-35.68, -5.62) * mm, v(-35.62, -5.58) * mm]});
            skFitSpline(sketch, "E3496", {"points": [v(-35.62, -5.58) * mm, v(-35.33, -5.37) * mm, v(-35.05, -5.15) * mm, v(-34.77, -4.93) * mm]});
            skFitSpline(sketch, "E3497", {"points": [v(-34.77, -4.93) * mm, v(-34.75, -4.92) * mm, v(-34.74, -4.9) * mm, v(-34.7, -4.85) * mm]});
            skFitSpline(sketch, "E3498", {"points": [v(-34.7, -4.85) * mm, v(-34.9, -4.82) * mm, v(-35.06, -4.78) * mm, v(-35.23, -4.76) * mm]});
            skFitSpline(sketch, "E3499", {"points": [v(-35.23, -4.76) * mm, v(-36.01, -4.66) * mm, v(-36.8, -4.56) * mm, v(-37.58, -4.46) * mm]});
            skFitSpline(sketch, "E3500", {"points": [v(-37.58, -4.46) * mm, v(-37.83, -4.43) * mm, v(-38.03, -4.23) * mm, v(-38.03, -3.98) * mm]});
            skFitSpline(sketch, "E3501", {"points": [v(-38.03, -3.98) * mm, v(-38.03, -3.73) * mm, v(-37.82, -3.5) * mm, v(-37.55, -3.51) * mm]});
            skFitSpline(sketch, "E3502", {"points": [v(-37.55, -3.51) * mm, v(-37.24, -3.52) * mm, v(-36.93, -3.56) * mm, v(-36.62, -3.6) * mm]});
            skFitSpline(sketch, "E3503", {"points": [v(-36.62, -3.6) * mm, v(-36.19, -3.65) * mm, v(-35.75, -3.72) * mm, v(-35.32, -3.78) * mm]});
            skFitSpline(sketch, "E3504", {"points": [v(-35.32, -3.78) * mm, v(-34.77, -3.85) * mm, v(-34.21, -3.93) * mm, v(-33.66, -4) * mm]});
            skFitSpline(sketch, "E3505", {"points": [v(-33.66, -4) * mm, v(-33.6, -4) * mm, v(-33.53, -4) * mm, v(-33.48, -3.98) * mm]});
            skFitSpline(sketch, "E3506", {"points": [v(-33.48, -3.98) * mm, v(-33.1, -3.72) * mm, v(-32.71, -3.46) * mm, v(-32.33, -3.2) * mm]});
            skFitSpline(sketch, "E3507", {"points": [v(-32.33, -3.2) * mm, v(-32.32, -3.19) * mm, v(-32.32, -3.16) * mm, v(-32.31, -3.13) * mm]});
            skFitSpline(sketch, "E3508", {"points": [v(-32.31, -3.13) * mm, v(-32.5, -3.1) * mm, v(-32.68, -3.06) * mm, v(-32.86, -3.03) * mm]});
            skFitSpline(sketch, "E3509", {"points": [v(-32.86, -3.03) * mm, v(-33.26, -2.97) * mm, v(-33.65, -2.9) * mm, v(-34.05, -2.85) * mm]});
            skFitSpline(sketch, "E3510", {"points": [v(-34.05, -2.85) * mm, v(-34.2, -2.83) * mm, v(-34.36, -2.81) * mm, v(-34.52, -2.79) * mm]});
            skFitSpline(sketch, "E3511", {"points": [v(-34.52, -2.79) * mm, v(-34.83, -2.74) * mm, v(-35, -2.52) * mm, v(-34.96, -2.24) * mm]});
            skFitSpline(sketch, "E3512", {"points": [v(-34.96, -2.24) * mm, v(-34.93, -1.98) * mm, v(-34.7, -1.8) * mm, v(-34.4, -1.83) * mm]});
            skFitSpline(sketch, "E3513", {"points": [v(-34.4, -1.83) * mm, v(-34.09, -1.86) * mm, v(-33.77, -1.92) * mm, v(-33.46, -1.96) * mm]});
            skFitSpline(sketch, "E3514", {"points": [v(-33.46, -1.96) * mm, v(-32.93, -2.04) * mm, v(-32.4, -2.12) * mm, v(-31.87, -2.2) * mm]});
            skFitSpline(sketch, "E3515", {"points": [v(-31.87, -2.2) * mm, v(-31.8, -2.2) * mm, v(-31.71, -2.22) * mm, v(-31.63, -2.23) * mm]});
            skFitSpline(sketch, "E3516", {"points": [v(-31.63, -2.23) * mm, v(-31.26, -2.31) * mm, v(-30.93, -2.22) * mm, v(-30.63, -2) * mm]});
            skFitSpline(sketch, "E3517", {"points": [v(-30.63, -2) * mm, v(-30.28, -1.73) * mm, v(-29.92, -1.46) * mm, v(-29.56, -1.2) * mm]});
            skFitSpline(sketch, "E3518", {"points": [v(-29.56, -1.2) * mm, v(-29.53, -1.16) * mm, v(-29.5, -1.13) * mm, v(-29.44, -1.06) * mm]});
            skFitSpline(sketch, "E3519", {"points": [v(-29.44, -1.06) * mm, v(-29.63, -1.06) * mm, v(-29.78, -1.06) * mm, v(-29.93, -1.06) * mm]});
            skFitSpline(sketch, "E3520", {"points": [v(-29.93, -1.06) * mm, v(-30.16, -1.06) * mm, v(-30.39, -1.06) * mm, v(-30.62, -1.06) * mm]});
            skFitSpline(sketch, "E3521", {"points": [v(-30.62, -1.06) * mm, v(-30.96, -1.07) * mm, v(-31.3, -1.07) * mm, v(-31.65, -1.08) * mm]});
            skFitSpline(sketch, "E3522", {"points": [v(-31.65, -1.08) * mm, v(-31.68, -1.08) * mm, v(-31.71, -1.09) * mm, v(-31.74, -1.09) * mm]});
            skFitSpline(sketch, "E3523", {"points": [v(-31.74, -1.09) * mm, v(-32.46, -1.1) * mm, v(-33.18, -1.13) * mm, v(-33.9, -1.14) * mm]});
            skFitSpline(sketch, "E3524", {"points": [v(-33.9, -1.14) * mm, v(-34.18, -1.14) * mm, v(-34.47, -1.1) * mm, v(-34.76, -1.1) * mm]});
            skFitSpline(sketch, "E3525", {"points": [v(-34.76, -1.1) * mm, v(-35.7, -1.12) * mm, v(-36.63, -1.15) * mm, v(-37.56, -1.15) * mm]});
            skFitSpline(sketch, "E3526", {"points": [v(-37.56, -1.15) * mm, v(-38.04, -1.15) * mm, v(-38.52, -1.12) * mm, v(-39, -1.1) * mm]});
            skFitSpline(sketch, "E3527", {"points": [v(-39, -1.1) * mm, v(-39.12, -1.1) * mm, v(-39.2, -1.13) * mm, v(-39.29, -1.23) * mm]});
            skFitSpline(sketch, "E3528", {"points": [v(-39.29, -1.23) * mm, v(-39.7, -1.76) * mm, v(-40.18, -2.23) * mm, v(-40.7, -2.67) * mm]});
            skFitSpline(sketch, "E3529", {"points": [v(-40.7, -2.67) * mm, v(-40.96, -2.9) * mm, v(-41.22, -3.16) * mm, v(-41.5, -3.38) * mm]});
            skFitSpline(sketch, "E3530", {"points": [v(-41.5, -3.38) * mm, v(-41.8, -3.61) * mm, v(-42.2, -3.48) * mm, v(-42.3, -3.14) * mm]});
            skFitSpline(sketch, "E3531", {"points": [v(-42.3, -3.14) * mm, v(-42.36, -2.9) * mm, v(-42.27, -2.7) * mm, v(-42.08, -2.57) * mm]});
            skFitSpline(sketch, "E3532", {"points": [v(-42.08, -2.57) * mm, v(-41.69, -2.32) * mm, v(-41.4, -1.95) * mm, v(-41.03, -1.67) * mm]});
            skFitSpline(sketch, "E3533", {"points": [v(-41.03, -1.67) * mm, v(-41, -1.64) * mm, v(-40.96, -1.6) * mm, v(-40.91, -1.55) * mm]});
            skFitSpline(sketch, "E3534", {"points": [v(-40.91, -1.55) * mm, v(-41, -1.51) * mm, v(-41.06, -1.57) * mm, v(-41.12, -1.59) * mm]});
            skFitSpline(sketch, "E3535", {"points": [v(-41.12, -1.59) * mm, v(-41.72, -1.84) * mm, v(-42.33, -2.09) * mm, v(-42.93, -2.34) * mm]});
            skFitSpline(sketch, "E3536", {"points": [v(-42.93, -2.34) * mm, v(-43.14, -2.43) * mm, v(-43.32, -2.41) * mm, v(-43.52, -2.3) * mm]});
            skFitSpline(sketch, "E3537", {"points": [v(-43.52, -2.3) * mm, v(-44.13, -1.98) * mm, v(-44.74, -1.67) * mm, v(-45.35, -1.36) * mm]});
            skFitSpline(sketch, "E3538", {"points": [v(-45.35, -1.36) * mm, v(-45.37, -1.35) * mm, v(-45.38, -1.35) * mm, v(-45.4, -1.34) * mm]});
            skFitSpline(sketch, "E3539", {"points": [v(-45.4, -1.34) * mm, v(-46.07, -1) * mm, v(-45.96, -0.9) * mm, v(-45.96, -0.27) * mm]});
            skFitSpline(sketch, "E3540", {"points": [v(-45.96, -0.27) * mm, v(-45.96, -0.14) * mm, v(-45.87, -0.03) * mm, v(-45.76, 0.04) * mm]});
            skFitSpline(sketch, "E3541", {"points": [v(-45.76, 0.04) * mm, v(-45.62, 0.14) * mm, v(-45.46, 0.22) * mm, v(-45.3, 0.3) * mm]});
            skFitSpline(sketch, "E3542", {"points": [v(-45.3, 0.3) * mm, v(-44.98, 0.48) * mm, v(-44.64, 0.65) * mm, v(-44.3, 0.82) * mm]});
            skFitSpline(sketch, "E3543", {"points": [v(-44.3, 0.82) * mm, v(-44.01, 0.98) * mm, v(-43.72, 1.14) * mm, v(-43.42, 1.3) * mm]});
            skFitSpline(sketch, "E3544", {"points": [v(-43.42, 1.3) * mm, v(-43.3, 1.35) * mm, v(-43.16, 1.36) * mm, v(-43.02, 1.3) * mm]});
            skFitSpline(sketch, "E3545", {"points": [v(-43.02, 1.3) * mm, v(-42.89, 1.26) * mm, v(-42.76, 1.2) * mm, v(-42.62, 1.15) * mm]});
            skFitSpline(sketch, "E3546", {"points": [v(-42.62, 1.15) * mm, v(-42.07, 0.92) * mm, v(-41.52, 0.69) * mm, v(-40.97, 0.46) * mm]});
            skFitSpline(sketch, "E3547", {"points": [v(-40.97, 0.46) * mm, v(-40.95, 0.45) * mm, v(-40.94, 0.45) * mm, v(-40.89, 0.45) * mm]});
            skFitSpline(sketch, "E3548", {"points": [v(-40.89, 0.45) * mm, v(-40.94, 0.5) * mm, v(-40.96, 0.54) * mm, v(-41, 0.57) * mm]});
            skFitSpline(sketch, "E3549", {"points": [v(-41, 0.57) * mm, v(-41.26, 0.81) * mm, v(-41.53, 1.06) * mm, v(-41.8, 1.3) * mm]});
            skFitSpline(sketch, "E3550", {"points": [v(-41.8, 1.3) * mm, v(-41.85, 1.35) * mm, v(-41.93, 1.38) * mm, v(-41.99, 1.44) * mm]});
            skFitSpline(sketch, "E3551", {"points": [v(-41.99, 1.44) * mm, v(-42.07, 1.5) * mm, v(-42.16, 1.58) * mm, v(-42.22, 1.67) * mm]});
            skFitSpline(sketch, "E3552", {"points": [v(-42.22, 1.67) * mm, v(-42.37, 1.88) * mm, v(-42.34, 2.11) * mm, v(-42.17, 2.28) * mm]});
            skFitSpline(sketch, "E3553", {"points": [v(-42.17, 2.28) * mm, v(-42.02, 2.43) * mm, v(-41.74, 2.47) * mm, v(-41.55, 2.35) * mm]});
            skFitSpline(sketch, "E3554", {"points": [v(-41.55, 2.35) * mm, v(-41.42, 2.26) * mm, v(-41.3, 2.16) * mm, v(-41.18, 2.05) * mm]});
            skFitSpline(sketch, "E3555", {"points": [v(-41.18, 2.05) * mm, v(-40.9, 1.81) * mm, v(-40.64, 1.58) * mm, v(-40.38, 1.32) * mm]});
            skFitSpline(sketch, "E3556", {"points": [v(-40.38, 1.32) * mm, v(-40.02, 0.96) * mm, v(-39.67, 0.6) * mm, v(-39.33, 0.21) * mm]});
            skFitSpline(sketch, "E3557", {"points": [v(-39.33, 0.21) * mm, v(-39.22, 0.1) * mm, v(-39.12, 0.04) * mm, v(-38.96, 0.04) * mm]});
            skFitSpline(sketch, "E3558", {"points": [v(-38.96, 0.04) * mm, v(-38.46, 0.07) * mm, v(-37.96, 0.1) * mm, v(-37.45, 0.09) * mm]});
            skFitSpline(sketch, "E3559", {"points": [v(-37.45, 0.09) * mm, v(-36.58, 0.09) * mm, v(-35.71, 0.06) * mm, v(-34.84, 0.05) * mm]});
            skFitSpline(sketch, "E3560", {"points": [v(-34.84, 0.05) * mm, v(-34.5, 0.04) * mm, v(-34.15, 0.07) * mm, v(-33.81, 0.06) * mm]});
            skFitSpline(sketch, "E3561", {"points": [v(-33.81, 0.06) * mm, v(-32.8, 0.04) * mm, v(-31.8, 0.02) * mm, v(-30.8, 0) * mm]});
            skFitSpline(sketch, "E3562", {"points": [v(-30.8, 0) * mm, v(-30.36, 0) * mm, v(-29.92, 0) * mm, v(-29.45, 0) * mm]});
            skFitSpline(sketch, "E3563", {"points": [v(-29.45, 0) * mm, v(-29.48, 0.04) * mm, v(-29.49, 0.07) * mm, v(-29.5, 0.08) * mm]});
            skFitSpline(sketch, "E3564", {"points": [v(-29.5, 0.08) * mm, v(-29.94, 0.4) * mm, v(-30.35, 0.74) * mm, v(-30.8, 1.03) * mm]});
            skFitSpline(sketch, "E3565", {"points": [v(-30.8, 1.03) * mm, v(-30.98, 1.15) * mm, v(-31.2, 1.23) * mm, v(-31.45, 1.19) * mm]});
            skFitSpline(sketch, "E3566", {"points": [v(-31.45, 1.19) * mm, v(-32, 1.1) * mm, v(-32.56, 1.04) * mm, v(-33.1, 0.96) * mm]});
            skFitSpline(sketch, "E3567", {"points": [v(-33.1, 0.96) * mm, v(-33.45, 0.91) * mm, v(-33.79, 0.85) * mm, v(-34.12, 0.8) * mm]});
            skFitSpline(sketch, "E3568", {"points": [v(-34.12, 0.8) * mm, v(-34.23, 0.78) * mm, v(-34.35, 0.77) * mm, v(-34.46, 0.77) * mm]});
            skFitSpline(sketch, "E3569", {"points": [v(-34.46, 0.77) * mm, v(-34.74, 0.77) * mm, v(-34.94, 0.94) * mm, v(-34.96, 1.2) * mm]});
            skFitSpline(sketch, "E3570", {"points": [v(-34.96, 1.2) * mm, v(-34.98, 1.48) * mm, v(-34.8, 1.68) * mm, v(-34.51, 1.72) * mm]});
            skFitSpline(sketch, "E3571", {"points": [v(-34.51, 1.72) * mm, v(-34.27, 1.76) * mm, v(-34.02, 1.79) * mm, v(-33.78, 1.82) * mm]});
            skFitSpline(sketch, "E3572", {"points": [v(-33.78, 1.82) * mm, v(-33.33, 1.89) * mm, v(-32.88, 1.96) * mm, v(-32.43, 2.03) * mm]});
            skFitSpline(sketch, "E3573", {"points": [v(-32.43, 2.03) * mm, v(-32.4, 2.04) * mm, v(-32.36, 2.05) * mm, v(-32.27, 2.08) * mm]});
            skFitSpline(sketch, "E3574", {"points": [v(-32.27, 2.08) * mm, v(-32.37, 2.15) * mm, v(-32.44, 2.2) * mm, v(-32.51, 2.26) * mm]});
            skFitSpline(sketch, "E3575", {"points": [v(-32.51, 2.26) * mm, v(-32.81, 2.46) * mm, v(-33.11, 2.66) * mm, v(-33.4, 2.86) * mm]});
            skFitSpline(sketch, "E3576", {"points": [v(-33.4, 2.86) * mm, v(-33.49, 2.92) * mm, v(-33.57, 2.95) * mm, v(-33.67, 2.93) * mm]});
            skFitSpline(sketch, "E3577", {"points": [v(-33.67, 2.93) * mm, v(-34.17, 2.86) * mm, v(-34.67, 2.79) * mm, v(-35.17, 2.72) * mm]});
            skFitSpline(sketch, "E3578", {"points": [v(-35.17, 2.72) * mm, v(-35.83, 2.63) * mm, v(-36.5, 2.54) * mm, v(-37.16, 2.46) * mm]});
            skFitSpline(sketch, "E3579", {"points": [v(-37.16, 2.46) * mm, v(-37.28, 2.44) * mm, v(-37.4, 2.44) * mm, v(-37.52, 2.45) * mm]});
            skFitSpline(sketch, "E3580", {"points": [v(-37.52, 2.45) * mm, v(-37.8, 2.45) * mm, v(-38.02, 2.64) * mm, v(-38.03, 2.9) * mm]});
            skFitSpline(sketch, "E3581", {"points": [v(-38.03, 2.9) * mm, v(-38.04, 3.15) * mm, v(-37.83, 3.37) * mm, v(-37.56, 3.4) * mm]});
            skFitSpline(sketch, "E3582", {"points": [v(-37.56, 3.4) * mm, v(-37.38, 3.42) * mm, v(-37.2, 3.43) * mm, v(-37.02, 3.45) * mm]});
            skFitSpline(sketch, "E3583", {"points": [v(-37.02, 3.45) * mm, v(-36.28, 3.55) * mm, v(-35.55, 3.65) * mm, v(-34.81, 3.75) * mm]});
            skFitSpline(sketch, "E3584", {"points": [v(-34.81, 3.75) * mm, v(-34.79, 3.76) * mm, v(-34.76, 3.77) * mm, v(-34.68, 3.8) * mm]});
            skFitSpline(sketch, "E3585", {"points": [v(-34.68, 3.8) * mm, v(-34.81, 3.9) * mm, v(-34.9, 3.97) * mm, v(-35, 4.05) * mm]});
            skFitSpline(sketch, "E3586", {"points": [v(-35, 4.05) * mm, v(-35.2, 4.19) * mm, v(-35.38, 4.32) * mm, v(-35.56, 4.47) * mm]});
            skFitSpline(sketch, "E3587", {"points": [v(-35.56, 4.47) * mm, v(-35.65, 4.54) * mm, v(-35.74, 4.58) * mm, v(-35.86, 4.56) * mm]});
            skFitSpline(sketch, "E3588", {"points": [v(-35.86, 4.56) * mm, v(-36.79, 4.42) * mm, v(-37.71, 4.3) * mm, v(-38.63, 4.17) * mm]});
            skFitSpline(sketch, "E3589", {"points": [v(-38.63, 4.17) * mm, v(-38.78, 4.15) * mm, v(-38.91, 4.09) * mm, v(-39.05, 4.07) * mm]});
            skFitSpline(sketch, "E3590", {"points": [v(-39.05, 4.07) * mm, v(-39.22, 4.04) * mm, v(-39.39, 4.03) * mm, v(-39.55, 4.04) * mm]});
            skFitSpline(sketch, "E3591", {"points": [v(-39.55, 4.04) * mm, v(-39.75, 4.06) * mm, v(-39.9, 4.18) * mm, v(-40, 4.37) * mm]});
            skFitSpline(sketch, "E3592", {"points": [v(-40, 4.37) * mm, v(-40.15, 4.68) * mm, v(-39.86, 5.06) * mm, v(-39.6, 5.03) * mm]});
            skFitSpline(sketch, "E3593", {"points": [v(-39.6, 5.03) * mm, v(-39.27, 4.98) * mm, v(-38.98, 5.1) * mm, v(-38.68, 5.15) * mm]});
            skFitSpline(sketch, "E3594", {"points": [v(-38.68, 5.15) * mm, v(-38.12, 5.22) * mm, v(-37.56, 5.3) * mm, v(-37, 5.38) * mm]});
            skFitSpline(sketch, "E3595", {"points": [v(-37, 5.38) * mm, v(-36.97, 5.39) * mm, v(-36.94, 5.4) * mm, v(-36.87, 5.4) * mm]});
            skFitSpline(sketch, "E3596", {"points": [v(-36.87, 5.4) * mm, v(-36.92, 5.45) * mm, v(-36.94, 5.49) * mm, v(-36.97, 5.51) * mm]});
            skFitSpline(sketch, "E3597", {"points": [v(-36.97, 5.51) * mm, v(-37.28, 5.73) * mm, v(-37.58, 5.95) * mm, v(-37.9, 6.15) * mm]});
            skFitSpline(sketch, "E3598", {"points": [v(-37.9, 6.15) * mm, v(-37.97, 6.2) * mm, v(-38.08, 6.24) * mm, v(-38.16, 6.22) * mm]});
            skFitSpline(sketch, "E3599", {"points": [v(-38.16, 6.22) * mm, v(-39.32, 6.04) * mm, v(-40.48, 5.85) * mm, v(-41.63, 5.66) * mm]});
            skFitSpline(sketch, "E3600", {"points": [v(-41.63, 5.66) * mm, v(-41.84, 5.63) * mm, v(-42.04, 5.6) * mm, v(-42.25, 5.58) * mm]});
            skFitSpline(sketch, "E3601", {"points": [v(-42.25, 5.58) * mm, v(-42.56, 5.54) * mm, v(-42.8, 5.72) * mm, v(-42.84, 6) * mm]});
            skFitSpline(sketch, "E3602", {"points": [v(-42.84, 6) * mm, v(-42.87, 6.27) * mm, v(-42.68, 6.5) * mm, v(-42.38, 6.54) * mm]});
            skFitSpline(sketch, "E3603", {"points": [v(-42.38, 6.54) * mm, v(-41.55, 6.67) * mm, v(-40.71, 6.8) * mm, v(-39.88, 6.92) * mm]});
            skFitSpline(sketch, "E3604", {"points": [v(-39.88, 6.92) * mm, v(-39.84, 6.93) * mm, v(-39.8, 6.95) * mm, v(-39.77, 7) * mm]});
            skFitSpline(sketch, "E3605", {"points": [v(-39.77, 7) * mm, v(-40.17, 7.08) * mm, v(-40.57, 7.16) * mm, v(-40.97, 7.24) * mm]});
            skFitSpline(sketch, "E3606", {"points": [v(-40.97, 7.24) * mm, v(-41.32, 7.31) * mm, v(-41.67, 7.39) * mm, v(-42.02, 7.47) * mm]});
            skFitSpline(sketch, "E3607", {"points": [v(-42.02, 7.47) * mm, v(-42.24, 7.52) * mm, v(-42.38, 7.66) * mm, v(-42.46, 7.87) * mm]});
            skFitSpline(sketch, "E3608", {"points": [v(-42.46, 7.87) * mm, v(-42.57, 8.18) * mm, v(-42.67, 8.5) * mm, v(-42.79, 8.8) * mm]});
            skFitSpline(sketch, "E3609", {"points": [v(-42.79, 8.8) * mm, v(-42.9, 9.1) * mm, v(-43.04, 9.4) * mm, v(-43.15, 9.71) * mm]});
            skFitSpline(sketch, "E3610", {"points": [v(-43.15, 9.71) * mm, v(-43.2, 9.85) * mm, v(-43.3, 9.9) * mm, v(-43.42, 9.9) * mm]});
            skFitSpline(sketch, "E3611", {"points": [v(-43.42, 9.9) * mm, v(-43.65, 9.9) * mm, v(-43.89, 9.9) * mm, v(-44.12, 9.9) * mm]});
            skFitSpline(sketch, "E3612", {"points": [v(-44.12, 9.9) * mm, v(-44.35, 9.9) * mm, v(-44.58, 9.9) * mm, v(-44.81, 9.9) * mm]});
            skFitSpline(sketch, "E3613", {"points": [v(-44.81, 9.9) * mm, v(-45.13, 9.9) * mm, v(-45.32, 10.07) * mm, v(-45.34, 10.34) * mm]});
            skFitSpline(sketch, "E3614", {"points": [v(-45.34, 10.34) * mm, v(-45.36, 10.64) * mm, v(-45.18, 10.85) * mm, v(-44.87, 10.89) * mm]});
            skFitSpline(sketch, "E3615", {"points": [v(-44.87, 10.89) * mm, v(-44.47, 10.93) * mm, v(-44.07, 10.96) * mm, v(-43.65, 11) * mm]});
            skFitSpline(sketch, "E3616", {"points": [v(-43.65, 11) * mm, v(-43.7, 11.24) * mm, v(-43.76, 11.48) * mm, v(-43.82, 11.71) * mm]});
            skFitSpline(sketch, "E3617", {"points": [v(-43.82, 11.71) * mm, v(-43.85, 11.86) * mm, v(-43.9, 12) * mm, v(-43.93, 12.16) * mm]});
            skFitSpline(sketch, "E3618", {"points": [v(-43.93, 12.16) * mm, v(-43.94, 12.25) * mm, v(-43.94, 12.35) * mm, v(-43.92, 12.44) * mm]});
            skFitSpline(sketch, "E3619", {"points": [v(-43.92, 12.44) * mm, v(-43.88, 12.66) * mm, v(-43.7, 12.8) * mm, v(-43.48, 12.82) * mm]});
            skFitSpline(sketch, "E3620", {"points": [v(-43.48, 12.82) * mm, v(-43.27, 12.83) * mm, v(-43.08, 12.72) * mm, v(-43, 12.5) * mm]});
            skFitSpline(sketch, "E3621", {"points": [v(-43, 12.5) * mm, v(-42.9, 12.28) * mm, v(-42.84, 12.05) * mm, v(-42.76, 11.83) * mm]});
            skFitSpline(sketch, "E3622", {"points": [v(-42.76, 11.83) * mm, v(-42.69, 11.6) * mm, v(-42.61, 11.36) * mm, v(-42.54, 11.12) * mm]});
            skFitSpline(sketch, "E3623", {"points": [v(-42.54, 11.12) * mm, v(-42.5, 10.98) * mm, v(-42.4, 10.9) * mm, v(-42.24, 10.9) * mm]});
            skFitSpline(sketch, "E3624", {"points": [v(-42.24, 10.9) * mm, v(-41.7, 10.89) * mm, v(-41.17, 10.86) * mm, v(-40.64, 10.84) * mm]});
            skFitSpline(sketch, "E3625", {"points": [v(-40.64, 10.84) * mm, v(-40.48, 10.83) * mm, v(-40.33, 10.83) * mm, v(-40.18, 10.8) * mm]});
            skFitSpline(sketch, "E3626", {"points": [v(-40.18, 10.8) * mm, v(-39.98, 10.77) * mm, v(-39.85, 10.63) * mm, v(-39.75, 10.46) * mm]});
            skFitSpline(sketch, "E3627", {"points": [v(-39.75, 10.46) * mm, v(-39.4, 9.83) * mm, v(-39.03, 9.21) * mm, v(-38.68, 8.59) * mm]});
            skFitSpline(sketch, "E3628", {"points": [v(-38.68, 8.59) * mm, v(-38.67, 8.58) * mm, v(-38.65, 8.57) * mm, v(-38.63, 8.55) * mm]});
            skFitSpline(sketch, "E3629", {"points": [v(-38.63, 8.55) * mm, v(-38.63, 8.62) * mm, v(-38.62, 8.67) * mm, v(-38.63, 8.73) * mm]});
            skFitSpline(sketch, "E3630", {"points": [v(-38.63, 8.73) * mm, v(-38.73, 9.42) * mm, v(-38.84, 10.1) * mm, v(-38.95, 10.79) * mm]});
            skFitSpline(sketch, "E3631", {"points": [v(-38.95, 10.79) * mm, v(-38.97, 10.92) * mm, v(-39.01, 11.05) * mm, v(-39.03, 11.18) * mm]});
            skFitSpline(sketch, "E3632", {"points": [v(-39.03, 11.18) * mm, v(-39.08, 11.53) * mm, v(-38.82, 11.8) * mm, v(-38.48, 11.76) * mm]});
            skFitSpline(sketch, "E3633", {"points": [v(-38.48, 11.76) * mm, v(-38.28, 11.74) * mm, v(-38.13, 11.6) * mm, v(-38.08, 11.37) * mm]});
            skFitSpline(sketch, "E3634", {"points": [v(-38.08, 11.37) * mm, v(-38.02, 11.04) * mm, v(-37.96, 10.7) * mm, v(-37.9, 10.36) * mm]});
            skFitSpline(sketch, "E3635", {"points": [v(-37.9, 10.36) * mm, v(-37.8, 9.7) * mm, v(-37.7, 9.02) * mm, v(-37.59, 8.35) * mm]});
            skFitSpline(sketch, "E3636", {"points": [v(-37.59, 8.35) * mm, v(-37.53, 8) * mm, v(-37.48, 7.63) * mm, v(-37.42, 7.27) * mm]});
            skFitSpline(sketch, "E3637", {"points": [v(-37.42, 7.27) * mm, v(-37.4, 7.2) * mm, v(-37.39, 7.12) * mm, v(-37.34, 7.08) * mm]});
            skFitSpline(sketch, "E3638", {"points": [v(-37.34, 7.08) * mm, v(-37, 6.78) * mm, v(-36.66, 6.5) * mm, v(-36.25, 6.25) * mm]});
            skFitSpline(sketch, "E3639", {"points": [v(-36.25, 6.25) * mm, v(-36.28, 6.44) * mm, v(-36.3, 6.6) * mm, v(-36.33, 6.75) * mm]});
            skFitSpline(sketch, "E3640", {"points": [v(-36.33, 6.75) * mm, v(-36.46, 7.38) * mm, v(-36.56, 8) * mm, v(-36.61, 8.64) * mm]});
            skFitSpline(sketch, "E3641", {"points": [v(-36.61, 8.64) * mm, v(-36.62, 8.71) * mm, v(-36.65, 8.78) * mm, v(-36.68, 8.84) * mm]});
            skFitSpline(sketch, "E3642", {"points": [v(-36.68, 8.84) * mm, v(-36.8, 9.08) * mm, v(-36.75, 9.32) * mm, v(-36.55, 9.46) * mm]});
            skFitSpline(sketch, "E3643", {"points": [v(-36.55, 9.46) * mm, v(-36.36, 9.6) * mm, v(-36.1, 9.6) * mm, v(-35.91, 9.43) * mm]});
            skFitSpline(sketch, "E3644", {"points": [v(-35.91, 9.43) * mm, v(-35.76, 9.29) * mm, v(-35.66, 9.1) * mm, v(-35.65, 8.9) * mm]});
            skFitSpline(sketch, "E3645", {"points": [v(-35.65, 8.9) * mm, v(-35.62, 8.14) * mm, v(-35.46, 7.4) * mm, v(-35.32, 6.65) * mm]});
            skFitSpline(sketch, "E3646", {"points": [v(-35.32, 6.65) * mm, v(-35.25, 6.29) * mm, v(-35.2, 5.92) * mm, v(-35.12, 5.55) * mm]});
            skFitSpline(sketch, "E3647", {"points": [v(-35.12, 5.55) * mm, v(-35.1, 5.48) * mm, v(-35.07, 5.4) * mm, v(-35.02, 5.37) * mm]});
            skFitSpline(sketch, "E3648", {"points": [v(-35.02, 5.37) * mm, v(-34.72, 5.16) * mm, v(-34.42, 4.95) * mm, v(-34.12, 4.75) * mm]});
            skFitSpline(sketch, "E3649", {"points": [v(-34.12, 4.75) * mm, v(-34.1, 4.73) * mm, v(-34.07, 4.73) * mm, v(-34.02, 4.71) * mm]});
            skFitSpline(sketch, "E3650", {"points": [v(-34.02, 4.71) * mm, v(-34.07, 5) * mm, v(-34.11, 5.28) * mm, v(-34.16, 5.55) * mm]});
            skFitSpline(sketch, "E3651", {"points": [v(-34.16, 5.55) * mm, v(-34.27, 6.12) * mm, v(-34.37, 6.7) * mm, v(-34.48, 7.26) * mm]});
            skFitSpline(sketch, "E3652", {"points": [v(-34.48, 7.26) * mm, v(-34.5, 7.36) * mm, v(-34.52, 7.45) * mm, v(-34.54, 7.54) * mm]});
            skFitSpline(sketch, "E3653", {"points": [v(-34.54, 7.54) * mm, v(-34.6, 7.79) * mm, v(-34.5, 8.02) * mm, v(-34.27, 8.12) * mm]});
            skFitSpline(sketch, "E3654", {"points": [v(-34.27, 8.12) * mm, v(-34.05, 8.21) * mm, v(-33.8, 8.14) * mm, v(-33.67, 7.92) * mm]});
            skFitSpline(sketch, "E3655", {"points": [v(-33.67, 7.92) * mm, v(-33.6, 7.79) * mm, v(-33.56, 7.64) * mm, v(-33.53, 7.5) * mm]});
            skFitSpline(sketch, "E3656", {"points": [v(-33.53, 7.5) * mm, v(-33.34, 6.42) * mm, v(-33.13, 5.34) * mm, v(-32.96, 4.26) * mm]});
            skFitSpline(sketch, "E3657", {"points": [v(-32.96, 4.26) * mm, v(-32.91, 3.94) * mm, v(-32.75, 3.73) * mm, v(-32.5, 3.56) * mm]});
            skFitSpline(sketch, "E3658", {"points": [v(-32.5, 3.56) * mm, v(-32.23, 3.36) * mm, v(-31.97, 3.15) * mm, v(-31.65, 2.91) * mm]});
            skFitSpline(sketch, "E3659", {"points": [v(-31.65, 2.91) * mm, v(-31.68, 3.13) * mm, v(-31.7, 3.3) * mm, v(-31.72, 3.46) * mm]});
            skFitSpline(sketch, "E3660", {"points": [v(-31.72, 3.46) * mm, v(-31.82, 4.04) * mm, v(-31.92, 4.61) * mm, v(-32.02, 5.18) * mm]});
            skFitSpline(sketch, "E3661", {"points": [v(-32.02, 5.18) * mm, v(-32.07, 5.44) * mm, v(-31.9, 5.7) * mm, v(-31.66, 5.76) * mm]});
            skFitSpline(sketch, "E3662", {"points": [v(-31.66, 5.76) * mm, v(-31.4, 5.82) * mm, v(-31.15, 5.68) * mm, v(-31.08, 5.42) * mm]});
            skFitSpline(sketch, "E3663", {"points": [v(-31.08, 5.42) * mm, v(-31, 5.08) * mm, v(-30.96, 4.73) * mm, v(-30.9, 4.39) * mm]});
            skFitSpline(sketch, "E3664", {"points": [v(-30.9, 4.39) * mm, v(-30.77, 3.68) * mm, v(-30.66, 2.97) * mm, v(-30.5, 2.27) * mm]});
            skFitSpline(sketch, "E3665", {"points": [v(-30.5, 2.27) * mm, v(-30.47, 2.1) * mm, v(-30.33, 1.94) * mm, v(-30.2, 1.84) * mm]});
            skFitSpline(sketch, "E3666", {"points": [v(-30.2, 1.84) * mm, v(-29.78, 1.51) * mm, v(-29.34, 1.22) * mm, v(-28.9, 0.92) * mm]});
            skFitSpline(sketch, "E3667", {"points": [v(-28.9, 0.92) * mm, v(-28.89, 0.9) * mm, v(-28.86, 0.9) * mm, v(-28.82, 0.9) * mm]});
            skFitSpline(sketch, "E3668", {"points": [v(-28.82, 0.9) * mm, v(-28.83, 0.95) * mm, v(-28.83, 1) * mm, v(-28.85, 1.04) * mm]});
            skFitSpline(sketch, "E3669", {"points": [v(-28.85, 1.04) * mm, v(-29.16, 1.95) * mm, v(-29.46, 2.86) * mm, v(-29.77, 3.76) * mm]});
            skFitSpline(sketch, "E3670", {"points": [v(-29.77, 3.76) * mm, v(-30.08, 4.67) * mm, v(-30.4, 5.57) * mm, v(-30.7, 6.48) * mm]});
            skFitSpline(sketch, "E3671", {"points": [v(-30.7, 6.48) * mm, v(-31.04, 7.54) * mm, v(-31.44, 8.58) * mm, v(-31.7, 9.66) * mm]});
            skFitSpline(sketch, "E3672", {"points": [v(-31.7, 9.66) * mm, v(-31.78, 9.98) * mm, v(-31.94, 10.18) * mm, v(-32.27, 10.3) * mm]});
            skFitSpline(sketch, "E3673", {"points": [v(-32.27, 10.3) * mm, v(-32.74, 10.48) * mm, v(-33.18, 10.74) * mm, v(-33.62, 10.98) * mm]});
            skFitSpline(sketch, "E3674", {"points": [v(-33.62, 10.98) * mm, v(-33.99, 11.17) * mm, v(-34.34, 11.39) * mm, v(-34.7, 11.6) * mm]});
            skFitSpline(sketch, "E3675", {"points": [v(-34.7, 11.6) * mm, v(-34.8, 11.67) * mm, v(-34.88, 11.77) * mm, v(-34.92, 11.87) * mm]});
            skFitSpline(sketch, "E3676", {"points": [v(-34.92, 11.87) * mm, v(-35.06, 12.19) * mm, v(-34.84, 12.52) * mm, v(-34.5, 12.53) * mm]});
            skFitSpline(sketch, "E3677", {"points": [v(-34.5, 12.53) * mm, v(-34.34, 12.54) * mm, v(-34.2, 12.5) * mm, v(-34.1, 12.4) * mm]});
            skFitSpline(sketch, "E3678", {"points": [v(-34.1, 12.4) * mm, v(-33.72, 12.1) * mm, v(-33.27, 11.92) * mm, v(-32.86, 11.67) * mm]});
            skFitSpline(sketch, "E3679", {"points": [v(-32.86, 11.67) * mm, v(-32.85, 11.66) * mm, v(-32.83, 11.67) * mm, v(-32.79, 11.68) * mm]});
            skFitSpline(sketch, "E3680", {"points": [v(-32.79, 11.68) * mm, v(-32.92, 11.84) * mm, v(-33.05, 12) * mm, v(-33.18, 12.14) * mm]});
            skFitSpline(sketch, "E3681", {"points": [v(-33.18, 12.14) * mm, v(-33.52, 12.54) * mm, v(-33.86, 12.94) * mm, v(-34.2, 13.34) * mm]});
            skFitSpline(sketch, "E3682", {"points": [v(-34.2, 13.34) * mm, v(-34.34, 13.49) * mm, v(-34.38, 13.66) * mm, v(-34.34, 13.85) * mm]});
            skFitSpline(sketch, "E3683", {"points": [v(-34.34, 13.85) * mm, v(-34.24, 14.4) * mm, v(-34.14, 14.93) * mm, v(-34.05, 15.47) * mm]});
            skFitSpline(sketch, "E3684", {"points": [v(-34.05, 15.47) * mm, v(-34, 15.7) * mm, v(-33.99, 15.93) * mm, v(-33.95, 16.16) * mm]});
            skFitSpline(sketch, "E3685", {"points": [v(-33.95, 16.16) * mm, v(-33.9, 16.47) * mm, v(-33.76, 16.7) * mm, v(-33.42, 16.75) * mm]});
            skFitSpline(sketch, "E3686", {"points": [v(-33.42, 16.75) * mm, v(-33.38, 16.75) * mm, v(-33.35, 16.78) * mm, v(-33.3, 16.8) * mm]});
            skFitSpline(sketch, "E3687", {"points": [v(-33.3, 16.8) * mm, v(-33.1, 16.88) * mm, v(-32.92, 16.85) * mm, v(-32.75, 16.71) * mm]});
            skFitSpline(sketch, "E3688", {"points": [v(-32.75, 16.71) * mm, v(-32.62, 16.6) * mm, v(-32.5, 16.49) * mm, v(-32.38, 16.37) * mm]});
            skFitSpline(sketch, "E3689", {"points": [v(-32.38, 16.37) * mm, v(-32.16, 16.15) * mm, v(-31.95, 15.92) * mm, v(-31.72, 15.7) * mm]});
            skFitSpline(sketch, "E3690", {"points": [v(-31.72, 15.7) * mm, v(-31.45, 15.44) * mm, v(-31.17, 15.18) * mm, v(-30.9, 14.91) * mm]});
            skFitSpline(sketch, "E3691", {"points": [v(-30.9, 14.91) * mm, v(-30.78, 14.8) * mm, v(-30.73, 14.66) * mm, v(-30.74, 14.5) * mm]});
            skFitSpline(sketch, "E3692", {"points": [v(-30.74, 14.5) * mm, v(-30.77, 14.25) * mm, v(-30.8, 14) * mm, v(-30.82, 13.76) * mm]});
            skFitSpline(sketch, "E3693", {"points": [v(-30.82, 13.76) * mm, v(-30.83, 13.66) * mm, v(-30.84, 13.56) * mm, v(-30.85, 13.45) * mm]});
            skFitSpline(sketch, "E3694", {"points": [v(-30.85, 13.45) * mm, v(-30.88, 13.07) * mm, v(-30.9, 12.7) * mm, v(-30.93, 12.3) * mm]});
            skFitSpline(sketch, "E3695", {"points": [v(-30.93, 12.3) * mm, v(-30.93, 12.29) * mm, v(-30.92, 12.27) * mm, v(-30.9, 12.22) * mm]});
            skFitSpline(sketch, "E3696", {"points": [v(-30.9, 12.22) * mm, v(-30.87, 12.28) * mm, v(-30.85, 12.32) * mm, v(-30.83, 12.36) * mm]});
            skFitSpline(sketch, "E3697", {"points": [v(-30.83, 12.36) * mm, v(-30.67, 12.7) * mm, v(-30.51, 13.04) * mm, v(-30.36, 13.38) * mm]});
            skFitSpline(sketch, "E3698", {"points": [v(-30.36, 13.38) * mm, v(-30.33, 13.44) * mm, v(-30.32, 13.52) * mm, v(-30.3, 13.59) * mm]});
            skFitSpline(sketch, "E3699", {"points": [v(-30.3, 13.59) * mm, v(-30.27, 13.74) * mm, v(-30.19, 13.87) * mm, v(-30.07, 13.96) * mm]});
            skFitSpline(sketch, "E3700", {"points": [v(-30.07, 13.96) * mm, v(-29.9, 14.1) * mm, v(-29.68, 14.1) * mm, v(-29.5, 14) * mm]});
            skFitSpline(sketch, "E3701", {"points": [v(-29.5, 14) * mm, v(-29.34, 13.88) * mm, v(-29.24, 13.67) * mm, v(-29.3, 13.47) * mm]});
            skFitSpline(sketch, "E3702", {"points": [v(-29.3, 13.47) * mm, v(-29.33, 13.34) * mm, v(-29.36, 13.21) * mm, v(-29.42, 13.09) * mm]});
            skFitSpline(sketch, "E3703", {"points": [v(-29.42, 13.09) * mm, v(-29.62, 12.63) * mm, v(-29.83, 12.17) * mm, v(-30.05, 11.72) * mm]});
            skFitSpline(sketch, "E3704", {"points": [v(-30.05, 11.72) * mm, v(-30.24, 11.35) * mm, v(-30.46, 11) * mm, v(-30.67, 10.63) * mm]});
            skFitSpline(sketch, "E3705", {"points": [v(-30.67, 10.63) * mm, v(-30.72, 10.54) * mm, v(-30.75, 10.46) * mm, v(-30.7, 10.35) * mm]});
            skFitSpline(sketch, "E3706", {"points": [v(-30.7, 10.35) * mm, v(-30.53, 9.87) * mm, v(-30.36, 9.4) * mm, v(-30.2, 8.92) * mm]});
            skFitSpline(sketch, "E3707", {"points": [v(-30.2, 8.92) * mm, v(-30.06, 8.48) * mm, v(-29.93, 8.02) * mm, v(-29.79, 7.57) * mm]});
            skFitSpline(sketch, "E3708", {"points": [v(-29.79, 7.57) * mm, v(-29.54, 6.8) * mm, v(-29.27, 6.03) * mm, v(-29.03, 5.25) * mm]});
            skFitSpline(sketch, "E3709", {"points": [v(-29.03, 5.25) * mm, v(-28.81, 4.54) * mm, v(-28.61, 3.83) * mm, v(-28.4, 3.12) * mm]});
            skFitSpline(sketch, "E3710", {"points": [v(-28.4, 3.12) * mm, v(-28.22, 2.52) * mm, v(-28.03, 1.93) * mm, v(-27.84, 1.33) * mm]});
            skFitSpline(sketch, "E3711", {"points": [v(-27.84, 1.33) * mm, v(-27.83, 1.3) * mm, v(-27.81, 1.28) * mm, v(-27.79, 1.23) * mm]});
            skFitSpline(sketch, "E3712", {"points": [v(-27.79, 1.23) * mm, v(-27.76, 1.28) * mm, v(-27.73, 1.32) * mm, v(-27.71, 1.36) * mm]});
            skFitSpline(sketch, "E3713", {"points": [v(-27.71, 1.36) * mm, v(-27.55, 1.82) * mm, v(-27.38, 2.3) * mm, v(-27.24, 2.76) * mm]});
            skFitSpline(sketch, "E3714", {"points": [v(-27.24, 2.76) * mm, v(-27.17, 3) * mm, v(-27.16, 3.23) * mm, v(-27.28, 3.46) * mm]});
            skFitSpline(sketch, "E3715", {"points": [v(-27.28, 3.46) * mm, v(-27.6, 4.1) * mm, v(-27.92, 4.76) * mm, v(-28.24, 5.41) * mm]});
            skFitSpline(sketch, "E3716", {"points": [v(-28.24, 5.41) * mm, v(-28.36, 5.66) * mm, v(-28.48, 5.9) * mm, v(-28.6, 6.15) * mm]});
            skFitSpline(sketch, "E3717", {"points": [v(-28.6, 6.15) * mm, v(-28.66, 6.3) * mm, v(-28.67, 6.44) * mm, v(-28.6, 6.59) * mm]});
            skFitSpline(sketch, "E3718", {"points": [v(-28.6, 6.59) * mm, v(-28.52, 6.75) * mm, v(-28.4, 6.85) * mm, v(-28.2, 6.86) * mm]});
            skFitSpline(sketch, "E3719", {"points": [v(-28.2, 6.86) * mm, v(-28.01, 6.87) * mm, v(-27.86, 6.8) * mm, v(-27.76, 6.64) * mm]});
            skFitSpline(sketch, "E3720", {"points": [v(-27.76, 6.64) * mm, v(-27.69, 6.52) * mm, v(-27.64, 6.4) * mm, v(-27.58, 6.27) * mm]});
            skFitSpline(sketch, "E3721", {"points": [v(-27.58, 6.27) * mm, v(-27.3, 5.7) * mm, v(-27, 5.14) * mm, v(-26.7, 4.52) * mm]});
            skFitSpline(sketch, "E3722", {"points": [v(-26.7, 4.52) * mm, v(-26.64, 4.68) * mm, v(-26.6, 4.8) * mm, v(-26.56, 4.93) * mm]});
            skFitSpline(sketch, "E3723", {"points": [v(-26.56, 4.93) * mm, v(-26.47, 5.24) * mm, v(-26.38, 5.54) * mm, v(-26.3, 5.85) * mm]});
            skFitSpline(sketch, "E3724", {"points": [v(-26.3, 5.85) * mm, v(-26.26, 5.95) * mm, v(-26.27, 6.04) * mm, v(-26.32, 6.15) * mm]});
            skFitSpline(sketch, "E3725", {"points": [v(-26.32, 6.15) * mm, v(-26.58, 6.68) * mm, v(-26.83, 7.2) * mm, v(-27.1, 7.74) * mm]});
            skFitSpline(sketch, "E3726", {"points": [v(-27.1, 7.74) * mm, v(-27.35, 8.27) * mm, v(-27.6, 8.8) * mm, v(-27.86, 9.34) * mm]});
            skFitSpline(sketch, "E3727", {"points": [v(-27.86, 9.34) * mm, v(-27.9, 9.45) * mm, v(-27.95, 9.56) * mm, v(-27.98, 9.68) * mm]});
            skFitSpline(sketch, "E3728", {"points": [v(-27.98, 9.68) * mm, v(-28.04, 9.93) * mm, v(-27.91, 10.2) * mm, v(-27.68, 10.26) * mm]});
            skFitSpline(sketch, "E3729", {"points": [v(-27.68, 10.26) * mm, v(-27.44, 10.33) * mm, v(-27.2, 10.27) * mm, v(-27.07, 9.99) * mm]});
            skFitSpline(sketch, "E3730", {"points": [v(-27.07, 9.99) * mm, v(-26.74, 9.3) * mm, v(-26.42, 8.6) * mm, v(-26.09, 7.9) * mm]});
            skFitSpline(sketch, "E3731", {"points": [v(-26.09, 7.9) * mm, v(-26, 7.73) * mm, v(-25.92, 7.57) * mm, v(-25.81, 7.35) * mm]});
            skFitSpline(sketch, "E3732", {"points": [v(-25.81, 7.35) * mm, v(-25.75, 7.51) * mm, v(-25.7, 7.62) * mm, v(-25.67, 7.73) * mm]});
            skFitSpline(sketch, "E3733", {"points": [v(-25.67, 7.73) * mm, v(-25.58, 7.96) * mm, v(-25.5, 8.18) * mm, v(-25.43, 8.4) * mm]});
            skFitSpline(sketch, "E3734", {"points": [v(-25.43, 8.4) * mm, v(-25.38, 8.52) * mm, v(-25.38, 8.62) * mm, v(-25.44, 8.75) * mm]});
            skFitSpline(sketch, "E3735", {"points": [v(-25.44, 8.75) * mm, v(-25.72, 9.3) * mm, v(-25.97, 9.86) * mm, v(-26.24, 10.4) * mm]});
            skFitSpline(sketch, "E3736", {"points": [v(-26.24, 10.4) * mm, v(-26.45, 10.82) * mm, v(-26.68, 11.23) * mm, v(-26.91, 11.62) * mm]});
            skFitSpline(sketch, "E3737", {"points": [v(-26.91, 11.62) * mm, v(-27.03, 11.83) * mm, v(-27.08, 12.04) * mm, v(-27.06, 12.27) * mm]});
            skFitSpline(sketch, "E3738", {"points": [v(-27.06, 12.27) * mm, v(-27.04, 12.5) * mm, v(-26.84, 12.7) * mm, v(-26.6, 12.7) * mm]});
            skFitSpline(sketch, "E3739", {"points": [v(-26.6, 12.7) * mm, v(-26.36, 12.72) * mm, v(-26.14, 12.55) * mm, v(-26.1, 12.31) * mm]});
            skFitSpline(sketch, "E3740", {"points": [v(-26.1, 12.31) * mm, v(-26.1, 12.18) * mm, v(-26.04, 12.1) * mm, v(-25.98, 11.99) * mm]});
            skFitSpline(sketch, "E3741", {"points": [v(-25.98, 11.99) * mm, v(-25.7, 11.47) * mm, v(-25.44, 10.95) * mm, v(-25.18, 10.43) * mm]});
            skFitSpline(sketch, "E3742", {"points": [v(-25.18, 10.43) * mm, v(-25.1, 10.28) * mm, v(-25.03, 10.12) * mm, v(-24.93, 9.92) * mm]});
            skFitSpline(sketch, "E3743", {"points": [v(-24.93, 9.92) * mm, v(-24.75, 10.38) * mm, v(-24.62, 10.8) * mm, v(-24.52, 11.25) * mm]});
            skFitSpline(sketch, "E3744", {"points": [v(-24.52, 11.25) * mm, v(-24.51, 11.3) * mm, v(-24.55, 11.39) * mm, v(-24.58, 11.45) * mm]});
            skFitSpline(sketch, "E3745", {"points": [v(-24.58, 11.45) * mm, v(-25.1, 12.49) * mm, v(-25.65, 13.52) * mm, v(-26.18, 14.56) * mm]});
            skFitSpline(sketch, "E3746", {"points": [v(-26.18, 14.56) * mm, v(-26.28, 14.75) * mm, v(-26.37, 14.95) * mm, v(-26.45, 15.15) * mm]});
            skFitSpline(sketch, "E3747", {"points": [v(-26.45, 15.15) * mm, v(-26.57, 15.42) * mm, v(-26.47, 15.68) * mm, v(-26.23, 15.8) * mm]});
            skFitSpline(sketch, "E3748", {"points": [v(-26.23, 15.8) * mm, v(-26, 15.91) * mm, v(-25.72, 15.82) * mm, v(-25.58, 15.57) * mm]});
            skFitSpline(sketch, "E3749", {"points": [v(-25.58, 15.57) * mm, v(-25.44, 15.3) * mm, v(-25.32, 15.04) * mm, v(-25.19, 14.77) * mm]});
            skFitSpline(sketch, "E3750", {"points": [v(-25.19, 14.77) * mm, v(-24.95, 14.3) * mm, v(-24.72, 13.85) * mm, v(-24.48, 13.38) * mm]});
            skFitSpline(sketch, "E3751", {"points": [v(-24.48, 13.38) * mm, v(-24.44, 13.31) * mm, v(-24.4, 13.24) * mm, v(-24.33, 13.18) * mm]});
            skFitSpline(sketch, "E3752", {"points": [v(-24.33, 13.18) * mm, v(-24.34, 13.27) * mm, v(-24.35, 13.35) * mm, v(-24.36, 13.43) * mm]});
            skFitSpline(sketch, "E3753", {"points": [v(-24.36, 13.43) * mm, v(-24.37, 13.53) * mm, v(-24.37, 13.62) * mm, v(-24.38, 13.72) * mm]});
            skFitSpline(sketch, "E3754", {"points": [v(-24.38, 13.72) * mm, v(-24.42, 14.16) * mm, v(-24.46, 14.6) * mm, v(-24.5, 15.03) * mm]});
            skFitSpline(sketch, "E3755", {"points": [v(-24.5, 15.03) * mm, v(-24.52, 15.12) * mm, v(-24.53, 15.22) * mm, v(-24.55, 15.31) * mm]});
            skFitSpline(sketch, "E3756", {"points": [v(-24.55, 15.31) * mm, v(-24.6, 15.62) * mm, v(-24.53, 15.87) * mm, v(-24.27, 16.07) * mm]});
            skFitSpline(sketch, "E3757", {"points": [v(-24.27, 16.07) * mm, v(-23.77, 16.45) * mm, v(-23.3, 16.85) * mm, v(-22.8, 17.23) * mm]});
            skFitSpline(sketch, "E3758", {"points": [v(-22.8, 17.23) * mm, v(-22.68, 17.33) * mm, v(-22.65, 17.43) * mm, v(-22.7, 17.57) * mm]});
            skFitSpline(sketch, "E3759", {"points": [v(-22.7, 17.57) * mm, v(-22.79, 17.82) * mm, v(-22.88, 18.08) * mm, v(-22.96, 18.34) * mm]});
            skFitSpline(sketch, "E3760", {"points": [v(-22.96, 18.34) * mm, v(-23.03, 18.54) * mm, v(-23.1, 18.75) * mm, v(-23.15, 18.95) * mm]});
            skFitSpline(sketch, "E3761", {"points": [v(-23.15, 18.95) * mm, v(-23.2, 19.2) * mm, v(-23.1, 19.42) * mm, v(-22.9, 19.52) * mm]});
            skFitSpline(sketch, "E3762", {"points": [v(-22.9, 19.52) * mm, v(-22.68, 19.63) * mm, v(-22.42, 19.57) * mm, v(-22.27, 19.36) * mm]});
            skFitSpline(sketch, "E3763", {"points": [v(-22.27, 19.36) * mm, v(-22.22, 19.29) * mm, v(-22.17, 19.2) * mm, v(-22.14, 19.11) * mm]});
            skFitSpline(sketch, "E3764", {"points": [v(-22.14, 19.11) * mm, v(-22.01, 18.8) * mm, v(-21.9, 18.5) * mm, v(-21.77, 18.2) * mm]});
            skFitSpline(sketch, "E3765", {"points": [v(-21.77, 18.2) * mm, v(-21.76, 18.17) * mm, v(-21.74, 18.15) * mm, v(-21.72, 18.12) * mm]});
            skFitSpline(sketch, "E3766", {"points": [v(-21.72, 18.12) * mm, v(-21.4, 18.31) * mm, v(-21.09, 18.51) * mm, v(-20.77, 18.7) * mm]});
            skFitSpline(sketch, "E3767", {"points": [v(-20.77, 18.7) * mm, v(-20.66, 18.76) * mm, v(-20.52, 18.8) * mm, v(-20.4, 18.81) * mm]});
            skFitSpline(sketch, "E3768", {"points": [v(-20.4, 18.81) * mm, v(-20.18, 18.84) * mm, v(-20.02, 18.72) * mm, v(-19.94, 18.53) * mm]});
            skFitSpline(sketch, "E3769", {"points": [v(-19.94, 18.53) * mm, v(-19.85, 18.34) * mm, v(-19.9, 18.12) * mm, v(-20.06, 17.98) * mm]});
            skFitSpline(sketch, "E3770", {"points": [v(-20.06, 17.98) * mm, v(-20.23, 17.83) * mm, v(-20.42, 17.7) * mm, v(-20.61, 17.56) * mm]});
            skFitSpline(sketch, "E3771", {"points": [v(-20.61, 17.56) * mm, v(-20.83, 17.4) * mm, v(-21.05, 17.24) * mm, v(-21.27, 17.09) * mm]});
            skFitSpline(sketch, "E3772", {"points": [v(-21.27, 17.09) * mm, v(-21.38, 17) * mm, v(-21.41, 16.91) * mm, v(-21.37, 16.78) * mm]});
            skFitSpline(sketch, "E3773", {"points": [v(-21.37, 16.78) * mm, v(-21.2, 16.18) * mm, v(-21.06, 15.59) * mm, v(-20.88, 15) * mm]});
            skFitSpline(sketch, "E3774", {"points": [v(-20.88, 15) * mm, v(-20.78, 14.67) * mm, v(-20.85, 14.42) * mm, v(-21.1, 14.18) * mm]});
            skFitSpline(sketch, "E3775", {"points": [v(-21.1, 14.18) * mm, v(-21.42, 13.84) * mm, v(-21.72, 13.48) * mm, v(-22.04, 13.13) * mm]});
            skFitSpline(sketch, "E3776", {"points": [v(-22.04, 13.13) * mm, v(-22.2, 12.96) * mm, v(-22.35, 12.79) * mm, v(-22.48, 12.58) * mm]});
            skFitSpline(sketch, "E3777", {"points": [v(-22.48, 12.58) * mm, v(-22.43, 12.6) * mm, v(-22.37, 12.62) * mm, v(-22.32, 12.65) * mm]});
            skFitSpline(sketch, "E3778", {"points": [v(-22.32, 12.65) * mm, v(-21.71, 12.95) * mm, v(-21.1, 13.26) * mm, v(-20.5, 13.56) * mm]});
            skFitSpline(sketch, "E3779", {"points": [v(-20.5, 13.56) * mm, v(-20.4, 13.62) * mm, v(-20.3, 13.68) * mm, v(-20.2, 13.73) * mm]});
            skFitSpline(sketch, "E3780", {"points": [v(-20.2, 13.73) * mm, v(-20.14, 13.77) * mm, v(-20.07, 13.8) * mm, v(-19.99, 13.82) * mm]});
            skFitSpline(sketch, "E3781", {"points": [v(-19.99, 13.82) * mm, v(-19.72, 13.88) * mm, v(-19.5, 13.77) * mm, v(-19.42, 13.54) * mm]});
            skFitSpline(sketch, "E3782", {"points": [v(-19.42, 13.54) * mm, v(-19.32, 13.31) * mm, v(-19.4, 13.07) * mm, v(-19.65, 12.93) * mm]});
            skFitSpline(sketch, "E3783", {"points": [v(-19.65, 12.93) * mm, v(-19.86, 12.8) * mm, v(-20.08, 12.7) * mm, v(-20.3, 12.58) * mm]});
            skFitSpline(sketch, "E3784", {"points": [v(-20.3, 12.58) * mm, v(-21.3, 12.08) * mm, v(-22.29, 11.58) * mm, v(-23.28, 11.08) * mm]});
            skFitSpline(sketch, "E3785", {"points": [v(-23.28, 11.08) * mm, v(-23.42, 11) * mm, v(-23.52, 10.91) * mm, v(-23.57, 10.75) * mm]});
            skFitSpline(sketch, "E3786", {"points": [v(-23.57, 10.75) * mm, v(-23.69, 10.39) * mm, v(-23.82, 10.02) * mm, v(-23.95, 9.66) * mm]});
            skFitSpline(sketch, "E3787", {"points": [v(-23.95, 9.66) * mm, v(-23.94, 9.65) * mm, v(-23.93, 9.64) * mm, v(-23.91, 9.62) * mm]});
            skFitSpline(sketch, "E3788", {"points": [v(-23.91, 9.62) * mm, v(-23.84, 9.66) * mm, v(-23.76, 9.7) * mm, v(-23.69, 9.74) * mm]});
            skFitSpline(sketch, "E3789", {"points": [v(-23.69, 9.74) * mm, v(-23.17, 10) * mm, v(-22.65, 10.28) * mm, v(-22.14, 10.55) * mm]});
            skFitSpline(sketch, "E3790", {"points": [v(-22.14, 10.55) * mm, v(-21.93, 10.66) * mm, v(-21.7, 10.71) * mm, v(-21.52, 10.9) * mm]});
            skFitSpline(sketch, "E3791", {"points": [v(-21.52, 10.9) * mm, v(-21.38, 11.04) * mm, v(-21.15, 11) * mm, v(-20.98, 10.9) * mm]});
            skFitSpline(sketch, "E3792", {"points": [v(-20.98, 10.9) * mm, v(-20.82, 10.77) * mm, v(-20.74, 10.56) * mm, v(-20.8, 10.36) * mm]});
            skFitSpline(sketch, "E3793", {"points": [v(-20.8, 10.36) * mm, v(-20.86, 10.11) * mm, v(-21.04, 9.94) * mm, v(-21.27, 9.85) * mm]});
            skFitSpline(sketch, "E3794", {"points": [v(-21.27, 9.85) * mm, v(-22.32, 9.45) * mm, v(-23.27, 8.82) * mm, v(-24.27, 8.32) * mm]});
            skFitSpline(sketch, "E3795", {"points": [v(-24.27, 8.32) * mm, v(-24.33, 8.29) * mm, v(-24.39, 8.22) * mm, v(-24.4, 8.16) * mm]});
            skFitSpline(sketch, "E3796", {"points": [v(-24.4, 8.16) * mm, v(-24.52, 7.8) * mm, v(-24.63, 7.43) * mm, v(-24.74, 7.04) * mm]});
            skFitSpline(sketch, "E3797", {"points": [v(-24.74, 7.04) * mm, v(-24.68, 7.06) * mm, v(-24.63, 7.06) * mm, v(-24.6, 7.08) * mm]});
            skFitSpline(sketch, "E3798", {"points": [v(-24.6, 7.08) * mm, v(-23.8, 7.51) * mm, v(-23, 7.94) * mm, v(-22.22, 8.38) * mm]});
            skFitSpline(sketch, "E3799", {"points": [v(-22.22, 8.38) * mm, v(-21.96, 8.52) * mm, v(-21.68, 8.48) * mm, v(-21.53, 8.27) * mm]});
            skFitSpline(sketch, "E3800", {"points": [v(-21.53, 8.27) * mm, v(-21.38, 8.05) * mm, v(-21.42, 7.77) * mm, v(-21.65, 7.59) * mm]});
            skFitSpline(sketch, "E3801", {"points": [v(-21.65, 7.59) * mm, v(-21.74, 7.52) * mm, v(-21.84, 7.46) * mm, v(-21.93, 7.4) * mm]});
            skFitSpline(sketch, "E3802", {"points": [v(-21.93, 7.4) * mm, v(-22.82, 6.93) * mm, v(-23.71, 6.46) * mm, v(-24.6, 5.99) * mm]});
            skFitSpline(sketch, "E3803", {"points": [v(-24.6, 5.99) * mm, v(-24.7, 5.93) * mm, v(-24.8, 5.87) * mm, v(-24.9, 5.82) * mm]});
            skFitSpline(sketch, "E3804", {"points": [v(-24.9, 5.82) * mm, v(-25.1, 5.73) * mm, v(-25.23, 5.58) * mm, v(-25.3, 5.36) * mm]});
            skFitSpline(sketch, "E3805", {"points": [v(-25.3, 5.36) * mm, v(-25.4, 5.02) * mm, v(-25.53, 4.7) * mm, v(-25.65, 4.36) * mm]});
            skFitSpline(sketch, "E3806", {"points": [v(-25.65, 4.36) * mm, v(-25.66, 4.33) * mm, v(-25.66, 4.3) * mm, v(-25.68, 4.2) * mm]});
            skFitSpline(sketch, "E3807", {"points": [v(-25.68, 4.2) * mm, v(-25.42, 4.34) * mm, v(-25.21, 4.45) * mm, v(-25, 4.56) * mm]});
            skFitSpline(sketch, "E3808", {"points": [v(-25, 4.56) * mm, v(-24.54, 4.8) * mm, v(-24.1, 5.04) * mm, v(-23.64, 5.27) * mm]});
            skFitSpline(sketch, "E3809", {"points": [v(-23.64, 5.27) * mm, v(-23.4, 5.39) * mm, v(-23.12, 5.3) * mm, v(-22.99, 5.08) * mm]});
            skFitSpline(sketch, "E3810", {"points": [v(-22.99, 5.08) * mm, v(-22.86, 4.85) * mm, v(-22.93, 4.56) * mm, v(-23.18, 4.42) * mm]});
            skFitSpline(sketch, "E3811", {"points": [v(-23.18, 4.42) * mm, v(-23.46, 4.25) * mm, v(-23.76, 4.1) * mm, v(-24.04, 3.95) * mm]});
            skFitSpline(sketch, "E3812", {"points": [v(-24.04, 3.95) * mm, v(-24.68, 3.61) * mm, v(-25.32, 3.28) * mm, v(-25.95, 2.93) * mm]});
            skFitSpline(sketch, "E3813", {"points": [v(-25.95, 2.93) * mm, v(-26.12, 2.84) * mm, v(-26.22, 2.66) * mm, v(-26.28, 2.48) * mm]});
            skFitSpline(sketch, "E3814", {"points": [v(-26.28, 2.48) * mm, v(-26.46, 1.99) * mm, v(-26.6, 1.48) * mm, v(-26.75, 0.98) * mm]});
            skFitSpline(sketch, "E3815", {"points": [v(-26.75, 0.98) * mm, v(-26.76, 0.96) * mm, v(-26.75, 0.93) * mm, v(-26.75, 0.9) * mm]});
            skFitSpline(sketch, "E3816", {"points": [v(-26.75, 0.9) * mm, v(-26.7, 0.92) * mm, v(-26.65, 0.93) * mm, v(-26.62, 0.96) * mm]});
            skFitSpline(sketch, "E3817", {"points": [v(-26.62, 0.96) * mm, v(-25.9, 1.5) * mm, v(-25.17, 2.04) * mm, v(-24.45, 2.58) * mm]});
            skFitSpline(sketch, "E3818", {"points": [v(-24.45, 2.58) * mm, v(-23.63, 3.2) * mm, v(-22.82, 3.82) * mm, v(-22, 4.42) * mm]});
            skFitSpline(sketch, "E3819", {"points": [v(-22, 4.42) * mm, v(-21.11, 5.06) * mm, v(-20.26, 5.74) * mm, v(-19.34, 6.32) * mm]});
            skFitSpline(sketch, "E3820", {"points": [v(-19.34, 6.32) * mm, v(-19.2, 6.41) * mm, v(-19.02, 6.5) * mm, v(-18.93, 6.65) * mm]});
            skFitSpline(sketch, "E3821", {"points": [v(-18.93, 6.65) * mm, v(-18.86, 6.78) * mm, v(-18.87, 6.97) * mm, v(-18.86, 7.13) * mm]});
            skFitSpline(sketch, "E3822", {"points": [v(-18.86, 7.13) * mm, v(-18.83, 7.72) * mm, v(-18.7, 8.29) * mm, v(-18.58, 8.86) * mm]});
            skFitSpline(sketch, "E3823", {"points": [v(-18.58, 8.86) * mm, v(-18.51, 9.18) * mm, v(-18.45, 9.51) * mm, v(-18.36, 9.83) * mm]});
            skFitSpline(sketch, "E3824", {"points": [v(-18.36, 9.83) * mm, v(-18.26, 10.17) * mm, v(-17.91, 10.3) * mm, v(-17.64, 10.14) * mm]});
            skFitSpline(sketch, "E3825", {"points": [v(-17.64, 10.14) * mm, v(-17.4, 10) * mm, v(-17.33, 9.77) * mm, v(-17.43, 9.49) * mm]});
            skFitSpline(sketch, "E3826", {"points": [v(-17.43, 9.49) * mm, v(-17.56, 9.1) * mm, v(-17.6, 8.7) * mm, v(-17.7, 8.33) * mm]});
            skFitSpline(sketch, "E3827", {"points": [v(-17.7, 8.33) * mm, v(-17.73, 8.21) * mm, v(-17.75, 8.1) * mm, v(-17.74, 7.96) * mm]});
            skFitSpline(sketch, "E3828", {"points": [v(-17.74, 7.96) * mm, v(-17.65, 8.1) * mm, v(-17.56, 8.25) * mm, v(-17.47, 8.4) * mm]});
            skFitSpline(sketch, "E3829", {"points": [v(-17.47, 8.4) * mm, v(-17.18, 8.87) * mm, v(-16.88, 9.35) * mm, v(-16.6, 9.83) * mm]});
            skFitSpline(sketch, "E3830", {"points": [v(-16.6, 9.83) * mm, v(-16.48, 10.02) * mm, v(-16.33, 10.11) * mm, v(-16.1, 10.14) * mm]});
            skFitSpline(sketch, "E3831", {"points": [v(-16.1, 10.14) * mm, v(-15.43, 10.23) * mm, v(-14.76, 10.35) * mm, v(-14.09, 10.45) * mm]});
            skFitSpline(sketch, "E3832", {"points": [v(-14.09, 10.45) * mm, v(-13.94, 10.47) * mm, v(-13.79, 10.49) * mm, v(-13.64, 10.5) * mm]});
            skFitSpline(sketch, "E3833", {"points": [v(-13.64, 10.5) * mm, v(-13.6, 10.5) * mm, v(-13.54, 10.5) * mm, v(-13.5, 10.5) * mm]});
            skFitSpline(sketch, "E3834", {"points": [v(-13.5, 10.5) * mm, v(-13.13, 10.43) * mm, v(-12.79, 9.86) * mm, v(-12.91, 9.51) * mm]});
            skFitSpline(sketch, "E3835", {"points": [v(-12.91, 9.51) * mm, v(-12.97, 9.36) * mm, v(-13.04, 9.22) * mm, v(-13.12, 9.08) * mm]});
            skFitSpline(sketch, "E3836", {"points": [v(-13.12, 9.08) * mm, v(-13.26, 8.79) * mm, v(-13.42, 8.5) * mm, v(-13.57, 8.2) * mm]});
            skFitSpline(sketch, "E3837", {"points": [v(-13.57, 8.2) * mm, v(-13.73, 7.87) * mm, v(-13.89, 7.53) * mm, v(-14.05, 7.2) * mm]});
            skFitSpline(sketch, "E3838", {"points": [v(-14.05, 7.2) * mm, v(-14.12, 7.06) * mm, v(-14.24, 6.97) * mm, v(-14.38, 6.93) * mm]});
            skFitSpline(sketch, "E3839", {"points": [v(-14.38, 6.93) * mm, v(-14.5, 6.89) * mm, v(-14.64, 6.86) * mm, v(-14.77, 6.82) * mm]});
            skFitSpline(sketch, "E3840", {"points": [v(-14.77, 6.82) * mm, v(-15.36, 6.69) * mm, v(-15.94, 6.56) * mm, v(-16.52, 6.42) * mm]});
            skFitSpline(sketch, "E3841", {"points": [v(-16.52, 6.42) * mm, v(-16.54, 6.42) * mm, v(-16.56, 6.4) * mm, v(-16.62, 6.36) * mm]});
            skFitSpline(sketch, "E3842", {"points": [v(-16.62, 6.36) * mm, v(-16.4, 6.34) * mm, v(-16.24, 6.32) * mm, v(-16.06, 6.3) * mm]});
            skFitSpline(sketch, "E3843", {"points": [v(-16.06, 6.3) * mm, v(-15.84, 6.27) * mm, v(-15.62, 6.24) * mm, v(-15.4, 6.21) * mm]});
            skFitSpline(sketch, "E3844", {"points": [v(-15.4, 6.21) * mm, v(-15.32, 6.2) * mm, v(-15.24, 6.2) * mm, v(-15.16, 6.22) * mm]});
            skFitSpline(sketch, "E3845", {"points": [v(-15.16, 6.22) * mm, v(-15.01, 6.25) * mm, v(-14.88, 6.21) * mm, v(-14.75, 6.14) * mm]});
            skFitSpline(sketch, "E3846", {"points": [v(-14.75, 6.14) * mm, v(-14.55, 6.04) * mm, v(-14.44, 5.82) * mm, v(-14.49, 5.62) * mm]});
            skFitSpline(sketch, "E3847", {"points": [v(-14.49, 5.62) * mm, v(-14.54, 5.4) * mm, v(-14.72, 5.23) * mm, v(-14.94, 5.23) * mm]});
            skFitSpline(sketch, "E3848", {"points": [v(-14.94, 5.23) * mm, v(-15.21, 5.23) * mm, v(-15.48, 5.26) * mm, v(-15.75, 5.3) * mm]});
            skFitSpline(sketch, "E3849", {"points": [v(-15.75, 5.3) * mm, v(-16.24, 5.35) * mm, v(-16.74, 5.4) * mm, v(-17.22, 5.47) * mm]});
            skFitSpline(sketch, "E3850", {"points": [v(-17.22, 5.47) * mm, v(-17.5, 5.51) * mm, v(-17.76, 5.58) * mm, v(-18.02, 5.65) * mm]});
            skFitSpline(sketch, "E3851", {"points": [v(-18.02, 5.65) * mm, v(-18.15, 5.68) * mm, v(-18.26, 5.67) * mm, v(-18.37, 5.58) * mm]});
            skFitSpline(sketch, "E3852", {"points": [v(-18.37, 5.58) * mm, v(-18.75, 5.29) * mm, v(-19.13, 5) * mm, v(-19.51, 4.7) * mm]});
            skFitSpline(sketch, "E3853", {"points": [v(-19.51, 4.7) * mm, v(-20.1, 4.27) * mm, v(-20.7, 3.85) * mm, v(-21.3, 3.42) * mm]});
            skFitSpline(sketch, "E3854", {"points": [v(-21.3, 3.42) * mm, v(-21.75, 3.1) * mm, v(-22.2, 2.77) * mm, v(-22.65, 2.45) * mm]});
            skFitSpline(sketch, "E3855", {"points": [v(-22.65, 2.45) * mm, v(-23.27, 2.02) * mm, v(-23.9, 1.6) * mm, v(-24.52, 1.16) * mm]});
            skFitSpline(sketch, "E3856", {"points": [v(-24.52, 1.16) * mm, v(-25.03, 0.81) * mm, v(-25.53, 0.45) * mm, v(-26.03, 0.1) * mm]});
            skFitSpline(sketch, "E3857", {"points": [v(-26.03, 0.1) * mm, v(-26.06, 0.07) * mm, v(-26.07, 0.04) * mm, v(-26.11, -0.01) * mm]});
            skFitSpline(sketch, "E3858", {"points": [v(-26.11, -0.01) * mm, v(-26.05, -0.02) * mm, v(-26.01, -0.03) * mm, v(-25.98, -0.03) * mm]});
            skFitSpline(sketch, "E3859", {"points": [v(-25.98, -0.03) * mm, v(-25.5, -0.04) * mm, v(-25.02, -0.06) * mm, v(-24.54, -0.05) * mm]});
            skFitSpline(sketch, "E3860", {"points": [v(-24.54, -0.05) * mm, v(-24.27, -0.04) * mm, v(-24.01, 0.04) * mm, v(-23.8, 0.24) * mm]});
            skFitSpline(sketch, "E3861", {"points": [v(-23.8, 0.24) * mm, v(-23.4, 0.64) * mm, v(-22.97, 1.03) * mm, v(-22.55, 1.42) * mm]});
            skFitSpline(sketch, "E3862", {"points": [v(-22.55, 1.42) * mm, v(-22.27, 1.7) * mm, v(-22, 2) * mm, v(-21.7, 2.27) * mm]});
            skFitSpline(sketch, "E3863", {"points": [v(-21.7, 2.27) * mm, v(-21.63, 2.34) * mm, v(-21.52, 2.4) * mm, v(-21.42, 2.43) * mm]});
            skFitSpline(sketch, "E3864", {"points": [v(-21.42, 2.43) * mm, v(-21.22, 2.5) * mm, v(-21, 2.39) * mm, v(-20.9, 2.21) * mm]});
            skFitSpline(sketch, "E3865", {"points": [v(-20.9, 2.21) * mm, v(-20.81, 2.05) * mm, v(-20.84, 1.8) * mm, v(-20.96, 1.65) * mm]});
            skFitSpline(sketch, "E3866", {"points": [v(-20.96, 1.65) * mm, v(-21, 1.6) * mm, v(-21.06, 1.55) * mm, v(-21.11, 1.5) * mm]});
            skFitSpline(sketch, "E3867", {"points": [v(-21.11, 1.5) * mm, v(-21.58, 1.04) * mm, v(-22.05, 0.58) * mm, v(-22.51, 0.12) * mm]});
            skFitSpline(sketch, "E3868", {"points": [v(-22.51, 0.12) * mm, v(-22.55, 0.09) * mm, v(-22.58, 0.05) * mm, v(-22.62, 0) * mm]});
            skFitSpline(sketch, "E3869", {"points": [v(-22.62, 0) * mm, v(-22.5, -0.06) * mm, v(-22.4, -0.04) * mm, v(-22.29, -0.03) * mm]});
            skFitSpline(sketch, "E3870", {"points": [v(-22.29, -0.03) * mm, v(-21.95, -0.02) * mm, v(-21.6, 0) * mm, v(-21.26, 0.01) * mm]});
            skFitSpline(sketch, "E3871", {"points": [v(-21.26, 0.01) * mm, v(-21.16, 0.01) * mm, v(-21.08, 0.04) * mm, v(-21, 0.1) * mm]});
            skFitSpline(sketch, "E3872", {"points": [v(-21, 0.1) * mm, v(-20.89, 0.22) * mm, v(-20.76, 0.32) * mm, v(-20.65, 0.43) * mm]});
            skFitSpline(sketch, "E3873", {"points": [v(-20.65, 0.43) * mm, v(-19.91, 1.14) * mm, v(-19.18, 1.85) * mm, v(-18.44, 2.56) * mm]});
            skFitSpline(sketch, "E3874", {"points": [v(-18.44, 2.56) * mm, v(-18.35, 2.64) * mm, v(-18.26, 2.72) * mm, v(-18.16, 2.79) * mm]});
            skFitSpline(sketch, "E3875", {"points": [v(-18.16, 2.79) * mm, v(-17.91, 2.95) * mm, v(-17.64, 2.9) * mm, v(-17.48, 2.7) * mm]});
            skFitSpline(sketch, "E3876", {"points": [v(-17.48, 2.7) * mm, v(-17.31, 2.48) * mm, v(-17.36, 2.22) * mm, v(-17.58, 2.01) * mm]});
            skFitSpline(sketch, "E3877", {"points": [v(-17.58, 2.01) * mm, v(-18.24, 1.4) * mm, v(-18.9, 0.77) * mm, v(-19.55, 0.15) * mm]});
            skFitSpline(sketch, "E3878", {"points": [v(-19.55, 0.15) * mm, v(-19.58, 0.12) * mm, v(-19.6, 0.1) * mm, v(-19.64, 0.05) * mm]});
            skFitSpline(sketch, "E3879", {"points": [v(-19.64, 0.05) * mm, v(-19.53, -0.01) * mm, v(-19.42, 0) * mm, v(-19.31, 0) * mm]});
            skFitSpline(sketch, "E3880", {"points": [v(-19.31, 0) * mm, v(-19.05, 0) * mm, v(-18.79, 0) * mm, v(-18.52, -0.02) * mm]});
            skFitSpline(sketch, "E3881", {"points": [v(-18.52, -0.02) * mm, v(-18.43, -0.02) * mm, v(-18.34, 0) * mm, v(-18.27, 0.08) * mm]});
            skFitSpline(sketch, "E3882", {"points": [v(-18.27, 0.08) * mm, v(-17.6, 0.73) * mm, v(-16.92, 1.38) * mm, v(-16.26, 2.03) * mm]});
            skFitSpline(sketch, "E3883", {"points": [v(-16.26, 2.03) * mm, v(-16.14, 2.15) * mm, v(-16.05, 2.27) * mm, v(-15.94, 2.4) * mm]});
            skFitSpline(sketch, "E3884", {"points": [v(-15.94, 2.4) * mm, v(-15.82, 2.54) * mm, v(-15.68, 2.65) * mm, v(-15.5, 2.71) * mm]});
            skFitSpline(sketch, "E3885", {"points": [v(-15.5, 2.71) * mm, v(-15.33, 2.77) * mm, v(-15.17, 2.76) * mm, v(-15.02, 2.67) * mm]});
            skFitSpline(sketch, "E3886", {"points": [v(-15.02, 2.67) * mm, v(-14.71, 2.47) * mm, v(-14.7, 2.03) * mm, v(-15.03, 1.86) * mm]});
            skFitSpline(sketch, "E3887", {"points": [v(-15.03, 1.86) * mm, v(-15.18, 1.77) * mm, v(-15.27, 1.65) * mm, v(-15.38, 1.54) * mm]});
            skFitSpline(sketch, "E3888", {"points": [v(-15.38, 1.54) * mm, v(-15.82, 1.1) * mm, v(-16.27, 0.66) * mm, v(-16.7, 0.23) * mm]});
            skFitSpline(sketch, "E3889", {"points": [v(-16.7, 0.23) * mm, v(-16.78, 0.15) * mm, v(-16.85, 0.09) * mm, v(-16.97, -0.02) * mm]});
            skFitSpline(sketch, "E3890", {"points": [v(-16.97, -0.02) * mm, v(-16.55, -0.04) * mm, v(-16.2, -0.04) * mm, v(-15.84, -0.03) * mm]});
            skFitSpline(sketch, "E3891", {"points": [v(-15.84, -0.03) * mm, v(-15.57, -0.02) * mm, v(-15.4, 0.1) * mm, v(-15.21, 0.29) * mm]});
            skFitSpline(sketch, "E3892", {"points": [v(-15.21, 0.29) * mm, v(-14.41, 1.11) * mm, v(-13.6, 1.93) * mm, v(-12.8, 2.75) * mm]});
            skFitSpline(sketch, "E3893", {"points": [v(-12.8, 2.75) * mm, v(-12.68, 2.86) * mm, v(-12.57, 2.96) * mm, v(-12.45, 3.05) * mm]});
            skFitSpline(sketch, "E3894", {"points": [v(-12.45, 3.05) * mm, v(-12.24, 3.23) * mm, v(-11.96, 3.22) * mm, v(-11.78, 3.04) * mm]});
            skFitSpline(sketch, "E3895", {"points": [v(-11.78, 3.04) * mm, v(-11.6, 2.85) * mm, v(-11.6, 2.56) * mm, v(-11.79, 2.35) * mm]});
            skFitSpline(sketch, "E3896", {"points": [v(-11.79, 2.35) * mm, v(-12.03, 2.1) * mm, v(-12.28, 1.86) * mm, v(-12.52, 1.62) * mm]});
            skFitSpline(sketch, "E3897", {"points": [v(-12.52, 1.62) * mm, v(-12.85, 1.3) * mm, v(-13.19, 0.96) * mm, v(-13.52, 0.62) * mm]});
            skFitSpline(sketch, "E3898", {"points": [v(-13.52, 0.62) * mm, v(-13.57, 0.57) * mm, v(-13.62, 0.52) * mm, v(-13.65, 0.44) * mm]});
            skFitSpline(sketch, "E3899", {"points": [v(-13.65, 0.44) * mm, v(-13.6, 0.46) * mm, v(-13.54, 0.47) * mm, v(-13.5, 0.5) * mm]});
            skFitSpline(sketch, "E3900", {"points": [v(-13.5, 0.5) * mm, v(-13.13, 0.66) * mm, v(-12.77, 0.83) * mm, v(-12.4, 1) * mm]});
            skFitSpline(sketch, "E3901", {"points": [v(-12.4, 1) * mm, v(-12.14, 1.11) * mm, v(-11.88, 1.22) * mm, v(-11.61, 1.34) * mm]});
            skFitSpline(sketch, "E3902", {"points": [v(-11.61, 1.34) * mm, v(-11.38, 1.44) * mm, v(-11.16, 1.42) * mm, v(-10.95, 1.28) * mm]});
            skFitSpline(sketch, "E3903", {"points": [v(-10.95, 1.28) * mm, v(-10.7, 1.1) * mm, v(-10.44, 0.92) * mm, v(-10.18, 0.75) * mm]});
            skFitSpline(sketch, "E3904", {"points": [v(-10.18, 0.75) * mm, v(-9.9, 0.56) * mm, v(-9.61, 0.4) * mm, v(-9.33, 0.2) * mm]});
            skFitSpline(sketch, "E3905", {"points": [v(-9.33, 0.2) * mm, v(-9.21, 0.13) * mm, v(-9.11, 0.14) * mm, v(-9, 0.22) * mm]});
            skFitSpline(sketch, "E3906", {"points": [v(-9, 0.22) * mm, v(-8.79, 0.38) * mm, v(-8.57, 0.55) * mm, v(-8.35, 0.7) * mm]});
            skFitSpline(sketch, "E3907", {"points": [v(-8.35, 0.7) * mm, v(-8.17, 0.83) * mm, v(-7.99, 0.97) * mm, v(-7.8, 1.09) * mm]});
            skFitSpline(sketch, "E3908", {"points": [v(-7.8, 1.09) * mm, v(-7.6, 1.2) * mm, v(-7.35, 1.17) * mm, v(-7.2, 1.01) * mm]});
            skFitSpline(sketch, "E3909", {"points": [v(-7.2, 1.01) * mm, v(-7.04, 0.85) * mm, v(-7, 0.62) * mm, v(-7.13, 0.42) * mm]});
            skFitSpline(sketch, "E3910", {"points": [v(-7.13, 0.42) * mm, v(-7.2, 0.3) * mm, v(-7.3, 0.21) * mm, v(-7.4, 0.12) * mm]});
            skFitSpline(sketch, "E3911", {"points": [v(-7.4, 0.12) * mm, v(-7.66, -0.1) * mm, v(-7.92, -0.3) * mm, v(-8.18, -0.53) * mm]});
            skFitSpline(sketch, "E3912", {"points": [v(-8.18, -0.53) * mm, v(-7.91, -0.76) * mm, v(-7.66, -0.97) * mm, v(-7.4, -1.2) * mm]});
            skFitSpline(sketch, "E3913", {"points": [v(-7.4, -1.2) * mm, v(-7.31, -1.27) * mm, v(-7.22, -1.35) * mm, v(-7.15, -1.45) * mm]});
            skFitSpline(sketch, "E3914", {"points": [v(-7.15, -1.45) * mm, v(-7, -1.65) * mm, v(-7.03, -1.92) * mm, v(-7.2, -2.08) * mm]});
            skFitSpline(sketch, "E3915", {"points": [v(-7.2, -2.08) * mm, v(-7.4, -2.26) * mm, v(-7.58, -2.3) * mm, v(-7.81, -2.14) * mm]});
            skFitSpline(sketch, "E3916", {"points": [v(-7.81, -2.14) * mm, v(-8.02, -2.01) * mm, v(-8.22, -1.86) * mm, v(-8.42, -1.71) * mm]});
            skFitSpline(sketch, "E3917", {"points": [v(-8.42, -1.71) * mm, v(-8.61, -1.57) * mm, v(-8.8, -1.43) * mm, v(-9, -1.3) * mm]});
            skFitSpline(sketch, "E3918", {"points": [v(-9, -1.3) * mm, v(-9.12, -1.2) * mm, v(-9.22, -1.2) * mm, v(-9.35, -1.29) * mm]});
            skFitSpline(sketch, "E3919", {"points": [v(-9.35, -1.29) * mm, v(-9.86, -1.63) * mm, v(-10.38, -1.96) * mm, v(-10.88, -2.3) * mm]});
            skFitSpline(sketch, "E3920", {"points": [v(-10.88, -2.3) * mm, v(-11.17, -2.5) * mm, v(-11.44, -2.53) * mm, v(-11.73, -2.35) * mm]});
            skFitSpline(sketch, "E3921", {"points": [v(-11.73, -2.35) * mm, v(-11.78, -2.32) * mm, v(-11.83, -2.29) * mm, v(-11.88, -2.27) * mm]});
            skFitSpline(sketch, "E3922", {"points": [v(-11.88, -2.27) * mm, v(-12.44, -2.02) * mm, v(-13, -1.78) * mm, v(-13.57, -1.53) * mm]});
            skFitSpline(sketch, "E3923", {"points": [v(-13.57, -1.53) * mm, v(-13.6, -1.52) * mm, v(-13.64, -1.5) * mm, v(-13.73, -1.47) * mm]});
            skFitSpline(sketch, "E3924", {"points": [v(-13.73, -1.47) * mm, v(-13.65, -1.56) * mm, v(-13.62, -1.6) * mm, v(-13.58, -1.64) * mm]});
            skFitSpline(sketch, "E3925", {"points": [v(-13.58, -1.64) * mm, v(-13.1, -2.13) * mm, v(-12.62, -2.61) * mm, v(-12.14, -3.1) * mm]});
            skFitSpline(sketch, "E3926", {"points": [v(-12.14, -3.1) * mm, v(-12.03, -3.2) * mm, v(-11.9, -3.3) * mm, v(-11.79, -3.42) * mm]});
            skFitSpline(sketch, "E3927", {"points": [v(-11.79, -3.42) * mm, v(-11.64, -3.58) * mm, v(-11.6, -3.77) * mm, v(-11.69, -3.97) * mm]});
            skFitSpline(sketch, "E3928", {"points": [v(-11.69, -3.97) * mm, v(-11.8, -4.26) * mm, v(-12.16, -4.34) * mm, v(-12.41, -4.15) * mm]});
            skFitSpline(sketch, "E3929", {"points": [v(-12.41, -4.15) * mm, v(-12.54, -4.05) * mm, v(-12.67, -3.94) * mm, v(-12.79, -3.82) * mm]});
            skFitSpline(sketch, "E3930", {"points": [v(-12.79, -3.82) * mm, v(-13.34, -3.27) * mm, v(-13.9, -2.71) * mm, v(-14.45, -2.15) * mm]});
            skFitSpline(sketch, "E3931", {"points": [v(-14.45, -2.15) * mm, v(-14.75, -1.85) * mm, v(-15.05, -1.54) * mm, v(-15.35, -1.23) * mm]});
            skFitSpline(sketch, "E3932", {"points": [v(-15.35, -1.23) * mm, v(-15.46, -1.1) * mm, v(-15.58, -1.06) * mm, v(-15.75, -1.05) * mm]});
            skFitSpline(sketch, "E3933", {"points": [v(-15.75, -1.05) * mm, v(-16.08, -1.03) * mm, v(-16.41, -1.03) * mm, v(-16.75, -1.04) * mm]});
            skFitSpline(sketch, "E3934", {"points": [v(-16.75, -1.04) * mm, v(-16.8, -1.04) * mm, v(-16.85, -1.05) * mm, v(-16.89, -1.05) * mm]});
            skFitSpline(sketch, "E3935", {"points": [v(-16.89, -1.05) * mm, v(-16.75, -1.21) * mm, v(-16.6, -1.37) * mm, v(-16.46, -1.53) * mm]});
            skFitSpline(sketch, "E3936", {"points": [v(-16.46, -1.53) * mm, v(-16.06, -1.95) * mm, v(-15.65, -2.36) * mm, v(-15.24, -2.78) * mm]});
            skFitSpline(sketch, "E3937", {"points": [v(-15.24, -2.78) * mm, v(-15.2, -2.83) * mm, v(-15.13, -2.86) * mm, v(-15.07, -2.9) * mm]});
            skFitSpline(sketch, "E3938", {"points": [v(-15.07, -2.9) * mm, v(-14.83, -3.02) * mm, v(-14.73, -3.27) * mm, v(-14.82, -3.5) * mm]});
            skFitSpline(sketch, "E3939", {"points": [v(-14.82, -3.5) * mm, v(-14.92, -3.74) * mm, v(-15.17, -3.86) * mm, v(-15.43, -3.8) * mm]});
            skFitSpline(sketch, "E3940", {"points": [v(-15.43, -3.8) * mm, v(-15.61, -3.76) * mm, v(-15.78, -3.67) * mm, v(-15.9, -3.52) * mm]});
            skFitSpline(sketch, "E3941", {"points": [v(-15.9, -3.52) * mm, v(-16.4, -2.89) * mm, v(-17.01, -2.36) * mm, v(-17.6, -1.8) * mm]});
            skFitSpline(sketch, "E3942", {"points": [v(-17.6, -1.8) * mm, v(-17.82, -1.58) * mm, v(-18.04, -1.36) * mm, v(-18.27, -1.15) * mm]});
            skFitSpline(sketch, "E3943", {"points": [v(-18.27, -1.15) * mm, v(-18.32, -1.1) * mm, v(-18.39, -1.07) * mm, v(-18.45, -1.06) * mm]});
            skFitSpline(sketch, "E3944", {"points": [v(-18.45, -1.06) * mm, v(-18.6, -1.05) * mm, v(-18.75, -1.06) * mm, v(-18.9, -1.06) * mm]});
            skFitSpline(sketch, "E3945", {"points": [v(-18.9, -1.06) * mm, v(-19, -1.06) * mm, v(-19.1, -1.06) * mm, v(-19.21, -1.06) * mm]});
            skFitSpline(sketch, "E3946", {"points": [v(-19.21, -1.06) * mm, v(-19.34, -1.07) * mm, v(-19.48, -1.08) * mm, v(-19.64, -1.09) * mm]});
            skFitSpline(sketch, "E3947", {"points": [v(-19.64, -1.09) * mm, v(-19.6, -1.15) * mm, v(-19.58, -1.19) * mm, v(-19.55, -1.22) * mm]});
            skFitSpline(sketch, "E3948", {"points": [v(-19.55, -1.22) * mm, v(-18.9, -1.84) * mm, v(-18.24, -2.46) * mm, v(-17.59, -3.08) * mm]});
            skFitSpline(sketch, "E3949", {"points": [v(-17.59, -3.08) * mm, v(-17.44, -3.22) * mm, v(-17.34, -3.37) * mm, v(-17.4, -3.59) * mm]});
            skFitSpline(sketch, "E3950", {"points": [v(-17.4, -3.59) * mm, v(-17.45, -3.8) * mm, v(-17.6, -3.91) * mm, v(-17.8, -3.95) * mm]});
            skFitSpline(sketch, "E3951", {"points": [v(-17.8, -3.95) * mm, v(-17.96, -3.99) * mm, v(-18.11, -3.92) * mm, v(-18.23, -3.8) * mm]});
            skFitSpline(sketch, "E3952", {"points": [v(-18.23, -3.8) * mm, v(-18.46, -3.61) * mm, v(-18.67, -3.4) * mm, v(-18.88, -3.2) * mm]});
            skFitSpline(sketch, "E3953", {"points": [v(-18.88, -3.2) * mm, v(-19.52, -2.6) * mm, v(-20.16, -1.98) * mm, v(-20.8, -1.36) * mm]});
            skFitSpline(sketch, "E3954", {"points": [v(-20.8, -1.36) * mm, v(-20.97, -1.2) * mm, v(-21.14, -1.07) * mm, v(-21.4, -1.07) * mm]});
            skFitSpline(sketch, "E3955", {"points": [v(-21.4, -1.07) * mm, v(-21.8, -1.08) * mm, v(-22.2, -1.05) * mm, v(-22.64, -1.04) * mm]});
            skFitSpline(sketch, "E3956", {"points": [v(-22.64, -1.04) * mm, v(-22.57, -1.12) * mm, v(-22.54, -1.16) * mm, v(-22.5, -1.2) * mm]});
            skFitSpline(sketch, "E3957", {"points": [v(-22.5, -1.2) * mm, v(-22.14, -1.57) * mm, v(-21.76, -1.94) * mm, v(-21.39, -2.31) * mm]});
            skFitSpline(sketch, "E3958", {"points": [v(-21.39, -2.31) * mm, v(-21.26, -2.44) * mm, v(-21.13, -2.55) * mm, v(-21, -2.67) * mm]});
            skFitSpline(sketch, "E3959", {"points": [v(-21, -2.67) * mm, v(-20.91, -2.76) * mm, v(-20.86, -2.86) * mm, v(-20.85, -2.99) * mm]});
            skFitSpline(sketch, "E3960", {"points": [v(-20.85, -2.99) * mm, v(-20.84, -3.2) * mm, v(-20.9, -3.37) * mm, v(-21.1, -3.46) * mm]});
            skFitSpline(sketch, "E3961", {"points": [v(-21.1, -3.46) * mm, v(-21.3, -3.55) * mm, v(-21.5, -3.53) * mm, v(-21.66, -3.38) * mm]});
            skFitSpline(sketch, "E3962", {"points": [v(-21.66, -3.38) * mm, v(-21.83, -3.23) * mm, v(-22, -3.07) * mm, v(-22.17, -2.9) * mm]});
            skFitSpline(sketch, "E3963", {"points": [v(-22.17, -2.9) * mm, v(-22.72, -2.37) * mm, v(-23.27, -1.84) * mm, v(-23.81, -1.3) * mm]});
            skFitSpline(sketch, "E3964", {"points": [v(-23.81, -1.3) * mm, v(-24.02, -1.1) * mm, v(-24.28, -1.04) * mm, v(-24.55, -1.02) * mm]});
            skFitSpline(sketch, "E3965", {"points": [v(-24.55, -1.02) * mm, v(-24.73, -1) * mm, v(-24.91, -1.04) * mm, v(-25.1, -1.04) * mm]});
            skFitSpline(sketch, "E3966", {"points": [v(-25.1, -1.04) * mm, v(-25.37, -1.04) * mm, v(-25.64, -1.04) * mm, v(-25.9, -1.04) * mm]});
            skFitSpline(sketch, "E3967", {"points": [v(-25.9, -1.04) * mm, v(-25.97, -1.04) * mm, v(-26.02, -1.05) * mm, v(-26.13, -1.06) * mm]});
            skFitSpline(sketch, "E3968", {"points": [v(-26.13, -1.06) * mm, v(-26.06, -1.13) * mm, v(-26.02, -1.16) * mm, v(-25.98, -1.2) * mm]});
            skFitSpline(sketch, "E3969", {"points": [v(-25.98, -1.2) * mm, v(-25.2, -1.74) * mm, v(-24.43, -2.3) * mm, v(-23.65, -2.84) * mm]});
            skFitSpline(sketch, "E3970", {"points": [v(-23.65, -2.84) * mm, v(-22.87, -3.4) * mm, v(-22.08, -3.94) * mm, v(-21.3, -4.5) * mm]});
            skFitSpline(sketch, "E3971", {"points": [v(-21.3, -4.5) * mm, v(-20.4, -5.15) * mm, v(-19.47, -5.76) * mm, v(-18.62, -6.48) * mm]});
            skFitSpline(sketch, "E3972", {"points": [v(-18.62, -6.48) * mm, v(-18.36, -6.7) * mm, v(-18.12, -6.77) * mm, v(-17.78, -6.67) * mm]});
            skFitSpline(sketch, "E3973", {"points": [v(-17.78, -6.67) * mm, v(-17.2, -6.48) * mm, v(-16.57, -6.44) * mm, v(-15.96, -6.38) * mm]});
            skFitSpline(sketch, "E3974", {"points": [v(-15.96, -6.38) * mm, v(-15.65, -6.35) * mm, v(-15.33, -6.31) * mm, v(-15.01, -6.3) * mm]});
            skFitSpline(sketch, "E3975", {"points": [v(-15.01, -6.3) * mm, v(-14.81, -6.28) * mm, v(-14.65, -6.37) * mm, v(-14.55, -6.54) * mm]});
            skFitSpline(sketch, "E3976", {"points": [v(-14.55, -6.54) * mm, v(-14.35, -6.87) * mm, v(-14.6, -7.27) * mm, v(-15.02, -7.3) * mm]});
            skFitSpline(sketch, "E3977", {"points": [v(-15.02, -7.3) * mm, v(-15.3, -7.3) * mm, v(-15.58, -7.32) * mm, v(-15.86, -7.35) * mm]});
            skFitSpline(sketch, "E3978", {"points": [v(-15.86, -7.35) * mm, v(-16.1, -7.37) * mm, v(-16.36, -7.4) * mm, v(-16.62, -7.46) * mm]});
            skFitSpline(sketch, "E3979", {"points": [v(-16.62, -7.46) * mm, v(-16.54, -7.48) * mm, v(-16.46, -7.5) * mm, v(-16.38, -7.52) * mm]});
            skFitSpline(sketch, "E3980", {"points": [v(-16.38, -7.52) * mm, v(-15.75, -7.67) * mm, v(-15.12, -7.82) * mm, v(-14.5, -7.96) * mm]});
            skFitSpline(sketch, "E3981", {"points": [v(-14.5, -7.96) * mm, v(-14.26, -8.02) * mm, v(-14.1, -8.15) * mm, v(-14, -8.37) * mm]});
            skFitSpline(sketch, "E3982", {"points": [v(-14, -8.37) * mm, v(-13.71, -8.98) * mm, v(-13.4, -9.58) * mm, v(-13.1, -10.19) * mm]});
            skFitSpline(sketch, "E3983", {"points": [v(-13.1, -10.19) * mm, v(-13.03, -10.3) * mm, v(-12.98, -10.42) * mm, v(-12.93, -10.54) * mm]});
            skFitSpline(sketch, "E3984", {"points": [v(-12.93, -10.54) * mm, v(-12.9, -10.6) * mm, v(-12.88, -10.67) * mm, v(-12.87, -10.74) * mm]});
            skFitSpline(sketch, "E3985", {"points": [v(-12.87, -10.74) * mm, v(-12.83, -11.04) * mm, v(-13.25, -11.55) * mm, v(-13.55, -11.56) * mm]});
            skFitSpline(sketch, "E3986", {"points": [v(-13.55, -11.56) * mm, v(-13.7, -11.57) * mm, v(-13.87, -11.56) * mm, v(-14.02, -11.53) * mm]});
            skFitSpline(sketch, "E3987", {"points": [v(-14.02, -11.53) * mm, v(-14.46, -11.47) * mm, v(-14.9, -11.4) * mm, v(-15.34, -11.33) * mm]});
            skFitSpline(sketch, "E3988", {"points": [v(-15.34, -11.33) * mm, v(-15.63, -11.28) * mm, v(-15.91, -11.25) * mm, v(-16.2, -11.2) * mm]});
            skFitSpline(sketch, "E3989", {"points": [v(-16.2, -11.2) * mm, v(-16.34, -11.18) * mm, v(-16.46, -11.1) * mm, v(-16.55, -10.97) * mm]});
            skFitSpline(sketch, "E3990", {"points": [v(-16.55, -10.97) * mm, v(-16.62, -10.86) * mm, v(-16.7, -10.75) * mm, v(-16.76, -10.63) * mm]});
            skFitSpline(sketch, "E3991", {"points": [v(-16.76, -10.63) * mm, v(-17.06, -10.14) * mm, v(-17.36, -9.65) * mm, v(-17.66, -9.16) * mm]});
            skFitSpline(sketch, "E3992", {"points": [v(-17.66, -9.16) * mm, v(-17.67, -9.13) * mm, v(-17.7, -9.1) * mm, v(-17.75, -9.04) * mm]});
            skFitSpline(sketch, "E3993", {"points": [v(-17.75, -9.04) * mm, v(-17.74, -9.15) * mm, v(-17.74, -9.2) * mm, v(-17.73, -9.26) * mm]});
            skFitSpline(sketch, "E3994", {"points": [v(-17.73, -9.26) * mm, v(-17.67, -9.57) * mm, v(-17.6, -9.89) * mm, v(-17.54, -10.2) * mm]});
            skFitSpline(sketch, "E3995", {"points": [v(-17.54, -10.2) * mm, v(-17.52, -10.28) * mm, v(-17.5, -10.37) * mm, v(-17.46, -10.45) * mm]});
            skFitSpline(sketch, "E3996", {"points": [v(-17.46, -10.45) * mm, v(-17.39, -10.6) * mm, v(-17.4, -10.74) * mm, v(-17.41, -10.9) * mm]});
            skFitSpline(sketch, "E3997", {"points": [v(-17.41, -10.9) * mm, v(-17.44, -11.1) * mm, v(-17.62, -11.25) * mm, v(-17.82, -11.27) * mm]});
            skFitSpline(sketch, "E3998", {"points": [v(-17.82, -11.27) * mm, v(-18.04, -11.3) * mm, v(-18.26, -11.18) * mm, v(-18.34, -10.97) * mm]});
            skFitSpline(sketch, "E3999", {"points": [v(-18.34, -10.97) * mm, v(-18.4, -10.8) * mm, v(-18.44, -10.61) * mm, v(-18.48, -10.44) * mm]});
            skFitSpline(sketch, "E4000", {"points": [v(-18.48, -10.44) * mm, v(-18.58, -9.94) * mm, v(-18.7, -9.44) * mm, v(-18.78, -8.93) * mm]});
            skFitSpline(sketch, "E4001", {"points": [v(-18.78, -8.93) * mm, v(-18.83, -8.6) * mm, v(-18.86, -8.25) * mm, v(-18.88, -7.91) * mm]});
            skFitSpline(sketch, "E4002", {"points": [v(-18.88, -7.91) * mm, v(-18.9, -7.77) * mm, v(-18.94, -7.67) * mm, v(-19.05, -7.6) * mm]});
            skFitSpline(sketch, "E4003", {"points": [v(-19.05, -7.6) * mm, v(-19.45, -7.33) * mm, v(-19.84, -7.07) * mm, v(-20.22, -6.8) * mm]});
            skFitSpline(sketch, "E4004", {"points": [v(-20.22, -6.8) * mm, v(-20.78, -6.4) * mm, v(-21.33, -5.98) * mm, v(-21.88, -5.58) * mm]});
            skFitSpline(sketch, "E4005", {"points": [v(-21.88, -5.58) * mm, v(-22.37, -5.22) * mm, v(-22.87, -4.86) * mm, v(-23.35, -4.5) * mm]});
            skFitSpline(sketch, "E4006", {"points": [v(-23.35, -4.5) * mm, v(-23.95, -4.05) * mm, v(-24.54, -3.58) * mm, v(-25.14, -3.13) * mm]});
            skFitSpline(sketch, "E4007", {"points": [v(-25.14, -3.13) * mm, v(-25.65, -2.74) * mm, v(-26.17, -2.36) * mm, v(-26.68, -1.98) * mm]});
            skFitSpline(sketch, "E4008", {"points": [v(-26.68, -1.98) * mm, v(-26.7, -1.98) * mm, v(-26.71, -1.98) * mm, v(-26.74, -1.97) * mm]});
            skFitSpline(sketch, "E4009", {"points": [v(-26.74, -1.97) * mm, v(-26.75, -2) * mm, v(-26.76, -2.03) * mm, v(-26.75, -2.05) * mm]});
            skFitSpline(sketch, "E4010", {"points": [v(-26.75, -2.05) * mm, v(-26.6, -2.55) * mm, v(-26.46, -3.06) * mm, v(-26.28, -3.56) * mm]});
            skFitSpline(sketch, "E4011", {"points": [v(-26.28, -3.56) * mm, v(-26.2, -3.75) * mm, v(-26.08, -3.95) * mm, v(-25.86, -4.06) * mm]});
            skFitSpline(sketch, "E4012", {"points": [v(-25.86, -4.06) * mm, v(-25.22, -4.39) * mm, v(-24.58, -4.73) * mm, v(-23.93, -5.07) * mm]});
            skFitSpline(sketch, "E4013", {"points": [v(-23.93, -5.07) * mm, v(-23.69, -5.2) * mm, v(-23.44, -5.33) * mm, v(-23.2, -5.47) * mm]});
            skFitSpline(sketch, "E4014", {"points": [v(-23.2, -5.47) * mm, v(-23.01, -5.57) * mm, v(-22.92, -5.73) * mm, v(-22.93, -5.94) * mm]});
            skFitSpline(sketch, "E4015", {"points": [v(-22.93, -5.94) * mm, v(-22.96, -6.28) * mm, v(-23.3, -6.49) * mm, v(-23.62, -6.34) * mm]});
            skFitSpline(sketch, "E4016", {"points": [v(-23.62, -6.34) * mm, v(-23.77, -6.27) * mm, v(-23.9, -6.18) * mm, v(-24.06, -6.1) * mm]});
            skFitSpline(sketch, "E4017", {"points": [v(-24.06, -6.1) * mm, v(-24.56, -5.84) * mm, v(-25.07, -5.58) * mm, v(-25.57, -5.33) * mm]});
            skFitSpline(sketch, "E4018", {"points": [v(-25.57, -5.33) * mm, v(-25.6, -5.31) * mm, v(-25.63, -5.3) * mm, v(-25.68, -5.3) * mm]});
            skFitSpline(sketch, "E4019", {"points": [v(-25.68, -5.3) * mm, v(-25.66, -5.35) * mm, v(-25.66, -5.4) * mm, v(-25.65, -5.43) * mm]});
            skFitSpline(sketch, "E4020", {"points": [v(-25.65, -5.43) * mm, v(-25.52, -5.8) * mm, v(-25.38, -6.16) * mm, v(-25.26, -6.53) * mm]});
            skFitSpline(sketch, "E4021", {"points": [v(-25.26, -6.53) * mm, v(-25.2, -6.68) * mm, v(-25.11, -6.77) * mm, v(-24.98, -6.84) * mm]});
            skFitSpline(sketch, "E4022", {"points": [v(-24.98, -6.84) * mm, v(-24.17, -7.28) * mm, v(-23.35, -7.72) * mm, v(-22.53, -8.16) * mm]});
            skFitSpline(sketch, "E4023", {"points": [v(-22.53, -8.16) * mm, v(-22.3, -8.28) * mm, v(-22.08, -8.4) * mm, v(-21.86, -8.52) * mm]});
            skFitSpline(sketch, "E4024", {"points": [v(-21.86, -8.52) * mm, v(-21.76, -8.57) * mm, v(-21.67, -8.64) * mm, v(-21.59, -8.72) * mm]});
            skFitSpline(sketch, "E4025", {"points": [v(-21.59, -8.72) * mm, v(-21.41, -8.9) * mm, v(-21.4, -9.16) * mm, v(-21.54, -9.35) * mm]});
            skFitSpline(sketch, "E4026", {"points": [v(-21.54, -9.35) * mm, v(-21.69, -9.55) * mm, v(-21.93, -9.6) * mm, v(-22.16, -9.48) * mm]});
            skFitSpline(sketch, "E4027", {"points": [v(-22.16, -9.48) * mm, v(-22.6, -9.23) * mm, v(-23.05, -8.99) * mm, v(-23.5, -8.74) * mm]});
            skFitSpline(sketch, "E4028", {"points": [v(-23.5, -8.74) * mm, v(-23.85, -8.55) * mm, v(-24.2, -8.37) * mm, v(-24.54, -8.18) * mm]});
            skFitSpline(sketch, "E4029", {"points": [v(-24.54, -8.18) * mm, v(-24.59, -8.15) * mm, v(-24.65, -8.13) * mm, v(-24.75, -8.09) * mm]});
            skSolve(sketch);
        }
        {
            var Q0;
            Q0=makeQuery(id+"F0.imprint","IMPRINT",FACE,{"disambiguationData":[TD([[makeQuery(id+"F0.imprint","IMPRINT",EDGE,{"derivedFrom":sQuery(id+"F0.wireOp",EDGE,"E2588")}),-1.0]])]});
            var Q1;
            Q1=makeQuery(id+"F0.imprint","IMPRINT",FACE,{"disambiguationData":[TD([[makeQuery(id+"F0.imprint","IMPRINT",EDGE,{"derivedFrom":sQuery(id+"F0.wireOp",EDGE,"E3280")}),-1.0]])]});
            var Q2;
            Q2=makeQuery(id+"F0.imprint","IMPRINT",FACE,{"disambiguationData":[TD([[makeQuery(id+"F0.imprint","IMPRINT",EDGE,{"derivedFrom":sQuery(id+"F0.wireOp",EDGE,"E585")}),-1.0]])]});
            var Q3;
            Q3=makeQuery(id+"F0.imprint","IMPRINT",FACE,{"disambiguationData":[TD([[makeQuery(id+"F0.imprint","IMPRINT",EDGE,{"derivedFrom":sQuery(id+"F0.wireOp",EDGE,"E1334")}),-1.0]])]});
            var Q4;
            Q4=makeQuery(id+"F0.imprint","IMPRINT",FACE,{"disambiguationData":[TD([[makeQuery(id+"F0.imprint","IMPRINT",EDGE,{"derivedFrom":sQuery(id+"F0.wireOp",EDGE,"E0")}),-1.0]])]});
            extrude(context, id + "F1", {"entities" : qUnion([Q0, Q1, Q2, Q3, Q4]), "depth" : 0.8 * mm});
        }
    });
